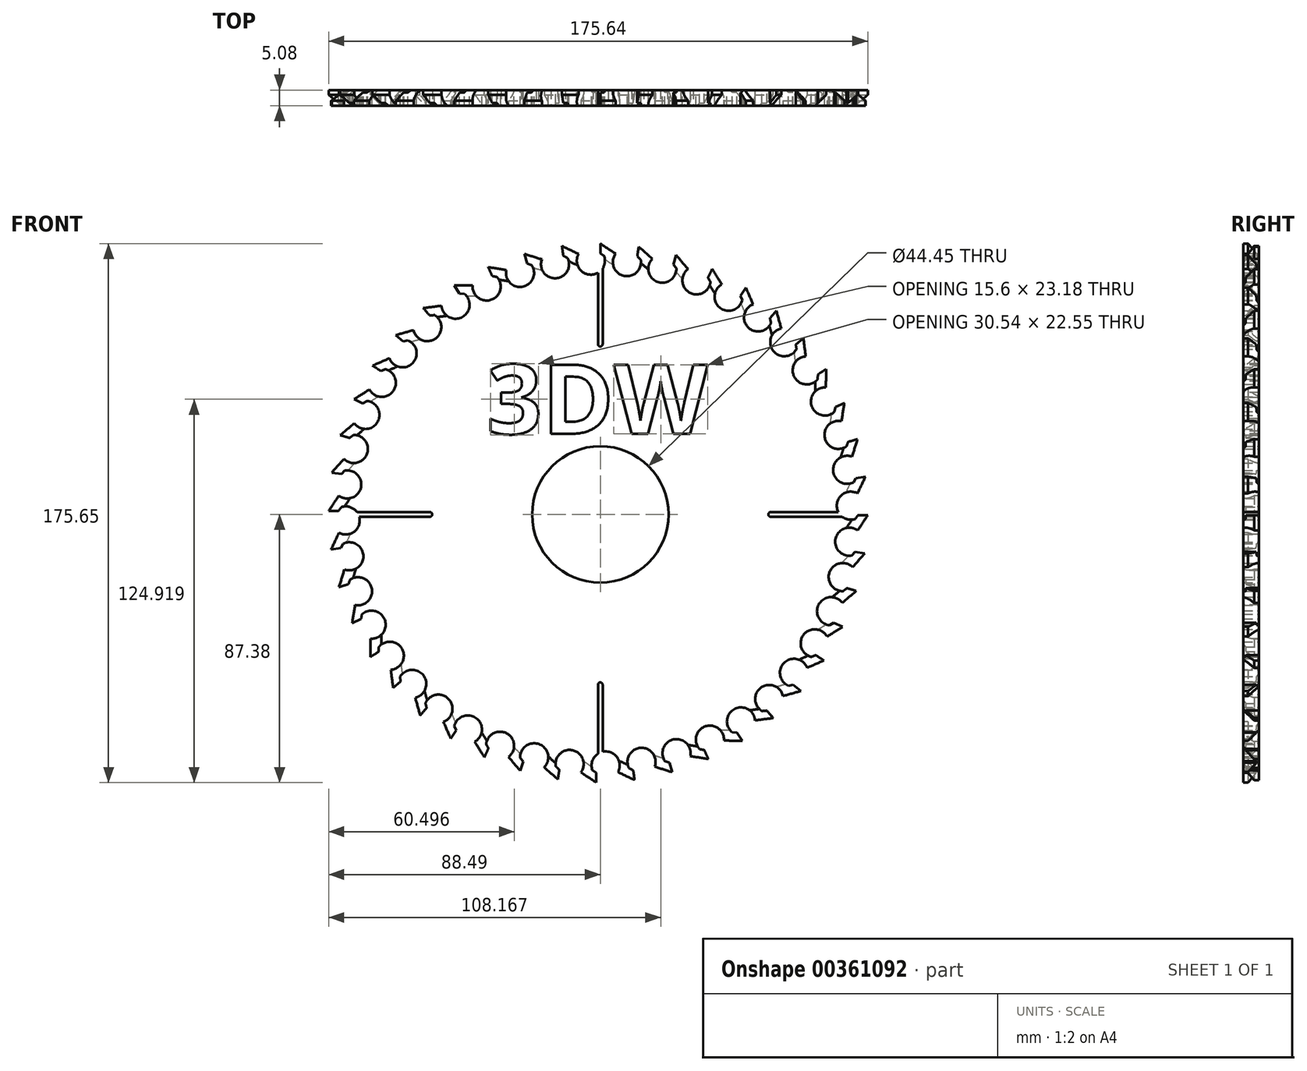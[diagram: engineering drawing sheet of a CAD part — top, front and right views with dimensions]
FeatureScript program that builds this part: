
annotation { "Feature Type Name" : "Feature", "Feature Type Description" : "" }
export const myFeature = defineFeature(function(context is Context, id is Id, definition is map)
    precondition{}
    {
        {
            var Q0;
            Q0=qCreatedBy(makeId("Front.planeOp"),FACE);
            var sketch = newSketch(context, id + "F0", { "sketchPlane" : qUnion([Q0])});
            skCircle(sketch, "E0", {"center": v(0, 0) * mm, "radius": 22.23 * mm});
            skLineSegment(sketch, "E1", {"start": v(0, 88.27) * mm, "end": v(0, 85.07) * mm});
            skLineSegment(sketch, "E2", {"start": v(0, 85.07) * mm, "end": v(1.27, 84.16) * mm});
            skLineSegment(sketch, "E3", {"start": v(1.27, 84.16) * mm, "end": v(1.27, 87.63) * mm});
            skLineSegment(sketch, "E4", {"start": v(1.27, 87.63) * mm, "end": v(0, 88.27) * mm});
            skLineSegment(sketch, "E5", {"start": v(1.27, 87.63) * mm, "end": v(5.07, 85.07) * mm});
            skLineSegment(sketch, "E6.1.0", {"start": v(-10.66, 83.58) * mm, "end": v(-11.15, 87.02) * mm});
            skLineSegment(sketch, "E6.1.1", {"start": v(-11.15, 87.02) * mm, "end": v(-7.03, 85.02) * mm});
            skLineSegment(sketch, "E6.1.2", {"start": v(-12.5, 87.47) * mm, "end": v(-12.05, 84.3) * mm});
            skLineSegment(sketch, "E6.1.3", {"start": v(-11.15, 87.02) * mm, "end": v(-12.5, 87.47) * mm});
            skLineSegment(sketch, "E6.1.4", {"start": v(-12.05, 84.3) * mm, "end": v(-10.66, 83.58) * mm});
            skLineSegment(sketch, "E6.2.0", {"start": v(-22.39, 81.31) * mm, "end": v(-23.37, 84.64) * mm});
            skLineSegment(sketch, "E6.2.1", {"start": v(-23.37, 84.64) * mm, "end": v(-19, 83.25) * mm});
            skLineSegment(sketch, "E6.2.2", {"start": v(-24.77, 84.9) * mm, "end": v(-23.87, 81.83) * mm});
            skLineSegment(sketch, "E6.2.3", {"start": v(-23.37, 84.64) * mm, "end": v(-24.77, 84.9) * mm});
            skLineSegment(sketch, "E6.2.4", {"start": v(-23.87, 81.83) * mm, "end": v(-22.39, 81.31) * mm});
            skLineSegment(sketch, "E6.3.0", {"start": v(-33.68, 77.4) * mm, "end": v(-35.12, 80.56) * mm});
            skLineSegment(sketch, "E6.3.1", {"start": v(-35.12, 80.56) * mm, "end": v(-30.6, 79.8) * mm});
            skLineSegment(sketch, "E6.3.2", {"start": v(-36.54, 80.6) * mm, "end": v(-35.21, 77.7) * mm});
            skLineSegment(sketch, "E6.3.3", {"start": v(-35.12, 80.56) * mm, "end": v(-36.54, 80.6) * mm});
            skLineSegment(sketch, "E6.3.4", {"start": v(-35.21, 77.7) * mm, "end": v(-33.68, 77.4) * mm});
            skLineSegment(sketch, "E6.4.0", {"start": v(-44.3, 71.92) * mm, "end": v(-46.17, 74.84) * mm});
            skLineSegment(sketch, "E6.4.1", {"start": v(-46.17, 74.84) * mm, "end": v(-41.6, 74.73) * mm});
            skLineSegment(sketch, "E6.4.2", {"start": v(-47.59, 74.69) * mm, "end": v(-45.86, 72) * mm});
            skLineSegment(sketch, "E6.4.3", {"start": v(-46.17, 74.84) * mm, "end": v(-47.59, 74.69) * mm});
            skLineSegment(sketch, "E6.4.4", {"start": v(-45.86, 72) * mm, "end": v(-44.3, 71.92) * mm});
            skLineSegment(sketch, "E6.5.0", {"start": v(-54.02, 64.98) * mm, "end": v(-56.3, 67.6) * mm});
            skLineSegment(sketch, "E6.5.1", {"start": v(-56.3, 67.6) * mm, "end": v(-51.75, 68.15) * mm});
            skLineSegment(sketch, "E6.5.2", {"start": v(-57.67, 67.25) * mm, "end": v(-55.58, 64.84) * mm});
            skLineSegment(sketch, "E6.5.3", {"start": v(-56.3, 67.6) * mm, "end": v(-57.67, 67.25) * mm});
            skLineSegment(sketch, "E6.5.4", {"start": v(-55.58, 64.84) * mm, "end": v(-54.02, 64.98) * mm});
            skLineSegment(sketch, "E6.6.0", {"start": v(-62.66, 56.73) * mm, "end": v(-65.29, 59) * mm});
            skLineSegment(sketch, "E6.6.1", {"start": v(-65.29, 59) * mm, "end": v(-60.87, 60.2) * mm});
            skLineSegment(sketch, "E6.6.2", {"start": v(-66.6, 58.46) * mm, "end": v(-64.18, 56.37) * mm});
            skLineSegment(sketch, "E6.6.3", {"start": v(-65.29, 59) * mm, "end": v(-66.6, 58.46) * mm});
            skLineSegment(sketch, "E6.6.4", {"start": v(-64.18, 56.37) * mm, "end": v(-62.66, 56.73) * mm});
            skLineSegment(sketch, "E6.7.0", {"start": v(-70.04, 47.34) * mm, "end": v(-72.96, 49.21) * mm});
            skLineSegment(sketch, "E6.7.1", {"start": v(-72.96, 49.21) * mm, "end": v(-68.76, 51.02) * mm});
            skLineSegment(sketch, "E6.7.2", {"start": v(-74.19, 48.49) * mm, "end": v(-71.5, 46.76) * mm});
            skLineSegment(sketch, "E6.7.3", {"start": v(-72.96, 49.21) * mm, "end": v(-74.19, 48.49) * mm});
            skLineSegment(sketch, "E6.7.4", {"start": v(-71.5, 46.76) * mm, "end": v(-70.04, 47.34) * mm});
            skLineSegment(sketch, "E6.8.0", {"start": v(-76.01, 36.99) * mm, "end": v(-79.17, 38.43) * mm});
            skLineSegment(sketch, "E6.8.1", {"start": v(-79.17, 38.43) * mm, "end": v(-75.26, 40.82) * mm});
            skLineSegment(sketch, "E6.8.2", {"start": v(-80.28, 37.54) * mm, "end": v(-77.37, 36.2) * mm});
            skLineSegment(sketch, "E6.8.3", {"start": v(-79.17, 38.43) * mm, "end": v(-80.28, 37.54) * mm});
            skLineSegment(sketch, "E6.8.4", {"start": v(-77.37, 36.2) * mm, "end": v(-76.01, 36.99) * mm});
            skLineSegment(sketch, "E6.9.0", {"start": v(-80.45, 25.9) * mm, "end": v(-83.77, 26.87) * mm});
            skLineSegment(sketch, "E6.9.1", {"start": v(-83.77, 26.87) * mm, "end": v(-80.25, 29.79) * mm});
            skLineSegment(sketch, "E6.9.2", {"start": v(-84.75, 25.83) * mm, "end": v(-81.68, 24.93) * mm});
            skLineSegment(sketch, "E6.9.3", {"start": v(-83.77, 26.87) * mm, "end": v(-84.75, 25.83) * mm});
            skLineSegment(sketch, "E6.9.4", {"start": v(-81.68, 24.93) * mm, "end": v(-80.45, 25.9) * mm});
            skLineSegment(sketch, "E6.10.0", {"start": v(-83.26, 14.28) * mm, "end": v(-86.69, 14.77) * mm});
            skLineSegment(sketch, "E6.10.1", {"start": v(-86.69, 14.77) * mm, "end": v(-83.61, 18.17) * mm});
            skLineSegment(sketch, "E6.10.2", {"start": v(-87.5, 13.6) * mm, "end": v(-84.34, 13.15) * mm});
            skLineSegment(sketch, "E6.10.3", {"start": v(-86.69, 14.77) * mm, "end": v(-87.5, 13.6) * mm});
            skLineSegment(sketch, "E6.10.4", {"start": v(-84.34, 13.15) * mm, "end": v(-83.26, 14.28) * mm});
            skLineSegment(sketch, "E6.11.0", {"start": v(-84.38, 2.39) * mm, "end": v(-87.85, 2.39) * mm});
            skLineSegment(sketch, "E6.11.1", {"start": v(-87.85, 2.39) * mm, "end": v(-85.3, 6.18) * mm});
            skLineSegment(sketch, "E6.11.2", {"start": v(-88.5, 1.11) * mm, "end": v(-85.3, 1.11) * mm});
            skLineSegment(sketch, "E6.11.3", {"start": v(-87.85, 2.39) * mm, "end": v(-88.5, 1.11) * mm});
            skLineSegment(sketch, "E6.11.4", {"start": v(-85.3, 1.11) * mm, "end": v(-84.38, 2.39) * mm});
            skLineSegment(sketch, "E6.12.0", {"start": v(-83.8, -9.55) * mm, "end": v(-87.24, -10.04) * mm});
            skLineSegment(sketch, "E6.12.1", {"start": v(-87.24, -10.04) * mm, "end": v(-85.25, -5.92) * mm});
            skLineSegment(sketch, "E6.12.2", {"start": v(-87.7, -11.4) * mm, "end": v(-84.53, -10.94) * mm});
            skLineSegment(sketch, "E6.12.3", {"start": v(-87.24, -10.04) * mm, "end": v(-87.7, -11.4) * mm});
            skLineSegment(sketch, "E6.12.4", {"start": v(-84.53, -10.94) * mm, "end": v(-83.8, -9.55) * mm});
            skLineSegment(sketch, "E6.13.0", {"start": v(-81.54, -21.28) * mm, "end": v(-84.87, -22.25) * mm});
            skLineSegment(sketch, "E6.13.1", {"start": v(-84.87, -22.25) * mm, "end": v(-83.48, -17.9) * mm});
            skLineSegment(sketch, "E6.13.2", {"start": v(-85.12, -23.66) * mm, "end": v(-82.05, -22.75) * mm});
            skLineSegment(sketch, "E6.13.3", {"start": v(-84.87, -22.25) * mm, "end": v(-85.12, -23.66) * mm});
            skLineSegment(sketch, "E6.13.4", {"start": v(-82.05, -22.75) * mm, "end": v(-81.54, -21.28) * mm});
            skLineSegment(sketch, "E6.14.0", {"start": v(-77.63, -32.56) * mm, "end": v(-80.78, -34) * mm});
            skLineSegment(sketch, "E6.14.1", {"start": v(-80.78, -34) * mm, "end": v(-80.03, -29.5) * mm});
            skLineSegment(sketch, "E6.14.2", {"start": v(-80.83, -35.43) * mm, "end": v(-77.92, -34.1) * mm});
            skLineSegment(sketch, "E6.14.3", {"start": v(-80.78, -34) * mm, "end": v(-80.83, -35.43) * mm});
            skLineSegment(sketch, "E6.14.4", {"start": v(-77.92, -34.1) * mm, "end": v(-77.63, -32.56) * mm});
            skLineSegment(sketch, "E6.15.0", {"start": v(-72.15, -43.18) * mm, "end": v(-75.06, -45.06) * mm});
            skLineSegment(sketch, "E6.15.1", {"start": v(-75.06, -45.06) * mm, "end": v(-74.96, -40.48) * mm});
            skLineSegment(sketch, "E6.15.2", {"start": v(-74.91, -46.47) * mm, "end": v(-72.22, -44.74) * mm});
            skLineSegment(sketch, "E6.15.3", {"start": v(-75.06, -45.06) * mm, "end": v(-74.91, -46.47) * mm});
            skLineSegment(sketch, "E6.15.4", {"start": v(-72.22, -44.74) * mm, "end": v(-72.15, -43.18) * mm});
            skLineSegment(sketch, "E6.16.0", {"start": v(-65.21, -52.9) * mm, "end": v(-67.83, -55.18) * mm});
            skLineSegment(sketch, "E6.16.1", {"start": v(-67.83, -55.18) * mm, "end": v(-68.38, -50.64) * mm});
            skLineSegment(sketch, "E6.16.2", {"start": v(-67.48, -56.56) * mm, "end": v(-65.06, -54.47) * mm});
            skLineSegment(sketch, "E6.16.3", {"start": v(-67.83, -55.18) * mm, "end": v(-67.48, -56.56) * mm});
            skLineSegment(sketch, "E6.16.4", {"start": v(-65.06, -54.47) * mm, "end": v(-65.21, -52.9) * mm});
            skLineSegment(sketch, "E6.17.0", {"start": v(-56.96, -61.55) * mm, "end": v(-59.23, -64.17) * mm});
            skLineSegment(sketch, "E6.17.1", {"start": v(-59.23, -64.17) * mm, "end": v(-60.42, -59.75) * mm});
            skLineSegment(sketch, "E6.17.2", {"start": v(-58.69, -65.49) * mm, "end": v(-56.6, -63.07) * mm});
            skLineSegment(sketch, "E6.17.3", {"start": v(-59.23, -64.17) * mm, "end": v(-58.69, -65.49) * mm});
            skLineSegment(sketch, "E6.17.4", {"start": v(-56.6, -63.07) * mm, "end": v(-56.96, -61.55) * mm});
            skLineSegment(sketch, "E6.18.0", {"start": v(-47.56, -68.93) * mm, "end": v(-49.44, -71.85) * mm});
            skLineSegment(sketch, "E6.18.1", {"start": v(-49.44, -71.85) * mm, "end": v(-51.25, -67.64) * mm});
            skLineSegment(sketch, "E6.18.2", {"start": v(-48.71, -73.07) * mm, "end": v(-46.98, -70.38) * mm});
            skLineSegment(sketch, "E6.18.3", {"start": v(-49.44, -71.85) * mm, "end": v(-48.71, -73.07) * mm});
            skLineSegment(sketch, "E6.18.4", {"start": v(-46.98, -70.38) * mm, "end": v(-47.56, -68.93) * mm});
            skLineSegment(sketch, "E6.19.0", {"start": v(-37.21, -74.9) * mm, "end": v(-38.66, -78.05) * mm});
            skLineSegment(sketch, "E6.19.1", {"start": v(-38.66, -78.05) * mm, "end": v(-41.04, -74.15) * mm});
            skLineSegment(sketch, "E6.19.2", {"start": v(-37.76, -79.16) * mm, "end": v(-36.43, -76.25) * mm});
            skLineSegment(sketch, "E6.19.3", {"start": v(-38.66, -78.05) * mm, "end": v(-37.76, -79.16) * mm});
            skLineSegment(sketch, "E6.19.4", {"start": v(-36.43, -76.25) * mm, "end": v(-37.21, -74.9) * mm});
            skLineSegment(sketch, "E6.20.0", {"start": v(-26.12, -79.33) * mm, "end": v(-27.1, -82.66) * mm});
            skLineSegment(sketch, "E6.20.1", {"start": v(-27.1, -82.66) * mm, "end": v(-30.02, -79.14) * mm});
            skLineSegment(sketch, "E6.20.2", {"start": v(-26.05, -83.63) * mm, "end": v(-25.15, -80.56) * mm});
            skLineSegment(sketch, "E6.20.3", {"start": v(-27.1, -82.66) * mm, "end": v(-26.05, -83.63) * mm});
            skLineSegment(sketch, "E6.20.4", {"start": v(-25.15, -80.56) * mm, "end": v(-26.12, -79.33) * mm});
            skLineSegment(sketch, "E6.21.0", {"start": v(-14.5, -82.14) * mm, "end": v(-15, -85.58) * mm});
            skLineSegment(sketch, "E6.21.1", {"start": v(-15, -85.58) * mm, "end": v(-18.4, -82.5) * mm});
            skLineSegment(sketch, "E6.21.2", {"start": v(-13.83, -86.39) * mm, "end": v(-13.38, -83.22) * mm});
            skLineSegment(sketch, "E6.21.3", {"start": v(-15, -85.58) * mm, "end": v(-13.83, -86.39) * mm});
            skLineSegment(sketch, "E6.21.4", {"start": v(-13.38, -83.22) * mm, "end": v(-14.5, -82.14) * mm});
            skLineSegment(sketch, "E6.22.0", {"start": v(-2.61, -83.27) * mm, "end": v(-2.61, -86.74) * mm});
            skLineSegment(sketch, "E6.22.1", {"start": v(-2.61, -86.74) * mm, "end": v(-6.4, -84.18) * mm});
            skLineSegment(sketch, "E6.22.2", {"start": v(-1.34, -87.38) * mm, "end": v(-1.34, -84.18) * mm});
            skLineSegment(sketch, "E6.22.3", {"start": v(-2.61, -86.74) * mm, "end": v(-1.34, -87.38) * mm});
            skLineSegment(sketch, "E6.22.4", {"start": v(-1.34, -84.18) * mm, "end": v(-2.61, -83.27) * mm});
            skLineSegment(sketch, "E6.23.0", {"start": v(9.32, -82.7) * mm, "end": v(9.81, -86.13) * mm});
            skLineSegment(sketch, "E6.23.1", {"start": v(9.81, -86.13) * mm, "end": v(5.7, -84.13) * mm});
            skLineSegment(sketch, "E6.23.2", {"start": v(11.17, -86.58) * mm, "end": v(10.71, -83.41) * mm});
            skLineSegment(sketch, "E6.23.3", {"start": v(9.81, -86.13) * mm, "end": v(11.17, -86.58) * mm});
            skLineSegment(sketch, "E6.23.4", {"start": v(10.71, -83.41) * mm, "end": v(9.32, -82.7) * mm});
            skLineSegment(sketch, "E6.24.0", {"start": v(21.05, -80.43) * mm, "end": v(22.03, -83.76) * mm});
            skLineSegment(sketch, "E6.24.1", {"start": v(22.03, -83.76) * mm, "end": v(17.67, -82.37) * mm});
            skLineSegment(sketch, "E6.24.2", {"start": v(23.43, -84) * mm, "end": v(22.53, -80.94) * mm});
            skLineSegment(sketch, "E6.24.3", {"start": v(22.03, -83.76) * mm, "end": v(23.43, -84) * mm});
            skLineSegment(sketch, "E6.24.4", {"start": v(22.53, -80.94) * mm, "end": v(21.05, -80.43) * mm});
            skLineSegment(sketch, "E6.25.0", {"start": v(32.34, -76.51) * mm, "end": v(33.78, -79.67) * mm});
            skLineSegment(sketch, "E6.25.1", {"start": v(33.78, -79.67) * mm, "end": v(29.26, -78.92) * mm});
            skLineSegment(sketch, "E6.25.2", {"start": v(35.2, -79.72) * mm, "end": v(33.87, -76.81) * mm});
            skLineSegment(sketch, "E6.25.3", {"start": v(33.78, -79.67) * mm, "end": v(35.2, -79.72) * mm});
            skLineSegment(sketch, "E6.25.4", {"start": v(33.87, -76.81) * mm, "end": v(32.34, -76.51) * mm});
            skLineSegment(sketch, "E6.26.0", {"start": v(42.95, -71.03) * mm, "end": v(44.83, -73.95) * mm});
            skLineSegment(sketch, "E6.26.1", {"start": v(44.83, -73.95) * mm, "end": v(40.25, -73.85) * mm});
            skLineSegment(sketch, "E6.26.2", {"start": v(46.25, -73.8) * mm, "end": v(44.52, -71.1) * mm});
            skLineSegment(sketch, "E6.26.3", {"start": v(44.83, -73.95) * mm, "end": v(46.25, -73.8) * mm});
            skLineSegment(sketch, "E6.26.4", {"start": v(44.52, -71.1) * mm, "end": v(42.95, -71.03) * mm});
            skLineSegment(sketch, "E6.27.0", {"start": v(52.68, -64.1) * mm, "end": v(54.95, -66.72) * mm});
            skLineSegment(sketch, "E6.27.1", {"start": v(54.95, -66.72) * mm, "end": v(50.41, -67.27) * mm});
            skLineSegment(sketch, "E6.27.2", {"start": v(56.33, -66.37) * mm, "end": v(54.24, -63.95) * mm});
            skLineSegment(sketch, "E6.27.3", {"start": v(54.95, -66.72) * mm, "end": v(56.33, -66.37) * mm});
            skLineSegment(sketch, "E6.27.4", {"start": v(54.24, -63.95) * mm, "end": v(52.68, -64.1) * mm});
            skLineSegment(sketch, "E6.28.0", {"start": v(61.32, -55.85) * mm, "end": v(63.95, -58.12) * mm});
            skLineSegment(sketch, "E6.28.1", {"start": v(63.95, -58.12) * mm, "end": v(59.53, -59.3) * mm});
            skLineSegment(sketch, "E6.28.2", {"start": v(65.26, -57.57) * mm, "end": v(62.85, -55.48) * mm});
            skLineSegment(sketch, "E6.28.3", {"start": v(63.95, -58.12) * mm, "end": v(65.26, -57.57) * mm});
            skLineSegment(sketch, "E6.28.4", {"start": v(62.85, -55.48) * mm, "end": v(61.32, -55.85) * mm});
            skLineSegment(sketch, "E6.29.0", {"start": v(68.7, -46.45) * mm, "end": v(71.62, -48.33) * mm});
            skLineSegment(sketch, "E6.29.1", {"start": v(71.62, -48.33) * mm, "end": v(67.42, -50.13) * mm});
            skLineSegment(sketch, "E6.29.2", {"start": v(72.85, -47.6) * mm, "end": v(70.16, -45.87) * mm});
            skLineSegment(sketch, "E6.29.3", {"start": v(71.62, -48.33) * mm, "end": v(72.85, -47.6) * mm});
            skLineSegment(sketch, "E6.29.4", {"start": v(70.16, -45.87) * mm, "end": v(68.7, -46.45) * mm});
            skLineSegment(sketch, "E6.30.0", {"start": v(74.67, -36.1) * mm, "end": v(77.83, -37.54) * mm});
            skLineSegment(sketch, "E6.30.1", {"start": v(77.83, -37.54) * mm, "end": v(73.92, -39.93) * mm});
            skLineSegment(sketch, "E6.30.2", {"start": v(78.94, -36.65) * mm, "end": v(76.03, -35.32) * mm});
            skLineSegment(sketch, "E6.30.3", {"start": v(77.83, -37.54) * mm, "end": v(78.94, -36.65) * mm});
            skLineSegment(sketch, "E6.30.4", {"start": v(76.03, -35.32) * mm, "end": v(74.67, -36.1) * mm});
            skLineSegment(sketch, "E6.31.0", {"start": v(79.1, -25) * mm, "end": v(82.43, -25.98) * mm});
            skLineSegment(sketch, "E6.31.1", {"start": v(82.43, -25.98) * mm, "end": v(78.9, -28.9) * mm});
            skLineSegment(sketch, "E6.31.2", {"start": v(83.4, -24.94) * mm, "end": v(80.34, -24.04) * mm});
            skLineSegment(sketch, "E6.31.3", {"start": v(82.43, -25.98) * mm, "end": v(83.4, -24.94) * mm});
            skLineSegment(sketch, "E6.31.4", {"start": v(80.34, -24.04) * mm, "end": v(79.1, -25) * mm});
            skLineSegment(sketch, "E6.32.0", {"start": v(81.92, -13.4) * mm, "end": v(85.35, -13.89) * mm});
            skLineSegment(sketch, "E6.32.1", {"start": v(85.35, -13.89) * mm, "end": v(82.28, -17.28) * mm});
            skLineSegment(sketch, "E6.32.2", {"start": v(86.16, -12.72) * mm, "end": v(83, -12.26) * mm});
            skLineSegment(sketch, "E6.32.3", {"start": v(85.35, -13.89) * mm, "end": v(86.16, -12.72) * mm});
            skLineSegment(sketch, "E6.32.4", {"start": v(83, -12.26) * mm, "end": v(81.92, -13.4) * mm});
            skLineSegment(sketch, "E6.33.0", {"start": v(83.04, -1.5) * mm, "end": v(86.51, -1.5) * mm});
            skLineSegment(sketch, "E6.33.1", {"start": v(86.51, -1.5) * mm, "end": v(83.95, -5.3) * mm});
            skLineSegment(sketch, "E6.33.2", {"start": v(87.15, -0.23) * mm, "end": v(83.95, -0.23) * mm});
            skLineSegment(sketch, "E6.33.3", {"start": v(86.51, -1.5) * mm, "end": v(87.15, -0.23) * mm});
            skLineSegment(sketch, "E6.33.4", {"start": v(83.95, -0.23) * mm, "end": v(83.04, -1.5) * mm});
            skLineSegment(sketch, "E6.34.0", {"start": v(82.47, 10.43) * mm, "end": v(85.9, 10.93) * mm});
            skLineSegment(sketch, "E6.34.1", {"start": v(85.9, 10.93) * mm, "end": v(83.9, 6.8) * mm});
            skLineSegment(sketch, "E6.34.2", {"start": v(86.35, 12.28) * mm, "end": v(83.19, 11.82) * mm});
            skLineSegment(sketch, "E6.34.3", {"start": v(85.9, 10.93) * mm, "end": v(86.35, 12.28) * mm});
            skLineSegment(sketch, "E6.34.4", {"start": v(83.19, 11.82) * mm, "end": v(82.47, 10.43) * mm});
            skLineSegment(sketch, "E6.35.0", {"start": v(80.2, 22.16) * mm, "end": v(83.53, 23.14) * mm});
            skLineSegment(sketch, "E6.35.1", {"start": v(83.53, 23.14) * mm, "end": v(82.14, 18.78) * mm});
            skLineSegment(sketch, "E6.35.2", {"start": v(83.78, 24.54) * mm, "end": v(80.71, 23.64) * mm});
            skLineSegment(sketch, "E6.35.3", {"start": v(83.53, 23.14) * mm, "end": v(83.78, 24.54) * mm});
            skLineSegment(sketch, "E6.35.4", {"start": v(80.71, 23.64) * mm, "end": v(80.2, 22.16) * mm});
            skLineSegment(sketch, "E6.36.0", {"start": v(76.29, 33.45) * mm, "end": v(79.44, 34.9) * mm});
            skLineSegment(sketch, "E6.36.1", {"start": v(79.44, 34.9) * mm, "end": v(78.69, 30.38) * mm});
            skLineSegment(sketch, "E6.36.2", {"start": v(79.5, 36.32) * mm, "end": v(76.58, 34.99) * mm});
            skLineSegment(sketch, "E6.36.3", {"start": v(79.44, 34.9) * mm, "end": v(79.5, 36.32) * mm});
            skLineSegment(sketch, "E6.36.4", {"start": v(76.58, 34.99) * mm, "end": v(76.29, 33.45) * mm});
            skLineSegment(sketch, "E6.37.0", {"start": v(70.8, 44.07) * mm, "end": v(73.72, 45.94) * mm});
            skLineSegment(sketch, "E6.37.1", {"start": v(73.72, 45.94) * mm, "end": v(73.62, 41.37) * mm});
            skLineSegment(sketch, "E6.37.2", {"start": v(73.57, 47.36) * mm, "end": v(70.88, 45.63) * mm});
            skLineSegment(sketch, "E6.37.3", {"start": v(73.72, 45.94) * mm, "end": v(73.57, 47.36) * mm});
            skLineSegment(sketch, "E6.37.4", {"start": v(70.88, 45.63) * mm, "end": v(70.8, 44.07) * mm});
            skLineSegment(sketch, "E6.38.0", {"start": v(63.87, 53.8) * mm, "end": v(66.5, 56.07) * mm});
            skLineSegment(sketch, "E6.38.1", {"start": v(66.5, 56.07) * mm, "end": v(67.04, 51.52) * mm});
            skLineSegment(sketch, "E6.38.2", {"start": v(66.14, 57.45) * mm, "end": v(63.72, 55.35) * mm});
            skLineSegment(sketch, "E6.38.3", {"start": v(66.5, 56.07) * mm, "end": v(66.14, 57.45) * mm});
            skLineSegment(sketch, "E6.38.4", {"start": v(63.72, 55.35) * mm, "end": v(63.87, 53.8) * mm});
            skLineSegment(sketch, "E6.39.0", {"start": v(55.62, 62.44) * mm, "end": v(57.9, 65.06) * mm});
            skLineSegment(sketch, "E6.39.1", {"start": v(57.9, 65.06) * mm, "end": v(59.08, 60.64) * mm});
            skLineSegment(sketch, "E6.39.2", {"start": v(57.35, 66.38) * mm, "end": v(55.25, 63.96) * mm});
            skLineSegment(sketch, "E6.39.3", {"start": v(57.9, 65.06) * mm, "end": v(57.35, 66.38) * mm});
            skLineSegment(sketch, "E6.39.4", {"start": v(55.25, 63.96) * mm, "end": v(55.62, 62.44) * mm});
            skLineSegment(sketch, "E6.40.0", {"start": v(46.22, 69.82) * mm, "end": v(48.1, 72.74) * mm});
            skLineSegment(sketch, "E6.40.1", {"start": v(48.1, 72.74) * mm, "end": v(49.9, 68.53) * mm});
            skLineSegment(sketch, "E6.40.2", {"start": v(47.37, 73.96) * mm, "end": v(45.64, 71.27) * mm});
            skLineSegment(sketch, "E6.40.3", {"start": v(48.1, 72.74) * mm, "end": v(47.37, 73.96) * mm});
            skLineSegment(sketch, "E6.40.4", {"start": v(45.64, 71.27) * mm, "end": v(46.22, 69.82) * mm});
            skLineSegment(sketch, "E6.41.0", {"start": v(35.87, 75.79) * mm, "end": v(37.32, 78.94) * mm});
            skLineSegment(sketch, "E6.41.1", {"start": v(37.32, 78.94) * mm, "end": v(39.7, 75.04) * mm});
            skLineSegment(sketch, "E6.41.2", {"start": v(36.42, 80.05) * mm, "end": v(35.1, 77.14) * mm});
            skLineSegment(sketch, "E6.41.3", {"start": v(37.32, 78.94) * mm, "end": v(36.42, 80.05) * mm});
            skLineSegment(sketch, "E6.41.4", {"start": v(35.1, 77.14) * mm, "end": v(35.87, 75.79) * mm});
            skLineSegment(sketch, "E6.42.0", {"start": v(24.78, 80.22) * mm, "end": v(25.76, 83.55) * mm});
            skLineSegment(sketch, "E6.42.1", {"start": v(25.76, 83.55) * mm, "end": v(28.68, 80.02) * mm});
            skLineSegment(sketch, "E6.42.2", {"start": v(24.72, 84.52) * mm, "end": v(23.81, 81.45) * mm});
            skLineSegment(sketch, "E6.42.3", {"start": v(25.76, 83.55) * mm, "end": v(24.72, 84.52) * mm});
            skLineSegment(sketch, "E6.42.4", {"start": v(23.81, 81.45) * mm, "end": v(24.78, 80.22) * mm});
            skLineSegment(sketch, "E6.43.0", {"start": v(13.17, 83.03) * mm, "end": v(13.66, 86.46) * mm});
            skLineSegment(sketch, "E6.43.1", {"start": v(13.66, 86.46) * mm, "end": v(17.05, 83.39) * mm});
            skLineSegment(sketch, "E6.43.2", {"start": v(12.5, 87.28) * mm, "end": v(12.04, 84.1) * mm});
            skLineSegment(sketch, "E6.43.3", {"start": v(13.66, 86.46) * mm, "end": v(12.5, 87.28) * mm});
            skLineSegment(sketch, "E6.43.4", {"start": v(12.04, 84.1) * mm, "end": v(13.17, 83.03) * mm});
            skPoint(sketch, "E6.center", {"position": v(-0.67, 0.44) * mm});
            skArc(sketch, "E7", {"start": v(5.07, 85.07) * mm, "mid": v(7.54, 77.79) * mm, "end": v(13.17, 83.03) * mm});
            skArc(sketch, "E8.1.0", {"start": v(-7.03, 85.02) * mm, "mid": v(-3.55, 78.17) * mm, "end": v(1.27, 84.16) * mm});
            skArc(sketch, "E8.2.0", {"start": v(-19, 83.25) * mm, "mid": v(-14.58, 76.97) * mm, "end": v(-10.66, 83.58) * mm});
            skArc(sketch, "E8.3.0", {"start": v(-30.6, 79.8) * mm, "mid": v(-25.33, 74.21) * mm, "end": v(-22.39, 81.31) * mm});
            skArc(sketch, "E8.4.0", {"start": v(-41.6, 74.73) * mm, "mid": v(-35.58, 69.95) * mm, "end": v(-33.68, 77.4) * mm});
            skArc(sketch, "E8.5.0", {"start": v(-51.75, 68.15) * mm, "mid": v(-45.11, 64.28) * mm, "end": v(-44.3, 71.92) * mm});
            skArc(sketch, "E8.6.0", {"start": v(-60.87, 60.2) * mm, "mid": v(-53.74, 57.3) * mm, "end": v(-54.02, 64.98) * mm});
            skArc(sketch, "E8.7.0", {"start": v(-68.76, 51.02) * mm, "mid": v(-61.3, 49.17) * mm, "end": v(-62.66, 56.73) * mm});
            skArc(sketch, "E8.8.0", {"start": v(-75.26, 40.82) * mm, "mid": v(-67.61, 40.04) * mm, "end": v(-70.04, 47.34) * mm});
            skArc(sketch, "E8.9.0", {"start": v(-80.25, 29.79) * mm, "mid": v(-72.57, 30.11) * mm, "end": v(-76.01, 36.99) * mm});
            skArc(sketch, "E8.10.0", {"start": v(-83.61, 18.17) * mm, "mid": v(-76.06, 19.58) * mm, "end": v(-80.45, 25.9) * mm});
            skArc(sketch, "E8.11.0", {"start": v(-85.3, 6.18) * mm, "mid": v(-78.02, 8.66) * mm, "end": v(-83.26, 14.28) * mm});
            skArc(sketch, "E8.12.0", {"start": v(-85.25, -5.92) * mm, "mid": v(-78.4, -2.43) * mm, "end": v(-84.38, 2.39) * mm});
            skArc(sketch, "E8.13.0", {"start": v(-83.48, -17.9) * mm, "mid": v(-77.2, -13.47) * mm, "end": v(-83.8, -9.55) * mm});
            skArc(sketch, "E8.14.0", {"start": v(-80.03, -29.5) * mm, "mid": v(-74.44, -24.22) * mm, "end": v(-81.54, -21.28) * mm});
            skArc(sketch, "E8.15.0", {"start": v(-74.96, -40.48) * mm, "mid": v(-70.18, -34.46) * mm, "end": v(-77.63, -32.56) * mm});
            skArc(sketch, "E8.16.0", {"start": v(-68.38, -50.64) * mm, "mid": v(-64.5, -44) * mm, "end": v(-72.15, -43.18) * mm});
            skArc(sketch, "E8.17.0", {"start": v(-60.42, -59.75) * mm, "mid": v(-57.53, -52.63) * mm, "end": v(-65.21, -52.9) * mm});
            skArc(sketch, "E8.18.0", {"start": v(-51.25, -67.64) * mm, "mid": v(-49.4, -60.18) * mm, "end": v(-56.96, -61.55) * mm});
            skArc(sketch, "E8.19.0", {"start": v(-41.04, -74.15) * mm, "mid": v(-40.27, -66.5) * mm, "end": v(-47.56, -68.93) * mm});
            skArc(sketch, "E8.20.0", {"start": v(-30.02, -79.14) * mm, "mid": v(-30.34, -71.45) * mm, "end": v(-37.21, -74.9) * mm});
            skArc(sketch, "E8.21.0", {"start": v(-18.4, -82.5) * mm, "mid": v(-19.8, -74.95) * mm, "end": v(-26.12, -79.33) * mm});
            skArc(sketch, "E8.22.0", {"start": v(-6.4, -84.18) * mm, "mid": v(-8.88, -76.9) * mm, "end": v(-14.5, -82.14) * mm});
            skArc(sketch, "E8.23.0", {"start": v(5.7, -84.13) * mm, "mid": v(2.2, -77.28) * mm, "end": v(-2.61, -83.27) * mm});
            skArc(sketch, "E8.24.0", {"start": v(17.67, -82.37) * mm, "mid": v(13.24, -76.08) * mm, "end": v(9.32, -82.7) * mm});
            skArc(sketch, "E8.25.0", {"start": v(29.26, -78.92) * mm, "mid": v(23.99, -73.32) * mm, "end": v(21.05, -80.43) * mm});
            skArc(sketch, "E8.26.0", {"start": v(40.25, -73.85) * mm, "mid": v(34.24, -69.06) * mm, "end": v(32.34, -76.51) * mm});
            skArc(sketch, "E8.27.0", {"start": v(50.41, -67.27) * mm, "mid": v(43.77, -63.39) * mm, "end": v(42.95, -71.03) * mm});
            skArc(sketch, "E8.28.0", {"start": v(59.53, -59.3) * mm, "mid": v(52.4, -56.41) * mm, "end": v(52.68, -64.1) * mm});
            skArc(sketch, "E8.29.0", {"start": v(67.42, -50.13) * mm, "mid": v(59.96, -48.28) * mm, "end": v(61.32, -55.85) * mm});
            skArc(sketch, "E8.30.0", {"start": v(73.92, -39.93) * mm, "mid": v(66.27, -39.16) * mm, "end": v(68.7, -46.45) * mm});
            skArc(sketch, "E8.31.0", {"start": v(78.9, -28.9) * mm, "mid": v(71.23, -29.23) * mm, "end": v(74.67, -36.1) * mm});
            skArc(sketch, "E8.32.0", {"start": v(82.28, -17.28) * mm, "mid": v(74.72, -18.7) * mm, "end": v(79.1, -25) * mm});
            skArc(sketch, "E8.33.0", {"start": v(83.95, -5.3) * mm, "mid": v(76.68, -7.77) * mm, "end": v(81.92, -13.4) * mm});
            skArc(sketch, "E8.34.0", {"start": v(83.9, 6.8) * mm, "mid": v(77.06, 3.32) * mm, "end": v(83.04, -1.5) * mm});
            skArc(sketch, "E8.35.0", {"start": v(82.14, 18.78) * mm, "mid": v(75.86, 14.35) * mm, "end": v(82.47, 10.43) * mm});
            skArc(sketch, "E8.36.0", {"start": v(78.69, 30.38) * mm, "mid": v(73.1, 25.1) * mm, "end": v(80.2, 22.16) * mm});
            skArc(sketch, "E8.37.0", {"start": v(73.62, 41.37) * mm, "mid": v(68.84, 35.35) * mm, "end": v(76.29, 33.45) * mm});
            skArc(sketch, "E8.38.0", {"start": v(67.04, 51.52) * mm, "mid": v(63.16, 44.89) * mm, "end": v(70.8, 44.07) * mm});
            skArc(sketch, "E8.39.0", {"start": v(59.08, 60.64) * mm, "mid": v(56.19, 53.52) * mm, "end": v(63.87, 53.8) * mm});
            skArc(sketch, "E8.40.0", {"start": v(49.9, 68.53) * mm, "mid": v(48.06, 61.07) * mm, "end": v(55.62, 62.44) * mm});
            skArc(sketch, "E8.41.0", {"start": v(39.7, 75.04) * mm, "mid": v(38.93, 67.39) * mm, "end": v(46.22, 69.82) * mm});
            skArc(sketch, "E8.42.0", {"start": v(28.68, 80.02) * mm, "mid": v(29, 72.34) * mm, "end": v(35.87, 75.79) * mm});
            skArc(sketch, "E8.43.0", {"start": v(17.05, 83.39) * mm, "mid": v(18.47, 75.83) * mm, "end": v(24.78, 80.22) * mm});
            skSolve(sketch);
        }
        {
            var Q0;
            Q0 = qSketchRegion(id + "F0", true);
            extrude(context, id + "F1", {"entities" : qUnion([Q0]), "depth" : 5.08 * mm});
        }
        {
            var Q0;
            Q0=makeQuery(id+"F1.opExtrude","SWEPT_EDGE",EDGE,{"disambiguationData":[OSD([sQuery(id+"F0.wireOp",EDGE,"E6.1.0"),sQuery(id+"F0.wireOp",EDGE,"E6.1.1"),sQuery(id+"F0.wireOp",EDGE,"E6.1.3")])]});
            var Q1;
            Q1=makeQuery(id+"F1.opExtrude","SWEPT_EDGE",EDGE,{"disambiguationData":[OSD([sQuery(id+"F0.wireOp",EDGE,"E3"),sQuery(id+"F0.wireOp",EDGE,"E4"),sQuery(id+"F0.wireOp",EDGE,"E5")])]});
            var Q2;
            Q2=makeQuery(id+"F1.opExtrude","SWEPT_EDGE",EDGE,{"disambiguationData":[OSD([sQuery(id+"F0.wireOp",EDGE,"E6.43.0"),sQuery(id+"F0.wireOp",EDGE,"E6.43.1"),sQuery(id+"F0.wireOp",EDGE,"E6.43.3")])]});
            var Q3;
            Q3=makeQuery(id+"F1.opExtrude","SWEPT_EDGE",EDGE,{"disambiguationData":[OSD([sQuery(id+"F0.wireOp",EDGE,"E6.42.0"),sQuery(id+"F0.wireOp",EDGE,"E6.42.1"),sQuery(id+"F0.wireOp",EDGE,"E6.42.3")])]});
            var Q4;
            Q4=makeQuery(id+"F1.opExtrude","SWEPT_EDGE",EDGE,{"disambiguationData":[OSD([sQuery(id+"F0.wireOp",EDGE,"E6.41.0"),sQuery(id+"F0.wireOp",EDGE,"E6.41.1"),sQuery(id+"F0.wireOp",EDGE,"E6.41.3")])]});
            var Q5;
            Q5=makeQuery(id+"F1.opExtrude","SWEPT_EDGE",EDGE,{"disambiguationData":[OSD([sQuery(id+"F0.wireOp",EDGE,"E6.40.0"),sQuery(id+"F0.wireOp",EDGE,"E6.40.1"),sQuery(id+"F0.wireOp",EDGE,"E6.40.3")])]});
            var Q6;
            Q6=makeQuery(id+"F1.opExtrude","SWEPT_EDGE",EDGE,{"disambiguationData":[OSD([sQuery(id+"F0.wireOp",EDGE,"E6.39.0"),sQuery(id+"F0.wireOp",EDGE,"E6.39.1"),sQuery(id+"F0.wireOp",EDGE,"E6.39.3")])]});
            var Q7;
            Q7=makeQuery(id+"F1.opExtrude","SWEPT_EDGE",EDGE,{"disambiguationData":[OSD([sQuery(id+"F0.wireOp",EDGE,"E6.38.0"),sQuery(id+"F0.wireOp",EDGE,"E6.38.1"),sQuery(id+"F0.wireOp",EDGE,"E6.38.3")])]});
            var Q8;
            Q8=makeQuery(id+"F1.opExtrude","SWEPT_EDGE",EDGE,{"disambiguationData":[OSD([sQuery(id+"F0.wireOp",EDGE,"E6.37.0"),sQuery(id+"F0.wireOp",EDGE,"E6.37.1"),sQuery(id+"F0.wireOp",EDGE,"E6.37.3")])]});
            var Q9;
            Q9=makeQuery(id+"F1.opExtrude","SWEPT_EDGE",EDGE,{"disambiguationData":[OSD([sQuery(id+"F0.wireOp",EDGE,"E6.36.0"),sQuery(id+"F0.wireOp",EDGE,"E6.36.1"),sQuery(id+"F0.wireOp",EDGE,"E6.36.3")])]});
            var Q10;
            Q10=makeQuery(id+"F1.opExtrude","SWEPT_EDGE",EDGE,{"disambiguationData":[OSD([sQuery(id+"F0.wireOp",EDGE,"E6.35.0"),sQuery(id+"F0.wireOp",EDGE,"E6.35.1"),sQuery(id+"F0.wireOp",EDGE,"E6.35.3")])]});
            var Q11;
            Q11=makeQuery(id+"F1.opExtrude","SWEPT_EDGE",EDGE,{"disambiguationData":[OSD([sQuery(id+"F0.wireOp",EDGE,"E6.34.0"),sQuery(id+"F0.wireOp",EDGE,"E6.34.1"),sQuery(id+"F0.wireOp",EDGE,"E6.34.3")])]});
            var Q12;
            Q12=makeQuery(id+"F1.opExtrude","SWEPT_EDGE",EDGE,{"disambiguationData":[OSD([sQuery(id+"F0.wireOp",EDGE,"E6.33.0"),sQuery(id+"F0.wireOp",EDGE,"E6.33.1"),sQuery(id+"F0.wireOp",EDGE,"E6.33.3")])]});
            var Q13;
            Q13=makeQuery(id+"F1.opExtrude","SWEPT_EDGE",EDGE,{"disambiguationData":[OSD([sQuery(id+"F0.wireOp",EDGE,"E6.32.0"),sQuery(id+"F0.wireOp",EDGE,"E6.32.1"),sQuery(id+"F0.wireOp",EDGE,"E6.32.3")])]});
            var Q14;
            Q14=makeQuery(id+"F1.opExtrude","SWEPT_EDGE",EDGE,{"disambiguationData":[OSD([sQuery(id+"F0.wireOp",EDGE,"E6.31.0"),sQuery(id+"F0.wireOp",EDGE,"E6.31.1"),sQuery(id+"F0.wireOp",EDGE,"E6.31.3")])]});
            var Q15;
            Q15=makeQuery(id+"F1.opExtrude","SWEPT_EDGE",EDGE,{"disambiguationData":[OSD([sQuery(id+"F0.wireOp",EDGE,"E6.30.0"),sQuery(id+"F0.wireOp",EDGE,"E6.30.1"),sQuery(id+"F0.wireOp",EDGE,"E6.30.3")])]});
            var Q16;
            Q16=makeQuery(id+"F1.opExtrude","SWEPT_EDGE",EDGE,{"disambiguationData":[OSD([sQuery(id+"F0.wireOp",EDGE,"E6.29.0"),sQuery(id+"F0.wireOp",EDGE,"E6.29.1"),sQuery(id+"F0.wireOp",EDGE,"E6.29.3")])]});
            var Q17;
            Q17=makeQuery(id+"F1.opExtrude","SWEPT_EDGE",EDGE,{"disambiguationData":[OSD([sQuery(id+"F0.wireOp",EDGE,"E6.28.0"),sQuery(id+"F0.wireOp",EDGE,"E6.28.1"),sQuery(id+"F0.wireOp",EDGE,"E6.28.3")])]});
            var Q18;
            Q18=makeQuery(id+"F1.opExtrude","SWEPT_EDGE",EDGE,{"disambiguationData":[OSD([sQuery(id+"F0.wireOp",EDGE,"E6.27.0"),sQuery(id+"F0.wireOp",EDGE,"E6.27.1"),sQuery(id+"F0.wireOp",EDGE,"E6.27.3")])]});
            var Q19;
            Q19=makeQuery(id+"F1.opExtrude","SWEPT_EDGE",EDGE,{"disambiguationData":[OSD([sQuery(id+"F0.wireOp",EDGE,"E6.26.0"),sQuery(id+"F0.wireOp",EDGE,"E6.26.1"),sQuery(id+"F0.wireOp",EDGE,"E6.26.3")])]});
            var Q20;
            Q20=makeQuery(id+"F1.opExtrude","SWEPT_EDGE",EDGE,{"disambiguationData":[OSD([sQuery(id+"F0.wireOp",EDGE,"E6.25.0"),sQuery(id+"F0.wireOp",EDGE,"E6.25.1"),sQuery(id+"F0.wireOp",EDGE,"E6.25.3")])]});
            var Q21;
            Q21=makeQuery(id+"F1.opExtrude","SWEPT_EDGE",EDGE,{"disambiguationData":[OSD([sQuery(id+"F0.wireOp",EDGE,"E6.24.0"),sQuery(id+"F0.wireOp",EDGE,"E6.24.1"),sQuery(id+"F0.wireOp",EDGE,"E6.24.3")])]});
            var Q22;
            Q22=makeQuery(id+"F1.opExtrude","SWEPT_EDGE",EDGE,{"disambiguationData":[OSD([sQuery(id+"F0.wireOp",EDGE,"E6.23.0"),sQuery(id+"F0.wireOp",EDGE,"E6.23.1"),sQuery(id+"F0.wireOp",EDGE,"E6.23.3")])]});
            var Q23;
            Q23=makeQuery(id+"F1.opExtrude","SWEPT_EDGE",EDGE,{"disambiguationData":[OSD([sQuery(id+"F0.wireOp",EDGE,"E6.22.0"),sQuery(id+"F0.wireOp",EDGE,"E6.22.1"),sQuery(id+"F0.wireOp",EDGE,"E6.22.3")])]});
            var Q24;
            Q24=makeQuery(id+"F1.opExtrude","SWEPT_EDGE",EDGE,{"disambiguationData":[OSD([sQuery(id+"F0.wireOp",EDGE,"E6.21.0"),sQuery(id+"F0.wireOp",EDGE,"E6.21.1"),sQuery(id+"F0.wireOp",EDGE,"E6.21.3")])]});
            var Q25;
            Q25=makeQuery(id+"F1.opExtrude","SWEPT_EDGE",EDGE,{"disambiguationData":[OSD([sQuery(id+"F0.wireOp",EDGE,"E6.20.0"),sQuery(id+"F0.wireOp",EDGE,"E6.20.1"),sQuery(id+"F0.wireOp",EDGE,"E6.20.3")])]});
            var Q26;
            Q26=makeQuery(id+"F1.opExtrude","SWEPT_EDGE",EDGE,{"disambiguationData":[OSD([sQuery(id+"F0.wireOp",EDGE,"E6.19.0"),sQuery(id+"F0.wireOp",EDGE,"E6.19.1"),sQuery(id+"F0.wireOp",EDGE,"E6.19.3")])]});
            var Q27;
            Q27=makeQuery(id+"F1.opExtrude","SWEPT_EDGE",EDGE,{"disambiguationData":[OSD([sQuery(id+"F0.wireOp",EDGE,"E6.18.0"),sQuery(id+"F0.wireOp",EDGE,"E6.18.1"),sQuery(id+"F0.wireOp",EDGE,"E6.18.3")])]});
            var Q28;
            Q28=makeQuery(id+"F1.opExtrude","SWEPT_EDGE",EDGE,{"disambiguationData":[OSD([sQuery(id+"F0.wireOp",EDGE,"E6.17.0"),sQuery(id+"F0.wireOp",EDGE,"E6.17.1"),sQuery(id+"F0.wireOp",EDGE,"E6.17.3")])]});
            var Q29;
            Q29=makeQuery(id+"F1.opExtrude","SWEPT_EDGE",EDGE,{"disambiguationData":[OSD([sQuery(id+"F0.wireOp",EDGE,"E6.16.0"),sQuery(id+"F0.wireOp",EDGE,"E6.16.1"),sQuery(id+"F0.wireOp",EDGE,"E6.16.3")])]});
            var Q30;
            Q30=makeQuery(id+"F1.opExtrude","SWEPT_EDGE",EDGE,{"disambiguationData":[OSD([sQuery(id+"F0.wireOp",EDGE,"E6.15.0"),sQuery(id+"F0.wireOp",EDGE,"E6.15.1"),sQuery(id+"F0.wireOp",EDGE,"E6.15.3")])]});
            var Q31;
            Q31=makeQuery(id+"F1.opExtrude","SWEPT_EDGE",EDGE,{"disambiguationData":[OSD([sQuery(id+"F0.wireOp",EDGE,"E6.14.0"),sQuery(id+"F0.wireOp",EDGE,"E6.14.1"),sQuery(id+"F0.wireOp",EDGE,"E6.14.3")])]});
            var Q32;
            Q32=makeQuery(id+"F1.opExtrude","SWEPT_EDGE",EDGE,{"disambiguationData":[OSD([sQuery(id+"F0.wireOp",EDGE,"E6.13.0"),sQuery(id+"F0.wireOp",EDGE,"E6.13.1"),sQuery(id+"F0.wireOp",EDGE,"E6.13.3")])]});
            var Q33;
            Q33=makeQuery(id+"F1.opExtrude","SWEPT_EDGE",EDGE,{"disambiguationData":[OSD([sQuery(id+"F0.wireOp",EDGE,"E6.12.0"),sQuery(id+"F0.wireOp",EDGE,"E6.12.1"),sQuery(id+"F0.wireOp",EDGE,"E6.12.3")])]});
            var Q34;
            Q34=makeQuery(id+"F1.opExtrude","SWEPT_EDGE",EDGE,{"disambiguationData":[OSD([sQuery(id+"F0.wireOp",EDGE,"E6.11.0"),sQuery(id+"F0.wireOp",EDGE,"E6.11.1"),sQuery(id+"F0.wireOp",EDGE,"E6.11.3")])]});
            var Q35;
            Q35=makeQuery(id+"F1.opExtrude","SWEPT_EDGE",EDGE,{"disambiguationData":[OSD([sQuery(id+"F0.wireOp",EDGE,"E6.10.0"),sQuery(id+"F0.wireOp",EDGE,"E6.10.1"),sQuery(id+"F0.wireOp",EDGE,"E6.10.3")])]});
            var Q36;
            Q36=makeQuery(id+"F1.opExtrude","SWEPT_EDGE",EDGE,{"disambiguationData":[OSD([sQuery(id+"F0.wireOp",EDGE,"E6.9.0"),sQuery(id+"F0.wireOp",EDGE,"E6.9.1"),sQuery(id+"F0.wireOp",EDGE,"E6.9.3")])]});
            var Q37;
            Q37=makeQuery(id+"F1.opExtrude","SWEPT_EDGE",EDGE,{"disambiguationData":[OSD([sQuery(id+"F0.wireOp",EDGE,"E6.8.0"),sQuery(id+"F0.wireOp",EDGE,"E6.8.1"),sQuery(id+"F0.wireOp",EDGE,"E6.8.3")])]});
            var Q38;
            Q38=makeQuery(id+"F1.opExtrude","SWEPT_EDGE",EDGE,{"disambiguationData":[OSD([sQuery(id+"F0.wireOp",EDGE,"E6.7.0"),sQuery(id+"F0.wireOp",EDGE,"E6.7.1"),sQuery(id+"F0.wireOp",EDGE,"E6.7.3")])]});
            var Q39;
            Q39=makeQuery(id+"F1.opExtrude","SWEPT_EDGE",EDGE,{"disambiguationData":[OSD([sQuery(id+"F0.wireOp",EDGE,"E6.6.0"),sQuery(id+"F0.wireOp",EDGE,"E6.6.1"),sQuery(id+"F0.wireOp",EDGE,"E6.6.3")])]});
            var Q40;
            Q40=makeQuery(id+"F1.opExtrude","SWEPT_EDGE",EDGE,{"disambiguationData":[OSD([sQuery(id+"F0.wireOp",EDGE,"E6.5.0"),sQuery(id+"F0.wireOp",EDGE,"E6.5.1"),sQuery(id+"F0.wireOp",EDGE,"E6.5.3")])]});
            var Q41;
            Q41=makeQuery(id+"F1.opExtrude","SWEPT_EDGE",EDGE,{"disambiguationData":[OSD([sQuery(id+"F0.wireOp",EDGE,"E6.4.0"),sQuery(id+"F0.wireOp",EDGE,"E6.4.1"),sQuery(id+"F0.wireOp",EDGE,"E6.4.3")])]});
            var Q42;
            Q42=makeQuery(id+"F1.opExtrude","SWEPT_EDGE",EDGE,{"disambiguationData":[OSD([sQuery(id+"F0.wireOp",EDGE,"E6.3.0"),sQuery(id+"F0.wireOp",EDGE,"E6.3.1"),sQuery(id+"F0.wireOp",EDGE,"E6.3.3")])]});
            var Q43;
            Q43=makeQuery(id+"F1.opExtrude","SWEPT_EDGE",EDGE,{"disambiguationData":[OSD([sQuery(id+"F0.wireOp",EDGE,"E6.2.0"),sQuery(id+"F0.wireOp",EDGE,"E6.2.1"),sQuery(id+"F0.wireOp",EDGE,"E6.2.3")])]});
            fillet(context, id + "F2", {"entities" : qUnion([Q0, Q1, Q2, Q3, Q4, Q5, Q6, Q7, Q8, Q9, Q10, Q11, Q12, Q13, Q14, Q15, Q16, Q17, Q18, Q19, Q20, Q21, Q22, Q23, Q24, Q25, Q26, Q27, Q28, Q29, Q30, Q31, Q32, Q33, Q34, Q35, Q36, Q37, Q38, Q39, Q40, Q41, Q42, Q43]), "radius" : 4067.85 * mm, "tangentPropagation" : true, "allowEdgeOverflow" : false});
        }
        {
            var Q0;
            {var subQ0=sQuery(id+"F0.wireOp",EDGE,"E6.23.3");var subQ1=sQuery(id+"F0.wireOp",EDGE,"E6.23.1");Q0=makeQuery(id+"F2.opFillet","BLEND_EDGE",EDGE,{"blendedFrom":[makeQuery(id+"F1.opExtrude","SWEPT_EDGE",EDGE,{"disambiguationData":[OSD([sQuery(id+"F0.wireOp",EDGE,"E6.23.0"),subQ1,subQ0])]}),makeQuery(id+"F1.opExtrude","CAP_FACE",FACE,{"disambiguationData":[OSD([sQuery(id+"F0.wireOp",EDGE,"E0"),sQuery(id+"F0.wireOp",EDGE,"E1"),sQuery(id+"F0.wireOp",EDGE,"E2"),sQuery(id+"F0.wireOp",EDGE,"E4"),sQuery(id+"F0.wireOp",EDGE,"E5"),sQuery(id+"F0.wireOp",EDGE,"E6.1.1"),sQuery(id+"F0.wireOp",EDGE,"E6.1.2"),sQuery(id+"F0.wireOp",EDGE,"E6.1.3"),sQuery(id+"F0.wireOp",EDGE,"E6.1.4"),sQuery(id+"F0.wireOp",EDGE,"E6.2.1"),sQuery(id+"F0.wireOp",EDGE,"E6.2.2"),sQuery(id+"F0.wireOp",EDGE,"E6.2.3"),sQuery(id+"F0.wireOp",EDGE,"E6.2.4"),sQuery(id+"F0.wireOp",EDGE,"E6.3.1"),sQuery(id+"F0.wireOp",EDGE,"E6.3.2"),sQuery(id+"F0.wireOp",EDGE,"E6.3.3"),sQuery(id+"F0.wireOp",EDGE,"E6.3.4"),sQuery(id+"F0.wireOp",EDGE,"E6.4.1"),sQuery(id+"F0.wireOp",EDGE,"E6.4.2"),sQuery(id+"F0.wireOp",EDGE,"E6.4.3"),sQuery(id+"F0.wireOp",EDGE,"E6.4.4"),sQuery(id+"F0.wireOp",EDGE,"E6.5.1"),sQuery(id+"F0.wireOp",EDGE,"E6.5.2"),sQuery(id+"F0.wireOp",EDGE,"E6.5.3"),sQuery(id+"F0.wireOp",EDGE,"E6.5.4"),sQuery(id+"F0.wireOp",EDGE,"E6.6.1"),sQuery(id+"F0.wireOp",EDGE,"E6.6.2"),sQuery(id+"F0.wireOp",EDGE,"E6.6.3"),sQuery(id+"F0.wireOp",EDGE,"E6.6.4"),sQuery(id+"F0.wireOp",EDGE,"E6.7.1"),sQuery(id+"F0.wireOp",EDGE,"E6.7.2"),sQuery(id+"F0.wireOp",EDGE,"E6.7.3"),sQuery(id+"F0.wireOp",EDGE,"E6.7.4"),sQuery(id+"F0.wireOp",EDGE,"E6.8.1"),sQuery(id+"F0.wireOp",EDGE,"E6.8.2"),sQuery(id+"F0.wireOp",EDGE,"E6.8.3"),sQuery(id+"F0.wireOp",EDGE,"E6.8.4"),sQuery(id+"F0.wireOp",EDGE,"E6.9.1"),sQuery(id+"F0.wireOp",EDGE,"E6.9.2"),sQuery(id+"F0.wireOp",EDGE,"E6.9.3"),sQuery(id+"F0.wireOp",EDGE,"E6.9.4"),sQuery(id+"F0.wireOp",EDGE,"E6.10.1"),sQuery(id+"F0.wireOp",EDGE,"E6.10.2"),sQuery(id+"F0.wireOp",EDGE,"E6.10.3"),sQuery(id+"F0.wireOp",EDGE,"E6.10.4"),sQuery(id+"F0.wireOp",EDGE,"E6.11.1"),sQuery(id+"F0.wireOp",EDGE,"E6.11.2"),sQuery(id+"F0.wireOp",EDGE,"E6.11.3"),sQuery(id+"F0.wireOp",EDGE,"E6.11.4"),sQuery(id+"F0.wireOp",EDGE,"E6.12.1"),sQuery(id+"F0.wireOp",EDGE,"E6.12.2"),sQuery(id+"F0.wireOp",EDGE,"E6.12.3"),sQuery(id+"F0.wireOp",EDGE,"E6.12.4"),sQuery(id+"F0.wireOp",EDGE,"E6.13.1"),sQuery(id+"F0.wireOp",EDGE,"E6.13.2"),sQuery(id+"F0.wireOp",EDGE,"E6.13.3"),sQuery(id+"F0.wireOp",EDGE,"E6.13.4"),sQuery(id+"F0.wireOp",EDGE,"E6.14.1"),sQuery(id+"F0.wireOp",EDGE,"E6.14.2"),sQuery(id+"F0.wireOp",EDGE,"E6.14.3"),sQuery(id+"F0.wireOp",EDGE,"E6.14.4"),sQuery(id+"F0.wireOp",EDGE,"E6.15.1"),sQuery(id+"F0.wireOp",EDGE,"E6.15.2"),sQuery(id+"F0.wireOp",EDGE,"E6.15.3"),sQuery(id+"F0.wireOp",EDGE,"E6.15.4"),sQuery(id+"F0.wireOp",EDGE,"E6.16.1"),sQuery(id+"F0.wireOp",EDGE,"E6.16.2"),sQuery(id+"F0.wireOp",EDGE,"E6.16.3"),sQuery(id+"F0.wireOp",EDGE,"E6.16.4"),sQuery(id+"F0.wireOp",EDGE,"E6.17.1"),sQuery(id+"F0.wireOp",EDGE,"E6.17.2"),sQuery(id+"F0.wireOp",EDGE,"E6.17.3"),sQuery(id+"F0.wireOp",EDGE,"E6.17.4"),sQuery(id+"F0.wireOp",EDGE,"E6.18.1"),sQuery(id+"F0.wireOp",EDGE,"E6.18.2"),sQuery(id+"F0.wireOp",EDGE,"E6.18.3"),sQuery(id+"F0.wireOp",EDGE,"E6.18.4"),sQuery(id+"F0.wireOp",EDGE,"E6.19.1"),sQuery(id+"F0.wireOp",EDGE,"E6.19.2"),sQuery(id+"F0.wireOp",EDGE,"E6.19.3"),sQuery(id+"F0.wireOp",EDGE,"E6.19.4"),sQuery(id+"F0.wireOp",EDGE,"E6.20.1"),sQuery(id+"F0.wireOp",EDGE,"E6.20.2"),sQuery(id+"F0.wireOp",EDGE,"E6.20.3"),sQuery(id+"F0.wireOp",EDGE,"E6.20.4"),sQuery(id+"F0.wireOp",EDGE,"E6.21.1"),sQuery(id+"F0.wireOp",EDGE,"E6.21.2"),sQuery(id+"F0.wireOp",EDGE,"E6.21.3"),sQuery(id+"F0.wireOp",EDGE,"E6.21.4"),sQuery(id+"F0.wireOp",EDGE,"E6.22.1"),sQuery(id+"F0.wireOp",EDGE,"E6.22.2"),sQuery(id+"F0.wireOp",EDGE,"E6.22.3"),sQuery(id+"F0.wireOp",EDGE,"E6.22.4"),subQ1,sQuery(id+"F0.wireOp",EDGE,"E6.23.2"),subQ0,sQuery(id+"F0.wireOp",EDGE,"E6.23.4"),sQuery(id+"F0.wireOp",EDGE,"E6.24.1"),sQuery(id+"F0.wireOp",EDGE,"E6.24.2"),sQuery(id+"F0.wireOp",EDGE,"E6.24.3"),sQuery(id+"F0.wireOp",EDGE,"E6.24.4"),sQuery(id+"F0.wireOp",EDGE,"E6.25.1"),sQuery(id+"F0.wireOp",EDGE,"E6.25.2"),sQuery(id+"F0.wireOp",EDGE,"E6.25.3"),sQuery(id+"F0.wireOp",EDGE,"E6.25.4"),sQuery(id+"F0.wireOp",EDGE,"E6.26.1"),sQuery(id+"F0.wireOp",EDGE,"E6.26.2"),sQuery(id+"F0.wireOp",EDGE,"E6.26.3"),sQuery(id+"F0.wireOp",EDGE,"E6.26.4"),sQuery(id+"F0.wireOp",EDGE,"E6.27.1"),sQuery(id+"F0.wireOp",EDGE,"E6.27.2"),sQuery(id+"F0.wireOp",EDGE,"E6.27.3"),sQuery(id+"F0.wireOp",EDGE,"E6.27.4"),sQuery(id+"F0.wireOp",EDGE,"E6.28.1"),sQuery(id+"F0.wireOp",EDGE,"E6.28.2"),sQuery(id+"F0.wireOp",EDGE,"E6.28.3"),sQuery(id+"F0.wireOp",EDGE,"E6.28.4"),sQuery(id+"F0.wireOp",EDGE,"E6.29.1"),sQuery(id+"F0.wireOp",EDGE,"E6.29.2"),sQuery(id+"F0.wireOp",EDGE,"E6.29.3"),sQuery(id+"F0.wireOp",EDGE,"E6.29.4"),sQuery(id+"F0.wireOp",EDGE,"E6.30.1"),sQuery(id+"F0.wireOp",EDGE,"E6.30.2"),sQuery(id+"F0.wireOp",EDGE,"E6.30.3"),sQuery(id+"F0.wireOp",EDGE,"E6.30.4"),sQuery(id+"F0.wireOp",EDGE,"E6.31.1"),sQuery(id+"F0.wireOp",EDGE,"E6.31.2"),sQuery(id+"F0.wireOp",EDGE,"E6.31.3"),sQuery(id+"F0.wireOp",EDGE,"E6.31.4"),sQuery(id+"F0.wireOp",EDGE,"E6.32.1"),sQuery(id+"F0.wireOp",EDGE,"E6.32.2"),sQuery(id+"F0.wireOp",EDGE,"E6.32.3"),sQuery(id+"F0.wireOp",EDGE,"E6.32.4"),sQuery(id+"F0.wireOp",EDGE,"E6.33.1"),sQuery(id+"F0.wireOp",EDGE,"E6.33.2"),sQuery(id+"F0.wireOp",EDGE,"E6.33.3"),sQuery(id+"F0.wireOp",EDGE,"E6.33.4"),sQuery(id+"F0.wireOp",EDGE,"E6.34.1"),sQuery(id+"F0.wireOp",EDGE,"E6.34.2"),sQuery(id+"F0.wireOp",EDGE,"E6.34.3"),sQuery(id+"F0.wireOp",EDGE,"E6.34.4"),sQuery(id+"F0.wireOp",EDGE,"E6.35.1"),sQuery(id+"F0.wireOp",EDGE,"E6.35.2"),sQuery(id+"F0.wireOp",EDGE,"E6.35.3"),sQuery(id+"F0.wireOp",EDGE,"E6.35.4"),sQuery(id+"F0.wireOp",EDGE,"E6.36.1"),sQuery(id+"F0.wireOp",EDGE,"E6.36.2"),sQuery(id+"F0.wireOp",EDGE,"E6.36.3"),sQuery(id+"F0.wireOp",EDGE,"E6.36.4"),sQuery(id+"F0.wireOp",EDGE,"E6.37.1"),sQuery(id+"F0.wireOp",EDGE,"E6.37.2"),sQuery(id+"F0.wireOp",EDGE,"E6.37.3"),sQuery(id+"F0.wireOp",EDGE,"E6.37.4"),sQuery(id+"F0.wireOp",EDGE,"E6.38.1"),sQuery(id+"F0.wireOp",EDGE,"E6.38.2"),sQuery(id+"F0.wireOp",EDGE,"E6.38.3"),sQuery(id+"F0.wireOp",EDGE,"E6.38.4"),sQuery(id+"F0.wireOp",EDGE,"E6.39.1"),sQuery(id+"F0.wireOp",EDGE,"E6.39.2"),sQuery(id+"F0.wireOp",EDGE,"E6.39.3"),sQuery(id+"F0.wireOp",EDGE,"E6.39.4"),sQuery(id+"F0.wireOp",EDGE,"E6.40.1"),sQuery(id+"F0.wireOp",EDGE,"E6.40.2"),sQuery(id+"F0.wireOp",EDGE,"E6.40.3"),sQuery(id+"F0.wireOp",EDGE,"E6.40.4"),sQuery(id+"F0.wireOp",EDGE,"E6.41.1"),sQuery(id+"F0.wireOp",EDGE,"E6.41.2"),sQuery(id+"F0.wireOp",EDGE,"E6.41.3"),sQuery(id+"F0.wireOp",EDGE,"E6.41.4"),sQuery(id+"F0.wireOp",EDGE,"E6.42.1"),sQuery(id+"F0.wireOp",EDGE,"E6.42.2"),sQuery(id+"F0.wireOp",EDGE,"E6.42.3"),sQuery(id+"F0.wireOp",EDGE,"E6.42.4"),sQuery(id+"F0.wireOp",EDGE,"E6.43.1"),sQuery(id+"F0.wireOp",EDGE,"E6.43.2"),sQuery(id+"F0.wireOp",EDGE,"E6.43.3"),sQuery(id+"F0.wireOp",EDGE,"E6.43.4"),sQuery(id+"F0.wireOp",EDGE,"E7"),sQuery(id+"F0.wireOp",EDGE,"E8.1.0"),sQuery(id+"F0.wireOp",EDGE,"E8.2.0"),sQuery(id+"F0.wireOp",EDGE,"E8.3.0"),sQuery(id+"F0.wireOp",EDGE,"E8.4.0"),sQuery(id+"F0.wireOp",EDGE,"E8.5.0"),sQuery(id+"F0.wireOp",EDGE,"E8.6.0"),sQuery(id+"F0.wireOp",EDGE,"E8.7.0"),sQuery(id+"F0.wireOp",EDGE,"E8.8.0"),sQuery(id+"F0.wireOp",EDGE,"E8.9.0"),sQuery(id+"F0.wireOp",EDGE,"E8.10.0"),sQuery(id+"F0.wireOp",EDGE,"E8.11.0"),sQuery(id+"F0.wireOp",EDGE,"E8.12.0"),sQuery(id+"F0.wireOp",EDGE,"E8.13.0"),sQuery(id+"F0.wireOp",EDGE,"E8.14.0"),sQuery(id+"F0.wireOp",EDGE,"E8.15.0"),sQuery(id+"F0.wireOp",EDGE,"E8.16.0"),sQuery(id+"F0.wireOp",EDGE,"E8.17.0"),sQuery(id+"F0.wireOp",EDGE,"E8.18.0"),sQuery(id+"F0.wireOp",EDGE,"E8.19.0"),sQuery(id+"F0.wireOp",EDGE,"E8.20.0"),sQuery(id+"F0.wireOp",EDGE,"E8.21.0"),sQuery(id+"F0.wireOp",EDGE,"E8.22.0"),sQuery(id+"F0.wireOp",EDGE,"E8.23.0"),sQuery(id+"F0.wireOp",EDGE,"E8.24.0"),sQuery(id+"F0.wireOp",EDGE,"E8.25.0"),sQuery(id+"F0.wireOp",EDGE,"E8.26.0"),sQuery(id+"F0.wireOp",EDGE,"E8.27.0"),sQuery(id+"F0.wireOp",EDGE,"E8.28.0"),sQuery(id+"F0.wireOp",EDGE,"E8.29.0"),sQuery(id+"F0.wireOp",EDGE,"E8.30.0"),sQuery(id+"F0.wireOp",EDGE,"E8.31.0"),sQuery(id+"F0.wireOp",EDGE,"E8.32.0"),sQuery(id+"F0.wireOp",EDGE,"E8.33.0"),sQuery(id+"F0.wireOp",EDGE,"E8.34.0"),sQuery(id+"F0.wireOp",EDGE,"E8.35.0"),sQuery(id+"F0.wireOp",EDGE,"E8.36.0"),sQuery(id+"F0.wireOp",EDGE,"E8.37.0"),sQuery(id+"F0.wireOp",EDGE,"E8.38.0"),sQuery(id+"F0.wireOp",EDGE,"E8.39.0"),sQuery(id+"F0.wireOp",EDGE,"E8.40.0"),sQuery(id+"F0.wireOp",EDGE,"E8.41.0"),sQuery(id+"F0.wireOp",EDGE,"E8.42.0"),sQuery(id+"F0.wireOp",EDGE,"E8.43.0")])],"isStart":false})],"blendedInto":[makeQuery(id+"F1.opExtrude","CAP_FACE",FACE,{"disambiguationData":[OSD([sQuery(id+"F0.wireOp",EDGE,"E0"),sQuery(id+"F0.wireOp",EDGE,"E1"),sQuery(id+"F0.wireOp",EDGE,"E2"),sQuery(id+"F0.wireOp",EDGE,"E4"),sQuery(id+"F0.wireOp",EDGE,"E5"),sQuery(id+"F0.wireOp",EDGE,"E6.1.1"),sQuery(id+"F0.wireOp",EDGE,"E6.1.2"),sQuery(id+"F0.wireOp",EDGE,"E6.1.3"),sQuery(id+"F0.wireOp",EDGE,"E6.1.4"),sQuery(id+"F0.wireOp",EDGE,"E6.2.1"),sQuery(id+"F0.wireOp",EDGE,"E6.2.2"),sQuery(id+"F0.wireOp",EDGE,"E6.2.3"),sQuery(id+"F0.wireOp",EDGE,"E6.2.4"),sQuery(id+"F0.wireOp",EDGE,"E6.3.1"),sQuery(id+"F0.wireOp",EDGE,"E6.3.2"),sQuery(id+"F0.wireOp",EDGE,"E6.3.3"),sQuery(id+"F0.wireOp",EDGE,"E6.3.4"),sQuery(id+"F0.wireOp",EDGE,"E6.4.1"),sQuery(id+"F0.wireOp",EDGE,"E6.4.2"),sQuery(id+"F0.wireOp",EDGE,"E6.4.3"),sQuery(id+"F0.wireOp",EDGE,"E6.4.4"),sQuery(id+"F0.wireOp",EDGE,"E6.5.1"),sQuery(id+"F0.wireOp",EDGE,"E6.5.2"),sQuery(id+"F0.wireOp",EDGE,"E6.5.3"),sQuery(id+"F0.wireOp",EDGE,"E6.5.4"),sQuery(id+"F0.wireOp",EDGE,"E6.6.1"),sQuery(id+"F0.wireOp",EDGE,"E6.6.2"),sQuery(id+"F0.wireOp",EDGE,"E6.6.3"),sQuery(id+"F0.wireOp",EDGE,"E6.6.4"),sQuery(id+"F0.wireOp",EDGE,"E6.7.1"),sQuery(id+"F0.wireOp",EDGE,"E6.7.2"),sQuery(id+"F0.wireOp",EDGE,"E6.7.3"),sQuery(id+"F0.wireOp",EDGE,"E6.7.4"),sQuery(id+"F0.wireOp",EDGE,"E6.8.1"),sQuery(id+"F0.wireOp",EDGE,"E6.8.2"),sQuery(id+"F0.wireOp",EDGE,"E6.8.3"),sQuery(id+"F0.wireOp",EDGE,"E6.8.4"),sQuery(id+"F0.wireOp",EDGE,"E6.9.1"),sQuery(id+"F0.wireOp",EDGE,"E6.9.2"),sQuery(id+"F0.wireOp",EDGE,"E6.9.3"),sQuery(id+"F0.wireOp",EDGE,"E6.9.4"),sQuery(id+"F0.wireOp",EDGE,"E6.10.1"),sQuery(id+"F0.wireOp",EDGE,"E6.10.2"),sQuery(id+"F0.wireOp",EDGE,"E6.10.3"),sQuery(id+"F0.wireOp",EDGE,"E6.10.4"),sQuery(id+"F0.wireOp",EDGE,"E6.11.1"),sQuery(id+"F0.wireOp",EDGE,"E6.11.2"),sQuery(id+"F0.wireOp",EDGE,"E6.11.3"),sQuery(id+"F0.wireOp",EDGE,"E6.11.4"),sQuery(id+"F0.wireOp",EDGE,"E6.12.1"),sQuery(id+"F0.wireOp",EDGE,"E6.12.2"),sQuery(id+"F0.wireOp",EDGE,"E6.12.3"),sQuery(id+"F0.wireOp",EDGE,"E6.12.4"),sQuery(id+"F0.wireOp",EDGE,"E6.13.1"),sQuery(id+"F0.wireOp",EDGE,"E6.13.2"),sQuery(id+"F0.wireOp",EDGE,"E6.13.3"),sQuery(id+"F0.wireOp",EDGE,"E6.13.4"),sQuery(id+"F0.wireOp",EDGE,"E6.14.1"),sQuery(id+"F0.wireOp",EDGE,"E6.14.2"),sQuery(id+"F0.wireOp",EDGE,"E6.14.3"),sQuery(id+"F0.wireOp",EDGE,"E6.14.4"),sQuery(id+"F0.wireOp",EDGE,"E6.15.1"),sQuery(id+"F0.wireOp",EDGE,"E6.15.2"),sQuery(id+"F0.wireOp",EDGE,"E6.15.3"),sQuery(id+"F0.wireOp",EDGE,"E6.15.4"),sQuery(id+"F0.wireOp",EDGE,"E6.16.1"),sQuery(id+"F0.wireOp",EDGE,"E6.16.2"),sQuery(id+"F0.wireOp",EDGE,"E6.16.3"),sQuery(id+"F0.wireOp",EDGE,"E6.16.4"),sQuery(id+"F0.wireOp",EDGE,"E6.17.1"),sQuery(id+"F0.wireOp",EDGE,"E6.17.2"),sQuery(id+"F0.wireOp",EDGE,"E6.17.3"),sQuery(id+"F0.wireOp",EDGE,"E6.17.4"),sQuery(id+"F0.wireOp",EDGE,"E6.18.1"),sQuery(id+"F0.wireOp",EDGE,"E6.18.2"),sQuery(id+"F0.wireOp",EDGE,"E6.18.3"),sQuery(id+"F0.wireOp",EDGE,"E6.18.4"),sQuery(id+"F0.wireOp",EDGE,"E6.19.1"),sQuery(id+"F0.wireOp",EDGE,"E6.19.2"),sQuery(id+"F0.wireOp",EDGE,"E6.19.3"),sQuery(id+"F0.wireOp",EDGE,"E6.19.4"),sQuery(id+"F0.wireOp",EDGE,"E6.20.1"),sQuery(id+"F0.wireOp",EDGE,"E6.20.2"),sQuery(id+"F0.wireOp",EDGE,"E6.20.3"),sQuery(id+"F0.wireOp",EDGE,"E6.20.4"),sQuery(id+"F0.wireOp",EDGE,"E6.21.1"),sQuery(id+"F0.wireOp",EDGE,"E6.21.2"),sQuery(id+"F0.wireOp",EDGE,"E6.21.3"),sQuery(id+"F0.wireOp",EDGE,"E6.21.4"),sQuery(id+"F0.wireOp",EDGE,"E6.22.1"),sQuery(id+"F0.wireOp",EDGE,"E6.22.2"),sQuery(id+"F0.wireOp",EDGE,"E6.22.3"),sQuery(id+"F0.wireOp",EDGE,"E6.22.4"),subQ1,sQuery(id+"F0.wireOp",EDGE,"E6.23.2"),subQ0,sQuery(id+"F0.wireOp",EDGE,"E6.23.4"),sQuery(id+"F0.wireOp",EDGE,"E6.24.1"),sQuery(id+"F0.wireOp",EDGE,"E6.24.2"),sQuery(id+"F0.wireOp",EDGE,"E6.24.3"),sQuery(id+"F0.wireOp",EDGE,"E6.24.4"),sQuery(id+"F0.wireOp",EDGE,"E6.25.1"),sQuery(id+"F0.wireOp",EDGE,"E6.25.2"),sQuery(id+"F0.wireOp",EDGE,"E6.25.3"),sQuery(id+"F0.wireOp",EDGE,"E6.25.4"),sQuery(id+"F0.wireOp",EDGE,"E6.26.1"),sQuery(id+"F0.wireOp",EDGE,"E6.26.2"),sQuery(id+"F0.wireOp",EDGE,"E6.26.3"),sQuery(id+"F0.wireOp",EDGE,"E6.26.4"),sQuery(id+"F0.wireOp",EDGE,"E6.27.1"),sQuery(id+"F0.wireOp",EDGE,"E6.27.2"),sQuery(id+"F0.wireOp",EDGE,"E6.27.3"),sQuery(id+"F0.wireOp",EDGE,"E6.27.4"),sQuery(id+"F0.wireOp",EDGE,"E6.28.1"),sQuery(id+"F0.wireOp",EDGE,"E6.28.2"),sQuery(id+"F0.wireOp",EDGE,"E6.28.3"),sQuery(id+"F0.wireOp",EDGE,"E6.28.4"),sQuery(id+"F0.wireOp",EDGE,"E6.29.1"),sQuery(id+"F0.wireOp",EDGE,"E6.29.2"),sQuery(id+"F0.wireOp",EDGE,"E6.29.3"),sQuery(id+"F0.wireOp",EDGE,"E6.29.4"),sQuery(id+"F0.wireOp",EDGE,"E6.30.1"),sQuery(id+"F0.wireOp",EDGE,"E6.30.2"),sQuery(id+"F0.wireOp",EDGE,"E6.30.3"),sQuery(id+"F0.wireOp",EDGE,"E6.30.4"),sQuery(id+"F0.wireOp",EDGE,"E6.31.1"),sQuery(id+"F0.wireOp",EDGE,"E6.31.2"),sQuery(id+"F0.wireOp",EDGE,"E6.31.3"),sQuery(id+"F0.wireOp",EDGE,"E6.31.4"),sQuery(id+"F0.wireOp",EDGE,"E6.32.1"),sQuery(id+"F0.wireOp",EDGE,"E6.32.2"),sQuery(id+"F0.wireOp",EDGE,"E6.32.3"),sQuery(id+"F0.wireOp",EDGE,"E6.32.4"),sQuery(id+"F0.wireOp",EDGE,"E6.33.1"),sQuery(id+"F0.wireOp",EDGE,"E6.33.2"),sQuery(id+"F0.wireOp",EDGE,"E6.33.3"),sQuery(id+"F0.wireOp",EDGE,"E6.33.4"),sQuery(id+"F0.wireOp",EDGE,"E6.34.1"),sQuery(id+"F0.wireOp",EDGE,"E6.34.2"),sQuery(id+"F0.wireOp",EDGE,"E6.34.3"),sQuery(id+"F0.wireOp",EDGE,"E6.34.4"),sQuery(id+"F0.wireOp",EDGE,"E6.35.1"),sQuery(id+"F0.wireOp",EDGE,"E6.35.2"),sQuery(id+"F0.wireOp",EDGE,"E6.35.3"),sQuery(id+"F0.wireOp",EDGE,"E6.35.4"),sQuery(id+"F0.wireOp",EDGE,"E6.36.1"),sQuery(id+"F0.wireOp",EDGE,"E6.36.2"),sQuery(id+"F0.wireOp",EDGE,"E6.36.3"),sQuery(id+"F0.wireOp",EDGE,"E6.36.4"),sQuery(id+"F0.wireOp",EDGE,"E6.37.1"),sQuery(id+"F0.wireOp",EDGE,"E6.37.2"),sQuery(id+"F0.wireOp",EDGE,"E6.37.3"),sQuery(id+"F0.wireOp",EDGE,"E6.37.4"),sQuery(id+"F0.wireOp",EDGE,"E6.38.1"),sQuery(id+"F0.wireOp",EDGE,"E6.38.2"),sQuery(id+"F0.wireOp",EDGE,"E6.38.3"),sQuery(id+"F0.wireOp",EDGE,"E6.38.4"),sQuery(id+"F0.wireOp",EDGE,"E6.39.1"),sQuery(id+"F0.wireOp",EDGE,"E6.39.2"),sQuery(id+"F0.wireOp",EDGE,"E6.39.3"),sQuery(id+"F0.wireOp",EDGE,"E6.39.4"),sQuery(id+"F0.wireOp",EDGE,"E6.40.1"),sQuery(id+"F0.wireOp",EDGE,"E6.40.2"),sQuery(id+"F0.wireOp",EDGE,"E6.40.3"),sQuery(id+"F0.wireOp",EDGE,"E6.40.4"),sQuery(id+"F0.wireOp",EDGE,"E6.41.1"),sQuery(id+"F0.wireOp",EDGE,"E6.41.2"),sQuery(id+"F0.wireOp",EDGE,"E6.41.3"),sQuery(id+"F0.wireOp",EDGE,"E6.41.4"),sQuery(id+"F0.wireOp",EDGE,"E6.42.1"),sQuery(id+"F0.wireOp",EDGE,"E6.42.2"),sQuery(id+"F0.wireOp",EDGE,"E6.42.3"),sQuery(id+"F0.wireOp",EDGE,"E6.42.4"),sQuery(id+"F0.wireOp",EDGE,"E6.43.1"),sQuery(id+"F0.wireOp",EDGE,"E6.43.2"),sQuery(id+"F0.wireOp",EDGE,"E6.43.3"),sQuery(id+"F0.wireOp",EDGE,"E6.43.4"),sQuery(id+"F0.wireOp",EDGE,"E7"),sQuery(id+"F0.wireOp",EDGE,"E8.1.0"),sQuery(id+"F0.wireOp",EDGE,"E8.2.0"),sQuery(id+"F0.wireOp",EDGE,"E8.3.0"),sQuery(id+"F0.wireOp",EDGE,"E8.4.0"),sQuery(id+"F0.wireOp",EDGE,"E8.5.0"),sQuery(id+"F0.wireOp",EDGE,"E8.6.0"),sQuery(id+"F0.wireOp",EDGE,"E8.7.0"),sQuery(id+"F0.wireOp",EDGE,"E8.8.0"),sQuery(id+"F0.wireOp",EDGE,"E8.9.0"),sQuery(id+"F0.wireOp",EDGE,"E8.10.0"),sQuery(id+"F0.wireOp",EDGE,"E8.11.0"),sQuery(id+"F0.wireOp",EDGE,"E8.12.0"),sQuery(id+"F0.wireOp",EDGE,"E8.13.0"),sQuery(id+"F0.wireOp",EDGE,"E8.14.0"),sQuery(id+"F0.wireOp",EDGE,"E8.15.0"),sQuery(id+"F0.wireOp",EDGE,"E8.16.0"),sQuery(id+"F0.wireOp",EDGE,"E8.17.0"),sQuery(id+"F0.wireOp",EDGE,"E8.18.0"),sQuery(id+"F0.wireOp",EDGE,"E8.19.0"),sQuery(id+"F0.wireOp",EDGE,"E8.20.0"),sQuery(id+"F0.wireOp",EDGE,"E8.21.0"),sQuery(id+"F0.wireOp",EDGE,"E8.22.0"),sQuery(id+"F0.wireOp",EDGE,"E8.23.0"),sQuery(id+"F0.wireOp",EDGE,"E8.24.0"),sQuery(id+"F0.wireOp",EDGE,"E8.25.0"),sQuery(id+"F0.wireOp",EDGE,"E8.26.0"),sQuery(id+"F0.wireOp",EDGE,"E8.27.0"),sQuery(id+"F0.wireOp",EDGE,"E8.28.0"),sQuery(id+"F0.wireOp",EDGE,"E8.29.0"),sQuery(id+"F0.wireOp",EDGE,"E8.30.0"),sQuery(id+"F0.wireOp",EDGE,"E8.31.0"),sQuery(id+"F0.wireOp",EDGE,"E8.32.0"),sQuery(id+"F0.wireOp",EDGE,"E8.33.0"),sQuery(id+"F0.wireOp",EDGE,"E8.34.0"),sQuery(id+"F0.wireOp",EDGE,"E8.35.0"),sQuery(id+"F0.wireOp",EDGE,"E8.36.0"),sQuery(id+"F0.wireOp",EDGE,"E8.37.0"),sQuery(id+"F0.wireOp",EDGE,"E8.38.0"),sQuery(id+"F0.wireOp",EDGE,"E8.39.0"),sQuery(id+"F0.wireOp",EDGE,"E8.40.0"),sQuery(id+"F0.wireOp",EDGE,"E8.41.0"),sQuery(id+"F0.wireOp",EDGE,"E8.42.0"),sQuery(id+"F0.wireOp",EDGE,"E8.43.0")])],"isStart":false})]});}
            var Q1;
            {var subQ0=sQuery(id+"F0.wireOp",EDGE,"E6.25.3");var subQ1=sQuery(id+"F0.wireOp",EDGE,"E6.25.1");Q1=makeQuery(id+"F2.opFillet","BLEND_EDGE",EDGE,{"blendedFrom":[makeQuery(id+"F1.opExtrude","SWEPT_EDGE",EDGE,{"disambiguationData":[OSD([sQuery(id+"F0.wireOp",EDGE,"E6.25.0"),subQ1,subQ0])]}),makeQuery(id+"F1.opExtrude","CAP_FACE",FACE,{"disambiguationData":[OSD([sQuery(id+"F0.wireOp",EDGE,"E0"),sQuery(id+"F0.wireOp",EDGE,"E1"),sQuery(id+"F0.wireOp",EDGE,"E2"),sQuery(id+"F0.wireOp",EDGE,"E4"),sQuery(id+"F0.wireOp",EDGE,"E5"),sQuery(id+"F0.wireOp",EDGE,"E6.1.1"),sQuery(id+"F0.wireOp",EDGE,"E6.1.2"),sQuery(id+"F0.wireOp",EDGE,"E6.1.3"),sQuery(id+"F0.wireOp",EDGE,"E6.1.4"),sQuery(id+"F0.wireOp",EDGE,"E6.2.1"),sQuery(id+"F0.wireOp",EDGE,"E6.2.2"),sQuery(id+"F0.wireOp",EDGE,"E6.2.3"),sQuery(id+"F0.wireOp",EDGE,"E6.2.4"),sQuery(id+"F0.wireOp",EDGE,"E6.3.1"),sQuery(id+"F0.wireOp",EDGE,"E6.3.2"),sQuery(id+"F0.wireOp",EDGE,"E6.3.3"),sQuery(id+"F0.wireOp",EDGE,"E6.3.4"),sQuery(id+"F0.wireOp",EDGE,"E6.4.1"),sQuery(id+"F0.wireOp",EDGE,"E6.4.2"),sQuery(id+"F0.wireOp",EDGE,"E6.4.3"),sQuery(id+"F0.wireOp",EDGE,"E6.4.4"),sQuery(id+"F0.wireOp",EDGE,"E6.5.1"),sQuery(id+"F0.wireOp",EDGE,"E6.5.2"),sQuery(id+"F0.wireOp",EDGE,"E6.5.3"),sQuery(id+"F0.wireOp",EDGE,"E6.5.4"),sQuery(id+"F0.wireOp",EDGE,"E6.6.1"),sQuery(id+"F0.wireOp",EDGE,"E6.6.2"),sQuery(id+"F0.wireOp",EDGE,"E6.6.3"),sQuery(id+"F0.wireOp",EDGE,"E6.6.4"),sQuery(id+"F0.wireOp",EDGE,"E6.7.1"),sQuery(id+"F0.wireOp",EDGE,"E6.7.2"),sQuery(id+"F0.wireOp",EDGE,"E6.7.3"),sQuery(id+"F0.wireOp",EDGE,"E6.7.4"),sQuery(id+"F0.wireOp",EDGE,"E6.8.1"),sQuery(id+"F0.wireOp",EDGE,"E6.8.2"),sQuery(id+"F0.wireOp",EDGE,"E6.8.3"),sQuery(id+"F0.wireOp",EDGE,"E6.8.4"),sQuery(id+"F0.wireOp",EDGE,"E6.9.1"),sQuery(id+"F0.wireOp",EDGE,"E6.9.2"),sQuery(id+"F0.wireOp",EDGE,"E6.9.3"),sQuery(id+"F0.wireOp",EDGE,"E6.9.4"),sQuery(id+"F0.wireOp",EDGE,"E6.10.1"),sQuery(id+"F0.wireOp",EDGE,"E6.10.2"),sQuery(id+"F0.wireOp",EDGE,"E6.10.3"),sQuery(id+"F0.wireOp",EDGE,"E6.10.4"),sQuery(id+"F0.wireOp",EDGE,"E6.11.1"),sQuery(id+"F0.wireOp",EDGE,"E6.11.2"),sQuery(id+"F0.wireOp",EDGE,"E6.11.3"),sQuery(id+"F0.wireOp",EDGE,"E6.11.4"),sQuery(id+"F0.wireOp",EDGE,"E6.12.1"),sQuery(id+"F0.wireOp",EDGE,"E6.12.2"),sQuery(id+"F0.wireOp",EDGE,"E6.12.3"),sQuery(id+"F0.wireOp",EDGE,"E6.12.4"),sQuery(id+"F0.wireOp",EDGE,"E6.13.1"),sQuery(id+"F0.wireOp",EDGE,"E6.13.2"),sQuery(id+"F0.wireOp",EDGE,"E6.13.3"),sQuery(id+"F0.wireOp",EDGE,"E6.13.4"),sQuery(id+"F0.wireOp",EDGE,"E6.14.1"),sQuery(id+"F0.wireOp",EDGE,"E6.14.2"),sQuery(id+"F0.wireOp",EDGE,"E6.14.3"),sQuery(id+"F0.wireOp",EDGE,"E6.14.4"),sQuery(id+"F0.wireOp",EDGE,"E6.15.1"),sQuery(id+"F0.wireOp",EDGE,"E6.15.2"),sQuery(id+"F0.wireOp",EDGE,"E6.15.3"),sQuery(id+"F0.wireOp",EDGE,"E6.15.4"),sQuery(id+"F0.wireOp",EDGE,"E6.16.1"),sQuery(id+"F0.wireOp",EDGE,"E6.16.2"),sQuery(id+"F0.wireOp",EDGE,"E6.16.3"),sQuery(id+"F0.wireOp",EDGE,"E6.16.4"),sQuery(id+"F0.wireOp",EDGE,"E6.17.1"),sQuery(id+"F0.wireOp",EDGE,"E6.17.2"),sQuery(id+"F0.wireOp",EDGE,"E6.17.3"),sQuery(id+"F0.wireOp",EDGE,"E6.17.4"),sQuery(id+"F0.wireOp",EDGE,"E6.18.1"),sQuery(id+"F0.wireOp",EDGE,"E6.18.2"),sQuery(id+"F0.wireOp",EDGE,"E6.18.3"),sQuery(id+"F0.wireOp",EDGE,"E6.18.4"),sQuery(id+"F0.wireOp",EDGE,"E6.19.1"),sQuery(id+"F0.wireOp",EDGE,"E6.19.2"),sQuery(id+"F0.wireOp",EDGE,"E6.19.3"),sQuery(id+"F0.wireOp",EDGE,"E6.19.4"),sQuery(id+"F0.wireOp",EDGE,"E6.20.1"),sQuery(id+"F0.wireOp",EDGE,"E6.20.2"),sQuery(id+"F0.wireOp",EDGE,"E6.20.3"),sQuery(id+"F0.wireOp",EDGE,"E6.20.4"),sQuery(id+"F0.wireOp",EDGE,"E6.21.1"),sQuery(id+"F0.wireOp",EDGE,"E6.21.2"),sQuery(id+"F0.wireOp",EDGE,"E6.21.3"),sQuery(id+"F0.wireOp",EDGE,"E6.21.4"),sQuery(id+"F0.wireOp",EDGE,"E6.22.1"),sQuery(id+"F0.wireOp",EDGE,"E6.22.2"),sQuery(id+"F0.wireOp",EDGE,"E6.22.3"),sQuery(id+"F0.wireOp",EDGE,"E6.22.4"),sQuery(id+"F0.wireOp",EDGE,"E6.23.1"),sQuery(id+"F0.wireOp",EDGE,"E6.23.2"),sQuery(id+"F0.wireOp",EDGE,"E6.23.3"),sQuery(id+"F0.wireOp",EDGE,"E6.23.4"),sQuery(id+"F0.wireOp",EDGE,"E6.24.1"),sQuery(id+"F0.wireOp",EDGE,"E6.24.2"),sQuery(id+"F0.wireOp",EDGE,"E6.24.3"),sQuery(id+"F0.wireOp",EDGE,"E6.24.4"),subQ1,sQuery(id+"F0.wireOp",EDGE,"E6.25.2"),subQ0,sQuery(id+"F0.wireOp",EDGE,"E6.25.4"),sQuery(id+"F0.wireOp",EDGE,"E6.26.1"),sQuery(id+"F0.wireOp",EDGE,"E6.26.2"),sQuery(id+"F0.wireOp",EDGE,"E6.26.3"),sQuery(id+"F0.wireOp",EDGE,"E6.26.4"),sQuery(id+"F0.wireOp",EDGE,"E6.27.1"),sQuery(id+"F0.wireOp",EDGE,"E6.27.2"),sQuery(id+"F0.wireOp",EDGE,"E6.27.3"),sQuery(id+"F0.wireOp",EDGE,"E6.27.4"),sQuery(id+"F0.wireOp",EDGE,"E6.28.1"),sQuery(id+"F0.wireOp",EDGE,"E6.28.2"),sQuery(id+"F0.wireOp",EDGE,"E6.28.3"),sQuery(id+"F0.wireOp",EDGE,"E6.28.4"),sQuery(id+"F0.wireOp",EDGE,"E6.29.1"),sQuery(id+"F0.wireOp",EDGE,"E6.29.2"),sQuery(id+"F0.wireOp",EDGE,"E6.29.3"),sQuery(id+"F0.wireOp",EDGE,"E6.29.4"),sQuery(id+"F0.wireOp",EDGE,"E6.30.1"),sQuery(id+"F0.wireOp",EDGE,"E6.30.2"),sQuery(id+"F0.wireOp",EDGE,"E6.30.3"),sQuery(id+"F0.wireOp",EDGE,"E6.30.4"),sQuery(id+"F0.wireOp",EDGE,"E6.31.1"),sQuery(id+"F0.wireOp",EDGE,"E6.31.2"),sQuery(id+"F0.wireOp",EDGE,"E6.31.3"),sQuery(id+"F0.wireOp",EDGE,"E6.31.4"),sQuery(id+"F0.wireOp",EDGE,"E6.32.1"),sQuery(id+"F0.wireOp",EDGE,"E6.32.2"),sQuery(id+"F0.wireOp",EDGE,"E6.32.3"),sQuery(id+"F0.wireOp",EDGE,"E6.32.4"),sQuery(id+"F0.wireOp",EDGE,"E6.33.1"),sQuery(id+"F0.wireOp",EDGE,"E6.33.2"),sQuery(id+"F0.wireOp",EDGE,"E6.33.3"),sQuery(id+"F0.wireOp",EDGE,"E6.33.4"),sQuery(id+"F0.wireOp",EDGE,"E6.34.1"),sQuery(id+"F0.wireOp",EDGE,"E6.34.2"),sQuery(id+"F0.wireOp",EDGE,"E6.34.3"),sQuery(id+"F0.wireOp",EDGE,"E6.34.4"),sQuery(id+"F0.wireOp",EDGE,"E6.35.1"),sQuery(id+"F0.wireOp",EDGE,"E6.35.2"),sQuery(id+"F0.wireOp",EDGE,"E6.35.3"),sQuery(id+"F0.wireOp",EDGE,"E6.35.4"),sQuery(id+"F0.wireOp",EDGE,"E6.36.1"),sQuery(id+"F0.wireOp",EDGE,"E6.36.2"),sQuery(id+"F0.wireOp",EDGE,"E6.36.3"),sQuery(id+"F0.wireOp",EDGE,"E6.36.4"),sQuery(id+"F0.wireOp",EDGE,"E6.37.1"),sQuery(id+"F0.wireOp",EDGE,"E6.37.2"),sQuery(id+"F0.wireOp",EDGE,"E6.37.3"),sQuery(id+"F0.wireOp",EDGE,"E6.37.4"),sQuery(id+"F0.wireOp",EDGE,"E6.38.1"),sQuery(id+"F0.wireOp",EDGE,"E6.38.2"),sQuery(id+"F0.wireOp",EDGE,"E6.38.3"),sQuery(id+"F0.wireOp",EDGE,"E6.38.4"),sQuery(id+"F0.wireOp",EDGE,"E6.39.1"),sQuery(id+"F0.wireOp",EDGE,"E6.39.2"),sQuery(id+"F0.wireOp",EDGE,"E6.39.3"),sQuery(id+"F0.wireOp",EDGE,"E6.39.4"),sQuery(id+"F0.wireOp",EDGE,"E6.40.1"),sQuery(id+"F0.wireOp",EDGE,"E6.40.2"),sQuery(id+"F0.wireOp",EDGE,"E6.40.3"),sQuery(id+"F0.wireOp",EDGE,"E6.40.4"),sQuery(id+"F0.wireOp",EDGE,"E6.41.1"),sQuery(id+"F0.wireOp",EDGE,"E6.41.2"),sQuery(id+"F0.wireOp",EDGE,"E6.41.3"),sQuery(id+"F0.wireOp",EDGE,"E6.41.4"),sQuery(id+"F0.wireOp",EDGE,"E6.42.1"),sQuery(id+"F0.wireOp",EDGE,"E6.42.2"),sQuery(id+"F0.wireOp",EDGE,"E6.42.3"),sQuery(id+"F0.wireOp",EDGE,"E6.42.4"),sQuery(id+"F0.wireOp",EDGE,"E6.43.1"),sQuery(id+"F0.wireOp",EDGE,"E6.43.2"),sQuery(id+"F0.wireOp",EDGE,"E6.43.3"),sQuery(id+"F0.wireOp",EDGE,"E6.43.4"),sQuery(id+"F0.wireOp",EDGE,"E7"),sQuery(id+"F0.wireOp",EDGE,"E8.1.0"),sQuery(id+"F0.wireOp",EDGE,"E8.2.0"),sQuery(id+"F0.wireOp",EDGE,"E8.3.0"),sQuery(id+"F0.wireOp",EDGE,"E8.4.0"),sQuery(id+"F0.wireOp",EDGE,"E8.5.0"),sQuery(id+"F0.wireOp",EDGE,"E8.6.0"),sQuery(id+"F0.wireOp",EDGE,"E8.7.0"),sQuery(id+"F0.wireOp",EDGE,"E8.8.0"),sQuery(id+"F0.wireOp",EDGE,"E8.9.0"),sQuery(id+"F0.wireOp",EDGE,"E8.10.0"),sQuery(id+"F0.wireOp",EDGE,"E8.11.0"),sQuery(id+"F0.wireOp",EDGE,"E8.12.0"),sQuery(id+"F0.wireOp",EDGE,"E8.13.0"),sQuery(id+"F0.wireOp",EDGE,"E8.14.0"),sQuery(id+"F0.wireOp",EDGE,"E8.15.0"),sQuery(id+"F0.wireOp",EDGE,"E8.16.0"),sQuery(id+"F0.wireOp",EDGE,"E8.17.0"),sQuery(id+"F0.wireOp",EDGE,"E8.18.0"),sQuery(id+"F0.wireOp",EDGE,"E8.19.0"),sQuery(id+"F0.wireOp",EDGE,"E8.20.0"),sQuery(id+"F0.wireOp",EDGE,"E8.21.0"),sQuery(id+"F0.wireOp",EDGE,"E8.22.0"),sQuery(id+"F0.wireOp",EDGE,"E8.23.0"),sQuery(id+"F0.wireOp",EDGE,"E8.24.0"),sQuery(id+"F0.wireOp",EDGE,"E8.25.0"),sQuery(id+"F0.wireOp",EDGE,"E8.26.0"),sQuery(id+"F0.wireOp",EDGE,"E8.27.0"),sQuery(id+"F0.wireOp",EDGE,"E8.28.0"),sQuery(id+"F0.wireOp",EDGE,"E8.29.0"),sQuery(id+"F0.wireOp",EDGE,"E8.30.0"),sQuery(id+"F0.wireOp",EDGE,"E8.31.0"),sQuery(id+"F0.wireOp",EDGE,"E8.32.0"),sQuery(id+"F0.wireOp",EDGE,"E8.33.0"),sQuery(id+"F0.wireOp",EDGE,"E8.34.0"),sQuery(id+"F0.wireOp",EDGE,"E8.35.0"),sQuery(id+"F0.wireOp",EDGE,"E8.36.0"),sQuery(id+"F0.wireOp",EDGE,"E8.37.0"),sQuery(id+"F0.wireOp",EDGE,"E8.38.0"),sQuery(id+"F0.wireOp",EDGE,"E8.39.0"),sQuery(id+"F0.wireOp",EDGE,"E8.40.0"),sQuery(id+"F0.wireOp",EDGE,"E8.41.0"),sQuery(id+"F0.wireOp",EDGE,"E8.42.0"),sQuery(id+"F0.wireOp",EDGE,"E8.43.0")])],"isStart":false})],"blendedInto":[makeQuery(id+"F1.opExtrude","CAP_FACE",FACE,{"disambiguationData":[OSD([sQuery(id+"F0.wireOp",EDGE,"E0"),sQuery(id+"F0.wireOp",EDGE,"E1"),sQuery(id+"F0.wireOp",EDGE,"E2"),sQuery(id+"F0.wireOp",EDGE,"E4"),sQuery(id+"F0.wireOp",EDGE,"E5"),sQuery(id+"F0.wireOp",EDGE,"E6.1.1"),sQuery(id+"F0.wireOp",EDGE,"E6.1.2"),sQuery(id+"F0.wireOp",EDGE,"E6.1.3"),sQuery(id+"F0.wireOp",EDGE,"E6.1.4"),sQuery(id+"F0.wireOp",EDGE,"E6.2.1"),sQuery(id+"F0.wireOp",EDGE,"E6.2.2"),sQuery(id+"F0.wireOp",EDGE,"E6.2.3"),sQuery(id+"F0.wireOp",EDGE,"E6.2.4"),sQuery(id+"F0.wireOp",EDGE,"E6.3.1"),sQuery(id+"F0.wireOp",EDGE,"E6.3.2"),sQuery(id+"F0.wireOp",EDGE,"E6.3.3"),sQuery(id+"F0.wireOp",EDGE,"E6.3.4"),sQuery(id+"F0.wireOp",EDGE,"E6.4.1"),sQuery(id+"F0.wireOp",EDGE,"E6.4.2"),sQuery(id+"F0.wireOp",EDGE,"E6.4.3"),sQuery(id+"F0.wireOp",EDGE,"E6.4.4"),sQuery(id+"F0.wireOp",EDGE,"E6.5.1"),sQuery(id+"F0.wireOp",EDGE,"E6.5.2"),sQuery(id+"F0.wireOp",EDGE,"E6.5.3"),sQuery(id+"F0.wireOp",EDGE,"E6.5.4"),sQuery(id+"F0.wireOp",EDGE,"E6.6.1"),sQuery(id+"F0.wireOp",EDGE,"E6.6.2"),sQuery(id+"F0.wireOp",EDGE,"E6.6.3"),sQuery(id+"F0.wireOp",EDGE,"E6.6.4"),sQuery(id+"F0.wireOp",EDGE,"E6.7.1"),sQuery(id+"F0.wireOp",EDGE,"E6.7.2"),sQuery(id+"F0.wireOp",EDGE,"E6.7.3"),sQuery(id+"F0.wireOp",EDGE,"E6.7.4"),sQuery(id+"F0.wireOp",EDGE,"E6.8.1"),sQuery(id+"F0.wireOp",EDGE,"E6.8.2"),sQuery(id+"F0.wireOp",EDGE,"E6.8.3"),sQuery(id+"F0.wireOp",EDGE,"E6.8.4"),sQuery(id+"F0.wireOp",EDGE,"E6.9.1"),sQuery(id+"F0.wireOp",EDGE,"E6.9.2"),sQuery(id+"F0.wireOp",EDGE,"E6.9.3"),sQuery(id+"F0.wireOp",EDGE,"E6.9.4"),sQuery(id+"F0.wireOp",EDGE,"E6.10.1"),sQuery(id+"F0.wireOp",EDGE,"E6.10.2"),sQuery(id+"F0.wireOp",EDGE,"E6.10.3"),sQuery(id+"F0.wireOp",EDGE,"E6.10.4"),sQuery(id+"F0.wireOp",EDGE,"E6.11.1"),sQuery(id+"F0.wireOp",EDGE,"E6.11.2"),sQuery(id+"F0.wireOp",EDGE,"E6.11.3"),sQuery(id+"F0.wireOp",EDGE,"E6.11.4"),sQuery(id+"F0.wireOp",EDGE,"E6.12.1"),sQuery(id+"F0.wireOp",EDGE,"E6.12.2"),sQuery(id+"F0.wireOp",EDGE,"E6.12.3"),sQuery(id+"F0.wireOp",EDGE,"E6.12.4"),sQuery(id+"F0.wireOp",EDGE,"E6.13.1"),sQuery(id+"F0.wireOp",EDGE,"E6.13.2"),sQuery(id+"F0.wireOp",EDGE,"E6.13.3"),sQuery(id+"F0.wireOp",EDGE,"E6.13.4"),sQuery(id+"F0.wireOp",EDGE,"E6.14.1"),sQuery(id+"F0.wireOp",EDGE,"E6.14.2"),sQuery(id+"F0.wireOp",EDGE,"E6.14.3"),sQuery(id+"F0.wireOp",EDGE,"E6.14.4"),sQuery(id+"F0.wireOp",EDGE,"E6.15.1"),sQuery(id+"F0.wireOp",EDGE,"E6.15.2"),sQuery(id+"F0.wireOp",EDGE,"E6.15.3"),sQuery(id+"F0.wireOp",EDGE,"E6.15.4"),sQuery(id+"F0.wireOp",EDGE,"E6.16.1"),sQuery(id+"F0.wireOp",EDGE,"E6.16.2"),sQuery(id+"F0.wireOp",EDGE,"E6.16.3"),sQuery(id+"F0.wireOp",EDGE,"E6.16.4"),sQuery(id+"F0.wireOp",EDGE,"E6.17.1"),sQuery(id+"F0.wireOp",EDGE,"E6.17.2"),sQuery(id+"F0.wireOp",EDGE,"E6.17.3"),sQuery(id+"F0.wireOp",EDGE,"E6.17.4"),sQuery(id+"F0.wireOp",EDGE,"E6.18.1"),sQuery(id+"F0.wireOp",EDGE,"E6.18.2"),sQuery(id+"F0.wireOp",EDGE,"E6.18.3"),sQuery(id+"F0.wireOp",EDGE,"E6.18.4"),sQuery(id+"F0.wireOp",EDGE,"E6.19.1"),sQuery(id+"F0.wireOp",EDGE,"E6.19.2"),sQuery(id+"F0.wireOp",EDGE,"E6.19.3"),sQuery(id+"F0.wireOp",EDGE,"E6.19.4"),sQuery(id+"F0.wireOp",EDGE,"E6.20.1"),sQuery(id+"F0.wireOp",EDGE,"E6.20.2"),sQuery(id+"F0.wireOp",EDGE,"E6.20.3"),sQuery(id+"F0.wireOp",EDGE,"E6.20.4"),sQuery(id+"F0.wireOp",EDGE,"E6.21.1"),sQuery(id+"F0.wireOp",EDGE,"E6.21.2"),sQuery(id+"F0.wireOp",EDGE,"E6.21.3"),sQuery(id+"F0.wireOp",EDGE,"E6.21.4"),sQuery(id+"F0.wireOp",EDGE,"E6.22.1"),sQuery(id+"F0.wireOp",EDGE,"E6.22.2"),sQuery(id+"F0.wireOp",EDGE,"E6.22.3"),sQuery(id+"F0.wireOp",EDGE,"E6.22.4"),sQuery(id+"F0.wireOp",EDGE,"E6.23.1"),sQuery(id+"F0.wireOp",EDGE,"E6.23.2"),sQuery(id+"F0.wireOp",EDGE,"E6.23.3"),sQuery(id+"F0.wireOp",EDGE,"E6.23.4"),sQuery(id+"F0.wireOp",EDGE,"E6.24.1"),sQuery(id+"F0.wireOp",EDGE,"E6.24.2"),sQuery(id+"F0.wireOp",EDGE,"E6.24.3"),sQuery(id+"F0.wireOp",EDGE,"E6.24.4"),subQ1,sQuery(id+"F0.wireOp",EDGE,"E6.25.2"),subQ0,sQuery(id+"F0.wireOp",EDGE,"E6.25.4"),sQuery(id+"F0.wireOp",EDGE,"E6.26.1"),sQuery(id+"F0.wireOp",EDGE,"E6.26.2"),sQuery(id+"F0.wireOp",EDGE,"E6.26.3"),sQuery(id+"F0.wireOp",EDGE,"E6.26.4"),sQuery(id+"F0.wireOp",EDGE,"E6.27.1"),sQuery(id+"F0.wireOp",EDGE,"E6.27.2"),sQuery(id+"F0.wireOp",EDGE,"E6.27.3"),sQuery(id+"F0.wireOp",EDGE,"E6.27.4"),sQuery(id+"F0.wireOp",EDGE,"E6.28.1"),sQuery(id+"F0.wireOp",EDGE,"E6.28.2"),sQuery(id+"F0.wireOp",EDGE,"E6.28.3"),sQuery(id+"F0.wireOp",EDGE,"E6.28.4"),sQuery(id+"F0.wireOp",EDGE,"E6.29.1"),sQuery(id+"F0.wireOp",EDGE,"E6.29.2"),sQuery(id+"F0.wireOp",EDGE,"E6.29.3"),sQuery(id+"F0.wireOp",EDGE,"E6.29.4"),sQuery(id+"F0.wireOp",EDGE,"E6.30.1"),sQuery(id+"F0.wireOp",EDGE,"E6.30.2"),sQuery(id+"F0.wireOp",EDGE,"E6.30.3"),sQuery(id+"F0.wireOp",EDGE,"E6.30.4"),sQuery(id+"F0.wireOp",EDGE,"E6.31.1"),sQuery(id+"F0.wireOp",EDGE,"E6.31.2"),sQuery(id+"F0.wireOp",EDGE,"E6.31.3"),sQuery(id+"F0.wireOp",EDGE,"E6.31.4"),sQuery(id+"F0.wireOp",EDGE,"E6.32.1"),sQuery(id+"F0.wireOp",EDGE,"E6.32.2"),sQuery(id+"F0.wireOp",EDGE,"E6.32.3"),sQuery(id+"F0.wireOp",EDGE,"E6.32.4"),sQuery(id+"F0.wireOp",EDGE,"E6.33.1"),sQuery(id+"F0.wireOp",EDGE,"E6.33.2"),sQuery(id+"F0.wireOp",EDGE,"E6.33.3"),sQuery(id+"F0.wireOp",EDGE,"E6.33.4"),sQuery(id+"F0.wireOp",EDGE,"E6.34.1"),sQuery(id+"F0.wireOp",EDGE,"E6.34.2"),sQuery(id+"F0.wireOp",EDGE,"E6.34.3"),sQuery(id+"F0.wireOp",EDGE,"E6.34.4"),sQuery(id+"F0.wireOp",EDGE,"E6.35.1"),sQuery(id+"F0.wireOp",EDGE,"E6.35.2"),sQuery(id+"F0.wireOp",EDGE,"E6.35.3"),sQuery(id+"F0.wireOp",EDGE,"E6.35.4"),sQuery(id+"F0.wireOp",EDGE,"E6.36.1"),sQuery(id+"F0.wireOp",EDGE,"E6.36.2"),sQuery(id+"F0.wireOp",EDGE,"E6.36.3"),sQuery(id+"F0.wireOp",EDGE,"E6.36.4"),sQuery(id+"F0.wireOp",EDGE,"E6.37.1"),sQuery(id+"F0.wireOp",EDGE,"E6.37.2"),sQuery(id+"F0.wireOp",EDGE,"E6.37.3"),sQuery(id+"F0.wireOp",EDGE,"E6.37.4"),sQuery(id+"F0.wireOp",EDGE,"E6.38.1"),sQuery(id+"F0.wireOp",EDGE,"E6.38.2"),sQuery(id+"F0.wireOp",EDGE,"E6.38.3"),sQuery(id+"F0.wireOp",EDGE,"E6.38.4"),sQuery(id+"F0.wireOp",EDGE,"E6.39.1"),sQuery(id+"F0.wireOp",EDGE,"E6.39.2"),sQuery(id+"F0.wireOp",EDGE,"E6.39.3"),sQuery(id+"F0.wireOp",EDGE,"E6.39.4"),sQuery(id+"F0.wireOp",EDGE,"E6.40.1"),sQuery(id+"F0.wireOp",EDGE,"E6.40.2"),sQuery(id+"F0.wireOp",EDGE,"E6.40.3"),sQuery(id+"F0.wireOp",EDGE,"E6.40.4"),sQuery(id+"F0.wireOp",EDGE,"E6.41.1"),sQuery(id+"F0.wireOp",EDGE,"E6.41.2"),sQuery(id+"F0.wireOp",EDGE,"E6.41.3"),sQuery(id+"F0.wireOp",EDGE,"E6.41.4"),sQuery(id+"F0.wireOp",EDGE,"E6.42.1"),sQuery(id+"F0.wireOp",EDGE,"E6.42.2"),sQuery(id+"F0.wireOp",EDGE,"E6.42.3"),sQuery(id+"F0.wireOp",EDGE,"E6.42.4"),sQuery(id+"F0.wireOp",EDGE,"E6.43.1"),sQuery(id+"F0.wireOp",EDGE,"E6.43.2"),sQuery(id+"F0.wireOp",EDGE,"E6.43.3"),sQuery(id+"F0.wireOp",EDGE,"E6.43.4"),sQuery(id+"F0.wireOp",EDGE,"E7"),sQuery(id+"F0.wireOp",EDGE,"E8.1.0"),sQuery(id+"F0.wireOp",EDGE,"E8.2.0"),sQuery(id+"F0.wireOp",EDGE,"E8.3.0"),sQuery(id+"F0.wireOp",EDGE,"E8.4.0"),sQuery(id+"F0.wireOp",EDGE,"E8.5.0"),sQuery(id+"F0.wireOp",EDGE,"E8.6.0"),sQuery(id+"F0.wireOp",EDGE,"E8.7.0"),sQuery(id+"F0.wireOp",EDGE,"E8.8.0"),sQuery(id+"F0.wireOp",EDGE,"E8.9.0"),sQuery(id+"F0.wireOp",EDGE,"E8.10.0"),sQuery(id+"F0.wireOp",EDGE,"E8.11.0"),sQuery(id+"F0.wireOp",EDGE,"E8.12.0"),sQuery(id+"F0.wireOp",EDGE,"E8.13.0"),sQuery(id+"F0.wireOp",EDGE,"E8.14.0"),sQuery(id+"F0.wireOp",EDGE,"E8.15.0"),sQuery(id+"F0.wireOp",EDGE,"E8.16.0"),sQuery(id+"F0.wireOp",EDGE,"E8.17.0"),sQuery(id+"F0.wireOp",EDGE,"E8.18.0"),sQuery(id+"F0.wireOp",EDGE,"E8.19.0"),sQuery(id+"F0.wireOp",EDGE,"E8.20.0"),sQuery(id+"F0.wireOp",EDGE,"E8.21.0"),sQuery(id+"F0.wireOp",EDGE,"E8.22.0"),sQuery(id+"F0.wireOp",EDGE,"E8.23.0"),sQuery(id+"F0.wireOp",EDGE,"E8.24.0"),sQuery(id+"F0.wireOp",EDGE,"E8.25.0"),sQuery(id+"F0.wireOp",EDGE,"E8.26.0"),sQuery(id+"F0.wireOp",EDGE,"E8.27.0"),sQuery(id+"F0.wireOp",EDGE,"E8.28.0"),sQuery(id+"F0.wireOp",EDGE,"E8.29.0"),sQuery(id+"F0.wireOp",EDGE,"E8.30.0"),sQuery(id+"F0.wireOp",EDGE,"E8.31.0"),sQuery(id+"F0.wireOp",EDGE,"E8.32.0"),sQuery(id+"F0.wireOp",EDGE,"E8.33.0"),sQuery(id+"F0.wireOp",EDGE,"E8.34.0"),sQuery(id+"F0.wireOp",EDGE,"E8.35.0"),sQuery(id+"F0.wireOp",EDGE,"E8.36.0"),sQuery(id+"F0.wireOp",EDGE,"E8.37.0"),sQuery(id+"F0.wireOp",EDGE,"E8.38.0"),sQuery(id+"F0.wireOp",EDGE,"E8.39.0"),sQuery(id+"F0.wireOp",EDGE,"E8.40.0"),sQuery(id+"F0.wireOp",EDGE,"E8.41.0"),sQuery(id+"F0.wireOp",EDGE,"E8.42.0"),sQuery(id+"F0.wireOp",EDGE,"E8.43.0")])],"isStart":false})]});}
            var Q2;
            {var subQ0=sQuery(id+"F0.wireOp",EDGE,"E6.27.3");var subQ1=sQuery(id+"F0.wireOp",EDGE,"E6.27.1");Q2=makeQuery(id+"F2.opFillet","BLEND_EDGE",EDGE,{"blendedFrom":[makeQuery(id+"F1.opExtrude","SWEPT_EDGE",EDGE,{"disambiguationData":[OSD([sQuery(id+"F0.wireOp",EDGE,"E6.27.0"),subQ1,subQ0])]}),makeQuery(id+"F1.opExtrude","CAP_FACE",FACE,{"disambiguationData":[OSD([sQuery(id+"F0.wireOp",EDGE,"E0"),sQuery(id+"F0.wireOp",EDGE,"E1"),sQuery(id+"F0.wireOp",EDGE,"E2"),sQuery(id+"F0.wireOp",EDGE,"E4"),sQuery(id+"F0.wireOp",EDGE,"E5"),sQuery(id+"F0.wireOp",EDGE,"E6.1.1"),sQuery(id+"F0.wireOp",EDGE,"E6.1.2"),sQuery(id+"F0.wireOp",EDGE,"E6.1.3"),sQuery(id+"F0.wireOp",EDGE,"E6.1.4"),sQuery(id+"F0.wireOp",EDGE,"E6.2.1"),sQuery(id+"F0.wireOp",EDGE,"E6.2.2"),sQuery(id+"F0.wireOp",EDGE,"E6.2.3"),sQuery(id+"F0.wireOp",EDGE,"E6.2.4"),sQuery(id+"F0.wireOp",EDGE,"E6.3.1"),sQuery(id+"F0.wireOp",EDGE,"E6.3.2"),sQuery(id+"F0.wireOp",EDGE,"E6.3.3"),sQuery(id+"F0.wireOp",EDGE,"E6.3.4"),sQuery(id+"F0.wireOp",EDGE,"E6.4.1"),sQuery(id+"F0.wireOp",EDGE,"E6.4.2"),sQuery(id+"F0.wireOp",EDGE,"E6.4.3"),sQuery(id+"F0.wireOp",EDGE,"E6.4.4"),sQuery(id+"F0.wireOp",EDGE,"E6.5.1"),sQuery(id+"F0.wireOp",EDGE,"E6.5.2"),sQuery(id+"F0.wireOp",EDGE,"E6.5.3"),sQuery(id+"F0.wireOp",EDGE,"E6.5.4"),sQuery(id+"F0.wireOp",EDGE,"E6.6.1"),sQuery(id+"F0.wireOp",EDGE,"E6.6.2"),sQuery(id+"F0.wireOp",EDGE,"E6.6.3"),sQuery(id+"F0.wireOp",EDGE,"E6.6.4"),sQuery(id+"F0.wireOp",EDGE,"E6.7.1"),sQuery(id+"F0.wireOp",EDGE,"E6.7.2"),sQuery(id+"F0.wireOp",EDGE,"E6.7.3"),sQuery(id+"F0.wireOp",EDGE,"E6.7.4"),sQuery(id+"F0.wireOp",EDGE,"E6.8.1"),sQuery(id+"F0.wireOp",EDGE,"E6.8.2"),sQuery(id+"F0.wireOp",EDGE,"E6.8.3"),sQuery(id+"F0.wireOp",EDGE,"E6.8.4"),sQuery(id+"F0.wireOp",EDGE,"E6.9.1"),sQuery(id+"F0.wireOp",EDGE,"E6.9.2"),sQuery(id+"F0.wireOp",EDGE,"E6.9.3"),sQuery(id+"F0.wireOp",EDGE,"E6.9.4"),sQuery(id+"F0.wireOp",EDGE,"E6.10.1"),sQuery(id+"F0.wireOp",EDGE,"E6.10.2"),sQuery(id+"F0.wireOp",EDGE,"E6.10.3"),sQuery(id+"F0.wireOp",EDGE,"E6.10.4"),sQuery(id+"F0.wireOp",EDGE,"E6.11.1"),sQuery(id+"F0.wireOp",EDGE,"E6.11.2"),sQuery(id+"F0.wireOp",EDGE,"E6.11.3"),sQuery(id+"F0.wireOp",EDGE,"E6.11.4"),sQuery(id+"F0.wireOp",EDGE,"E6.12.1"),sQuery(id+"F0.wireOp",EDGE,"E6.12.2"),sQuery(id+"F0.wireOp",EDGE,"E6.12.3"),sQuery(id+"F0.wireOp",EDGE,"E6.12.4"),sQuery(id+"F0.wireOp",EDGE,"E6.13.1"),sQuery(id+"F0.wireOp",EDGE,"E6.13.2"),sQuery(id+"F0.wireOp",EDGE,"E6.13.3"),sQuery(id+"F0.wireOp",EDGE,"E6.13.4"),sQuery(id+"F0.wireOp",EDGE,"E6.14.1"),sQuery(id+"F0.wireOp",EDGE,"E6.14.2"),sQuery(id+"F0.wireOp",EDGE,"E6.14.3"),sQuery(id+"F0.wireOp",EDGE,"E6.14.4"),sQuery(id+"F0.wireOp",EDGE,"E6.15.1"),sQuery(id+"F0.wireOp",EDGE,"E6.15.2"),sQuery(id+"F0.wireOp",EDGE,"E6.15.3"),sQuery(id+"F0.wireOp",EDGE,"E6.15.4"),sQuery(id+"F0.wireOp",EDGE,"E6.16.1"),sQuery(id+"F0.wireOp",EDGE,"E6.16.2"),sQuery(id+"F0.wireOp",EDGE,"E6.16.3"),sQuery(id+"F0.wireOp",EDGE,"E6.16.4"),sQuery(id+"F0.wireOp",EDGE,"E6.17.1"),sQuery(id+"F0.wireOp",EDGE,"E6.17.2"),sQuery(id+"F0.wireOp",EDGE,"E6.17.3"),sQuery(id+"F0.wireOp",EDGE,"E6.17.4"),sQuery(id+"F0.wireOp",EDGE,"E6.18.1"),sQuery(id+"F0.wireOp",EDGE,"E6.18.2"),sQuery(id+"F0.wireOp",EDGE,"E6.18.3"),sQuery(id+"F0.wireOp",EDGE,"E6.18.4"),sQuery(id+"F0.wireOp",EDGE,"E6.19.1"),sQuery(id+"F0.wireOp",EDGE,"E6.19.2"),sQuery(id+"F0.wireOp",EDGE,"E6.19.3"),sQuery(id+"F0.wireOp",EDGE,"E6.19.4"),sQuery(id+"F0.wireOp",EDGE,"E6.20.1"),sQuery(id+"F0.wireOp",EDGE,"E6.20.2"),sQuery(id+"F0.wireOp",EDGE,"E6.20.3"),sQuery(id+"F0.wireOp",EDGE,"E6.20.4"),sQuery(id+"F0.wireOp",EDGE,"E6.21.1"),sQuery(id+"F0.wireOp",EDGE,"E6.21.2"),sQuery(id+"F0.wireOp",EDGE,"E6.21.3"),sQuery(id+"F0.wireOp",EDGE,"E6.21.4"),sQuery(id+"F0.wireOp",EDGE,"E6.22.1"),sQuery(id+"F0.wireOp",EDGE,"E6.22.2"),sQuery(id+"F0.wireOp",EDGE,"E6.22.3"),sQuery(id+"F0.wireOp",EDGE,"E6.22.4"),sQuery(id+"F0.wireOp",EDGE,"E6.23.1"),sQuery(id+"F0.wireOp",EDGE,"E6.23.2"),sQuery(id+"F0.wireOp",EDGE,"E6.23.3"),sQuery(id+"F0.wireOp",EDGE,"E6.23.4"),sQuery(id+"F0.wireOp",EDGE,"E6.24.1"),sQuery(id+"F0.wireOp",EDGE,"E6.24.2"),sQuery(id+"F0.wireOp",EDGE,"E6.24.3"),sQuery(id+"F0.wireOp",EDGE,"E6.24.4"),sQuery(id+"F0.wireOp",EDGE,"E6.25.1"),sQuery(id+"F0.wireOp",EDGE,"E6.25.2"),sQuery(id+"F0.wireOp",EDGE,"E6.25.3"),sQuery(id+"F0.wireOp",EDGE,"E6.25.4"),sQuery(id+"F0.wireOp",EDGE,"E6.26.1"),sQuery(id+"F0.wireOp",EDGE,"E6.26.2"),sQuery(id+"F0.wireOp",EDGE,"E6.26.3"),sQuery(id+"F0.wireOp",EDGE,"E6.26.4"),subQ1,sQuery(id+"F0.wireOp",EDGE,"E6.27.2"),subQ0,sQuery(id+"F0.wireOp",EDGE,"E6.27.4"),sQuery(id+"F0.wireOp",EDGE,"E6.28.1"),sQuery(id+"F0.wireOp",EDGE,"E6.28.2"),sQuery(id+"F0.wireOp",EDGE,"E6.28.3"),sQuery(id+"F0.wireOp",EDGE,"E6.28.4"),sQuery(id+"F0.wireOp",EDGE,"E6.29.1"),sQuery(id+"F0.wireOp",EDGE,"E6.29.2"),sQuery(id+"F0.wireOp",EDGE,"E6.29.3"),sQuery(id+"F0.wireOp",EDGE,"E6.29.4"),sQuery(id+"F0.wireOp",EDGE,"E6.30.1"),sQuery(id+"F0.wireOp",EDGE,"E6.30.2"),sQuery(id+"F0.wireOp",EDGE,"E6.30.3"),sQuery(id+"F0.wireOp",EDGE,"E6.30.4"),sQuery(id+"F0.wireOp",EDGE,"E6.31.1"),sQuery(id+"F0.wireOp",EDGE,"E6.31.2"),sQuery(id+"F0.wireOp",EDGE,"E6.31.3"),sQuery(id+"F0.wireOp",EDGE,"E6.31.4"),sQuery(id+"F0.wireOp",EDGE,"E6.32.1"),sQuery(id+"F0.wireOp",EDGE,"E6.32.2"),sQuery(id+"F0.wireOp",EDGE,"E6.32.3"),sQuery(id+"F0.wireOp",EDGE,"E6.32.4"),sQuery(id+"F0.wireOp",EDGE,"E6.33.1"),sQuery(id+"F0.wireOp",EDGE,"E6.33.2"),sQuery(id+"F0.wireOp",EDGE,"E6.33.3"),sQuery(id+"F0.wireOp",EDGE,"E6.33.4"),sQuery(id+"F0.wireOp",EDGE,"E6.34.1"),sQuery(id+"F0.wireOp",EDGE,"E6.34.2"),sQuery(id+"F0.wireOp",EDGE,"E6.34.3"),sQuery(id+"F0.wireOp",EDGE,"E6.34.4"),sQuery(id+"F0.wireOp",EDGE,"E6.35.1"),sQuery(id+"F0.wireOp",EDGE,"E6.35.2"),sQuery(id+"F0.wireOp",EDGE,"E6.35.3"),sQuery(id+"F0.wireOp",EDGE,"E6.35.4"),sQuery(id+"F0.wireOp",EDGE,"E6.36.1"),sQuery(id+"F0.wireOp",EDGE,"E6.36.2"),sQuery(id+"F0.wireOp",EDGE,"E6.36.3"),sQuery(id+"F0.wireOp",EDGE,"E6.36.4"),sQuery(id+"F0.wireOp",EDGE,"E6.37.1"),sQuery(id+"F0.wireOp",EDGE,"E6.37.2"),sQuery(id+"F0.wireOp",EDGE,"E6.37.3"),sQuery(id+"F0.wireOp",EDGE,"E6.37.4"),sQuery(id+"F0.wireOp",EDGE,"E6.38.1"),sQuery(id+"F0.wireOp",EDGE,"E6.38.2"),sQuery(id+"F0.wireOp",EDGE,"E6.38.3"),sQuery(id+"F0.wireOp",EDGE,"E6.38.4"),sQuery(id+"F0.wireOp",EDGE,"E6.39.1"),sQuery(id+"F0.wireOp",EDGE,"E6.39.2"),sQuery(id+"F0.wireOp",EDGE,"E6.39.3"),sQuery(id+"F0.wireOp",EDGE,"E6.39.4"),sQuery(id+"F0.wireOp",EDGE,"E6.40.1"),sQuery(id+"F0.wireOp",EDGE,"E6.40.2"),sQuery(id+"F0.wireOp",EDGE,"E6.40.3"),sQuery(id+"F0.wireOp",EDGE,"E6.40.4"),sQuery(id+"F0.wireOp",EDGE,"E6.41.1"),sQuery(id+"F0.wireOp",EDGE,"E6.41.2"),sQuery(id+"F0.wireOp",EDGE,"E6.41.3"),sQuery(id+"F0.wireOp",EDGE,"E6.41.4"),sQuery(id+"F0.wireOp",EDGE,"E6.42.1"),sQuery(id+"F0.wireOp",EDGE,"E6.42.2"),sQuery(id+"F0.wireOp",EDGE,"E6.42.3"),sQuery(id+"F0.wireOp",EDGE,"E6.42.4"),sQuery(id+"F0.wireOp",EDGE,"E6.43.1"),sQuery(id+"F0.wireOp",EDGE,"E6.43.2"),sQuery(id+"F0.wireOp",EDGE,"E6.43.3"),sQuery(id+"F0.wireOp",EDGE,"E6.43.4"),sQuery(id+"F0.wireOp",EDGE,"E7"),sQuery(id+"F0.wireOp",EDGE,"E8.1.0"),sQuery(id+"F0.wireOp",EDGE,"E8.2.0"),sQuery(id+"F0.wireOp",EDGE,"E8.3.0"),sQuery(id+"F0.wireOp",EDGE,"E8.4.0"),sQuery(id+"F0.wireOp",EDGE,"E8.5.0"),sQuery(id+"F0.wireOp",EDGE,"E8.6.0"),sQuery(id+"F0.wireOp",EDGE,"E8.7.0"),sQuery(id+"F0.wireOp",EDGE,"E8.8.0"),sQuery(id+"F0.wireOp",EDGE,"E8.9.0"),sQuery(id+"F0.wireOp",EDGE,"E8.10.0"),sQuery(id+"F0.wireOp",EDGE,"E8.11.0"),sQuery(id+"F0.wireOp",EDGE,"E8.12.0"),sQuery(id+"F0.wireOp",EDGE,"E8.13.0"),sQuery(id+"F0.wireOp",EDGE,"E8.14.0"),sQuery(id+"F0.wireOp",EDGE,"E8.15.0"),sQuery(id+"F0.wireOp",EDGE,"E8.16.0"),sQuery(id+"F0.wireOp",EDGE,"E8.17.0"),sQuery(id+"F0.wireOp",EDGE,"E8.18.0"),sQuery(id+"F0.wireOp",EDGE,"E8.19.0"),sQuery(id+"F0.wireOp",EDGE,"E8.20.0"),sQuery(id+"F0.wireOp",EDGE,"E8.21.0"),sQuery(id+"F0.wireOp",EDGE,"E8.22.0"),sQuery(id+"F0.wireOp",EDGE,"E8.23.0"),sQuery(id+"F0.wireOp",EDGE,"E8.24.0"),sQuery(id+"F0.wireOp",EDGE,"E8.25.0"),sQuery(id+"F0.wireOp",EDGE,"E8.26.0"),sQuery(id+"F0.wireOp",EDGE,"E8.27.0"),sQuery(id+"F0.wireOp",EDGE,"E8.28.0"),sQuery(id+"F0.wireOp",EDGE,"E8.29.0"),sQuery(id+"F0.wireOp",EDGE,"E8.30.0"),sQuery(id+"F0.wireOp",EDGE,"E8.31.0"),sQuery(id+"F0.wireOp",EDGE,"E8.32.0"),sQuery(id+"F0.wireOp",EDGE,"E8.33.0"),sQuery(id+"F0.wireOp",EDGE,"E8.34.0"),sQuery(id+"F0.wireOp",EDGE,"E8.35.0"),sQuery(id+"F0.wireOp",EDGE,"E8.36.0"),sQuery(id+"F0.wireOp",EDGE,"E8.37.0"),sQuery(id+"F0.wireOp",EDGE,"E8.38.0"),sQuery(id+"F0.wireOp",EDGE,"E8.39.0"),sQuery(id+"F0.wireOp",EDGE,"E8.40.0"),sQuery(id+"F0.wireOp",EDGE,"E8.41.0"),sQuery(id+"F0.wireOp",EDGE,"E8.42.0"),sQuery(id+"F0.wireOp",EDGE,"E8.43.0")])],"isStart":false})],"blendedInto":[makeQuery(id+"F1.opExtrude","CAP_FACE",FACE,{"disambiguationData":[OSD([sQuery(id+"F0.wireOp",EDGE,"E0"),sQuery(id+"F0.wireOp",EDGE,"E1"),sQuery(id+"F0.wireOp",EDGE,"E2"),sQuery(id+"F0.wireOp",EDGE,"E4"),sQuery(id+"F0.wireOp",EDGE,"E5"),sQuery(id+"F0.wireOp",EDGE,"E6.1.1"),sQuery(id+"F0.wireOp",EDGE,"E6.1.2"),sQuery(id+"F0.wireOp",EDGE,"E6.1.3"),sQuery(id+"F0.wireOp",EDGE,"E6.1.4"),sQuery(id+"F0.wireOp",EDGE,"E6.2.1"),sQuery(id+"F0.wireOp",EDGE,"E6.2.2"),sQuery(id+"F0.wireOp",EDGE,"E6.2.3"),sQuery(id+"F0.wireOp",EDGE,"E6.2.4"),sQuery(id+"F0.wireOp",EDGE,"E6.3.1"),sQuery(id+"F0.wireOp",EDGE,"E6.3.2"),sQuery(id+"F0.wireOp",EDGE,"E6.3.3"),sQuery(id+"F0.wireOp",EDGE,"E6.3.4"),sQuery(id+"F0.wireOp",EDGE,"E6.4.1"),sQuery(id+"F0.wireOp",EDGE,"E6.4.2"),sQuery(id+"F0.wireOp",EDGE,"E6.4.3"),sQuery(id+"F0.wireOp",EDGE,"E6.4.4"),sQuery(id+"F0.wireOp",EDGE,"E6.5.1"),sQuery(id+"F0.wireOp",EDGE,"E6.5.2"),sQuery(id+"F0.wireOp",EDGE,"E6.5.3"),sQuery(id+"F0.wireOp",EDGE,"E6.5.4"),sQuery(id+"F0.wireOp",EDGE,"E6.6.1"),sQuery(id+"F0.wireOp",EDGE,"E6.6.2"),sQuery(id+"F0.wireOp",EDGE,"E6.6.3"),sQuery(id+"F0.wireOp",EDGE,"E6.6.4"),sQuery(id+"F0.wireOp",EDGE,"E6.7.1"),sQuery(id+"F0.wireOp",EDGE,"E6.7.2"),sQuery(id+"F0.wireOp",EDGE,"E6.7.3"),sQuery(id+"F0.wireOp",EDGE,"E6.7.4"),sQuery(id+"F0.wireOp",EDGE,"E6.8.1"),sQuery(id+"F0.wireOp",EDGE,"E6.8.2"),sQuery(id+"F0.wireOp",EDGE,"E6.8.3"),sQuery(id+"F0.wireOp",EDGE,"E6.8.4"),sQuery(id+"F0.wireOp",EDGE,"E6.9.1"),sQuery(id+"F0.wireOp",EDGE,"E6.9.2"),sQuery(id+"F0.wireOp",EDGE,"E6.9.3"),sQuery(id+"F0.wireOp",EDGE,"E6.9.4"),sQuery(id+"F0.wireOp",EDGE,"E6.10.1"),sQuery(id+"F0.wireOp",EDGE,"E6.10.2"),sQuery(id+"F0.wireOp",EDGE,"E6.10.3"),sQuery(id+"F0.wireOp",EDGE,"E6.10.4"),sQuery(id+"F0.wireOp",EDGE,"E6.11.1"),sQuery(id+"F0.wireOp",EDGE,"E6.11.2"),sQuery(id+"F0.wireOp",EDGE,"E6.11.3"),sQuery(id+"F0.wireOp",EDGE,"E6.11.4"),sQuery(id+"F0.wireOp",EDGE,"E6.12.1"),sQuery(id+"F0.wireOp",EDGE,"E6.12.2"),sQuery(id+"F0.wireOp",EDGE,"E6.12.3"),sQuery(id+"F0.wireOp",EDGE,"E6.12.4"),sQuery(id+"F0.wireOp",EDGE,"E6.13.1"),sQuery(id+"F0.wireOp",EDGE,"E6.13.2"),sQuery(id+"F0.wireOp",EDGE,"E6.13.3"),sQuery(id+"F0.wireOp",EDGE,"E6.13.4"),sQuery(id+"F0.wireOp",EDGE,"E6.14.1"),sQuery(id+"F0.wireOp",EDGE,"E6.14.2"),sQuery(id+"F0.wireOp",EDGE,"E6.14.3"),sQuery(id+"F0.wireOp",EDGE,"E6.14.4"),sQuery(id+"F0.wireOp",EDGE,"E6.15.1"),sQuery(id+"F0.wireOp",EDGE,"E6.15.2"),sQuery(id+"F0.wireOp",EDGE,"E6.15.3"),sQuery(id+"F0.wireOp",EDGE,"E6.15.4"),sQuery(id+"F0.wireOp",EDGE,"E6.16.1"),sQuery(id+"F0.wireOp",EDGE,"E6.16.2"),sQuery(id+"F0.wireOp",EDGE,"E6.16.3"),sQuery(id+"F0.wireOp",EDGE,"E6.16.4"),sQuery(id+"F0.wireOp",EDGE,"E6.17.1"),sQuery(id+"F0.wireOp",EDGE,"E6.17.2"),sQuery(id+"F0.wireOp",EDGE,"E6.17.3"),sQuery(id+"F0.wireOp",EDGE,"E6.17.4"),sQuery(id+"F0.wireOp",EDGE,"E6.18.1"),sQuery(id+"F0.wireOp",EDGE,"E6.18.2"),sQuery(id+"F0.wireOp",EDGE,"E6.18.3"),sQuery(id+"F0.wireOp",EDGE,"E6.18.4"),sQuery(id+"F0.wireOp",EDGE,"E6.19.1"),sQuery(id+"F0.wireOp",EDGE,"E6.19.2"),sQuery(id+"F0.wireOp",EDGE,"E6.19.3"),sQuery(id+"F0.wireOp",EDGE,"E6.19.4"),sQuery(id+"F0.wireOp",EDGE,"E6.20.1"),sQuery(id+"F0.wireOp",EDGE,"E6.20.2"),sQuery(id+"F0.wireOp",EDGE,"E6.20.3"),sQuery(id+"F0.wireOp",EDGE,"E6.20.4"),sQuery(id+"F0.wireOp",EDGE,"E6.21.1"),sQuery(id+"F0.wireOp",EDGE,"E6.21.2"),sQuery(id+"F0.wireOp",EDGE,"E6.21.3"),sQuery(id+"F0.wireOp",EDGE,"E6.21.4"),sQuery(id+"F0.wireOp",EDGE,"E6.22.1"),sQuery(id+"F0.wireOp",EDGE,"E6.22.2"),sQuery(id+"F0.wireOp",EDGE,"E6.22.3"),sQuery(id+"F0.wireOp",EDGE,"E6.22.4"),sQuery(id+"F0.wireOp",EDGE,"E6.23.1"),sQuery(id+"F0.wireOp",EDGE,"E6.23.2"),sQuery(id+"F0.wireOp",EDGE,"E6.23.3"),sQuery(id+"F0.wireOp",EDGE,"E6.23.4"),sQuery(id+"F0.wireOp",EDGE,"E6.24.1"),sQuery(id+"F0.wireOp",EDGE,"E6.24.2"),sQuery(id+"F0.wireOp",EDGE,"E6.24.3"),sQuery(id+"F0.wireOp",EDGE,"E6.24.4"),sQuery(id+"F0.wireOp",EDGE,"E6.25.1"),sQuery(id+"F0.wireOp",EDGE,"E6.25.2"),sQuery(id+"F0.wireOp",EDGE,"E6.25.3"),sQuery(id+"F0.wireOp",EDGE,"E6.25.4"),sQuery(id+"F0.wireOp",EDGE,"E6.26.1"),sQuery(id+"F0.wireOp",EDGE,"E6.26.2"),sQuery(id+"F0.wireOp",EDGE,"E6.26.3"),sQuery(id+"F0.wireOp",EDGE,"E6.26.4"),subQ1,sQuery(id+"F0.wireOp",EDGE,"E6.27.2"),subQ0,sQuery(id+"F0.wireOp",EDGE,"E6.27.4"),sQuery(id+"F0.wireOp",EDGE,"E6.28.1"),sQuery(id+"F0.wireOp",EDGE,"E6.28.2"),sQuery(id+"F0.wireOp",EDGE,"E6.28.3"),sQuery(id+"F0.wireOp",EDGE,"E6.28.4"),sQuery(id+"F0.wireOp",EDGE,"E6.29.1"),sQuery(id+"F0.wireOp",EDGE,"E6.29.2"),sQuery(id+"F0.wireOp",EDGE,"E6.29.3"),sQuery(id+"F0.wireOp",EDGE,"E6.29.4"),sQuery(id+"F0.wireOp",EDGE,"E6.30.1"),sQuery(id+"F0.wireOp",EDGE,"E6.30.2"),sQuery(id+"F0.wireOp",EDGE,"E6.30.3"),sQuery(id+"F0.wireOp",EDGE,"E6.30.4"),sQuery(id+"F0.wireOp",EDGE,"E6.31.1"),sQuery(id+"F0.wireOp",EDGE,"E6.31.2"),sQuery(id+"F0.wireOp",EDGE,"E6.31.3"),sQuery(id+"F0.wireOp",EDGE,"E6.31.4"),sQuery(id+"F0.wireOp",EDGE,"E6.32.1"),sQuery(id+"F0.wireOp",EDGE,"E6.32.2"),sQuery(id+"F0.wireOp",EDGE,"E6.32.3"),sQuery(id+"F0.wireOp",EDGE,"E6.32.4"),sQuery(id+"F0.wireOp",EDGE,"E6.33.1"),sQuery(id+"F0.wireOp",EDGE,"E6.33.2"),sQuery(id+"F0.wireOp",EDGE,"E6.33.3"),sQuery(id+"F0.wireOp",EDGE,"E6.33.4"),sQuery(id+"F0.wireOp",EDGE,"E6.34.1"),sQuery(id+"F0.wireOp",EDGE,"E6.34.2"),sQuery(id+"F0.wireOp",EDGE,"E6.34.3"),sQuery(id+"F0.wireOp",EDGE,"E6.34.4"),sQuery(id+"F0.wireOp",EDGE,"E6.35.1"),sQuery(id+"F0.wireOp",EDGE,"E6.35.2"),sQuery(id+"F0.wireOp",EDGE,"E6.35.3"),sQuery(id+"F0.wireOp",EDGE,"E6.35.4"),sQuery(id+"F0.wireOp",EDGE,"E6.36.1"),sQuery(id+"F0.wireOp",EDGE,"E6.36.2"),sQuery(id+"F0.wireOp",EDGE,"E6.36.3"),sQuery(id+"F0.wireOp",EDGE,"E6.36.4"),sQuery(id+"F0.wireOp",EDGE,"E6.37.1"),sQuery(id+"F0.wireOp",EDGE,"E6.37.2"),sQuery(id+"F0.wireOp",EDGE,"E6.37.3"),sQuery(id+"F0.wireOp",EDGE,"E6.37.4"),sQuery(id+"F0.wireOp",EDGE,"E6.38.1"),sQuery(id+"F0.wireOp",EDGE,"E6.38.2"),sQuery(id+"F0.wireOp",EDGE,"E6.38.3"),sQuery(id+"F0.wireOp",EDGE,"E6.38.4"),sQuery(id+"F0.wireOp",EDGE,"E6.39.1"),sQuery(id+"F0.wireOp",EDGE,"E6.39.2"),sQuery(id+"F0.wireOp",EDGE,"E6.39.3"),sQuery(id+"F0.wireOp",EDGE,"E6.39.4"),sQuery(id+"F0.wireOp",EDGE,"E6.40.1"),sQuery(id+"F0.wireOp",EDGE,"E6.40.2"),sQuery(id+"F0.wireOp",EDGE,"E6.40.3"),sQuery(id+"F0.wireOp",EDGE,"E6.40.4"),sQuery(id+"F0.wireOp",EDGE,"E6.41.1"),sQuery(id+"F0.wireOp",EDGE,"E6.41.2"),sQuery(id+"F0.wireOp",EDGE,"E6.41.3"),sQuery(id+"F0.wireOp",EDGE,"E6.41.4"),sQuery(id+"F0.wireOp",EDGE,"E6.42.1"),sQuery(id+"F0.wireOp",EDGE,"E6.42.2"),sQuery(id+"F0.wireOp",EDGE,"E6.42.3"),sQuery(id+"F0.wireOp",EDGE,"E6.42.4"),sQuery(id+"F0.wireOp",EDGE,"E6.43.1"),sQuery(id+"F0.wireOp",EDGE,"E6.43.2"),sQuery(id+"F0.wireOp",EDGE,"E6.43.3"),sQuery(id+"F0.wireOp",EDGE,"E6.43.4"),sQuery(id+"F0.wireOp",EDGE,"E7"),sQuery(id+"F0.wireOp",EDGE,"E8.1.0"),sQuery(id+"F0.wireOp",EDGE,"E8.2.0"),sQuery(id+"F0.wireOp",EDGE,"E8.3.0"),sQuery(id+"F0.wireOp",EDGE,"E8.4.0"),sQuery(id+"F0.wireOp",EDGE,"E8.5.0"),sQuery(id+"F0.wireOp",EDGE,"E8.6.0"),sQuery(id+"F0.wireOp",EDGE,"E8.7.0"),sQuery(id+"F0.wireOp",EDGE,"E8.8.0"),sQuery(id+"F0.wireOp",EDGE,"E8.9.0"),sQuery(id+"F0.wireOp",EDGE,"E8.10.0"),sQuery(id+"F0.wireOp",EDGE,"E8.11.0"),sQuery(id+"F0.wireOp",EDGE,"E8.12.0"),sQuery(id+"F0.wireOp",EDGE,"E8.13.0"),sQuery(id+"F0.wireOp",EDGE,"E8.14.0"),sQuery(id+"F0.wireOp",EDGE,"E8.15.0"),sQuery(id+"F0.wireOp",EDGE,"E8.16.0"),sQuery(id+"F0.wireOp",EDGE,"E8.17.0"),sQuery(id+"F0.wireOp",EDGE,"E8.18.0"),sQuery(id+"F0.wireOp",EDGE,"E8.19.0"),sQuery(id+"F0.wireOp",EDGE,"E8.20.0"),sQuery(id+"F0.wireOp",EDGE,"E8.21.0"),sQuery(id+"F0.wireOp",EDGE,"E8.22.0"),sQuery(id+"F0.wireOp",EDGE,"E8.23.0"),sQuery(id+"F0.wireOp",EDGE,"E8.24.0"),sQuery(id+"F0.wireOp",EDGE,"E8.25.0"),sQuery(id+"F0.wireOp",EDGE,"E8.26.0"),sQuery(id+"F0.wireOp",EDGE,"E8.27.0"),sQuery(id+"F0.wireOp",EDGE,"E8.28.0"),sQuery(id+"F0.wireOp",EDGE,"E8.29.0"),sQuery(id+"F0.wireOp",EDGE,"E8.30.0"),sQuery(id+"F0.wireOp",EDGE,"E8.31.0"),sQuery(id+"F0.wireOp",EDGE,"E8.32.0"),sQuery(id+"F0.wireOp",EDGE,"E8.33.0"),sQuery(id+"F0.wireOp",EDGE,"E8.34.0"),sQuery(id+"F0.wireOp",EDGE,"E8.35.0"),sQuery(id+"F0.wireOp",EDGE,"E8.36.0"),sQuery(id+"F0.wireOp",EDGE,"E8.37.0"),sQuery(id+"F0.wireOp",EDGE,"E8.38.0"),sQuery(id+"F0.wireOp",EDGE,"E8.39.0"),sQuery(id+"F0.wireOp",EDGE,"E8.40.0"),sQuery(id+"F0.wireOp",EDGE,"E8.41.0"),sQuery(id+"F0.wireOp",EDGE,"E8.42.0"),sQuery(id+"F0.wireOp",EDGE,"E8.43.0")])],"isStart":false})]});}
            var Q3;
            {var subQ0=sQuery(id+"F0.wireOp",EDGE,"E6.29.3");var subQ1=sQuery(id+"F0.wireOp",EDGE,"E6.29.1");Q3=makeQuery(id+"F2.opFillet","BLEND_EDGE",EDGE,{"blendedFrom":[makeQuery(id+"F1.opExtrude","SWEPT_EDGE",EDGE,{"disambiguationData":[OSD([sQuery(id+"F0.wireOp",EDGE,"E6.29.0"),subQ1,subQ0])]}),makeQuery(id+"F1.opExtrude","CAP_FACE",FACE,{"disambiguationData":[OSD([sQuery(id+"F0.wireOp",EDGE,"E0"),sQuery(id+"F0.wireOp",EDGE,"E1"),sQuery(id+"F0.wireOp",EDGE,"E2"),sQuery(id+"F0.wireOp",EDGE,"E4"),sQuery(id+"F0.wireOp",EDGE,"E5"),sQuery(id+"F0.wireOp",EDGE,"E6.1.1"),sQuery(id+"F0.wireOp",EDGE,"E6.1.2"),sQuery(id+"F0.wireOp",EDGE,"E6.1.3"),sQuery(id+"F0.wireOp",EDGE,"E6.1.4"),sQuery(id+"F0.wireOp",EDGE,"E6.2.1"),sQuery(id+"F0.wireOp",EDGE,"E6.2.2"),sQuery(id+"F0.wireOp",EDGE,"E6.2.3"),sQuery(id+"F0.wireOp",EDGE,"E6.2.4"),sQuery(id+"F0.wireOp",EDGE,"E6.3.1"),sQuery(id+"F0.wireOp",EDGE,"E6.3.2"),sQuery(id+"F0.wireOp",EDGE,"E6.3.3"),sQuery(id+"F0.wireOp",EDGE,"E6.3.4"),sQuery(id+"F0.wireOp",EDGE,"E6.4.1"),sQuery(id+"F0.wireOp",EDGE,"E6.4.2"),sQuery(id+"F0.wireOp",EDGE,"E6.4.3"),sQuery(id+"F0.wireOp",EDGE,"E6.4.4"),sQuery(id+"F0.wireOp",EDGE,"E6.5.1"),sQuery(id+"F0.wireOp",EDGE,"E6.5.2"),sQuery(id+"F0.wireOp",EDGE,"E6.5.3"),sQuery(id+"F0.wireOp",EDGE,"E6.5.4"),sQuery(id+"F0.wireOp",EDGE,"E6.6.1"),sQuery(id+"F0.wireOp",EDGE,"E6.6.2"),sQuery(id+"F0.wireOp",EDGE,"E6.6.3"),sQuery(id+"F0.wireOp",EDGE,"E6.6.4"),sQuery(id+"F0.wireOp",EDGE,"E6.7.1"),sQuery(id+"F0.wireOp",EDGE,"E6.7.2"),sQuery(id+"F0.wireOp",EDGE,"E6.7.3"),sQuery(id+"F0.wireOp",EDGE,"E6.7.4"),sQuery(id+"F0.wireOp",EDGE,"E6.8.1"),sQuery(id+"F0.wireOp",EDGE,"E6.8.2"),sQuery(id+"F0.wireOp",EDGE,"E6.8.3"),sQuery(id+"F0.wireOp",EDGE,"E6.8.4"),sQuery(id+"F0.wireOp",EDGE,"E6.9.1"),sQuery(id+"F0.wireOp",EDGE,"E6.9.2"),sQuery(id+"F0.wireOp",EDGE,"E6.9.3"),sQuery(id+"F0.wireOp",EDGE,"E6.9.4"),sQuery(id+"F0.wireOp",EDGE,"E6.10.1"),sQuery(id+"F0.wireOp",EDGE,"E6.10.2"),sQuery(id+"F0.wireOp",EDGE,"E6.10.3"),sQuery(id+"F0.wireOp",EDGE,"E6.10.4"),sQuery(id+"F0.wireOp",EDGE,"E6.11.1"),sQuery(id+"F0.wireOp",EDGE,"E6.11.2"),sQuery(id+"F0.wireOp",EDGE,"E6.11.3"),sQuery(id+"F0.wireOp",EDGE,"E6.11.4"),sQuery(id+"F0.wireOp",EDGE,"E6.12.1"),sQuery(id+"F0.wireOp",EDGE,"E6.12.2"),sQuery(id+"F0.wireOp",EDGE,"E6.12.3"),sQuery(id+"F0.wireOp",EDGE,"E6.12.4"),sQuery(id+"F0.wireOp",EDGE,"E6.13.1"),sQuery(id+"F0.wireOp",EDGE,"E6.13.2"),sQuery(id+"F0.wireOp",EDGE,"E6.13.3"),sQuery(id+"F0.wireOp",EDGE,"E6.13.4"),sQuery(id+"F0.wireOp",EDGE,"E6.14.1"),sQuery(id+"F0.wireOp",EDGE,"E6.14.2"),sQuery(id+"F0.wireOp",EDGE,"E6.14.3"),sQuery(id+"F0.wireOp",EDGE,"E6.14.4"),sQuery(id+"F0.wireOp",EDGE,"E6.15.1"),sQuery(id+"F0.wireOp",EDGE,"E6.15.2"),sQuery(id+"F0.wireOp",EDGE,"E6.15.3"),sQuery(id+"F0.wireOp",EDGE,"E6.15.4"),sQuery(id+"F0.wireOp",EDGE,"E6.16.1"),sQuery(id+"F0.wireOp",EDGE,"E6.16.2"),sQuery(id+"F0.wireOp",EDGE,"E6.16.3"),sQuery(id+"F0.wireOp",EDGE,"E6.16.4"),sQuery(id+"F0.wireOp",EDGE,"E6.17.1"),sQuery(id+"F0.wireOp",EDGE,"E6.17.2"),sQuery(id+"F0.wireOp",EDGE,"E6.17.3"),sQuery(id+"F0.wireOp",EDGE,"E6.17.4"),sQuery(id+"F0.wireOp",EDGE,"E6.18.1"),sQuery(id+"F0.wireOp",EDGE,"E6.18.2"),sQuery(id+"F0.wireOp",EDGE,"E6.18.3"),sQuery(id+"F0.wireOp",EDGE,"E6.18.4"),sQuery(id+"F0.wireOp",EDGE,"E6.19.1"),sQuery(id+"F0.wireOp",EDGE,"E6.19.2"),sQuery(id+"F0.wireOp",EDGE,"E6.19.3"),sQuery(id+"F0.wireOp",EDGE,"E6.19.4"),sQuery(id+"F0.wireOp",EDGE,"E6.20.1"),sQuery(id+"F0.wireOp",EDGE,"E6.20.2"),sQuery(id+"F0.wireOp",EDGE,"E6.20.3"),sQuery(id+"F0.wireOp",EDGE,"E6.20.4"),sQuery(id+"F0.wireOp",EDGE,"E6.21.1"),sQuery(id+"F0.wireOp",EDGE,"E6.21.2"),sQuery(id+"F0.wireOp",EDGE,"E6.21.3"),sQuery(id+"F0.wireOp",EDGE,"E6.21.4"),sQuery(id+"F0.wireOp",EDGE,"E6.22.1"),sQuery(id+"F0.wireOp",EDGE,"E6.22.2"),sQuery(id+"F0.wireOp",EDGE,"E6.22.3"),sQuery(id+"F0.wireOp",EDGE,"E6.22.4"),sQuery(id+"F0.wireOp",EDGE,"E6.23.1"),sQuery(id+"F0.wireOp",EDGE,"E6.23.2"),sQuery(id+"F0.wireOp",EDGE,"E6.23.3"),sQuery(id+"F0.wireOp",EDGE,"E6.23.4"),sQuery(id+"F0.wireOp",EDGE,"E6.24.1"),sQuery(id+"F0.wireOp",EDGE,"E6.24.2"),sQuery(id+"F0.wireOp",EDGE,"E6.24.3"),sQuery(id+"F0.wireOp",EDGE,"E6.24.4"),sQuery(id+"F0.wireOp",EDGE,"E6.25.1"),sQuery(id+"F0.wireOp",EDGE,"E6.25.2"),sQuery(id+"F0.wireOp",EDGE,"E6.25.3"),sQuery(id+"F0.wireOp",EDGE,"E6.25.4"),sQuery(id+"F0.wireOp",EDGE,"E6.26.1"),sQuery(id+"F0.wireOp",EDGE,"E6.26.2"),sQuery(id+"F0.wireOp",EDGE,"E6.26.3"),sQuery(id+"F0.wireOp",EDGE,"E6.26.4"),sQuery(id+"F0.wireOp",EDGE,"E6.27.1"),sQuery(id+"F0.wireOp",EDGE,"E6.27.2"),sQuery(id+"F0.wireOp",EDGE,"E6.27.3"),sQuery(id+"F0.wireOp",EDGE,"E6.27.4"),sQuery(id+"F0.wireOp",EDGE,"E6.28.1"),sQuery(id+"F0.wireOp",EDGE,"E6.28.2"),sQuery(id+"F0.wireOp",EDGE,"E6.28.3"),sQuery(id+"F0.wireOp",EDGE,"E6.28.4"),subQ1,sQuery(id+"F0.wireOp",EDGE,"E6.29.2"),subQ0,sQuery(id+"F0.wireOp",EDGE,"E6.29.4"),sQuery(id+"F0.wireOp",EDGE,"E6.30.1"),sQuery(id+"F0.wireOp",EDGE,"E6.30.2"),sQuery(id+"F0.wireOp",EDGE,"E6.30.3"),sQuery(id+"F0.wireOp",EDGE,"E6.30.4"),sQuery(id+"F0.wireOp",EDGE,"E6.31.1"),sQuery(id+"F0.wireOp",EDGE,"E6.31.2"),sQuery(id+"F0.wireOp",EDGE,"E6.31.3"),sQuery(id+"F0.wireOp",EDGE,"E6.31.4"),sQuery(id+"F0.wireOp",EDGE,"E6.32.1"),sQuery(id+"F0.wireOp",EDGE,"E6.32.2"),sQuery(id+"F0.wireOp",EDGE,"E6.32.3"),sQuery(id+"F0.wireOp",EDGE,"E6.32.4"),sQuery(id+"F0.wireOp",EDGE,"E6.33.1"),sQuery(id+"F0.wireOp",EDGE,"E6.33.2"),sQuery(id+"F0.wireOp",EDGE,"E6.33.3"),sQuery(id+"F0.wireOp",EDGE,"E6.33.4"),sQuery(id+"F0.wireOp",EDGE,"E6.34.1"),sQuery(id+"F0.wireOp",EDGE,"E6.34.2"),sQuery(id+"F0.wireOp",EDGE,"E6.34.3"),sQuery(id+"F0.wireOp",EDGE,"E6.34.4"),sQuery(id+"F0.wireOp",EDGE,"E6.35.1"),sQuery(id+"F0.wireOp",EDGE,"E6.35.2"),sQuery(id+"F0.wireOp",EDGE,"E6.35.3"),sQuery(id+"F0.wireOp",EDGE,"E6.35.4"),sQuery(id+"F0.wireOp",EDGE,"E6.36.1"),sQuery(id+"F0.wireOp",EDGE,"E6.36.2"),sQuery(id+"F0.wireOp",EDGE,"E6.36.3"),sQuery(id+"F0.wireOp",EDGE,"E6.36.4"),sQuery(id+"F0.wireOp",EDGE,"E6.37.1"),sQuery(id+"F0.wireOp",EDGE,"E6.37.2"),sQuery(id+"F0.wireOp",EDGE,"E6.37.3"),sQuery(id+"F0.wireOp",EDGE,"E6.37.4"),sQuery(id+"F0.wireOp",EDGE,"E6.38.1"),sQuery(id+"F0.wireOp",EDGE,"E6.38.2"),sQuery(id+"F0.wireOp",EDGE,"E6.38.3"),sQuery(id+"F0.wireOp",EDGE,"E6.38.4"),sQuery(id+"F0.wireOp",EDGE,"E6.39.1"),sQuery(id+"F0.wireOp",EDGE,"E6.39.2"),sQuery(id+"F0.wireOp",EDGE,"E6.39.3"),sQuery(id+"F0.wireOp",EDGE,"E6.39.4"),sQuery(id+"F0.wireOp",EDGE,"E6.40.1"),sQuery(id+"F0.wireOp",EDGE,"E6.40.2"),sQuery(id+"F0.wireOp",EDGE,"E6.40.3"),sQuery(id+"F0.wireOp",EDGE,"E6.40.4"),sQuery(id+"F0.wireOp",EDGE,"E6.41.1"),sQuery(id+"F0.wireOp",EDGE,"E6.41.2"),sQuery(id+"F0.wireOp",EDGE,"E6.41.3"),sQuery(id+"F0.wireOp",EDGE,"E6.41.4"),sQuery(id+"F0.wireOp",EDGE,"E6.42.1"),sQuery(id+"F0.wireOp",EDGE,"E6.42.2"),sQuery(id+"F0.wireOp",EDGE,"E6.42.3"),sQuery(id+"F0.wireOp",EDGE,"E6.42.4"),sQuery(id+"F0.wireOp",EDGE,"E6.43.1"),sQuery(id+"F0.wireOp",EDGE,"E6.43.2"),sQuery(id+"F0.wireOp",EDGE,"E6.43.3"),sQuery(id+"F0.wireOp",EDGE,"E6.43.4"),sQuery(id+"F0.wireOp",EDGE,"E7"),sQuery(id+"F0.wireOp",EDGE,"E8.1.0"),sQuery(id+"F0.wireOp",EDGE,"E8.2.0"),sQuery(id+"F0.wireOp",EDGE,"E8.3.0"),sQuery(id+"F0.wireOp",EDGE,"E8.4.0"),sQuery(id+"F0.wireOp",EDGE,"E8.5.0"),sQuery(id+"F0.wireOp",EDGE,"E8.6.0"),sQuery(id+"F0.wireOp",EDGE,"E8.7.0"),sQuery(id+"F0.wireOp",EDGE,"E8.8.0"),sQuery(id+"F0.wireOp",EDGE,"E8.9.0"),sQuery(id+"F0.wireOp",EDGE,"E8.10.0"),sQuery(id+"F0.wireOp",EDGE,"E8.11.0"),sQuery(id+"F0.wireOp",EDGE,"E8.12.0"),sQuery(id+"F0.wireOp",EDGE,"E8.13.0"),sQuery(id+"F0.wireOp",EDGE,"E8.14.0"),sQuery(id+"F0.wireOp",EDGE,"E8.15.0"),sQuery(id+"F0.wireOp",EDGE,"E8.16.0"),sQuery(id+"F0.wireOp",EDGE,"E8.17.0"),sQuery(id+"F0.wireOp",EDGE,"E8.18.0"),sQuery(id+"F0.wireOp",EDGE,"E8.19.0"),sQuery(id+"F0.wireOp",EDGE,"E8.20.0"),sQuery(id+"F0.wireOp",EDGE,"E8.21.0"),sQuery(id+"F0.wireOp",EDGE,"E8.22.0"),sQuery(id+"F0.wireOp",EDGE,"E8.23.0"),sQuery(id+"F0.wireOp",EDGE,"E8.24.0"),sQuery(id+"F0.wireOp",EDGE,"E8.25.0"),sQuery(id+"F0.wireOp",EDGE,"E8.26.0"),sQuery(id+"F0.wireOp",EDGE,"E8.27.0"),sQuery(id+"F0.wireOp",EDGE,"E8.28.0"),sQuery(id+"F0.wireOp",EDGE,"E8.29.0"),sQuery(id+"F0.wireOp",EDGE,"E8.30.0"),sQuery(id+"F0.wireOp",EDGE,"E8.31.0"),sQuery(id+"F0.wireOp",EDGE,"E8.32.0"),sQuery(id+"F0.wireOp",EDGE,"E8.33.0"),sQuery(id+"F0.wireOp",EDGE,"E8.34.0"),sQuery(id+"F0.wireOp",EDGE,"E8.35.0"),sQuery(id+"F0.wireOp",EDGE,"E8.36.0"),sQuery(id+"F0.wireOp",EDGE,"E8.37.0"),sQuery(id+"F0.wireOp",EDGE,"E8.38.0"),sQuery(id+"F0.wireOp",EDGE,"E8.39.0"),sQuery(id+"F0.wireOp",EDGE,"E8.40.0"),sQuery(id+"F0.wireOp",EDGE,"E8.41.0"),sQuery(id+"F0.wireOp",EDGE,"E8.42.0"),sQuery(id+"F0.wireOp",EDGE,"E8.43.0")])],"isStart":false})],"blendedInto":[makeQuery(id+"F1.opExtrude","CAP_FACE",FACE,{"disambiguationData":[OSD([sQuery(id+"F0.wireOp",EDGE,"E0"),sQuery(id+"F0.wireOp",EDGE,"E1"),sQuery(id+"F0.wireOp",EDGE,"E2"),sQuery(id+"F0.wireOp",EDGE,"E4"),sQuery(id+"F0.wireOp",EDGE,"E5"),sQuery(id+"F0.wireOp",EDGE,"E6.1.1"),sQuery(id+"F0.wireOp",EDGE,"E6.1.2"),sQuery(id+"F0.wireOp",EDGE,"E6.1.3"),sQuery(id+"F0.wireOp",EDGE,"E6.1.4"),sQuery(id+"F0.wireOp",EDGE,"E6.2.1"),sQuery(id+"F0.wireOp",EDGE,"E6.2.2"),sQuery(id+"F0.wireOp",EDGE,"E6.2.3"),sQuery(id+"F0.wireOp",EDGE,"E6.2.4"),sQuery(id+"F0.wireOp",EDGE,"E6.3.1"),sQuery(id+"F0.wireOp",EDGE,"E6.3.2"),sQuery(id+"F0.wireOp",EDGE,"E6.3.3"),sQuery(id+"F0.wireOp",EDGE,"E6.3.4"),sQuery(id+"F0.wireOp",EDGE,"E6.4.1"),sQuery(id+"F0.wireOp",EDGE,"E6.4.2"),sQuery(id+"F0.wireOp",EDGE,"E6.4.3"),sQuery(id+"F0.wireOp",EDGE,"E6.4.4"),sQuery(id+"F0.wireOp",EDGE,"E6.5.1"),sQuery(id+"F0.wireOp",EDGE,"E6.5.2"),sQuery(id+"F0.wireOp",EDGE,"E6.5.3"),sQuery(id+"F0.wireOp",EDGE,"E6.5.4"),sQuery(id+"F0.wireOp",EDGE,"E6.6.1"),sQuery(id+"F0.wireOp",EDGE,"E6.6.2"),sQuery(id+"F0.wireOp",EDGE,"E6.6.3"),sQuery(id+"F0.wireOp",EDGE,"E6.6.4"),sQuery(id+"F0.wireOp",EDGE,"E6.7.1"),sQuery(id+"F0.wireOp",EDGE,"E6.7.2"),sQuery(id+"F0.wireOp",EDGE,"E6.7.3"),sQuery(id+"F0.wireOp",EDGE,"E6.7.4"),sQuery(id+"F0.wireOp",EDGE,"E6.8.1"),sQuery(id+"F0.wireOp",EDGE,"E6.8.2"),sQuery(id+"F0.wireOp",EDGE,"E6.8.3"),sQuery(id+"F0.wireOp",EDGE,"E6.8.4"),sQuery(id+"F0.wireOp",EDGE,"E6.9.1"),sQuery(id+"F0.wireOp",EDGE,"E6.9.2"),sQuery(id+"F0.wireOp",EDGE,"E6.9.3"),sQuery(id+"F0.wireOp",EDGE,"E6.9.4"),sQuery(id+"F0.wireOp",EDGE,"E6.10.1"),sQuery(id+"F0.wireOp",EDGE,"E6.10.2"),sQuery(id+"F0.wireOp",EDGE,"E6.10.3"),sQuery(id+"F0.wireOp",EDGE,"E6.10.4"),sQuery(id+"F0.wireOp",EDGE,"E6.11.1"),sQuery(id+"F0.wireOp",EDGE,"E6.11.2"),sQuery(id+"F0.wireOp",EDGE,"E6.11.3"),sQuery(id+"F0.wireOp",EDGE,"E6.11.4"),sQuery(id+"F0.wireOp",EDGE,"E6.12.1"),sQuery(id+"F0.wireOp",EDGE,"E6.12.2"),sQuery(id+"F0.wireOp",EDGE,"E6.12.3"),sQuery(id+"F0.wireOp",EDGE,"E6.12.4"),sQuery(id+"F0.wireOp",EDGE,"E6.13.1"),sQuery(id+"F0.wireOp",EDGE,"E6.13.2"),sQuery(id+"F0.wireOp",EDGE,"E6.13.3"),sQuery(id+"F0.wireOp",EDGE,"E6.13.4"),sQuery(id+"F0.wireOp",EDGE,"E6.14.1"),sQuery(id+"F0.wireOp",EDGE,"E6.14.2"),sQuery(id+"F0.wireOp",EDGE,"E6.14.3"),sQuery(id+"F0.wireOp",EDGE,"E6.14.4"),sQuery(id+"F0.wireOp",EDGE,"E6.15.1"),sQuery(id+"F0.wireOp",EDGE,"E6.15.2"),sQuery(id+"F0.wireOp",EDGE,"E6.15.3"),sQuery(id+"F0.wireOp",EDGE,"E6.15.4"),sQuery(id+"F0.wireOp",EDGE,"E6.16.1"),sQuery(id+"F0.wireOp",EDGE,"E6.16.2"),sQuery(id+"F0.wireOp",EDGE,"E6.16.3"),sQuery(id+"F0.wireOp",EDGE,"E6.16.4"),sQuery(id+"F0.wireOp",EDGE,"E6.17.1"),sQuery(id+"F0.wireOp",EDGE,"E6.17.2"),sQuery(id+"F0.wireOp",EDGE,"E6.17.3"),sQuery(id+"F0.wireOp",EDGE,"E6.17.4"),sQuery(id+"F0.wireOp",EDGE,"E6.18.1"),sQuery(id+"F0.wireOp",EDGE,"E6.18.2"),sQuery(id+"F0.wireOp",EDGE,"E6.18.3"),sQuery(id+"F0.wireOp",EDGE,"E6.18.4"),sQuery(id+"F0.wireOp",EDGE,"E6.19.1"),sQuery(id+"F0.wireOp",EDGE,"E6.19.2"),sQuery(id+"F0.wireOp",EDGE,"E6.19.3"),sQuery(id+"F0.wireOp",EDGE,"E6.19.4"),sQuery(id+"F0.wireOp",EDGE,"E6.20.1"),sQuery(id+"F0.wireOp",EDGE,"E6.20.2"),sQuery(id+"F0.wireOp",EDGE,"E6.20.3"),sQuery(id+"F0.wireOp",EDGE,"E6.20.4"),sQuery(id+"F0.wireOp",EDGE,"E6.21.1"),sQuery(id+"F0.wireOp",EDGE,"E6.21.2"),sQuery(id+"F0.wireOp",EDGE,"E6.21.3"),sQuery(id+"F0.wireOp",EDGE,"E6.21.4"),sQuery(id+"F0.wireOp",EDGE,"E6.22.1"),sQuery(id+"F0.wireOp",EDGE,"E6.22.2"),sQuery(id+"F0.wireOp",EDGE,"E6.22.3"),sQuery(id+"F0.wireOp",EDGE,"E6.22.4"),sQuery(id+"F0.wireOp",EDGE,"E6.23.1"),sQuery(id+"F0.wireOp",EDGE,"E6.23.2"),sQuery(id+"F0.wireOp",EDGE,"E6.23.3"),sQuery(id+"F0.wireOp",EDGE,"E6.23.4"),sQuery(id+"F0.wireOp",EDGE,"E6.24.1"),sQuery(id+"F0.wireOp",EDGE,"E6.24.2"),sQuery(id+"F0.wireOp",EDGE,"E6.24.3"),sQuery(id+"F0.wireOp",EDGE,"E6.24.4"),sQuery(id+"F0.wireOp",EDGE,"E6.25.1"),sQuery(id+"F0.wireOp",EDGE,"E6.25.2"),sQuery(id+"F0.wireOp",EDGE,"E6.25.3"),sQuery(id+"F0.wireOp",EDGE,"E6.25.4"),sQuery(id+"F0.wireOp",EDGE,"E6.26.1"),sQuery(id+"F0.wireOp",EDGE,"E6.26.2"),sQuery(id+"F0.wireOp",EDGE,"E6.26.3"),sQuery(id+"F0.wireOp",EDGE,"E6.26.4"),sQuery(id+"F0.wireOp",EDGE,"E6.27.1"),sQuery(id+"F0.wireOp",EDGE,"E6.27.2"),sQuery(id+"F0.wireOp",EDGE,"E6.27.3"),sQuery(id+"F0.wireOp",EDGE,"E6.27.4"),sQuery(id+"F0.wireOp",EDGE,"E6.28.1"),sQuery(id+"F0.wireOp",EDGE,"E6.28.2"),sQuery(id+"F0.wireOp",EDGE,"E6.28.3"),sQuery(id+"F0.wireOp",EDGE,"E6.28.4"),subQ1,sQuery(id+"F0.wireOp",EDGE,"E6.29.2"),subQ0,sQuery(id+"F0.wireOp",EDGE,"E6.29.4"),sQuery(id+"F0.wireOp",EDGE,"E6.30.1"),sQuery(id+"F0.wireOp",EDGE,"E6.30.2"),sQuery(id+"F0.wireOp",EDGE,"E6.30.3"),sQuery(id+"F0.wireOp",EDGE,"E6.30.4"),sQuery(id+"F0.wireOp",EDGE,"E6.31.1"),sQuery(id+"F0.wireOp",EDGE,"E6.31.2"),sQuery(id+"F0.wireOp",EDGE,"E6.31.3"),sQuery(id+"F0.wireOp",EDGE,"E6.31.4"),sQuery(id+"F0.wireOp",EDGE,"E6.32.1"),sQuery(id+"F0.wireOp",EDGE,"E6.32.2"),sQuery(id+"F0.wireOp",EDGE,"E6.32.3"),sQuery(id+"F0.wireOp",EDGE,"E6.32.4"),sQuery(id+"F0.wireOp",EDGE,"E6.33.1"),sQuery(id+"F0.wireOp",EDGE,"E6.33.2"),sQuery(id+"F0.wireOp",EDGE,"E6.33.3"),sQuery(id+"F0.wireOp",EDGE,"E6.33.4"),sQuery(id+"F0.wireOp",EDGE,"E6.34.1"),sQuery(id+"F0.wireOp",EDGE,"E6.34.2"),sQuery(id+"F0.wireOp",EDGE,"E6.34.3"),sQuery(id+"F0.wireOp",EDGE,"E6.34.4"),sQuery(id+"F0.wireOp",EDGE,"E6.35.1"),sQuery(id+"F0.wireOp",EDGE,"E6.35.2"),sQuery(id+"F0.wireOp",EDGE,"E6.35.3"),sQuery(id+"F0.wireOp",EDGE,"E6.35.4"),sQuery(id+"F0.wireOp",EDGE,"E6.36.1"),sQuery(id+"F0.wireOp",EDGE,"E6.36.2"),sQuery(id+"F0.wireOp",EDGE,"E6.36.3"),sQuery(id+"F0.wireOp",EDGE,"E6.36.4"),sQuery(id+"F0.wireOp",EDGE,"E6.37.1"),sQuery(id+"F0.wireOp",EDGE,"E6.37.2"),sQuery(id+"F0.wireOp",EDGE,"E6.37.3"),sQuery(id+"F0.wireOp",EDGE,"E6.37.4"),sQuery(id+"F0.wireOp",EDGE,"E6.38.1"),sQuery(id+"F0.wireOp",EDGE,"E6.38.2"),sQuery(id+"F0.wireOp",EDGE,"E6.38.3"),sQuery(id+"F0.wireOp",EDGE,"E6.38.4"),sQuery(id+"F0.wireOp",EDGE,"E6.39.1"),sQuery(id+"F0.wireOp",EDGE,"E6.39.2"),sQuery(id+"F0.wireOp",EDGE,"E6.39.3"),sQuery(id+"F0.wireOp",EDGE,"E6.39.4"),sQuery(id+"F0.wireOp",EDGE,"E6.40.1"),sQuery(id+"F0.wireOp",EDGE,"E6.40.2"),sQuery(id+"F0.wireOp",EDGE,"E6.40.3"),sQuery(id+"F0.wireOp",EDGE,"E6.40.4"),sQuery(id+"F0.wireOp",EDGE,"E6.41.1"),sQuery(id+"F0.wireOp",EDGE,"E6.41.2"),sQuery(id+"F0.wireOp",EDGE,"E6.41.3"),sQuery(id+"F0.wireOp",EDGE,"E6.41.4"),sQuery(id+"F0.wireOp",EDGE,"E6.42.1"),sQuery(id+"F0.wireOp",EDGE,"E6.42.2"),sQuery(id+"F0.wireOp",EDGE,"E6.42.3"),sQuery(id+"F0.wireOp",EDGE,"E6.42.4"),sQuery(id+"F0.wireOp",EDGE,"E6.43.1"),sQuery(id+"F0.wireOp",EDGE,"E6.43.2"),sQuery(id+"F0.wireOp",EDGE,"E6.43.3"),sQuery(id+"F0.wireOp",EDGE,"E6.43.4"),sQuery(id+"F0.wireOp",EDGE,"E7"),sQuery(id+"F0.wireOp",EDGE,"E8.1.0"),sQuery(id+"F0.wireOp",EDGE,"E8.2.0"),sQuery(id+"F0.wireOp",EDGE,"E8.3.0"),sQuery(id+"F0.wireOp",EDGE,"E8.4.0"),sQuery(id+"F0.wireOp",EDGE,"E8.5.0"),sQuery(id+"F0.wireOp",EDGE,"E8.6.0"),sQuery(id+"F0.wireOp",EDGE,"E8.7.0"),sQuery(id+"F0.wireOp",EDGE,"E8.8.0"),sQuery(id+"F0.wireOp",EDGE,"E8.9.0"),sQuery(id+"F0.wireOp",EDGE,"E8.10.0"),sQuery(id+"F0.wireOp",EDGE,"E8.11.0"),sQuery(id+"F0.wireOp",EDGE,"E8.12.0"),sQuery(id+"F0.wireOp",EDGE,"E8.13.0"),sQuery(id+"F0.wireOp",EDGE,"E8.14.0"),sQuery(id+"F0.wireOp",EDGE,"E8.15.0"),sQuery(id+"F0.wireOp",EDGE,"E8.16.0"),sQuery(id+"F0.wireOp",EDGE,"E8.17.0"),sQuery(id+"F0.wireOp",EDGE,"E8.18.0"),sQuery(id+"F0.wireOp",EDGE,"E8.19.0"),sQuery(id+"F0.wireOp",EDGE,"E8.20.0"),sQuery(id+"F0.wireOp",EDGE,"E8.21.0"),sQuery(id+"F0.wireOp",EDGE,"E8.22.0"),sQuery(id+"F0.wireOp",EDGE,"E8.23.0"),sQuery(id+"F0.wireOp",EDGE,"E8.24.0"),sQuery(id+"F0.wireOp",EDGE,"E8.25.0"),sQuery(id+"F0.wireOp",EDGE,"E8.26.0"),sQuery(id+"F0.wireOp",EDGE,"E8.27.0"),sQuery(id+"F0.wireOp",EDGE,"E8.28.0"),sQuery(id+"F0.wireOp",EDGE,"E8.29.0"),sQuery(id+"F0.wireOp",EDGE,"E8.30.0"),sQuery(id+"F0.wireOp",EDGE,"E8.31.0"),sQuery(id+"F0.wireOp",EDGE,"E8.32.0"),sQuery(id+"F0.wireOp",EDGE,"E8.33.0"),sQuery(id+"F0.wireOp",EDGE,"E8.34.0"),sQuery(id+"F0.wireOp",EDGE,"E8.35.0"),sQuery(id+"F0.wireOp",EDGE,"E8.36.0"),sQuery(id+"F0.wireOp",EDGE,"E8.37.0"),sQuery(id+"F0.wireOp",EDGE,"E8.38.0"),sQuery(id+"F0.wireOp",EDGE,"E8.39.0"),sQuery(id+"F0.wireOp",EDGE,"E8.40.0"),sQuery(id+"F0.wireOp",EDGE,"E8.41.0"),sQuery(id+"F0.wireOp",EDGE,"E8.42.0"),sQuery(id+"F0.wireOp",EDGE,"E8.43.0")])],"isStart":false})]});}
            var Q4;
            {var subQ0=sQuery(id+"F0.wireOp",EDGE,"E6.31.3");var subQ1=sQuery(id+"F0.wireOp",EDGE,"E6.31.1");Q4=makeQuery(id+"F2.opFillet","BLEND_EDGE",EDGE,{"blendedFrom":[makeQuery(id+"F1.opExtrude","SWEPT_EDGE",EDGE,{"disambiguationData":[OSD([sQuery(id+"F0.wireOp",EDGE,"E6.31.0"),subQ1,subQ0])]}),makeQuery(id+"F1.opExtrude","CAP_FACE",FACE,{"disambiguationData":[OSD([sQuery(id+"F0.wireOp",EDGE,"E0"),sQuery(id+"F0.wireOp",EDGE,"E1"),sQuery(id+"F0.wireOp",EDGE,"E2"),sQuery(id+"F0.wireOp",EDGE,"E4"),sQuery(id+"F0.wireOp",EDGE,"E5"),sQuery(id+"F0.wireOp",EDGE,"E6.1.1"),sQuery(id+"F0.wireOp",EDGE,"E6.1.2"),sQuery(id+"F0.wireOp",EDGE,"E6.1.3"),sQuery(id+"F0.wireOp",EDGE,"E6.1.4"),sQuery(id+"F0.wireOp",EDGE,"E6.2.1"),sQuery(id+"F0.wireOp",EDGE,"E6.2.2"),sQuery(id+"F0.wireOp",EDGE,"E6.2.3"),sQuery(id+"F0.wireOp",EDGE,"E6.2.4"),sQuery(id+"F0.wireOp",EDGE,"E6.3.1"),sQuery(id+"F0.wireOp",EDGE,"E6.3.2"),sQuery(id+"F0.wireOp",EDGE,"E6.3.3"),sQuery(id+"F0.wireOp",EDGE,"E6.3.4"),sQuery(id+"F0.wireOp",EDGE,"E6.4.1"),sQuery(id+"F0.wireOp",EDGE,"E6.4.2"),sQuery(id+"F0.wireOp",EDGE,"E6.4.3"),sQuery(id+"F0.wireOp",EDGE,"E6.4.4"),sQuery(id+"F0.wireOp",EDGE,"E6.5.1"),sQuery(id+"F0.wireOp",EDGE,"E6.5.2"),sQuery(id+"F0.wireOp",EDGE,"E6.5.3"),sQuery(id+"F0.wireOp",EDGE,"E6.5.4"),sQuery(id+"F0.wireOp",EDGE,"E6.6.1"),sQuery(id+"F0.wireOp",EDGE,"E6.6.2"),sQuery(id+"F0.wireOp",EDGE,"E6.6.3"),sQuery(id+"F0.wireOp",EDGE,"E6.6.4"),sQuery(id+"F0.wireOp",EDGE,"E6.7.1"),sQuery(id+"F0.wireOp",EDGE,"E6.7.2"),sQuery(id+"F0.wireOp",EDGE,"E6.7.3"),sQuery(id+"F0.wireOp",EDGE,"E6.7.4"),sQuery(id+"F0.wireOp",EDGE,"E6.8.1"),sQuery(id+"F0.wireOp",EDGE,"E6.8.2"),sQuery(id+"F0.wireOp",EDGE,"E6.8.3"),sQuery(id+"F0.wireOp",EDGE,"E6.8.4"),sQuery(id+"F0.wireOp",EDGE,"E6.9.1"),sQuery(id+"F0.wireOp",EDGE,"E6.9.2"),sQuery(id+"F0.wireOp",EDGE,"E6.9.3"),sQuery(id+"F0.wireOp",EDGE,"E6.9.4"),sQuery(id+"F0.wireOp",EDGE,"E6.10.1"),sQuery(id+"F0.wireOp",EDGE,"E6.10.2"),sQuery(id+"F0.wireOp",EDGE,"E6.10.3"),sQuery(id+"F0.wireOp",EDGE,"E6.10.4"),sQuery(id+"F0.wireOp",EDGE,"E6.11.1"),sQuery(id+"F0.wireOp",EDGE,"E6.11.2"),sQuery(id+"F0.wireOp",EDGE,"E6.11.3"),sQuery(id+"F0.wireOp",EDGE,"E6.11.4"),sQuery(id+"F0.wireOp",EDGE,"E6.12.1"),sQuery(id+"F0.wireOp",EDGE,"E6.12.2"),sQuery(id+"F0.wireOp",EDGE,"E6.12.3"),sQuery(id+"F0.wireOp",EDGE,"E6.12.4"),sQuery(id+"F0.wireOp",EDGE,"E6.13.1"),sQuery(id+"F0.wireOp",EDGE,"E6.13.2"),sQuery(id+"F0.wireOp",EDGE,"E6.13.3"),sQuery(id+"F0.wireOp",EDGE,"E6.13.4"),sQuery(id+"F0.wireOp",EDGE,"E6.14.1"),sQuery(id+"F0.wireOp",EDGE,"E6.14.2"),sQuery(id+"F0.wireOp",EDGE,"E6.14.3"),sQuery(id+"F0.wireOp",EDGE,"E6.14.4"),sQuery(id+"F0.wireOp",EDGE,"E6.15.1"),sQuery(id+"F0.wireOp",EDGE,"E6.15.2"),sQuery(id+"F0.wireOp",EDGE,"E6.15.3"),sQuery(id+"F0.wireOp",EDGE,"E6.15.4"),sQuery(id+"F0.wireOp",EDGE,"E6.16.1"),sQuery(id+"F0.wireOp",EDGE,"E6.16.2"),sQuery(id+"F0.wireOp",EDGE,"E6.16.3"),sQuery(id+"F0.wireOp",EDGE,"E6.16.4"),sQuery(id+"F0.wireOp",EDGE,"E6.17.1"),sQuery(id+"F0.wireOp",EDGE,"E6.17.2"),sQuery(id+"F0.wireOp",EDGE,"E6.17.3"),sQuery(id+"F0.wireOp",EDGE,"E6.17.4"),sQuery(id+"F0.wireOp",EDGE,"E6.18.1"),sQuery(id+"F0.wireOp",EDGE,"E6.18.2"),sQuery(id+"F0.wireOp",EDGE,"E6.18.3"),sQuery(id+"F0.wireOp",EDGE,"E6.18.4"),sQuery(id+"F0.wireOp",EDGE,"E6.19.1"),sQuery(id+"F0.wireOp",EDGE,"E6.19.2"),sQuery(id+"F0.wireOp",EDGE,"E6.19.3"),sQuery(id+"F0.wireOp",EDGE,"E6.19.4"),sQuery(id+"F0.wireOp",EDGE,"E6.20.1"),sQuery(id+"F0.wireOp",EDGE,"E6.20.2"),sQuery(id+"F0.wireOp",EDGE,"E6.20.3"),sQuery(id+"F0.wireOp",EDGE,"E6.20.4"),sQuery(id+"F0.wireOp",EDGE,"E6.21.1"),sQuery(id+"F0.wireOp",EDGE,"E6.21.2"),sQuery(id+"F0.wireOp",EDGE,"E6.21.3"),sQuery(id+"F0.wireOp",EDGE,"E6.21.4"),sQuery(id+"F0.wireOp",EDGE,"E6.22.1"),sQuery(id+"F0.wireOp",EDGE,"E6.22.2"),sQuery(id+"F0.wireOp",EDGE,"E6.22.3"),sQuery(id+"F0.wireOp",EDGE,"E6.22.4"),sQuery(id+"F0.wireOp",EDGE,"E6.23.1"),sQuery(id+"F0.wireOp",EDGE,"E6.23.2"),sQuery(id+"F0.wireOp",EDGE,"E6.23.3"),sQuery(id+"F0.wireOp",EDGE,"E6.23.4"),sQuery(id+"F0.wireOp",EDGE,"E6.24.1"),sQuery(id+"F0.wireOp",EDGE,"E6.24.2"),sQuery(id+"F0.wireOp",EDGE,"E6.24.3"),sQuery(id+"F0.wireOp",EDGE,"E6.24.4"),sQuery(id+"F0.wireOp",EDGE,"E6.25.1"),sQuery(id+"F0.wireOp",EDGE,"E6.25.2"),sQuery(id+"F0.wireOp",EDGE,"E6.25.3"),sQuery(id+"F0.wireOp",EDGE,"E6.25.4"),sQuery(id+"F0.wireOp",EDGE,"E6.26.1"),sQuery(id+"F0.wireOp",EDGE,"E6.26.2"),sQuery(id+"F0.wireOp",EDGE,"E6.26.3"),sQuery(id+"F0.wireOp",EDGE,"E6.26.4"),sQuery(id+"F0.wireOp",EDGE,"E6.27.1"),sQuery(id+"F0.wireOp",EDGE,"E6.27.2"),sQuery(id+"F0.wireOp",EDGE,"E6.27.3"),sQuery(id+"F0.wireOp",EDGE,"E6.27.4"),sQuery(id+"F0.wireOp",EDGE,"E6.28.1"),sQuery(id+"F0.wireOp",EDGE,"E6.28.2"),sQuery(id+"F0.wireOp",EDGE,"E6.28.3"),sQuery(id+"F0.wireOp",EDGE,"E6.28.4"),sQuery(id+"F0.wireOp",EDGE,"E6.29.1"),sQuery(id+"F0.wireOp",EDGE,"E6.29.2"),sQuery(id+"F0.wireOp",EDGE,"E6.29.3"),sQuery(id+"F0.wireOp",EDGE,"E6.29.4"),sQuery(id+"F0.wireOp",EDGE,"E6.30.1"),sQuery(id+"F0.wireOp",EDGE,"E6.30.2"),sQuery(id+"F0.wireOp",EDGE,"E6.30.3"),sQuery(id+"F0.wireOp",EDGE,"E6.30.4"),subQ1,sQuery(id+"F0.wireOp",EDGE,"E6.31.2"),subQ0,sQuery(id+"F0.wireOp",EDGE,"E6.31.4"),sQuery(id+"F0.wireOp",EDGE,"E6.32.1"),sQuery(id+"F0.wireOp",EDGE,"E6.32.2"),sQuery(id+"F0.wireOp",EDGE,"E6.32.3"),sQuery(id+"F0.wireOp",EDGE,"E6.32.4"),sQuery(id+"F0.wireOp",EDGE,"E6.33.1"),sQuery(id+"F0.wireOp",EDGE,"E6.33.2"),sQuery(id+"F0.wireOp",EDGE,"E6.33.3"),sQuery(id+"F0.wireOp",EDGE,"E6.33.4"),sQuery(id+"F0.wireOp",EDGE,"E6.34.1"),sQuery(id+"F0.wireOp",EDGE,"E6.34.2"),sQuery(id+"F0.wireOp",EDGE,"E6.34.3"),sQuery(id+"F0.wireOp",EDGE,"E6.34.4"),sQuery(id+"F0.wireOp",EDGE,"E6.35.1"),sQuery(id+"F0.wireOp",EDGE,"E6.35.2"),sQuery(id+"F0.wireOp",EDGE,"E6.35.3"),sQuery(id+"F0.wireOp",EDGE,"E6.35.4"),sQuery(id+"F0.wireOp",EDGE,"E6.36.1"),sQuery(id+"F0.wireOp",EDGE,"E6.36.2"),sQuery(id+"F0.wireOp",EDGE,"E6.36.3"),sQuery(id+"F0.wireOp",EDGE,"E6.36.4"),sQuery(id+"F0.wireOp",EDGE,"E6.37.1"),sQuery(id+"F0.wireOp",EDGE,"E6.37.2"),sQuery(id+"F0.wireOp",EDGE,"E6.37.3"),sQuery(id+"F0.wireOp",EDGE,"E6.37.4"),sQuery(id+"F0.wireOp",EDGE,"E6.38.1"),sQuery(id+"F0.wireOp",EDGE,"E6.38.2"),sQuery(id+"F0.wireOp",EDGE,"E6.38.3"),sQuery(id+"F0.wireOp",EDGE,"E6.38.4"),sQuery(id+"F0.wireOp",EDGE,"E6.39.1"),sQuery(id+"F0.wireOp",EDGE,"E6.39.2"),sQuery(id+"F0.wireOp",EDGE,"E6.39.3"),sQuery(id+"F0.wireOp",EDGE,"E6.39.4"),sQuery(id+"F0.wireOp",EDGE,"E6.40.1"),sQuery(id+"F0.wireOp",EDGE,"E6.40.2"),sQuery(id+"F0.wireOp",EDGE,"E6.40.3"),sQuery(id+"F0.wireOp",EDGE,"E6.40.4"),sQuery(id+"F0.wireOp",EDGE,"E6.41.1"),sQuery(id+"F0.wireOp",EDGE,"E6.41.2"),sQuery(id+"F0.wireOp",EDGE,"E6.41.3"),sQuery(id+"F0.wireOp",EDGE,"E6.41.4"),sQuery(id+"F0.wireOp",EDGE,"E6.42.1"),sQuery(id+"F0.wireOp",EDGE,"E6.42.2"),sQuery(id+"F0.wireOp",EDGE,"E6.42.3"),sQuery(id+"F0.wireOp",EDGE,"E6.42.4"),sQuery(id+"F0.wireOp",EDGE,"E6.43.1"),sQuery(id+"F0.wireOp",EDGE,"E6.43.2"),sQuery(id+"F0.wireOp",EDGE,"E6.43.3"),sQuery(id+"F0.wireOp",EDGE,"E6.43.4"),sQuery(id+"F0.wireOp",EDGE,"E7"),sQuery(id+"F0.wireOp",EDGE,"E8.1.0"),sQuery(id+"F0.wireOp",EDGE,"E8.2.0"),sQuery(id+"F0.wireOp",EDGE,"E8.3.0"),sQuery(id+"F0.wireOp",EDGE,"E8.4.0"),sQuery(id+"F0.wireOp",EDGE,"E8.5.0"),sQuery(id+"F0.wireOp",EDGE,"E8.6.0"),sQuery(id+"F0.wireOp",EDGE,"E8.7.0"),sQuery(id+"F0.wireOp",EDGE,"E8.8.0"),sQuery(id+"F0.wireOp",EDGE,"E8.9.0"),sQuery(id+"F0.wireOp",EDGE,"E8.10.0"),sQuery(id+"F0.wireOp",EDGE,"E8.11.0"),sQuery(id+"F0.wireOp",EDGE,"E8.12.0"),sQuery(id+"F0.wireOp",EDGE,"E8.13.0"),sQuery(id+"F0.wireOp",EDGE,"E8.14.0"),sQuery(id+"F0.wireOp",EDGE,"E8.15.0"),sQuery(id+"F0.wireOp",EDGE,"E8.16.0"),sQuery(id+"F0.wireOp",EDGE,"E8.17.0"),sQuery(id+"F0.wireOp",EDGE,"E8.18.0"),sQuery(id+"F0.wireOp",EDGE,"E8.19.0"),sQuery(id+"F0.wireOp",EDGE,"E8.20.0"),sQuery(id+"F0.wireOp",EDGE,"E8.21.0"),sQuery(id+"F0.wireOp",EDGE,"E8.22.0"),sQuery(id+"F0.wireOp",EDGE,"E8.23.0"),sQuery(id+"F0.wireOp",EDGE,"E8.24.0"),sQuery(id+"F0.wireOp",EDGE,"E8.25.0"),sQuery(id+"F0.wireOp",EDGE,"E8.26.0"),sQuery(id+"F0.wireOp",EDGE,"E8.27.0"),sQuery(id+"F0.wireOp",EDGE,"E8.28.0"),sQuery(id+"F0.wireOp",EDGE,"E8.29.0"),sQuery(id+"F0.wireOp",EDGE,"E8.30.0"),sQuery(id+"F0.wireOp",EDGE,"E8.31.0"),sQuery(id+"F0.wireOp",EDGE,"E8.32.0"),sQuery(id+"F0.wireOp",EDGE,"E8.33.0"),sQuery(id+"F0.wireOp",EDGE,"E8.34.0"),sQuery(id+"F0.wireOp",EDGE,"E8.35.0"),sQuery(id+"F0.wireOp",EDGE,"E8.36.0"),sQuery(id+"F0.wireOp",EDGE,"E8.37.0"),sQuery(id+"F0.wireOp",EDGE,"E8.38.0"),sQuery(id+"F0.wireOp",EDGE,"E8.39.0"),sQuery(id+"F0.wireOp",EDGE,"E8.40.0"),sQuery(id+"F0.wireOp",EDGE,"E8.41.0"),sQuery(id+"F0.wireOp",EDGE,"E8.42.0"),sQuery(id+"F0.wireOp",EDGE,"E8.43.0")])],"isStart":false})],"blendedInto":[makeQuery(id+"F1.opExtrude","CAP_FACE",FACE,{"disambiguationData":[OSD([sQuery(id+"F0.wireOp",EDGE,"E0"),sQuery(id+"F0.wireOp",EDGE,"E1"),sQuery(id+"F0.wireOp",EDGE,"E2"),sQuery(id+"F0.wireOp",EDGE,"E4"),sQuery(id+"F0.wireOp",EDGE,"E5"),sQuery(id+"F0.wireOp",EDGE,"E6.1.1"),sQuery(id+"F0.wireOp",EDGE,"E6.1.2"),sQuery(id+"F0.wireOp",EDGE,"E6.1.3"),sQuery(id+"F0.wireOp",EDGE,"E6.1.4"),sQuery(id+"F0.wireOp",EDGE,"E6.2.1"),sQuery(id+"F0.wireOp",EDGE,"E6.2.2"),sQuery(id+"F0.wireOp",EDGE,"E6.2.3"),sQuery(id+"F0.wireOp",EDGE,"E6.2.4"),sQuery(id+"F0.wireOp",EDGE,"E6.3.1"),sQuery(id+"F0.wireOp",EDGE,"E6.3.2"),sQuery(id+"F0.wireOp",EDGE,"E6.3.3"),sQuery(id+"F0.wireOp",EDGE,"E6.3.4"),sQuery(id+"F0.wireOp",EDGE,"E6.4.1"),sQuery(id+"F0.wireOp",EDGE,"E6.4.2"),sQuery(id+"F0.wireOp",EDGE,"E6.4.3"),sQuery(id+"F0.wireOp",EDGE,"E6.4.4"),sQuery(id+"F0.wireOp",EDGE,"E6.5.1"),sQuery(id+"F0.wireOp",EDGE,"E6.5.2"),sQuery(id+"F0.wireOp",EDGE,"E6.5.3"),sQuery(id+"F0.wireOp",EDGE,"E6.5.4"),sQuery(id+"F0.wireOp",EDGE,"E6.6.1"),sQuery(id+"F0.wireOp",EDGE,"E6.6.2"),sQuery(id+"F0.wireOp",EDGE,"E6.6.3"),sQuery(id+"F0.wireOp",EDGE,"E6.6.4"),sQuery(id+"F0.wireOp",EDGE,"E6.7.1"),sQuery(id+"F0.wireOp",EDGE,"E6.7.2"),sQuery(id+"F0.wireOp",EDGE,"E6.7.3"),sQuery(id+"F0.wireOp",EDGE,"E6.7.4"),sQuery(id+"F0.wireOp",EDGE,"E6.8.1"),sQuery(id+"F0.wireOp",EDGE,"E6.8.2"),sQuery(id+"F0.wireOp",EDGE,"E6.8.3"),sQuery(id+"F0.wireOp",EDGE,"E6.8.4"),sQuery(id+"F0.wireOp",EDGE,"E6.9.1"),sQuery(id+"F0.wireOp",EDGE,"E6.9.2"),sQuery(id+"F0.wireOp",EDGE,"E6.9.3"),sQuery(id+"F0.wireOp",EDGE,"E6.9.4"),sQuery(id+"F0.wireOp",EDGE,"E6.10.1"),sQuery(id+"F0.wireOp",EDGE,"E6.10.2"),sQuery(id+"F0.wireOp",EDGE,"E6.10.3"),sQuery(id+"F0.wireOp",EDGE,"E6.10.4"),sQuery(id+"F0.wireOp",EDGE,"E6.11.1"),sQuery(id+"F0.wireOp",EDGE,"E6.11.2"),sQuery(id+"F0.wireOp",EDGE,"E6.11.3"),sQuery(id+"F0.wireOp",EDGE,"E6.11.4"),sQuery(id+"F0.wireOp",EDGE,"E6.12.1"),sQuery(id+"F0.wireOp",EDGE,"E6.12.2"),sQuery(id+"F0.wireOp",EDGE,"E6.12.3"),sQuery(id+"F0.wireOp",EDGE,"E6.12.4"),sQuery(id+"F0.wireOp",EDGE,"E6.13.1"),sQuery(id+"F0.wireOp",EDGE,"E6.13.2"),sQuery(id+"F0.wireOp",EDGE,"E6.13.3"),sQuery(id+"F0.wireOp",EDGE,"E6.13.4"),sQuery(id+"F0.wireOp",EDGE,"E6.14.1"),sQuery(id+"F0.wireOp",EDGE,"E6.14.2"),sQuery(id+"F0.wireOp",EDGE,"E6.14.3"),sQuery(id+"F0.wireOp",EDGE,"E6.14.4"),sQuery(id+"F0.wireOp",EDGE,"E6.15.1"),sQuery(id+"F0.wireOp",EDGE,"E6.15.2"),sQuery(id+"F0.wireOp",EDGE,"E6.15.3"),sQuery(id+"F0.wireOp",EDGE,"E6.15.4"),sQuery(id+"F0.wireOp",EDGE,"E6.16.1"),sQuery(id+"F0.wireOp",EDGE,"E6.16.2"),sQuery(id+"F0.wireOp",EDGE,"E6.16.3"),sQuery(id+"F0.wireOp",EDGE,"E6.16.4"),sQuery(id+"F0.wireOp",EDGE,"E6.17.1"),sQuery(id+"F0.wireOp",EDGE,"E6.17.2"),sQuery(id+"F0.wireOp",EDGE,"E6.17.3"),sQuery(id+"F0.wireOp",EDGE,"E6.17.4"),sQuery(id+"F0.wireOp",EDGE,"E6.18.1"),sQuery(id+"F0.wireOp",EDGE,"E6.18.2"),sQuery(id+"F0.wireOp",EDGE,"E6.18.3"),sQuery(id+"F0.wireOp",EDGE,"E6.18.4"),sQuery(id+"F0.wireOp",EDGE,"E6.19.1"),sQuery(id+"F0.wireOp",EDGE,"E6.19.2"),sQuery(id+"F0.wireOp",EDGE,"E6.19.3"),sQuery(id+"F0.wireOp",EDGE,"E6.19.4"),sQuery(id+"F0.wireOp",EDGE,"E6.20.1"),sQuery(id+"F0.wireOp",EDGE,"E6.20.2"),sQuery(id+"F0.wireOp",EDGE,"E6.20.3"),sQuery(id+"F0.wireOp",EDGE,"E6.20.4"),sQuery(id+"F0.wireOp",EDGE,"E6.21.1"),sQuery(id+"F0.wireOp",EDGE,"E6.21.2"),sQuery(id+"F0.wireOp",EDGE,"E6.21.3"),sQuery(id+"F0.wireOp",EDGE,"E6.21.4"),sQuery(id+"F0.wireOp",EDGE,"E6.22.1"),sQuery(id+"F0.wireOp",EDGE,"E6.22.2"),sQuery(id+"F0.wireOp",EDGE,"E6.22.3"),sQuery(id+"F0.wireOp",EDGE,"E6.22.4"),sQuery(id+"F0.wireOp",EDGE,"E6.23.1"),sQuery(id+"F0.wireOp",EDGE,"E6.23.2"),sQuery(id+"F0.wireOp",EDGE,"E6.23.3"),sQuery(id+"F0.wireOp",EDGE,"E6.23.4"),sQuery(id+"F0.wireOp",EDGE,"E6.24.1"),sQuery(id+"F0.wireOp",EDGE,"E6.24.2"),sQuery(id+"F0.wireOp",EDGE,"E6.24.3"),sQuery(id+"F0.wireOp",EDGE,"E6.24.4"),sQuery(id+"F0.wireOp",EDGE,"E6.25.1"),sQuery(id+"F0.wireOp",EDGE,"E6.25.2"),sQuery(id+"F0.wireOp",EDGE,"E6.25.3"),sQuery(id+"F0.wireOp",EDGE,"E6.25.4"),sQuery(id+"F0.wireOp",EDGE,"E6.26.1"),sQuery(id+"F0.wireOp",EDGE,"E6.26.2"),sQuery(id+"F0.wireOp",EDGE,"E6.26.3"),sQuery(id+"F0.wireOp",EDGE,"E6.26.4"),sQuery(id+"F0.wireOp",EDGE,"E6.27.1"),sQuery(id+"F0.wireOp",EDGE,"E6.27.2"),sQuery(id+"F0.wireOp",EDGE,"E6.27.3"),sQuery(id+"F0.wireOp",EDGE,"E6.27.4"),sQuery(id+"F0.wireOp",EDGE,"E6.28.1"),sQuery(id+"F0.wireOp",EDGE,"E6.28.2"),sQuery(id+"F0.wireOp",EDGE,"E6.28.3"),sQuery(id+"F0.wireOp",EDGE,"E6.28.4"),sQuery(id+"F0.wireOp",EDGE,"E6.29.1"),sQuery(id+"F0.wireOp",EDGE,"E6.29.2"),sQuery(id+"F0.wireOp",EDGE,"E6.29.3"),sQuery(id+"F0.wireOp",EDGE,"E6.29.4"),sQuery(id+"F0.wireOp",EDGE,"E6.30.1"),sQuery(id+"F0.wireOp",EDGE,"E6.30.2"),sQuery(id+"F0.wireOp",EDGE,"E6.30.3"),sQuery(id+"F0.wireOp",EDGE,"E6.30.4"),subQ1,sQuery(id+"F0.wireOp",EDGE,"E6.31.2"),subQ0,sQuery(id+"F0.wireOp",EDGE,"E6.31.4"),sQuery(id+"F0.wireOp",EDGE,"E6.32.1"),sQuery(id+"F0.wireOp",EDGE,"E6.32.2"),sQuery(id+"F0.wireOp",EDGE,"E6.32.3"),sQuery(id+"F0.wireOp",EDGE,"E6.32.4"),sQuery(id+"F0.wireOp",EDGE,"E6.33.1"),sQuery(id+"F0.wireOp",EDGE,"E6.33.2"),sQuery(id+"F0.wireOp",EDGE,"E6.33.3"),sQuery(id+"F0.wireOp",EDGE,"E6.33.4"),sQuery(id+"F0.wireOp",EDGE,"E6.34.1"),sQuery(id+"F0.wireOp",EDGE,"E6.34.2"),sQuery(id+"F0.wireOp",EDGE,"E6.34.3"),sQuery(id+"F0.wireOp",EDGE,"E6.34.4"),sQuery(id+"F0.wireOp",EDGE,"E6.35.1"),sQuery(id+"F0.wireOp",EDGE,"E6.35.2"),sQuery(id+"F0.wireOp",EDGE,"E6.35.3"),sQuery(id+"F0.wireOp",EDGE,"E6.35.4"),sQuery(id+"F0.wireOp",EDGE,"E6.36.1"),sQuery(id+"F0.wireOp",EDGE,"E6.36.2"),sQuery(id+"F0.wireOp",EDGE,"E6.36.3"),sQuery(id+"F0.wireOp",EDGE,"E6.36.4"),sQuery(id+"F0.wireOp",EDGE,"E6.37.1"),sQuery(id+"F0.wireOp",EDGE,"E6.37.2"),sQuery(id+"F0.wireOp",EDGE,"E6.37.3"),sQuery(id+"F0.wireOp",EDGE,"E6.37.4"),sQuery(id+"F0.wireOp",EDGE,"E6.38.1"),sQuery(id+"F0.wireOp",EDGE,"E6.38.2"),sQuery(id+"F0.wireOp",EDGE,"E6.38.3"),sQuery(id+"F0.wireOp",EDGE,"E6.38.4"),sQuery(id+"F0.wireOp",EDGE,"E6.39.1"),sQuery(id+"F0.wireOp",EDGE,"E6.39.2"),sQuery(id+"F0.wireOp",EDGE,"E6.39.3"),sQuery(id+"F0.wireOp",EDGE,"E6.39.4"),sQuery(id+"F0.wireOp",EDGE,"E6.40.1"),sQuery(id+"F0.wireOp",EDGE,"E6.40.2"),sQuery(id+"F0.wireOp",EDGE,"E6.40.3"),sQuery(id+"F0.wireOp",EDGE,"E6.40.4"),sQuery(id+"F0.wireOp",EDGE,"E6.41.1"),sQuery(id+"F0.wireOp",EDGE,"E6.41.2"),sQuery(id+"F0.wireOp",EDGE,"E6.41.3"),sQuery(id+"F0.wireOp",EDGE,"E6.41.4"),sQuery(id+"F0.wireOp",EDGE,"E6.42.1"),sQuery(id+"F0.wireOp",EDGE,"E6.42.2"),sQuery(id+"F0.wireOp",EDGE,"E6.42.3"),sQuery(id+"F0.wireOp",EDGE,"E6.42.4"),sQuery(id+"F0.wireOp",EDGE,"E6.43.1"),sQuery(id+"F0.wireOp",EDGE,"E6.43.2"),sQuery(id+"F0.wireOp",EDGE,"E6.43.3"),sQuery(id+"F0.wireOp",EDGE,"E6.43.4"),sQuery(id+"F0.wireOp",EDGE,"E7"),sQuery(id+"F0.wireOp",EDGE,"E8.1.0"),sQuery(id+"F0.wireOp",EDGE,"E8.2.0"),sQuery(id+"F0.wireOp",EDGE,"E8.3.0"),sQuery(id+"F0.wireOp",EDGE,"E8.4.0"),sQuery(id+"F0.wireOp",EDGE,"E8.5.0"),sQuery(id+"F0.wireOp",EDGE,"E8.6.0"),sQuery(id+"F0.wireOp",EDGE,"E8.7.0"),sQuery(id+"F0.wireOp",EDGE,"E8.8.0"),sQuery(id+"F0.wireOp",EDGE,"E8.9.0"),sQuery(id+"F0.wireOp",EDGE,"E8.10.0"),sQuery(id+"F0.wireOp",EDGE,"E8.11.0"),sQuery(id+"F0.wireOp",EDGE,"E8.12.0"),sQuery(id+"F0.wireOp",EDGE,"E8.13.0"),sQuery(id+"F0.wireOp",EDGE,"E8.14.0"),sQuery(id+"F0.wireOp",EDGE,"E8.15.0"),sQuery(id+"F0.wireOp",EDGE,"E8.16.0"),sQuery(id+"F0.wireOp",EDGE,"E8.17.0"),sQuery(id+"F0.wireOp",EDGE,"E8.18.0"),sQuery(id+"F0.wireOp",EDGE,"E8.19.0"),sQuery(id+"F0.wireOp",EDGE,"E8.20.0"),sQuery(id+"F0.wireOp",EDGE,"E8.21.0"),sQuery(id+"F0.wireOp",EDGE,"E8.22.0"),sQuery(id+"F0.wireOp",EDGE,"E8.23.0"),sQuery(id+"F0.wireOp",EDGE,"E8.24.0"),sQuery(id+"F0.wireOp",EDGE,"E8.25.0"),sQuery(id+"F0.wireOp",EDGE,"E8.26.0"),sQuery(id+"F0.wireOp",EDGE,"E8.27.0"),sQuery(id+"F0.wireOp",EDGE,"E8.28.0"),sQuery(id+"F0.wireOp",EDGE,"E8.29.0"),sQuery(id+"F0.wireOp",EDGE,"E8.30.0"),sQuery(id+"F0.wireOp",EDGE,"E8.31.0"),sQuery(id+"F0.wireOp",EDGE,"E8.32.0"),sQuery(id+"F0.wireOp",EDGE,"E8.33.0"),sQuery(id+"F0.wireOp",EDGE,"E8.34.0"),sQuery(id+"F0.wireOp",EDGE,"E8.35.0"),sQuery(id+"F0.wireOp",EDGE,"E8.36.0"),sQuery(id+"F0.wireOp",EDGE,"E8.37.0"),sQuery(id+"F0.wireOp",EDGE,"E8.38.0"),sQuery(id+"F0.wireOp",EDGE,"E8.39.0"),sQuery(id+"F0.wireOp",EDGE,"E8.40.0"),sQuery(id+"F0.wireOp",EDGE,"E8.41.0"),sQuery(id+"F0.wireOp",EDGE,"E8.42.0"),sQuery(id+"F0.wireOp",EDGE,"E8.43.0")])],"isStart":false})]});}
            var Q5;
            {var subQ0=sQuery(id+"F0.wireOp",EDGE,"E6.33.3");var subQ1=sQuery(id+"F0.wireOp",EDGE,"E6.33.1");Q5=makeQuery(id+"F2.opFillet","BLEND_EDGE",EDGE,{"blendedFrom":[makeQuery(id+"F1.opExtrude","SWEPT_EDGE",EDGE,{"disambiguationData":[OSD([sQuery(id+"F0.wireOp",EDGE,"E6.33.0"),subQ1,subQ0])]}),makeQuery(id+"F1.opExtrude","CAP_FACE",FACE,{"disambiguationData":[OSD([sQuery(id+"F0.wireOp",EDGE,"E0"),sQuery(id+"F0.wireOp",EDGE,"E1"),sQuery(id+"F0.wireOp",EDGE,"E2"),sQuery(id+"F0.wireOp",EDGE,"E4"),sQuery(id+"F0.wireOp",EDGE,"E5"),sQuery(id+"F0.wireOp",EDGE,"E6.1.1"),sQuery(id+"F0.wireOp",EDGE,"E6.1.2"),sQuery(id+"F0.wireOp",EDGE,"E6.1.3"),sQuery(id+"F0.wireOp",EDGE,"E6.1.4"),sQuery(id+"F0.wireOp",EDGE,"E6.2.1"),sQuery(id+"F0.wireOp",EDGE,"E6.2.2"),sQuery(id+"F0.wireOp",EDGE,"E6.2.3"),sQuery(id+"F0.wireOp",EDGE,"E6.2.4"),sQuery(id+"F0.wireOp",EDGE,"E6.3.1"),sQuery(id+"F0.wireOp",EDGE,"E6.3.2"),sQuery(id+"F0.wireOp",EDGE,"E6.3.3"),sQuery(id+"F0.wireOp",EDGE,"E6.3.4"),sQuery(id+"F0.wireOp",EDGE,"E6.4.1"),sQuery(id+"F0.wireOp",EDGE,"E6.4.2"),sQuery(id+"F0.wireOp",EDGE,"E6.4.3"),sQuery(id+"F0.wireOp",EDGE,"E6.4.4"),sQuery(id+"F0.wireOp",EDGE,"E6.5.1"),sQuery(id+"F0.wireOp",EDGE,"E6.5.2"),sQuery(id+"F0.wireOp",EDGE,"E6.5.3"),sQuery(id+"F0.wireOp",EDGE,"E6.5.4"),sQuery(id+"F0.wireOp",EDGE,"E6.6.1"),sQuery(id+"F0.wireOp",EDGE,"E6.6.2"),sQuery(id+"F0.wireOp",EDGE,"E6.6.3"),sQuery(id+"F0.wireOp",EDGE,"E6.6.4"),sQuery(id+"F0.wireOp",EDGE,"E6.7.1"),sQuery(id+"F0.wireOp",EDGE,"E6.7.2"),sQuery(id+"F0.wireOp",EDGE,"E6.7.3"),sQuery(id+"F0.wireOp",EDGE,"E6.7.4"),sQuery(id+"F0.wireOp",EDGE,"E6.8.1"),sQuery(id+"F0.wireOp",EDGE,"E6.8.2"),sQuery(id+"F0.wireOp",EDGE,"E6.8.3"),sQuery(id+"F0.wireOp",EDGE,"E6.8.4"),sQuery(id+"F0.wireOp",EDGE,"E6.9.1"),sQuery(id+"F0.wireOp",EDGE,"E6.9.2"),sQuery(id+"F0.wireOp",EDGE,"E6.9.3"),sQuery(id+"F0.wireOp",EDGE,"E6.9.4"),sQuery(id+"F0.wireOp",EDGE,"E6.10.1"),sQuery(id+"F0.wireOp",EDGE,"E6.10.2"),sQuery(id+"F0.wireOp",EDGE,"E6.10.3"),sQuery(id+"F0.wireOp",EDGE,"E6.10.4"),sQuery(id+"F0.wireOp",EDGE,"E6.11.1"),sQuery(id+"F0.wireOp",EDGE,"E6.11.2"),sQuery(id+"F0.wireOp",EDGE,"E6.11.3"),sQuery(id+"F0.wireOp",EDGE,"E6.11.4"),sQuery(id+"F0.wireOp",EDGE,"E6.12.1"),sQuery(id+"F0.wireOp",EDGE,"E6.12.2"),sQuery(id+"F0.wireOp",EDGE,"E6.12.3"),sQuery(id+"F0.wireOp",EDGE,"E6.12.4"),sQuery(id+"F0.wireOp",EDGE,"E6.13.1"),sQuery(id+"F0.wireOp",EDGE,"E6.13.2"),sQuery(id+"F0.wireOp",EDGE,"E6.13.3"),sQuery(id+"F0.wireOp",EDGE,"E6.13.4"),sQuery(id+"F0.wireOp",EDGE,"E6.14.1"),sQuery(id+"F0.wireOp",EDGE,"E6.14.2"),sQuery(id+"F0.wireOp",EDGE,"E6.14.3"),sQuery(id+"F0.wireOp",EDGE,"E6.14.4"),sQuery(id+"F0.wireOp",EDGE,"E6.15.1"),sQuery(id+"F0.wireOp",EDGE,"E6.15.2"),sQuery(id+"F0.wireOp",EDGE,"E6.15.3"),sQuery(id+"F0.wireOp",EDGE,"E6.15.4"),sQuery(id+"F0.wireOp",EDGE,"E6.16.1"),sQuery(id+"F0.wireOp",EDGE,"E6.16.2"),sQuery(id+"F0.wireOp",EDGE,"E6.16.3"),sQuery(id+"F0.wireOp",EDGE,"E6.16.4"),sQuery(id+"F0.wireOp",EDGE,"E6.17.1"),sQuery(id+"F0.wireOp",EDGE,"E6.17.2"),sQuery(id+"F0.wireOp",EDGE,"E6.17.3"),sQuery(id+"F0.wireOp",EDGE,"E6.17.4"),sQuery(id+"F0.wireOp",EDGE,"E6.18.1"),sQuery(id+"F0.wireOp",EDGE,"E6.18.2"),sQuery(id+"F0.wireOp",EDGE,"E6.18.3"),sQuery(id+"F0.wireOp",EDGE,"E6.18.4"),sQuery(id+"F0.wireOp",EDGE,"E6.19.1"),sQuery(id+"F0.wireOp",EDGE,"E6.19.2"),sQuery(id+"F0.wireOp",EDGE,"E6.19.3"),sQuery(id+"F0.wireOp",EDGE,"E6.19.4"),sQuery(id+"F0.wireOp",EDGE,"E6.20.1"),sQuery(id+"F0.wireOp",EDGE,"E6.20.2"),sQuery(id+"F0.wireOp",EDGE,"E6.20.3"),sQuery(id+"F0.wireOp",EDGE,"E6.20.4"),sQuery(id+"F0.wireOp",EDGE,"E6.21.1"),sQuery(id+"F0.wireOp",EDGE,"E6.21.2"),sQuery(id+"F0.wireOp",EDGE,"E6.21.3"),sQuery(id+"F0.wireOp",EDGE,"E6.21.4"),sQuery(id+"F0.wireOp",EDGE,"E6.22.1"),sQuery(id+"F0.wireOp",EDGE,"E6.22.2"),sQuery(id+"F0.wireOp",EDGE,"E6.22.3"),sQuery(id+"F0.wireOp",EDGE,"E6.22.4"),sQuery(id+"F0.wireOp",EDGE,"E6.23.1"),sQuery(id+"F0.wireOp",EDGE,"E6.23.2"),sQuery(id+"F0.wireOp",EDGE,"E6.23.3"),sQuery(id+"F0.wireOp",EDGE,"E6.23.4"),sQuery(id+"F0.wireOp",EDGE,"E6.24.1"),sQuery(id+"F0.wireOp",EDGE,"E6.24.2"),sQuery(id+"F0.wireOp",EDGE,"E6.24.3"),sQuery(id+"F0.wireOp",EDGE,"E6.24.4"),sQuery(id+"F0.wireOp",EDGE,"E6.25.1"),sQuery(id+"F0.wireOp",EDGE,"E6.25.2"),sQuery(id+"F0.wireOp",EDGE,"E6.25.3"),sQuery(id+"F0.wireOp",EDGE,"E6.25.4"),sQuery(id+"F0.wireOp",EDGE,"E6.26.1"),sQuery(id+"F0.wireOp",EDGE,"E6.26.2"),sQuery(id+"F0.wireOp",EDGE,"E6.26.3"),sQuery(id+"F0.wireOp",EDGE,"E6.26.4"),sQuery(id+"F0.wireOp",EDGE,"E6.27.1"),sQuery(id+"F0.wireOp",EDGE,"E6.27.2"),sQuery(id+"F0.wireOp",EDGE,"E6.27.3"),sQuery(id+"F0.wireOp",EDGE,"E6.27.4"),sQuery(id+"F0.wireOp",EDGE,"E6.28.1"),sQuery(id+"F0.wireOp",EDGE,"E6.28.2"),sQuery(id+"F0.wireOp",EDGE,"E6.28.3"),sQuery(id+"F0.wireOp",EDGE,"E6.28.4"),sQuery(id+"F0.wireOp",EDGE,"E6.29.1"),sQuery(id+"F0.wireOp",EDGE,"E6.29.2"),sQuery(id+"F0.wireOp",EDGE,"E6.29.3"),sQuery(id+"F0.wireOp",EDGE,"E6.29.4"),sQuery(id+"F0.wireOp",EDGE,"E6.30.1"),sQuery(id+"F0.wireOp",EDGE,"E6.30.2"),sQuery(id+"F0.wireOp",EDGE,"E6.30.3"),sQuery(id+"F0.wireOp",EDGE,"E6.30.4"),sQuery(id+"F0.wireOp",EDGE,"E6.31.1"),sQuery(id+"F0.wireOp",EDGE,"E6.31.2"),sQuery(id+"F0.wireOp",EDGE,"E6.31.3"),sQuery(id+"F0.wireOp",EDGE,"E6.31.4"),sQuery(id+"F0.wireOp",EDGE,"E6.32.1"),sQuery(id+"F0.wireOp",EDGE,"E6.32.2"),sQuery(id+"F0.wireOp",EDGE,"E6.32.3"),sQuery(id+"F0.wireOp",EDGE,"E6.32.4"),subQ1,sQuery(id+"F0.wireOp",EDGE,"E6.33.2"),subQ0,sQuery(id+"F0.wireOp",EDGE,"E6.33.4"),sQuery(id+"F0.wireOp",EDGE,"E6.34.1"),sQuery(id+"F0.wireOp",EDGE,"E6.34.2"),sQuery(id+"F0.wireOp",EDGE,"E6.34.3"),sQuery(id+"F0.wireOp",EDGE,"E6.34.4"),sQuery(id+"F0.wireOp",EDGE,"E6.35.1"),sQuery(id+"F0.wireOp",EDGE,"E6.35.2"),sQuery(id+"F0.wireOp",EDGE,"E6.35.3"),sQuery(id+"F0.wireOp",EDGE,"E6.35.4"),sQuery(id+"F0.wireOp",EDGE,"E6.36.1"),sQuery(id+"F0.wireOp",EDGE,"E6.36.2"),sQuery(id+"F0.wireOp",EDGE,"E6.36.3"),sQuery(id+"F0.wireOp",EDGE,"E6.36.4"),sQuery(id+"F0.wireOp",EDGE,"E6.37.1"),sQuery(id+"F0.wireOp",EDGE,"E6.37.2"),sQuery(id+"F0.wireOp",EDGE,"E6.37.3"),sQuery(id+"F0.wireOp",EDGE,"E6.37.4"),sQuery(id+"F0.wireOp",EDGE,"E6.38.1"),sQuery(id+"F0.wireOp",EDGE,"E6.38.2"),sQuery(id+"F0.wireOp",EDGE,"E6.38.3"),sQuery(id+"F0.wireOp",EDGE,"E6.38.4"),sQuery(id+"F0.wireOp",EDGE,"E6.39.1"),sQuery(id+"F0.wireOp",EDGE,"E6.39.2"),sQuery(id+"F0.wireOp",EDGE,"E6.39.3"),sQuery(id+"F0.wireOp",EDGE,"E6.39.4"),sQuery(id+"F0.wireOp",EDGE,"E6.40.1"),sQuery(id+"F0.wireOp",EDGE,"E6.40.2"),sQuery(id+"F0.wireOp",EDGE,"E6.40.3"),sQuery(id+"F0.wireOp",EDGE,"E6.40.4"),sQuery(id+"F0.wireOp",EDGE,"E6.41.1"),sQuery(id+"F0.wireOp",EDGE,"E6.41.2"),sQuery(id+"F0.wireOp",EDGE,"E6.41.3"),sQuery(id+"F0.wireOp",EDGE,"E6.41.4"),sQuery(id+"F0.wireOp",EDGE,"E6.42.1"),sQuery(id+"F0.wireOp",EDGE,"E6.42.2"),sQuery(id+"F0.wireOp",EDGE,"E6.42.3"),sQuery(id+"F0.wireOp",EDGE,"E6.42.4"),sQuery(id+"F0.wireOp",EDGE,"E6.43.1"),sQuery(id+"F0.wireOp",EDGE,"E6.43.2"),sQuery(id+"F0.wireOp",EDGE,"E6.43.3"),sQuery(id+"F0.wireOp",EDGE,"E6.43.4"),sQuery(id+"F0.wireOp",EDGE,"E7"),sQuery(id+"F0.wireOp",EDGE,"E8.1.0"),sQuery(id+"F0.wireOp",EDGE,"E8.2.0"),sQuery(id+"F0.wireOp",EDGE,"E8.3.0"),sQuery(id+"F0.wireOp",EDGE,"E8.4.0"),sQuery(id+"F0.wireOp",EDGE,"E8.5.0"),sQuery(id+"F0.wireOp",EDGE,"E8.6.0"),sQuery(id+"F0.wireOp",EDGE,"E8.7.0"),sQuery(id+"F0.wireOp",EDGE,"E8.8.0"),sQuery(id+"F0.wireOp",EDGE,"E8.9.0"),sQuery(id+"F0.wireOp",EDGE,"E8.10.0"),sQuery(id+"F0.wireOp",EDGE,"E8.11.0"),sQuery(id+"F0.wireOp",EDGE,"E8.12.0"),sQuery(id+"F0.wireOp",EDGE,"E8.13.0"),sQuery(id+"F0.wireOp",EDGE,"E8.14.0"),sQuery(id+"F0.wireOp",EDGE,"E8.15.0"),sQuery(id+"F0.wireOp",EDGE,"E8.16.0"),sQuery(id+"F0.wireOp",EDGE,"E8.17.0"),sQuery(id+"F0.wireOp",EDGE,"E8.18.0"),sQuery(id+"F0.wireOp",EDGE,"E8.19.0"),sQuery(id+"F0.wireOp",EDGE,"E8.20.0"),sQuery(id+"F0.wireOp",EDGE,"E8.21.0"),sQuery(id+"F0.wireOp",EDGE,"E8.22.0"),sQuery(id+"F0.wireOp",EDGE,"E8.23.0"),sQuery(id+"F0.wireOp",EDGE,"E8.24.0"),sQuery(id+"F0.wireOp",EDGE,"E8.25.0"),sQuery(id+"F0.wireOp",EDGE,"E8.26.0"),sQuery(id+"F0.wireOp",EDGE,"E8.27.0"),sQuery(id+"F0.wireOp",EDGE,"E8.28.0"),sQuery(id+"F0.wireOp",EDGE,"E8.29.0"),sQuery(id+"F0.wireOp",EDGE,"E8.30.0"),sQuery(id+"F0.wireOp",EDGE,"E8.31.0"),sQuery(id+"F0.wireOp",EDGE,"E8.32.0"),sQuery(id+"F0.wireOp",EDGE,"E8.33.0"),sQuery(id+"F0.wireOp",EDGE,"E8.34.0"),sQuery(id+"F0.wireOp",EDGE,"E8.35.0"),sQuery(id+"F0.wireOp",EDGE,"E8.36.0"),sQuery(id+"F0.wireOp",EDGE,"E8.37.0"),sQuery(id+"F0.wireOp",EDGE,"E8.38.0"),sQuery(id+"F0.wireOp",EDGE,"E8.39.0"),sQuery(id+"F0.wireOp",EDGE,"E8.40.0"),sQuery(id+"F0.wireOp",EDGE,"E8.41.0"),sQuery(id+"F0.wireOp",EDGE,"E8.42.0"),sQuery(id+"F0.wireOp",EDGE,"E8.43.0")])],"isStart":false})],"blendedInto":[makeQuery(id+"F1.opExtrude","CAP_FACE",FACE,{"disambiguationData":[OSD([sQuery(id+"F0.wireOp",EDGE,"E0"),sQuery(id+"F0.wireOp",EDGE,"E1"),sQuery(id+"F0.wireOp",EDGE,"E2"),sQuery(id+"F0.wireOp",EDGE,"E4"),sQuery(id+"F0.wireOp",EDGE,"E5"),sQuery(id+"F0.wireOp",EDGE,"E6.1.1"),sQuery(id+"F0.wireOp",EDGE,"E6.1.2"),sQuery(id+"F0.wireOp",EDGE,"E6.1.3"),sQuery(id+"F0.wireOp",EDGE,"E6.1.4"),sQuery(id+"F0.wireOp",EDGE,"E6.2.1"),sQuery(id+"F0.wireOp",EDGE,"E6.2.2"),sQuery(id+"F0.wireOp",EDGE,"E6.2.3"),sQuery(id+"F0.wireOp",EDGE,"E6.2.4"),sQuery(id+"F0.wireOp",EDGE,"E6.3.1"),sQuery(id+"F0.wireOp",EDGE,"E6.3.2"),sQuery(id+"F0.wireOp",EDGE,"E6.3.3"),sQuery(id+"F0.wireOp",EDGE,"E6.3.4"),sQuery(id+"F0.wireOp",EDGE,"E6.4.1"),sQuery(id+"F0.wireOp",EDGE,"E6.4.2"),sQuery(id+"F0.wireOp",EDGE,"E6.4.3"),sQuery(id+"F0.wireOp",EDGE,"E6.4.4"),sQuery(id+"F0.wireOp",EDGE,"E6.5.1"),sQuery(id+"F0.wireOp",EDGE,"E6.5.2"),sQuery(id+"F0.wireOp",EDGE,"E6.5.3"),sQuery(id+"F0.wireOp",EDGE,"E6.5.4"),sQuery(id+"F0.wireOp",EDGE,"E6.6.1"),sQuery(id+"F0.wireOp",EDGE,"E6.6.2"),sQuery(id+"F0.wireOp",EDGE,"E6.6.3"),sQuery(id+"F0.wireOp",EDGE,"E6.6.4"),sQuery(id+"F0.wireOp",EDGE,"E6.7.1"),sQuery(id+"F0.wireOp",EDGE,"E6.7.2"),sQuery(id+"F0.wireOp",EDGE,"E6.7.3"),sQuery(id+"F0.wireOp",EDGE,"E6.7.4"),sQuery(id+"F0.wireOp",EDGE,"E6.8.1"),sQuery(id+"F0.wireOp",EDGE,"E6.8.2"),sQuery(id+"F0.wireOp",EDGE,"E6.8.3"),sQuery(id+"F0.wireOp",EDGE,"E6.8.4"),sQuery(id+"F0.wireOp",EDGE,"E6.9.1"),sQuery(id+"F0.wireOp",EDGE,"E6.9.2"),sQuery(id+"F0.wireOp",EDGE,"E6.9.3"),sQuery(id+"F0.wireOp",EDGE,"E6.9.4"),sQuery(id+"F0.wireOp",EDGE,"E6.10.1"),sQuery(id+"F0.wireOp",EDGE,"E6.10.2"),sQuery(id+"F0.wireOp",EDGE,"E6.10.3"),sQuery(id+"F0.wireOp",EDGE,"E6.10.4"),sQuery(id+"F0.wireOp",EDGE,"E6.11.1"),sQuery(id+"F0.wireOp",EDGE,"E6.11.2"),sQuery(id+"F0.wireOp",EDGE,"E6.11.3"),sQuery(id+"F0.wireOp",EDGE,"E6.11.4"),sQuery(id+"F0.wireOp",EDGE,"E6.12.1"),sQuery(id+"F0.wireOp",EDGE,"E6.12.2"),sQuery(id+"F0.wireOp",EDGE,"E6.12.3"),sQuery(id+"F0.wireOp",EDGE,"E6.12.4"),sQuery(id+"F0.wireOp",EDGE,"E6.13.1"),sQuery(id+"F0.wireOp",EDGE,"E6.13.2"),sQuery(id+"F0.wireOp",EDGE,"E6.13.3"),sQuery(id+"F0.wireOp",EDGE,"E6.13.4"),sQuery(id+"F0.wireOp",EDGE,"E6.14.1"),sQuery(id+"F0.wireOp",EDGE,"E6.14.2"),sQuery(id+"F0.wireOp",EDGE,"E6.14.3"),sQuery(id+"F0.wireOp",EDGE,"E6.14.4"),sQuery(id+"F0.wireOp",EDGE,"E6.15.1"),sQuery(id+"F0.wireOp",EDGE,"E6.15.2"),sQuery(id+"F0.wireOp",EDGE,"E6.15.3"),sQuery(id+"F0.wireOp",EDGE,"E6.15.4"),sQuery(id+"F0.wireOp",EDGE,"E6.16.1"),sQuery(id+"F0.wireOp",EDGE,"E6.16.2"),sQuery(id+"F0.wireOp",EDGE,"E6.16.3"),sQuery(id+"F0.wireOp",EDGE,"E6.16.4"),sQuery(id+"F0.wireOp",EDGE,"E6.17.1"),sQuery(id+"F0.wireOp",EDGE,"E6.17.2"),sQuery(id+"F0.wireOp",EDGE,"E6.17.3"),sQuery(id+"F0.wireOp",EDGE,"E6.17.4"),sQuery(id+"F0.wireOp",EDGE,"E6.18.1"),sQuery(id+"F0.wireOp",EDGE,"E6.18.2"),sQuery(id+"F0.wireOp",EDGE,"E6.18.3"),sQuery(id+"F0.wireOp",EDGE,"E6.18.4"),sQuery(id+"F0.wireOp",EDGE,"E6.19.1"),sQuery(id+"F0.wireOp",EDGE,"E6.19.2"),sQuery(id+"F0.wireOp",EDGE,"E6.19.3"),sQuery(id+"F0.wireOp",EDGE,"E6.19.4"),sQuery(id+"F0.wireOp",EDGE,"E6.20.1"),sQuery(id+"F0.wireOp",EDGE,"E6.20.2"),sQuery(id+"F0.wireOp",EDGE,"E6.20.3"),sQuery(id+"F0.wireOp",EDGE,"E6.20.4"),sQuery(id+"F0.wireOp",EDGE,"E6.21.1"),sQuery(id+"F0.wireOp",EDGE,"E6.21.2"),sQuery(id+"F0.wireOp",EDGE,"E6.21.3"),sQuery(id+"F0.wireOp",EDGE,"E6.21.4"),sQuery(id+"F0.wireOp",EDGE,"E6.22.1"),sQuery(id+"F0.wireOp",EDGE,"E6.22.2"),sQuery(id+"F0.wireOp",EDGE,"E6.22.3"),sQuery(id+"F0.wireOp",EDGE,"E6.22.4"),sQuery(id+"F0.wireOp",EDGE,"E6.23.1"),sQuery(id+"F0.wireOp",EDGE,"E6.23.2"),sQuery(id+"F0.wireOp",EDGE,"E6.23.3"),sQuery(id+"F0.wireOp",EDGE,"E6.23.4"),sQuery(id+"F0.wireOp",EDGE,"E6.24.1"),sQuery(id+"F0.wireOp",EDGE,"E6.24.2"),sQuery(id+"F0.wireOp",EDGE,"E6.24.3"),sQuery(id+"F0.wireOp",EDGE,"E6.24.4"),sQuery(id+"F0.wireOp",EDGE,"E6.25.1"),sQuery(id+"F0.wireOp",EDGE,"E6.25.2"),sQuery(id+"F0.wireOp",EDGE,"E6.25.3"),sQuery(id+"F0.wireOp",EDGE,"E6.25.4"),sQuery(id+"F0.wireOp",EDGE,"E6.26.1"),sQuery(id+"F0.wireOp",EDGE,"E6.26.2"),sQuery(id+"F0.wireOp",EDGE,"E6.26.3"),sQuery(id+"F0.wireOp",EDGE,"E6.26.4"),sQuery(id+"F0.wireOp",EDGE,"E6.27.1"),sQuery(id+"F0.wireOp",EDGE,"E6.27.2"),sQuery(id+"F0.wireOp",EDGE,"E6.27.3"),sQuery(id+"F0.wireOp",EDGE,"E6.27.4"),sQuery(id+"F0.wireOp",EDGE,"E6.28.1"),sQuery(id+"F0.wireOp",EDGE,"E6.28.2"),sQuery(id+"F0.wireOp",EDGE,"E6.28.3"),sQuery(id+"F0.wireOp",EDGE,"E6.28.4"),sQuery(id+"F0.wireOp",EDGE,"E6.29.1"),sQuery(id+"F0.wireOp",EDGE,"E6.29.2"),sQuery(id+"F0.wireOp",EDGE,"E6.29.3"),sQuery(id+"F0.wireOp",EDGE,"E6.29.4"),sQuery(id+"F0.wireOp",EDGE,"E6.30.1"),sQuery(id+"F0.wireOp",EDGE,"E6.30.2"),sQuery(id+"F0.wireOp",EDGE,"E6.30.3"),sQuery(id+"F0.wireOp",EDGE,"E6.30.4"),sQuery(id+"F0.wireOp",EDGE,"E6.31.1"),sQuery(id+"F0.wireOp",EDGE,"E6.31.2"),sQuery(id+"F0.wireOp",EDGE,"E6.31.3"),sQuery(id+"F0.wireOp",EDGE,"E6.31.4"),sQuery(id+"F0.wireOp",EDGE,"E6.32.1"),sQuery(id+"F0.wireOp",EDGE,"E6.32.2"),sQuery(id+"F0.wireOp",EDGE,"E6.32.3"),sQuery(id+"F0.wireOp",EDGE,"E6.32.4"),subQ1,sQuery(id+"F0.wireOp",EDGE,"E6.33.2"),subQ0,sQuery(id+"F0.wireOp",EDGE,"E6.33.4"),sQuery(id+"F0.wireOp",EDGE,"E6.34.1"),sQuery(id+"F0.wireOp",EDGE,"E6.34.2"),sQuery(id+"F0.wireOp",EDGE,"E6.34.3"),sQuery(id+"F0.wireOp",EDGE,"E6.34.4"),sQuery(id+"F0.wireOp",EDGE,"E6.35.1"),sQuery(id+"F0.wireOp",EDGE,"E6.35.2"),sQuery(id+"F0.wireOp",EDGE,"E6.35.3"),sQuery(id+"F0.wireOp",EDGE,"E6.35.4"),sQuery(id+"F0.wireOp",EDGE,"E6.36.1"),sQuery(id+"F0.wireOp",EDGE,"E6.36.2"),sQuery(id+"F0.wireOp",EDGE,"E6.36.3"),sQuery(id+"F0.wireOp",EDGE,"E6.36.4"),sQuery(id+"F0.wireOp",EDGE,"E6.37.1"),sQuery(id+"F0.wireOp",EDGE,"E6.37.2"),sQuery(id+"F0.wireOp",EDGE,"E6.37.3"),sQuery(id+"F0.wireOp",EDGE,"E6.37.4"),sQuery(id+"F0.wireOp",EDGE,"E6.38.1"),sQuery(id+"F0.wireOp",EDGE,"E6.38.2"),sQuery(id+"F0.wireOp",EDGE,"E6.38.3"),sQuery(id+"F0.wireOp",EDGE,"E6.38.4"),sQuery(id+"F0.wireOp",EDGE,"E6.39.1"),sQuery(id+"F0.wireOp",EDGE,"E6.39.2"),sQuery(id+"F0.wireOp",EDGE,"E6.39.3"),sQuery(id+"F0.wireOp",EDGE,"E6.39.4"),sQuery(id+"F0.wireOp",EDGE,"E6.40.1"),sQuery(id+"F0.wireOp",EDGE,"E6.40.2"),sQuery(id+"F0.wireOp",EDGE,"E6.40.3"),sQuery(id+"F0.wireOp",EDGE,"E6.40.4"),sQuery(id+"F0.wireOp",EDGE,"E6.41.1"),sQuery(id+"F0.wireOp",EDGE,"E6.41.2"),sQuery(id+"F0.wireOp",EDGE,"E6.41.3"),sQuery(id+"F0.wireOp",EDGE,"E6.41.4"),sQuery(id+"F0.wireOp",EDGE,"E6.42.1"),sQuery(id+"F0.wireOp",EDGE,"E6.42.2"),sQuery(id+"F0.wireOp",EDGE,"E6.42.3"),sQuery(id+"F0.wireOp",EDGE,"E6.42.4"),sQuery(id+"F0.wireOp",EDGE,"E6.43.1"),sQuery(id+"F0.wireOp",EDGE,"E6.43.2"),sQuery(id+"F0.wireOp",EDGE,"E6.43.3"),sQuery(id+"F0.wireOp",EDGE,"E6.43.4"),sQuery(id+"F0.wireOp",EDGE,"E7"),sQuery(id+"F0.wireOp",EDGE,"E8.1.0"),sQuery(id+"F0.wireOp",EDGE,"E8.2.0"),sQuery(id+"F0.wireOp",EDGE,"E8.3.0"),sQuery(id+"F0.wireOp",EDGE,"E8.4.0"),sQuery(id+"F0.wireOp",EDGE,"E8.5.0"),sQuery(id+"F0.wireOp",EDGE,"E8.6.0"),sQuery(id+"F0.wireOp",EDGE,"E8.7.0"),sQuery(id+"F0.wireOp",EDGE,"E8.8.0"),sQuery(id+"F0.wireOp",EDGE,"E8.9.0"),sQuery(id+"F0.wireOp",EDGE,"E8.10.0"),sQuery(id+"F0.wireOp",EDGE,"E8.11.0"),sQuery(id+"F0.wireOp",EDGE,"E8.12.0"),sQuery(id+"F0.wireOp",EDGE,"E8.13.0"),sQuery(id+"F0.wireOp",EDGE,"E8.14.0"),sQuery(id+"F0.wireOp",EDGE,"E8.15.0"),sQuery(id+"F0.wireOp",EDGE,"E8.16.0"),sQuery(id+"F0.wireOp",EDGE,"E8.17.0"),sQuery(id+"F0.wireOp",EDGE,"E8.18.0"),sQuery(id+"F0.wireOp",EDGE,"E8.19.0"),sQuery(id+"F0.wireOp",EDGE,"E8.20.0"),sQuery(id+"F0.wireOp",EDGE,"E8.21.0"),sQuery(id+"F0.wireOp",EDGE,"E8.22.0"),sQuery(id+"F0.wireOp",EDGE,"E8.23.0"),sQuery(id+"F0.wireOp",EDGE,"E8.24.0"),sQuery(id+"F0.wireOp",EDGE,"E8.25.0"),sQuery(id+"F0.wireOp",EDGE,"E8.26.0"),sQuery(id+"F0.wireOp",EDGE,"E8.27.0"),sQuery(id+"F0.wireOp",EDGE,"E8.28.0"),sQuery(id+"F0.wireOp",EDGE,"E8.29.0"),sQuery(id+"F0.wireOp",EDGE,"E8.30.0"),sQuery(id+"F0.wireOp",EDGE,"E8.31.0"),sQuery(id+"F0.wireOp",EDGE,"E8.32.0"),sQuery(id+"F0.wireOp",EDGE,"E8.33.0"),sQuery(id+"F0.wireOp",EDGE,"E8.34.0"),sQuery(id+"F0.wireOp",EDGE,"E8.35.0"),sQuery(id+"F0.wireOp",EDGE,"E8.36.0"),sQuery(id+"F0.wireOp",EDGE,"E8.37.0"),sQuery(id+"F0.wireOp",EDGE,"E8.38.0"),sQuery(id+"F0.wireOp",EDGE,"E8.39.0"),sQuery(id+"F0.wireOp",EDGE,"E8.40.0"),sQuery(id+"F0.wireOp",EDGE,"E8.41.0"),sQuery(id+"F0.wireOp",EDGE,"E8.42.0"),sQuery(id+"F0.wireOp",EDGE,"E8.43.0")])],"isStart":false})]});}
            var Q6;
            {var subQ0=sQuery(id+"F0.wireOp",EDGE,"E6.35.3");var subQ1=sQuery(id+"F0.wireOp",EDGE,"E6.35.1");Q6=makeQuery(id+"F2.opFillet","BLEND_EDGE",EDGE,{"blendedFrom":[makeQuery(id+"F1.opExtrude","SWEPT_EDGE",EDGE,{"disambiguationData":[OSD([sQuery(id+"F0.wireOp",EDGE,"E6.35.0"),subQ1,subQ0])]}),makeQuery(id+"F1.opExtrude","CAP_FACE",FACE,{"disambiguationData":[OSD([sQuery(id+"F0.wireOp",EDGE,"E0"),sQuery(id+"F0.wireOp",EDGE,"E1"),sQuery(id+"F0.wireOp",EDGE,"E2"),sQuery(id+"F0.wireOp",EDGE,"E4"),sQuery(id+"F0.wireOp",EDGE,"E5"),sQuery(id+"F0.wireOp",EDGE,"E6.1.1"),sQuery(id+"F0.wireOp",EDGE,"E6.1.2"),sQuery(id+"F0.wireOp",EDGE,"E6.1.3"),sQuery(id+"F0.wireOp",EDGE,"E6.1.4"),sQuery(id+"F0.wireOp",EDGE,"E6.2.1"),sQuery(id+"F0.wireOp",EDGE,"E6.2.2"),sQuery(id+"F0.wireOp",EDGE,"E6.2.3"),sQuery(id+"F0.wireOp",EDGE,"E6.2.4"),sQuery(id+"F0.wireOp",EDGE,"E6.3.1"),sQuery(id+"F0.wireOp",EDGE,"E6.3.2"),sQuery(id+"F0.wireOp",EDGE,"E6.3.3"),sQuery(id+"F0.wireOp",EDGE,"E6.3.4"),sQuery(id+"F0.wireOp",EDGE,"E6.4.1"),sQuery(id+"F0.wireOp",EDGE,"E6.4.2"),sQuery(id+"F0.wireOp",EDGE,"E6.4.3"),sQuery(id+"F0.wireOp",EDGE,"E6.4.4"),sQuery(id+"F0.wireOp",EDGE,"E6.5.1"),sQuery(id+"F0.wireOp",EDGE,"E6.5.2"),sQuery(id+"F0.wireOp",EDGE,"E6.5.3"),sQuery(id+"F0.wireOp",EDGE,"E6.5.4"),sQuery(id+"F0.wireOp",EDGE,"E6.6.1"),sQuery(id+"F0.wireOp",EDGE,"E6.6.2"),sQuery(id+"F0.wireOp",EDGE,"E6.6.3"),sQuery(id+"F0.wireOp",EDGE,"E6.6.4"),sQuery(id+"F0.wireOp",EDGE,"E6.7.1"),sQuery(id+"F0.wireOp",EDGE,"E6.7.2"),sQuery(id+"F0.wireOp",EDGE,"E6.7.3"),sQuery(id+"F0.wireOp",EDGE,"E6.7.4"),sQuery(id+"F0.wireOp",EDGE,"E6.8.1"),sQuery(id+"F0.wireOp",EDGE,"E6.8.2"),sQuery(id+"F0.wireOp",EDGE,"E6.8.3"),sQuery(id+"F0.wireOp",EDGE,"E6.8.4"),sQuery(id+"F0.wireOp",EDGE,"E6.9.1"),sQuery(id+"F0.wireOp",EDGE,"E6.9.2"),sQuery(id+"F0.wireOp",EDGE,"E6.9.3"),sQuery(id+"F0.wireOp",EDGE,"E6.9.4"),sQuery(id+"F0.wireOp",EDGE,"E6.10.1"),sQuery(id+"F0.wireOp",EDGE,"E6.10.2"),sQuery(id+"F0.wireOp",EDGE,"E6.10.3"),sQuery(id+"F0.wireOp",EDGE,"E6.10.4"),sQuery(id+"F0.wireOp",EDGE,"E6.11.1"),sQuery(id+"F0.wireOp",EDGE,"E6.11.2"),sQuery(id+"F0.wireOp",EDGE,"E6.11.3"),sQuery(id+"F0.wireOp",EDGE,"E6.11.4"),sQuery(id+"F0.wireOp",EDGE,"E6.12.1"),sQuery(id+"F0.wireOp",EDGE,"E6.12.2"),sQuery(id+"F0.wireOp",EDGE,"E6.12.3"),sQuery(id+"F0.wireOp",EDGE,"E6.12.4"),sQuery(id+"F0.wireOp",EDGE,"E6.13.1"),sQuery(id+"F0.wireOp",EDGE,"E6.13.2"),sQuery(id+"F0.wireOp",EDGE,"E6.13.3"),sQuery(id+"F0.wireOp",EDGE,"E6.13.4"),sQuery(id+"F0.wireOp",EDGE,"E6.14.1"),sQuery(id+"F0.wireOp",EDGE,"E6.14.2"),sQuery(id+"F0.wireOp",EDGE,"E6.14.3"),sQuery(id+"F0.wireOp",EDGE,"E6.14.4"),sQuery(id+"F0.wireOp",EDGE,"E6.15.1"),sQuery(id+"F0.wireOp",EDGE,"E6.15.2"),sQuery(id+"F0.wireOp",EDGE,"E6.15.3"),sQuery(id+"F0.wireOp",EDGE,"E6.15.4"),sQuery(id+"F0.wireOp",EDGE,"E6.16.1"),sQuery(id+"F0.wireOp",EDGE,"E6.16.2"),sQuery(id+"F0.wireOp",EDGE,"E6.16.3"),sQuery(id+"F0.wireOp",EDGE,"E6.16.4"),sQuery(id+"F0.wireOp",EDGE,"E6.17.1"),sQuery(id+"F0.wireOp",EDGE,"E6.17.2"),sQuery(id+"F0.wireOp",EDGE,"E6.17.3"),sQuery(id+"F0.wireOp",EDGE,"E6.17.4"),sQuery(id+"F0.wireOp",EDGE,"E6.18.1"),sQuery(id+"F0.wireOp",EDGE,"E6.18.2"),sQuery(id+"F0.wireOp",EDGE,"E6.18.3"),sQuery(id+"F0.wireOp",EDGE,"E6.18.4"),sQuery(id+"F0.wireOp",EDGE,"E6.19.1"),sQuery(id+"F0.wireOp",EDGE,"E6.19.2"),sQuery(id+"F0.wireOp",EDGE,"E6.19.3"),sQuery(id+"F0.wireOp",EDGE,"E6.19.4"),sQuery(id+"F0.wireOp",EDGE,"E6.20.1"),sQuery(id+"F0.wireOp",EDGE,"E6.20.2"),sQuery(id+"F0.wireOp",EDGE,"E6.20.3"),sQuery(id+"F0.wireOp",EDGE,"E6.20.4"),sQuery(id+"F0.wireOp",EDGE,"E6.21.1"),sQuery(id+"F0.wireOp",EDGE,"E6.21.2"),sQuery(id+"F0.wireOp",EDGE,"E6.21.3"),sQuery(id+"F0.wireOp",EDGE,"E6.21.4"),sQuery(id+"F0.wireOp",EDGE,"E6.22.1"),sQuery(id+"F0.wireOp",EDGE,"E6.22.2"),sQuery(id+"F0.wireOp",EDGE,"E6.22.3"),sQuery(id+"F0.wireOp",EDGE,"E6.22.4"),sQuery(id+"F0.wireOp",EDGE,"E6.23.1"),sQuery(id+"F0.wireOp",EDGE,"E6.23.2"),sQuery(id+"F0.wireOp",EDGE,"E6.23.3"),sQuery(id+"F0.wireOp",EDGE,"E6.23.4"),sQuery(id+"F0.wireOp",EDGE,"E6.24.1"),sQuery(id+"F0.wireOp",EDGE,"E6.24.2"),sQuery(id+"F0.wireOp",EDGE,"E6.24.3"),sQuery(id+"F0.wireOp",EDGE,"E6.24.4"),sQuery(id+"F0.wireOp",EDGE,"E6.25.1"),sQuery(id+"F0.wireOp",EDGE,"E6.25.2"),sQuery(id+"F0.wireOp",EDGE,"E6.25.3"),sQuery(id+"F0.wireOp",EDGE,"E6.25.4"),sQuery(id+"F0.wireOp",EDGE,"E6.26.1"),sQuery(id+"F0.wireOp",EDGE,"E6.26.2"),sQuery(id+"F0.wireOp",EDGE,"E6.26.3"),sQuery(id+"F0.wireOp",EDGE,"E6.26.4"),sQuery(id+"F0.wireOp",EDGE,"E6.27.1"),sQuery(id+"F0.wireOp",EDGE,"E6.27.2"),sQuery(id+"F0.wireOp",EDGE,"E6.27.3"),sQuery(id+"F0.wireOp",EDGE,"E6.27.4"),sQuery(id+"F0.wireOp",EDGE,"E6.28.1"),sQuery(id+"F0.wireOp",EDGE,"E6.28.2"),sQuery(id+"F0.wireOp",EDGE,"E6.28.3"),sQuery(id+"F0.wireOp",EDGE,"E6.28.4"),sQuery(id+"F0.wireOp",EDGE,"E6.29.1"),sQuery(id+"F0.wireOp",EDGE,"E6.29.2"),sQuery(id+"F0.wireOp",EDGE,"E6.29.3"),sQuery(id+"F0.wireOp",EDGE,"E6.29.4"),sQuery(id+"F0.wireOp",EDGE,"E6.30.1"),sQuery(id+"F0.wireOp",EDGE,"E6.30.2"),sQuery(id+"F0.wireOp",EDGE,"E6.30.3"),sQuery(id+"F0.wireOp",EDGE,"E6.30.4"),sQuery(id+"F0.wireOp",EDGE,"E6.31.1"),sQuery(id+"F0.wireOp",EDGE,"E6.31.2"),sQuery(id+"F0.wireOp",EDGE,"E6.31.3"),sQuery(id+"F0.wireOp",EDGE,"E6.31.4"),sQuery(id+"F0.wireOp",EDGE,"E6.32.1"),sQuery(id+"F0.wireOp",EDGE,"E6.32.2"),sQuery(id+"F0.wireOp",EDGE,"E6.32.3"),sQuery(id+"F0.wireOp",EDGE,"E6.32.4"),sQuery(id+"F0.wireOp",EDGE,"E6.33.1"),sQuery(id+"F0.wireOp",EDGE,"E6.33.2"),sQuery(id+"F0.wireOp",EDGE,"E6.33.3"),sQuery(id+"F0.wireOp",EDGE,"E6.33.4"),sQuery(id+"F0.wireOp",EDGE,"E6.34.1"),sQuery(id+"F0.wireOp",EDGE,"E6.34.2"),sQuery(id+"F0.wireOp",EDGE,"E6.34.3"),sQuery(id+"F0.wireOp",EDGE,"E6.34.4"),subQ1,sQuery(id+"F0.wireOp",EDGE,"E6.35.2"),subQ0,sQuery(id+"F0.wireOp",EDGE,"E6.35.4"),sQuery(id+"F0.wireOp",EDGE,"E6.36.1"),sQuery(id+"F0.wireOp",EDGE,"E6.36.2"),sQuery(id+"F0.wireOp",EDGE,"E6.36.3"),sQuery(id+"F0.wireOp",EDGE,"E6.36.4"),sQuery(id+"F0.wireOp",EDGE,"E6.37.1"),sQuery(id+"F0.wireOp",EDGE,"E6.37.2"),sQuery(id+"F0.wireOp",EDGE,"E6.37.3"),sQuery(id+"F0.wireOp",EDGE,"E6.37.4"),sQuery(id+"F0.wireOp",EDGE,"E6.38.1"),sQuery(id+"F0.wireOp",EDGE,"E6.38.2"),sQuery(id+"F0.wireOp",EDGE,"E6.38.3"),sQuery(id+"F0.wireOp",EDGE,"E6.38.4"),sQuery(id+"F0.wireOp",EDGE,"E6.39.1"),sQuery(id+"F0.wireOp",EDGE,"E6.39.2"),sQuery(id+"F0.wireOp",EDGE,"E6.39.3"),sQuery(id+"F0.wireOp",EDGE,"E6.39.4"),sQuery(id+"F0.wireOp",EDGE,"E6.40.1"),sQuery(id+"F0.wireOp",EDGE,"E6.40.2"),sQuery(id+"F0.wireOp",EDGE,"E6.40.3"),sQuery(id+"F0.wireOp",EDGE,"E6.40.4"),sQuery(id+"F0.wireOp",EDGE,"E6.41.1"),sQuery(id+"F0.wireOp",EDGE,"E6.41.2"),sQuery(id+"F0.wireOp",EDGE,"E6.41.3"),sQuery(id+"F0.wireOp",EDGE,"E6.41.4"),sQuery(id+"F0.wireOp",EDGE,"E6.42.1"),sQuery(id+"F0.wireOp",EDGE,"E6.42.2"),sQuery(id+"F0.wireOp",EDGE,"E6.42.3"),sQuery(id+"F0.wireOp",EDGE,"E6.42.4"),sQuery(id+"F0.wireOp",EDGE,"E6.43.1"),sQuery(id+"F0.wireOp",EDGE,"E6.43.2"),sQuery(id+"F0.wireOp",EDGE,"E6.43.3"),sQuery(id+"F0.wireOp",EDGE,"E6.43.4"),sQuery(id+"F0.wireOp",EDGE,"E7"),sQuery(id+"F0.wireOp",EDGE,"E8.1.0"),sQuery(id+"F0.wireOp",EDGE,"E8.2.0"),sQuery(id+"F0.wireOp",EDGE,"E8.3.0"),sQuery(id+"F0.wireOp",EDGE,"E8.4.0"),sQuery(id+"F0.wireOp",EDGE,"E8.5.0"),sQuery(id+"F0.wireOp",EDGE,"E8.6.0"),sQuery(id+"F0.wireOp",EDGE,"E8.7.0"),sQuery(id+"F0.wireOp",EDGE,"E8.8.0"),sQuery(id+"F0.wireOp",EDGE,"E8.9.0"),sQuery(id+"F0.wireOp",EDGE,"E8.10.0"),sQuery(id+"F0.wireOp",EDGE,"E8.11.0"),sQuery(id+"F0.wireOp",EDGE,"E8.12.0"),sQuery(id+"F0.wireOp",EDGE,"E8.13.0"),sQuery(id+"F0.wireOp",EDGE,"E8.14.0"),sQuery(id+"F0.wireOp",EDGE,"E8.15.0"),sQuery(id+"F0.wireOp",EDGE,"E8.16.0"),sQuery(id+"F0.wireOp",EDGE,"E8.17.0"),sQuery(id+"F0.wireOp",EDGE,"E8.18.0"),sQuery(id+"F0.wireOp",EDGE,"E8.19.0"),sQuery(id+"F0.wireOp",EDGE,"E8.20.0"),sQuery(id+"F0.wireOp",EDGE,"E8.21.0"),sQuery(id+"F0.wireOp",EDGE,"E8.22.0"),sQuery(id+"F0.wireOp",EDGE,"E8.23.0"),sQuery(id+"F0.wireOp",EDGE,"E8.24.0"),sQuery(id+"F0.wireOp",EDGE,"E8.25.0"),sQuery(id+"F0.wireOp",EDGE,"E8.26.0"),sQuery(id+"F0.wireOp",EDGE,"E8.27.0"),sQuery(id+"F0.wireOp",EDGE,"E8.28.0"),sQuery(id+"F0.wireOp",EDGE,"E8.29.0"),sQuery(id+"F0.wireOp",EDGE,"E8.30.0"),sQuery(id+"F0.wireOp",EDGE,"E8.31.0"),sQuery(id+"F0.wireOp",EDGE,"E8.32.0"),sQuery(id+"F0.wireOp",EDGE,"E8.33.0"),sQuery(id+"F0.wireOp",EDGE,"E8.34.0"),sQuery(id+"F0.wireOp",EDGE,"E8.35.0"),sQuery(id+"F0.wireOp",EDGE,"E8.36.0"),sQuery(id+"F0.wireOp",EDGE,"E8.37.0"),sQuery(id+"F0.wireOp",EDGE,"E8.38.0"),sQuery(id+"F0.wireOp",EDGE,"E8.39.0"),sQuery(id+"F0.wireOp",EDGE,"E8.40.0"),sQuery(id+"F0.wireOp",EDGE,"E8.41.0"),sQuery(id+"F0.wireOp",EDGE,"E8.42.0"),sQuery(id+"F0.wireOp",EDGE,"E8.43.0")])],"isStart":false})],"blendedInto":[makeQuery(id+"F1.opExtrude","CAP_FACE",FACE,{"disambiguationData":[OSD([sQuery(id+"F0.wireOp",EDGE,"E0"),sQuery(id+"F0.wireOp",EDGE,"E1"),sQuery(id+"F0.wireOp",EDGE,"E2"),sQuery(id+"F0.wireOp",EDGE,"E4"),sQuery(id+"F0.wireOp",EDGE,"E5"),sQuery(id+"F0.wireOp",EDGE,"E6.1.1"),sQuery(id+"F0.wireOp",EDGE,"E6.1.2"),sQuery(id+"F0.wireOp",EDGE,"E6.1.3"),sQuery(id+"F0.wireOp",EDGE,"E6.1.4"),sQuery(id+"F0.wireOp",EDGE,"E6.2.1"),sQuery(id+"F0.wireOp",EDGE,"E6.2.2"),sQuery(id+"F0.wireOp",EDGE,"E6.2.3"),sQuery(id+"F0.wireOp",EDGE,"E6.2.4"),sQuery(id+"F0.wireOp",EDGE,"E6.3.1"),sQuery(id+"F0.wireOp",EDGE,"E6.3.2"),sQuery(id+"F0.wireOp",EDGE,"E6.3.3"),sQuery(id+"F0.wireOp",EDGE,"E6.3.4"),sQuery(id+"F0.wireOp",EDGE,"E6.4.1"),sQuery(id+"F0.wireOp",EDGE,"E6.4.2"),sQuery(id+"F0.wireOp",EDGE,"E6.4.3"),sQuery(id+"F0.wireOp",EDGE,"E6.4.4"),sQuery(id+"F0.wireOp",EDGE,"E6.5.1"),sQuery(id+"F0.wireOp",EDGE,"E6.5.2"),sQuery(id+"F0.wireOp",EDGE,"E6.5.3"),sQuery(id+"F0.wireOp",EDGE,"E6.5.4"),sQuery(id+"F0.wireOp",EDGE,"E6.6.1"),sQuery(id+"F0.wireOp",EDGE,"E6.6.2"),sQuery(id+"F0.wireOp",EDGE,"E6.6.3"),sQuery(id+"F0.wireOp",EDGE,"E6.6.4"),sQuery(id+"F0.wireOp",EDGE,"E6.7.1"),sQuery(id+"F0.wireOp",EDGE,"E6.7.2"),sQuery(id+"F0.wireOp",EDGE,"E6.7.3"),sQuery(id+"F0.wireOp",EDGE,"E6.7.4"),sQuery(id+"F0.wireOp",EDGE,"E6.8.1"),sQuery(id+"F0.wireOp",EDGE,"E6.8.2"),sQuery(id+"F0.wireOp",EDGE,"E6.8.3"),sQuery(id+"F0.wireOp",EDGE,"E6.8.4"),sQuery(id+"F0.wireOp",EDGE,"E6.9.1"),sQuery(id+"F0.wireOp",EDGE,"E6.9.2"),sQuery(id+"F0.wireOp",EDGE,"E6.9.3"),sQuery(id+"F0.wireOp",EDGE,"E6.9.4"),sQuery(id+"F0.wireOp",EDGE,"E6.10.1"),sQuery(id+"F0.wireOp",EDGE,"E6.10.2"),sQuery(id+"F0.wireOp",EDGE,"E6.10.3"),sQuery(id+"F0.wireOp",EDGE,"E6.10.4"),sQuery(id+"F0.wireOp",EDGE,"E6.11.1"),sQuery(id+"F0.wireOp",EDGE,"E6.11.2"),sQuery(id+"F0.wireOp",EDGE,"E6.11.3"),sQuery(id+"F0.wireOp",EDGE,"E6.11.4"),sQuery(id+"F0.wireOp",EDGE,"E6.12.1"),sQuery(id+"F0.wireOp",EDGE,"E6.12.2"),sQuery(id+"F0.wireOp",EDGE,"E6.12.3"),sQuery(id+"F0.wireOp",EDGE,"E6.12.4"),sQuery(id+"F0.wireOp",EDGE,"E6.13.1"),sQuery(id+"F0.wireOp",EDGE,"E6.13.2"),sQuery(id+"F0.wireOp",EDGE,"E6.13.3"),sQuery(id+"F0.wireOp",EDGE,"E6.13.4"),sQuery(id+"F0.wireOp",EDGE,"E6.14.1"),sQuery(id+"F0.wireOp",EDGE,"E6.14.2"),sQuery(id+"F0.wireOp",EDGE,"E6.14.3"),sQuery(id+"F0.wireOp",EDGE,"E6.14.4"),sQuery(id+"F0.wireOp",EDGE,"E6.15.1"),sQuery(id+"F0.wireOp",EDGE,"E6.15.2"),sQuery(id+"F0.wireOp",EDGE,"E6.15.3"),sQuery(id+"F0.wireOp",EDGE,"E6.15.4"),sQuery(id+"F0.wireOp",EDGE,"E6.16.1"),sQuery(id+"F0.wireOp",EDGE,"E6.16.2"),sQuery(id+"F0.wireOp",EDGE,"E6.16.3"),sQuery(id+"F0.wireOp",EDGE,"E6.16.4"),sQuery(id+"F0.wireOp",EDGE,"E6.17.1"),sQuery(id+"F0.wireOp",EDGE,"E6.17.2"),sQuery(id+"F0.wireOp",EDGE,"E6.17.3"),sQuery(id+"F0.wireOp",EDGE,"E6.17.4"),sQuery(id+"F0.wireOp",EDGE,"E6.18.1"),sQuery(id+"F0.wireOp",EDGE,"E6.18.2"),sQuery(id+"F0.wireOp",EDGE,"E6.18.3"),sQuery(id+"F0.wireOp",EDGE,"E6.18.4"),sQuery(id+"F0.wireOp",EDGE,"E6.19.1"),sQuery(id+"F0.wireOp",EDGE,"E6.19.2"),sQuery(id+"F0.wireOp",EDGE,"E6.19.3"),sQuery(id+"F0.wireOp",EDGE,"E6.19.4"),sQuery(id+"F0.wireOp",EDGE,"E6.20.1"),sQuery(id+"F0.wireOp",EDGE,"E6.20.2"),sQuery(id+"F0.wireOp",EDGE,"E6.20.3"),sQuery(id+"F0.wireOp",EDGE,"E6.20.4"),sQuery(id+"F0.wireOp",EDGE,"E6.21.1"),sQuery(id+"F0.wireOp",EDGE,"E6.21.2"),sQuery(id+"F0.wireOp",EDGE,"E6.21.3"),sQuery(id+"F0.wireOp",EDGE,"E6.21.4"),sQuery(id+"F0.wireOp",EDGE,"E6.22.1"),sQuery(id+"F0.wireOp",EDGE,"E6.22.2"),sQuery(id+"F0.wireOp",EDGE,"E6.22.3"),sQuery(id+"F0.wireOp",EDGE,"E6.22.4"),sQuery(id+"F0.wireOp",EDGE,"E6.23.1"),sQuery(id+"F0.wireOp",EDGE,"E6.23.2"),sQuery(id+"F0.wireOp",EDGE,"E6.23.3"),sQuery(id+"F0.wireOp",EDGE,"E6.23.4"),sQuery(id+"F0.wireOp",EDGE,"E6.24.1"),sQuery(id+"F0.wireOp",EDGE,"E6.24.2"),sQuery(id+"F0.wireOp",EDGE,"E6.24.3"),sQuery(id+"F0.wireOp",EDGE,"E6.24.4"),sQuery(id+"F0.wireOp",EDGE,"E6.25.1"),sQuery(id+"F0.wireOp",EDGE,"E6.25.2"),sQuery(id+"F0.wireOp",EDGE,"E6.25.3"),sQuery(id+"F0.wireOp",EDGE,"E6.25.4"),sQuery(id+"F0.wireOp",EDGE,"E6.26.1"),sQuery(id+"F0.wireOp",EDGE,"E6.26.2"),sQuery(id+"F0.wireOp",EDGE,"E6.26.3"),sQuery(id+"F0.wireOp",EDGE,"E6.26.4"),sQuery(id+"F0.wireOp",EDGE,"E6.27.1"),sQuery(id+"F0.wireOp",EDGE,"E6.27.2"),sQuery(id+"F0.wireOp",EDGE,"E6.27.3"),sQuery(id+"F0.wireOp",EDGE,"E6.27.4"),sQuery(id+"F0.wireOp",EDGE,"E6.28.1"),sQuery(id+"F0.wireOp",EDGE,"E6.28.2"),sQuery(id+"F0.wireOp",EDGE,"E6.28.3"),sQuery(id+"F0.wireOp",EDGE,"E6.28.4"),sQuery(id+"F0.wireOp",EDGE,"E6.29.1"),sQuery(id+"F0.wireOp",EDGE,"E6.29.2"),sQuery(id+"F0.wireOp",EDGE,"E6.29.3"),sQuery(id+"F0.wireOp",EDGE,"E6.29.4"),sQuery(id+"F0.wireOp",EDGE,"E6.30.1"),sQuery(id+"F0.wireOp",EDGE,"E6.30.2"),sQuery(id+"F0.wireOp",EDGE,"E6.30.3"),sQuery(id+"F0.wireOp",EDGE,"E6.30.4"),sQuery(id+"F0.wireOp",EDGE,"E6.31.1"),sQuery(id+"F0.wireOp",EDGE,"E6.31.2"),sQuery(id+"F0.wireOp",EDGE,"E6.31.3"),sQuery(id+"F0.wireOp",EDGE,"E6.31.4"),sQuery(id+"F0.wireOp",EDGE,"E6.32.1"),sQuery(id+"F0.wireOp",EDGE,"E6.32.2"),sQuery(id+"F0.wireOp",EDGE,"E6.32.3"),sQuery(id+"F0.wireOp",EDGE,"E6.32.4"),sQuery(id+"F0.wireOp",EDGE,"E6.33.1"),sQuery(id+"F0.wireOp",EDGE,"E6.33.2"),sQuery(id+"F0.wireOp",EDGE,"E6.33.3"),sQuery(id+"F0.wireOp",EDGE,"E6.33.4"),sQuery(id+"F0.wireOp",EDGE,"E6.34.1"),sQuery(id+"F0.wireOp",EDGE,"E6.34.2"),sQuery(id+"F0.wireOp",EDGE,"E6.34.3"),sQuery(id+"F0.wireOp",EDGE,"E6.34.4"),subQ1,sQuery(id+"F0.wireOp",EDGE,"E6.35.2"),subQ0,sQuery(id+"F0.wireOp",EDGE,"E6.35.4"),sQuery(id+"F0.wireOp",EDGE,"E6.36.1"),sQuery(id+"F0.wireOp",EDGE,"E6.36.2"),sQuery(id+"F0.wireOp",EDGE,"E6.36.3"),sQuery(id+"F0.wireOp",EDGE,"E6.36.4"),sQuery(id+"F0.wireOp",EDGE,"E6.37.1"),sQuery(id+"F0.wireOp",EDGE,"E6.37.2"),sQuery(id+"F0.wireOp",EDGE,"E6.37.3"),sQuery(id+"F0.wireOp",EDGE,"E6.37.4"),sQuery(id+"F0.wireOp",EDGE,"E6.38.1"),sQuery(id+"F0.wireOp",EDGE,"E6.38.2"),sQuery(id+"F0.wireOp",EDGE,"E6.38.3"),sQuery(id+"F0.wireOp",EDGE,"E6.38.4"),sQuery(id+"F0.wireOp",EDGE,"E6.39.1"),sQuery(id+"F0.wireOp",EDGE,"E6.39.2"),sQuery(id+"F0.wireOp",EDGE,"E6.39.3"),sQuery(id+"F0.wireOp",EDGE,"E6.39.4"),sQuery(id+"F0.wireOp",EDGE,"E6.40.1"),sQuery(id+"F0.wireOp",EDGE,"E6.40.2"),sQuery(id+"F0.wireOp",EDGE,"E6.40.3"),sQuery(id+"F0.wireOp",EDGE,"E6.40.4"),sQuery(id+"F0.wireOp",EDGE,"E6.41.1"),sQuery(id+"F0.wireOp",EDGE,"E6.41.2"),sQuery(id+"F0.wireOp",EDGE,"E6.41.3"),sQuery(id+"F0.wireOp",EDGE,"E6.41.4"),sQuery(id+"F0.wireOp",EDGE,"E6.42.1"),sQuery(id+"F0.wireOp",EDGE,"E6.42.2"),sQuery(id+"F0.wireOp",EDGE,"E6.42.3"),sQuery(id+"F0.wireOp",EDGE,"E6.42.4"),sQuery(id+"F0.wireOp",EDGE,"E6.43.1"),sQuery(id+"F0.wireOp",EDGE,"E6.43.2"),sQuery(id+"F0.wireOp",EDGE,"E6.43.3"),sQuery(id+"F0.wireOp",EDGE,"E6.43.4"),sQuery(id+"F0.wireOp",EDGE,"E7"),sQuery(id+"F0.wireOp",EDGE,"E8.1.0"),sQuery(id+"F0.wireOp",EDGE,"E8.2.0"),sQuery(id+"F0.wireOp",EDGE,"E8.3.0"),sQuery(id+"F0.wireOp",EDGE,"E8.4.0"),sQuery(id+"F0.wireOp",EDGE,"E8.5.0"),sQuery(id+"F0.wireOp",EDGE,"E8.6.0"),sQuery(id+"F0.wireOp",EDGE,"E8.7.0"),sQuery(id+"F0.wireOp",EDGE,"E8.8.0"),sQuery(id+"F0.wireOp",EDGE,"E8.9.0"),sQuery(id+"F0.wireOp",EDGE,"E8.10.0"),sQuery(id+"F0.wireOp",EDGE,"E8.11.0"),sQuery(id+"F0.wireOp",EDGE,"E8.12.0"),sQuery(id+"F0.wireOp",EDGE,"E8.13.0"),sQuery(id+"F0.wireOp",EDGE,"E8.14.0"),sQuery(id+"F0.wireOp",EDGE,"E8.15.0"),sQuery(id+"F0.wireOp",EDGE,"E8.16.0"),sQuery(id+"F0.wireOp",EDGE,"E8.17.0"),sQuery(id+"F0.wireOp",EDGE,"E8.18.0"),sQuery(id+"F0.wireOp",EDGE,"E8.19.0"),sQuery(id+"F0.wireOp",EDGE,"E8.20.0"),sQuery(id+"F0.wireOp",EDGE,"E8.21.0"),sQuery(id+"F0.wireOp",EDGE,"E8.22.0"),sQuery(id+"F0.wireOp",EDGE,"E8.23.0"),sQuery(id+"F0.wireOp",EDGE,"E8.24.0"),sQuery(id+"F0.wireOp",EDGE,"E8.25.0"),sQuery(id+"F0.wireOp",EDGE,"E8.26.0"),sQuery(id+"F0.wireOp",EDGE,"E8.27.0"),sQuery(id+"F0.wireOp",EDGE,"E8.28.0"),sQuery(id+"F0.wireOp",EDGE,"E8.29.0"),sQuery(id+"F0.wireOp",EDGE,"E8.30.0"),sQuery(id+"F0.wireOp",EDGE,"E8.31.0"),sQuery(id+"F0.wireOp",EDGE,"E8.32.0"),sQuery(id+"F0.wireOp",EDGE,"E8.33.0"),sQuery(id+"F0.wireOp",EDGE,"E8.34.0"),sQuery(id+"F0.wireOp",EDGE,"E8.35.0"),sQuery(id+"F0.wireOp",EDGE,"E8.36.0"),sQuery(id+"F0.wireOp",EDGE,"E8.37.0"),sQuery(id+"F0.wireOp",EDGE,"E8.38.0"),sQuery(id+"F0.wireOp",EDGE,"E8.39.0"),sQuery(id+"F0.wireOp",EDGE,"E8.40.0"),sQuery(id+"F0.wireOp",EDGE,"E8.41.0"),sQuery(id+"F0.wireOp",EDGE,"E8.42.0"),sQuery(id+"F0.wireOp",EDGE,"E8.43.0")])],"isStart":false})]});}
            var Q7;
            {var subQ0=sQuery(id+"F0.wireOp",EDGE,"E6.37.3");var subQ1=sQuery(id+"F0.wireOp",EDGE,"E6.37.1");Q7=makeQuery(id+"F2.opFillet","BLEND_EDGE",EDGE,{"blendedFrom":[makeQuery(id+"F1.opExtrude","SWEPT_EDGE",EDGE,{"disambiguationData":[OSD([sQuery(id+"F0.wireOp",EDGE,"E6.37.0"),subQ1,subQ0])]}),makeQuery(id+"F1.opExtrude","CAP_FACE",FACE,{"disambiguationData":[OSD([sQuery(id+"F0.wireOp",EDGE,"E0"),sQuery(id+"F0.wireOp",EDGE,"E1"),sQuery(id+"F0.wireOp",EDGE,"E2"),sQuery(id+"F0.wireOp",EDGE,"E4"),sQuery(id+"F0.wireOp",EDGE,"E5"),sQuery(id+"F0.wireOp",EDGE,"E6.1.1"),sQuery(id+"F0.wireOp",EDGE,"E6.1.2"),sQuery(id+"F0.wireOp",EDGE,"E6.1.3"),sQuery(id+"F0.wireOp",EDGE,"E6.1.4"),sQuery(id+"F0.wireOp",EDGE,"E6.2.1"),sQuery(id+"F0.wireOp",EDGE,"E6.2.2"),sQuery(id+"F0.wireOp",EDGE,"E6.2.3"),sQuery(id+"F0.wireOp",EDGE,"E6.2.4"),sQuery(id+"F0.wireOp",EDGE,"E6.3.1"),sQuery(id+"F0.wireOp",EDGE,"E6.3.2"),sQuery(id+"F0.wireOp",EDGE,"E6.3.3"),sQuery(id+"F0.wireOp",EDGE,"E6.3.4"),sQuery(id+"F0.wireOp",EDGE,"E6.4.1"),sQuery(id+"F0.wireOp",EDGE,"E6.4.2"),sQuery(id+"F0.wireOp",EDGE,"E6.4.3"),sQuery(id+"F0.wireOp",EDGE,"E6.4.4"),sQuery(id+"F0.wireOp",EDGE,"E6.5.1"),sQuery(id+"F0.wireOp",EDGE,"E6.5.2"),sQuery(id+"F0.wireOp",EDGE,"E6.5.3"),sQuery(id+"F0.wireOp",EDGE,"E6.5.4"),sQuery(id+"F0.wireOp",EDGE,"E6.6.1"),sQuery(id+"F0.wireOp",EDGE,"E6.6.2"),sQuery(id+"F0.wireOp",EDGE,"E6.6.3"),sQuery(id+"F0.wireOp",EDGE,"E6.6.4"),sQuery(id+"F0.wireOp",EDGE,"E6.7.1"),sQuery(id+"F0.wireOp",EDGE,"E6.7.2"),sQuery(id+"F0.wireOp",EDGE,"E6.7.3"),sQuery(id+"F0.wireOp",EDGE,"E6.7.4"),sQuery(id+"F0.wireOp",EDGE,"E6.8.1"),sQuery(id+"F0.wireOp",EDGE,"E6.8.2"),sQuery(id+"F0.wireOp",EDGE,"E6.8.3"),sQuery(id+"F0.wireOp",EDGE,"E6.8.4"),sQuery(id+"F0.wireOp",EDGE,"E6.9.1"),sQuery(id+"F0.wireOp",EDGE,"E6.9.2"),sQuery(id+"F0.wireOp",EDGE,"E6.9.3"),sQuery(id+"F0.wireOp",EDGE,"E6.9.4"),sQuery(id+"F0.wireOp",EDGE,"E6.10.1"),sQuery(id+"F0.wireOp",EDGE,"E6.10.2"),sQuery(id+"F0.wireOp",EDGE,"E6.10.3"),sQuery(id+"F0.wireOp",EDGE,"E6.10.4"),sQuery(id+"F0.wireOp",EDGE,"E6.11.1"),sQuery(id+"F0.wireOp",EDGE,"E6.11.2"),sQuery(id+"F0.wireOp",EDGE,"E6.11.3"),sQuery(id+"F0.wireOp",EDGE,"E6.11.4"),sQuery(id+"F0.wireOp",EDGE,"E6.12.1"),sQuery(id+"F0.wireOp",EDGE,"E6.12.2"),sQuery(id+"F0.wireOp",EDGE,"E6.12.3"),sQuery(id+"F0.wireOp",EDGE,"E6.12.4"),sQuery(id+"F0.wireOp",EDGE,"E6.13.1"),sQuery(id+"F0.wireOp",EDGE,"E6.13.2"),sQuery(id+"F0.wireOp",EDGE,"E6.13.3"),sQuery(id+"F0.wireOp",EDGE,"E6.13.4"),sQuery(id+"F0.wireOp",EDGE,"E6.14.1"),sQuery(id+"F0.wireOp",EDGE,"E6.14.2"),sQuery(id+"F0.wireOp",EDGE,"E6.14.3"),sQuery(id+"F0.wireOp",EDGE,"E6.14.4"),sQuery(id+"F0.wireOp",EDGE,"E6.15.1"),sQuery(id+"F0.wireOp",EDGE,"E6.15.2"),sQuery(id+"F0.wireOp",EDGE,"E6.15.3"),sQuery(id+"F0.wireOp",EDGE,"E6.15.4"),sQuery(id+"F0.wireOp",EDGE,"E6.16.1"),sQuery(id+"F0.wireOp",EDGE,"E6.16.2"),sQuery(id+"F0.wireOp",EDGE,"E6.16.3"),sQuery(id+"F0.wireOp",EDGE,"E6.16.4"),sQuery(id+"F0.wireOp",EDGE,"E6.17.1"),sQuery(id+"F0.wireOp",EDGE,"E6.17.2"),sQuery(id+"F0.wireOp",EDGE,"E6.17.3"),sQuery(id+"F0.wireOp",EDGE,"E6.17.4"),sQuery(id+"F0.wireOp",EDGE,"E6.18.1"),sQuery(id+"F0.wireOp",EDGE,"E6.18.2"),sQuery(id+"F0.wireOp",EDGE,"E6.18.3"),sQuery(id+"F0.wireOp",EDGE,"E6.18.4"),sQuery(id+"F0.wireOp",EDGE,"E6.19.1"),sQuery(id+"F0.wireOp",EDGE,"E6.19.2"),sQuery(id+"F0.wireOp",EDGE,"E6.19.3"),sQuery(id+"F0.wireOp",EDGE,"E6.19.4"),sQuery(id+"F0.wireOp",EDGE,"E6.20.1"),sQuery(id+"F0.wireOp",EDGE,"E6.20.2"),sQuery(id+"F0.wireOp",EDGE,"E6.20.3"),sQuery(id+"F0.wireOp",EDGE,"E6.20.4"),sQuery(id+"F0.wireOp",EDGE,"E6.21.1"),sQuery(id+"F0.wireOp",EDGE,"E6.21.2"),sQuery(id+"F0.wireOp",EDGE,"E6.21.3"),sQuery(id+"F0.wireOp",EDGE,"E6.21.4"),sQuery(id+"F0.wireOp",EDGE,"E6.22.1"),sQuery(id+"F0.wireOp",EDGE,"E6.22.2"),sQuery(id+"F0.wireOp",EDGE,"E6.22.3"),sQuery(id+"F0.wireOp",EDGE,"E6.22.4"),sQuery(id+"F0.wireOp",EDGE,"E6.23.1"),sQuery(id+"F0.wireOp",EDGE,"E6.23.2"),sQuery(id+"F0.wireOp",EDGE,"E6.23.3"),sQuery(id+"F0.wireOp",EDGE,"E6.23.4"),sQuery(id+"F0.wireOp",EDGE,"E6.24.1"),sQuery(id+"F0.wireOp",EDGE,"E6.24.2"),sQuery(id+"F0.wireOp",EDGE,"E6.24.3"),sQuery(id+"F0.wireOp",EDGE,"E6.24.4"),sQuery(id+"F0.wireOp",EDGE,"E6.25.1"),sQuery(id+"F0.wireOp",EDGE,"E6.25.2"),sQuery(id+"F0.wireOp",EDGE,"E6.25.3"),sQuery(id+"F0.wireOp",EDGE,"E6.25.4"),sQuery(id+"F0.wireOp",EDGE,"E6.26.1"),sQuery(id+"F0.wireOp",EDGE,"E6.26.2"),sQuery(id+"F0.wireOp",EDGE,"E6.26.3"),sQuery(id+"F0.wireOp",EDGE,"E6.26.4"),sQuery(id+"F0.wireOp",EDGE,"E6.27.1"),sQuery(id+"F0.wireOp",EDGE,"E6.27.2"),sQuery(id+"F0.wireOp",EDGE,"E6.27.3"),sQuery(id+"F0.wireOp",EDGE,"E6.27.4"),sQuery(id+"F0.wireOp",EDGE,"E6.28.1"),sQuery(id+"F0.wireOp",EDGE,"E6.28.2"),sQuery(id+"F0.wireOp",EDGE,"E6.28.3"),sQuery(id+"F0.wireOp",EDGE,"E6.28.4"),sQuery(id+"F0.wireOp",EDGE,"E6.29.1"),sQuery(id+"F0.wireOp",EDGE,"E6.29.2"),sQuery(id+"F0.wireOp",EDGE,"E6.29.3"),sQuery(id+"F0.wireOp",EDGE,"E6.29.4"),sQuery(id+"F0.wireOp",EDGE,"E6.30.1"),sQuery(id+"F0.wireOp",EDGE,"E6.30.2"),sQuery(id+"F0.wireOp",EDGE,"E6.30.3"),sQuery(id+"F0.wireOp",EDGE,"E6.30.4"),sQuery(id+"F0.wireOp",EDGE,"E6.31.1"),sQuery(id+"F0.wireOp",EDGE,"E6.31.2"),sQuery(id+"F0.wireOp",EDGE,"E6.31.3"),sQuery(id+"F0.wireOp",EDGE,"E6.31.4"),sQuery(id+"F0.wireOp",EDGE,"E6.32.1"),sQuery(id+"F0.wireOp",EDGE,"E6.32.2"),sQuery(id+"F0.wireOp",EDGE,"E6.32.3"),sQuery(id+"F0.wireOp",EDGE,"E6.32.4"),sQuery(id+"F0.wireOp",EDGE,"E6.33.1"),sQuery(id+"F0.wireOp",EDGE,"E6.33.2"),sQuery(id+"F0.wireOp",EDGE,"E6.33.3"),sQuery(id+"F0.wireOp",EDGE,"E6.33.4"),sQuery(id+"F0.wireOp",EDGE,"E6.34.1"),sQuery(id+"F0.wireOp",EDGE,"E6.34.2"),sQuery(id+"F0.wireOp",EDGE,"E6.34.3"),sQuery(id+"F0.wireOp",EDGE,"E6.34.4"),sQuery(id+"F0.wireOp",EDGE,"E6.35.1"),sQuery(id+"F0.wireOp",EDGE,"E6.35.2"),sQuery(id+"F0.wireOp",EDGE,"E6.35.3"),sQuery(id+"F0.wireOp",EDGE,"E6.35.4"),sQuery(id+"F0.wireOp",EDGE,"E6.36.1"),sQuery(id+"F0.wireOp",EDGE,"E6.36.2"),sQuery(id+"F0.wireOp",EDGE,"E6.36.3"),sQuery(id+"F0.wireOp",EDGE,"E6.36.4"),subQ1,sQuery(id+"F0.wireOp",EDGE,"E6.37.2"),subQ0,sQuery(id+"F0.wireOp",EDGE,"E6.37.4"),sQuery(id+"F0.wireOp",EDGE,"E6.38.1"),sQuery(id+"F0.wireOp",EDGE,"E6.38.2"),sQuery(id+"F0.wireOp",EDGE,"E6.38.3"),sQuery(id+"F0.wireOp",EDGE,"E6.38.4"),sQuery(id+"F0.wireOp",EDGE,"E6.39.1"),sQuery(id+"F0.wireOp",EDGE,"E6.39.2"),sQuery(id+"F0.wireOp",EDGE,"E6.39.3"),sQuery(id+"F0.wireOp",EDGE,"E6.39.4"),sQuery(id+"F0.wireOp",EDGE,"E6.40.1"),sQuery(id+"F0.wireOp",EDGE,"E6.40.2"),sQuery(id+"F0.wireOp",EDGE,"E6.40.3"),sQuery(id+"F0.wireOp",EDGE,"E6.40.4"),sQuery(id+"F0.wireOp",EDGE,"E6.41.1"),sQuery(id+"F0.wireOp",EDGE,"E6.41.2"),sQuery(id+"F0.wireOp",EDGE,"E6.41.3"),sQuery(id+"F0.wireOp",EDGE,"E6.41.4"),sQuery(id+"F0.wireOp",EDGE,"E6.42.1"),sQuery(id+"F0.wireOp",EDGE,"E6.42.2"),sQuery(id+"F0.wireOp",EDGE,"E6.42.3"),sQuery(id+"F0.wireOp",EDGE,"E6.42.4"),sQuery(id+"F0.wireOp",EDGE,"E6.43.1"),sQuery(id+"F0.wireOp",EDGE,"E6.43.2"),sQuery(id+"F0.wireOp",EDGE,"E6.43.3"),sQuery(id+"F0.wireOp",EDGE,"E6.43.4"),sQuery(id+"F0.wireOp",EDGE,"E7"),sQuery(id+"F0.wireOp",EDGE,"E8.1.0"),sQuery(id+"F0.wireOp",EDGE,"E8.2.0"),sQuery(id+"F0.wireOp",EDGE,"E8.3.0"),sQuery(id+"F0.wireOp",EDGE,"E8.4.0"),sQuery(id+"F0.wireOp",EDGE,"E8.5.0"),sQuery(id+"F0.wireOp",EDGE,"E8.6.0"),sQuery(id+"F0.wireOp",EDGE,"E8.7.0"),sQuery(id+"F0.wireOp",EDGE,"E8.8.0"),sQuery(id+"F0.wireOp",EDGE,"E8.9.0"),sQuery(id+"F0.wireOp",EDGE,"E8.10.0"),sQuery(id+"F0.wireOp",EDGE,"E8.11.0"),sQuery(id+"F0.wireOp",EDGE,"E8.12.0"),sQuery(id+"F0.wireOp",EDGE,"E8.13.0"),sQuery(id+"F0.wireOp",EDGE,"E8.14.0"),sQuery(id+"F0.wireOp",EDGE,"E8.15.0"),sQuery(id+"F0.wireOp",EDGE,"E8.16.0"),sQuery(id+"F0.wireOp",EDGE,"E8.17.0"),sQuery(id+"F0.wireOp",EDGE,"E8.18.0"),sQuery(id+"F0.wireOp",EDGE,"E8.19.0"),sQuery(id+"F0.wireOp",EDGE,"E8.20.0"),sQuery(id+"F0.wireOp",EDGE,"E8.21.0"),sQuery(id+"F0.wireOp",EDGE,"E8.22.0"),sQuery(id+"F0.wireOp",EDGE,"E8.23.0"),sQuery(id+"F0.wireOp",EDGE,"E8.24.0"),sQuery(id+"F0.wireOp",EDGE,"E8.25.0"),sQuery(id+"F0.wireOp",EDGE,"E8.26.0"),sQuery(id+"F0.wireOp",EDGE,"E8.27.0"),sQuery(id+"F0.wireOp",EDGE,"E8.28.0"),sQuery(id+"F0.wireOp",EDGE,"E8.29.0"),sQuery(id+"F0.wireOp",EDGE,"E8.30.0"),sQuery(id+"F0.wireOp",EDGE,"E8.31.0"),sQuery(id+"F0.wireOp",EDGE,"E8.32.0"),sQuery(id+"F0.wireOp",EDGE,"E8.33.0"),sQuery(id+"F0.wireOp",EDGE,"E8.34.0"),sQuery(id+"F0.wireOp",EDGE,"E8.35.0"),sQuery(id+"F0.wireOp",EDGE,"E8.36.0"),sQuery(id+"F0.wireOp",EDGE,"E8.37.0"),sQuery(id+"F0.wireOp",EDGE,"E8.38.0"),sQuery(id+"F0.wireOp",EDGE,"E8.39.0"),sQuery(id+"F0.wireOp",EDGE,"E8.40.0"),sQuery(id+"F0.wireOp",EDGE,"E8.41.0"),sQuery(id+"F0.wireOp",EDGE,"E8.42.0"),sQuery(id+"F0.wireOp",EDGE,"E8.43.0")])],"isStart":false})],"blendedInto":[makeQuery(id+"F1.opExtrude","CAP_FACE",FACE,{"disambiguationData":[OSD([sQuery(id+"F0.wireOp",EDGE,"E0"),sQuery(id+"F0.wireOp",EDGE,"E1"),sQuery(id+"F0.wireOp",EDGE,"E2"),sQuery(id+"F0.wireOp",EDGE,"E4"),sQuery(id+"F0.wireOp",EDGE,"E5"),sQuery(id+"F0.wireOp",EDGE,"E6.1.1"),sQuery(id+"F0.wireOp",EDGE,"E6.1.2"),sQuery(id+"F0.wireOp",EDGE,"E6.1.3"),sQuery(id+"F0.wireOp",EDGE,"E6.1.4"),sQuery(id+"F0.wireOp",EDGE,"E6.2.1"),sQuery(id+"F0.wireOp",EDGE,"E6.2.2"),sQuery(id+"F0.wireOp",EDGE,"E6.2.3"),sQuery(id+"F0.wireOp",EDGE,"E6.2.4"),sQuery(id+"F0.wireOp",EDGE,"E6.3.1"),sQuery(id+"F0.wireOp",EDGE,"E6.3.2"),sQuery(id+"F0.wireOp",EDGE,"E6.3.3"),sQuery(id+"F0.wireOp",EDGE,"E6.3.4"),sQuery(id+"F0.wireOp",EDGE,"E6.4.1"),sQuery(id+"F0.wireOp",EDGE,"E6.4.2"),sQuery(id+"F0.wireOp",EDGE,"E6.4.3"),sQuery(id+"F0.wireOp",EDGE,"E6.4.4"),sQuery(id+"F0.wireOp",EDGE,"E6.5.1"),sQuery(id+"F0.wireOp",EDGE,"E6.5.2"),sQuery(id+"F0.wireOp",EDGE,"E6.5.3"),sQuery(id+"F0.wireOp",EDGE,"E6.5.4"),sQuery(id+"F0.wireOp",EDGE,"E6.6.1"),sQuery(id+"F0.wireOp",EDGE,"E6.6.2"),sQuery(id+"F0.wireOp",EDGE,"E6.6.3"),sQuery(id+"F0.wireOp",EDGE,"E6.6.4"),sQuery(id+"F0.wireOp",EDGE,"E6.7.1"),sQuery(id+"F0.wireOp",EDGE,"E6.7.2"),sQuery(id+"F0.wireOp",EDGE,"E6.7.3"),sQuery(id+"F0.wireOp",EDGE,"E6.7.4"),sQuery(id+"F0.wireOp",EDGE,"E6.8.1"),sQuery(id+"F0.wireOp",EDGE,"E6.8.2"),sQuery(id+"F0.wireOp",EDGE,"E6.8.3"),sQuery(id+"F0.wireOp",EDGE,"E6.8.4"),sQuery(id+"F0.wireOp",EDGE,"E6.9.1"),sQuery(id+"F0.wireOp",EDGE,"E6.9.2"),sQuery(id+"F0.wireOp",EDGE,"E6.9.3"),sQuery(id+"F0.wireOp",EDGE,"E6.9.4"),sQuery(id+"F0.wireOp",EDGE,"E6.10.1"),sQuery(id+"F0.wireOp",EDGE,"E6.10.2"),sQuery(id+"F0.wireOp",EDGE,"E6.10.3"),sQuery(id+"F0.wireOp",EDGE,"E6.10.4"),sQuery(id+"F0.wireOp",EDGE,"E6.11.1"),sQuery(id+"F0.wireOp",EDGE,"E6.11.2"),sQuery(id+"F0.wireOp",EDGE,"E6.11.3"),sQuery(id+"F0.wireOp",EDGE,"E6.11.4"),sQuery(id+"F0.wireOp",EDGE,"E6.12.1"),sQuery(id+"F0.wireOp",EDGE,"E6.12.2"),sQuery(id+"F0.wireOp",EDGE,"E6.12.3"),sQuery(id+"F0.wireOp",EDGE,"E6.12.4"),sQuery(id+"F0.wireOp",EDGE,"E6.13.1"),sQuery(id+"F0.wireOp",EDGE,"E6.13.2"),sQuery(id+"F0.wireOp",EDGE,"E6.13.3"),sQuery(id+"F0.wireOp",EDGE,"E6.13.4"),sQuery(id+"F0.wireOp",EDGE,"E6.14.1"),sQuery(id+"F0.wireOp",EDGE,"E6.14.2"),sQuery(id+"F0.wireOp",EDGE,"E6.14.3"),sQuery(id+"F0.wireOp",EDGE,"E6.14.4"),sQuery(id+"F0.wireOp",EDGE,"E6.15.1"),sQuery(id+"F0.wireOp",EDGE,"E6.15.2"),sQuery(id+"F0.wireOp",EDGE,"E6.15.3"),sQuery(id+"F0.wireOp",EDGE,"E6.15.4"),sQuery(id+"F0.wireOp",EDGE,"E6.16.1"),sQuery(id+"F0.wireOp",EDGE,"E6.16.2"),sQuery(id+"F0.wireOp",EDGE,"E6.16.3"),sQuery(id+"F0.wireOp",EDGE,"E6.16.4"),sQuery(id+"F0.wireOp",EDGE,"E6.17.1"),sQuery(id+"F0.wireOp",EDGE,"E6.17.2"),sQuery(id+"F0.wireOp",EDGE,"E6.17.3"),sQuery(id+"F0.wireOp",EDGE,"E6.17.4"),sQuery(id+"F0.wireOp",EDGE,"E6.18.1"),sQuery(id+"F0.wireOp",EDGE,"E6.18.2"),sQuery(id+"F0.wireOp",EDGE,"E6.18.3"),sQuery(id+"F0.wireOp",EDGE,"E6.18.4"),sQuery(id+"F0.wireOp",EDGE,"E6.19.1"),sQuery(id+"F0.wireOp",EDGE,"E6.19.2"),sQuery(id+"F0.wireOp",EDGE,"E6.19.3"),sQuery(id+"F0.wireOp",EDGE,"E6.19.4"),sQuery(id+"F0.wireOp",EDGE,"E6.20.1"),sQuery(id+"F0.wireOp",EDGE,"E6.20.2"),sQuery(id+"F0.wireOp",EDGE,"E6.20.3"),sQuery(id+"F0.wireOp",EDGE,"E6.20.4"),sQuery(id+"F0.wireOp",EDGE,"E6.21.1"),sQuery(id+"F0.wireOp",EDGE,"E6.21.2"),sQuery(id+"F0.wireOp",EDGE,"E6.21.3"),sQuery(id+"F0.wireOp",EDGE,"E6.21.4"),sQuery(id+"F0.wireOp",EDGE,"E6.22.1"),sQuery(id+"F0.wireOp",EDGE,"E6.22.2"),sQuery(id+"F0.wireOp",EDGE,"E6.22.3"),sQuery(id+"F0.wireOp",EDGE,"E6.22.4"),sQuery(id+"F0.wireOp",EDGE,"E6.23.1"),sQuery(id+"F0.wireOp",EDGE,"E6.23.2"),sQuery(id+"F0.wireOp",EDGE,"E6.23.3"),sQuery(id+"F0.wireOp",EDGE,"E6.23.4"),sQuery(id+"F0.wireOp",EDGE,"E6.24.1"),sQuery(id+"F0.wireOp",EDGE,"E6.24.2"),sQuery(id+"F0.wireOp",EDGE,"E6.24.3"),sQuery(id+"F0.wireOp",EDGE,"E6.24.4"),sQuery(id+"F0.wireOp",EDGE,"E6.25.1"),sQuery(id+"F0.wireOp",EDGE,"E6.25.2"),sQuery(id+"F0.wireOp",EDGE,"E6.25.3"),sQuery(id+"F0.wireOp",EDGE,"E6.25.4"),sQuery(id+"F0.wireOp",EDGE,"E6.26.1"),sQuery(id+"F0.wireOp",EDGE,"E6.26.2"),sQuery(id+"F0.wireOp",EDGE,"E6.26.3"),sQuery(id+"F0.wireOp",EDGE,"E6.26.4"),sQuery(id+"F0.wireOp",EDGE,"E6.27.1"),sQuery(id+"F0.wireOp",EDGE,"E6.27.2"),sQuery(id+"F0.wireOp",EDGE,"E6.27.3"),sQuery(id+"F0.wireOp",EDGE,"E6.27.4"),sQuery(id+"F0.wireOp",EDGE,"E6.28.1"),sQuery(id+"F0.wireOp",EDGE,"E6.28.2"),sQuery(id+"F0.wireOp",EDGE,"E6.28.3"),sQuery(id+"F0.wireOp",EDGE,"E6.28.4"),sQuery(id+"F0.wireOp",EDGE,"E6.29.1"),sQuery(id+"F0.wireOp",EDGE,"E6.29.2"),sQuery(id+"F0.wireOp",EDGE,"E6.29.3"),sQuery(id+"F0.wireOp",EDGE,"E6.29.4"),sQuery(id+"F0.wireOp",EDGE,"E6.30.1"),sQuery(id+"F0.wireOp",EDGE,"E6.30.2"),sQuery(id+"F0.wireOp",EDGE,"E6.30.3"),sQuery(id+"F0.wireOp",EDGE,"E6.30.4"),sQuery(id+"F0.wireOp",EDGE,"E6.31.1"),sQuery(id+"F0.wireOp",EDGE,"E6.31.2"),sQuery(id+"F0.wireOp",EDGE,"E6.31.3"),sQuery(id+"F0.wireOp",EDGE,"E6.31.4"),sQuery(id+"F0.wireOp",EDGE,"E6.32.1"),sQuery(id+"F0.wireOp",EDGE,"E6.32.2"),sQuery(id+"F0.wireOp",EDGE,"E6.32.3"),sQuery(id+"F0.wireOp",EDGE,"E6.32.4"),sQuery(id+"F0.wireOp",EDGE,"E6.33.1"),sQuery(id+"F0.wireOp",EDGE,"E6.33.2"),sQuery(id+"F0.wireOp",EDGE,"E6.33.3"),sQuery(id+"F0.wireOp",EDGE,"E6.33.4"),sQuery(id+"F0.wireOp",EDGE,"E6.34.1"),sQuery(id+"F0.wireOp",EDGE,"E6.34.2"),sQuery(id+"F0.wireOp",EDGE,"E6.34.3"),sQuery(id+"F0.wireOp",EDGE,"E6.34.4"),sQuery(id+"F0.wireOp",EDGE,"E6.35.1"),sQuery(id+"F0.wireOp",EDGE,"E6.35.2"),sQuery(id+"F0.wireOp",EDGE,"E6.35.3"),sQuery(id+"F0.wireOp",EDGE,"E6.35.4"),sQuery(id+"F0.wireOp",EDGE,"E6.36.1"),sQuery(id+"F0.wireOp",EDGE,"E6.36.2"),sQuery(id+"F0.wireOp",EDGE,"E6.36.3"),sQuery(id+"F0.wireOp",EDGE,"E6.36.4"),subQ1,sQuery(id+"F0.wireOp",EDGE,"E6.37.2"),subQ0,sQuery(id+"F0.wireOp",EDGE,"E6.37.4"),sQuery(id+"F0.wireOp",EDGE,"E6.38.1"),sQuery(id+"F0.wireOp",EDGE,"E6.38.2"),sQuery(id+"F0.wireOp",EDGE,"E6.38.3"),sQuery(id+"F0.wireOp",EDGE,"E6.38.4"),sQuery(id+"F0.wireOp",EDGE,"E6.39.1"),sQuery(id+"F0.wireOp",EDGE,"E6.39.2"),sQuery(id+"F0.wireOp",EDGE,"E6.39.3"),sQuery(id+"F0.wireOp",EDGE,"E6.39.4"),sQuery(id+"F0.wireOp",EDGE,"E6.40.1"),sQuery(id+"F0.wireOp",EDGE,"E6.40.2"),sQuery(id+"F0.wireOp",EDGE,"E6.40.3"),sQuery(id+"F0.wireOp",EDGE,"E6.40.4"),sQuery(id+"F0.wireOp",EDGE,"E6.41.1"),sQuery(id+"F0.wireOp",EDGE,"E6.41.2"),sQuery(id+"F0.wireOp",EDGE,"E6.41.3"),sQuery(id+"F0.wireOp",EDGE,"E6.41.4"),sQuery(id+"F0.wireOp",EDGE,"E6.42.1"),sQuery(id+"F0.wireOp",EDGE,"E6.42.2"),sQuery(id+"F0.wireOp",EDGE,"E6.42.3"),sQuery(id+"F0.wireOp",EDGE,"E6.42.4"),sQuery(id+"F0.wireOp",EDGE,"E6.43.1"),sQuery(id+"F0.wireOp",EDGE,"E6.43.2"),sQuery(id+"F0.wireOp",EDGE,"E6.43.3"),sQuery(id+"F0.wireOp",EDGE,"E6.43.4"),sQuery(id+"F0.wireOp",EDGE,"E7"),sQuery(id+"F0.wireOp",EDGE,"E8.1.0"),sQuery(id+"F0.wireOp",EDGE,"E8.2.0"),sQuery(id+"F0.wireOp",EDGE,"E8.3.0"),sQuery(id+"F0.wireOp",EDGE,"E8.4.0"),sQuery(id+"F0.wireOp",EDGE,"E8.5.0"),sQuery(id+"F0.wireOp",EDGE,"E8.6.0"),sQuery(id+"F0.wireOp",EDGE,"E8.7.0"),sQuery(id+"F0.wireOp",EDGE,"E8.8.0"),sQuery(id+"F0.wireOp",EDGE,"E8.9.0"),sQuery(id+"F0.wireOp",EDGE,"E8.10.0"),sQuery(id+"F0.wireOp",EDGE,"E8.11.0"),sQuery(id+"F0.wireOp",EDGE,"E8.12.0"),sQuery(id+"F0.wireOp",EDGE,"E8.13.0"),sQuery(id+"F0.wireOp",EDGE,"E8.14.0"),sQuery(id+"F0.wireOp",EDGE,"E8.15.0"),sQuery(id+"F0.wireOp",EDGE,"E8.16.0"),sQuery(id+"F0.wireOp",EDGE,"E8.17.0"),sQuery(id+"F0.wireOp",EDGE,"E8.18.0"),sQuery(id+"F0.wireOp",EDGE,"E8.19.0"),sQuery(id+"F0.wireOp",EDGE,"E8.20.0"),sQuery(id+"F0.wireOp",EDGE,"E8.21.0"),sQuery(id+"F0.wireOp",EDGE,"E8.22.0"),sQuery(id+"F0.wireOp",EDGE,"E8.23.0"),sQuery(id+"F0.wireOp",EDGE,"E8.24.0"),sQuery(id+"F0.wireOp",EDGE,"E8.25.0"),sQuery(id+"F0.wireOp",EDGE,"E8.26.0"),sQuery(id+"F0.wireOp",EDGE,"E8.27.0"),sQuery(id+"F0.wireOp",EDGE,"E8.28.0"),sQuery(id+"F0.wireOp",EDGE,"E8.29.0"),sQuery(id+"F0.wireOp",EDGE,"E8.30.0"),sQuery(id+"F0.wireOp",EDGE,"E8.31.0"),sQuery(id+"F0.wireOp",EDGE,"E8.32.0"),sQuery(id+"F0.wireOp",EDGE,"E8.33.0"),sQuery(id+"F0.wireOp",EDGE,"E8.34.0"),sQuery(id+"F0.wireOp",EDGE,"E8.35.0"),sQuery(id+"F0.wireOp",EDGE,"E8.36.0"),sQuery(id+"F0.wireOp",EDGE,"E8.37.0"),sQuery(id+"F0.wireOp",EDGE,"E8.38.0"),sQuery(id+"F0.wireOp",EDGE,"E8.39.0"),sQuery(id+"F0.wireOp",EDGE,"E8.40.0"),sQuery(id+"F0.wireOp",EDGE,"E8.41.0"),sQuery(id+"F0.wireOp",EDGE,"E8.42.0"),sQuery(id+"F0.wireOp",EDGE,"E8.43.0")])],"isStart":false})]});}
            var Q8;
            {var subQ0=sQuery(id+"F0.wireOp",EDGE,"E6.39.3");var subQ1=sQuery(id+"F0.wireOp",EDGE,"E6.39.1");Q8=makeQuery(id+"F2.opFillet","BLEND_EDGE",EDGE,{"blendedFrom":[makeQuery(id+"F1.opExtrude","SWEPT_EDGE",EDGE,{"disambiguationData":[OSD([sQuery(id+"F0.wireOp",EDGE,"E6.39.0"),subQ1,subQ0])]}),makeQuery(id+"F1.opExtrude","CAP_FACE",FACE,{"disambiguationData":[OSD([sQuery(id+"F0.wireOp",EDGE,"E0"),sQuery(id+"F0.wireOp",EDGE,"E1"),sQuery(id+"F0.wireOp",EDGE,"E2"),sQuery(id+"F0.wireOp",EDGE,"E4"),sQuery(id+"F0.wireOp",EDGE,"E5"),sQuery(id+"F0.wireOp",EDGE,"E6.1.1"),sQuery(id+"F0.wireOp",EDGE,"E6.1.2"),sQuery(id+"F0.wireOp",EDGE,"E6.1.3"),sQuery(id+"F0.wireOp",EDGE,"E6.1.4"),sQuery(id+"F0.wireOp",EDGE,"E6.2.1"),sQuery(id+"F0.wireOp",EDGE,"E6.2.2"),sQuery(id+"F0.wireOp",EDGE,"E6.2.3"),sQuery(id+"F0.wireOp",EDGE,"E6.2.4"),sQuery(id+"F0.wireOp",EDGE,"E6.3.1"),sQuery(id+"F0.wireOp",EDGE,"E6.3.2"),sQuery(id+"F0.wireOp",EDGE,"E6.3.3"),sQuery(id+"F0.wireOp",EDGE,"E6.3.4"),sQuery(id+"F0.wireOp",EDGE,"E6.4.1"),sQuery(id+"F0.wireOp",EDGE,"E6.4.2"),sQuery(id+"F0.wireOp",EDGE,"E6.4.3"),sQuery(id+"F0.wireOp",EDGE,"E6.4.4"),sQuery(id+"F0.wireOp",EDGE,"E6.5.1"),sQuery(id+"F0.wireOp",EDGE,"E6.5.2"),sQuery(id+"F0.wireOp",EDGE,"E6.5.3"),sQuery(id+"F0.wireOp",EDGE,"E6.5.4"),sQuery(id+"F0.wireOp",EDGE,"E6.6.1"),sQuery(id+"F0.wireOp",EDGE,"E6.6.2"),sQuery(id+"F0.wireOp",EDGE,"E6.6.3"),sQuery(id+"F0.wireOp",EDGE,"E6.6.4"),sQuery(id+"F0.wireOp",EDGE,"E6.7.1"),sQuery(id+"F0.wireOp",EDGE,"E6.7.2"),sQuery(id+"F0.wireOp",EDGE,"E6.7.3"),sQuery(id+"F0.wireOp",EDGE,"E6.7.4"),sQuery(id+"F0.wireOp",EDGE,"E6.8.1"),sQuery(id+"F0.wireOp",EDGE,"E6.8.2"),sQuery(id+"F0.wireOp",EDGE,"E6.8.3"),sQuery(id+"F0.wireOp",EDGE,"E6.8.4"),sQuery(id+"F0.wireOp",EDGE,"E6.9.1"),sQuery(id+"F0.wireOp",EDGE,"E6.9.2"),sQuery(id+"F0.wireOp",EDGE,"E6.9.3"),sQuery(id+"F0.wireOp",EDGE,"E6.9.4"),sQuery(id+"F0.wireOp",EDGE,"E6.10.1"),sQuery(id+"F0.wireOp",EDGE,"E6.10.2"),sQuery(id+"F0.wireOp",EDGE,"E6.10.3"),sQuery(id+"F0.wireOp",EDGE,"E6.10.4"),sQuery(id+"F0.wireOp",EDGE,"E6.11.1"),sQuery(id+"F0.wireOp",EDGE,"E6.11.2"),sQuery(id+"F0.wireOp",EDGE,"E6.11.3"),sQuery(id+"F0.wireOp",EDGE,"E6.11.4"),sQuery(id+"F0.wireOp",EDGE,"E6.12.1"),sQuery(id+"F0.wireOp",EDGE,"E6.12.2"),sQuery(id+"F0.wireOp",EDGE,"E6.12.3"),sQuery(id+"F0.wireOp",EDGE,"E6.12.4"),sQuery(id+"F0.wireOp",EDGE,"E6.13.1"),sQuery(id+"F0.wireOp",EDGE,"E6.13.2"),sQuery(id+"F0.wireOp",EDGE,"E6.13.3"),sQuery(id+"F0.wireOp",EDGE,"E6.13.4"),sQuery(id+"F0.wireOp",EDGE,"E6.14.1"),sQuery(id+"F0.wireOp",EDGE,"E6.14.2"),sQuery(id+"F0.wireOp",EDGE,"E6.14.3"),sQuery(id+"F0.wireOp",EDGE,"E6.14.4"),sQuery(id+"F0.wireOp",EDGE,"E6.15.1"),sQuery(id+"F0.wireOp",EDGE,"E6.15.2"),sQuery(id+"F0.wireOp",EDGE,"E6.15.3"),sQuery(id+"F0.wireOp",EDGE,"E6.15.4"),sQuery(id+"F0.wireOp",EDGE,"E6.16.1"),sQuery(id+"F0.wireOp",EDGE,"E6.16.2"),sQuery(id+"F0.wireOp",EDGE,"E6.16.3"),sQuery(id+"F0.wireOp",EDGE,"E6.16.4"),sQuery(id+"F0.wireOp",EDGE,"E6.17.1"),sQuery(id+"F0.wireOp",EDGE,"E6.17.2"),sQuery(id+"F0.wireOp",EDGE,"E6.17.3"),sQuery(id+"F0.wireOp",EDGE,"E6.17.4"),sQuery(id+"F0.wireOp",EDGE,"E6.18.1"),sQuery(id+"F0.wireOp",EDGE,"E6.18.2"),sQuery(id+"F0.wireOp",EDGE,"E6.18.3"),sQuery(id+"F0.wireOp",EDGE,"E6.18.4"),sQuery(id+"F0.wireOp",EDGE,"E6.19.1"),sQuery(id+"F0.wireOp",EDGE,"E6.19.2"),sQuery(id+"F0.wireOp",EDGE,"E6.19.3"),sQuery(id+"F0.wireOp",EDGE,"E6.19.4"),sQuery(id+"F0.wireOp",EDGE,"E6.20.1"),sQuery(id+"F0.wireOp",EDGE,"E6.20.2"),sQuery(id+"F0.wireOp",EDGE,"E6.20.3"),sQuery(id+"F0.wireOp",EDGE,"E6.20.4"),sQuery(id+"F0.wireOp",EDGE,"E6.21.1"),sQuery(id+"F0.wireOp",EDGE,"E6.21.2"),sQuery(id+"F0.wireOp",EDGE,"E6.21.3"),sQuery(id+"F0.wireOp",EDGE,"E6.21.4"),sQuery(id+"F0.wireOp",EDGE,"E6.22.1"),sQuery(id+"F0.wireOp",EDGE,"E6.22.2"),sQuery(id+"F0.wireOp",EDGE,"E6.22.3"),sQuery(id+"F0.wireOp",EDGE,"E6.22.4"),sQuery(id+"F0.wireOp",EDGE,"E6.23.1"),sQuery(id+"F0.wireOp",EDGE,"E6.23.2"),sQuery(id+"F0.wireOp",EDGE,"E6.23.3"),sQuery(id+"F0.wireOp",EDGE,"E6.23.4"),sQuery(id+"F0.wireOp",EDGE,"E6.24.1"),sQuery(id+"F0.wireOp",EDGE,"E6.24.2"),sQuery(id+"F0.wireOp",EDGE,"E6.24.3"),sQuery(id+"F0.wireOp",EDGE,"E6.24.4"),sQuery(id+"F0.wireOp",EDGE,"E6.25.1"),sQuery(id+"F0.wireOp",EDGE,"E6.25.2"),sQuery(id+"F0.wireOp",EDGE,"E6.25.3"),sQuery(id+"F0.wireOp",EDGE,"E6.25.4"),sQuery(id+"F0.wireOp",EDGE,"E6.26.1"),sQuery(id+"F0.wireOp",EDGE,"E6.26.2"),sQuery(id+"F0.wireOp",EDGE,"E6.26.3"),sQuery(id+"F0.wireOp",EDGE,"E6.26.4"),sQuery(id+"F0.wireOp",EDGE,"E6.27.1"),sQuery(id+"F0.wireOp",EDGE,"E6.27.2"),sQuery(id+"F0.wireOp",EDGE,"E6.27.3"),sQuery(id+"F0.wireOp",EDGE,"E6.27.4"),sQuery(id+"F0.wireOp",EDGE,"E6.28.1"),sQuery(id+"F0.wireOp",EDGE,"E6.28.2"),sQuery(id+"F0.wireOp",EDGE,"E6.28.3"),sQuery(id+"F0.wireOp",EDGE,"E6.28.4"),sQuery(id+"F0.wireOp",EDGE,"E6.29.1"),sQuery(id+"F0.wireOp",EDGE,"E6.29.2"),sQuery(id+"F0.wireOp",EDGE,"E6.29.3"),sQuery(id+"F0.wireOp",EDGE,"E6.29.4"),sQuery(id+"F0.wireOp",EDGE,"E6.30.1"),sQuery(id+"F0.wireOp",EDGE,"E6.30.2"),sQuery(id+"F0.wireOp",EDGE,"E6.30.3"),sQuery(id+"F0.wireOp",EDGE,"E6.30.4"),sQuery(id+"F0.wireOp",EDGE,"E6.31.1"),sQuery(id+"F0.wireOp",EDGE,"E6.31.2"),sQuery(id+"F0.wireOp",EDGE,"E6.31.3"),sQuery(id+"F0.wireOp",EDGE,"E6.31.4"),sQuery(id+"F0.wireOp",EDGE,"E6.32.1"),sQuery(id+"F0.wireOp",EDGE,"E6.32.2"),sQuery(id+"F0.wireOp",EDGE,"E6.32.3"),sQuery(id+"F0.wireOp",EDGE,"E6.32.4"),sQuery(id+"F0.wireOp",EDGE,"E6.33.1"),sQuery(id+"F0.wireOp",EDGE,"E6.33.2"),sQuery(id+"F0.wireOp",EDGE,"E6.33.3"),sQuery(id+"F0.wireOp",EDGE,"E6.33.4"),sQuery(id+"F0.wireOp",EDGE,"E6.34.1"),sQuery(id+"F0.wireOp",EDGE,"E6.34.2"),sQuery(id+"F0.wireOp",EDGE,"E6.34.3"),sQuery(id+"F0.wireOp",EDGE,"E6.34.4"),sQuery(id+"F0.wireOp",EDGE,"E6.35.1"),sQuery(id+"F0.wireOp",EDGE,"E6.35.2"),sQuery(id+"F0.wireOp",EDGE,"E6.35.3"),sQuery(id+"F0.wireOp",EDGE,"E6.35.4"),sQuery(id+"F0.wireOp",EDGE,"E6.36.1"),sQuery(id+"F0.wireOp",EDGE,"E6.36.2"),sQuery(id+"F0.wireOp",EDGE,"E6.36.3"),sQuery(id+"F0.wireOp",EDGE,"E6.36.4"),sQuery(id+"F0.wireOp",EDGE,"E6.37.1"),sQuery(id+"F0.wireOp",EDGE,"E6.37.2"),sQuery(id+"F0.wireOp",EDGE,"E6.37.3"),sQuery(id+"F0.wireOp",EDGE,"E6.37.4"),sQuery(id+"F0.wireOp",EDGE,"E6.38.1"),sQuery(id+"F0.wireOp",EDGE,"E6.38.2"),sQuery(id+"F0.wireOp",EDGE,"E6.38.3"),sQuery(id+"F0.wireOp",EDGE,"E6.38.4"),subQ1,sQuery(id+"F0.wireOp",EDGE,"E6.39.2"),subQ0,sQuery(id+"F0.wireOp",EDGE,"E6.39.4"),sQuery(id+"F0.wireOp",EDGE,"E6.40.1"),sQuery(id+"F0.wireOp",EDGE,"E6.40.2"),sQuery(id+"F0.wireOp",EDGE,"E6.40.3"),sQuery(id+"F0.wireOp",EDGE,"E6.40.4"),sQuery(id+"F0.wireOp",EDGE,"E6.41.1"),sQuery(id+"F0.wireOp",EDGE,"E6.41.2"),sQuery(id+"F0.wireOp",EDGE,"E6.41.3"),sQuery(id+"F0.wireOp",EDGE,"E6.41.4"),sQuery(id+"F0.wireOp",EDGE,"E6.42.1"),sQuery(id+"F0.wireOp",EDGE,"E6.42.2"),sQuery(id+"F0.wireOp",EDGE,"E6.42.3"),sQuery(id+"F0.wireOp",EDGE,"E6.42.4"),sQuery(id+"F0.wireOp",EDGE,"E6.43.1"),sQuery(id+"F0.wireOp",EDGE,"E6.43.2"),sQuery(id+"F0.wireOp",EDGE,"E6.43.3"),sQuery(id+"F0.wireOp",EDGE,"E6.43.4"),sQuery(id+"F0.wireOp",EDGE,"E7"),sQuery(id+"F0.wireOp",EDGE,"E8.1.0"),sQuery(id+"F0.wireOp",EDGE,"E8.2.0"),sQuery(id+"F0.wireOp",EDGE,"E8.3.0"),sQuery(id+"F0.wireOp",EDGE,"E8.4.0"),sQuery(id+"F0.wireOp",EDGE,"E8.5.0"),sQuery(id+"F0.wireOp",EDGE,"E8.6.0"),sQuery(id+"F0.wireOp",EDGE,"E8.7.0"),sQuery(id+"F0.wireOp",EDGE,"E8.8.0"),sQuery(id+"F0.wireOp",EDGE,"E8.9.0"),sQuery(id+"F0.wireOp",EDGE,"E8.10.0"),sQuery(id+"F0.wireOp",EDGE,"E8.11.0"),sQuery(id+"F0.wireOp",EDGE,"E8.12.0"),sQuery(id+"F0.wireOp",EDGE,"E8.13.0"),sQuery(id+"F0.wireOp",EDGE,"E8.14.0"),sQuery(id+"F0.wireOp",EDGE,"E8.15.0"),sQuery(id+"F0.wireOp",EDGE,"E8.16.0"),sQuery(id+"F0.wireOp",EDGE,"E8.17.0"),sQuery(id+"F0.wireOp",EDGE,"E8.18.0"),sQuery(id+"F0.wireOp",EDGE,"E8.19.0"),sQuery(id+"F0.wireOp",EDGE,"E8.20.0"),sQuery(id+"F0.wireOp",EDGE,"E8.21.0"),sQuery(id+"F0.wireOp",EDGE,"E8.22.0"),sQuery(id+"F0.wireOp",EDGE,"E8.23.0"),sQuery(id+"F0.wireOp",EDGE,"E8.24.0"),sQuery(id+"F0.wireOp",EDGE,"E8.25.0"),sQuery(id+"F0.wireOp",EDGE,"E8.26.0"),sQuery(id+"F0.wireOp",EDGE,"E8.27.0"),sQuery(id+"F0.wireOp",EDGE,"E8.28.0"),sQuery(id+"F0.wireOp",EDGE,"E8.29.0"),sQuery(id+"F0.wireOp",EDGE,"E8.30.0"),sQuery(id+"F0.wireOp",EDGE,"E8.31.0"),sQuery(id+"F0.wireOp",EDGE,"E8.32.0"),sQuery(id+"F0.wireOp",EDGE,"E8.33.0"),sQuery(id+"F0.wireOp",EDGE,"E8.34.0"),sQuery(id+"F0.wireOp",EDGE,"E8.35.0"),sQuery(id+"F0.wireOp",EDGE,"E8.36.0"),sQuery(id+"F0.wireOp",EDGE,"E8.37.0"),sQuery(id+"F0.wireOp",EDGE,"E8.38.0"),sQuery(id+"F0.wireOp",EDGE,"E8.39.0"),sQuery(id+"F0.wireOp",EDGE,"E8.40.0"),sQuery(id+"F0.wireOp",EDGE,"E8.41.0"),sQuery(id+"F0.wireOp",EDGE,"E8.42.0"),sQuery(id+"F0.wireOp",EDGE,"E8.43.0")])],"isStart":false})],"blendedInto":[makeQuery(id+"F1.opExtrude","CAP_FACE",FACE,{"disambiguationData":[OSD([sQuery(id+"F0.wireOp",EDGE,"E0"),sQuery(id+"F0.wireOp",EDGE,"E1"),sQuery(id+"F0.wireOp",EDGE,"E2"),sQuery(id+"F0.wireOp",EDGE,"E4"),sQuery(id+"F0.wireOp",EDGE,"E5"),sQuery(id+"F0.wireOp",EDGE,"E6.1.1"),sQuery(id+"F0.wireOp",EDGE,"E6.1.2"),sQuery(id+"F0.wireOp",EDGE,"E6.1.3"),sQuery(id+"F0.wireOp",EDGE,"E6.1.4"),sQuery(id+"F0.wireOp",EDGE,"E6.2.1"),sQuery(id+"F0.wireOp",EDGE,"E6.2.2"),sQuery(id+"F0.wireOp",EDGE,"E6.2.3"),sQuery(id+"F0.wireOp",EDGE,"E6.2.4"),sQuery(id+"F0.wireOp",EDGE,"E6.3.1"),sQuery(id+"F0.wireOp",EDGE,"E6.3.2"),sQuery(id+"F0.wireOp",EDGE,"E6.3.3"),sQuery(id+"F0.wireOp",EDGE,"E6.3.4"),sQuery(id+"F0.wireOp",EDGE,"E6.4.1"),sQuery(id+"F0.wireOp",EDGE,"E6.4.2"),sQuery(id+"F0.wireOp",EDGE,"E6.4.3"),sQuery(id+"F0.wireOp",EDGE,"E6.4.4"),sQuery(id+"F0.wireOp",EDGE,"E6.5.1"),sQuery(id+"F0.wireOp",EDGE,"E6.5.2"),sQuery(id+"F0.wireOp",EDGE,"E6.5.3"),sQuery(id+"F0.wireOp",EDGE,"E6.5.4"),sQuery(id+"F0.wireOp",EDGE,"E6.6.1"),sQuery(id+"F0.wireOp",EDGE,"E6.6.2"),sQuery(id+"F0.wireOp",EDGE,"E6.6.3"),sQuery(id+"F0.wireOp",EDGE,"E6.6.4"),sQuery(id+"F0.wireOp",EDGE,"E6.7.1"),sQuery(id+"F0.wireOp",EDGE,"E6.7.2"),sQuery(id+"F0.wireOp",EDGE,"E6.7.3"),sQuery(id+"F0.wireOp",EDGE,"E6.7.4"),sQuery(id+"F0.wireOp",EDGE,"E6.8.1"),sQuery(id+"F0.wireOp",EDGE,"E6.8.2"),sQuery(id+"F0.wireOp",EDGE,"E6.8.3"),sQuery(id+"F0.wireOp",EDGE,"E6.8.4"),sQuery(id+"F0.wireOp",EDGE,"E6.9.1"),sQuery(id+"F0.wireOp",EDGE,"E6.9.2"),sQuery(id+"F0.wireOp",EDGE,"E6.9.3"),sQuery(id+"F0.wireOp",EDGE,"E6.9.4"),sQuery(id+"F0.wireOp",EDGE,"E6.10.1"),sQuery(id+"F0.wireOp",EDGE,"E6.10.2"),sQuery(id+"F0.wireOp",EDGE,"E6.10.3"),sQuery(id+"F0.wireOp",EDGE,"E6.10.4"),sQuery(id+"F0.wireOp",EDGE,"E6.11.1"),sQuery(id+"F0.wireOp",EDGE,"E6.11.2"),sQuery(id+"F0.wireOp",EDGE,"E6.11.3"),sQuery(id+"F0.wireOp",EDGE,"E6.11.4"),sQuery(id+"F0.wireOp",EDGE,"E6.12.1"),sQuery(id+"F0.wireOp",EDGE,"E6.12.2"),sQuery(id+"F0.wireOp",EDGE,"E6.12.3"),sQuery(id+"F0.wireOp",EDGE,"E6.12.4"),sQuery(id+"F0.wireOp",EDGE,"E6.13.1"),sQuery(id+"F0.wireOp",EDGE,"E6.13.2"),sQuery(id+"F0.wireOp",EDGE,"E6.13.3"),sQuery(id+"F0.wireOp",EDGE,"E6.13.4"),sQuery(id+"F0.wireOp",EDGE,"E6.14.1"),sQuery(id+"F0.wireOp",EDGE,"E6.14.2"),sQuery(id+"F0.wireOp",EDGE,"E6.14.3"),sQuery(id+"F0.wireOp",EDGE,"E6.14.4"),sQuery(id+"F0.wireOp",EDGE,"E6.15.1"),sQuery(id+"F0.wireOp",EDGE,"E6.15.2"),sQuery(id+"F0.wireOp",EDGE,"E6.15.3"),sQuery(id+"F0.wireOp",EDGE,"E6.15.4"),sQuery(id+"F0.wireOp",EDGE,"E6.16.1"),sQuery(id+"F0.wireOp",EDGE,"E6.16.2"),sQuery(id+"F0.wireOp",EDGE,"E6.16.3"),sQuery(id+"F0.wireOp",EDGE,"E6.16.4"),sQuery(id+"F0.wireOp",EDGE,"E6.17.1"),sQuery(id+"F0.wireOp",EDGE,"E6.17.2"),sQuery(id+"F0.wireOp",EDGE,"E6.17.3"),sQuery(id+"F0.wireOp",EDGE,"E6.17.4"),sQuery(id+"F0.wireOp",EDGE,"E6.18.1"),sQuery(id+"F0.wireOp",EDGE,"E6.18.2"),sQuery(id+"F0.wireOp",EDGE,"E6.18.3"),sQuery(id+"F0.wireOp",EDGE,"E6.18.4"),sQuery(id+"F0.wireOp",EDGE,"E6.19.1"),sQuery(id+"F0.wireOp",EDGE,"E6.19.2"),sQuery(id+"F0.wireOp",EDGE,"E6.19.3"),sQuery(id+"F0.wireOp",EDGE,"E6.19.4"),sQuery(id+"F0.wireOp",EDGE,"E6.20.1"),sQuery(id+"F0.wireOp",EDGE,"E6.20.2"),sQuery(id+"F0.wireOp",EDGE,"E6.20.3"),sQuery(id+"F0.wireOp",EDGE,"E6.20.4"),sQuery(id+"F0.wireOp",EDGE,"E6.21.1"),sQuery(id+"F0.wireOp",EDGE,"E6.21.2"),sQuery(id+"F0.wireOp",EDGE,"E6.21.3"),sQuery(id+"F0.wireOp",EDGE,"E6.21.4"),sQuery(id+"F0.wireOp",EDGE,"E6.22.1"),sQuery(id+"F0.wireOp",EDGE,"E6.22.2"),sQuery(id+"F0.wireOp",EDGE,"E6.22.3"),sQuery(id+"F0.wireOp",EDGE,"E6.22.4"),sQuery(id+"F0.wireOp",EDGE,"E6.23.1"),sQuery(id+"F0.wireOp",EDGE,"E6.23.2"),sQuery(id+"F0.wireOp",EDGE,"E6.23.3"),sQuery(id+"F0.wireOp",EDGE,"E6.23.4"),sQuery(id+"F0.wireOp",EDGE,"E6.24.1"),sQuery(id+"F0.wireOp",EDGE,"E6.24.2"),sQuery(id+"F0.wireOp",EDGE,"E6.24.3"),sQuery(id+"F0.wireOp",EDGE,"E6.24.4"),sQuery(id+"F0.wireOp",EDGE,"E6.25.1"),sQuery(id+"F0.wireOp",EDGE,"E6.25.2"),sQuery(id+"F0.wireOp",EDGE,"E6.25.3"),sQuery(id+"F0.wireOp",EDGE,"E6.25.4"),sQuery(id+"F0.wireOp",EDGE,"E6.26.1"),sQuery(id+"F0.wireOp",EDGE,"E6.26.2"),sQuery(id+"F0.wireOp",EDGE,"E6.26.3"),sQuery(id+"F0.wireOp",EDGE,"E6.26.4"),sQuery(id+"F0.wireOp",EDGE,"E6.27.1"),sQuery(id+"F0.wireOp",EDGE,"E6.27.2"),sQuery(id+"F0.wireOp",EDGE,"E6.27.3"),sQuery(id+"F0.wireOp",EDGE,"E6.27.4"),sQuery(id+"F0.wireOp",EDGE,"E6.28.1"),sQuery(id+"F0.wireOp",EDGE,"E6.28.2"),sQuery(id+"F0.wireOp",EDGE,"E6.28.3"),sQuery(id+"F0.wireOp",EDGE,"E6.28.4"),sQuery(id+"F0.wireOp",EDGE,"E6.29.1"),sQuery(id+"F0.wireOp",EDGE,"E6.29.2"),sQuery(id+"F0.wireOp",EDGE,"E6.29.3"),sQuery(id+"F0.wireOp",EDGE,"E6.29.4"),sQuery(id+"F0.wireOp",EDGE,"E6.30.1"),sQuery(id+"F0.wireOp",EDGE,"E6.30.2"),sQuery(id+"F0.wireOp",EDGE,"E6.30.3"),sQuery(id+"F0.wireOp",EDGE,"E6.30.4"),sQuery(id+"F0.wireOp",EDGE,"E6.31.1"),sQuery(id+"F0.wireOp",EDGE,"E6.31.2"),sQuery(id+"F0.wireOp",EDGE,"E6.31.3"),sQuery(id+"F0.wireOp",EDGE,"E6.31.4"),sQuery(id+"F0.wireOp",EDGE,"E6.32.1"),sQuery(id+"F0.wireOp",EDGE,"E6.32.2"),sQuery(id+"F0.wireOp",EDGE,"E6.32.3"),sQuery(id+"F0.wireOp",EDGE,"E6.32.4"),sQuery(id+"F0.wireOp",EDGE,"E6.33.1"),sQuery(id+"F0.wireOp",EDGE,"E6.33.2"),sQuery(id+"F0.wireOp",EDGE,"E6.33.3"),sQuery(id+"F0.wireOp",EDGE,"E6.33.4"),sQuery(id+"F0.wireOp",EDGE,"E6.34.1"),sQuery(id+"F0.wireOp",EDGE,"E6.34.2"),sQuery(id+"F0.wireOp",EDGE,"E6.34.3"),sQuery(id+"F0.wireOp",EDGE,"E6.34.4"),sQuery(id+"F0.wireOp",EDGE,"E6.35.1"),sQuery(id+"F0.wireOp",EDGE,"E6.35.2"),sQuery(id+"F0.wireOp",EDGE,"E6.35.3"),sQuery(id+"F0.wireOp",EDGE,"E6.35.4"),sQuery(id+"F0.wireOp",EDGE,"E6.36.1"),sQuery(id+"F0.wireOp",EDGE,"E6.36.2"),sQuery(id+"F0.wireOp",EDGE,"E6.36.3"),sQuery(id+"F0.wireOp",EDGE,"E6.36.4"),sQuery(id+"F0.wireOp",EDGE,"E6.37.1"),sQuery(id+"F0.wireOp",EDGE,"E6.37.2"),sQuery(id+"F0.wireOp",EDGE,"E6.37.3"),sQuery(id+"F0.wireOp",EDGE,"E6.37.4"),sQuery(id+"F0.wireOp",EDGE,"E6.38.1"),sQuery(id+"F0.wireOp",EDGE,"E6.38.2"),sQuery(id+"F0.wireOp",EDGE,"E6.38.3"),sQuery(id+"F0.wireOp",EDGE,"E6.38.4"),subQ1,sQuery(id+"F0.wireOp",EDGE,"E6.39.2"),subQ0,sQuery(id+"F0.wireOp",EDGE,"E6.39.4"),sQuery(id+"F0.wireOp",EDGE,"E6.40.1"),sQuery(id+"F0.wireOp",EDGE,"E6.40.2"),sQuery(id+"F0.wireOp",EDGE,"E6.40.3"),sQuery(id+"F0.wireOp",EDGE,"E6.40.4"),sQuery(id+"F0.wireOp",EDGE,"E6.41.1"),sQuery(id+"F0.wireOp",EDGE,"E6.41.2"),sQuery(id+"F0.wireOp",EDGE,"E6.41.3"),sQuery(id+"F0.wireOp",EDGE,"E6.41.4"),sQuery(id+"F0.wireOp",EDGE,"E6.42.1"),sQuery(id+"F0.wireOp",EDGE,"E6.42.2"),sQuery(id+"F0.wireOp",EDGE,"E6.42.3"),sQuery(id+"F0.wireOp",EDGE,"E6.42.4"),sQuery(id+"F0.wireOp",EDGE,"E6.43.1"),sQuery(id+"F0.wireOp",EDGE,"E6.43.2"),sQuery(id+"F0.wireOp",EDGE,"E6.43.3"),sQuery(id+"F0.wireOp",EDGE,"E6.43.4"),sQuery(id+"F0.wireOp",EDGE,"E7"),sQuery(id+"F0.wireOp",EDGE,"E8.1.0"),sQuery(id+"F0.wireOp",EDGE,"E8.2.0"),sQuery(id+"F0.wireOp",EDGE,"E8.3.0"),sQuery(id+"F0.wireOp",EDGE,"E8.4.0"),sQuery(id+"F0.wireOp",EDGE,"E8.5.0"),sQuery(id+"F0.wireOp",EDGE,"E8.6.0"),sQuery(id+"F0.wireOp",EDGE,"E8.7.0"),sQuery(id+"F0.wireOp",EDGE,"E8.8.0"),sQuery(id+"F0.wireOp",EDGE,"E8.9.0"),sQuery(id+"F0.wireOp",EDGE,"E8.10.0"),sQuery(id+"F0.wireOp",EDGE,"E8.11.0"),sQuery(id+"F0.wireOp",EDGE,"E8.12.0"),sQuery(id+"F0.wireOp",EDGE,"E8.13.0"),sQuery(id+"F0.wireOp",EDGE,"E8.14.0"),sQuery(id+"F0.wireOp",EDGE,"E8.15.0"),sQuery(id+"F0.wireOp",EDGE,"E8.16.0"),sQuery(id+"F0.wireOp",EDGE,"E8.17.0"),sQuery(id+"F0.wireOp",EDGE,"E8.18.0"),sQuery(id+"F0.wireOp",EDGE,"E8.19.0"),sQuery(id+"F0.wireOp",EDGE,"E8.20.0"),sQuery(id+"F0.wireOp",EDGE,"E8.21.0"),sQuery(id+"F0.wireOp",EDGE,"E8.22.0"),sQuery(id+"F0.wireOp",EDGE,"E8.23.0"),sQuery(id+"F0.wireOp",EDGE,"E8.24.0"),sQuery(id+"F0.wireOp",EDGE,"E8.25.0"),sQuery(id+"F0.wireOp",EDGE,"E8.26.0"),sQuery(id+"F0.wireOp",EDGE,"E8.27.0"),sQuery(id+"F0.wireOp",EDGE,"E8.28.0"),sQuery(id+"F0.wireOp",EDGE,"E8.29.0"),sQuery(id+"F0.wireOp",EDGE,"E8.30.0"),sQuery(id+"F0.wireOp",EDGE,"E8.31.0"),sQuery(id+"F0.wireOp",EDGE,"E8.32.0"),sQuery(id+"F0.wireOp",EDGE,"E8.33.0"),sQuery(id+"F0.wireOp",EDGE,"E8.34.0"),sQuery(id+"F0.wireOp",EDGE,"E8.35.0"),sQuery(id+"F0.wireOp",EDGE,"E8.36.0"),sQuery(id+"F0.wireOp",EDGE,"E8.37.0"),sQuery(id+"F0.wireOp",EDGE,"E8.38.0"),sQuery(id+"F0.wireOp",EDGE,"E8.39.0"),sQuery(id+"F0.wireOp",EDGE,"E8.40.0"),sQuery(id+"F0.wireOp",EDGE,"E8.41.0"),sQuery(id+"F0.wireOp",EDGE,"E8.42.0"),sQuery(id+"F0.wireOp",EDGE,"E8.43.0")])],"isStart":false})]});}
            var Q9;
            {var subQ0=sQuery(id+"F0.wireOp",EDGE,"E6.41.3");var subQ1=sQuery(id+"F0.wireOp",EDGE,"E6.41.1");Q9=makeQuery(id+"F2.opFillet","BLEND_EDGE",EDGE,{"blendedFrom":[makeQuery(id+"F1.opExtrude","SWEPT_EDGE",EDGE,{"disambiguationData":[OSD([sQuery(id+"F0.wireOp",EDGE,"E6.41.0"),subQ1,subQ0])]}),makeQuery(id+"F1.opExtrude","CAP_FACE",FACE,{"disambiguationData":[OSD([sQuery(id+"F0.wireOp",EDGE,"E0"),sQuery(id+"F0.wireOp",EDGE,"E1"),sQuery(id+"F0.wireOp",EDGE,"E2"),sQuery(id+"F0.wireOp",EDGE,"E4"),sQuery(id+"F0.wireOp",EDGE,"E5"),sQuery(id+"F0.wireOp",EDGE,"E6.1.1"),sQuery(id+"F0.wireOp",EDGE,"E6.1.2"),sQuery(id+"F0.wireOp",EDGE,"E6.1.3"),sQuery(id+"F0.wireOp",EDGE,"E6.1.4"),sQuery(id+"F0.wireOp",EDGE,"E6.2.1"),sQuery(id+"F0.wireOp",EDGE,"E6.2.2"),sQuery(id+"F0.wireOp",EDGE,"E6.2.3"),sQuery(id+"F0.wireOp",EDGE,"E6.2.4"),sQuery(id+"F0.wireOp",EDGE,"E6.3.1"),sQuery(id+"F0.wireOp",EDGE,"E6.3.2"),sQuery(id+"F0.wireOp",EDGE,"E6.3.3"),sQuery(id+"F0.wireOp",EDGE,"E6.3.4"),sQuery(id+"F0.wireOp",EDGE,"E6.4.1"),sQuery(id+"F0.wireOp",EDGE,"E6.4.2"),sQuery(id+"F0.wireOp",EDGE,"E6.4.3"),sQuery(id+"F0.wireOp",EDGE,"E6.4.4"),sQuery(id+"F0.wireOp",EDGE,"E6.5.1"),sQuery(id+"F0.wireOp",EDGE,"E6.5.2"),sQuery(id+"F0.wireOp",EDGE,"E6.5.3"),sQuery(id+"F0.wireOp",EDGE,"E6.5.4"),sQuery(id+"F0.wireOp",EDGE,"E6.6.1"),sQuery(id+"F0.wireOp",EDGE,"E6.6.2"),sQuery(id+"F0.wireOp",EDGE,"E6.6.3"),sQuery(id+"F0.wireOp",EDGE,"E6.6.4"),sQuery(id+"F0.wireOp",EDGE,"E6.7.1"),sQuery(id+"F0.wireOp",EDGE,"E6.7.2"),sQuery(id+"F0.wireOp",EDGE,"E6.7.3"),sQuery(id+"F0.wireOp",EDGE,"E6.7.4"),sQuery(id+"F0.wireOp",EDGE,"E6.8.1"),sQuery(id+"F0.wireOp",EDGE,"E6.8.2"),sQuery(id+"F0.wireOp",EDGE,"E6.8.3"),sQuery(id+"F0.wireOp",EDGE,"E6.8.4"),sQuery(id+"F0.wireOp",EDGE,"E6.9.1"),sQuery(id+"F0.wireOp",EDGE,"E6.9.2"),sQuery(id+"F0.wireOp",EDGE,"E6.9.3"),sQuery(id+"F0.wireOp",EDGE,"E6.9.4"),sQuery(id+"F0.wireOp",EDGE,"E6.10.1"),sQuery(id+"F0.wireOp",EDGE,"E6.10.2"),sQuery(id+"F0.wireOp",EDGE,"E6.10.3"),sQuery(id+"F0.wireOp",EDGE,"E6.10.4"),sQuery(id+"F0.wireOp",EDGE,"E6.11.1"),sQuery(id+"F0.wireOp",EDGE,"E6.11.2"),sQuery(id+"F0.wireOp",EDGE,"E6.11.3"),sQuery(id+"F0.wireOp",EDGE,"E6.11.4"),sQuery(id+"F0.wireOp",EDGE,"E6.12.1"),sQuery(id+"F0.wireOp",EDGE,"E6.12.2"),sQuery(id+"F0.wireOp",EDGE,"E6.12.3"),sQuery(id+"F0.wireOp",EDGE,"E6.12.4"),sQuery(id+"F0.wireOp",EDGE,"E6.13.1"),sQuery(id+"F0.wireOp",EDGE,"E6.13.2"),sQuery(id+"F0.wireOp",EDGE,"E6.13.3"),sQuery(id+"F0.wireOp",EDGE,"E6.13.4"),sQuery(id+"F0.wireOp",EDGE,"E6.14.1"),sQuery(id+"F0.wireOp",EDGE,"E6.14.2"),sQuery(id+"F0.wireOp",EDGE,"E6.14.3"),sQuery(id+"F0.wireOp",EDGE,"E6.14.4"),sQuery(id+"F0.wireOp",EDGE,"E6.15.1"),sQuery(id+"F0.wireOp",EDGE,"E6.15.2"),sQuery(id+"F0.wireOp",EDGE,"E6.15.3"),sQuery(id+"F0.wireOp",EDGE,"E6.15.4"),sQuery(id+"F0.wireOp",EDGE,"E6.16.1"),sQuery(id+"F0.wireOp",EDGE,"E6.16.2"),sQuery(id+"F0.wireOp",EDGE,"E6.16.3"),sQuery(id+"F0.wireOp",EDGE,"E6.16.4"),sQuery(id+"F0.wireOp",EDGE,"E6.17.1"),sQuery(id+"F0.wireOp",EDGE,"E6.17.2"),sQuery(id+"F0.wireOp",EDGE,"E6.17.3"),sQuery(id+"F0.wireOp",EDGE,"E6.17.4"),sQuery(id+"F0.wireOp",EDGE,"E6.18.1"),sQuery(id+"F0.wireOp",EDGE,"E6.18.2"),sQuery(id+"F0.wireOp",EDGE,"E6.18.3"),sQuery(id+"F0.wireOp",EDGE,"E6.18.4"),sQuery(id+"F0.wireOp",EDGE,"E6.19.1"),sQuery(id+"F0.wireOp",EDGE,"E6.19.2"),sQuery(id+"F0.wireOp",EDGE,"E6.19.3"),sQuery(id+"F0.wireOp",EDGE,"E6.19.4"),sQuery(id+"F0.wireOp",EDGE,"E6.20.1"),sQuery(id+"F0.wireOp",EDGE,"E6.20.2"),sQuery(id+"F0.wireOp",EDGE,"E6.20.3"),sQuery(id+"F0.wireOp",EDGE,"E6.20.4"),sQuery(id+"F0.wireOp",EDGE,"E6.21.1"),sQuery(id+"F0.wireOp",EDGE,"E6.21.2"),sQuery(id+"F0.wireOp",EDGE,"E6.21.3"),sQuery(id+"F0.wireOp",EDGE,"E6.21.4"),sQuery(id+"F0.wireOp",EDGE,"E6.22.1"),sQuery(id+"F0.wireOp",EDGE,"E6.22.2"),sQuery(id+"F0.wireOp",EDGE,"E6.22.3"),sQuery(id+"F0.wireOp",EDGE,"E6.22.4"),sQuery(id+"F0.wireOp",EDGE,"E6.23.1"),sQuery(id+"F0.wireOp",EDGE,"E6.23.2"),sQuery(id+"F0.wireOp",EDGE,"E6.23.3"),sQuery(id+"F0.wireOp",EDGE,"E6.23.4"),sQuery(id+"F0.wireOp",EDGE,"E6.24.1"),sQuery(id+"F0.wireOp",EDGE,"E6.24.2"),sQuery(id+"F0.wireOp",EDGE,"E6.24.3"),sQuery(id+"F0.wireOp",EDGE,"E6.24.4"),sQuery(id+"F0.wireOp",EDGE,"E6.25.1"),sQuery(id+"F0.wireOp",EDGE,"E6.25.2"),sQuery(id+"F0.wireOp",EDGE,"E6.25.3"),sQuery(id+"F0.wireOp",EDGE,"E6.25.4"),sQuery(id+"F0.wireOp",EDGE,"E6.26.1"),sQuery(id+"F0.wireOp",EDGE,"E6.26.2"),sQuery(id+"F0.wireOp",EDGE,"E6.26.3"),sQuery(id+"F0.wireOp",EDGE,"E6.26.4"),sQuery(id+"F0.wireOp",EDGE,"E6.27.1"),sQuery(id+"F0.wireOp",EDGE,"E6.27.2"),sQuery(id+"F0.wireOp",EDGE,"E6.27.3"),sQuery(id+"F0.wireOp",EDGE,"E6.27.4"),sQuery(id+"F0.wireOp",EDGE,"E6.28.1"),sQuery(id+"F0.wireOp",EDGE,"E6.28.2"),sQuery(id+"F0.wireOp",EDGE,"E6.28.3"),sQuery(id+"F0.wireOp",EDGE,"E6.28.4"),sQuery(id+"F0.wireOp",EDGE,"E6.29.1"),sQuery(id+"F0.wireOp",EDGE,"E6.29.2"),sQuery(id+"F0.wireOp",EDGE,"E6.29.3"),sQuery(id+"F0.wireOp",EDGE,"E6.29.4"),sQuery(id+"F0.wireOp",EDGE,"E6.30.1"),sQuery(id+"F0.wireOp",EDGE,"E6.30.2"),sQuery(id+"F0.wireOp",EDGE,"E6.30.3"),sQuery(id+"F0.wireOp",EDGE,"E6.30.4"),sQuery(id+"F0.wireOp",EDGE,"E6.31.1"),sQuery(id+"F0.wireOp",EDGE,"E6.31.2"),sQuery(id+"F0.wireOp",EDGE,"E6.31.3"),sQuery(id+"F0.wireOp",EDGE,"E6.31.4"),sQuery(id+"F0.wireOp",EDGE,"E6.32.1"),sQuery(id+"F0.wireOp",EDGE,"E6.32.2"),sQuery(id+"F0.wireOp",EDGE,"E6.32.3"),sQuery(id+"F0.wireOp",EDGE,"E6.32.4"),sQuery(id+"F0.wireOp",EDGE,"E6.33.1"),sQuery(id+"F0.wireOp",EDGE,"E6.33.2"),sQuery(id+"F0.wireOp",EDGE,"E6.33.3"),sQuery(id+"F0.wireOp",EDGE,"E6.33.4"),sQuery(id+"F0.wireOp",EDGE,"E6.34.1"),sQuery(id+"F0.wireOp",EDGE,"E6.34.2"),sQuery(id+"F0.wireOp",EDGE,"E6.34.3"),sQuery(id+"F0.wireOp",EDGE,"E6.34.4"),sQuery(id+"F0.wireOp",EDGE,"E6.35.1"),sQuery(id+"F0.wireOp",EDGE,"E6.35.2"),sQuery(id+"F0.wireOp",EDGE,"E6.35.3"),sQuery(id+"F0.wireOp",EDGE,"E6.35.4"),sQuery(id+"F0.wireOp",EDGE,"E6.36.1"),sQuery(id+"F0.wireOp",EDGE,"E6.36.2"),sQuery(id+"F0.wireOp",EDGE,"E6.36.3"),sQuery(id+"F0.wireOp",EDGE,"E6.36.4"),sQuery(id+"F0.wireOp",EDGE,"E6.37.1"),sQuery(id+"F0.wireOp",EDGE,"E6.37.2"),sQuery(id+"F0.wireOp",EDGE,"E6.37.3"),sQuery(id+"F0.wireOp",EDGE,"E6.37.4"),sQuery(id+"F0.wireOp",EDGE,"E6.38.1"),sQuery(id+"F0.wireOp",EDGE,"E6.38.2"),sQuery(id+"F0.wireOp",EDGE,"E6.38.3"),sQuery(id+"F0.wireOp",EDGE,"E6.38.4"),sQuery(id+"F0.wireOp",EDGE,"E6.39.1"),sQuery(id+"F0.wireOp",EDGE,"E6.39.2"),sQuery(id+"F0.wireOp",EDGE,"E6.39.3"),sQuery(id+"F0.wireOp",EDGE,"E6.39.4"),sQuery(id+"F0.wireOp",EDGE,"E6.40.1"),sQuery(id+"F0.wireOp",EDGE,"E6.40.2"),sQuery(id+"F0.wireOp",EDGE,"E6.40.3"),sQuery(id+"F0.wireOp",EDGE,"E6.40.4"),subQ1,sQuery(id+"F0.wireOp",EDGE,"E6.41.2"),subQ0,sQuery(id+"F0.wireOp",EDGE,"E6.41.4"),sQuery(id+"F0.wireOp",EDGE,"E6.42.1"),sQuery(id+"F0.wireOp",EDGE,"E6.42.2"),sQuery(id+"F0.wireOp",EDGE,"E6.42.3"),sQuery(id+"F0.wireOp",EDGE,"E6.42.4"),sQuery(id+"F0.wireOp",EDGE,"E6.43.1"),sQuery(id+"F0.wireOp",EDGE,"E6.43.2"),sQuery(id+"F0.wireOp",EDGE,"E6.43.3"),sQuery(id+"F0.wireOp",EDGE,"E6.43.4"),sQuery(id+"F0.wireOp",EDGE,"E7"),sQuery(id+"F0.wireOp",EDGE,"E8.1.0"),sQuery(id+"F0.wireOp",EDGE,"E8.2.0"),sQuery(id+"F0.wireOp",EDGE,"E8.3.0"),sQuery(id+"F0.wireOp",EDGE,"E8.4.0"),sQuery(id+"F0.wireOp",EDGE,"E8.5.0"),sQuery(id+"F0.wireOp",EDGE,"E8.6.0"),sQuery(id+"F0.wireOp",EDGE,"E8.7.0"),sQuery(id+"F0.wireOp",EDGE,"E8.8.0"),sQuery(id+"F0.wireOp",EDGE,"E8.9.0"),sQuery(id+"F0.wireOp",EDGE,"E8.10.0"),sQuery(id+"F0.wireOp",EDGE,"E8.11.0"),sQuery(id+"F0.wireOp",EDGE,"E8.12.0"),sQuery(id+"F0.wireOp",EDGE,"E8.13.0"),sQuery(id+"F0.wireOp",EDGE,"E8.14.0"),sQuery(id+"F0.wireOp",EDGE,"E8.15.0"),sQuery(id+"F0.wireOp",EDGE,"E8.16.0"),sQuery(id+"F0.wireOp",EDGE,"E8.17.0"),sQuery(id+"F0.wireOp",EDGE,"E8.18.0"),sQuery(id+"F0.wireOp",EDGE,"E8.19.0"),sQuery(id+"F0.wireOp",EDGE,"E8.20.0"),sQuery(id+"F0.wireOp",EDGE,"E8.21.0"),sQuery(id+"F0.wireOp",EDGE,"E8.22.0"),sQuery(id+"F0.wireOp",EDGE,"E8.23.0"),sQuery(id+"F0.wireOp",EDGE,"E8.24.0"),sQuery(id+"F0.wireOp",EDGE,"E8.25.0"),sQuery(id+"F0.wireOp",EDGE,"E8.26.0"),sQuery(id+"F0.wireOp",EDGE,"E8.27.0"),sQuery(id+"F0.wireOp",EDGE,"E8.28.0"),sQuery(id+"F0.wireOp",EDGE,"E8.29.0"),sQuery(id+"F0.wireOp",EDGE,"E8.30.0"),sQuery(id+"F0.wireOp",EDGE,"E8.31.0"),sQuery(id+"F0.wireOp",EDGE,"E8.32.0"),sQuery(id+"F0.wireOp",EDGE,"E8.33.0"),sQuery(id+"F0.wireOp",EDGE,"E8.34.0"),sQuery(id+"F0.wireOp",EDGE,"E8.35.0"),sQuery(id+"F0.wireOp",EDGE,"E8.36.0"),sQuery(id+"F0.wireOp",EDGE,"E8.37.0"),sQuery(id+"F0.wireOp",EDGE,"E8.38.0"),sQuery(id+"F0.wireOp",EDGE,"E8.39.0"),sQuery(id+"F0.wireOp",EDGE,"E8.40.0"),sQuery(id+"F0.wireOp",EDGE,"E8.41.0"),sQuery(id+"F0.wireOp",EDGE,"E8.42.0"),sQuery(id+"F0.wireOp",EDGE,"E8.43.0")])],"isStart":false})],"blendedInto":[makeQuery(id+"F1.opExtrude","CAP_FACE",FACE,{"disambiguationData":[OSD([sQuery(id+"F0.wireOp",EDGE,"E0"),sQuery(id+"F0.wireOp",EDGE,"E1"),sQuery(id+"F0.wireOp",EDGE,"E2"),sQuery(id+"F0.wireOp",EDGE,"E4"),sQuery(id+"F0.wireOp",EDGE,"E5"),sQuery(id+"F0.wireOp",EDGE,"E6.1.1"),sQuery(id+"F0.wireOp",EDGE,"E6.1.2"),sQuery(id+"F0.wireOp",EDGE,"E6.1.3"),sQuery(id+"F0.wireOp",EDGE,"E6.1.4"),sQuery(id+"F0.wireOp",EDGE,"E6.2.1"),sQuery(id+"F0.wireOp",EDGE,"E6.2.2"),sQuery(id+"F0.wireOp",EDGE,"E6.2.3"),sQuery(id+"F0.wireOp",EDGE,"E6.2.4"),sQuery(id+"F0.wireOp",EDGE,"E6.3.1"),sQuery(id+"F0.wireOp",EDGE,"E6.3.2"),sQuery(id+"F0.wireOp",EDGE,"E6.3.3"),sQuery(id+"F0.wireOp",EDGE,"E6.3.4"),sQuery(id+"F0.wireOp",EDGE,"E6.4.1"),sQuery(id+"F0.wireOp",EDGE,"E6.4.2"),sQuery(id+"F0.wireOp",EDGE,"E6.4.3"),sQuery(id+"F0.wireOp",EDGE,"E6.4.4"),sQuery(id+"F0.wireOp",EDGE,"E6.5.1"),sQuery(id+"F0.wireOp",EDGE,"E6.5.2"),sQuery(id+"F0.wireOp",EDGE,"E6.5.3"),sQuery(id+"F0.wireOp",EDGE,"E6.5.4"),sQuery(id+"F0.wireOp",EDGE,"E6.6.1"),sQuery(id+"F0.wireOp",EDGE,"E6.6.2"),sQuery(id+"F0.wireOp",EDGE,"E6.6.3"),sQuery(id+"F0.wireOp",EDGE,"E6.6.4"),sQuery(id+"F0.wireOp",EDGE,"E6.7.1"),sQuery(id+"F0.wireOp",EDGE,"E6.7.2"),sQuery(id+"F0.wireOp",EDGE,"E6.7.3"),sQuery(id+"F0.wireOp",EDGE,"E6.7.4"),sQuery(id+"F0.wireOp",EDGE,"E6.8.1"),sQuery(id+"F0.wireOp",EDGE,"E6.8.2"),sQuery(id+"F0.wireOp",EDGE,"E6.8.3"),sQuery(id+"F0.wireOp",EDGE,"E6.8.4"),sQuery(id+"F0.wireOp",EDGE,"E6.9.1"),sQuery(id+"F0.wireOp",EDGE,"E6.9.2"),sQuery(id+"F0.wireOp",EDGE,"E6.9.3"),sQuery(id+"F0.wireOp",EDGE,"E6.9.4"),sQuery(id+"F0.wireOp",EDGE,"E6.10.1"),sQuery(id+"F0.wireOp",EDGE,"E6.10.2"),sQuery(id+"F0.wireOp",EDGE,"E6.10.3"),sQuery(id+"F0.wireOp",EDGE,"E6.10.4"),sQuery(id+"F0.wireOp",EDGE,"E6.11.1"),sQuery(id+"F0.wireOp",EDGE,"E6.11.2"),sQuery(id+"F0.wireOp",EDGE,"E6.11.3"),sQuery(id+"F0.wireOp",EDGE,"E6.11.4"),sQuery(id+"F0.wireOp",EDGE,"E6.12.1"),sQuery(id+"F0.wireOp",EDGE,"E6.12.2"),sQuery(id+"F0.wireOp",EDGE,"E6.12.3"),sQuery(id+"F0.wireOp",EDGE,"E6.12.4"),sQuery(id+"F0.wireOp",EDGE,"E6.13.1"),sQuery(id+"F0.wireOp",EDGE,"E6.13.2"),sQuery(id+"F0.wireOp",EDGE,"E6.13.3"),sQuery(id+"F0.wireOp",EDGE,"E6.13.4"),sQuery(id+"F0.wireOp",EDGE,"E6.14.1"),sQuery(id+"F0.wireOp",EDGE,"E6.14.2"),sQuery(id+"F0.wireOp",EDGE,"E6.14.3"),sQuery(id+"F0.wireOp",EDGE,"E6.14.4"),sQuery(id+"F0.wireOp",EDGE,"E6.15.1"),sQuery(id+"F0.wireOp",EDGE,"E6.15.2"),sQuery(id+"F0.wireOp",EDGE,"E6.15.3"),sQuery(id+"F0.wireOp",EDGE,"E6.15.4"),sQuery(id+"F0.wireOp",EDGE,"E6.16.1"),sQuery(id+"F0.wireOp",EDGE,"E6.16.2"),sQuery(id+"F0.wireOp",EDGE,"E6.16.3"),sQuery(id+"F0.wireOp",EDGE,"E6.16.4"),sQuery(id+"F0.wireOp",EDGE,"E6.17.1"),sQuery(id+"F0.wireOp",EDGE,"E6.17.2"),sQuery(id+"F0.wireOp",EDGE,"E6.17.3"),sQuery(id+"F0.wireOp",EDGE,"E6.17.4"),sQuery(id+"F0.wireOp",EDGE,"E6.18.1"),sQuery(id+"F0.wireOp",EDGE,"E6.18.2"),sQuery(id+"F0.wireOp",EDGE,"E6.18.3"),sQuery(id+"F0.wireOp",EDGE,"E6.18.4"),sQuery(id+"F0.wireOp",EDGE,"E6.19.1"),sQuery(id+"F0.wireOp",EDGE,"E6.19.2"),sQuery(id+"F0.wireOp",EDGE,"E6.19.3"),sQuery(id+"F0.wireOp",EDGE,"E6.19.4"),sQuery(id+"F0.wireOp",EDGE,"E6.20.1"),sQuery(id+"F0.wireOp",EDGE,"E6.20.2"),sQuery(id+"F0.wireOp",EDGE,"E6.20.3"),sQuery(id+"F0.wireOp",EDGE,"E6.20.4"),sQuery(id+"F0.wireOp",EDGE,"E6.21.1"),sQuery(id+"F0.wireOp",EDGE,"E6.21.2"),sQuery(id+"F0.wireOp",EDGE,"E6.21.3"),sQuery(id+"F0.wireOp",EDGE,"E6.21.4"),sQuery(id+"F0.wireOp",EDGE,"E6.22.1"),sQuery(id+"F0.wireOp",EDGE,"E6.22.2"),sQuery(id+"F0.wireOp",EDGE,"E6.22.3"),sQuery(id+"F0.wireOp",EDGE,"E6.22.4"),sQuery(id+"F0.wireOp",EDGE,"E6.23.1"),sQuery(id+"F0.wireOp",EDGE,"E6.23.2"),sQuery(id+"F0.wireOp",EDGE,"E6.23.3"),sQuery(id+"F0.wireOp",EDGE,"E6.23.4"),sQuery(id+"F0.wireOp",EDGE,"E6.24.1"),sQuery(id+"F0.wireOp",EDGE,"E6.24.2"),sQuery(id+"F0.wireOp",EDGE,"E6.24.3"),sQuery(id+"F0.wireOp",EDGE,"E6.24.4"),sQuery(id+"F0.wireOp",EDGE,"E6.25.1"),sQuery(id+"F0.wireOp",EDGE,"E6.25.2"),sQuery(id+"F0.wireOp",EDGE,"E6.25.3"),sQuery(id+"F0.wireOp",EDGE,"E6.25.4"),sQuery(id+"F0.wireOp",EDGE,"E6.26.1"),sQuery(id+"F0.wireOp",EDGE,"E6.26.2"),sQuery(id+"F0.wireOp",EDGE,"E6.26.3"),sQuery(id+"F0.wireOp",EDGE,"E6.26.4"),sQuery(id+"F0.wireOp",EDGE,"E6.27.1"),sQuery(id+"F0.wireOp",EDGE,"E6.27.2"),sQuery(id+"F0.wireOp",EDGE,"E6.27.3"),sQuery(id+"F0.wireOp",EDGE,"E6.27.4"),sQuery(id+"F0.wireOp",EDGE,"E6.28.1"),sQuery(id+"F0.wireOp",EDGE,"E6.28.2"),sQuery(id+"F0.wireOp",EDGE,"E6.28.3"),sQuery(id+"F0.wireOp",EDGE,"E6.28.4"),sQuery(id+"F0.wireOp",EDGE,"E6.29.1"),sQuery(id+"F0.wireOp",EDGE,"E6.29.2"),sQuery(id+"F0.wireOp",EDGE,"E6.29.3"),sQuery(id+"F0.wireOp",EDGE,"E6.29.4"),sQuery(id+"F0.wireOp",EDGE,"E6.30.1"),sQuery(id+"F0.wireOp",EDGE,"E6.30.2"),sQuery(id+"F0.wireOp",EDGE,"E6.30.3"),sQuery(id+"F0.wireOp",EDGE,"E6.30.4"),sQuery(id+"F0.wireOp",EDGE,"E6.31.1"),sQuery(id+"F0.wireOp",EDGE,"E6.31.2"),sQuery(id+"F0.wireOp",EDGE,"E6.31.3"),sQuery(id+"F0.wireOp",EDGE,"E6.31.4"),sQuery(id+"F0.wireOp",EDGE,"E6.32.1"),sQuery(id+"F0.wireOp",EDGE,"E6.32.2"),sQuery(id+"F0.wireOp",EDGE,"E6.32.3"),sQuery(id+"F0.wireOp",EDGE,"E6.32.4"),sQuery(id+"F0.wireOp",EDGE,"E6.33.1"),sQuery(id+"F0.wireOp",EDGE,"E6.33.2"),sQuery(id+"F0.wireOp",EDGE,"E6.33.3"),sQuery(id+"F0.wireOp",EDGE,"E6.33.4"),sQuery(id+"F0.wireOp",EDGE,"E6.34.1"),sQuery(id+"F0.wireOp",EDGE,"E6.34.2"),sQuery(id+"F0.wireOp",EDGE,"E6.34.3"),sQuery(id+"F0.wireOp",EDGE,"E6.34.4"),sQuery(id+"F0.wireOp",EDGE,"E6.35.1"),sQuery(id+"F0.wireOp",EDGE,"E6.35.2"),sQuery(id+"F0.wireOp",EDGE,"E6.35.3"),sQuery(id+"F0.wireOp",EDGE,"E6.35.4"),sQuery(id+"F0.wireOp",EDGE,"E6.36.1"),sQuery(id+"F0.wireOp",EDGE,"E6.36.2"),sQuery(id+"F0.wireOp",EDGE,"E6.36.3"),sQuery(id+"F0.wireOp",EDGE,"E6.36.4"),sQuery(id+"F0.wireOp",EDGE,"E6.37.1"),sQuery(id+"F0.wireOp",EDGE,"E6.37.2"),sQuery(id+"F0.wireOp",EDGE,"E6.37.3"),sQuery(id+"F0.wireOp",EDGE,"E6.37.4"),sQuery(id+"F0.wireOp",EDGE,"E6.38.1"),sQuery(id+"F0.wireOp",EDGE,"E6.38.2"),sQuery(id+"F0.wireOp",EDGE,"E6.38.3"),sQuery(id+"F0.wireOp",EDGE,"E6.38.4"),sQuery(id+"F0.wireOp",EDGE,"E6.39.1"),sQuery(id+"F0.wireOp",EDGE,"E6.39.2"),sQuery(id+"F0.wireOp",EDGE,"E6.39.3"),sQuery(id+"F0.wireOp",EDGE,"E6.39.4"),sQuery(id+"F0.wireOp",EDGE,"E6.40.1"),sQuery(id+"F0.wireOp",EDGE,"E6.40.2"),sQuery(id+"F0.wireOp",EDGE,"E6.40.3"),sQuery(id+"F0.wireOp",EDGE,"E6.40.4"),subQ1,sQuery(id+"F0.wireOp",EDGE,"E6.41.2"),subQ0,sQuery(id+"F0.wireOp",EDGE,"E6.41.4"),sQuery(id+"F0.wireOp",EDGE,"E6.42.1"),sQuery(id+"F0.wireOp",EDGE,"E6.42.2"),sQuery(id+"F0.wireOp",EDGE,"E6.42.3"),sQuery(id+"F0.wireOp",EDGE,"E6.42.4"),sQuery(id+"F0.wireOp",EDGE,"E6.43.1"),sQuery(id+"F0.wireOp",EDGE,"E6.43.2"),sQuery(id+"F0.wireOp",EDGE,"E6.43.3"),sQuery(id+"F0.wireOp",EDGE,"E6.43.4"),sQuery(id+"F0.wireOp",EDGE,"E7"),sQuery(id+"F0.wireOp",EDGE,"E8.1.0"),sQuery(id+"F0.wireOp",EDGE,"E8.2.0"),sQuery(id+"F0.wireOp",EDGE,"E8.3.0"),sQuery(id+"F0.wireOp",EDGE,"E8.4.0"),sQuery(id+"F0.wireOp",EDGE,"E8.5.0"),sQuery(id+"F0.wireOp",EDGE,"E8.6.0"),sQuery(id+"F0.wireOp",EDGE,"E8.7.0"),sQuery(id+"F0.wireOp",EDGE,"E8.8.0"),sQuery(id+"F0.wireOp",EDGE,"E8.9.0"),sQuery(id+"F0.wireOp",EDGE,"E8.10.0"),sQuery(id+"F0.wireOp",EDGE,"E8.11.0"),sQuery(id+"F0.wireOp",EDGE,"E8.12.0"),sQuery(id+"F0.wireOp",EDGE,"E8.13.0"),sQuery(id+"F0.wireOp",EDGE,"E8.14.0"),sQuery(id+"F0.wireOp",EDGE,"E8.15.0"),sQuery(id+"F0.wireOp",EDGE,"E8.16.0"),sQuery(id+"F0.wireOp",EDGE,"E8.17.0"),sQuery(id+"F0.wireOp",EDGE,"E8.18.0"),sQuery(id+"F0.wireOp",EDGE,"E8.19.0"),sQuery(id+"F0.wireOp",EDGE,"E8.20.0"),sQuery(id+"F0.wireOp",EDGE,"E8.21.0"),sQuery(id+"F0.wireOp",EDGE,"E8.22.0"),sQuery(id+"F0.wireOp",EDGE,"E8.23.0"),sQuery(id+"F0.wireOp",EDGE,"E8.24.0"),sQuery(id+"F0.wireOp",EDGE,"E8.25.0"),sQuery(id+"F0.wireOp",EDGE,"E8.26.0"),sQuery(id+"F0.wireOp",EDGE,"E8.27.0"),sQuery(id+"F0.wireOp",EDGE,"E8.28.0"),sQuery(id+"F0.wireOp",EDGE,"E8.29.0"),sQuery(id+"F0.wireOp",EDGE,"E8.30.0"),sQuery(id+"F0.wireOp",EDGE,"E8.31.0"),sQuery(id+"F0.wireOp",EDGE,"E8.32.0"),sQuery(id+"F0.wireOp",EDGE,"E8.33.0"),sQuery(id+"F0.wireOp",EDGE,"E8.34.0"),sQuery(id+"F0.wireOp",EDGE,"E8.35.0"),sQuery(id+"F0.wireOp",EDGE,"E8.36.0"),sQuery(id+"F0.wireOp",EDGE,"E8.37.0"),sQuery(id+"F0.wireOp",EDGE,"E8.38.0"),sQuery(id+"F0.wireOp",EDGE,"E8.39.0"),sQuery(id+"F0.wireOp",EDGE,"E8.40.0"),sQuery(id+"F0.wireOp",EDGE,"E8.41.0"),sQuery(id+"F0.wireOp",EDGE,"E8.42.0"),sQuery(id+"F0.wireOp",EDGE,"E8.43.0")])],"isStart":false})]});}
            var Q10;
            {var subQ0=sQuery(id+"F0.wireOp",EDGE,"E6.43.3");var subQ1=sQuery(id+"F0.wireOp",EDGE,"E6.43.1");Q10=makeQuery(id+"F2.opFillet","BLEND_EDGE",EDGE,{"blendedFrom":[makeQuery(id+"F1.opExtrude","SWEPT_EDGE",EDGE,{"disambiguationData":[OSD([sQuery(id+"F0.wireOp",EDGE,"E6.43.0"),subQ1,subQ0])]}),makeQuery(id+"F1.opExtrude","CAP_FACE",FACE,{"disambiguationData":[OSD([sQuery(id+"F0.wireOp",EDGE,"E0"),sQuery(id+"F0.wireOp",EDGE,"E1"),sQuery(id+"F0.wireOp",EDGE,"E2"),sQuery(id+"F0.wireOp",EDGE,"E4"),sQuery(id+"F0.wireOp",EDGE,"E5"),sQuery(id+"F0.wireOp",EDGE,"E6.1.1"),sQuery(id+"F0.wireOp",EDGE,"E6.1.2"),sQuery(id+"F0.wireOp",EDGE,"E6.1.3"),sQuery(id+"F0.wireOp",EDGE,"E6.1.4"),sQuery(id+"F0.wireOp",EDGE,"E6.2.1"),sQuery(id+"F0.wireOp",EDGE,"E6.2.2"),sQuery(id+"F0.wireOp",EDGE,"E6.2.3"),sQuery(id+"F0.wireOp",EDGE,"E6.2.4"),sQuery(id+"F0.wireOp",EDGE,"E6.3.1"),sQuery(id+"F0.wireOp",EDGE,"E6.3.2"),sQuery(id+"F0.wireOp",EDGE,"E6.3.3"),sQuery(id+"F0.wireOp",EDGE,"E6.3.4"),sQuery(id+"F0.wireOp",EDGE,"E6.4.1"),sQuery(id+"F0.wireOp",EDGE,"E6.4.2"),sQuery(id+"F0.wireOp",EDGE,"E6.4.3"),sQuery(id+"F0.wireOp",EDGE,"E6.4.4"),sQuery(id+"F0.wireOp",EDGE,"E6.5.1"),sQuery(id+"F0.wireOp",EDGE,"E6.5.2"),sQuery(id+"F0.wireOp",EDGE,"E6.5.3"),sQuery(id+"F0.wireOp",EDGE,"E6.5.4"),sQuery(id+"F0.wireOp",EDGE,"E6.6.1"),sQuery(id+"F0.wireOp",EDGE,"E6.6.2"),sQuery(id+"F0.wireOp",EDGE,"E6.6.3"),sQuery(id+"F0.wireOp",EDGE,"E6.6.4"),sQuery(id+"F0.wireOp",EDGE,"E6.7.1"),sQuery(id+"F0.wireOp",EDGE,"E6.7.2"),sQuery(id+"F0.wireOp",EDGE,"E6.7.3"),sQuery(id+"F0.wireOp",EDGE,"E6.7.4"),sQuery(id+"F0.wireOp",EDGE,"E6.8.1"),sQuery(id+"F0.wireOp",EDGE,"E6.8.2"),sQuery(id+"F0.wireOp",EDGE,"E6.8.3"),sQuery(id+"F0.wireOp",EDGE,"E6.8.4"),sQuery(id+"F0.wireOp",EDGE,"E6.9.1"),sQuery(id+"F0.wireOp",EDGE,"E6.9.2"),sQuery(id+"F0.wireOp",EDGE,"E6.9.3"),sQuery(id+"F0.wireOp",EDGE,"E6.9.4"),sQuery(id+"F0.wireOp",EDGE,"E6.10.1"),sQuery(id+"F0.wireOp",EDGE,"E6.10.2"),sQuery(id+"F0.wireOp",EDGE,"E6.10.3"),sQuery(id+"F0.wireOp",EDGE,"E6.10.4"),sQuery(id+"F0.wireOp",EDGE,"E6.11.1"),sQuery(id+"F0.wireOp",EDGE,"E6.11.2"),sQuery(id+"F0.wireOp",EDGE,"E6.11.3"),sQuery(id+"F0.wireOp",EDGE,"E6.11.4"),sQuery(id+"F0.wireOp",EDGE,"E6.12.1"),sQuery(id+"F0.wireOp",EDGE,"E6.12.2"),sQuery(id+"F0.wireOp",EDGE,"E6.12.3"),sQuery(id+"F0.wireOp",EDGE,"E6.12.4"),sQuery(id+"F0.wireOp",EDGE,"E6.13.1"),sQuery(id+"F0.wireOp",EDGE,"E6.13.2"),sQuery(id+"F0.wireOp",EDGE,"E6.13.3"),sQuery(id+"F0.wireOp",EDGE,"E6.13.4"),sQuery(id+"F0.wireOp",EDGE,"E6.14.1"),sQuery(id+"F0.wireOp",EDGE,"E6.14.2"),sQuery(id+"F0.wireOp",EDGE,"E6.14.3"),sQuery(id+"F0.wireOp",EDGE,"E6.14.4"),sQuery(id+"F0.wireOp",EDGE,"E6.15.1"),sQuery(id+"F0.wireOp",EDGE,"E6.15.2"),sQuery(id+"F0.wireOp",EDGE,"E6.15.3"),sQuery(id+"F0.wireOp",EDGE,"E6.15.4"),sQuery(id+"F0.wireOp",EDGE,"E6.16.1"),sQuery(id+"F0.wireOp",EDGE,"E6.16.2"),sQuery(id+"F0.wireOp",EDGE,"E6.16.3"),sQuery(id+"F0.wireOp",EDGE,"E6.16.4"),sQuery(id+"F0.wireOp",EDGE,"E6.17.1"),sQuery(id+"F0.wireOp",EDGE,"E6.17.2"),sQuery(id+"F0.wireOp",EDGE,"E6.17.3"),sQuery(id+"F0.wireOp",EDGE,"E6.17.4"),sQuery(id+"F0.wireOp",EDGE,"E6.18.1"),sQuery(id+"F0.wireOp",EDGE,"E6.18.2"),sQuery(id+"F0.wireOp",EDGE,"E6.18.3"),sQuery(id+"F0.wireOp",EDGE,"E6.18.4"),sQuery(id+"F0.wireOp",EDGE,"E6.19.1"),sQuery(id+"F0.wireOp",EDGE,"E6.19.2"),sQuery(id+"F0.wireOp",EDGE,"E6.19.3"),sQuery(id+"F0.wireOp",EDGE,"E6.19.4"),sQuery(id+"F0.wireOp",EDGE,"E6.20.1"),sQuery(id+"F0.wireOp",EDGE,"E6.20.2"),sQuery(id+"F0.wireOp",EDGE,"E6.20.3"),sQuery(id+"F0.wireOp",EDGE,"E6.20.4"),sQuery(id+"F0.wireOp",EDGE,"E6.21.1"),sQuery(id+"F0.wireOp",EDGE,"E6.21.2"),sQuery(id+"F0.wireOp",EDGE,"E6.21.3"),sQuery(id+"F0.wireOp",EDGE,"E6.21.4"),sQuery(id+"F0.wireOp",EDGE,"E6.22.1"),sQuery(id+"F0.wireOp",EDGE,"E6.22.2"),sQuery(id+"F0.wireOp",EDGE,"E6.22.3"),sQuery(id+"F0.wireOp",EDGE,"E6.22.4"),sQuery(id+"F0.wireOp",EDGE,"E6.23.1"),sQuery(id+"F0.wireOp",EDGE,"E6.23.2"),sQuery(id+"F0.wireOp",EDGE,"E6.23.3"),sQuery(id+"F0.wireOp",EDGE,"E6.23.4"),sQuery(id+"F0.wireOp",EDGE,"E6.24.1"),sQuery(id+"F0.wireOp",EDGE,"E6.24.2"),sQuery(id+"F0.wireOp",EDGE,"E6.24.3"),sQuery(id+"F0.wireOp",EDGE,"E6.24.4"),sQuery(id+"F0.wireOp",EDGE,"E6.25.1"),sQuery(id+"F0.wireOp",EDGE,"E6.25.2"),sQuery(id+"F0.wireOp",EDGE,"E6.25.3"),sQuery(id+"F0.wireOp",EDGE,"E6.25.4"),sQuery(id+"F0.wireOp",EDGE,"E6.26.1"),sQuery(id+"F0.wireOp",EDGE,"E6.26.2"),sQuery(id+"F0.wireOp",EDGE,"E6.26.3"),sQuery(id+"F0.wireOp",EDGE,"E6.26.4"),sQuery(id+"F0.wireOp",EDGE,"E6.27.1"),sQuery(id+"F0.wireOp",EDGE,"E6.27.2"),sQuery(id+"F0.wireOp",EDGE,"E6.27.3"),sQuery(id+"F0.wireOp",EDGE,"E6.27.4"),sQuery(id+"F0.wireOp",EDGE,"E6.28.1"),sQuery(id+"F0.wireOp",EDGE,"E6.28.2"),sQuery(id+"F0.wireOp",EDGE,"E6.28.3"),sQuery(id+"F0.wireOp",EDGE,"E6.28.4"),sQuery(id+"F0.wireOp",EDGE,"E6.29.1"),sQuery(id+"F0.wireOp",EDGE,"E6.29.2"),sQuery(id+"F0.wireOp",EDGE,"E6.29.3"),sQuery(id+"F0.wireOp",EDGE,"E6.29.4"),sQuery(id+"F0.wireOp",EDGE,"E6.30.1"),sQuery(id+"F0.wireOp",EDGE,"E6.30.2"),sQuery(id+"F0.wireOp",EDGE,"E6.30.3"),sQuery(id+"F0.wireOp",EDGE,"E6.30.4"),sQuery(id+"F0.wireOp",EDGE,"E6.31.1"),sQuery(id+"F0.wireOp",EDGE,"E6.31.2"),sQuery(id+"F0.wireOp",EDGE,"E6.31.3"),sQuery(id+"F0.wireOp",EDGE,"E6.31.4"),sQuery(id+"F0.wireOp",EDGE,"E6.32.1"),sQuery(id+"F0.wireOp",EDGE,"E6.32.2"),sQuery(id+"F0.wireOp",EDGE,"E6.32.3"),sQuery(id+"F0.wireOp",EDGE,"E6.32.4"),sQuery(id+"F0.wireOp",EDGE,"E6.33.1"),sQuery(id+"F0.wireOp",EDGE,"E6.33.2"),sQuery(id+"F0.wireOp",EDGE,"E6.33.3"),sQuery(id+"F0.wireOp",EDGE,"E6.33.4"),sQuery(id+"F0.wireOp",EDGE,"E6.34.1"),sQuery(id+"F0.wireOp",EDGE,"E6.34.2"),sQuery(id+"F0.wireOp",EDGE,"E6.34.3"),sQuery(id+"F0.wireOp",EDGE,"E6.34.4"),sQuery(id+"F0.wireOp",EDGE,"E6.35.1"),sQuery(id+"F0.wireOp",EDGE,"E6.35.2"),sQuery(id+"F0.wireOp",EDGE,"E6.35.3"),sQuery(id+"F0.wireOp",EDGE,"E6.35.4"),sQuery(id+"F0.wireOp",EDGE,"E6.36.1"),sQuery(id+"F0.wireOp",EDGE,"E6.36.2"),sQuery(id+"F0.wireOp",EDGE,"E6.36.3"),sQuery(id+"F0.wireOp",EDGE,"E6.36.4"),sQuery(id+"F0.wireOp",EDGE,"E6.37.1"),sQuery(id+"F0.wireOp",EDGE,"E6.37.2"),sQuery(id+"F0.wireOp",EDGE,"E6.37.3"),sQuery(id+"F0.wireOp",EDGE,"E6.37.4"),sQuery(id+"F0.wireOp",EDGE,"E6.38.1"),sQuery(id+"F0.wireOp",EDGE,"E6.38.2"),sQuery(id+"F0.wireOp",EDGE,"E6.38.3"),sQuery(id+"F0.wireOp",EDGE,"E6.38.4"),sQuery(id+"F0.wireOp",EDGE,"E6.39.1"),sQuery(id+"F0.wireOp",EDGE,"E6.39.2"),sQuery(id+"F0.wireOp",EDGE,"E6.39.3"),sQuery(id+"F0.wireOp",EDGE,"E6.39.4"),sQuery(id+"F0.wireOp",EDGE,"E6.40.1"),sQuery(id+"F0.wireOp",EDGE,"E6.40.2"),sQuery(id+"F0.wireOp",EDGE,"E6.40.3"),sQuery(id+"F0.wireOp",EDGE,"E6.40.4"),sQuery(id+"F0.wireOp",EDGE,"E6.41.1"),sQuery(id+"F0.wireOp",EDGE,"E6.41.2"),sQuery(id+"F0.wireOp",EDGE,"E6.41.3"),sQuery(id+"F0.wireOp",EDGE,"E6.41.4"),sQuery(id+"F0.wireOp",EDGE,"E6.42.1"),sQuery(id+"F0.wireOp",EDGE,"E6.42.2"),sQuery(id+"F0.wireOp",EDGE,"E6.42.3"),sQuery(id+"F0.wireOp",EDGE,"E6.42.4"),subQ1,sQuery(id+"F0.wireOp",EDGE,"E6.43.2"),subQ0,sQuery(id+"F0.wireOp",EDGE,"E6.43.4"),sQuery(id+"F0.wireOp",EDGE,"E7"),sQuery(id+"F0.wireOp",EDGE,"E8.1.0"),sQuery(id+"F0.wireOp",EDGE,"E8.2.0"),sQuery(id+"F0.wireOp",EDGE,"E8.3.0"),sQuery(id+"F0.wireOp",EDGE,"E8.4.0"),sQuery(id+"F0.wireOp",EDGE,"E8.5.0"),sQuery(id+"F0.wireOp",EDGE,"E8.6.0"),sQuery(id+"F0.wireOp",EDGE,"E8.7.0"),sQuery(id+"F0.wireOp",EDGE,"E8.8.0"),sQuery(id+"F0.wireOp",EDGE,"E8.9.0"),sQuery(id+"F0.wireOp",EDGE,"E8.10.0"),sQuery(id+"F0.wireOp",EDGE,"E8.11.0"),sQuery(id+"F0.wireOp",EDGE,"E8.12.0"),sQuery(id+"F0.wireOp",EDGE,"E8.13.0"),sQuery(id+"F0.wireOp",EDGE,"E8.14.0"),sQuery(id+"F0.wireOp",EDGE,"E8.15.0"),sQuery(id+"F0.wireOp",EDGE,"E8.16.0"),sQuery(id+"F0.wireOp",EDGE,"E8.17.0"),sQuery(id+"F0.wireOp",EDGE,"E8.18.0"),sQuery(id+"F0.wireOp",EDGE,"E8.19.0"),sQuery(id+"F0.wireOp",EDGE,"E8.20.0"),sQuery(id+"F0.wireOp",EDGE,"E8.21.0"),sQuery(id+"F0.wireOp",EDGE,"E8.22.0"),sQuery(id+"F0.wireOp",EDGE,"E8.23.0"),sQuery(id+"F0.wireOp",EDGE,"E8.24.0"),sQuery(id+"F0.wireOp",EDGE,"E8.25.0"),sQuery(id+"F0.wireOp",EDGE,"E8.26.0"),sQuery(id+"F0.wireOp",EDGE,"E8.27.0"),sQuery(id+"F0.wireOp",EDGE,"E8.28.0"),sQuery(id+"F0.wireOp",EDGE,"E8.29.0"),sQuery(id+"F0.wireOp",EDGE,"E8.30.0"),sQuery(id+"F0.wireOp",EDGE,"E8.31.0"),sQuery(id+"F0.wireOp",EDGE,"E8.32.0"),sQuery(id+"F0.wireOp",EDGE,"E8.33.0"),sQuery(id+"F0.wireOp",EDGE,"E8.34.0"),sQuery(id+"F0.wireOp",EDGE,"E8.35.0"),sQuery(id+"F0.wireOp",EDGE,"E8.36.0"),sQuery(id+"F0.wireOp",EDGE,"E8.37.0"),sQuery(id+"F0.wireOp",EDGE,"E8.38.0"),sQuery(id+"F0.wireOp",EDGE,"E8.39.0"),sQuery(id+"F0.wireOp",EDGE,"E8.40.0"),sQuery(id+"F0.wireOp",EDGE,"E8.41.0"),sQuery(id+"F0.wireOp",EDGE,"E8.42.0"),sQuery(id+"F0.wireOp",EDGE,"E8.43.0")])],"isStart":false})],"blendedInto":[makeQuery(id+"F1.opExtrude","CAP_FACE",FACE,{"disambiguationData":[OSD([sQuery(id+"F0.wireOp",EDGE,"E0"),sQuery(id+"F0.wireOp",EDGE,"E1"),sQuery(id+"F0.wireOp",EDGE,"E2"),sQuery(id+"F0.wireOp",EDGE,"E4"),sQuery(id+"F0.wireOp",EDGE,"E5"),sQuery(id+"F0.wireOp",EDGE,"E6.1.1"),sQuery(id+"F0.wireOp",EDGE,"E6.1.2"),sQuery(id+"F0.wireOp",EDGE,"E6.1.3"),sQuery(id+"F0.wireOp",EDGE,"E6.1.4"),sQuery(id+"F0.wireOp",EDGE,"E6.2.1"),sQuery(id+"F0.wireOp",EDGE,"E6.2.2"),sQuery(id+"F0.wireOp",EDGE,"E6.2.3"),sQuery(id+"F0.wireOp",EDGE,"E6.2.4"),sQuery(id+"F0.wireOp",EDGE,"E6.3.1"),sQuery(id+"F0.wireOp",EDGE,"E6.3.2"),sQuery(id+"F0.wireOp",EDGE,"E6.3.3"),sQuery(id+"F0.wireOp",EDGE,"E6.3.4"),sQuery(id+"F0.wireOp",EDGE,"E6.4.1"),sQuery(id+"F0.wireOp",EDGE,"E6.4.2"),sQuery(id+"F0.wireOp",EDGE,"E6.4.3"),sQuery(id+"F0.wireOp",EDGE,"E6.4.4"),sQuery(id+"F0.wireOp",EDGE,"E6.5.1"),sQuery(id+"F0.wireOp",EDGE,"E6.5.2"),sQuery(id+"F0.wireOp",EDGE,"E6.5.3"),sQuery(id+"F0.wireOp",EDGE,"E6.5.4"),sQuery(id+"F0.wireOp",EDGE,"E6.6.1"),sQuery(id+"F0.wireOp",EDGE,"E6.6.2"),sQuery(id+"F0.wireOp",EDGE,"E6.6.3"),sQuery(id+"F0.wireOp",EDGE,"E6.6.4"),sQuery(id+"F0.wireOp",EDGE,"E6.7.1"),sQuery(id+"F0.wireOp",EDGE,"E6.7.2"),sQuery(id+"F0.wireOp",EDGE,"E6.7.3"),sQuery(id+"F0.wireOp",EDGE,"E6.7.4"),sQuery(id+"F0.wireOp",EDGE,"E6.8.1"),sQuery(id+"F0.wireOp",EDGE,"E6.8.2"),sQuery(id+"F0.wireOp",EDGE,"E6.8.3"),sQuery(id+"F0.wireOp",EDGE,"E6.8.4"),sQuery(id+"F0.wireOp",EDGE,"E6.9.1"),sQuery(id+"F0.wireOp",EDGE,"E6.9.2"),sQuery(id+"F0.wireOp",EDGE,"E6.9.3"),sQuery(id+"F0.wireOp",EDGE,"E6.9.4"),sQuery(id+"F0.wireOp",EDGE,"E6.10.1"),sQuery(id+"F0.wireOp",EDGE,"E6.10.2"),sQuery(id+"F0.wireOp",EDGE,"E6.10.3"),sQuery(id+"F0.wireOp",EDGE,"E6.10.4"),sQuery(id+"F0.wireOp",EDGE,"E6.11.1"),sQuery(id+"F0.wireOp",EDGE,"E6.11.2"),sQuery(id+"F0.wireOp",EDGE,"E6.11.3"),sQuery(id+"F0.wireOp",EDGE,"E6.11.4"),sQuery(id+"F0.wireOp",EDGE,"E6.12.1"),sQuery(id+"F0.wireOp",EDGE,"E6.12.2"),sQuery(id+"F0.wireOp",EDGE,"E6.12.3"),sQuery(id+"F0.wireOp",EDGE,"E6.12.4"),sQuery(id+"F0.wireOp",EDGE,"E6.13.1"),sQuery(id+"F0.wireOp",EDGE,"E6.13.2"),sQuery(id+"F0.wireOp",EDGE,"E6.13.3"),sQuery(id+"F0.wireOp",EDGE,"E6.13.4"),sQuery(id+"F0.wireOp",EDGE,"E6.14.1"),sQuery(id+"F0.wireOp",EDGE,"E6.14.2"),sQuery(id+"F0.wireOp",EDGE,"E6.14.3"),sQuery(id+"F0.wireOp",EDGE,"E6.14.4"),sQuery(id+"F0.wireOp",EDGE,"E6.15.1"),sQuery(id+"F0.wireOp",EDGE,"E6.15.2"),sQuery(id+"F0.wireOp",EDGE,"E6.15.3"),sQuery(id+"F0.wireOp",EDGE,"E6.15.4"),sQuery(id+"F0.wireOp",EDGE,"E6.16.1"),sQuery(id+"F0.wireOp",EDGE,"E6.16.2"),sQuery(id+"F0.wireOp",EDGE,"E6.16.3"),sQuery(id+"F0.wireOp",EDGE,"E6.16.4"),sQuery(id+"F0.wireOp",EDGE,"E6.17.1"),sQuery(id+"F0.wireOp",EDGE,"E6.17.2"),sQuery(id+"F0.wireOp",EDGE,"E6.17.3"),sQuery(id+"F0.wireOp",EDGE,"E6.17.4"),sQuery(id+"F0.wireOp",EDGE,"E6.18.1"),sQuery(id+"F0.wireOp",EDGE,"E6.18.2"),sQuery(id+"F0.wireOp",EDGE,"E6.18.3"),sQuery(id+"F0.wireOp",EDGE,"E6.18.4"),sQuery(id+"F0.wireOp",EDGE,"E6.19.1"),sQuery(id+"F0.wireOp",EDGE,"E6.19.2"),sQuery(id+"F0.wireOp",EDGE,"E6.19.3"),sQuery(id+"F0.wireOp",EDGE,"E6.19.4"),sQuery(id+"F0.wireOp",EDGE,"E6.20.1"),sQuery(id+"F0.wireOp",EDGE,"E6.20.2"),sQuery(id+"F0.wireOp",EDGE,"E6.20.3"),sQuery(id+"F0.wireOp",EDGE,"E6.20.4"),sQuery(id+"F0.wireOp",EDGE,"E6.21.1"),sQuery(id+"F0.wireOp",EDGE,"E6.21.2"),sQuery(id+"F0.wireOp",EDGE,"E6.21.3"),sQuery(id+"F0.wireOp",EDGE,"E6.21.4"),sQuery(id+"F0.wireOp",EDGE,"E6.22.1"),sQuery(id+"F0.wireOp",EDGE,"E6.22.2"),sQuery(id+"F0.wireOp",EDGE,"E6.22.3"),sQuery(id+"F0.wireOp",EDGE,"E6.22.4"),sQuery(id+"F0.wireOp",EDGE,"E6.23.1"),sQuery(id+"F0.wireOp",EDGE,"E6.23.2"),sQuery(id+"F0.wireOp",EDGE,"E6.23.3"),sQuery(id+"F0.wireOp",EDGE,"E6.23.4"),sQuery(id+"F0.wireOp",EDGE,"E6.24.1"),sQuery(id+"F0.wireOp",EDGE,"E6.24.2"),sQuery(id+"F0.wireOp",EDGE,"E6.24.3"),sQuery(id+"F0.wireOp",EDGE,"E6.24.4"),sQuery(id+"F0.wireOp",EDGE,"E6.25.1"),sQuery(id+"F0.wireOp",EDGE,"E6.25.2"),sQuery(id+"F0.wireOp",EDGE,"E6.25.3"),sQuery(id+"F0.wireOp",EDGE,"E6.25.4"),sQuery(id+"F0.wireOp",EDGE,"E6.26.1"),sQuery(id+"F0.wireOp",EDGE,"E6.26.2"),sQuery(id+"F0.wireOp",EDGE,"E6.26.3"),sQuery(id+"F0.wireOp",EDGE,"E6.26.4"),sQuery(id+"F0.wireOp",EDGE,"E6.27.1"),sQuery(id+"F0.wireOp",EDGE,"E6.27.2"),sQuery(id+"F0.wireOp",EDGE,"E6.27.3"),sQuery(id+"F0.wireOp",EDGE,"E6.27.4"),sQuery(id+"F0.wireOp",EDGE,"E6.28.1"),sQuery(id+"F0.wireOp",EDGE,"E6.28.2"),sQuery(id+"F0.wireOp",EDGE,"E6.28.3"),sQuery(id+"F0.wireOp",EDGE,"E6.28.4"),sQuery(id+"F0.wireOp",EDGE,"E6.29.1"),sQuery(id+"F0.wireOp",EDGE,"E6.29.2"),sQuery(id+"F0.wireOp",EDGE,"E6.29.3"),sQuery(id+"F0.wireOp",EDGE,"E6.29.4"),sQuery(id+"F0.wireOp",EDGE,"E6.30.1"),sQuery(id+"F0.wireOp",EDGE,"E6.30.2"),sQuery(id+"F0.wireOp",EDGE,"E6.30.3"),sQuery(id+"F0.wireOp",EDGE,"E6.30.4"),sQuery(id+"F0.wireOp",EDGE,"E6.31.1"),sQuery(id+"F0.wireOp",EDGE,"E6.31.2"),sQuery(id+"F0.wireOp",EDGE,"E6.31.3"),sQuery(id+"F0.wireOp",EDGE,"E6.31.4"),sQuery(id+"F0.wireOp",EDGE,"E6.32.1"),sQuery(id+"F0.wireOp",EDGE,"E6.32.2"),sQuery(id+"F0.wireOp",EDGE,"E6.32.3"),sQuery(id+"F0.wireOp",EDGE,"E6.32.4"),sQuery(id+"F0.wireOp",EDGE,"E6.33.1"),sQuery(id+"F0.wireOp",EDGE,"E6.33.2"),sQuery(id+"F0.wireOp",EDGE,"E6.33.3"),sQuery(id+"F0.wireOp",EDGE,"E6.33.4"),sQuery(id+"F0.wireOp",EDGE,"E6.34.1"),sQuery(id+"F0.wireOp",EDGE,"E6.34.2"),sQuery(id+"F0.wireOp",EDGE,"E6.34.3"),sQuery(id+"F0.wireOp",EDGE,"E6.34.4"),sQuery(id+"F0.wireOp",EDGE,"E6.35.1"),sQuery(id+"F0.wireOp",EDGE,"E6.35.2"),sQuery(id+"F0.wireOp",EDGE,"E6.35.3"),sQuery(id+"F0.wireOp",EDGE,"E6.35.4"),sQuery(id+"F0.wireOp",EDGE,"E6.36.1"),sQuery(id+"F0.wireOp",EDGE,"E6.36.2"),sQuery(id+"F0.wireOp",EDGE,"E6.36.3"),sQuery(id+"F0.wireOp",EDGE,"E6.36.4"),sQuery(id+"F0.wireOp",EDGE,"E6.37.1"),sQuery(id+"F0.wireOp",EDGE,"E6.37.2"),sQuery(id+"F0.wireOp",EDGE,"E6.37.3"),sQuery(id+"F0.wireOp",EDGE,"E6.37.4"),sQuery(id+"F0.wireOp",EDGE,"E6.38.1"),sQuery(id+"F0.wireOp",EDGE,"E6.38.2"),sQuery(id+"F0.wireOp",EDGE,"E6.38.3"),sQuery(id+"F0.wireOp",EDGE,"E6.38.4"),sQuery(id+"F0.wireOp",EDGE,"E6.39.1"),sQuery(id+"F0.wireOp",EDGE,"E6.39.2"),sQuery(id+"F0.wireOp",EDGE,"E6.39.3"),sQuery(id+"F0.wireOp",EDGE,"E6.39.4"),sQuery(id+"F0.wireOp",EDGE,"E6.40.1"),sQuery(id+"F0.wireOp",EDGE,"E6.40.2"),sQuery(id+"F0.wireOp",EDGE,"E6.40.3"),sQuery(id+"F0.wireOp",EDGE,"E6.40.4"),sQuery(id+"F0.wireOp",EDGE,"E6.41.1"),sQuery(id+"F0.wireOp",EDGE,"E6.41.2"),sQuery(id+"F0.wireOp",EDGE,"E6.41.3"),sQuery(id+"F0.wireOp",EDGE,"E6.41.4"),sQuery(id+"F0.wireOp",EDGE,"E6.42.1"),sQuery(id+"F0.wireOp",EDGE,"E6.42.2"),sQuery(id+"F0.wireOp",EDGE,"E6.42.3"),sQuery(id+"F0.wireOp",EDGE,"E6.42.4"),subQ1,sQuery(id+"F0.wireOp",EDGE,"E6.43.2"),subQ0,sQuery(id+"F0.wireOp",EDGE,"E6.43.4"),sQuery(id+"F0.wireOp",EDGE,"E7"),sQuery(id+"F0.wireOp",EDGE,"E8.1.0"),sQuery(id+"F0.wireOp",EDGE,"E8.2.0"),sQuery(id+"F0.wireOp",EDGE,"E8.3.0"),sQuery(id+"F0.wireOp",EDGE,"E8.4.0"),sQuery(id+"F0.wireOp",EDGE,"E8.5.0"),sQuery(id+"F0.wireOp",EDGE,"E8.6.0"),sQuery(id+"F0.wireOp",EDGE,"E8.7.0"),sQuery(id+"F0.wireOp",EDGE,"E8.8.0"),sQuery(id+"F0.wireOp",EDGE,"E8.9.0"),sQuery(id+"F0.wireOp",EDGE,"E8.10.0"),sQuery(id+"F0.wireOp",EDGE,"E8.11.0"),sQuery(id+"F0.wireOp",EDGE,"E8.12.0"),sQuery(id+"F0.wireOp",EDGE,"E8.13.0"),sQuery(id+"F0.wireOp",EDGE,"E8.14.0"),sQuery(id+"F0.wireOp",EDGE,"E8.15.0"),sQuery(id+"F0.wireOp",EDGE,"E8.16.0"),sQuery(id+"F0.wireOp",EDGE,"E8.17.0"),sQuery(id+"F0.wireOp",EDGE,"E8.18.0"),sQuery(id+"F0.wireOp",EDGE,"E8.19.0"),sQuery(id+"F0.wireOp",EDGE,"E8.20.0"),sQuery(id+"F0.wireOp",EDGE,"E8.21.0"),sQuery(id+"F0.wireOp",EDGE,"E8.22.0"),sQuery(id+"F0.wireOp",EDGE,"E8.23.0"),sQuery(id+"F0.wireOp",EDGE,"E8.24.0"),sQuery(id+"F0.wireOp",EDGE,"E8.25.0"),sQuery(id+"F0.wireOp",EDGE,"E8.26.0"),sQuery(id+"F0.wireOp",EDGE,"E8.27.0"),sQuery(id+"F0.wireOp",EDGE,"E8.28.0"),sQuery(id+"F0.wireOp",EDGE,"E8.29.0"),sQuery(id+"F0.wireOp",EDGE,"E8.30.0"),sQuery(id+"F0.wireOp",EDGE,"E8.31.0"),sQuery(id+"F0.wireOp",EDGE,"E8.32.0"),sQuery(id+"F0.wireOp",EDGE,"E8.33.0"),sQuery(id+"F0.wireOp",EDGE,"E8.34.0"),sQuery(id+"F0.wireOp",EDGE,"E8.35.0"),sQuery(id+"F0.wireOp",EDGE,"E8.36.0"),sQuery(id+"F0.wireOp",EDGE,"E8.37.0"),sQuery(id+"F0.wireOp",EDGE,"E8.38.0"),sQuery(id+"F0.wireOp",EDGE,"E8.39.0"),sQuery(id+"F0.wireOp",EDGE,"E8.40.0"),sQuery(id+"F0.wireOp",EDGE,"E8.41.0"),sQuery(id+"F0.wireOp",EDGE,"E8.42.0"),sQuery(id+"F0.wireOp",EDGE,"E8.43.0")])],"isStart":false})]});}
            var Q11;
            {var subQ0=sQuery(id+"F0.wireOp",EDGE,"E6.1.3");var subQ1=sQuery(id+"F0.wireOp",EDGE,"E6.1.1");Q11=makeQuery(id+"F2.opFillet","BLEND_EDGE",EDGE,{"blendedFrom":[makeQuery(id+"F1.opExtrude","SWEPT_EDGE",EDGE,{"disambiguationData":[OSD([sQuery(id+"F0.wireOp",EDGE,"E6.1.0"),subQ1,subQ0])]}),makeQuery(id+"F1.opExtrude","CAP_FACE",FACE,{"disambiguationData":[OSD([sQuery(id+"F0.wireOp",EDGE,"E0"),sQuery(id+"F0.wireOp",EDGE,"E1"),sQuery(id+"F0.wireOp",EDGE,"E2"),sQuery(id+"F0.wireOp",EDGE,"E4"),sQuery(id+"F0.wireOp",EDGE,"E5"),subQ1,sQuery(id+"F0.wireOp",EDGE,"E6.1.2"),subQ0,sQuery(id+"F0.wireOp",EDGE,"E6.1.4"),sQuery(id+"F0.wireOp",EDGE,"E6.2.1"),sQuery(id+"F0.wireOp",EDGE,"E6.2.2"),sQuery(id+"F0.wireOp",EDGE,"E6.2.3"),sQuery(id+"F0.wireOp",EDGE,"E6.2.4"),sQuery(id+"F0.wireOp",EDGE,"E6.3.1"),sQuery(id+"F0.wireOp",EDGE,"E6.3.2"),sQuery(id+"F0.wireOp",EDGE,"E6.3.3"),sQuery(id+"F0.wireOp",EDGE,"E6.3.4"),sQuery(id+"F0.wireOp",EDGE,"E6.4.1"),sQuery(id+"F0.wireOp",EDGE,"E6.4.2"),sQuery(id+"F0.wireOp",EDGE,"E6.4.3"),sQuery(id+"F0.wireOp",EDGE,"E6.4.4"),sQuery(id+"F0.wireOp",EDGE,"E6.5.1"),sQuery(id+"F0.wireOp",EDGE,"E6.5.2"),sQuery(id+"F0.wireOp",EDGE,"E6.5.3"),sQuery(id+"F0.wireOp",EDGE,"E6.5.4"),sQuery(id+"F0.wireOp",EDGE,"E6.6.1"),sQuery(id+"F0.wireOp",EDGE,"E6.6.2"),sQuery(id+"F0.wireOp",EDGE,"E6.6.3"),sQuery(id+"F0.wireOp",EDGE,"E6.6.4"),sQuery(id+"F0.wireOp",EDGE,"E6.7.1"),sQuery(id+"F0.wireOp",EDGE,"E6.7.2"),sQuery(id+"F0.wireOp",EDGE,"E6.7.3"),sQuery(id+"F0.wireOp",EDGE,"E6.7.4"),sQuery(id+"F0.wireOp",EDGE,"E6.8.1"),sQuery(id+"F0.wireOp",EDGE,"E6.8.2"),sQuery(id+"F0.wireOp",EDGE,"E6.8.3"),sQuery(id+"F0.wireOp",EDGE,"E6.8.4"),sQuery(id+"F0.wireOp",EDGE,"E6.9.1"),sQuery(id+"F0.wireOp",EDGE,"E6.9.2"),sQuery(id+"F0.wireOp",EDGE,"E6.9.3"),sQuery(id+"F0.wireOp",EDGE,"E6.9.4"),sQuery(id+"F0.wireOp",EDGE,"E6.10.1"),sQuery(id+"F0.wireOp",EDGE,"E6.10.2"),sQuery(id+"F0.wireOp",EDGE,"E6.10.3"),sQuery(id+"F0.wireOp",EDGE,"E6.10.4"),sQuery(id+"F0.wireOp",EDGE,"E6.11.1"),sQuery(id+"F0.wireOp",EDGE,"E6.11.2"),sQuery(id+"F0.wireOp",EDGE,"E6.11.3"),sQuery(id+"F0.wireOp",EDGE,"E6.11.4"),sQuery(id+"F0.wireOp",EDGE,"E6.12.1"),sQuery(id+"F0.wireOp",EDGE,"E6.12.2"),sQuery(id+"F0.wireOp",EDGE,"E6.12.3"),sQuery(id+"F0.wireOp",EDGE,"E6.12.4"),sQuery(id+"F0.wireOp",EDGE,"E6.13.1"),sQuery(id+"F0.wireOp",EDGE,"E6.13.2"),sQuery(id+"F0.wireOp",EDGE,"E6.13.3"),sQuery(id+"F0.wireOp",EDGE,"E6.13.4"),sQuery(id+"F0.wireOp",EDGE,"E6.14.1"),sQuery(id+"F0.wireOp",EDGE,"E6.14.2"),sQuery(id+"F0.wireOp",EDGE,"E6.14.3"),sQuery(id+"F0.wireOp",EDGE,"E6.14.4"),sQuery(id+"F0.wireOp",EDGE,"E6.15.1"),sQuery(id+"F0.wireOp",EDGE,"E6.15.2"),sQuery(id+"F0.wireOp",EDGE,"E6.15.3"),sQuery(id+"F0.wireOp",EDGE,"E6.15.4"),sQuery(id+"F0.wireOp",EDGE,"E6.16.1"),sQuery(id+"F0.wireOp",EDGE,"E6.16.2"),sQuery(id+"F0.wireOp",EDGE,"E6.16.3"),sQuery(id+"F0.wireOp",EDGE,"E6.16.4"),sQuery(id+"F0.wireOp",EDGE,"E6.17.1"),sQuery(id+"F0.wireOp",EDGE,"E6.17.2"),sQuery(id+"F0.wireOp",EDGE,"E6.17.3"),sQuery(id+"F0.wireOp",EDGE,"E6.17.4"),sQuery(id+"F0.wireOp",EDGE,"E6.18.1"),sQuery(id+"F0.wireOp",EDGE,"E6.18.2"),sQuery(id+"F0.wireOp",EDGE,"E6.18.3"),sQuery(id+"F0.wireOp",EDGE,"E6.18.4"),sQuery(id+"F0.wireOp",EDGE,"E6.19.1"),sQuery(id+"F0.wireOp",EDGE,"E6.19.2"),sQuery(id+"F0.wireOp",EDGE,"E6.19.3"),sQuery(id+"F0.wireOp",EDGE,"E6.19.4"),sQuery(id+"F0.wireOp",EDGE,"E6.20.1"),sQuery(id+"F0.wireOp",EDGE,"E6.20.2"),sQuery(id+"F0.wireOp",EDGE,"E6.20.3"),sQuery(id+"F0.wireOp",EDGE,"E6.20.4"),sQuery(id+"F0.wireOp",EDGE,"E6.21.1"),sQuery(id+"F0.wireOp",EDGE,"E6.21.2"),sQuery(id+"F0.wireOp",EDGE,"E6.21.3"),sQuery(id+"F0.wireOp",EDGE,"E6.21.4"),sQuery(id+"F0.wireOp",EDGE,"E6.22.1"),sQuery(id+"F0.wireOp",EDGE,"E6.22.2"),sQuery(id+"F0.wireOp",EDGE,"E6.22.3"),sQuery(id+"F0.wireOp",EDGE,"E6.22.4"),sQuery(id+"F0.wireOp",EDGE,"E6.23.1"),sQuery(id+"F0.wireOp",EDGE,"E6.23.2"),sQuery(id+"F0.wireOp",EDGE,"E6.23.3"),sQuery(id+"F0.wireOp",EDGE,"E6.23.4"),sQuery(id+"F0.wireOp",EDGE,"E6.24.1"),sQuery(id+"F0.wireOp",EDGE,"E6.24.2"),sQuery(id+"F0.wireOp",EDGE,"E6.24.3"),sQuery(id+"F0.wireOp",EDGE,"E6.24.4"),sQuery(id+"F0.wireOp",EDGE,"E6.25.1"),sQuery(id+"F0.wireOp",EDGE,"E6.25.2"),sQuery(id+"F0.wireOp",EDGE,"E6.25.3"),sQuery(id+"F0.wireOp",EDGE,"E6.25.4"),sQuery(id+"F0.wireOp",EDGE,"E6.26.1"),sQuery(id+"F0.wireOp",EDGE,"E6.26.2"),sQuery(id+"F0.wireOp",EDGE,"E6.26.3"),sQuery(id+"F0.wireOp",EDGE,"E6.26.4"),sQuery(id+"F0.wireOp",EDGE,"E6.27.1"),sQuery(id+"F0.wireOp",EDGE,"E6.27.2"),sQuery(id+"F0.wireOp",EDGE,"E6.27.3"),sQuery(id+"F0.wireOp",EDGE,"E6.27.4"),sQuery(id+"F0.wireOp",EDGE,"E6.28.1"),sQuery(id+"F0.wireOp",EDGE,"E6.28.2"),sQuery(id+"F0.wireOp",EDGE,"E6.28.3"),sQuery(id+"F0.wireOp",EDGE,"E6.28.4"),sQuery(id+"F0.wireOp",EDGE,"E6.29.1"),sQuery(id+"F0.wireOp",EDGE,"E6.29.2"),sQuery(id+"F0.wireOp",EDGE,"E6.29.3"),sQuery(id+"F0.wireOp",EDGE,"E6.29.4"),sQuery(id+"F0.wireOp",EDGE,"E6.30.1"),sQuery(id+"F0.wireOp",EDGE,"E6.30.2"),sQuery(id+"F0.wireOp",EDGE,"E6.30.3"),sQuery(id+"F0.wireOp",EDGE,"E6.30.4"),sQuery(id+"F0.wireOp",EDGE,"E6.31.1"),sQuery(id+"F0.wireOp",EDGE,"E6.31.2"),sQuery(id+"F0.wireOp",EDGE,"E6.31.3"),sQuery(id+"F0.wireOp",EDGE,"E6.31.4"),sQuery(id+"F0.wireOp",EDGE,"E6.32.1"),sQuery(id+"F0.wireOp",EDGE,"E6.32.2"),sQuery(id+"F0.wireOp",EDGE,"E6.32.3"),sQuery(id+"F0.wireOp",EDGE,"E6.32.4"),sQuery(id+"F0.wireOp",EDGE,"E6.33.1"),sQuery(id+"F0.wireOp",EDGE,"E6.33.2"),sQuery(id+"F0.wireOp",EDGE,"E6.33.3"),sQuery(id+"F0.wireOp",EDGE,"E6.33.4"),sQuery(id+"F0.wireOp",EDGE,"E6.34.1"),sQuery(id+"F0.wireOp",EDGE,"E6.34.2"),sQuery(id+"F0.wireOp",EDGE,"E6.34.3"),sQuery(id+"F0.wireOp",EDGE,"E6.34.4"),sQuery(id+"F0.wireOp",EDGE,"E6.35.1"),sQuery(id+"F0.wireOp",EDGE,"E6.35.2"),sQuery(id+"F0.wireOp",EDGE,"E6.35.3"),sQuery(id+"F0.wireOp",EDGE,"E6.35.4"),sQuery(id+"F0.wireOp",EDGE,"E6.36.1"),sQuery(id+"F0.wireOp",EDGE,"E6.36.2"),sQuery(id+"F0.wireOp",EDGE,"E6.36.3"),sQuery(id+"F0.wireOp",EDGE,"E6.36.4"),sQuery(id+"F0.wireOp",EDGE,"E6.37.1"),sQuery(id+"F0.wireOp",EDGE,"E6.37.2"),sQuery(id+"F0.wireOp",EDGE,"E6.37.3"),sQuery(id+"F0.wireOp",EDGE,"E6.37.4"),sQuery(id+"F0.wireOp",EDGE,"E6.38.1"),sQuery(id+"F0.wireOp",EDGE,"E6.38.2"),sQuery(id+"F0.wireOp",EDGE,"E6.38.3"),sQuery(id+"F0.wireOp",EDGE,"E6.38.4"),sQuery(id+"F0.wireOp",EDGE,"E6.39.1"),sQuery(id+"F0.wireOp",EDGE,"E6.39.2"),sQuery(id+"F0.wireOp",EDGE,"E6.39.3"),sQuery(id+"F0.wireOp",EDGE,"E6.39.4"),sQuery(id+"F0.wireOp",EDGE,"E6.40.1"),sQuery(id+"F0.wireOp",EDGE,"E6.40.2"),sQuery(id+"F0.wireOp",EDGE,"E6.40.3"),sQuery(id+"F0.wireOp",EDGE,"E6.40.4"),sQuery(id+"F0.wireOp",EDGE,"E6.41.1"),sQuery(id+"F0.wireOp",EDGE,"E6.41.2"),sQuery(id+"F0.wireOp",EDGE,"E6.41.3"),sQuery(id+"F0.wireOp",EDGE,"E6.41.4"),sQuery(id+"F0.wireOp",EDGE,"E6.42.1"),sQuery(id+"F0.wireOp",EDGE,"E6.42.2"),sQuery(id+"F0.wireOp",EDGE,"E6.42.3"),sQuery(id+"F0.wireOp",EDGE,"E6.42.4"),sQuery(id+"F0.wireOp",EDGE,"E6.43.1"),sQuery(id+"F0.wireOp",EDGE,"E6.43.2"),sQuery(id+"F0.wireOp",EDGE,"E6.43.3"),sQuery(id+"F0.wireOp",EDGE,"E6.43.4"),sQuery(id+"F0.wireOp",EDGE,"E7"),sQuery(id+"F0.wireOp",EDGE,"E8.1.0"),sQuery(id+"F0.wireOp",EDGE,"E8.2.0"),sQuery(id+"F0.wireOp",EDGE,"E8.3.0"),sQuery(id+"F0.wireOp",EDGE,"E8.4.0"),sQuery(id+"F0.wireOp",EDGE,"E8.5.0"),sQuery(id+"F0.wireOp",EDGE,"E8.6.0"),sQuery(id+"F0.wireOp",EDGE,"E8.7.0"),sQuery(id+"F0.wireOp",EDGE,"E8.8.0"),sQuery(id+"F0.wireOp",EDGE,"E8.9.0"),sQuery(id+"F0.wireOp",EDGE,"E8.10.0"),sQuery(id+"F0.wireOp",EDGE,"E8.11.0"),sQuery(id+"F0.wireOp",EDGE,"E8.12.0"),sQuery(id+"F0.wireOp",EDGE,"E8.13.0"),sQuery(id+"F0.wireOp",EDGE,"E8.14.0"),sQuery(id+"F0.wireOp",EDGE,"E8.15.0"),sQuery(id+"F0.wireOp",EDGE,"E8.16.0"),sQuery(id+"F0.wireOp",EDGE,"E8.17.0"),sQuery(id+"F0.wireOp",EDGE,"E8.18.0"),sQuery(id+"F0.wireOp",EDGE,"E8.19.0"),sQuery(id+"F0.wireOp",EDGE,"E8.20.0"),sQuery(id+"F0.wireOp",EDGE,"E8.21.0"),sQuery(id+"F0.wireOp",EDGE,"E8.22.0"),sQuery(id+"F0.wireOp",EDGE,"E8.23.0"),sQuery(id+"F0.wireOp",EDGE,"E8.24.0"),sQuery(id+"F0.wireOp",EDGE,"E8.25.0"),sQuery(id+"F0.wireOp",EDGE,"E8.26.0"),sQuery(id+"F0.wireOp",EDGE,"E8.27.0"),sQuery(id+"F0.wireOp",EDGE,"E8.28.0"),sQuery(id+"F0.wireOp",EDGE,"E8.29.0"),sQuery(id+"F0.wireOp",EDGE,"E8.30.0"),sQuery(id+"F0.wireOp",EDGE,"E8.31.0"),sQuery(id+"F0.wireOp",EDGE,"E8.32.0"),sQuery(id+"F0.wireOp",EDGE,"E8.33.0"),sQuery(id+"F0.wireOp",EDGE,"E8.34.0"),sQuery(id+"F0.wireOp",EDGE,"E8.35.0"),sQuery(id+"F0.wireOp",EDGE,"E8.36.0"),sQuery(id+"F0.wireOp",EDGE,"E8.37.0"),sQuery(id+"F0.wireOp",EDGE,"E8.38.0"),sQuery(id+"F0.wireOp",EDGE,"E8.39.0"),sQuery(id+"F0.wireOp",EDGE,"E8.40.0"),sQuery(id+"F0.wireOp",EDGE,"E8.41.0"),sQuery(id+"F0.wireOp",EDGE,"E8.42.0"),sQuery(id+"F0.wireOp",EDGE,"E8.43.0")])],"isStart":false})],"blendedInto":[makeQuery(id+"F1.opExtrude","CAP_FACE",FACE,{"disambiguationData":[OSD([sQuery(id+"F0.wireOp",EDGE,"E0"),sQuery(id+"F0.wireOp",EDGE,"E1"),sQuery(id+"F0.wireOp",EDGE,"E2"),sQuery(id+"F0.wireOp",EDGE,"E4"),sQuery(id+"F0.wireOp",EDGE,"E5"),subQ1,sQuery(id+"F0.wireOp",EDGE,"E6.1.2"),subQ0,sQuery(id+"F0.wireOp",EDGE,"E6.1.4"),sQuery(id+"F0.wireOp",EDGE,"E6.2.1"),sQuery(id+"F0.wireOp",EDGE,"E6.2.2"),sQuery(id+"F0.wireOp",EDGE,"E6.2.3"),sQuery(id+"F0.wireOp",EDGE,"E6.2.4"),sQuery(id+"F0.wireOp",EDGE,"E6.3.1"),sQuery(id+"F0.wireOp",EDGE,"E6.3.2"),sQuery(id+"F0.wireOp",EDGE,"E6.3.3"),sQuery(id+"F0.wireOp",EDGE,"E6.3.4"),sQuery(id+"F0.wireOp",EDGE,"E6.4.1"),sQuery(id+"F0.wireOp",EDGE,"E6.4.2"),sQuery(id+"F0.wireOp",EDGE,"E6.4.3"),sQuery(id+"F0.wireOp",EDGE,"E6.4.4"),sQuery(id+"F0.wireOp",EDGE,"E6.5.1"),sQuery(id+"F0.wireOp",EDGE,"E6.5.2"),sQuery(id+"F0.wireOp",EDGE,"E6.5.3"),sQuery(id+"F0.wireOp",EDGE,"E6.5.4"),sQuery(id+"F0.wireOp",EDGE,"E6.6.1"),sQuery(id+"F0.wireOp",EDGE,"E6.6.2"),sQuery(id+"F0.wireOp",EDGE,"E6.6.3"),sQuery(id+"F0.wireOp",EDGE,"E6.6.4"),sQuery(id+"F0.wireOp",EDGE,"E6.7.1"),sQuery(id+"F0.wireOp",EDGE,"E6.7.2"),sQuery(id+"F0.wireOp",EDGE,"E6.7.3"),sQuery(id+"F0.wireOp",EDGE,"E6.7.4"),sQuery(id+"F0.wireOp",EDGE,"E6.8.1"),sQuery(id+"F0.wireOp",EDGE,"E6.8.2"),sQuery(id+"F0.wireOp",EDGE,"E6.8.3"),sQuery(id+"F0.wireOp",EDGE,"E6.8.4"),sQuery(id+"F0.wireOp",EDGE,"E6.9.1"),sQuery(id+"F0.wireOp",EDGE,"E6.9.2"),sQuery(id+"F0.wireOp",EDGE,"E6.9.3"),sQuery(id+"F0.wireOp",EDGE,"E6.9.4"),sQuery(id+"F0.wireOp",EDGE,"E6.10.1"),sQuery(id+"F0.wireOp",EDGE,"E6.10.2"),sQuery(id+"F0.wireOp",EDGE,"E6.10.3"),sQuery(id+"F0.wireOp",EDGE,"E6.10.4"),sQuery(id+"F0.wireOp",EDGE,"E6.11.1"),sQuery(id+"F0.wireOp",EDGE,"E6.11.2"),sQuery(id+"F0.wireOp",EDGE,"E6.11.3"),sQuery(id+"F0.wireOp",EDGE,"E6.11.4"),sQuery(id+"F0.wireOp",EDGE,"E6.12.1"),sQuery(id+"F0.wireOp",EDGE,"E6.12.2"),sQuery(id+"F0.wireOp",EDGE,"E6.12.3"),sQuery(id+"F0.wireOp",EDGE,"E6.12.4"),sQuery(id+"F0.wireOp",EDGE,"E6.13.1"),sQuery(id+"F0.wireOp",EDGE,"E6.13.2"),sQuery(id+"F0.wireOp",EDGE,"E6.13.3"),sQuery(id+"F0.wireOp",EDGE,"E6.13.4"),sQuery(id+"F0.wireOp",EDGE,"E6.14.1"),sQuery(id+"F0.wireOp",EDGE,"E6.14.2"),sQuery(id+"F0.wireOp",EDGE,"E6.14.3"),sQuery(id+"F0.wireOp",EDGE,"E6.14.4"),sQuery(id+"F0.wireOp",EDGE,"E6.15.1"),sQuery(id+"F0.wireOp",EDGE,"E6.15.2"),sQuery(id+"F0.wireOp",EDGE,"E6.15.3"),sQuery(id+"F0.wireOp",EDGE,"E6.15.4"),sQuery(id+"F0.wireOp",EDGE,"E6.16.1"),sQuery(id+"F0.wireOp",EDGE,"E6.16.2"),sQuery(id+"F0.wireOp",EDGE,"E6.16.3"),sQuery(id+"F0.wireOp",EDGE,"E6.16.4"),sQuery(id+"F0.wireOp",EDGE,"E6.17.1"),sQuery(id+"F0.wireOp",EDGE,"E6.17.2"),sQuery(id+"F0.wireOp",EDGE,"E6.17.3"),sQuery(id+"F0.wireOp",EDGE,"E6.17.4"),sQuery(id+"F0.wireOp",EDGE,"E6.18.1"),sQuery(id+"F0.wireOp",EDGE,"E6.18.2"),sQuery(id+"F0.wireOp",EDGE,"E6.18.3"),sQuery(id+"F0.wireOp",EDGE,"E6.18.4"),sQuery(id+"F0.wireOp",EDGE,"E6.19.1"),sQuery(id+"F0.wireOp",EDGE,"E6.19.2"),sQuery(id+"F0.wireOp",EDGE,"E6.19.3"),sQuery(id+"F0.wireOp",EDGE,"E6.19.4"),sQuery(id+"F0.wireOp",EDGE,"E6.20.1"),sQuery(id+"F0.wireOp",EDGE,"E6.20.2"),sQuery(id+"F0.wireOp",EDGE,"E6.20.3"),sQuery(id+"F0.wireOp",EDGE,"E6.20.4"),sQuery(id+"F0.wireOp",EDGE,"E6.21.1"),sQuery(id+"F0.wireOp",EDGE,"E6.21.2"),sQuery(id+"F0.wireOp",EDGE,"E6.21.3"),sQuery(id+"F0.wireOp",EDGE,"E6.21.4"),sQuery(id+"F0.wireOp",EDGE,"E6.22.1"),sQuery(id+"F0.wireOp",EDGE,"E6.22.2"),sQuery(id+"F0.wireOp",EDGE,"E6.22.3"),sQuery(id+"F0.wireOp",EDGE,"E6.22.4"),sQuery(id+"F0.wireOp",EDGE,"E6.23.1"),sQuery(id+"F0.wireOp",EDGE,"E6.23.2"),sQuery(id+"F0.wireOp",EDGE,"E6.23.3"),sQuery(id+"F0.wireOp",EDGE,"E6.23.4"),sQuery(id+"F0.wireOp",EDGE,"E6.24.1"),sQuery(id+"F0.wireOp",EDGE,"E6.24.2"),sQuery(id+"F0.wireOp",EDGE,"E6.24.3"),sQuery(id+"F0.wireOp",EDGE,"E6.24.4"),sQuery(id+"F0.wireOp",EDGE,"E6.25.1"),sQuery(id+"F0.wireOp",EDGE,"E6.25.2"),sQuery(id+"F0.wireOp",EDGE,"E6.25.3"),sQuery(id+"F0.wireOp",EDGE,"E6.25.4"),sQuery(id+"F0.wireOp",EDGE,"E6.26.1"),sQuery(id+"F0.wireOp",EDGE,"E6.26.2"),sQuery(id+"F0.wireOp",EDGE,"E6.26.3"),sQuery(id+"F0.wireOp",EDGE,"E6.26.4"),sQuery(id+"F0.wireOp",EDGE,"E6.27.1"),sQuery(id+"F0.wireOp",EDGE,"E6.27.2"),sQuery(id+"F0.wireOp",EDGE,"E6.27.3"),sQuery(id+"F0.wireOp",EDGE,"E6.27.4"),sQuery(id+"F0.wireOp",EDGE,"E6.28.1"),sQuery(id+"F0.wireOp",EDGE,"E6.28.2"),sQuery(id+"F0.wireOp",EDGE,"E6.28.3"),sQuery(id+"F0.wireOp",EDGE,"E6.28.4"),sQuery(id+"F0.wireOp",EDGE,"E6.29.1"),sQuery(id+"F0.wireOp",EDGE,"E6.29.2"),sQuery(id+"F0.wireOp",EDGE,"E6.29.3"),sQuery(id+"F0.wireOp",EDGE,"E6.29.4"),sQuery(id+"F0.wireOp",EDGE,"E6.30.1"),sQuery(id+"F0.wireOp",EDGE,"E6.30.2"),sQuery(id+"F0.wireOp",EDGE,"E6.30.3"),sQuery(id+"F0.wireOp",EDGE,"E6.30.4"),sQuery(id+"F0.wireOp",EDGE,"E6.31.1"),sQuery(id+"F0.wireOp",EDGE,"E6.31.2"),sQuery(id+"F0.wireOp",EDGE,"E6.31.3"),sQuery(id+"F0.wireOp",EDGE,"E6.31.4"),sQuery(id+"F0.wireOp",EDGE,"E6.32.1"),sQuery(id+"F0.wireOp",EDGE,"E6.32.2"),sQuery(id+"F0.wireOp",EDGE,"E6.32.3"),sQuery(id+"F0.wireOp",EDGE,"E6.32.4"),sQuery(id+"F0.wireOp",EDGE,"E6.33.1"),sQuery(id+"F0.wireOp",EDGE,"E6.33.2"),sQuery(id+"F0.wireOp",EDGE,"E6.33.3"),sQuery(id+"F0.wireOp",EDGE,"E6.33.4"),sQuery(id+"F0.wireOp",EDGE,"E6.34.1"),sQuery(id+"F0.wireOp",EDGE,"E6.34.2"),sQuery(id+"F0.wireOp",EDGE,"E6.34.3"),sQuery(id+"F0.wireOp",EDGE,"E6.34.4"),sQuery(id+"F0.wireOp",EDGE,"E6.35.1"),sQuery(id+"F0.wireOp",EDGE,"E6.35.2"),sQuery(id+"F0.wireOp",EDGE,"E6.35.3"),sQuery(id+"F0.wireOp",EDGE,"E6.35.4"),sQuery(id+"F0.wireOp",EDGE,"E6.36.1"),sQuery(id+"F0.wireOp",EDGE,"E6.36.2"),sQuery(id+"F0.wireOp",EDGE,"E6.36.3"),sQuery(id+"F0.wireOp",EDGE,"E6.36.4"),sQuery(id+"F0.wireOp",EDGE,"E6.37.1"),sQuery(id+"F0.wireOp",EDGE,"E6.37.2"),sQuery(id+"F0.wireOp",EDGE,"E6.37.3"),sQuery(id+"F0.wireOp",EDGE,"E6.37.4"),sQuery(id+"F0.wireOp",EDGE,"E6.38.1"),sQuery(id+"F0.wireOp",EDGE,"E6.38.2"),sQuery(id+"F0.wireOp",EDGE,"E6.38.3"),sQuery(id+"F0.wireOp",EDGE,"E6.38.4"),sQuery(id+"F0.wireOp",EDGE,"E6.39.1"),sQuery(id+"F0.wireOp",EDGE,"E6.39.2"),sQuery(id+"F0.wireOp",EDGE,"E6.39.3"),sQuery(id+"F0.wireOp",EDGE,"E6.39.4"),sQuery(id+"F0.wireOp",EDGE,"E6.40.1"),sQuery(id+"F0.wireOp",EDGE,"E6.40.2"),sQuery(id+"F0.wireOp",EDGE,"E6.40.3"),sQuery(id+"F0.wireOp",EDGE,"E6.40.4"),sQuery(id+"F0.wireOp",EDGE,"E6.41.1"),sQuery(id+"F0.wireOp",EDGE,"E6.41.2"),sQuery(id+"F0.wireOp",EDGE,"E6.41.3"),sQuery(id+"F0.wireOp",EDGE,"E6.41.4"),sQuery(id+"F0.wireOp",EDGE,"E6.42.1"),sQuery(id+"F0.wireOp",EDGE,"E6.42.2"),sQuery(id+"F0.wireOp",EDGE,"E6.42.3"),sQuery(id+"F0.wireOp",EDGE,"E6.42.4"),sQuery(id+"F0.wireOp",EDGE,"E6.43.1"),sQuery(id+"F0.wireOp",EDGE,"E6.43.2"),sQuery(id+"F0.wireOp",EDGE,"E6.43.3"),sQuery(id+"F0.wireOp",EDGE,"E6.43.4"),sQuery(id+"F0.wireOp",EDGE,"E7"),sQuery(id+"F0.wireOp",EDGE,"E8.1.0"),sQuery(id+"F0.wireOp",EDGE,"E8.2.0"),sQuery(id+"F0.wireOp",EDGE,"E8.3.0"),sQuery(id+"F0.wireOp",EDGE,"E8.4.0"),sQuery(id+"F0.wireOp",EDGE,"E8.5.0"),sQuery(id+"F0.wireOp",EDGE,"E8.6.0"),sQuery(id+"F0.wireOp",EDGE,"E8.7.0"),sQuery(id+"F0.wireOp",EDGE,"E8.8.0"),sQuery(id+"F0.wireOp",EDGE,"E8.9.0"),sQuery(id+"F0.wireOp",EDGE,"E8.10.0"),sQuery(id+"F0.wireOp",EDGE,"E8.11.0"),sQuery(id+"F0.wireOp",EDGE,"E8.12.0"),sQuery(id+"F0.wireOp",EDGE,"E8.13.0"),sQuery(id+"F0.wireOp",EDGE,"E8.14.0"),sQuery(id+"F0.wireOp",EDGE,"E8.15.0"),sQuery(id+"F0.wireOp",EDGE,"E8.16.0"),sQuery(id+"F0.wireOp",EDGE,"E8.17.0"),sQuery(id+"F0.wireOp",EDGE,"E8.18.0"),sQuery(id+"F0.wireOp",EDGE,"E8.19.0"),sQuery(id+"F0.wireOp",EDGE,"E8.20.0"),sQuery(id+"F0.wireOp",EDGE,"E8.21.0"),sQuery(id+"F0.wireOp",EDGE,"E8.22.0"),sQuery(id+"F0.wireOp",EDGE,"E8.23.0"),sQuery(id+"F0.wireOp",EDGE,"E8.24.0"),sQuery(id+"F0.wireOp",EDGE,"E8.25.0"),sQuery(id+"F0.wireOp",EDGE,"E8.26.0"),sQuery(id+"F0.wireOp",EDGE,"E8.27.0"),sQuery(id+"F0.wireOp",EDGE,"E8.28.0"),sQuery(id+"F0.wireOp",EDGE,"E8.29.0"),sQuery(id+"F0.wireOp",EDGE,"E8.30.0"),sQuery(id+"F0.wireOp",EDGE,"E8.31.0"),sQuery(id+"F0.wireOp",EDGE,"E8.32.0"),sQuery(id+"F0.wireOp",EDGE,"E8.33.0"),sQuery(id+"F0.wireOp",EDGE,"E8.34.0"),sQuery(id+"F0.wireOp",EDGE,"E8.35.0"),sQuery(id+"F0.wireOp",EDGE,"E8.36.0"),sQuery(id+"F0.wireOp",EDGE,"E8.37.0"),sQuery(id+"F0.wireOp",EDGE,"E8.38.0"),sQuery(id+"F0.wireOp",EDGE,"E8.39.0"),sQuery(id+"F0.wireOp",EDGE,"E8.40.0"),sQuery(id+"F0.wireOp",EDGE,"E8.41.0"),sQuery(id+"F0.wireOp",EDGE,"E8.42.0"),sQuery(id+"F0.wireOp",EDGE,"E8.43.0")])],"isStart":false})]});}
            var Q12;
            {var subQ0=sQuery(id+"F0.wireOp",EDGE,"E6.3.3");var subQ1=sQuery(id+"F0.wireOp",EDGE,"E6.3.1");Q12=makeQuery(id+"F2.opFillet","BLEND_EDGE",EDGE,{"blendedFrom":[makeQuery(id+"F1.opExtrude","SWEPT_EDGE",EDGE,{"disambiguationData":[OSD([sQuery(id+"F0.wireOp",EDGE,"E6.3.0"),subQ1,subQ0])]}),makeQuery(id+"F1.opExtrude","CAP_FACE",FACE,{"disambiguationData":[OSD([sQuery(id+"F0.wireOp",EDGE,"E0"),sQuery(id+"F0.wireOp",EDGE,"E1"),sQuery(id+"F0.wireOp",EDGE,"E2"),sQuery(id+"F0.wireOp",EDGE,"E4"),sQuery(id+"F0.wireOp",EDGE,"E5"),sQuery(id+"F0.wireOp",EDGE,"E6.1.1"),sQuery(id+"F0.wireOp",EDGE,"E6.1.2"),sQuery(id+"F0.wireOp",EDGE,"E6.1.3"),sQuery(id+"F0.wireOp",EDGE,"E6.1.4"),sQuery(id+"F0.wireOp",EDGE,"E6.2.1"),sQuery(id+"F0.wireOp",EDGE,"E6.2.2"),sQuery(id+"F0.wireOp",EDGE,"E6.2.3"),sQuery(id+"F0.wireOp",EDGE,"E6.2.4"),subQ1,sQuery(id+"F0.wireOp",EDGE,"E6.3.2"),subQ0,sQuery(id+"F0.wireOp",EDGE,"E6.3.4"),sQuery(id+"F0.wireOp",EDGE,"E6.4.1"),sQuery(id+"F0.wireOp",EDGE,"E6.4.2"),sQuery(id+"F0.wireOp",EDGE,"E6.4.3"),sQuery(id+"F0.wireOp",EDGE,"E6.4.4"),sQuery(id+"F0.wireOp",EDGE,"E6.5.1"),sQuery(id+"F0.wireOp",EDGE,"E6.5.2"),sQuery(id+"F0.wireOp",EDGE,"E6.5.3"),sQuery(id+"F0.wireOp",EDGE,"E6.5.4"),sQuery(id+"F0.wireOp",EDGE,"E6.6.1"),sQuery(id+"F0.wireOp",EDGE,"E6.6.2"),sQuery(id+"F0.wireOp",EDGE,"E6.6.3"),sQuery(id+"F0.wireOp",EDGE,"E6.6.4"),sQuery(id+"F0.wireOp",EDGE,"E6.7.1"),sQuery(id+"F0.wireOp",EDGE,"E6.7.2"),sQuery(id+"F0.wireOp",EDGE,"E6.7.3"),sQuery(id+"F0.wireOp",EDGE,"E6.7.4"),sQuery(id+"F0.wireOp",EDGE,"E6.8.1"),sQuery(id+"F0.wireOp",EDGE,"E6.8.2"),sQuery(id+"F0.wireOp",EDGE,"E6.8.3"),sQuery(id+"F0.wireOp",EDGE,"E6.8.4"),sQuery(id+"F0.wireOp",EDGE,"E6.9.1"),sQuery(id+"F0.wireOp",EDGE,"E6.9.2"),sQuery(id+"F0.wireOp",EDGE,"E6.9.3"),sQuery(id+"F0.wireOp",EDGE,"E6.9.4"),sQuery(id+"F0.wireOp",EDGE,"E6.10.1"),sQuery(id+"F0.wireOp",EDGE,"E6.10.2"),sQuery(id+"F0.wireOp",EDGE,"E6.10.3"),sQuery(id+"F0.wireOp",EDGE,"E6.10.4"),sQuery(id+"F0.wireOp",EDGE,"E6.11.1"),sQuery(id+"F0.wireOp",EDGE,"E6.11.2"),sQuery(id+"F0.wireOp",EDGE,"E6.11.3"),sQuery(id+"F0.wireOp",EDGE,"E6.11.4"),sQuery(id+"F0.wireOp",EDGE,"E6.12.1"),sQuery(id+"F0.wireOp",EDGE,"E6.12.2"),sQuery(id+"F0.wireOp",EDGE,"E6.12.3"),sQuery(id+"F0.wireOp",EDGE,"E6.12.4"),sQuery(id+"F0.wireOp",EDGE,"E6.13.1"),sQuery(id+"F0.wireOp",EDGE,"E6.13.2"),sQuery(id+"F0.wireOp",EDGE,"E6.13.3"),sQuery(id+"F0.wireOp",EDGE,"E6.13.4"),sQuery(id+"F0.wireOp",EDGE,"E6.14.1"),sQuery(id+"F0.wireOp",EDGE,"E6.14.2"),sQuery(id+"F0.wireOp",EDGE,"E6.14.3"),sQuery(id+"F0.wireOp",EDGE,"E6.14.4"),sQuery(id+"F0.wireOp",EDGE,"E6.15.1"),sQuery(id+"F0.wireOp",EDGE,"E6.15.2"),sQuery(id+"F0.wireOp",EDGE,"E6.15.3"),sQuery(id+"F0.wireOp",EDGE,"E6.15.4"),sQuery(id+"F0.wireOp",EDGE,"E6.16.1"),sQuery(id+"F0.wireOp",EDGE,"E6.16.2"),sQuery(id+"F0.wireOp",EDGE,"E6.16.3"),sQuery(id+"F0.wireOp",EDGE,"E6.16.4"),sQuery(id+"F0.wireOp",EDGE,"E6.17.1"),sQuery(id+"F0.wireOp",EDGE,"E6.17.2"),sQuery(id+"F0.wireOp",EDGE,"E6.17.3"),sQuery(id+"F0.wireOp",EDGE,"E6.17.4"),sQuery(id+"F0.wireOp",EDGE,"E6.18.1"),sQuery(id+"F0.wireOp",EDGE,"E6.18.2"),sQuery(id+"F0.wireOp",EDGE,"E6.18.3"),sQuery(id+"F0.wireOp",EDGE,"E6.18.4"),sQuery(id+"F0.wireOp",EDGE,"E6.19.1"),sQuery(id+"F0.wireOp",EDGE,"E6.19.2"),sQuery(id+"F0.wireOp",EDGE,"E6.19.3"),sQuery(id+"F0.wireOp",EDGE,"E6.19.4"),sQuery(id+"F0.wireOp",EDGE,"E6.20.1"),sQuery(id+"F0.wireOp",EDGE,"E6.20.2"),sQuery(id+"F0.wireOp",EDGE,"E6.20.3"),sQuery(id+"F0.wireOp",EDGE,"E6.20.4"),sQuery(id+"F0.wireOp",EDGE,"E6.21.1"),sQuery(id+"F0.wireOp",EDGE,"E6.21.2"),sQuery(id+"F0.wireOp",EDGE,"E6.21.3"),sQuery(id+"F0.wireOp",EDGE,"E6.21.4"),sQuery(id+"F0.wireOp",EDGE,"E6.22.1"),sQuery(id+"F0.wireOp",EDGE,"E6.22.2"),sQuery(id+"F0.wireOp",EDGE,"E6.22.3"),sQuery(id+"F0.wireOp",EDGE,"E6.22.4"),sQuery(id+"F0.wireOp",EDGE,"E6.23.1"),sQuery(id+"F0.wireOp",EDGE,"E6.23.2"),sQuery(id+"F0.wireOp",EDGE,"E6.23.3"),sQuery(id+"F0.wireOp",EDGE,"E6.23.4"),sQuery(id+"F0.wireOp",EDGE,"E6.24.1"),sQuery(id+"F0.wireOp",EDGE,"E6.24.2"),sQuery(id+"F0.wireOp",EDGE,"E6.24.3"),sQuery(id+"F0.wireOp",EDGE,"E6.24.4"),sQuery(id+"F0.wireOp",EDGE,"E6.25.1"),sQuery(id+"F0.wireOp",EDGE,"E6.25.2"),sQuery(id+"F0.wireOp",EDGE,"E6.25.3"),sQuery(id+"F0.wireOp",EDGE,"E6.25.4"),sQuery(id+"F0.wireOp",EDGE,"E6.26.1"),sQuery(id+"F0.wireOp",EDGE,"E6.26.2"),sQuery(id+"F0.wireOp",EDGE,"E6.26.3"),sQuery(id+"F0.wireOp",EDGE,"E6.26.4"),sQuery(id+"F0.wireOp",EDGE,"E6.27.1"),sQuery(id+"F0.wireOp",EDGE,"E6.27.2"),sQuery(id+"F0.wireOp",EDGE,"E6.27.3"),sQuery(id+"F0.wireOp",EDGE,"E6.27.4"),sQuery(id+"F0.wireOp",EDGE,"E6.28.1"),sQuery(id+"F0.wireOp",EDGE,"E6.28.2"),sQuery(id+"F0.wireOp",EDGE,"E6.28.3"),sQuery(id+"F0.wireOp",EDGE,"E6.28.4"),sQuery(id+"F0.wireOp",EDGE,"E6.29.1"),sQuery(id+"F0.wireOp",EDGE,"E6.29.2"),sQuery(id+"F0.wireOp",EDGE,"E6.29.3"),sQuery(id+"F0.wireOp",EDGE,"E6.29.4"),sQuery(id+"F0.wireOp",EDGE,"E6.30.1"),sQuery(id+"F0.wireOp",EDGE,"E6.30.2"),sQuery(id+"F0.wireOp",EDGE,"E6.30.3"),sQuery(id+"F0.wireOp",EDGE,"E6.30.4"),sQuery(id+"F0.wireOp",EDGE,"E6.31.1"),sQuery(id+"F0.wireOp",EDGE,"E6.31.2"),sQuery(id+"F0.wireOp",EDGE,"E6.31.3"),sQuery(id+"F0.wireOp",EDGE,"E6.31.4"),sQuery(id+"F0.wireOp",EDGE,"E6.32.1"),sQuery(id+"F0.wireOp",EDGE,"E6.32.2"),sQuery(id+"F0.wireOp",EDGE,"E6.32.3"),sQuery(id+"F0.wireOp",EDGE,"E6.32.4"),sQuery(id+"F0.wireOp",EDGE,"E6.33.1"),sQuery(id+"F0.wireOp",EDGE,"E6.33.2"),sQuery(id+"F0.wireOp",EDGE,"E6.33.3"),sQuery(id+"F0.wireOp",EDGE,"E6.33.4"),sQuery(id+"F0.wireOp",EDGE,"E6.34.1"),sQuery(id+"F0.wireOp",EDGE,"E6.34.2"),sQuery(id+"F0.wireOp",EDGE,"E6.34.3"),sQuery(id+"F0.wireOp",EDGE,"E6.34.4"),sQuery(id+"F0.wireOp",EDGE,"E6.35.1"),sQuery(id+"F0.wireOp",EDGE,"E6.35.2"),sQuery(id+"F0.wireOp",EDGE,"E6.35.3"),sQuery(id+"F0.wireOp",EDGE,"E6.35.4"),sQuery(id+"F0.wireOp",EDGE,"E6.36.1"),sQuery(id+"F0.wireOp",EDGE,"E6.36.2"),sQuery(id+"F0.wireOp",EDGE,"E6.36.3"),sQuery(id+"F0.wireOp",EDGE,"E6.36.4"),sQuery(id+"F0.wireOp",EDGE,"E6.37.1"),sQuery(id+"F0.wireOp",EDGE,"E6.37.2"),sQuery(id+"F0.wireOp",EDGE,"E6.37.3"),sQuery(id+"F0.wireOp",EDGE,"E6.37.4"),sQuery(id+"F0.wireOp",EDGE,"E6.38.1"),sQuery(id+"F0.wireOp",EDGE,"E6.38.2"),sQuery(id+"F0.wireOp",EDGE,"E6.38.3"),sQuery(id+"F0.wireOp",EDGE,"E6.38.4"),sQuery(id+"F0.wireOp",EDGE,"E6.39.1"),sQuery(id+"F0.wireOp",EDGE,"E6.39.2"),sQuery(id+"F0.wireOp",EDGE,"E6.39.3"),sQuery(id+"F0.wireOp",EDGE,"E6.39.4"),sQuery(id+"F0.wireOp",EDGE,"E6.40.1"),sQuery(id+"F0.wireOp",EDGE,"E6.40.2"),sQuery(id+"F0.wireOp",EDGE,"E6.40.3"),sQuery(id+"F0.wireOp",EDGE,"E6.40.4"),sQuery(id+"F0.wireOp",EDGE,"E6.41.1"),sQuery(id+"F0.wireOp",EDGE,"E6.41.2"),sQuery(id+"F0.wireOp",EDGE,"E6.41.3"),sQuery(id+"F0.wireOp",EDGE,"E6.41.4"),sQuery(id+"F0.wireOp",EDGE,"E6.42.1"),sQuery(id+"F0.wireOp",EDGE,"E6.42.2"),sQuery(id+"F0.wireOp",EDGE,"E6.42.3"),sQuery(id+"F0.wireOp",EDGE,"E6.42.4"),sQuery(id+"F0.wireOp",EDGE,"E6.43.1"),sQuery(id+"F0.wireOp",EDGE,"E6.43.2"),sQuery(id+"F0.wireOp",EDGE,"E6.43.3"),sQuery(id+"F0.wireOp",EDGE,"E6.43.4"),sQuery(id+"F0.wireOp",EDGE,"E7"),sQuery(id+"F0.wireOp",EDGE,"E8.1.0"),sQuery(id+"F0.wireOp",EDGE,"E8.2.0"),sQuery(id+"F0.wireOp",EDGE,"E8.3.0"),sQuery(id+"F0.wireOp",EDGE,"E8.4.0"),sQuery(id+"F0.wireOp",EDGE,"E8.5.0"),sQuery(id+"F0.wireOp",EDGE,"E8.6.0"),sQuery(id+"F0.wireOp",EDGE,"E8.7.0"),sQuery(id+"F0.wireOp",EDGE,"E8.8.0"),sQuery(id+"F0.wireOp",EDGE,"E8.9.0"),sQuery(id+"F0.wireOp",EDGE,"E8.10.0"),sQuery(id+"F0.wireOp",EDGE,"E8.11.0"),sQuery(id+"F0.wireOp",EDGE,"E8.12.0"),sQuery(id+"F0.wireOp",EDGE,"E8.13.0"),sQuery(id+"F0.wireOp",EDGE,"E8.14.0"),sQuery(id+"F0.wireOp",EDGE,"E8.15.0"),sQuery(id+"F0.wireOp",EDGE,"E8.16.0"),sQuery(id+"F0.wireOp",EDGE,"E8.17.0"),sQuery(id+"F0.wireOp",EDGE,"E8.18.0"),sQuery(id+"F0.wireOp",EDGE,"E8.19.0"),sQuery(id+"F0.wireOp",EDGE,"E8.20.0"),sQuery(id+"F0.wireOp",EDGE,"E8.21.0"),sQuery(id+"F0.wireOp",EDGE,"E8.22.0"),sQuery(id+"F0.wireOp",EDGE,"E8.23.0"),sQuery(id+"F0.wireOp",EDGE,"E8.24.0"),sQuery(id+"F0.wireOp",EDGE,"E8.25.0"),sQuery(id+"F0.wireOp",EDGE,"E8.26.0"),sQuery(id+"F0.wireOp",EDGE,"E8.27.0"),sQuery(id+"F0.wireOp",EDGE,"E8.28.0"),sQuery(id+"F0.wireOp",EDGE,"E8.29.0"),sQuery(id+"F0.wireOp",EDGE,"E8.30.0"),sQuery(id+"F0.wireOp",EDGE,"E8.31.0"),sQuery(id+"F0.wireOp",EDGE,"E8.32.0"),sQuery(id+"F0.wireOp",EDGE,"E8.33.0"),sQuery(id+"F0.wireOp",EDGE,"E8.34.0"),sQuery(id+"F0.wireOp",EDGE,"E8.35.0"),sQuery(id+"F0.wireOp",EDGE,"E8.36.0"),sQuery(id+"F0.wireOp",EDGE,"E8.37.0"),sQuery(id+"F0.wireOp",EDGE,"E8.38.0"),sQuery(id+"F0.wireOp",EDGE,"E8.39.0"),sQuery(id+"F0.wireOp",EDGE,"E8.40.0"),sQuery(id+"F0.wireOp",EDGE,"E8.41.0"),sQuery(id+"F0.wireOp",EDGE,"E8.42.0"),sQuery(id+"F0.wireOp",EDGE,"E8.43.0")])],"isStart":false})],"blendedInto":[makeQuery(id+"F1.opExtrude","CAP_FACE",FACE,{"disambiguationData":[OSD([sQuery(id+"F0.wireOp",EDGE,"E0"),sQuery(id+"F0.wireOp",EDGE,"E1"),sQuery(id+"F0.wireOp",EDGE,"E2"),sQuery(id+"F0.wireOp",EDGE,"E4"),sQuery(id+"F0.wireOp",EDGE,"E5"),sQuery(id+"F0.wireOp",EDGE,"E6.1.1"),sQuery(id+"F0.wireOp",EDGE,"E6.1.2"),sQuery(id+"F0.wireOp",EDGE,"E6.1.3"),sQuery(id+"F0.wireOp",EDGE,"E6.1.4"),sQuery(id+"F0.wireOp",EDGE,"E6.2.1"),sQuery(id+"F0.wireOp",EDGE,"E6.2.2"),sQuery(id+"F0.wireOp",EDGE,"E6.2.3"),sQuery(id+"F0.wireOp",EDGE,"E6.2.4"),subQ1,sQuery(id+"F0.wireOp",EDGE,"E6.3.2"),subQ0,sQuery(id+"F0.wireOp",EDGE,"E6.3.4"),sQuery(id+"F0.wireOp",EDGE,"E6.4.1"),sQuery(id+"F0.wireOp",EDGE,"E6.4.2"),sQuery(id+"F0.wireOp",EDGE,"E6.4.3"),sQuery(id+"F0.wireOp",EDGE,"E6.4.4"),sQuery(id+"F0.wireOp",EDGE,"E6.5.1"),sQuery(id+"F0.wireOp",EDGE,"E6.5.2"),sQuery(id+"F0.wireOp",EDGE,"E6.5.3"),sQuery(id+"F0.wireOp",EDGE,"E6.5.4"),sQuery(id+"F0.wireOp",EDGE,"E6.6.1"),sQuery(id+"F0.wireOp",EDGE,"E6.6.2"),sQuery(id+"F0.wireOp",EDGE,"E6.6.3"),sQuery(id+"F0.wireOp",EDGE,"E6.6.4"),sQuery(id+"F0.wireOp",EDGE,"E6.7.1"),sQuery(id+"F0.wireOp",EDGE,"E6.7.2"),sQuery(id+"F0.wireOp",EDGE,"E6.7.3"),sQuery(id+"F0.wireOp",EDGE,"E6.7.4"),sQuery(id+"F0.wireOp",EDGE,"E6.8.1"),sQuery(id+"F0.wireOp",EDGE,"E6.8.2"),sQuery(id+"F0.wireOp",EDGE,"E6.8.3"),sQuery(id+"F0.wireOp",EDGE,"E6.8.4"),sQuery(id+"F0.wireOp",EDGE,"E6.9.1"),sQuery(id+"F0.wireOp",EDGE,"E6.9.2"),sQuery(id+"F0.wireOp",EDGE,"E6.9.3"),sQuery(id+"F0.wireOp",EDGE,"E6.9.4"),sQuery(id+"F0.wireOp",EDGE,"E6.10.1"),sQuery(id+"F0.wireOp",EDGE,"E6.10.2"),sQuery(id+"F0.wireOp",EDGE,"E6.10.3"),sQuery(id+"F0.wireOp",EDGE,"E6.10.4"),sQuery(id+"F0.wireOp",EDGE,"E6.11.1"),sQuery(id+"F0.wireOp",EDGE,"E6.11.2"),sQuery(id+"F0.wireOp",EDGE,"E6.11.3"),sQuery(id+"F0.wireOp",EDGE,"E6.11.4"),sQuery(id+"F0.wireOp",EDGE,"E6.12.1"),sQuery(id+"F0.wireOp",EDGE,"E6.12.2"),sQuery(id+"F0.wireOp",EDGE,"E6.12.3"),sQuery(id+"F0.wireOp",EDGE,"E6.12.4"),sQuery(id+"F0.wireOp",EDGE,"E6.13.1"),sQuery(id+"F0.wireOp",EDGE,"E6.13.2"),sQuery(id+"F0.wireOp",EDGE,"E6.13.3"),sQuery(id+"F0.wireOp",EDGE,"E6.13.4"),sQuery(id+"F0.wireOp",EDGE,"E6.14.1"),sQuery(id+"F0.wireOp",EDGE,"E6.14.2"),sQuery(id+"F0.wireOp",EDGE,"E6.14.3"),sQuery(id+"F0.wireOp",EDGE,"E6.14.4"),sQuery(id+"F0.wireOp",EDGE,"E6.15.1"),sQuery(id+"F0.wireOp",EDGE,"E6.15.2"),sQuery(id+"F0.wireOp",EDGE,"E6.15.3"),sQuery(id+"F0.wireOp",EDGE,"E6.15.4"),sQuery(id+"F0.wireOp",EDGE,"E6.16.1"),sQuery(id+"F0.wireOp",EDGE,"E6.16.2"),sQuery(id+"F0.wireOp",EDGE,"E6.16.3"),sQuery(id+"F0.wireOp",EDGE,"E6.16.4"),sQuery(id+"F0.wireOp",EDGE,"E6.17.1"),sQuery(id+"F0.wireOp",EDGE,"E6.17.2"),sQuery(id+"F0.wireOp",EDGE,"E6.17.3"),sQuery(id+"F0.wireOp",EDGE,"E6.17.4"),sQuery(id+"F0.wireOp",EDGE,"E6.18.1"),sQuery(id+"F0.wireOp",EDGE,"E6.18.2"),sQuery(id+"F0.wireOp",EDGE,"E6.18.3"),sQuery(id+"F0.wireOp",EDGE,"E6.18.4"),sQuery(id+"F0.wireOp",EDGE,"E6.19.1"),sQuery(id+"F0.wireOp",EDGE,"E6.19.2"),sQuery(id+"F0.wireOp",EDGE,"E6.19.3"),sQuery(id+"F0.wireOp",EDGE,"E6.19.4"),sQuery(id+"F0.wireOp",EDGE,"E6.20.1"),sQuery(id+"F0.wireOp",EDGE,"E6.20.2"),sQuery(id+"F0.wireOp",EDGE,"E6.20.3"),sQuery(id+"F0.wireOp",EDGE,"E6.20.4"),sQuery(id+"F0.wireOp",EDGE,"E6.21.1"),sQuery(id+"F0.wireOp",EDGE,"E6.21.2"),sQuery(id+"F0.wireOp",EDGE,"E6.21.3"),sQuery(id+"F0.wireOp",EDGE,"E6.21.4"),sQuery(id+"F0.wireOp",EDGE,"E6.22.1"),sQuery(id+"F0.wireOp",EDGE,"E6.22.2"),sQuery(id+"F0.wireOp",EDGE,"E6.22.3"),sQuery(id+"F0.wireOp",EDGE,"E6.22.4"),sQuery(id+"F0.wireOp",EDGE,"E6.23.1"),sQuery(id+"F0.wireOp",EDGE,"E6.23.2"),sQuery(id+"F0.wireOp",EDGE,"E6.23.3"),sQuery(id+"F0.wireOp",EDGE,"E6.23.4"),sQuery(id+"F0.wireOp",EDGE,"E6.24.1"),sQuery(id+"F0.wireOp",EDGE,"E6.24.2"),sQuery(id+"F0.wireOp",EDGE,"E6.24.3"),sQuery(id+"F0.wireOp",EDGE,"E6.24.4"),sQuery(id+"F0.wireOp",EDGE,"E6.25.1"),sQuery(id+"F0.wireOp",EDGE,"E6.25.2"),sQuery(id+"F0.wireOp",EDGE,"E6.25.3"),sQuery(id+"F0.wireOp",EDGE,"E6.25.4"),sQuery(id+"F0.wireOp",EDGE,"E6.26.1"),sQuery(id+"F0.wireOp",EDGE,"E6.26.2"),sQuery(id+"F0.wireOp",EDGE,"E6.26.3"),sQuery(id+"F0.wireOp",EDGE,"E6.26.4"),sQuery(id+"F0.wireOp",EDGE,"E6.27.1"),sQuery(id+"F0.wireOp",EDGE,"E6.27.2"),sQuery(id+"F0.wireOp",EDGE,"E6.27.3"),sQuery(id+"F0.wireOp",EDGE,"E6.27.4"),sQuery(id+"F0.wireOp",EDGE,"E6.28.1"),sQuery(id+"F0.wireOp",EDGE,"E6.28.2"),sQuery(id+"F0.wireOp",EDGE,"E6.28.3"),sQuery(id+"F0.wireOp",EDGE,"E6.28.4"),sQuery(id+"F0.wireOp",EDGE,"E6.29.1"),sQuery(id+"F0.wireOp",EDGE,"E6.29.2"),sQuery(id+"F0.wireOp",EDGE,"E6.29.3"),sQuery(id+"F0.wireOp",EDGE,"E6.29.4"),sQuery(id+"F0.wireOp",EDGE,"E6.30.1"),sQuery(id+"F0.wireOp",EDGE,"E6.30.2"),sQuery(id+"F0.wireOp",EDGE,"E6.30.3"),sQuery(id+"F0.wireOp",EDGE,"E6.30.4"),sQuery(id+"F0.wireOp",EDGE,"E6.31.1"),sQuery(id+"F0.wireOp",EDGE,"E6.31.2"),sQuery(id+"F0.wireOp",EDGE,"E6.31.3"),sQuery(id+"F0.wireOp",EDGE,"E6.31.4"),sQuery(id+"F0.wireOp",EDGE,"E6.32.1"),sQuery(id+"F0.wireOp",EDGE,"E6.32.2"),sQuery(id+"F0.wireOp",EDGE,"E6.32.3"),sQuery(id+"F0.wireOp",EDGE,"E6.32.4"),sQuery(id+"F0.wireOp",EDGE,"E6.33.1"),sQuery(id+"F0.wireOp",EDGE,"E6.33.2"),sQuery(id+"F0.wireOp",EDGE,"E6.33.3"),sQuery(id+"F0.wireOp",EDGE,"E6.33.4"),sQuery(id+"F0.wireOp",EDGE,"E6.34.1"),sQuery(id+"F0.wireOp",EDGE,"E6.34.2"),sQuery(id+"F0.wireOp",EDGE,"E6.34.3"),sQuery(id+"F0.wireOp",EDGE,"E6.34.4"),sQuery(id+"F0.wireOp",EDGE,"E6.35.1"),sQuery(id+"F0.wireOp",EDGE,"E6.35.2"),sQuery(id+"F0.wireOp",EDGE,"E6.35.3"),sQuery(id+"F0.wireOp",EDGE,"E6.35.4"),sQuery(id+"F0.wireOp",EDGE,"E6.36.1"),sQuery(id+"F0.wireOp",EDGE,"E6.36.2"),sQuery(id+"F0.wireOp",EDGE,"E6.36.3"),sQuery(id+"F0.wireOp",EDGE,"E6.36.4"),sQuery(id+"F0.wireOp",EDGE,"E6.37.1"),sQuery(id+"F0.wireOp",EDGE,"E6.37.2"),sQuery(id+"F0.wireOp",EDGE,"E6.37.3"),sQuery(id+"F0.wireOp",EDGE,"E6.37.4"),sQuery(id+"F0.wireOp",EDGE,"E6.38.1"),sQuery(id+"F0.wireOp",EDGE,"E6.38.2"),sQuery(id+"F0.wireOp",EDGE,"E6.38.3"),sQuery(id+"F0.wireOp",EDGE,"E6.38.4"),sQuery(id+"F0.wireOp",EDGE,"E6.39.1"),sQuery(id+"F0.wireOp",EDGE,"E6.39.2"),sQuery(id+"F0.wireOp",EDGE,"E6.39.3"),sQuery(id+"F0.wireOp",EDGE,"E6.39.4"),sQuery(id+"F0.wireOp",EDGE,"E6.40.1"),sQuery(id+"F0.wireOp",EDGE,"E6.40.2"),sQuery(id+"F0.wireOp",EDGE,"E6.40.3"),sQuery(id+"F0.wireOp",EDGE,"E6.40.4"),sQuery(id+"F0.wireOp",EDGE,"E6.41.1"),sQuery(id+"F0.wireOp",EDGE,"E6.41.2"),sQuery(id+"F0.wireOp",EDGE,"E6.41.3"),sQuery(id+"F0.wireOp",EDGE,"E6.41.4"),sQuery(id+"F0.wireOp",EDGE,"E6.42.1"),sQuery(id+"F0.wireOp",EDGE,"E6.42.2"),sQuery(id+"F0.wireOp",EDGE,"E6.42.3"),sQuery(id+"F0.wireOp",EDGE,"E6.42.4"),sQuery(id+"F0.wireOp",EDGE,"E6.43.1"),sQuery(id+"F0.wireOp",EDGE,"E6.43.2"),sQuery(id+"F0.wireOp",EDGE,"E6.43.3"),sQuery(id+"F0.wireOp",EDGE,"E6.43.4"),sQuery(id+"F0.wireOp",EDGE,"E7"),sQuery(id+"F0.wireOp",EDGE,"E8.1.0"),sQuery(id+"F0.wireOp",EDGE,"E8.2.0"),sQuery(id+"F0.wireOp",EDGE,"E8.3.0"),sQuery(id+"F0.wireOp",EDGE,"E8.4.0"),sQuery(id+"F0.wireOp",EDGE,"E8.5.0"),sQuery(id+"F0.wireOp",EDGE,"E8.6.0"),sQuery(id+"F0.wireOp",EDGE,"E8.7.0"),sQuery(id+"F0.wireOp",EDGE,"E8.8.0"),sQuery(id+"F0.wireOp",EDGE,"E8.9.0"),sQuery(id+"F0.wireOp",EDGE,"E8.10.0"),sQuery(id+"F0.wireOp",EDGE,"E8.11.0"),sQuery(id+"F0.wireOp",EDGE,"E8.12.0"),sQuery(id+"F0.wireOp",EDGE,"E8.13.0"),sQuery(id+"F0.wireOp",EDGE,"E8.14.0"),sQuery(id+"F0.wireOp",EDGE,"E8.15.0"),sQuery(id+"F0.wireOp",EDGE,"E8.16.0"),sQuery(id+"F0.wireOp",EDGE,"E8.17.0"),sQuery(id+"F0.wireOp",EDGE,"E8.18.0"),sQuery(id+"F0.wireOp",EDGE,"E8.19.0"),sQuery(id+"F0.wireOp",EDGE,"E8.20.0"),sQuery(id+"F0.wireOp",EDGE,"E8.21.0"),sQuery(id+"F0.wireOp",EDGE,"E8.22.0"),sQuery(id+"F0.wireOp",EDGE,"E8.23.0"),sQuery(id+"F0.wireOp",EDGE,"E8.24.0"),sQuery(id+"F0.wireOp",EDGE,"E8.25.0"),sQuery(id+"F0.wireOp",EDGE,"E8.26.0"),sQuery(id+"F0.wireOp",EDGE,"E8.27.0"),sQuery(id+"F0.wireOp",EDGE,"E8.28.0"),sQuery(id+"F0.wireOp",EDGE,"E8.29.0"),sQuery(id+"F0.wireOp",EDGE,"E8.30.0"),sQuery(id+"F0.wireOp",EDGE,"E8.31.0"),sQuery(id+"F0.wireOp",EDGE,"E8.32.0"),sQuery(id+"F0.wireOp",EDGE,"E8.33.0"),sQuery(id+"F0.wireOp",EDGE,"E8.34.0"),sQuery(id+"F0.wireOp",EDGE,"E8.35.0"),sQuery(id+"F0.wireOp",EDGE,"E8.36.0"),sQuery(id+"F0.wireOp",EDGE,"E8.37.0"),sQuery(id+"F0.wireOp",EDGE,"E8.38.0"),sQuery(id+"F0.wireOp",EDGE,"E8.39.0"),sQuery(id+"F0.wireOp",EDGE,"E8.40.0"),sQuery(id+"F0.wireOp",EDGE,"E8.41.0"),sQuery(id+"F0.wireOp",EDGE,"E8.42.0"),sQuery(id+"F0.wireOp",EDGE,"E8.43.0")])],"isStart":false})]});}
            var Q13;
            {var subQ0=sQuery(id+"F0.wireOp",EDGE,"E6.5.3");var subQ1=sQuery(id+"F0.wireOp",EDGE,"E6.5.1");Q13=makeQuery(id+"F2.opFillet","BLEND_EDGE",EDGE,{"blendedFrom":[makeQuery(id+"F1.opExtrude","SWEPT_EDGE",EDGE,{"disambiguationData":[OSD([sQuery(id+"F0.wireOp",EDGE,"E6.5.0"),subQ1,subQ0])]}),makeQuery(id+"F1.opExtrude","CAP_FACE",FACE,{"disambiguationData":[OSD([sQuery(id+"F0.wireOp",EDGE,"E0"),sQuery(id+"F0.wireOp",EDGE,"E1"),sQuery(id+"F0.wireOp",EDGE,"E2"),sQuery(id+"F0.wireOp",EDGE,"E4"),sQuery(id+"F0.wireOp",EDGE,"E5"),sQuery(id+"F0.wireOp",EDGE,"E6.1.1"),sQuery(id+"F0.wireOp",EDGE,"E6.1.2"),sQuery(id+"F0.wireOp",EDGE,"E6.1.3"),sQuery(id+"F0.wireOp",EDGE,"E6.1.4"),sQuery(id+"F0.wireOp",EDGE,"E6.2.1"),sQuery(id+"F0.wireOp",EDGE,"E6.2.2"),sQuery(id+"F0.wireOp",EDGE,"E6.2.3"),sQuery(id+"F0.wireOp",EDGE,"E6.2.4"),sQuery(id+"F0.wireOp",EDGE,"E6.3.1"),sQuery(id+"F0.wireOp",EDGE,"E6.3.2"),sQuery(id+"F0.wireOp",EDGE,"E6.3.3"),sQuery(id+"F0.wireOp",EDGE,"E6.3.4"),sQuery(id+"F0.wireOp",EDGE,"E6.4.1"),sQuery(id+"F0.wireOp",EDGE,"E6.4.2"),sQuery(id+"F0.wireOp",EDGE,"E6.4.3"),sQuery(id+"F0.wireOp",EDGE,"E6.4.4"),subQ1,sQuery(id+"F0.wireOp",EDGE,"E6.5.2"),subQ0,sQuery(id+"F0.wireOp",EDGE,"E6.5.4"),sQuery(id+"F0.wireOp",EDGE,"E6.6.1"),sQuery(id+"F0.wireOp",EDGE,"E6.6.2"),sQuery(id+"F0.wireOp",EDGE,"E6.6.3"),sQuery(id+"F0.wireOp",EDGE,"E6.6.4"),sQuery(id+"F0.wireOp",EDGE,"E6.7.1"),sQuery(id+"F0.wireOp",EDGE,"E6.7.2"),sQuery(id+"F0.wireOp",EDGE,"E6.7.3"),sQuery(id+"F0.wireOp",EDGE,"E6.7.4"),sQuery(id+"F0.wireOp",EDGE,"E6.8.1"),sQuery(id+"F0.wireOp",EDGE,"E6.8.2"),sQuery(id+"F0.wireOp",EDGE,"E6.8.3"),sQuery(id+"F0.wireOp",EDGE,"E6.8.4"),sQuery(id+"F0.wireOp",EDGE,"E6.9.1"),sQuery(id+"F0.wireOp",EDGE,"E6.9.2"),sQuery(id+"F0.wireOp",EDGE,"E6.9.3"),sQuery(id+"F0.wireOp",EDGE,"E6.9.4"),sQuery(id+"F0.wireOp",EDGE,"E6.10.1"),sQuery(id+"F0.wireOp",EDGE,"E6.10.2"),sQuery(id+"F0.wireOp",EDGE,"E6.10.3"),sQuery(id+"F0.wireOp",EDGE,"E6.10.4"),sQuery(id+"F0.wireOp",EDGE,"E6.11.1"),sQuery(id+"F0.wireOp",EDGE,"E6.11.2"),sQuery(id+"F0.wireOp",EDGE,"E6.11.3"),sQuery(id+"F0.wireOp",EDGE,"E6.11.4"),sQuery(id+"F0.wireOp",EDGE,"E6.12.1"),sQuery(id+"F0.wireOp",EDGE,"E6.12.2"),sQuery(id+"F0.wireOp",EDGE,"E6.12.3"),sQuery(id+"F0.wireOp",EDGE,"E6.12.4"),sQuery(id+"F0.wireOp",EDGE,"E6.13.1"),sQuery(id+"F0.wireOp",EDGE,"E6.13.2"),sQuery(id+"F0.wireOp",EDGE,"E6.13.3"),sQuery(id+"F0.wireOp",EDGE,"E6.13.4"),sQuery(id+"F0.wireOp",EDGE,"E6.14.1"),sQuery(id+"F0.wireOp",EDGE,"E6.14.2"),sQuery(id+"F0.wireOp",EDGE,"E6.14.3"),sQuery(id+"F0.wireOp",EDGE,"E6.14.4"),sQuery(id+"F0.wireOp",EDGE,"E6.15.1"),sQuery(id+"F0.wireOp",EDGE,"E6.15.2"),sQuery(id+"F0.wireOp",EDGE,"E6.15.3"),sQuery(id+"F0.wireOp",EDGE,"E6.15.4"),sQuery(id+"F0.wireOp",EDGE,"E6.16.1"),sQuery(id+"F0.wireOp",EDGE,"E6.16.2"),sQuery(id+"F0.wireOp",EDGE,"E6.16.3"),sQuery(id+"F0.wireOp",EDGE,"E6.16.4"),sQuery(id+"F0.wireOp",EDGE,"E6.17.1"),sQuery(id+"F0.wireOp",EDGE,"E6.17.2"),sQuery(id+"F0.wireOp",EDGE,"E6.17.3"),sQuery(id+"F0.wireOp",EDGE,"E6.17.4"),sQuery(id+"F0.wireOp",EDGE,"E6.18.1"),sQuery(id+"F0.wireOp",EDGE,"E6.18.2"),sQuery(id+"F0.wireOp",EDGE,"E6.18.3"),sQuery(id+"F0.wireOp",EDGE,"E6.18.4"),sQuery(id+"F0.wireOp",EDGE,"E6.19.1"),sQuery(id+"F0.wireOp",EDGE,"E6.19.2"),sQuery(id+"F0.wireOp",EDGE,"E6.19.3"),sQuery(id+"F0.wireOp",EDGE,"E6.19.4"),sQuery(id+"F0.wireOp",EDGE,"E6.20.1"),sQuery(id+"F0.wireOp",EDGE,"E6.20.2"),sQuery(id+"F0.wireOp",EDGE,"E6.20.3"),sQuery(id+"F0.wireOp",EDGE,"E6.20.4"),sQuery(id+"F0.wireOp",EDGE,"E6.21.1"),sQuery(id+"F0.wireOp",EDGE,"E6.21.2"),sQuery(id+"F0.wireOp",EDGE,"E6.21.3"),sQuery(id+"F0.wireOp",EDGE,"E6.21.4"),sQuery(id+"F0.wireOp",EDGE,"E6.22.1"),sQuery(id+"F0.wireOp",EDGE,"E6.22.2"),sQuery(id+"F0.wireOp",EDGE,"E6.22.3"),sQuery(id+"F0.wireOp",EDGE,"E6.22.4"),sQuery(id+"F0.wireOp",EDGE,"E6.23.1"),sQuery(id+"F0.wireOp",EDGE,"E6.23.2"),sQuery(id+"F0.wireOp",EDGE,"E6.23.3"),sQuery(id+"F0.wireOp",EDGE,"E6.23.4"),sQuery(id+"F0.wireOp",EDGE,"E6.24.1"),sQuery(id+"F0.wireOp",EDGE,"E6.24.2"),sQuery(id+"F0.wireOp",EDGE,"E6.24.3"),sQuery(id+"F0.wireOp",EDGE,"E6.24.4"),sQuery(id+"F0.wireOp",EDGE,"E6.25.1"),sQuery(id+"F0.wireOp",EDGE,"E6.25.2"),sQuery(id+"F0.wireOp",EDGE,"E6.25.3"),sQuery(id+"F0.wireOp",EDGE,"E6.25.4"),sQuery(id+"F0.wireOp",EDGE,"E6.26.1"),sQuery(id+"F0.wireOp",EDGE,"E6.26.2"),sQuery(id+"F0.wireOp",EDGE,"E6.26.3"),sQuery(id+"F0.wireOp",EDGE,"E6.26.4"),sQuery(id+"F0.wireOp",EDGE,"E6.27.1"),sQuery(id+"F0.wireOp",EDGE,"E6.27.2"),sQuery(id+"F0.wireOp",EDGE,"E6.27.3"),sQuery(id+"F0.wireOp",EDGE,"E6.27.4"),sQuery(id+"F0.wireOp",EDGE,"E6.28.1"),sQuery(id+"F0.wireOp",EDGE,"E6.28.2"),sQuery(id+"F0.wireOp",EDGE,"E6.28.3"),sQuery(id+"F0.wireOp",EDGE,"E6.28.4"),sQuery(id+"F0.wireOp",EDGE,"E6.29.1"),sQuery(id+"F0.wireOp",EDGE,"E6.29.2"),sQuery(id+"F0.wireOp",EDGE,"E6.29.3"),sQuery(id+"F0.wireOp",EDGE,"E6.29.4"),sQuery(id+"F0.wireOp",EDGE,"E6.30.1"),sQuery(id+"F0.wireOp",EDGE,"E6.30.2"),sQuery(id+"F0.wireOp",EDGE,"E6.30.3"),sQuery(id+"F0.wireOp",EDGE,"E6.30.4"),sQuery(id+"F0.wireOp",EDGE,"E6.31.1"),sQuery(id+"F0.wireOp",EDGE,"E6.31.2"),sQuery(id+"F0.wireOp",EDGE,"E6.31.3"),sQuery(id+"F0.wireOp",EDGE,"E6.31.4"),sQuery(id+"F0.wireOp",EDGE,"E6.32.1"),sQuery(id+"F0.wireOp",EDGE,"E6.32.2"),sQuery(id+"F0.wireOp",EDGE,"E6.32.3"),sQuery(id+"F0.wireOp",EDGE,"E6.32.4"),sQuery(id+"F0.wireOp",EDGE,"E6.33.1"),sQuery(id+"F0.wireOp",EDGE,"E6.33.2"),sQuery(id+"F0.wireOp",EDGE,"E6.33.3"),sQuery(id+"F0.wireOp",EDGE,"E6.33.4"),sQuery(id+"F0.wireOp",EDGE,"E6.34.1"),sQuery(id+"F0.wireOp",EDGE,"E6.34.2"),sQuery(id+"F0.wireOp",EDGE,"E6.34.3"),sQuery(id+"F0.wireOp",EDGE,"E6.34.4"),sQuery(id+"F0.wireOp",EDGE,"E6.35.1"),sQuery(id+"F0.wireOp",EDGE,"E6.35.2"),sQuery(id+"F0.wireOp",EDGE,"E6.35.3"),sQuery(id+"F0.wireOp",EDGE,"E6.35.4"),sQuery(id+"F0.wireOp",EDGE,"E6.36.1"),sQuery(id+"F0.wireOp",EDGE,"E6.36.2"),sQuery(id+"F0.wireOp",EDGE,"E6.36.3"),sQuery(id+"F0.wireOp",EDGE,"E6.36.4"),sQuery(id+"F0.wireOp",EDGE,"E6.37.1"),sQuery(id+"F0.wireOp",EDGE,"E6.37.2"),sQuery(id+"F0.wireOp",EDGE,"E6.37.3"),sQuery(id+"F0.wireOp",EDGE,"E6.37.4"),sQuery(id+"F0.wireOp",EDGE,"E6.38.1"),sQuery(id+"F0.wireOp",EDGE,"E6.38.2"),sQuery(id+"F0.wireOp",EDGE,"E6.38.3"),sQuery(id+"F0.wireOp",EDGE,"E6.38.4"),sQuery(id+"F0.wireOp",EDGE,"E6.39.1"),sQuery(id+"F0.wireOp",EDGE,"E6.39.2"),sQuery(id+"F0.wireOp",EDGE,"E6.39.3"),sQuery(id+"F0.wireOp",EDGE,"E6.39.4"),sQuery(id+"F0.wireOp",EDGE,"E6.40.1"),sQuery(id+"F0.wireOp",EDGE,"E6.40.2"),sQuery(id+"F0.wireOp",EDGE,"E6.40.3"),sQuery(id+"F0.wireOp",EDGE,"E6.40.4"),sQuery(id+"F0.wireOp",EDGE,"E6.41.1"),sQuery(id+"F0.wireOp",EDGE,"E6.41.2"),sQuery(id+"F0.wireOp",EDGE,"E6.41.3"),sQuery(id+"F0.wireOp",EDGE,"E6.41.4"),sQuery(id+"F0.wireOp",EDGE,"E6.42.1"),sQuery(id+"F0.wireOp",EDGE,"E6.42.2"),sQuery(id+"F0.wireOp",EDGE,"E6.42.3"),sQuery(id+"F0.wireOp",EDGE,"E6.42.4"),sQuery(id+"F0.wireOp",EDGE,"E6.43.1"),sQuery(id+"F0.wireOp",EDGE,"E6.43.2"),sQuery(id+"F0.wireOp",EDGE,"E6.43.3"),sQuery(id+"F0.wireOp",EDGE,"E6.43.4"),sQuery(id+"F0.wireOp",EDGE,"E7"),sQuery(id+"F0.wireOp",EDGE,"E8.1.0"),sQuery(id+"F0.wireOp",EDGE,"E8.2.0"),sQuery(id+"F0.wireOp",EDGE,"E8.3.0"),sQuery(id+"F0.wireOp",EDGE,"E8.4.0"),sQuery(id+"F0.wireOp",EDGE,"E8.5.0"),sQuery(id+"F0.wireOp",EDGE,"E8.6.0"),sQuery(id+"F0.wireOp",EDGE,"E8.7.0"),sQuery(id+"F0.wireOp",EDGE,"E8.8.0"),sQuery(id+"F0.wireOp",EDGE,"E8.9.0"),sQuery(id+"F0.wireOp",EDGE,"E8.10.0"),sQuery(id+"F0.wireOp",EDGE,"E8.11.0"),sQuery(id+"F0.wireOp",EDGE,"E8.12.0"),sQuery(id+"F0.wireOp",EDGE,"E8.13.0"),sQuery(id+"F0.wireOp",EDGE,"E8.14.0"),sQuery(id+"F0.wireOp",EDGE,"E8.15.0"),sQuery(id+"F0.wireOp",EDGE,"E8.16.0"),sQuery(id+"F0.wireOp",EDGE,"E8.17.0"),sQuery(id+"F0.wireOp",EDGE,"E8.18.0"),sQuery(id+"F0.wireOp",EDGE,"E8.19.0"),sQuery(id+"F0.wireOp",EDGE,"E8.20.0"),sQuery(id+"F0.wireOp",EDGE,"E8.21.0"),sQuery(id+"F0.wireOp",EDGE,"E8.22.0"),sQuery(id+"F0.wireOp",EDGE,"E8.23.0"),sQuery(id+"F0.wireOp",EDGE,"E8.24.0"),sQuery(id+"F0.wireOp",EDGE,"E8.25.0"),sQuery(id+"F0.wireOp",EDGE,"E8.26.0"),sQuery(id+"F0.wireOp",EDGE,"E8.27.0"),sQuery(id+"F0.wireOp",EDGE,"E8.28.0"),sQuery(id+"F0.wireOp",EDGE,"E8.29.0"),sQuery(id+"F0.wireOp",EDGE,"E8.30.0"),sQuery(id+"F0.wireOp",EDGE,"E8.31.0"),sQuery(id+"F0.wireOp",EDGE,"E8.32.0"),sQuery(id+"F0.wireOp",EDGE,"E8.33.0"),sQuery(id+"F0.wireOp",EDGE,"E8.34.0"),sQuery(id+"F0.wireOp",EDGE,"E8.35.0"),sQuery(id+"F0.wireOp",EDGE,"E8.36.0"),sQuery(id+"F0.wireOp",EDGE,"E8.37.0"),sQuery(id+"F0.wireOp",EDGE,"E8.38.0"),sQuery(id+"F0.wireOp",EDGE,"E8.39.0"),sQuery(id+"F0.wireOp",EDGE,"E8.40.0"),sQuery(id+"F0.wireOp",EDGE,"E8.41.0"),sQuery(id+"F0.wireOp",EDGE,"E8.42.0"),sQuery(id+"F0.wireOp",EDGE,"E8.43.0")])],"isStart":false})],"blendedInto":[makeQuery(id+"F1.opExtrude","CAP_FACE",FACE,{"disambiguationData":[OSD([sQuery(id+"F0.wireOp",EDGE,"E0"),sQuery(id+"F0.wireOp",EDGE,"E1"),sQuery(id+"F0.wireOp",EDGE,"E2"),sQuery(id+"F0.wireOp",EDGE,"E4"),sQuery(id+"F0.wireOp",EDGE,"E5"),sQuery(id+"F0.wireOp",EDGE,"E6.1.1"),sQuery(id+"F0.wireOp",EDGE,"E6.1.2"),sQuery(id+"F0.wireOp",EDGE,"E6.1.3"),sQuery(id+"F0.wireOp",EDGE,"E6.1.4"),sQuery(id+"F0.wireOp",EDGE,"E6.2.1"),sQuery(id+"F0.wireOp",EDGE,"E6.2.2"),sQuery(id+"F0.wireOp",EDGE,"E6.2.3"),sQuery(id+"F0.wireOp",EDGE,"E6.2.4"),sQuery(id+"F0.wireOp",EDGE,"E6.3.1"),sQuery(id+"F0.wireOp",EDGE,"E6.3.2"),sQuery(id+"F0.wireOp",EDGE,"E6.3.3"),sQuery(id+"F0.wireOp",EDGE,"E6.3.4"),sQuery(id+"F0.wireOp",EDGE,"E6.4.1"),sQuery(id+"F0.wireOp",EDGE,"E6.4.2"),sQuery(id+"F0.wireOp",EDGE,"E6.4.3"),sQuery(id+"F0.wireOp",EDGE,"E6.4.4"),subQ1,sQuery(id+"F0.wireOp",EDGE,"E6.5.2"),subQ0,sQuery(id+"F0.wireOp",EDGE,"E6.5.4"),sQuery(id+"F0.wireOp",EDGE,"E6.6.1"),sQuery(id+"F0.wireOp",EDGE,"E6.6.2"),sQuery(id+"F0.wireOp",EDGE,"E6.6.3"),sQuery(id+"F0.wireOp",EDGE,"E6.6.4"),sQuery(id+"F0.wireOp",EDGE,"E6.7.1"),sQuery(id+"F0.wireOp",EDGE,"E6.7.2"),sQuery(id+"F0.wireOp",EDGE,"E6.7.3"),sQuery(id+"F0.wireOp",EDGE,"E6.7.4"),sQuery(id+"F0.wireOp",EDGE,"E6.8.1"),sQuery(id+"F0.wireOp",EDGE,"E6.8.2"),sQuery(id+"F0.wireOp",EDGE,"E6.8.3"),sQuery(id+"F0.wireOp",EDGE,"E6.8.4"),sQuery(id+"F0.wireOp",EDGE,"E6.9.1"),sQuery(id+"F0.wireOp",EDGE,"E6.9.2"),sQuery(id+"F0.wireOp",EDGE,"E6.9.3"),sQuery(id+"F0.wireOp",EDGE,"E6.9.4"),sQuery(id+"F0.wireOp",EDGE,"E6.10.1"),sQuery(id+"F0.wireOp",EDGE,"E6.10.2"),sQuery(id+"F0.wireOp",EDGE,"E6.10.3"),sQuery(id+"F0.wireOp",EDGE,"E6.10.4"),sQuery(id+"F0.wireOp",EDGE,"E6.11.1"),sQuery(id+"F0.wireOp",EDGE,"E6.11.2"),sQuery(id+"F0.wireOp",EDGE,"E6.11.3"),sQuery(id+"F0.wireOp",EDGE,"E6.11.4"),sQuery(id+"F0.wireOp",EDGE,"E6.12.1"),sQuery(id+"F0.wireOp",EDGE,"E6.12.2"),sQuery(id+"F0.wireOp",EDGE,"E6.12.3"),sQuery(id+"F0.wireOp",EDGE,"E6.12.4"),sQuery(id+"F0.wireOp",EDGE,"E6.13.1"),sQuery(id+"F0.wireOp",EDGE,"E6.13.2"),sQuery(id+"F0.wireOp",EDGE,"E6.13.3"),sQuery(id+"F0.wireOp",EDGE,"E6.13.4"),sQuery(id+"F0.wireOp",EDGE,"E6.14.1"),sQuery(id+"F0.wireOp",EDGE,"E6.14.2"),sQuery(id+"F0.wireOp",EDGE,"E6.14.3"),sQuery(id+"F0.wireOp",EDGE,"E6.14.4"),sQuery(id+"F0.wireOp",EDGE,"E6.15.1"),sQuery(id+"F0.wireOp",EDGE,"E6.15.2"),sQuery(id+"F0.wireOp",EDGE,"E6.15.3"),sQuery(id+"F0.wireOp",EDGE,"E6.15.4"),sQuery(id+"F0.wireOp",EDGE,"E6.16.1"),sQuery(id+"F0.wireOp",EDGE,"E6.16.2"),sQuery(id+"F0.wireOp",EDGE,"E6.16.3"),sQuery(id+"F0.wireOp",EDGE,"E6.16.4"),sQuery(id+"F0.wireOp",EDGE,"E6.17.1"),sQuery(id+"F0.wireOp",EDGE,"E6.17.2"),sQuery(id+"F0.wireOp",EDGE,"E6.17.3"),sQuery(id+"F0.wireOp",EDGE,"E6.17.4"),sQuery(id+"F0.wireOp",EDGE,"E6.18.1"),sQuery(id+"F0.wireOp",EDGE,"E6.18.2"),sQuery(id+"F0.wireOp",EDGE,"E6.18.3"),sQuery(id+"F0.wireOp",EDGE,"E6.18.4"),sQuery(id+"F0.wireOp",EDGE,"E6.19.1"),sQuery(id+"F0.wireOp",EDGE,"E6.19.2"),sQuery(id+"F0.wireOp",EDGE,"E6.19.3"),sQuery(id+"F0.wireOp",EDGE,"E6.19.4"),sQuery(id+"F0.wireOp",EDGE,"E6.20.1"),sQuery(id+"F0.wireOp",EDGE,"E6.20.2"),sQuery(id+"F0.wireOp",EDGE,"E6.20.3"),sQuery(id+"F0.wireOp",EDGE,"E6.20.4"),sQuery(id+"F0.wireOp",EDGE,"E6.21.1"),sQuery(id+"F0.wireOp",EDGE,"E6.21.2"),sQuery(id+"F0.wireOp",EDGE,"E6.21.3"),sQuery(id+"F0.wireOp",EDGE,"E6.21.4"),sQuery(id+"F0.wireOp",EDGE,"E6.22.1"),sQuery(id+"F0.wireOp",EDGE,"E6.22.2"),sQuery(id+"F0.wireOp",EDGE,"E6.22.3"),sQuery(id+"F0.wireOp",EDGE,"E6.22.4"),sQuery(id+"F0.wireOp",EDGE,"E6.23.1"),sQuery(id+"F0.wireOp",EDGE,"E6.23.2"),sQuery(id+"F0.wireOp",EDGE,"E6.23.3"),sQuery(id+"F0.wireOp",EDGE,"E6.23.4"),sQuery(id+"F0.wireOp",EDGE,"E6.24.1"),sQuery(id+"F0.wireOp",EDGE,"E6.24.2"),sQuery(id+"F0.wireOp",EDGE,"E6.24.3"),sQuery(id+"F0.wireOp",EDGE,"E6.24.4"),sQuery(id+"F0.wireOp",EDGE,"E6.25.1"),sQuery(id+"F0.wireOp",EDGE,"E6.25.2"),sQuery(id+"F0.wireOp",EDGE,"E6.25.3"),sQuery(id+"F0.wireOp",EDGE,"E6.25.4"),sQuery(id+"F0.wireOp",EDGE,"E6.26.1"),sQuery(id+"F0.wireOp",EDGE,"E6.26.2"),sQuery(id+"F0.wireOp",EDGE,"E6.26.3"),sQuery(id+"F0.wireOp",EDGE,"E6.26.4"),sQuery(id+"F0.wireOp",EDGE,"E6.27.1"),sQuery(id+"F0.wireOp",EDGE,"E6.27.2"),sQuery(id+"F0.wireOp",EDGE,"E6.27.3"),sQuery(id+"F0.wireOp",EDGE,"E6.27.4"),sQuery(id+"F0.wireOp",EDGE,"E6.28.1"),sQuery(id+"F0.wireOp",EDGE,"E6.28.2"),sQuery(id+"F0.wireOp",EDGE,"E6.28.3"),sQuery(id+"F0.wireOp",EDGE,"E6.28.4"),sQuery(id+"F0.wireOp",EDGE,"E6.29.1"),sQuery(id+"F0.wireOp",EDGE,"E6.29.2"),sQuery(id+"F0.wireOp",EDGE,"E6.29.3"),sQuery(id+"F0.wireOp",EDGE,"E6.29.4"),sQuery(id+"F0.wireOp",EDGE,"E6.30.1"),sQuery(id+"F0.wireOp",EDGE,"E6.30.2"),sQuery(id+"F0.wireOp",EDGE,"E6.30.3"),sQuery(id+"F0.wireOp",EDGE,"E6.30.4"),sQuery(id+"F0.wireOp",EDGE,"E6.31.1"),sQuery(id+"F0.wireOp",EDGE,"E6.31.2"),sQuery(id+"F0.wireOp",EDGE,"E6.31.3"),sQuery(id+"F0.wireOp",EDGE,"E6.31.4"),sQuery(id+"F0.wireOp",EDGE,"E6.32.1"),sQuery(id+"F0.wireOp",EDGE,"E6.32.2"),sQuery(id+"F0.wireOp",EDGE,"E6.32.3"),sQuery(id+"F0.wireOp",EDGE,"E6.32.4"),sQuery(id+"F0.wireOp",EDGE,"E6.33.1"),sQuery(id+"F0.wireOp",EDGE,"E6.33.2"),sQuery(id+"F0.wireOp",EDGE,"E6.33.3"),sQuery(id+"F0.wireOp",EDGE,"E6.33.4"),sQuery(id+"F0.wireOp",EDGE,"E6.34.1"),sQuery(id+"F0.wireOp",EDGE,"E6.34.2"),sQuery(id+"F0.wireOp",EDGE,"E6.34.3"),sQuery(id+"F0.wireOp",EDGE,"E6.34.4"),sQuery(id+"F0.wireOp",EDGE,"E6.35.1"),sQuery(id+"F0.wireOp",EDGE,"E6.35.2"),sQuery(id+"F0.wireOp",EDGE,"E6.35.3"),sQuery(id+"F0.wireOp",EDGE,"E6.35.4"),sQuery(id+"F0.wireOp",EDGE,"E6.36.1"),sQuery(id+"F0.wireOp",EDGE,"E6.36.2"),sQuery(id+"F0.wireOp",EDGE,"E6.36.3"),sQuery(id+"F0.wireOp",EDGE,"E6.36.4"),sQuery(id+"F0.wireOp",EDGE,"E6.37.1"),sQuery(id+"F0.wireOp",EDGE,"E6.37.2"),sQuery(id+"F0.wireOp",EDGE,"E6.37.3"),sQuery(id+"F0.wireOp",EDGE,"E6.37.4"),sQuery(id+"F0.wireOp",EDGE,"E6.38.1"),sQuery(id+"F0.wireOp",EDGE,"E6.38.2"),sQuery(id+"F0.wireOp",EDGE,"E6.38.3"),sQuery(id+"F0.wireOp",EDGE,"E6.38.4"),sQuery(id+"F0.wireOp",EDGE,"E6.39.1"),sQuery(id+"F0.wireOp",EDGE,"E6.39.2"),sQuery(id+"F0.wireOp",EDGE,"E6.39.3"),sQuery(id+"F0.wireOp",EDGE,"E6.39.4"),sQuery(id+"F0.wireOp",EDGE,"E6.40.1"),sQuery(id+"F0.wireOp",EDGE,"E6.40.2"),sQuery(id+"F0.wireOp",EDGE,"E6.40.3"),sQuery(id+"F0.wireOp",EDGE,"E6.40.4"),sQuery(id+"F0.wireOp",EDGE,"E6.41.1"),sQuery(id+"F0.wireOp",EDGE,"E6.41.2"),sQuery(id+"F0.wireOp",EDGE,"E6.41.3"),sQuery(id+"F0.wireOp",EDGE,"E6.41.4"),sQuery(id+"F0.wireOp",EDGE,"E6.42.1"),sQuery(id+"F0.wireOp",EDGE,"E6.42.2"),sQuery(id+"F0.wireOp",EDGE,"E6.42.3"),sQuery(id+"F0.wireOp",EDGE,"E6.42.4"),sQuery(id+"F0.wireOp",EDGE,"E6.43.1"),sQuery(id+"F0.wireOp",EDGE,"E6.43.2"),sQuery(id+"F0.wireOp",EDGE,"E6.43.3"),sQuery(id+"F0.wireOp",EDGE,"E6.43.4"),sQuery(id+"F0.wireOp",EDGE,"E7"),sQuery(id+"F0.wireOp",EDGE,"E8.1.0"),sQuery(id+"F0.wireOp",EDGE,"E8.2.0"),sQuery(id+"F0.wireOp",EDGE,"E8.3.0"),sQuery(id+"F0.wireOp",EDGE,"E8.4.0"),sQuery(id+"F0.wireOp",EDGE,"E8.5.0"),sQuery(id+"F0.wireOp",EDGE,"E8.6.0"),sQuery(id+"F0.wireOp",EDGE,"E8.7.0"),sQuery(id+"F0.wireOp",EDGE,"E8.8.0"),sQuery(id+"F0.wireOp",EDGE,"E8.9.0"),sQuery(id+"F0.wireOp",EDGE,"E8.10.0"),sQuery(id+"F0.wireOp",EDGE,"E8.11.0"),sQuery(id+"F0.wireOp",EDGE,"E8.12.0"),sQuery(id+"F0.wireOp",EDGE,"E8.13.0"),sQuery(id+"F0.wireOp",EDGE,"E8.14.0"),sQuery(id+"F0.wireOp",EDGE,"E8.15.0"),sQuery(id+"F0.wireOp",EDGE,"E8.16.0"),sQuery(id+"F0.wireOp",EDGE,"E8.17.0"),sQuery(id+"F0.wireOp",EDGE,"E8.18.0"),sQuery(id+"F0.wireOp",EDGE,"E8.19.0"),sQuery(id+"F0.wireOp",EDGE,"E8.20.0"),sQuery(id+"F0.wireOp",EDGE,"E8.21.0"),sQuery(id+"F0.wireOp",EDGE,"E8.22.0"),sQuery(id+"F0.wireOp",EDGE,"E8.23.0"),sQuery(id+"F0.wireOp",EDGE,"E8.24.0"),sQuery(id+"F0.wireOp",EDGE,"E8.25.0"),sQuery(id+"F0.wireOp",EDGE,"E8.26.0"),sQuery(id+"F0.wireOp",EDGE,"E8.27.0"),sQuery(id+"F0.wireOp",EDGE,"E8.28.0"),sQuery(id+"F0.wireOp",EDGE,"E8.29.0"),sQuery(id+"F0.wireOp",EDGE,"E8.30.0"),sQuery(id+"F0.wireOp",EDGE,"E8.31.0"),sQuery(id+"F0.wireOp",EDGE,"E8.32.0"),sQuery(id+"F0.wireOp",EDGE,"E8.33.0"),sQuery(id+"F0.wireOp",EDGE,"E8.34.0"),sQuery(id+"F0.wireOp",EDGE,"E8.35.0"),sQuery(id+"F0.wireOp",EDGE,"E8.36.0"),sQuery(id+"F0.wireOp",EDGE,"E8.37.0"),sQuery(id+"F0.wireOp",EDGE,"E8.38.0"),sQuery(id+"F0.wireOp",EDGE,"E8.39.0"),sQuery(id+"F0.wireOp",EDGE,"E8.40.0"),sQuery(id+"F0.wireOp",EDGE,"E8.41.0"),sQuery(id+"F0.wireOp",EDGE,"E8.42.0"),sQuery(id+"F0.wireOp",EDGE,"E8.43.0")])],"isStart":false})]});}
            var Q14;
            {var subQ0=sQuery(id+"F0.wireOp",EDGE,"E6.7.3");var subQ1=sQuery(id+"F0.wireOp",EDGE,"E6.7.1");Q14=makeQuery(id+"F2.opFillet","BLEND_EDGE",EDGE,{"blendedFrom":[makeQuery(id+"F1.opExtrude","SWEPT_EDGE",EDGE,{"disambiguationData":[OSD([sQuery(id+"F0.wireOp",EDGE,"E6.7.0"),subQ1,subQ0])]}),makeQuery(id+"F1.opExtrude","CAP_FACE",FACE,{"disambiguationData":[OSD([sQuery(id+"F0.wireOp",EDGE,"E0"),sQuery(id+"F0.wireOp",EDGE,"E1"),sQuery(id+"F0.wireOp",EDGE,"E2"),sQuery(id+"F0.wireOp",EDGE,"E4"),sQuery(id+"F0.wireOp",EDGE,"E5"),sQuery(id+"F0.wireOp",EDGE,"E6.1.1"),sQuery(id+"F0.wireOp",EDGE,"E6.1.2"),sQuery(id+"F0.wireOp",EDGE,"E6.1.3"),sQuery(id+"F0.wireOp",EDGE,"E6.1.4"),sQuery(id+"F0.wireOp",EDGE,"E6.2.1"),sQuery(id+"F0.wireOp",EDGE,"E6.2.2"),sQuery(id+"F0.wireOp",EDGE,"E6.2.3"),sQuery(id+"F0.wireOp",EDGE,"E6.2.4"),sQuery(id+"F0.wireOp",EDGE,"E6.3.1"),sQuery(id+"F0.wireOp",EDGE,"E6.3.2"),sQuery(id+"F0.wireOp",EDGE,"E6.3.3"),sQuery(id+"F0.wireOp",EDGE,"E6.3.4"),sQuery(id+"F0.wireOp",EDGE,"E6.4.1"),sQuery(id+"F0.wireOp",EDGE,"E6.4.2"),sQuery(id+"F0.wireOp",EDGE,"E6.4.3"),sQuery(id+"F0.wireOp",EDGE,"E6.4.4"),sQuery(id+"F0.wireOp",EDGE,"E6.5.1"),sQuery(id+"F0.wireOp",EDGE,"E6.5.2"),sQuery(id+"F0.wireOp",EDGE,"E6.5.3"),sQuery(id+"F0.wireOp",EDGE,"E6.5.4"),sQuery(id+"F0.wireOp",EDGE,"E6.6.1"),sQuery(id+"F0.wireOp",EDGE,"E6.6.2"),sQuery(id+"F0.wireOp",EDGE,"E6.6.3"),sQuery(id+"F0.wireOp",EDGE,"E6.6.4"),subQ1,sQuery(id+"F0.wireOp",EDGE,"E6.7.2"),subQ0,sQuery(id+"F0.wireOp",EDGE,"E6.7.4"),sQuery(id+"F0.wireOp",EDGE,"E6.8.1"),sQuery(id+"F0.wireOp",EDGE,"E6.8.2"),sQuery(id+"F0.wireOp",EDGE,"E6.8.3"),sQuery(id+"F0.wireOp",EDGE,"E6.8.4"),sQuery(id+"F0.wireOp",EDGE,"E6.9.1"),sQuery(id+"F0.wireOp",EDGE,"E6.9.2"),sQuery(id+"F0.wireOp",EDGE,"E6.9.3"),sQuery(id+"F0.wireOp",EDGE,"E6.9.4"),sQuery(id+"F0.wireOp",EDGE,"E6.10.1"),sQuery(id+"F0.wireOp",EDGE,"E6.10.2"),sQuery(id+"F0.wireOp",EDGE,"E6.10.3"),sQuery(id+"F0.wireOp",EDGE,"E6.10.4"),sQuery(id+"F0.wireOp",EDGE,"E6.11.1"),sQuery(id+"F0.wireOp",EDGE,"E6.11.2"),sQuery(id+"F0.wireOp",EDGE,"E6.11.3"),sQuery(id+"F0.wireOp",EDGE,"E6.11.4"),sQuery(id+"F0.wireOp",EDGE,"E6.12.1"),sQuery(id+"F0.wireOp",EDGE,"E6.12.2"),sQuery(id+"F0.wireOp",EDGE,"E6.12.3"),sQuery(id+"F0.wireOp",EDGE,"E6.12.4"),sQuery(id+"F0.wireOp",EDGE,"E6.13.1"),sQuery(id+"F0.wireOp",EDGE,"E6.13.2"),sQuery(id+"F0.wireOp",EDGE,"E6.13.3"),sQuery(id+"F0.wireOp",EDGE,"E6.13.4"),sQuery(id+"F0.wireOp",EDGE,"E6.14.1"),sQuery(id+"F0.wireOp",EDGE,"E6.14.2"),sQuery(id+"F0.wireOp",EDGE,"E6.14.3"),sQuery(id+"F0.wireOp",EDGE,"E6.14.4"),sQuery(id+"F0.wireOp",EDGE,"E6.15.1"),sQuery(id+"F0.wireOp",EDGE,"E6.15.2"),sQuery(id+"F0.wireOp",EDGE,"E6.15.3"),sQuery(id+"F0.wireOp",EDGE,"E6.15.4"),sQuery(id+"F0.wireOp",EDGE,"E6.16.1"),sQuery(id+"F0.wireOp",EDGE,"E6.16.2"),sQuery(id+"F0.wireOp",EDGE,"E6.16.3"),sQuery(id+"F0.wireOp",EDGE,"E6.16.4"),sQuery(id+"F0.wireOp",EDGE,"E6.17.1"),sQuery(id+"F0.wireOp",EDGE,"E6.17.2"),sQuery(id+"F0.wireOp",EDGE,"E6.17.3"),sQuery(id+"F0.wireOp",EDGE,"E6.17.4"),sQuery(id+"F0.wireOp",EDGE,"E6.18.1"),sQuery(id+"F0.wireOp",EDGE,"E6.18.2"),sQuery(id+"F0.wireOp",EDGE,"E6.18.3"),sQuery(id+"F0.wireOp",EDGE,"E6.18.4"),sQuery(id+"F0.wireOp",EDGE,"E6.19.1"),sQuery(id+"F0.wireOp",EDGE,"E6.19.2"),sQuery(id+"F0.wireOp",EDGE,"E6.19.3"),sQuery(id+"F0.wireOp",EDGE,"E6.19.4"),sQuery(id+"F0.wireOp",EDGE,"E6.20.1"),sQuery(id+"F0.wireOp",EDGE,"E6.20.2"),sQuery(id+"F0.wireOp",EDGE,"E6.20.3"),sQuery(id+"F0.wireOp",EDGE,"E6.20.4"),sQuery(id+"F0.wireOp",EDGE,"E6.21.1"),sQuery(id+"F0.wireOp",EDGE,"E6.21.2"),sQuery(id+"F0.wireOp",EDGE,"E6.21.3"),sQuery(id+"F0.wireOp",EDGE,"E6.21.4"),sQuery(id+"F0.wireOp",EDGE,"E6.22.1"),sQuery(id+"F0.wireOp",EDGE,"E6.22.2"),sQuery(id+"F0.wireOp",EDGE,"E6.22.3"),sQuery(id+"F0.wireOp",EDGE,"E6.22.4"),sQuery(id+"F0.wireOp",EDGE,"E6.23.1"),sQuery(id+"F0.wireOp",EDGE,"E6.23.2"),sQuery(id+"F0.wireOp",EDGE,"E6.23.3"),sQuery(id+"F0.wireOp",EDGE,"E6.23.4"),sQuery(id+"F0.wireOp",EDGE,"E6.24.1"),sQuery(id+"F0.wireOp",EDGE,"E6.24.2"),sQuery(id+"F0.wireOp",EDGE,"E6.24.3"),sQuery(id+"F0.wireOp",EDGE,"E6.24.4"),sQuery(id+"F0.wireOp",EDGE,"E6.25.1"),sQuery(id+"F0.wireOp",EDGE,"E6.25.2"),sQuery(id+"F0.wireOp",EDGE,"E6.25.3"),sQuery(id+"F0.wireOp",EDGE,"E6.25.4"),sQuery(id+"F0.wireOp",EDGE,"E6.26.1"),sQuery(id+"F0.wireOp",EDGE,"E6.26.2"),sQuery(id+"F0.wireOp",EDGE,"E6.26.3"),sQuery(id+"F0.wireOp",EDGE,"E6.26.4"),sQuery(id+"F0.wireOp",EDGE,"E6.27.1"),sQuery(id+"F0.wireOp",EDGE,"E6.27.2"),sQuery(id+"F0.wireOp",EDGE,"E6.27.3"),sQuery(id+"F0.wireOp",EDGE,"E6.27.4"),sQuery(id+"F0.wireOp",EDGE,"E6.28.1"),sQuery(id+"F0.wireOp",EDGE,"E6.28.2"),sQuery(id+"F0.wireOp",EDGE,"E6.28.3"),sQuery(id+"F0.wireOp",EDGE,"E6.28.4"),sQuery(id+"F0.wireOp",EDGE,"E6.29.1"),sQuery(id+"F0.wireOp",EDGE,"E6.29.2"),sQuery(id+"F0.wireOp",EDGE,"E6.29.3"),sQuery(id+"F0.wireOp",EDGE,"E6.29.4"),sQuery(id+"F0.wireOp",EDGE,"E6.30.1"),sQuery(id+"F0.wireOp",EDGE,"E6.30.2"),sQuery(id+"F0.wireOp",EDGE,"E6.30.3"),sQuery(id+"F0.wireOp",EDGE,"E6.30.4"),sQuery(id+"F0.wireOp",EDGE,"E6.31.1"),sQuery(id+"F0.wireOp",EDGE,"E6.31.2"),sQuery(id+"F0.wireOp",EDGE,"E6.31.3"),sQuery(id+"F0.wireOp",EDGE,"E6.31.4"),sQuery(id+"F0.wireOp",EDGE,"E6.32.1"),sQuery(id+"F0.wireOp",EDGE,"E6.32.2"),sQuery(id+"F0.wireOp",EDGE,"E6.32.3"),sQuery(id+"F0.wireOp",EDGE,"E6.32.4"),sQuery(id+"F0.wireOp",EDGE,"E6.33.1"),sQuery(id+"F0.wireOp",EDGE,"E6.33.2"),sQuery(id+"F0.wireOp",EDGE,"E6.33.3"),sQuery(id+"F0.wireOp",EDGE,"E6.33.4"),sQuery(id+"F0.wireOp",EDGE,"E6.34.1"),sQuery(id+"F0.wireOp",EDGE,"E6.34.2"),sQuery(id+"F0.wireOp",EDGE,"E6.34.3"),sQuery(id+"F0.wireOp",EDGE,"E6.34.4"),sQuery(id+"F0.wireOp",EDGE,"E6.35.1"),sQuery(id+"F0.wireOp",EDGE,"E6.35.2"),sQuery(id+"F0.wireOp",EDGE,"E6.35.3"),sQuery(id+"F0.wireOp",EDGE,"E6.35.4"),sQuery(id+"F0.wireOp",EDGE,"E6.36.1"),sQuery(id+"F0.wireOp",EDGE,"E6.36.2"),sQuery(id+"F0.wireOp",EDGE,"E6.36.3"),sQuery(id+"F0.wireOp",EDGE,"E6.36.4"),sQuery(id+"F0.wireOp",EDGE,"E6.37.1"),sQuery(id+"F0.wireOp",EDGE,"E6.37.2"),sQuery(id+"F0.wireOp",EDGE,"E6.37.3"),sQuery(id+"F0.wireOp",EDGE,"E6.37.4"),sQuery(id+"F0.wireOp",EDGE,"E6.38.1"),sQuery(id+"F0.wireOp",EDGE,"E6.38.2"),sQuery(id+"F0.wireOp",EDGE,"E6.38.3"),sQuery(id+"F0.wireOp",EDGE,"E6.38.4"),sQuery(id+"F0.wireOp",EDGE,"E6.39.1"),sQuery(id+"F0.wireOp",EDGE,"E6.39.2"),sQuery(id+"F0.wireOp",EDGE,"E6.39.3"),sQuery(id+"F0.wireOp",EDGE,"E6.39.4"),sQuery(id+"F0.wireOp",EDGE,"E6.40.1"),sQuery(id+"F0.wireOp",EDGE,"E6.40.2"),sQuery(id+"F0.wireOp",EDGE,"E6.40.3"),sQuery(id+"F0.wireOp",EDGE,"E6.40.4"),sQuery(id+"F0.wireOp",EDGE,"E6.41.1"),sQuery(id+"F0.wireOp",EDGE,"E6.41.2"),sQuery(id+"F0.wireOp",EDGE,"E6.41.3"),sQuery(id+"F0.wireOp",EDGE,"E6.41.4"),sQuery(id+"F0.wireOp",EDGE,"E6.42.1"),sQuery(id+"F0.wireOp",EDGE,"E6.42.2"),sQuery(id+"F0.wireOp",EDGE,"E6.42.3"),sQuery(id+"F0.wireOp",EDGE,"E6.42.4"),sQuery(id+"F0.wireOp",EDGE,"E6.43.1"),sQuery(id+"F0.wireOp",EDGE,"E6.43.2"),sQuery(id+"F0.wireOp",EDGE,"E6.43.3"),sQuery(id+"F0.wireOp",EDGE,"E6.43.4"),sQuery(id+"F0.wireOp",EDGE,"E7"),sQuery(id+"F0.wireOp",EDGE,"E8.1.0"),sQuery(id+"F0.wireOp",EDGE,"E8.2.0"),sQuery(id+"F0.wireOp",EDGE,"E8.3.0"),sQuery(id+"F0.wireOp",EDGE,"E8.4.0"),sQuery(id+"F0.wireOp",EDGE,"E8.5.0"),sQuery(id+"F0.wireOp",EDGE,"E8.6.0"),sQuery(id+"F0.wireOp",EDGE,"E8.7.0"),sQuery(id+"F0.wireOp",EDGE,"E8.8.0"),sQuery(id+"F0.wireOp",EDGE,"E8.9.0"),sQuery(id+"F0.wireOp",EDGE,"E8.10.0"),sQuery(id+"F0.wireOp",EDGE,"E8.11.0"),sQuery(id+"F0.wireOp",EDGE,"E8.12.0"),sQuery(id+"F0.wireOp",EDGE,"E8.13.0"),sQuery(id+"F0.wireOp",EDGE,"E8.14.0"),sQuery(id+"F0.wireOp",EDGE,"E8.15.0"),sQuery(id+"F0.wireOp",EDGE,"E8.16.0"),sQuery(id+"F0.wireOp",EDGE,"E8.17.0"),sQuery(id+"F0.wireOp",EDGE,"E8.18.0"),sQuery(id+"F0.wireOp",EDGE,"E8.19.0"),sQuery(id+"F0.wireOp",EDGE,"E8.20.0"),sQuery(id+"F0.wireOp",EDGE,"E8.21.0"),sQuery(id+"F0.wireOp",EDGE,"E8.22.0"),sQuery(id+"F0.wireOp",EDGE,"E8.23.0"),sQuery(id+"F0.wireOp",EDGE,"E8.24.0"),sQuery(id+"F0.wireOp",EDGE,"E8.25.0"),sQuery(id+"F0.wireOp",EDGE,"E8.26.0"),sQuery(id+"F0.wireOp",EDGE,"E8.27.0"),sQuery(id+"F0.wireOp",EDGE,"E8.28.0"),sQuery(id+"F0.wireOp",EDGE,"E8.29.0"),sQuery(id+"F0.wireOp",EDGE,"E8.30.0"),sQuery(id+"F0.wireOp",EDGE,"E8.31.0"),sQuery(id+"F0.wireOp",EDGE,"E8.32.0"),sQuery(id+"F0.wireOp",EDGE,"E8.33.0"),sQuery(id+"F0.wireOp",EDGE,"E8.34.0"),sQuery(id+"F0.wireOp",EDGE,"E8.35.0"),sQuery(id+"F0.wireOp",EDGE,"E8.36.0"),sQuery(id+"F0.wireOp",EDGE,"E8.37.0"),sQuery(id+"F0.wireOp",EDGE,"E8.38.0"),sQuery(id+"F0.wireOp",EDGE,"E8.39.0"),sQuery(id+"F0.wireOp",EDGE,"E8.40.0"),sQuery(id+"F0.wireOp",EDGE,"E8.41.0"),sQuery(id+"F0.wireOp",EDGE,"E8.42.0"),sQuery(id+"F0.wireOp",EDGE,"E8.43.0")])],"isStart":false})],"blendedInto":[makeQuery(id+"F1.opExtrude","CAP_FACE",FACE,{"disambiguationData":[OSD([sQuery(id+"F0.wireOp",EDGE,"E0"),sQuery(id+"F0.wireOp",EDGE,"E1"),sQuery(id+"F0.wireOp",EDGE,"E2"),sQuery(id+"F0.wireOp",EDGE,"E4"),sQuery(id+"F0.wireOp",EDGE,"E5"),sQuery(id+"F0.wireOp",EDGE,"E6.1.1"),sQuery(id+"F0.wireOp",EDGE,"E6.1.2"),sQuery(id+"F0.wireOp",EDGE,"E6.1.3"),sQuery(id+"F0.wireOp",EDGE,"E6.1.4"),sQuery(id+"F0.wireOp",EDGE,"E6.2.1"),sQuery(id+"F0.wireOp",EDGE,"E6.2.2"),sQuery(id+"F0.wireOp",EDGE,"E6.2.3"),sQuery(id+"F0.wireOp",EDGE,"E6.2.4"),sQuery(id+"F0.wireOp",EDGE,"E6.3.1"),sQuery(id+"F0.wireOp",EDGE,"E6.3.2"),sQuery(id+"F0.wireOp",EDGE,"E6.3.3"),sQuery(id+"F0.wireOp",EDGE,"E6.3.4"),sQuery(id+"F0.wireOp",EDGE,"E6.4.1"),sQuery(id+"F0.wireOp",EDGE,"E6.4.2"),sQuery(id+"F0.wireOp",EDGE,"E6.4.3"),sQuery(id+"F0.wireOp",EDGE,"E6.4.4"),sQuery(id+"F0.wireOp",EDGE,"E6.5.1"),sQuery(id+"F0.wireOp",EDGE,"E6.5.2"),sQuery(id+"F0.wireOp",EDGE,"E6.5.3"),sQuery(id+"F0.wireOp",EDGE,"E6.5.4"),sQuery(id+"F0.wireOp",EDGE,"E6.6.1"),sQuery(id+"F0.wireOp",EDGE,"E6.6.2"),sQuery(id+"F0.wireOp",EDGE,"E6.6.3"),sQuery(id+"F0.wireOp",EDGE,"E6.6.4"),subQ1,sQuery(id+"F0.wireOp",EDGE,"E6.7.2"),subQ0,sQuery(id+"F0.wireOp",EDGE,"E6.7.4"),sQuery(id+"F0.wireOp",EDGE,"E6.8.1"),sQuery(id+"F0.wireOp",EDGE,"E6.8.2"),sQuery(id+"F0.wireOp",EDGE,"E6.8.3"),sQuery(id+"F0.wireOp",EDGE,"E6.8.4"),sQuery(id+"F0.wireOp",EDGE,"E6.9.1"),sQuery(id+"F0.wireOp",EDGE,"E6.9.2"),sQuery(id+"F0.wireOp",EDGE,"E6.9.3"),sQuery(id+"F0.wireOp",EDGE,"E6.9.4"),sQuery(id+"F0.wireOp",EDGE,"E6.10.1"),sQuery(id+"F0.wireOp",EDGE,"E6.10.2"),sQuery(id+"F0.wireOp",EDGE,"E6.10.3"),sQuery(id+"F0.wireOp",EDGE,"E6.10.4"),sQuery(id+"F0.wireOp",EDGE,"E6.11.1"),sQuery(id+"F0.wireOp",EDGE,"E6.11.2"),sQuery(id+"F0.wireOp",EDGE,"E6.11.3"),sQuery(id+"F0.wireOp",EDGE,"E6.11.4"),sQuery(id+"F0.wireOp",EDGE,"E6.12.1"),sQuery(id+"F0.wireOp",EDGE,"E6.12.2"),sQuery(id+"F0.wireOp",EDGE,"E6.12.3"),sQuery(id+"F0.wireOp",EDGE,"E6.12.4"),sQuery(id+"F0.wireOp",EDGE,"E6.13.1"),sQuery(id+"F0.wireOp",EDGE,"E6.13.2"),sQuery(id+"F0.wireOp",EDGE,"E6.13.3"),sQuery(id+"F0.wireOp",EDGE,"E6.13.4"),sQuery(id+"F0.wireOp",EDGE,"E6.14.1"),sQuery(id+"F0.wireOp",EDGE,"E6.14.2"),sQuery(id+"F0.wireOp",EDGE,"E6.14.3"),sQuery(id+"F0.wireOp",EDGE,"E6.14.4"),sQuery(id+"F0.wireOp",EDGE,"E6.15.1"),sQuery(id+"F0.wireOp",EDGE,"E6.15.2"),sQuery(id+"F0.wireOp",EDGE,"E6.15.3"),sQuery(id+"F0.wireOp",EDGE,"E6.15.4"),sQuery(id+"F0.wireOp",EDGE,"E6.16.1"),sQuery(id+"F0.wireOp",EDGE,"E6.16.2"),sQuery(id+"F0.wireOp",EDGE,"E6.16.3"),sQuery(id+"F0.wireOp",EDGE,"E6.16.4"),sQuery(id+"F0.wireOp",EDGE,"E6.17.1"),sQuery(id+"F0.wireOp",EDGE,"E6.17.2"),sQuery(id+"F0.wireOp",EDGE,"E6.17.3"),sQuery(id+"F0.wireOp",EDGE,"E6.17.4"),sQuery(id+"F0.wireOp",EDGE,"E6.18.1"),sQuery(id+"F0.wireOp",EDGE,"E6.18.2"),sQuery(id+"F0.wireOp",EDGE,"E6.18.3"),sQuery(id+"F0.wireOp",EDGE,"E6.18.4"),sQuery(id+"F0.wireOp",EDGE,"E6.19.1"),sQuery(id+"F0.wireOp",EDGE,"E6.19.2"),sQuery(id+"F0.wireOp",EDGE,"E6.19.3"),sQuery(id+"F0.wireOp",EDGE,"E6.19.4"),sQuery(id+"F0.wireOp",EDGE,"E6.20.1"),sQuery(id+"F0.wireOp",EDGE,"E6.20.2"),sQuery(id+"F0.wireOp",EDGE,"E6.20.3"),sQuery(id+"F0.wireOp",EDGE,"E6.20.4"),sQuery(id+"F0.wireOp",EDGE,"E6.21.1"),sQuery(id+"F0.wireOp",EDGE,"E6.21.2"),sQuery(id+"F0.wireOp",EDGE,"E6.21.3"),sQuery(id+"F0.wireOp",EDGE,"E6.21.4"),sQuery(id+"F0.wireOp",EDGE,"E6.22.1"),sQuery(id+"F0.wireOp",EDGE,"E6.22.2"),sQuery(id+"F0.wireOp",EDGE,"E6.22.3"),sQuery(id+"F0.wireOp",EDGE,"E6.22.4"),sQuery(id+"F0.wireOp",EDGE,"E6.23.1"),sQuery(id+"F0.wireOp",EDGE,"E6.23.2"),sQuery(id+"F0.wireOp",EDGE,"E6.23.3"),sQuery(id+"F0.wireOp",EDGE,"E6.23.4"),sQuery(id+"F0.wireOp",EDGE,"E6.24.1"),sQuery(id+"F0.wireOp",EDGE,"E6.24.2"),sQuery(id+"F0.wireOp",EDGE,"E6.24.3"),sQuery(id+"F0.wireOp",EDGE,"E6.24.4"),sQuery(id+"F0.wireOp",EDGE,"E6.25.1"),sQuery(id+"F0.wireOp",EDGE,"E6.25.2"),sQuery(id+"F0.wireOp",EDGE,"E6.25.3"),sQuery(id+"F0.wireOp",EDGE,"E6.25.4"),sQuery(id+"F0.wireOp",EDGE,"E6.26.1"),sQuery(id+"F0.wireOp",EDGE,"E6.26.2"),sQuery(id+"F0.wireOp",EDGE,"E6.26.3"),sQuery(id+"F0.wireOp",EDGE,"E6.26.4"),sQuery(id+"F0.wireOp",EDGE,"E6.27.1"),sQuery(id+"F0.wireOp",EDGE,"E6.27.2"),sQuery(id+"F0.wireOp",EDGE,"E6.27.3"),sQuery(id+"F0.wireOp",EDGE,"E6.27.4"),sQuery(id+"F0.wireOp",EDGE,"E6.28.1"),sQuery(id+"F0.wireOp",EDGE,"E6.28.2"),sQuery(id+"F0.wireOp",EDGE,"E6.28.3"),sQuery(id+"F0.wireOp",EDGE,"E6.28.4"),sQuery(id+"F0.wireOp",EDGE,"E6.29.1"),sQuery(id+"F0.wireOp",EDGE,"E6.29.2"),sQuery(id+"F0.wireOp",EDGE,"E6.29.3"),sQuery(id+"F0.wireOp",EDGE,"E6.29.4"),sQuery(id+"F0.wireOp",EDGE,"E6.30.1"),sQuery(id+"F0.wireOp",EDGE,"E6.30.2"),sQuery(id+"F0.wireOp",EDGE,"E6.30.3"),sQuery(id+"F0.wireOp",EDGE,"E6.30.4"),sQuery(id+"F0.wireOp",EDGE,"E6.31.1"),sQuery(id+"F0.wireOp",EDGE,"E6.31.2"),sQuery(id+"F0.wireOp",EDGE,"E6.31.3"),sQuery(id+"F0.wireOp",EDGE,"E6.31.4"),sQuery(id+"F0.wireOp",EDGE,"E6.32.1"),sQuery(id+"F0.wireOp",EDGE,"E6.32.2"),sQuery(id+"F0.wireOp",EDGE,"E6.32.3"),sQuery(id+"F0.wireOp",EDGE,"E6.32.4"),sQuery(id+"F0.wireOp",EDGE,"E6.33.1"),sQuery(id+"F0.wireOp",EDGE,"E6.33.2"),sQuery(id+"F0.wireOp",EDGE,"E6.33.3"),sQuery(id+"F0.wireOp",EDGE,"E6.33.4"),sQuery(id+"F0.wireOp",EDGE,"E6.34.1"),sQuery(id+"F0.wireOp",EDGE,"E6.34.2"),sQuery(id+"F0.wireOp",EDGE,"E6.34.3"),sQuery(id+"F0.wireOp",EDGE,"E6.34.4"),sQuery(id+"F0.wireOp",EDGE,"E6.35.1"),sQuery(id+"F0.wireOp",EDGE,"E6.35.2"),sQuery(id+"F0.wireOp",EDGE,"E6.35.3"),sQuery(id+"F0.wireOp",EDGE,"E6.35.4"),sQuery(id+"F0.wireOp",EDGE,"E6.36.1"),sQuery(id+"F0.wireOp",EDGE,"E6.36.2"),sQuery(id+"F0.wireOp",EDGE,"E6.36.3"),sQuery(id+"F0.wireOp",EDGE,"E6.36.4"),sQuery(id+"F0.wireOp",EDGE,"E6.37.1"),sQuery(id+"F0.wireOp",EDGE,"E6.37.2"),sQuery(id+"F0.wireOp",EDGE,"E6.37.3"),sQuery(id+"F0.wireOp",EDGE,"E6.37.4"),sQuery(id+"F0.wireOp",EDGE,"E6.38.1"),sQuery(id+"F0.wireOp",EDGE,"E6.38.2"),sQuery(id+"F0.wireOp",EDGE,"E6.38.3"),sQuery(id+"F0.wireOp",EDGE,"E6.38.4"),sQuery(id+"F0.wireOp",EDGE,"E6.39.1"),sQuery(id+"F0.wireOp",EDGE,"E6.39.2"),sQuery(id+"F0.wireOp",EDGE,"E6.39.3"),sQuery(id+"F0.wireOp",EDGE,"E6.39.4"),sQuery(id+"F0.wireOp",EDGE,"E6.40.1"),sQuery(id+"F0.wireOp",EDGE,"E6.40.2"),sQuery(id+"F0.wireOp",EDGE,"E6.40.3"),sQuery(id+"F0.wireOp",EDGE,"E6.40.4"),sQuery(id+"F0.wireOp",EDGE,"E6.41.1"),sQuery(id+"F0.wireOp",EDGE,"E6.41.2"),sQuery(id+"F0.wireOp",EDGE,"E6.41.3"),sQuery(id+"F0.wireOp",EDGE,"E6.41.4"),sQuery(id+"F0.wireOp",EDGE,"E6.42.1"),sQuery(id+"F0.wireOp",EDGE,"E6.42.2"),sQuery(id+"F0.wireOp",EDGE,"E6.42.3"),sQuery(id+"F0.wireOp",EDGE,"E6.42.4"),sQuery(id+"F0.wireOp",EDGE,"E6.43.1"),sQuery(id+"F0.wireOp",EDGE,"E6.43.2"),sQuery(id+"F0.wireOp",EDGE,"E6.43.3"),sQuery(id+"F0.wireOp",EDGE,"E6.43.4"),sQuery(id+"F0.wireOp",EDGE,"E7"),sQuery(id+"F0.wireOp",EDGE,"E8.1.0"),sQuery(id+"F0.wireOp",EDGE,"E8.2.0"),sQuery(id+"F0.wireOp",EDGE,"E8.3.0"),sQuery(id+"F0.wireOp",EDGE,"E8.4.0"),sQuery(id+"F0.wireOp",EDGE,"E8.5.0"),sQuery(id+"F0.wireOp",EDGE,"E8.6.0"),sQuery(id+"F0.wireOp",EDGE,"E8.7.0"),sQuery(id+"F0.wireOp",EDGE,"E8.8.0"),sQuery(id+"F0.wireOp",EDGE,"E8.9.0"),sQuery(id+"F0.wireOp",EDGE,"E8.10.0"),sQuery(id+"F0.wireOp",EDGE,"E8.11.0"),sQuery(id+"F0.wireOp",EDGE,"E8.12.0"),sQuery(id+"F0.wireOp",EDGE,"E8.13.0"),sQuery(id+"F0.wireOp",EDGE,"E8.14.0"),sQuery(id+"F0.wireOp",EDGE,"E8.15.0"),sQuery(id+"F0.wireOp",EDGE,"E8.16.0"),sQuery(id+"F0.wireOp",EDGE,"E8.17.0"),sQuery(id+"F0.wireOp",EDGE,"E8.18.0"),sQuery(id+"F0.wireOp",EDGE,"E8.19.0"),sQuery(id+"F0.wireOp",EDGE,"E8.20.0"),sQuery(id+"F0.wireOp",EDGE,"E8.21.0"),sQuery(id+"F0.wireOp",EDGE,"E8.22.0"),sQuery(id+"F0.wireOp",EDGE,"E8.23.0"),sQuery(id+"F0.wireOp",EDGE,"E8.24.0"),sQuery(id+"F0.wireOp",EDGE,"E8.25.0"),sQuery(id+"F0.wireOp",EDGE,"E8.26.0"),sQuery(id+"F0.wireOp",EDGE,"E8.27.0"),sQuery(id+"F0.wireOp",EDGE,"E8.28.0"),sQuery(id+"F0.wireOp",EDGE,"E8.29.0"),sQuery(id+"F0.wireOp",EDGE,"E8.30.0"),sQuery(id+"F0.wireOp",EDGE,"E8.31.0"),sQuery(id+"F0.wireOp",EDGE,"E8.32.0"),sQuery(id+"F0.wireOp",EDGE,"E8.33.0"),sQuery(id+"F0.wireOp",EDGE,"E8.34.0"),sQuery(id+"F0.wireOp",EDGE,"E8.35.0"),sQuery(id+"F0.wireOp",EDGE,"E8.36.0"),sQuery(id+"F0.wireOp",EDGE,"E8.37.0"),sQuery(id+"F0.wireOp",EDGE,"E8.38.0"),sQuery(id+"F0.wireOp",EDGE,"E8.39.0"),sQuery(id+"F0.wireOp",EDGE,"E8.40.0"),sQuery(id+"F0.wireOp",EDGE,"E8.41.0"),sQuery(id+"F0.wireOp",EDGE,"E8.42.0"),sQuery(id+"F0.wireOp",EDGE,"E8.43.0")])],"isStart":false})]});}
            var Q15;
            {var subQ0=sQuery(id+"F0.wireOp",EDGE,"E6.9.3");var subQ1=sQuery(id+"F0.wireOp",EDGE,"E6.9.1");Q15=makeQuery(id+"F2.opFillet","BLEND_EDGE",EDGE,{"blendedFrom":[makeQuery(id+"F1.opExtrude","SWEPT_EDGE",EDGE,{"disambiguationData":[OSD([sQuery(id+"F0.wireOp",EDGE,"E6.9.0"),subQ1,subQ0])]}),makeQuery(id+"F1.opExtrude","CAP_FACE",FACE,{"disambiguationData":[OSD([sQuery(id+"F0.wireOp",EDGE,"E0"),sQuery(id+"F0.wireOp",EDGE,"E1"),sQuery(id+"F0.wireOp",EDGE,"E2"),sQuery(id+"F0.wireOp",EDGE,"E4"),sQuery(id+"F0.wireOp",EDGE,"E5"),sQuery(id+"F0.wireOp",EDGE,"E6.1.1"),sQuery(id+"F0.wireOp",EDGE,"E6.1.2"),sQuery(id+"F0.wireOp",EDGE,"E6.1.3"),sQuery(id+"F0.wireOp",EDGE,"E6.1.4"),sQuery(id+"F0.wireOp",EDGE,"E6.2.1"),sQuery(id+"F0.wireOp",EDGE,"E6.2.2"),sQuery(id+"F0.wireOp",EDGE,"E6.2.3"),sQuery(id+"F0.wireOp",EDGE,"E6.2.4"),sQuery(id+"F0.wireOp",EDGE,"E6.3.1"),sQuery(id+"F0.wireOp",EDGE,"E6.3.2"),sQuery(id+"F0.wireOp",EDGE,"E6.3.3"),sQuery(id+"F0.wireOp",EDGE,"E6.3.4"),sQuery(id+"F0.wireOp",EDGE,"E6.4.1"),sQuery(id+"F0.wireOp",EDGE,"E6.4.2"),sQuery(id+"F0.wireOp",EDGE,"E6.4.3"),sQuery(id+"F0.wireOp",EDGE,"E6.4.4"),sQuery(id+"F0.wireOp",EDGE,"E6.5.1"),sQuery(id+"F0.wireOp",EDGE,"E6.5.2"),sQuery(id+"F0.wireOp",EDGE,"E6.5.3"),sQuery(id+"F0.wireOp",EDGE,"E6.5.4"),sQuery(id+"F0.wireOp",EDGE,"E6.6.1"),sQuery(id+"F0.wireOp",EDGE,"E6.6.2"),sQuery(id+"F0.wireOp",EDGE,"E6.6.3"),sQuery(id+"F0.wireOp",EDGE,"E6.6.4"),sQuery(id+"F0.wireOp",EDGE,"E6.7.1"),sQuery(id+"F0.wireOp",EDGE,"E6.7.2"),sQuery(id+"F0.wireOp",EDGE,"E6.7.3"),sQuery(id+"F0.wireOp",EDGE,"E6.7.4"),sQuery(id+"F0.wireOp",EDGE,"E6.8.1"),sQuery(id+"F0.wireOp",EDGE,"E6.8.2"),sQuery(id+"F0.wireOp",EDGE,"E6.8.3"),sQuery(id+"F0.wireOp",EDGE,"E6.8.4"),subQ1,sQuery(id+"F0.wireOp",EDGE,"E6.9.2"),subQ0,sQuery(id+"F0.wireOp",EDGE,"E6.9.4"),sQuery(id+"F0.wireOp",EDGE,"E6.10.1"),sQuery(id+"F0.wireOp",EDGE,"E6.10.2"),sQuery(id+"F0.wireOp",EDGE,"E6.10.3"),sQuery(id+"F0.wireOp",EDGE,"E6.10.4"),sQuery(id+"F0.wireOp",EDGE,"E6.11.1"),sQuery(id+"F0.wireOp",EDGE,"E6.11.2"),sQuery(id+"F0.wireOp",EDGE,"E6.11.3"),sQuery(id+"F0.wireOp",EDGE,"E6.11.4"),sQuery(id+"F0.wireOp",EDGE,"E6.12.1"),sQuery(id+"F0.wireOp",EDGE,"E6.12.2"),sQuery(id+"F0.wireOp",EDGE,"E6.12.3"),sQuery(id+"F0.wireOp",EDGE,"E6.12.4"),sQuery(id+"F0.wireOp",EDGE,"E6.13.1"),sQuery(id+"F0.wireOp",EDGE,"E6.13.2"),sQuery(id+"F0.wireOp",EDGE,"E6.13.3"),sQuery(id+"F0.wireOp",EDGE,"E6.13.4"),sQuery(id+"F0.wireOp",EDGE,"E6.14.1"),sQuery(id+"F0.wireOp",EDGE,"E6.14.2"),sQuery(id+"F0.wireOp",EDGE,"E6.14.3"),sQuery(id+"F0.wireOp",EDGE,"E6.14.4"),sQuery(id+"F0.wireOp",EDGE,"E6.15.1"),sQuery(id+"F0.wireOp",EDGE,"E6.15.2"),sQuery(id+"F0.wireOp",EDGE,"E6.15.3"),sQuery(id+"F0.wireOp",EDGE,"E6.15.4"),sQuery(id+"F0.wireOp",EDGE,"E6.16.1"),sQuery(id+"F0.wireOp",EDGE,"E6.16.2"),sQuery(id+"F0.wireOp",EDGE,"E6.16.3"),sQuery(id+"F0.wireOp",EDGE,"E6.16.4"),sQuery(id+"F0.wireOp",EDGE,"E6.17.1"),sQuery(id+"F0.wireOp",EDGE,"E6.17.2"),sQuery(id+"F0.wireOp",EDGE,"E6.17.3"),sQuery(id+"F0.wireOp",EDGE,"E6.17.4"),sQuery(id+"F0.wireOp",EDGE,"E6.18.1"),sQuery(id+"F0.wireOp",EDGE,"E6.18.2"),sQuery(id+"F0.wireOp",EDGE,"E6.18.3"),sQuery(id+"F0.wireOp",EDGE,"E6.18.4"),sQuery(id+"F0.wireOp",EDGE,"E6.19.1"),sQuery(id+"F0.wireOp",EDGE,"E6.19.2"),sQuery(id+"F0.wireOp",EDGE,"E6.19.3"),sQuery(id+"F0.wireOp",EDGE,"E6.19.4"),sQuery(id+"F0.wireOp",EDGE,"E6.20.1"),sQuery(id+"F0.wireOp",EDGE,"E6.20.2"),sQuery(id+"F0.wireOp",EDGE,"E6.20.3"),sQuery(id+"F0.wireOp",EDGE,"E6.20.4"),sQuery(id+"F0.wireOp",EDGE,"E6.21.1"),sQuery(id+"F0.wireOp",EDGE,"E6.21.2"),sQuery(id+"F0.wireOp",EDGE,"E6.21.3"),sQuery(id+"F0.wireOp",EDGE,"E6.21.4"),sQuery(id+"F0.wireOp",EDGE,"E6.22.1"),sQuery(id+"F0.wireOp",EDGE,"E6.22.2"),sQuery(id+"F0.wireOp",EDGE,"E6.22.3"),sQuery(id+"F0.wireOp",EDGE,"E6.22.4"),sQuery(id+"F0.wireOp",EDGE,"E6.23.1"),sQuery(id+"F0.wireOp",EDGE,"E6.23.2"),sQuery(id+"F0.wireOp",EDGE,"E6.23.3"),sQuery(id+"F0.wireOp",EDGE,"E6.23.4"),sQuery(id+"F0.wireOp",EDGE,"E6.24.1"),sQuery(id+"F0.wireOp",EDGE,"E6.24.2"),sQuery(id+"F0.wireOp",EDGE,"E6.24.3"),sQuery(id+"F0.wireOp",EDGE,"E6.24.4"),sQuery(id+"F0.wireOp",EDGE,"E6.25.1"),sQuery(id+"F0.wireOp",EDGE,"E6.25.2"),sQuery(id+"F0.wireOp",EDGE,"E6.25.3"),sQuery(id+"F0.wireOp",EDGE,"E6.25.4"),sQuery(id+"F0.wireOp",EDGE,"E6.26.1"),sQuery(id+"F0.wireOp",EDGE,"E6.26.2"),sQuery(id+"F0.wireOp",EDGE,"E6.26.3"),sQuery(id+"F0.wireOp",EDGE,"E6.26.4"),sQuery(id+"F0.wireOp",EDGE,"E6.27.1"),sQuery(id+"F0.wireOp",EDGE,"E6.27.2"),sQuery(id+"F0.wireOp",EDGE,"E6.27.3"),sQuery(id+"F0.wireOp",EDGE,"E6.27.4"),sQuery(id+"F0.wireOp",EDGE,"E6.28.1"),sQuery(id+"F0.wireOp",EDGE,"E6.28.2"),sQuery(id+"F0.wireOp",EDGE,"E6.28.3"),sQuery(id+"F0.wireOp",EDGE,"E6.28.4"),sQuery(id+"F0.wireOp",EDGE,"E6.29.1"),sQuery(id+"F0.wireOp",EDGE,"E6.29.2"),sQuery(id+"F0.wireOp",EDGE,"E6.29.3"),sQuery(id+"F0.wireOp",EDGE,"E6.29.4"),sQuery(id+"F0.wireOp",EDGE,"E6.30.1"),sQuery(id+"F0.wireOp",EDGE,"E6.30.2"),sQuery(id+"F0.wireOp",EDGE,"E6.30.3"),sQuery(id+"F0.wireOp",EDGE,"E6.30.4"),sQuery(id+"F0.wireOp",EDGE,"E6.31.1"),sQuery(id+"F0.wireOp",EDGE,"E6.31.2"),sQuery(id+"F0.wireOp",EDGE,"E6.31.3"),sQuery(id+"F0.wireOp",EDGE,"E6.31.4"),sQuery(id+"F0.wireOp",EDGE,"E6.32.1"),sQuery(id+"F0.wireOp",EDGE,"E6.32.2"),sQuery(id+"F0.wireOp",EDGE,"E6.32.3"),sQuery(id+"F0.wireOp",EDGE,"E6.32.4"),sQuery(id+"F0.wireOp",EDGE,"E6.33.1"),sQuery(id+"F0.wireOp",EDGE,"E6.33.2"),sQuery(id+"F0.wireOp",EDGE,"E6.33.3"),sQuery(id+"F0.wireOp",EDGE,"E6.33.4"),sQuery(id+"F0.wireOp",EDGE,"E6.34.1"),sQuery(id+"F0.wireOp",EDGE,"E6.34.2"),sQuery(id+"F0.wireOp",EDGE,"E6.34.3"),sQuery(id+"F0.wireOp",EDGE,"E6.34.4"),sQuery(id+"F0.wireOp",EDGE,"E6.35.1"),sQuery(id+"F0.wireOp",EDGE,"E6.35.2"),sQuery(id+"F0.wireOp",EDGE,"E6.35.3"),sQuery(id+"F0.wireOp",EDGE,"E6.35.4"),sQuery(id+"F0.wireOp",EDGE,"E6.36.1"),sQuery(id+"F0.wireOp",EDGE,"E6.36.2"),sQuery(id+"F0.wireOp",EDGE,"E6.36.3"),sQuery(id+"F0.wireOp",EDGE,"E6.36.4"),sQuery(id+"F0.wireOp",EDGE,"E6.37.1"),sQuery(id+"F0.wireOp",EDGE,"E6.37.2"),sQuery(id+"F0.wireOp",EDGE,"E6.37.3"),sQuery(id+"F0.wireOp",EDGE,"E6.37.4"),sQuery(id+"F0.wireOp",EDGE,"E6.38.1"),sQuery(id+"F0.wireOp",EDGE,"E6.38.2"),sQuery(id+"F0.wireOp",EDGE,"E6.38.3"),sQuery(id+"F0.wireOp",EDGE,"E6.38.4"),sQuery(id+"F0.wireOp",EDGE,"E6.39.1"),sQuery(id+"F0.wireOp",EDGE,"E6.39.2"),sQuery(id+"F0.wireOp",EDGE,"E6.39.3"),sQuery(id+"F0.wireOp",EDGE,"E6.39.4"),sQuery(id+"F0.wireOp",EDGE,"E6.40.1"),sQuery(id+"F0.wireOp",EDGE,"E6.40.2"),sQuery(id+"F0.wireOp",EDGE,"E6.40.3"),sQuery(id+"F0.wireOp",EDGE,"E6.40.4"),sQuery(id+"F0.wireOp",EDGE,"E6.41.1"),sQuery(id+"F0.wireOp",EDGE,"E6.41.2"),sQuery(id+"F0.wireOp",EDGE,"E6.41.3"),sQuery(id+"F0.wireOp",EDGE,"E6.41.4"),sQuery(id+"F0.wireOp",EDGE,"E6.42.1"),sQuery(id+"F0.wireOp",EDGE,"E6.42.2"),sQuery(id+"F0.wireOp",EDGE,"E6.42.3"),sQuery(id+"F0.wireOp",EDGE,"E6.42.4"),sQuery(id+"F0.wireOp",EDGE,"E6.43.1"),sQuery(id+"F0.wireOp",EDGE,"E6.43.2"),sQuery(id+"F0.wireOp",EDGE,"E6.43.3"),sQuery(id+"F0.wireOp",EDGE,"E6.43.4"),sQuery(id+"F0.wireOp",EDGE,"E7"),sQuery(id+"F0.wireOp",EDGE,"E8.1.0"),sQuery(id+"F0.wireOp",EDGE,"E8.2.0"),sQuery(id+"F0.wireOp",EDGE,"E8.3.0"),sQuery(id+"F0.wireOp",EDGE,"E8.4.0"),sQuery(id+"F0.wireOp",EDGE,"E8.5.0"),sQuery(id+"F0.wireOp",EDGE,"E8.6.0"),sQuery(id+"F0.wireOp",EDGE,"E8.7.0"),sQuery(id+"F0.wireOp",EDGE,"E8.8.0"),sQuery(id+"F0.wireOp",EDGE,"E8.9.0"),sQuery(id+"F0.wireOp",EDGE,"E8.10.0"),sQuery(id+"F0.wireOp",EDGE,"E8.11.0"),sQuery(id+"F0.wireOp",EDGE,"E8.12.0"),sQuery(id+"F0.wireOp",EDGE,"E8.13.0"),sQuery(id+"F0.wireOp",EDGE,"E8.14.0"),sQuery(id+"F0.wireOp",EDGE,"E8.15.0"),sQuery(id+"F0.wireOp",EDGE,"E8.16.0"),sQuery(id+"F0.wireOp",EDGE,"E8.17.0"),sQuery(id+"F0.wireOp",EDGE,"E8.18.0"),sQuery(id+"F0.wireOp",EDGE,"E8.19.0"),sQuery(id+"F0.wireOp",EDGE,"E8.20.0"),sQuery(id+"F0.wireOp",EDGE,"E8.21.0"),sQuery(id+"F0.wireOp",EDGE,"E8.22.0"),sQuery(id+"F0.wireOp",EDGE,"E8.23.0"),sQuery(id+"F0.wireOp",EDGE,"E8.24.0"),sQuery(id+"F0.wireOp",EDGE,"E8.25.0"),sQuery(id+"F0.wireOp",EDGE,"E8.26.0"),sQuery(id+"F0.wireOp",EDGE,"E8.27.0"),sQuery(id+"F0.wireOp",EDGE,"E8.28.0"),sQuery(id+"F0.wireOp",EDGE,"E8.29.0"),sQuery(id+"F0.wireOp",EDGE,"E8.30.0"),sQuery(id+"F0.wireOp",EDGE,"E8.31.0"),sQuery(id+"F0.wireOp",EDGE,"E8.32.0"),sQuery(id+"F0.wireOp",EDGE,"E8.33.0"),sQuery(id+"F0.wireOp",EDGE,"E8.34.0"),sQuery(id+"F0.wireOp",EDGE,"E8.35.0"),sQuery(id+"F0.wireOp",EDGE,"E8.36.0"),sQuery(id+"F0.wireOp",EDGE,"E8.37.0"),sQuery(id+"F0.wireOp",EDGE,"E8.38.0"),sQuery(id+"F0.wireOp",EDGE,"E8.39.0"),sQuery(id+"F0.wireOp",EDGE,"E8.40.0"),sQuery(id+"F0.wireOp",EDGE,"E8.41.0"),sQuery(id+"F0.wireOp",EDGE,"E8.42.0"),sQuery(id+"F0.wireOp",EDGE,"E8.43.0")])],"isStart":false})],"blendedInto":[makeQuery(id+"F1.opExtrude","CAP_FACE",FACE,{"disambiguationData":[OSD([sQuery(id+"F0.wireOp",EDGE,"E0"),sQuery(id+"F0.wireOp",EDGE,"E1"),sQuery(id+"F0.wireOp",EDGE,"E2"),sQuery(id+"F0.wireOp",EDGE,"E4"),sQuery(id+"F0.wireOp",EDGE,"E5"),sQuery(id+"F0.wireOp",EDGE,"E6.1.1"),sQuery(id+"F0.wireOp",EDGE,"E6.1.2"),sQuery(id+"F0.wireOp",EDGE,"E6.1.3"),sQuery(id+"F0.wireOp",EDGE,"E6.1.4"),sQuery(id+"F0.wireOp",EDGE,"E6.2.1"),sQuery(id+"F0.wireOp",EDGE,"E6.2.2"),sQuery(id+"F0.wireOp",EDGE,"E6.2.3"),sQuery(id+"F0.wireOp",EDGE,"E6.2.4"),sQuery(id+"F0.wireOp",EDGE,"E6.3.1"),sQuery(id+"F0.wireOp",EDGE,"E6.3.2"),sQuery(id+"F0.wireOp",EDGE,"E6.3.3"),sQuery(id+"F0.wireOp",EDGE,"E6.3.4"),sQuery(id+"F0.wireOp",EDGE,"E6.4.1"),sQuery(id+"F0.wireOp",EDGE,"E6.4.2"),sQuery(id+"F0.wireOp",EDGE,"E6.4.3"),sQuery(id+"F0.wireOp",EDGE,"E6.4.4"),sQuery(id+"F0.wireOp",EDGE,"E6.5.1"),sQuery(id+"F0.wireOp",EDGE,"E6.5.2"),sQuery(id+"F0.wireOp",EDGE,"E6.5.3"),sQuery(id+"F0.wireOp",EDGE,"E6.5.4"),sQuery(id+"F0.wireOp",EDGE,"E6.6.1"),sQuery(id+"F0.wireOp",EDGE,"E6.6.2"),sQuery(id+"F0.wireOp",EDGE,"E6.6.3"),sQuery(id+"F0.wireOp",EDGE,"E6.6.4"),sQuery(id+"F0.wireOp",EDGE,"E6.7.1"),sQuery(id+"F0.wireOp",EDGE,"E6.7.2"),sQuery(id+"F0.wireOp",EDGE,"E6.7.3"),sQuery(id+"F0.wireOp",EDGE,"E6.7.4"),sQuery(id+"F0.wireOp",EDGE,"E6.8.1"),sQuery(id+"F0.wireOp",EDGE,"E6.8.2"),sQuery(id+"F0.wireOp",EDGE,"E6.8.3"),sQuery(id+"F0.wireOp",EDGE,"E6.8.4"),subQ1,sQuery(id+"F0.wireOp",EDGE,"E6.9.2"),subQ0,sQuery(id+"F0.wireOp",EDGE,"E6.9.4"),sQuery(id+"F0.wireOp",EDGE,"E6.10.1"),sQuery(id+"F0.wireOp",EDGE,"E6.10.2"),sQuery(id+"F0.wireOp",EDGE,"E6.10.3"),sQuery(id+"F0.wireOp",EDGE,"E6.10.4"),sQuery(id+"F0.wireOp",EDGE,"E6.11.1"),sQuery(id+"F0.wireOp",EDGE,"E6.11.2"),sQuery(id+"F0.wireOp",EDGE,"E6.11.3"),sQuery(id+"F0.wireOp",EDGE,"E6.11.4"),sQuery(id+"F0.wireOp",EDGE,"E6.12.1"),sQuery(id+"F0.wireOp",EDGE,"E6.12.2"),sQuery(id+"F0.wireOp",EDGE,"E6.12.3"),sQuery(id+"F0.wireOp",EDGE,"E6.12.4"),sQuery(id+"F0.wireOp",EDGE,"E6.13.1"),sQuery(id+"F0.wireOp",EDGE,"E6.13.2"),sQuery(id+"F0.wireOp",EDGE,"E6.13.3"),sQuery(id+"F0.wireOp",EDGE,"E6.13.4"),sQuery(id+"F0.wireOp",EDGE,"E6.14.1"),sQuery(id+"F0.wireOp",EDGE,"E6.14.2"),sQuery(id+"F0.wireOp",EDGE,"E6.14.3"),sQuery(id+"F0.wireOp",EDGE,"E6.14.4"),sQuery(id+"F0.wireOp",EDGE,"E6.15.1"),sQuery(id+"F0.wireOp",EDGE,"E6.15.2"),sQuery(id+"F0.wireOp",EDGE,"E6.15.3"),sQuery(id+"F0.wireOp",EDGE,"E6.15.4"),sQuery(id+"F0.wireOp",EDGE,"E6.16.1"),sQuery(id+"F0.wireOp",EDGE,"E6.16.2"),sQuery(id+"F0.wireOp",EDGE,"E6.16.3"),sQuery(id+"F0.wireOp",EDGE,"E6.16.4"),sQuery(id+"F0.wireOp",EDGE,"E6.17.1"),sQuery(id+"F0.wireOp",EDGE,"E6.17.2"),sQuery(id+"F0.wireOp",EDGE,"E6.17.3"),sQuery(id+"F0.wireOp",EDGE,"E6.17.4"),sQuery(id+"F0.wireOp",EDGE,"E6.18.1"),sQuery(id+"F0.wireOp",EDGE,"E6.18.2"),sQuery(id+"F0.wireOp",EDGE,"E6.18.3"),sQuery(id+"F0.wireOp",EDGE,"E6.18.4"),sQuery(id+"F0.wireOp",EDGE,"E6.19.1"),sQuery(id+"F0.wireOp",EDGE,"E6.19.2"),sQuery(id+"F0.wireOp",EDGE,"E6.19.3"),sQuery(id+"F0.wireOp",EDGE,"E6.19.4"),sQuery(id+"F0.wireOp",EDGE,"E6.20.1"),sQuery(id+"F0.wireOp",EDGE,"E6.20.2"),sQuery(id+"F0.wireOp",EDGE,"E6.20.3"),sQuery(id+"F0.wireOp",EDGE,"E6.20.4"),sQuery(id+"F0.wireOp",EDGE,"E6.21.1"),sQuery(id+"F0.wireOp",EDGE,"E6.21.2"),sQuery(id+"F0.wireOp",EDGE,"E6.21.3"),sQuery(id+"F0.wireOp",EDGE,"E6.21.4"),sQuery(id+"F0.wireOp",EDGE,"E6.22.1"),sQuery(id+"F0.wireOp",EDGE,"E6.22.2"),sQuery(id+"F0.wireOp",EDGE,"E6.22.3"),sQuery(id+"F0.wireOp",EDGE,"E6.22.4"),sQuery(id+"F0.wireOp",EDGE,"E6.23.1"),sQuery(id+"F0.wireOp",EDGE,"E6.23.2"),sQuery(id+"F0.wireOp",EDGE,"E6.23.3"),sQuery(id+"F0.wireOp",EDGE,"E6.23.4"),sQuery(id+"F0.wireOp",EDGE,"E6.24.1"),sQuery(id+"F0.wireOp",EDGE,"E6.24.2"),sQuery(id+"F0.wireOp",EDGE,"E6.24.3"),sQuery(id+"F0.wireOp",EDGE,"E6.24.4"),sQuery(id+"F0.wireOp",EDGE,"E6.25.1"),sQuery(id+"F0.wireOp",EDGE,"E6.25.2"),sQuery(id+"F0.wireOp",EDGE,"E6.25.3"),sQuery(id+"F0.wireOp",EDGE,"E6.25.4"),sQuery(id+"F0.wireOp",EDGE,"E6.26.1"),sQuery(id+"F0.wireOp",EDGE,"E6.26.2"),sQuery(id+"F0.wireOp",EDGE,"E6.26.3"),sQuery(id+"F0.wireOp",EDGE,"E6.26.4"),sQuery(id+"F0.wireOp",EDGE,"E6.27.1"),sQuery(id+"F0.wireOp",EDGE,"E6.27.2"),sQuery(id+"F0.wireOp",EDGE,"E6.27.3"),sQuery(id+"F0.wireOp",EDGE,"E6.27.4"),sQuery(id+"F0.wireOp",EDGE,"E6.28.1"),sQuery(id+"F0.wireOp",EDGE,"E6.28.2"),sQuery(id+"F0.wireOp",EDGE,"E6.28.3"),sQuery(id+"F0.wireOp",EDGE,"E6.28.4"),sQuery(id+"F0.wireOp",EDGE,"E6.29.1"),sQuery(id+"F0.wireOp",EDGE,"E6.29.2"),sQuery(id+"F0.wireOp",EDGE,"E6.29.3"),sQuery(id+"F0.wireOp",EDGE,"E6.29.4"),sQuery(id+"F0.wireOp",EDGE,"E6.30.1"),sQuery(id+"F0.wireOp",EDGE,"E6.30.2"),sQuery(id+"F0.wireOp",EDGE,"E6.30.3"),sQuery(id+"F0.wireOp",EDGE,"E6.30.4"),sQuery(id+"F0.wireOp",EDGE,"E6.31.1"),sQuery(id+"F0.wireOp",EDGE,"E6.31.2"),sQuery(id+"F0.wireOp",EDGE,"E6.31.3"),sQuery(id+"F0.wireOp",EDGE,"E6.31.4"),sQuery(id+"F0.wireOp",EDGE,"E6.32.1"),sQuery(id+"F0.wireOp",EDGE,"E6.32.2"),sQuery(id+"F0.wireOp",EDGE,"E6.32.3"),sQuery(id+"F0.wireOp",EDGE,"E6.32.4"),sQuery(id+"F0.wireOp",EDGE,"E6.33.1"),sQuery(id+"F0.wireOp",EDGE,"E6.33.2"),sQuery(id+"F0.wireOp",EDGE,"E6.33.3"),sQuery(id+"F0.wireOp",EDGE,"E6.33.4"),sQuery(id+"F0.wireOp",EDGE,"E6.34.1"),sQuery(id+"F0.wireOp",EDGE,"E6.34.2"),sQuery(id+"F0.wireOp",EDGE,"E6.34.3"),sQuery(id+"F0.wireOp",EDGE,"E6.34.4"),sQuery(id+"F0.wireOp",EDGE,"E6.35.1"),sQuery(id+"F0.wireOp",EDGE,"E6.35.2"),sQuery(id+"F0.wireOp",EDGE,"E6.35.3"),sQuery(id+"F0.wireOp",EDGE,"E6.35.4"),sQuery(id+"F0.wireOp",EDGE,"E6.36.1"),sQuery(id+"F0.wireOp",EDGE,"E6.36.2"),sQuery(id+"F0.wireOp",EDGE,"E6.36.3"),sQuery(id+"F0.wireOp",EDGE,"E6.36.4"),sQuery(id+"F0.wireOp",EDGE,"E6.37.1"),sQuery(id+"F0.wireOp",EDGE,"E6.37.2"),sQuery(id+"F0.wireOp",EDGE,"E6.37.3"),sQuery(id+"F0.wireOp",EDGE,"E6.37.4"),sQuery(id+"F0.wireOp",EDGE,"E6.38.1"),sQuery(id+"F0.wireOp",EDGE,"E6.38.2"),sQuery(id+"F0.wireOp",EDGE,"E6.38.3"),sQuery(id+"F0.wireOp",EDGE,"E6.38.4"),sQuery(id+"F0.wireOp",EDGE,"E6.39.1"),sQuery(id+"F0.wireOp",EDGE,"E6.39.2"),sQuery(id+"F0.wireOp",EDGE,"E6.39.3"),sQuery(id+"F0.wireOp",EDGE,"E6.39.4"),sQuery(id+"F0.wireOp",EDGE,"E6.40.1"),sQuery(id+"F0.wireOp",EDGE,"E6.40.2"),sQuery(id+"F0.wireOp",EDGE,"E6.40.3"),sQuery(id+"F0.wireOp",EDGE,"E6.40.4"),sQuery(id+"F0.wireOp",EDGE,"E6.41.1"),sQuery(id+"F0.wireOp",EDGE,"E6.41.2"),sQuery(id+"F0.wireOp",EDGE,"E6.41.3"),sQuery(id+"F0.wireOp",EDGE,"E6.41.4"),sQuery(id+"F0.wireOp",EDGE,"E6.42.1"),sQuery(id+"F0.wireOp",EDGE,"E6.42.2"),sQuery(id+"F0.wireOp",EDGE,"E6.42.3"),sQuery(id+"F0.wireOp",EDGE,"E6.42.4"),sQuery(id+"F0.wireOp",EDGE,"E6.43.1"),sQuery(id+"F0.wireOp",EDGE,"E6.43.2"),sQuery(id+"F0.wireOp",EDGE,"E6.43.3"),sQuery(id+"F0.wireOp",EDGE,"E6.43.4"),sQuery(id+"F0.wireOp",EDGE,"E7"),sQuery(id+"F0.wireOp",EDGE,"E8.1.0"),sQuery(id+"F0.wireOp",EDGE,"E8.2.0"),sQuery(id+"F0.wireOp",EDGE,"E8.3.0"),sQuery(id+"F0.wireOp",EDGE,"E8.4.0"),sQuery(id+"F0.wireOp",EDGE,"E8.5.0"),sQuery(id+"F0.wireOp",EDGE,"E8.6.0"),sQuery(id+"F0.wireOp",EDGE,"E8.7.0"),sQuery(id+"F0.wireOp",EDGE,"E8.8.0"),sQuery(id+"F0.wireOp",EDGE,"E8.9.0"),sQuery(id+"F0.wireOp",EDGE,"E8.10.0"),sQuery(id+"F0.wireOp",EDGE,"E8.11.0"),sQuery(id+"F0.wireOp",EDGE,"E8.12.0"),sQuery(id+"F0.wireOp",EDGE,"E8.13.0"),sQuery(id+"F0.wireOp",EDGE,"E8.14.0"),sQuery(id+"F0.wireOp",EDGE,"E8.15.0"),sQuery(id+"F0.wireOp",EDGE,"E8.16.0"),sQuery(id+"F0.wireOp",EDGE,"E8.17.0"),sQuery(id+"F0.wireOp",EDGE,"E8.18.0"),sQuery(id+"F0.wireOp",EDGE,"E8.19.0"),sQuery(id+"F0.wireOp",EDGE,"E8.20.0"),sQuery(id+"F0.wireOp",EDGE,"E8.21.0"),sQuery(id+"F0.wireOp",EDGE,"E8.22.0"),sQuery(id+"F0.wireOp",EDGE,"E8.23.0"),sQuery(id+"F0.wireOp",EDGE,"E8.24.0"),sQuery(id+"F0.wireOp",EDGE,"E8.25.0"),sQuery(id+"F0.wireOp",EDGE,"E8.26.0"),sQuery(id+"F0.wireOp",EDGE,"E8.27.0"),sQuery(id+"F0.wireOp",EDGE,"E8.28.0"),sQuery(id+"F0.wireOp",EDGE,"E8.29.0"),sQuery(id+"F0.wireOp",EDGE,"E8.30.0"),sQuery(id+"F0.wireOp",EDGE,"E8.31.0"),sQuery(id+"F0.wireOp",EDGE,"E8.32.0"),sQuery(id+"F0.wireOp",EDGE,"E8.33.0"),sQuery(id+"F0.wireOp",EDGE,"E8.34.0"),sQuery(id+"F0.wireOp",EDGE,"E8.35.0"),sQuery(id+"F0.wireOp",EDGE,"E8.36.0"),sQuery(id+"F0.wireOp",EDGE,"E8.37.0"),sQuery(id+"F0.wireOp",EDGE,"E8.38.0"),sQuery(id+"F0.wireOp",EDGE,"E8.39.0"),sQuery(id+"F0.wireOp",EDGE,"E8.40.0"),sQuery(id+"F0.wireOp",EDGE,"E8.41.0"),sQuery(id+"F0.wireOp",EDGE,"E8.42.0"),sQuery(id+"F0.wireOp",EDGE,"E8.43.0")])],"isStart":false})]});}
            var Q16;
            {var subQ0=sQuery(id+"F0.wireOp",EDGE,"E6.11.3");var subQ1=sQuery(id+"F0.wireOp",EDGE,"E6.11.1");Q16=makeQuery(id+"F2.opFillet","BLEND_EDGE",EDGE,{"blendedFrom":[makeQuery(id+"F1.opExtrude","SWEPT_EDGE",EDGE,{"disambiguationData":[OSD([sQuery(id+"F0.wireOp",EDGE,"E6.11.0"),subQ1,subQ0])]}),makeQuery(id+"F1.opExtrude","CAP_FACE",FACE,{"disambiguationData":[OSD([sQuery(id+"F0.wireOp",EDGE,"E0"),sQuery(id+"F0.wireOp",EDGE,"E1"),sQuery(id+"F0.wireOp",EDGE,"E2"),sQuery(id+"F0.wireOp",EDGE,"E4"),sQuery(id+"F0.wireOp",EDGE,"E5"),sQuery(id+"F0.wireOp",EDGE,"E6.1.1"),sQuery(id+"F0.wireOp",EDGE,"E6.1.2"),sQuery(id+"F0.wireOp",EDGE,"E6.1.3"),sQuery(id+"F0.wireOp",EDGE,"E6.1.4"),sQuery(id+"F0.wireOp",EDGE,"E6.2.1"),sQuery(id+"F0.wireOp",EDGE,"E6.2.2"),sQuery(id+"F0.wireOp",EDGE,"E6.2.3"),sQuery(id+"F0.wireOp",EDGE,"E6.2.4"),sQuery(id+"F0.wireOp",EDGE,"E6.3.1"),sQuery(id+"F0.wireOp",EDGE,"E6.3.2"),sQuery(id+"F0.wireOp",EDGE,"E6.3.3"),sQuery(id+"F0.wireOp",EDGE,"E6.3.4"),sQuery(id+"F0.wireOp",EDGE,"E6.4.1"),sQuery(id+"F0.wireOp",EDGE,"E6.4.2"),sQuery(id+"F0.wireOp",EDGE,"E6.4.3"),sQuery(id+"F0.wireOp",EDGE,"E6.4.4"),sQuery(id+"F0.wireOp",EDGE,"E6.5.1"),sQuery(id+"F0.wireOp",EDGE,"E6.5.2"),sQuery(id+"F0.wireOp",EDGE,"E6.5.3"),sQuery(id+"F0.wireOp",EDGE,"E6.5.4"),sQuery(id+"F0.wireOp",EDGE,"E6.6.1"),sQuery(id+"F0.wireOp",EDGE,"E6.6.2"),sQuery(id+"F0.wireOp",EDGE,"E6.6.3"),sQuery(id+"F0.wireOp",EDGE,"E6.6.4"),sQuery(id+"F0.wireOp",EDGE,"E6.7.1"),sQuery(id+"F0.wireOp",EDGE,"E6.7.2"),sQuery(id+"F0.wireOp",EDGE,"E6.7.3"),sQuery(id+"F0.wireOp",EDGE,"E6.7.4"),sQuery(id+"F0.wireOp",EDGE,"E6.8.1"),sQuery(id+"F0.wireOp",EDGE,"E6.8.2"),sQuery(id+"F0.wireOp",EDGE,"E6.8.3"),sQuery(id+"F0.wireOp",EDGE,"E6.8.4"),sQuery(id+"F0.wireOp",EDGE,"E6.9.1"),sQuery(id+"F0.wireOp",EDGE,"E6.9.2"),sQuery(id+"F0.wireOp",EDGE,"E6.9.3"),sQuery(id+"F0.wireOp",EDGE,"E6.9.4"),sQuery(id+"F0.wireOp",EDGE,"E6.10.1"),sQuery(id+"F0.wireOp",EDGE,"E6.10.2"),sQuery(id+"F0.wireOp",EDGE,"E6.10.3"),sQuery(id+"F0.wireOp",EDGE,"E6.10.4"),subQ1,sQuery(id+"F0.wireOp",EDGE,"E6.11.2"),subQ0,sQuery(id+"F0.wireOp",EDGE,"E6.11.4"),sQuery(id+"F0.wireOp",EDGE,"E6.12.1"),sQuery(id+"F0.wireOp",EDGE,"E6.12.2"),sQuery(id+"F0.wireOp",EDGE,"E6.12.3"),sQuery(id+"F0.wireOp",EDGE,"E6.12.4"),sQuery(id+"F0.wireOp",EDGE,"E6.13.1"),sQuery(id+"F0.wireOp",EDGE,"E6.13.2"),sQuery(id+"F0.wireOp",EDGE,"E6.13.3"),sQuery(id+"F0.wireOp",EDGE,"E6.13.4"),sQuery(id+"F0.wireOp",EDGE,"E6.14.1"),sQuery(id+"F0.wireOp",EDGE,"E6.14.2"),sQuery(id+"F0.wireOp",EDGE,"E6.14.3"),sQuery(id+"F0.wireOp",EDGE,"E6.14.4"),sQuery(id+"F0.wireOp",EDGE,"E6.15.1"),sQuery(id+"F0.wireOp",EDGE,"E6.15.2"),sQuery(id+"F0.wireOp",EDGE,"E6.15.3"),sQuery(id+"F0.wireOp",EDGE,"E6.15.4"),sQuery(id+"F0.wireOp",EDGE,"E6.16.1"),sQuery(id+"F0.wireOp",EDGE,"E6.16.2"),sQuery(id+"F0.wireOp",EDGE,"E6.16.3"),sQuery(id+"F0.wireOp",EDGE,"E6.16.4"),sQuery(id+"F0.wireOp",EDGE,"E6.17.1"),sQuery(id+"F0.wireOp",EDGE,"E6.17.2"),sQuery(id+"F0.wireOp",EDGE,"E6.17.3"),sQuery(id+"F0.wireOp",EDGE,"E6.17.4"),sQuery(id+"F0.wireOp",EDGE,"E6.18.1"),sQuery(id+"F0.wireOp",EDGE,"E6.18.2"),sQuery(id+"F0.wireOp",EDGE,"E6.18.3"),sQuery(id+"F0.wireOp",EDGE,"E6.18.4"),sQuery(id+"F0.wireOp",EDGE,"E6.19.1"),sQuery(id+"F0.wireOp",EDGE,"E6.19.2"),sQuery(id+"F0.wireOp",EDGE,"E6.19.3"),sQuery(id+"F0.wireOp",EDGE,"E6.19.4"),sQuery(id+"F0.wireOp",EDGE,"E6.20.1"),sQuery(id+"F0.wireOp",EDGE,"E6.20.2"),sQuery(id+"F0.wireOp",EDGE,"E6.20.3"),sQuery(id+"F0.wireOp",EDGE,"E6.20.4"),sQuery(id+"F0.wireOp",EDGE,"E6.21.1"),sQuery(id+"F0.wireOp",EDGE,"E6.21.2"),sQuery(id+"F0.wireOp",EDGE,"E6.21.3"),sQuery(id+"F0.wireOp",EDGE,"E6.21.4"),sQuery(id+"F0.wireOp",EDGE,"E6.22.1"),sQuery(id+"F0.wireOp",EDGE,"E6.22.2"),sQuery(id+"F0.wireOp",EDGE,"E6.22.3"),sQuery(id+"F0.wireOp",EDGE,"E6.22.4"),sQuery(id+"F0.wireOp",EDGE,"E6.23.1"),sQuery(id+"F0.wireOp",EDGE,"E6.23.2"),sQuery(id+"F0.wireOp",EDGE,"E6.23.3"),sQuery(id+"F0.wireOp",EDGE,"E6.23.4"),sQuery(id+"F0.wireOp",EDGE,"E6.24.1"),sQuery(id+"F0.wireOp",EDGE,"E6.24.2"),sQuery(id+"F0.wireOp",EDGE,"E6.24.3"),sQuery(id+"F0.wireOp",EDGE,"E6.24.4"),sQuery(id+"F0.wireOp",EDGE,"E6.25.1"),sQuery(id+"F0.wireOp",EDGE,"E6.25.2"),sQuery(id+"F0.wireOp",EDGE,"E6.25.3"),sQuery(id+"F0.wireOp",EDGE,"E6.25.4"),sQuery(id+"F0.wireOp",EDGE,"E6.26.1"),sQuery(id+"F0.wireOp",EDGE,"E6.26.2"),sQuery(id+"F0.wireOp",EDGE,"E6.26.3"),sQuery(id+"F0.wireOp",EDGE,"E6.26.4"),sQuery(id+"F0.wireOp",EDGE,"E6.27.1"),sQuery(id+"F0.wireOp",EDGE,"E6.27.2"),sQuery(id+"F0.wireOp",EDGE,"E6.27.3"),sQuery(id+"F0.wireOp",EDGE,"E6.27.4"),sQuery(id+"F0.wireOp",EDGE,"E6.28.1"),sQuery(id+"F0.wireOp",EDGE,"E6.28.2"),sQuery(id+"F0.wireOp",EDGE,"E6.28.3"),sQuery(id+"F0.wireOp",EDGE,"E6.28.4"),sQuery(id+"F0.wireOp",EDGE,"E6.29.1"),sQuery(id+"F0.wireOp",EDGE,"E6.29.2"),sQuery(id+"F0.wireOp",EDGE,"E6.29.3"),sQuery(id+"F0.wireOp",EDGE,"E6.29.4"),sQuery(id+"F0.wireOp",EDGE,"E6.30.1"),sQuery(id+"F0.wireOp",EDGE,"E6.30.2"),sQuery(id+"F0.wireOp",EDGE,"E6.30.3"),sQuery(id+"F0.wireOp",EDGE,"E6.30.4"),sQuery(id+"F0.wireOp",EDGE,"E6.31.1"),sQuery(id+"F0.wireOp",EDGE,"E6.31.2"),sQuery(id+"F0.wireOp",EDGE,"E6.31.3"),sQuery(id+"F0.wireOp",EDGE,"E6.31.4"),sQuery(id+"F0.wireOp",EDGE,"E6.32.1"),sQuery(id+"F0.wireOp",EDGE,"E6.32.2"),sQuery(id+"F0.wireOp",EDGE,"E6.32.3"),sQuery(id+"F0.wireOp",EDGE,"E6.32.4"),sQuery(id+"F0.wireOp",EDGE,"E6.33.1"),sQuery(id+"F0.wireOp",EDGE,"E6.33.2"),sQuery(id+"F0.wireOp",EDGE,"E6.33.3"),sQuery(id+"F0.wireOp",EDGE,"E6.33.4"),sQuery(id+"F0.wireOp",EDGE,"E6.34.1"),sQuery(id+"F0.wireOp",EDGE,"E6.34.2"),sQuery(id+"F0.wireOp",EDGE,"E6.34.3"),sQuery(id+"F0.wireOp",EDGE,"E6.34.4"),sQuery(id+"F0.wireOp",EDGE,"E6.35.1"),sQuery(id+"F0.wireOp",EDGE,"E6.35.2"),sQuery(id+"F0.wireOp",EDGE,"E6.35.3"),sQuery(id+"F0.wireOp",EDGE,"E6.35.4"),sQuery(id+"F0.wireOp",EDGE,"E6.36.1"),sQuery(id+"F0.wireOp",EDGE,"E6.36.2"),sQuery(id+"F0.wireOp",EDGE,"E6.36.3"),sQuery(id+"F0.wireOp",EDGE,"E6.36.4"),sQuery(id+"F0.wireOp",EDGE,"E6.37.1"),sQuery(id+"F0.wireOp",EDGE,"E6.37.2"),sQuery(id+"F0.wireOp",EDGE,"E6.37.3"),sQuery(id+"F0.wireOp",EDGE,"E6.37.4"),sQuery(id+"F0.wireOp",EDGE,"E6.38.1"),sQuery(id+"F0.wireOp",EDGE,"E6.38.2"),sQuery(id+"F0.wireOp",EDGE,"E6.38.3"),sQuery(id+"F0.wireOp",EDGE,"E6.38.4"),sQuery(id+"F0.wireOp",EDGE,"E6.39.1"),sQuery(id+"F0.wireOp",EDGE,"E6.39.2"),sQuery(id+"F0.wireOp",EDGE,"E6.39.3"),sQuery(id+"F0.wireOp",EDGE,"E6.39.4"),sQuery(id+"F0.wireOp",EDGE,"E6.40.1"),sQuery(id+"F0.wireOp",EDGE,"E6.40.2"),sQuery(id+"F0.wireOp",EDGE,"E6.40.3"),sQuery(id+"F0.wireOp",EDGE,"E6.40.4"),sQuery(id+"F0.wireOp",EDGE,"E6.41.1"),sQuery(id+"F0.wireOp",EDGE,"E6.41.2"),sQuery(id+"F0.wireOp",EDGE,"E6.41.3"),sQuery(id+"F0.wireOp",EDGE,"E6.41.4"),sQuery(id+"F0.wireOp",EDGE,"E6.42.1"),sQuery(id+"F0.wireOp",EDGE,"E6.42.2"),sQuery(id+"F0.wireOp",EDGE,"E6.42.3"),sQuery(id+"F0.wireOp",EDGE,"E6.42.4"),sQuery(id+"F0.wireOp",EDGE,"E6.43.1"),sQuery(id+"F0.wireOp",EDGE,"E6.43.2"),sQuery(id+"F0.wireOp",EDGE,"E6.43.3"),sQuery(id+"F0.wireOp",EDGE,"E6.43.4"),sQuery(id+"F0.wireOp",EDGE,"E7"),sQuery(id+"F0.wireOp",EDGE,"E8.1.0"),sQuery(id+"F0.wireOp",EDGE,"E8.2.0"),sQuery(id+"F0.wireOp",EDGE,"E8.3.0"),sQuery(id+"F0.wireOp",EDGE,"E8.4.0"),sQuery(id+"F0.wireOp",EDGE,"E8.5.0"),sQuery(id+"F0.wireOp",EDGE,"E8.6.0"),sQuery(id+"F0.wireOp",EDGE,"E8.7.0"),sQuery(id+"F0.wireOp",EDGE,"E8.8.0"),sQuery(id+"F0.wireOp",EDGE,"E8.9.0"),sQuery(id+"F0.wireOp",EDGE,"E8.10.0"),sQuery(id+"F0.wireOp",EDGE,"E8.11.0"),sQuery(id+"F0.wireOp",EDGE,"E8.12.0"),sQuery(id+"F0.wireOp",EDGE,"E8.13.0"),sQuery(id+"F0.wireOp",EDGE,"E8.14.0"),sQuery(id+"F0.wireOp",EDGE,"E8.15.0"),sQuery(id+"F0.wireOp",EDGE,"E8.16.0"),sQuery(id+"F0.wireOp",EDGE,"E8.17.0"),sQuery(id+"F0.wireOp",EDGE,"E8.18.0"),sQuery(id+"F0.wireOp",EDGE,"E8.19.0"),sQuery(id+"F0.wireOp",EDGE,"E8.20.0"),sQuery(id+"F0.wireOp",EDGE,"E8.21.0"),sQuery(id+"F0.wireOp",EDGE,"E8.22.0"),sQuery(id+"F0.wireOp",EDGE,"E8.23.0"),sQuery(id+"F0.wireOp",EDGE,"E8.24.0"),sQuery(id+"F0.wireOp",EDGE,"E8.25.0"),sQuery(id+"F0.wireOp",EDGE,"E8.26.0"),sQuery(id+"F0.wireOp",EDGE,"E8.27.0"),sQuery(id+"F0.wireOp",EDGE,"E8.28.0"),sQuery(id+"F0.wireOp",EDGE,"E8.29.0"),sQuery(id+"F0.wireOp",EDGE,"E8.30.0"),sQuery(id+"F0.wireOp",EDGE,"E8.31.0"),sQuery(id+"F0.wireOp",EDGE,"E8.32.0"),sQuery(id+"F0.wireOp",EDGE,"E8.33.0"),sQuery(id+"F0.wireOp",EDGE,"E8.34.0"),sQuery(id+"F0.wireOp",EDGE,"E8.35.0"),sQuery(id+"F0.wireOp",EDGE,"E8.36.0"),sQuery(id+"F0.wireOp",EDGE,"E8.37.0"),sQuery(id+"F0.wireOp",EDGE,"E8.38.0"),sQuery(id+"F0.wireOp",EDGE,"E8.39.0"),sQuery(id+"F0.wireOp",EDGE,"E8.40.0"),sQuery(id+"F0.wireOp",EDGE,"E8.41.0"),sQuery(id+"F0.wireOp",EDGE,"E8.42.0"),sQuery(id+"F0.wireOp",EDGE,"E8.43.0")])],"isStart":false})],"blendedInto":[makeQuery(id+"F1.opExtrude","CAP_FACE",FACE,{"disambiguationData":[OSD([sQuery(id+"F0.wireOp",EDGE,"E0"),sQuery(id+"F0.wireOp",EDGE,"E1"),sQuery(id+"F0.wireOp",EDGE,"E2"),sQuery(id+"F0.wireOp",EDGE,"E4"),sQuery(id+"F0.wireOp",EDGE,"E5"),sQuery(id+"F0.wireOp",EDGE,"E6.1.1"),sQuery(id+"F0.wireOp",EDGE,"E6.1.2"),sQuery(id+"F0.wireOp",EDGE,"E6.1.3"),sQuery(id+"F0.wireOp",EDGE,"E6.1.4"),sQuery(id+"F0.wireOp",EDGE,"E6.2.1"),sQuery(id+"F0.wireOp",EDGE,"E6.2.2"),sQuery(id+"F0.wireOp",EDGE,"E6.2.3"),sQuery(id+"F0.wireOp",EDGE,"E6.2.4"),sQuery(id+"F0.wireOp",EDGE,"E6.3.1"),sQuery(id+"F0.wireOp",EDGE,"E6.3.2"),sQuery(id+"F0.wireOp",EDGE,"E6.3.3"),sQuery(id+"F0.wireOp",EDGE,"E6.3.4"),sQuery(id+"F0.wireOp",EDGE,"E6.4.1"),sQuery(id+"F0.wireOp",EDGE,"E6.4.2"),sQuery(id+"F0.wireOp",EDGE,"E6.4.3"),sQuery(id+"F0.wireOp",EDGE,"E6.4.4"),sQuery(id+"F0.wireOp",EDGE,"E6.5.1"),sQuery(id+"F0.wireOp",EDGE,"E6.5.2"),sQuery(id+"F0.wireOp",EDGE,"E6.5.3"),sQuery(id+"F0.wireOp",EDGE,"E6.5.4"),sQuery(id+"F0.wireOp",EDGE,"E6.6.1"),sQuery(id+"F0.wireOp",EDGE,"E6.6.2"),sQuery(id+"F0.wireOp",EDGE,"E6.6.3"),sQuery(id+"F0.wireOp",EDGE,"E6.6.4"),sQuery(id+"F0.wireOp",EDGE,"E6.7.1"),sQuery(id+"F0.wireOp",EDGE,"E6.7.2"),sQuery(id+"F0.wireOp",EDGE,"E6.7.3"),sQuery(id+"F0.wireOp",EDGE,"E6.7.4"),sQuery(id+"F0.wireOp",EDGE,"E6.8.1"),sQuery(id+"F0.wireOp",EDGE,"E6.8.2"),sQuery(id+"F0.wireOp",EDGE,"E6.8.3"),sQuery(id+"F0.wireOp",EDGE,"E6.8.4"),sQuery(id+"F0.wireOp",EDGE,"E6.9.1"),sQuery(id+"F0.wireOp",EDGE,"E6.9.2"),sQuery(id+"F0.wireOp",EDGE,"E6.9.3"),sQuery(id+"F0.wireOp",EDGE,"E6.9.4"),sQuery(id+"F0.wireOp",EDGE,"E6.10.1"),sQuery(id+"F0.wireOp",EDGE,"E6.10.2"),sQuery(id+"F0.wireOp",EDGE,"E6.10.3"),sQuery(id+"F0.wireOp",EDGE,"E6.10.4"),subQ1,sQuery(id+"F0.wireOp",EDGE,"E6.11.2"),subQ0,sQuery(id+"F0.wireOp",EDGE,"E6.11.4"),sQuery(id+"F0.wireOp",EDGE,"E6.12.1"),sQuery(id+"F0.wireOp",EDGE,"E6.12.2"),sQuery(id+"F0.wireOp",EDGE,"E6.12.3"),sQuery(id+"F0.wireOp",EDGE,"E6.12.4"),sQuery(id+"F0.wireOp",EDGE,"E6.13.1"),sQuery(id+"F0.wireOp",EDGE,"E6.13.2"),sQuery(id+"F0.wireOp",EDGE,"E6.13.3"),sQuery(id+"F0.wireOp",EDGE,"E6.13.4"),sQuery(id+"F0.wireOp",EDGE,"E6.14.1"),sQuery(id+"F0.wireOp",EDGE,"E6.14.2"),sQuery(id+"F0.wireOp",EDGE,"E6.14.3"),sQuery(id+"F0.wireOp",EDGE,"E6.14.4"),sQuery(id+"F0.wireOp",EDGE,"E6.15.1"),sQuery(id+"F0.wireOp",EDGE,"E6.15.2"),sQuery(id+"F0.wireOp",EDGE,"E6.15.3"),sQuery(id+"F0.wireOp",EDGE,"E6.15.4"),sQuery(id+"F0.wireOp",EDGE,"E6.16.1"),sQuery(id+"F0.wireOp",EDGE,"E6.16.2"),sQuery(id+"F0.wireOp",EDGE,"E6.16.3"),sQuery(id+"F0.wireOp",EDGE,"E6.16.4"),sQuery(id+"F0.wireOp",EDGE,"E6.17.1"),sQuery(id+"F0.wireOp",EDGE,"E6.17.2"),sQuery(id+"F0.wireOp",EDGE,"E6.17.3"),sQuery(id+"F0.wireOp",EDGE,"E6.17.4"),sQuery(id+"F0.wireOp",EDGE,"E6.18.1"),sQuery(id+"F0.wireOp",EDGE,"E6.18.2"),sQuery(id+"F0.wireOp",EDGE,"E6.18.3"),sQuery(id+"F0.wireOp",EDGE,"E6.18.4"),sQuery(id+"F0.wireOp",EDGE,"E6.19.1"),sQuery(id+"F0.wireOp",EDGE,"E6.19.2"),sQuery(id+"F0.wireOp",EDGE,"E6.19.3"),sQuery(id+"F0.wireOp",EDGE,"E6.19.4"),sQuery(id+"F0.wireOp",EDGE,"E6.20.1"),sQuery(id+"F0.wireOp",EDGE,"E6.20.2"),sQuery(id+"F0.wireOp",EDGE,"E6.20.3"),sQuery(id+"F0.wireOp",EDGE,"E6.20.4"),sQuery(id+"F0.wireOp",EDGE,"E6.21.1"),sQuery(id+"F0.wireOp",EDGE,"E6.21.2"),sQuery(id+"F0.wireOp",EDGE,"E6.21.3"),sQuery(id+"F0.wireOp",EDGE,"E6.21.4"),sQuery(id+"F0.wireOp",EDGE,"E6.22.1"),sQuery(id+"F0.wireOp",EDGE,"E6.22.2"),sQuery(id+"F0.wireOp",EDGE,"E6.22.3"),sQuery(id+"F0.wireOp",EDGE,"E6.22.4"),sQuery(id+"F0.wireOp",EDGE,"E6.23.1"),sQuery(id+"F0.wireOp",EDGE,"E6.23.2"),sQuery(id+"F0.wireOp",EDGE,"E6.23.3"),sQuery(id+"F0.wireOp",EDGE,"E6.23.4"),sQuery(id+"F0.wireOp",EDGE,"E6.24.1"),sQuery(id+"F0.wireOp",EDGE,"E6.24.2"),sQuery(id+"F0.wireOp",EDGE,"E6.24.3"),sQuery(id+"F0.wireOp",EDGE,"E6.24.4"),sQuery(id+"F0.wireOp",EDGE,"E6.25.1"),sQuery(id+"F0.wireOp",EDGE,"E6.25.2"),sQuery(id+"F0.wireOp",EDGE,"E6.25.3"),sQuery(id+"F0.wireOp",EDGE,"E6.25.4"),sQuery(id+"F0.wireOp",EDGE,"E6.26.1"),sQuery(id+"F0.wireOp",EDGE,"E6.26.2"),sQuery(id+"F0.wireOp",EDGE,"E6.26.3"),sQuery(id+"F0.wireOp",EDGE,"E6.26.4"),sQuery(id+"F0.wireOp",EDGE,"E6.27.1"),sQuery(id+"F0.wireOp",EDGE,"E6.27.2"),sQuery(id+"F0.wireOp",EDGE,"E6.27.3"),sQuery(id+"F0.wireOp",EDGE,"E6.27.4"),sQuery(id+"F0.wireOp",EDGE,"E6.28.1"),sQuery(id+"F0.wireOp",EDGE,"E6.28.2"),sQuery(id+"F0.wireOp",EDGE,"E6.28.3"),sQuery(id+"F0.wireOp",EDGE,"E6.28.4"),sQuery(id+"F0.wireOp",EDGE,"E6.29.1"),sQuery(id+"F0.wireOp",EDGE,"E6.29.2"),sQuery(id+"F0.wireOp",EDGE,"E6.29.3"),sQuery(id+"F0.wireOp",EDGE,"E6.29.4"),sQuery(id+"F0.wireOp",EDGE,"E6.30.1"),sQuery(id+"F0.wireOp",EDGE,"E6.30.2"),sQuery(id+"F0.wireOp",EDGE,"E6.30.3"),sQuery(id+"F0.wireOp",EDGE,"E6.30.4"),sQuery(id+"F0.wireOp",EDGE,"E6.31.1"),sQuery(id+"F0.wireOp",EDGE,"E6.31.2"),sQuery(id+"F0.wireOp",EDGE,"E6.31.3"),sQuery(id+"F0.wireOp",EDGE,"E6.31.4"),sQuery(id+"F0.wireOp",EDGE,"E6.32.1"),sQuery(id+"F0.wireOp",EDGE,"E6.32.2"),sQuery(id+"F0.wireOp",EDGE,"E6.32.3"),sQuery(id+"F0.wireOp",EDGE,"E6.32.4"),sQuery(id+"F0.wireOp",EDGE,"E6.33.1"),sQuery(id+"F0.wireOp",EDGE,"E6.33.2"),sQuery(id+"F0.wireOp",EDGE,"E6.33.3"),sQuery(id+"F0.wireOp",EDGE,"E6.33.4"),sQuery(id+"F0.wireOp",EDGE,"E6.34.1"),sQuery(id+"F0.wireOp",EDGE,"E6.34.2"),sQuery(id+"F0.wireOp",EDGE,"E6.34.3"),sQuery(id+"F0.wireOp",EDGE,"E6.34.4"),sQuery(id+"F0.wireOp",EDGE,"E6.35.1"),sQuery(id+"F0.wireOp",EDGE,"E6.35.2"),sQuery(id+"F0.wireOp",EDGE,"E6.35.3"),sQuery(id+"F0.wireOp",EDGE,"E6.35.4"),sQuery(id+"F0.wireOp",EDGE,"E6.36.1"),sQuery(id+"F0.wireOp",EDGE,"E6.36.2"),sQuery(id+"F0.wireOp",EDGE,"E6.36.3"),sQuery(id+"F0.wireOp",EDGE,"E6.36.4"),sQuery(id+"F0.wireOp",EDGE,"E6.37.1"),sQuery(id+"F0.wireOp",EDGE,"E6.37.2"),sQuery(id+"F0.wireOp",EDGE,"E6.37.3"),sQuery(id+"F0.wireOp",EDGE,"E6.37.4"),sQuery(id+"F0.wireOp",EDGE,"E6.38.1"),sQuery(id+"F0.wireOp",EDGE,"E6.38.2"),sQuery(id+"F0.wireOp",EDGE,"E6.38.3"),sQuery(id+"F0.wireOp",EDGE,"E6.38.4"),sQuery(id+"F0.wireOp",EDGE,"E6.39.1"),sQuery(id+"F0.wireOp",EDGE,"E6.39.2"),sQuery(id+"F0.wireOp",EDGE,"E6.39.3"),sQuery(id+"F0.wireOp",EDGE,"E6.39.4"),sQuery(id+"F0.wireOp",EDGE,"E6.40.1"),sQuery(id+"F0.wireOp",EDGE,"E6.40.2"),sQuery(id+"F0.wireOp",EDGE,"E6.40.3"),sQuery(id+"F0.wireOp",EDGE,"E6.40.4"),sQuery(id+"F0.wireOp",EDGE,"E6.41.1"),sQuery(id+"F0.wireOp",EDGE,"E6.41.2"),sQuery(id+"F0.wireOp",EDGE,"E6.41.3"),sQuery(id+"F0.wireOp",EDGE,"E6.41.4"),sQuery(id+"F0.wireOp",EDGE,"E6.42.1"),sQuery(id+"F0.wireOp",EDGE,"E6.42.2"),sQuery(id+"F0.wireOp",EDGE,"E6.42.3"),sQuery(id+"F0.wireOp",EDGE,"E6.42.4"),sQuery(id+"F0.wireOp",EDGE,"E6.43.1"),sQuery(id+"F0.wireOp",EDGE,"E6.43.2"),sQuery(id+"F0.wireOp",EDGE,"E6.43.3"),sQuery(id+"F0.wireOp",EDGE,"E6.43.4"),sQuery(id+"F0.wireOp",EDGE,"E7"),sQuery(id+"F0.wireOp",EDGE,"E8.1.0"),sQuery(id+"F0.wireOp",EDGE,"E8.2.0"),sQuery(id+"F0.wireOp",EDGE,"E8.3.0"),sQuery(id+"F0.wireOp",EDGE,"E8.4.0"),sQuery(id+"F0.wireOp",EDGE,"E8.5.0"),sQuery(id+"F0.wireOp",EDGE,"E8.6.0"),sQuery(id+"F0.wireOp",EDGE,"E8.7.0"),sQuery(id+"F0.wireOp",EDGE,"E8.8.0"),sQuery(id+"F0.wireOp",EDGE,"E8.9.0"),sQuery(id+"F0.wireOp",EDGE,"E8.10.0"),sQuery(id+"F0.wireOp",EDGE,"E8.11.0"),sQuery(id+"F0.wireOp",EDGE,"E8.12.0"),sQuery(id+"F0.wireOp",EDGE,"E8.13.0"),sQuery(id+"F0.wireOp",EDGE,"E8.14.0"),sQuery(id+"F0.wireOp",EDGE,"E8.15.0"),sQuery(id+"F0.wireOp",EDGE,"E8.16.0"),sQuery(id+"F0.wireOp",EDGE,"E8.17.0"),sQuery(id+"F0.wireOp",EDGE,"E8.18.0"),sQuery(id+"F0.wireOp",EDGE,"E8.19.0"),sQuery(id+"F0.wireOp",EDGE,"E8.20.0"),sQuery(id+"F0.wireOp",EDGE,"E8.21.0"),sQuery(id+"F0.wireOp",EDGE,"E8.22.0"),sQuery(id+"F0.wireOp",EDGE,"E8.23.0"),sQuery(id+"F0.wireOp",EDGE,"E8.24.0"),sQuery(id+"F0.wireOp",EDGE,"E8.25.0"),sQuery(id+"F0.wireOp",EDGE,"E8.26.0"),sQuery(id+"F0.wireOp",EDGE,"E8.27.0"),sQuery(id+"F0.wireOp",EDGE,"E8.28.0"),sQuery(id+"F0.wireOp",EDGE,"E8.29.0"),sQuery(id+"F0.wireOp",EDGE,"E8.30.0"),sQuery(id+"F0.wireOp",EDGE,"E8.31.0"),sQuery(id+"F0.wireOp",EDGE,"E8.32.0"),sQuery(id+"F0.wireOp",EDGE,"E8.33.0"),sQuery(id+"F0.wireOp",EDGE,"E8.34.0"),sQuery(id+"F0.wireOp",EDGE,"E8.35.0"),sQuery(id+"F0.wireOp",EDGE,"E8.36.0"),sQuery(id+"F0.wireOp",EDGE,"E8.37.0"),sQuery(id+"F0.wireOp",EDGE,"E8.38.0"),sQuery(id+"F0.wireOp",EDGE,"E8.39.0"),sQuery(id+"F0.wireOp",EDGE,"E8.40.0"),sQuery(id+"F0.wireOp",EDGE,"E8.41.0"),sQuery(id+"F0.wireOp",EDGE,"E8.42.0"),sQuery(id+"F0.wireOp",EDGE,"E8.43.0")])],"isStart":false})]});}
            var Q17;
            {var subQ0=sQuery(id+"F0.wireOp",EDGE,"E6.13.3");var subQ1=sQuery(id+"F0.wireOp",EDGE,"E6.13.1");Q17=makeQuery(id+"F2.opFillet","BLEND_EDGE",EDGE,{"blendedFrom":[makeQuery(id+"F1.opExtrude","SWEPT_EDGE",EDGE,{"disambiguationData":[OSD([sQuery(id+"F0.wireOp",EDGE,"E6.13.0"),subQ1,subQ0])]}),makeQuery(id+"F1.opExtrude","CAP_FACE",FACE,{"disambiguationData":[OSD([sQuery(id+"F0.wireOp",EDGE,"E0"),sQuery(id+"F0.wireOp",EDGE,"E1"),sQuery(id+"F0.wireOp",EDGE,"E2"),sQuery(id+"F0.wireOp",EDGE,"E4"),sQuery(id+"F0.wireOp",EDGE,"E5"),sQuery(id+"F0.wireOp",EDGE,"E6.1.1"),sQuery(id+"F0.wireOp",EDGE,"E6.1.2"),sQuery(id+"F0.wireOp",EDGE,"E6.1.3"),sQuery(id+"F0.wireOp",EDGE,"E6.1.4"),sQuery(id+"F0.wireOp",EDGE,"E6.2.1"),sQuery(id+"F0.wireOp",EDGE,"E6.2.2"),sQuery(id+"F0.wireOp",EDGE,"E6.2.3"),sQuery(id+"F0.wireOp",EDGE,"E6.2.4"),sQuery(id+"F0.wireOp",EDGE,"E6.3.1"),sQuery(id+"F0.wireOp",EDGE,"E6.3.2"),sQuery(id+"F0.wireOp",EDGE,"E6.3.3"),sQuery(id+"F0.wireOp",EDGE,"E6.3.4"),sQuery(id+"F0.wireOp",EDGE,"E6.4.1"),sQuery(id+"F0.wireOp",EDGE,"E6.4.2"),sQuery(id+"F0.wireOp",EDGE,"E6.4.3"),sQuery(id+"F0.wireOp",EDGE,"E6.4.4"),sQuery(id+"F0.wireOp",EDGE,"E6.5.1"),sQuery(id+"F0.wireOp",EDGE,"E6.5.2"),sQuery(id+"F0.wireOp",EDGE,"E6.5.3"),sQuery(id+"F0.wireOp",EDGE,"E6.5.4"),sQuery(id+"F0.wireOp",EDGE,"E6.6.1"),sQuery(id+"F0.wireOp",EDGE,"E6.6.2"),sQuery(id+"F0.wireOp",EDGE,"E6.6.3"),sQuery(id+"F0.wireOp",EDGE,"E6.6.4"),sQuery(id+"F0.wireOp",EDGE,"E6.7.1"),sQuery(id+"F0.wireOp",EDGE,"E6.7.2"),sQuery(id+"F0.wireOp",EDGE,"E6.7.3"),sQuery(id+"F0.wireOp",EDGE,"E6.7.4"),sQuery(id+"F0.wireOp",EDGE,"E6.8.1"),sQuery(id+"F0.wireOp",EDGE,"E6.8.2"),sQuery(id+"F0.wireOp",EDGE,"E6.8.3"),sQuery(id+"F0.wireOp",EDGE,"E6.8.4"),sQuery(id+"F0.wireOp",EDGE,"E6.9.1"),sQuery(id+"F0.wireOp",EDGE,"E6.9.2"),sQuery(id+"F0.wireOp",EDGE,"E6.9.3"),sQuery(id+"F0.wireOp",EDGE,"E6.9.4"),sQuery(id+"F0.wireOp",EDGE,"E6.10.1"),sQuery(id+"F0.wireOp",EDGE,"E6.10.2"),sQuery(id+"F0.wireOp",EDGE,"E6.10.3"),sQuery(id+"F0.wireOp",EDGE,"E6.10.4"),sQuery(id+"F0.wireOp",EDGE,"E6.11.1"),sQuery(id+"F0.wireOp",EDGE,"E6.11.2"),sQuery(id+"F0.wireOp",EDGE,"E6.11.3"),sQuery(id+"F0.wireOp",EDGE,"E6.11.4"),sQuery(id+"F0.wireOp",EDGE,"E6.12.1"),sQuery(id+"F0.wireOp",EDGE,"E6.12.2"),sQuery(id+"F0.wireOp",EDGE,"E6.12.3"),sQuery(id+"F0.wireOp",EDGE,"E6.12.4"),subQ1,sQuery(id+"F0.wireOp",EDGE,"E6.13.2"),subQ0,sQuery(id+"F0.wireOp",EDGE,"E6.13.4"),sQuery(id+"F0.wireOp",EDGE,"E6.14.1"),sQuery(id+"F0.wireOp",EDGE,"E6.14.2"),sQuery(id+"F0.wireOp",EDGE,"E6.14.3"),sQuery(id+"F0.wireOp",EDGE,"E6.14.4"),sQuery(id+"F0.wireOp",EDGE,"E6.15.1"),sQuery(id+"F0.wireOp",EDGE,"E6.15.2"),sQuery(id+"F0.wireOp",EDGE,"E6.15.3"),sQuery(id+"F0.wireOp",EDGE,"E6.15.4"),sQuery(id+"F0.wireOp",EDGE,"E6.16.1"),sQuery(id+"F0.wireOp",EDGE,"E6.16.2"),sQuery(id+"F0.wireOp",EDGE,"E6.16.3"),sQuery(id+"F0.wireOp",EDGE,"E6.16.4"),sQuery(id+"F0.wireOp",EDGE,"E6.17.1"),sQuery(id+"F0.wireOp",EDGE,"E6.17.2"),sQuery(id+"F0.wireOp",EDGE,"E6.17.3"),sQuery(id+"F0.wireOp",EDGE,"E6.17.4"),sQuery(id+"F0.wireOp",EDGE,"E6.18.1"),sQuery(id+"F0.wireOp",EDGE,"E6.18.2"),sQuery(id+"F0.wireOp",EDGE,"E6.18.3"),sQuery(id+"F0.wireOp",EDGE,"E6.18.4"),sQuery(id+"F0.wireOp",EDGE,"E6.19.1"),sQuery(id+"F0.wireOp",EDGE,"E6.19.2"),sQuery(id+"F0.wireOp",EDGE,"E6.19.3"),sQuery(id+"F0.wireOp",EDGE,"E6.19.4"),sQuery(id+"F0.wireOp",EDGE,"E6.20.1"),sQuery(id+"F0.wireOp",EDGE,"E6.20.2"),sQuery(id+"F0.wireOp",EDGE,"E6.20.3"),sQuery(id+"F0.wireOp",EDGE,"E6.20.4"),sQuery(id+"F0.wireOp",EDGE,"E6.21.1"),sQuery(id+"F0.wireOp",EDGE,"E6.21.2"),sQuery(id+"F0.wireOp",EDGE,"E6.21.3"),sQuery(id+"F0.wireOp",EDGE,"E6.21.4"),sQuery(id+"F0.wireOp",EDGE,"E6.22.1"),sQuery(id+"F0.wireOp",EDGE,"E6.22.2"),sQuery(id+"F0.wireOp",EDGE,"E6.22.3"),sQuery(id+"F0.wireOp",EDGE,"E6.22.4"),sQuery(id+"F0.wireOp",EDGE,"E6.23.1"),sQuery(id+"F0.wireOp",EDGE,"E6.23.2"),sQuery(id+"F0.wireOp",EDGE,"E6.23.3"),sQuery(id+"F0.wireOp",EDGE,"E6.23.4"),sQuery(id+"F0.wireOp",EDGE,"E6.24.1"),sQuery(id+"F0.wireOp",EDGE,"E6.24.2"),sQuery(id+"F0.wireOp",EDGE,"E6.24.3"),sQuery(id+"F0.wireOp",EDGE,"E6.24.4"),sQuery(id+"F0.wireOp",EDGE,"E6.25.1"),sQuery(id+"F0.wireOp",EDGE,"E6.25.2"),sQuery(id+"F0.wireOp",EDGE,"E6.25.3"),sQuery(id+"F0.wireOp",EDGE,"E6.25.4"),sQuery(id+"F0.wireOp",EDGE,"E6.26.1"),sQuery(id+"F0.wireOp",EDGE,"E6.26.2"),sQuery(id+"F0.wireOp",EDGE,"E6.26.3"),sQuery(id+"F0.wireOp",EDGE,"E6.26.4"),sQuery(id+"F0.wireOp",EDGE,"E6.27.1"),sQuery(id+"F0.wireOp",EDGE,"E6.27.2"),sQuery(id+"F0.wireOp",EDGE,"E6.27.3"),sQuery(id+"F0.wireOp",EDGE,"E6.27.4"),sQuery(id+"F0.wireOp",EDGE,"E6.28.1"),sQuery(id+"F0.wireOp",EDGE,"E6.28.2"),sQuery(id+"F0.wireOp",EDGE,"E6.28.3"),sQuery(id+"F0.wireOp",EDGE,"E6.28.4"),sQuery(id+"F0.wireOp",EDGE,"E6.29.1"),sQuery(id+"F0.wireOp",EDGE,"E6.29.2"),sQuery(id+"F0.wireOp",EDGE,"E6.29.3"),sQuery(id+"F0.wireOp",EDGE,"E6.29.4"),sQuery(id+"F0.wireOp",EDGE,"E6.30.1"),sQuery(id+"F0.wireOp",EDGE,"E6.30.2"),sQuery(id+"F0.wireOp",EDGE,"E6.30.3"),sQuery(id+"F0.wireOp",EDGE,"E6.30.4"),sQuery(id+"F0.wireOp",EDGE,"E6.31.1"),sQuery(id+"F0.wireOp",EDGE,"E6.31.2"),sQuery(id+"F0.wireOp",EDGE,"E6.31.3"),sQuery(id+"F0.wireOp",EDGE,"E6.31.4"),sQuery(id+"F0.wireOp",EDGE,"E6.32.1"),sQuery(id+"F0.wireOp",EDGE,"E6.32.2"),sQuery(id+"F0.wireOp",EDGE,"E6.32.3"),sQuery(id+"F0.wireOp",EDGE,"E6.32.4"),sQuery(id+"F0.wireOp",EDGE,"E6.33.1"),sQuery(id+"F0.wireOp",EDGE,"E6.33.2"),sQuery(id+"F0.wireOp",EDGE,"E6.33.3"),sQuery(id+"F0.wireOp",EDGE,"E6.33.4"),sQuery(id+"F0.wireOp",EDGE,"E6.34.1"),sQuery(id+"F0.wireOp",EDGE,"E6.34.2"),sQuery(id+"F0.wireOp",EDGE,"E6.34.3"),sQuery(id+"F0.wireOp",EDGE,"E6.34.4"),sQuery(id+"F0.wireOp",EDGE,"E6.35.1"),sQuery(id+"F0.wireOp",EDGE,"E6.35.2"),sQuery(id+"F0.wireOp",EDGE,"E6.35.3"),sQuery(id+"F0.wireOp",EDGE,"E6.35.4"),sQuery(id+"F0.wireOp",EDGE,"E6.36.1"),sQuery(id+"F0.wireOp",EDGE,"E6.36.2"),sQuery(id+"F0.wireOp",EDGE,"E6.36.3"),sQuery(id+"F0.wireOp",EDGE,"E6.36.4"),sQuery(id+"F0.wireOp",EDGE,"E6.37.1"),sQuery(id+"F0.wireOp",EDGE,"E6.37.2"),sQuery(id+"F0.wireOp",EDGE,"E6.37.3"),sQuery(id+"F0.wireOp",EDGE,"E6.37.4"),sQuery(id+"F0.wireOp",EDGE,"E6.38.1"),sQuery(id+"F0.wireOp",EDGE,"E6.38.2"),sQuery(id+"F0.wireOp",EDGE,"E6.38.3"),sQuery(id+"F0.wireOp",EDGE,"E6.38.4"),sQuery(id+"F0.wireOp",EDGE,"E6.39.1"),sQuery(id+"F0.wireOp",EDGE,"E6.39.2"),sQuery(id+"F0.wireOp",EDGE,"E6.39.3"),sQuery(id+"F0.wireOp",EDGE,"E6.39.4"),sQuery(id+"F0.wireOp",EDGE,"E6.40.1"),sQuery(id+"F0.wireOp",EDGE,"E6.40.2"),sQuery(id+"F0.wireOp",EDGE,"E6.40.3"),sQuery(id+"F0.wireOp",EDGE,"E6.40.4"),sQuery(id+"F0.wireOp",EDGE,"E6.41.1"),sQuery(id+"F0.wireOp",EDGE,"E6.41.2"),sQuery(id+"F0.wireOp",EDGE,"E6.41.3"),sQuery(id+"F0.wireOp",EDGE,"E6.41.4"),sQuery(id+"F0.wireOp",EDGE,"E6.42.1"),sQuery(id+"F0.wireOp",EDGE,"E6.42.2"),sQuery(id+"F0.wireOp",EDGE,"E6.42.3"),sQuery(id+"F0.wireOp",EDGE,"E6.42.4"),sQuery(id+"F0.wireOp",EDGE,"E6.43.1"),sQuery(id+"F0.wireOp",EDGE,"E6.43.2"),sQuery(id+"F0.wireOp",EDGE,"E6.43.3"),sQuery(id+"F0.wireOp",EDGE,"E6.43.4"),sQuery(id+"F0.wireOp",EDGE,"E7"),sQuery(id+"F0.wireOp",EDGE,"E8.1.0"),sQuery(id+"F0.wireOp",EDGE,"E8.2.0"),sQuery(id+"F0.wireOp",EDGE,"E8.3.0"),sQuery(id+"F0.wireOp",EDGE,"E8.4.0"),sQuery(id+"F0.wireOp",EDGE,"E8.5.0"),sQuery(id+"F0.wireOp",EDGE,"E8.6.0"),sQuery(id+"F0.wireOp",EDGE,"E8.7.0"),sQuery(id+"F0.wireOp",EDGE,"E8.8.0"),sQuery(id+"F0.wireOp",EDGE,"E8.9.0"),sQuery(id+"F0.wireOp",EDGE,"E8.10.0"),sQuery(id+"F0.wireOp",EDGE,"E8.11.0"),sQuery(id+"F0.wireOp",EDGE,"E8.12.0"),sQuery(id+"F0.wireOp",EDGE,"E8.13.0"),sQuery(id+"F0.wireOp",EDGE,"E8.14.0"),sQuery(id+"F0.wireOp",EDGE,"E8.15.0"),sQuery(id+"F0.wireOp",EDGE,"E8.16.0"),sQuery(id+"F0.wireOp",EDGE,"E8.17.0"),sQuery(id+"F0.wireOp",EDGE,"E8.18.0"),sQuery(id+"F0.wireOp",EDGE,"E8.19.0"),sQuery(id+"F0.wireOp",EDGE,"E8.20.0"),sQuery(id+"F0.wireOp",EDGE,"E8.21.0"),sQuery(id+"F0.wireOp",EDGE,"E8.22.0"),sQuery(id+"F0.wireOp",EDGE,"E8.23.0"),sQuery(id+"F0.wireOp",EDGE,"E8.24.0"),sQuery(id+"F0.wireOp",EDGE,"E8.25.0"),sQuery(id+"F0.wireOp",EDGE,"E8.26.0"),sQuery(id+"F0.wireOp",EDGE,"E8.27.0"),sQuery(id+"F0.wireOp",EDGE,"E8.28.0"),sQuery(id+"F0.wireOp",EDGE,"E8.29.0"),sQuery(id+"F0.wireOp",EDGE,"E8.30.0"),sQuery(id+"F0.wireOp",EDGE,"E8.31.0"),sQuery(id+"F0.wireOp",EDGE,"E8.32.0"),sQuery(id+"F0.wireOp",EDGE,"E8.33.0"),sQuery(id+"F0.wireOp",EDGE,"E8.34.0"),sQuery(id+"F0.wireOp",EDGE,"E8.35.0"),sQuery(id+"F0.wireOp",EDGE,"E8.36.0"),sQuery(id+"F0.wireOp",EDGE,"E8.37.0"),sQuery(id+"F0.wireOp",EDGE,"E8.38.0"),sQuery(id+"F0.wireOp",EDGE,"E8.39.0"),sQuery(id+"F0.wireOp",EDGE,"E8.40.0"),sQuery(id+"F0.wireOp",EDGE,"E8.41.0"),sQuery(id+"F0.wireOp",EDGE,"E8.42.0"),sQuery(id+"F0.wireOp",EDGE,"E8.43.0")])],"isStart":false})],"blendedInto":[makeQuery(id+"F1.opExtrude","CAP_FACE",FACE,{"disambiguationData":[OSD([sQuery(id+"F0.wireOp",EDGE,"E0"),sQuery(id+"F0.wireOp",EDGE,"E1"),sQuery(id+"F0.wireOp",EDGE,"E2"),sQuery(id+"F0.wireOp",EDGE,"E4"),sQuery(id+"F0.wireOp",EDGE,"E5"),sQuery(id+"F0.wireOp",EDGE,"E6.1.1"),sQuery(id+"F0.wireOp",EDGE,"E6.1.2"),sQuery(id+"F0.wireOp",EDGE,"E6.1.3"),sQuery(id+"F0.wireOp",EDGE,"E6.1.4"),sQuery(id+"F0.wireOp",EDGE,"E6.2.1"),sQuery(id+"F0.wireOp",EDGE,"E6.2.2"),sQuery(id+"F0.wireOp",EDGE,"E6.2.3"),sQuery(id+"F0.wireOp",EDGE,"E6.2.4"),sQuery(id+"F0.wireOp",EDGE,"E6.3.1"),sQuery(id+"F0.wireOp",EDGE,"E6.3.2"),sQuery(id+"F0.wireOp",EDGE,"E6.3.3"),sQuery(id+"F0.wireOp",EDGE,"E6.3.4"),sQuery(id+"F0.wireOp",EDGE,"E6.4.1"),sQuery(id+"F0.wireOp",EDGE,"E6.4.2"),sQuery(id+"F0.wireOp",EDGE,"E6.4.3"),sQuery(id+"F0.wireOp",EDGE,"E6.4.4"),sQuery(id+"F0.wireOp",EDGE,"E6.5.1"),sQuery(id+"F0.wireOp",EDGE,"E6.5.2"),sQuery(id+"F0.wireOp",EDGE,"E6.5.3"),sQuery(id+"F0.wireOp",EDGE,"E6.5.4"),sQuery(id+"F0.wireOp",EDGE,"E6.6.1"),sQuery(id+"F0.wireOp",EDGE,"E6.6.2"),sQuery(id+"F0.wireOp",EDGE,"E6.6.3"),sQuery(id+"F0.wireOp",EDGE,"E6.6.4"),sQuery(id+"F0.wireOp",EDGE,"E6.7.1"),sQuery(id+"F0.wireOp",EDGE,"E6.7.2"),sQuery(id+"F0.wireOp",EDGE,"E6.7.3"),sQuery(id+"F0.wireOp",EDGE,"E6.7.4"),sQuery(id+"F0.wireOp",EDGE,"E6.8.1"),sQuery(id+"F0.wireOp",EDGE,"E6.8.2"),sQuery(id+"F0.wireOp",EDGE,"E6.8.3"),sQuery(id+"F0.wireOp",EDGE,"E6.8.4"),sQuery(id+"F0.wireOp",EDGE,"E6.9.1"),sQuery(id+"F0.wireOp",EDGE,"E6.9.2"),sQuery(id+"F0.wireOp",EDGE,"E6.9.3"),sQuery(id+"F0.wireOp",EDGE,"E6.9.4"),sQuery(id+"F0.wireOp",EDGE,"E6.10.1"),sQuery(id+"F0.wireOp",EDGE,"E6.10.2"),sQuery(id+"F0.wireOp",EDGE,"E6.10.3"),sQuery(id+"F0.wireOp",EDGE,"E6.10.4"),sQuery(id+"F0.wireOp",EDGE,"E6.11.1"),sQuery(id+"F0.wireOp",EDGE,"E6.11.2"),sQuery(id+"F0.wireOp",EDGE,"E6.11.3"),sQuery(id+"F0.wireOp",EDGE,"E6.11.4"),sQuery(id+"F0.wireOp",EDGE,"E6.12.1"),sQuery(id+"F0.wireOp",EDGE,"E6.12.2"),sQuery(id+"F0.wireOp",EDGE,"E6.12.3"),sQuery(id+"F0.wireOp",EDGE,"E6.12.4"),subQ1,sQuery(id+"F0.wireOp",EDGE,"E6.13.2"),subQ0,sQuery(id+"F0.wireOp",EDGE,"E6.13.4"),sQuery(id+"F0.wireOp",EDGE,"E6.14.1"),sQuery(id+"F0.wireOp",EDGE,"E6.14.2"),sQuery(id+"F0.wireOp",EDGE,"E6.14.3"),sQuery(id+"F0.wireOp",EDGE,"E6.14.4"),sQuery(id+"F0.wireOp",EDGE,"E6.15.1"),sQuery(id+"F0.wireOp",EDGE,"E6.15.2"),sQuery(id+"F0.wireOp",EDGE,"E6.15.3"),sQuery(id+"F0.wireOp",EDGE,"E6.15.4"),sQuery(id+"F0.wireOp",EDGE,"E6.16.1"),sQuery(id+"F0.wireOp",EDGE,"E6.16.2"),sQuery(id+"F0.wireOp",EDGE,"E6.16.3"),sQuery(id+"F0.wireOp",EDGE,"E6.16.4"),sQuery(id+"F0.wireOp",EDGE,"E6.17.1"),sQuery(id+"F0.wireOp",EDGE,"E6.17.2"),sQuery(id+"F0.wireOp",EDGE,"E6.17.3"),sQuery(id+"F0.wireOp",EDGE,"E6.17.4"),sQuery(id+"F0.wireOp",EDGE,"E6.18.1"),sQuery(id+"F0.wireOp",EDGE,"E6.18.2"),sQuery(id+"F0.wireOp",EDGE,"E6.18.3"),sQuery(id+"F0.wireOp",EDGE,"E6.18.4"),sQuery(id+"F0.wireOp",EDGE,"E6.19.1"),sQuery(id+"F0.wireOp",EDGE,"E6.19.2"),sQuery(id+"F0.wireOp",EDGE,"E6.19.3"),sQuery(id+"F0.wireOp",EDGE,"E6.19.4"),sQuery(id+"F0.wireOp",EDGE,"E6.20.1"),sQuery(id+"F0.wireOp",EDGE,"E6.20.2"),sQuery(id+"F0.wireOp",EDGE,"E6.20.3"),sQuery(id+"F0.wireOp",EDGE,"E6.20.4"),sQuery(id+"F0.wireOp",EDGE,"E6.21.1"),sQuery(id+"F0.wireOp",EDGE,"E6.21.2"),sQuery(id+"F0.wireOp",EDGE,"E6.21.3"),sQuery(id+"F0.wireOp",EDGE,"E6.21.4"),sQuery(id+"F0.wireOp",EDGE,"E6.22.1"),sQuery(id+"F0.wireOp",EDGE,"E6.22.2"),sQuery(id+"F0.wireOp",EDGE,"E6.22.3"),sQuery(id+"F0.wireOp",EDGE,"E6.22.4"),sQuery(id+"F0.wireOp",EDGE,"E6.23.1"),sQuery(id+"F0.wireOp",EDGE,"E6.23.2"),sQuery(id+"F0.wireOp",EDGE,"E6.23.3"),sQuery(id+"F0.wireOp",EDGE,"E6.23.4"),sQuery(id+"F0.wireOp",EDGE,"E6.24.1"),sQuery(id+"F0.wireOp",EDGE,"E6.24.2"),sQuery(id+"F0.wireOp",EDGE,"E6.24.3"),sQuery(id+"F0.wireOp",EDGE,"E6.24.4"),sQuery(id+"F0.wireOp",EDGE,"E6.25.1"),sQuery(id+"F0.wireOp",EDGE,"E6.25.2"),sQuery(id+"F0.wireOp",EDGE,"E6.25.3"),sQuery(id+"F0.wireOp",EDGE,"E6.25.4"),sQuery(id+"F0.wireOp",EDGE,"E6.26.1"),sQuery(id+"F0.wireOp",EDGE,"E6.26.2"),sQuery(id+"F0.wireOp",EDGE,"E6.26.3"),sQuery(id+"F0.wireOp",EDGE,"E6.26.4"),sQuery(id+"F0.wireOp",EDGE,"E6.27.1"),sQuery(id+"F0.wireOp",EDGE,"E6.27.2"),sQuery(id+"F0.wireOp",EDGE,"E6.27.3"),sQuery(id+"F0.wireOp",EDGE,"E6.27.4"),sQuery(id+"F0.wireOp",EDGE,"E6.28.1"),sQuery(id+"F0.wireOp",EDGE,"E6.28.2"),sQuery(id+"F0.wireOp",EDGE,"E6.28.3"),sQuery(id+"F0.wireOp",EDGE,"E6.28.4"),sQuery(id+"F0.wireOp",EDGE,"E6.29.1"),sQuery(id+"F0.wireOp",EDGE,"E6.29.2"),sQuery(id+"F0.wireOp",EDGE,"E6.29.3"),sQuery(id+"F0.wireOp",EDGE,"E6.29.4"),sQuery(id+"F0.wireOp",EDGE,"E6.30.1"),sQuery(id+"F0.wireOp",EDGE,"E6.30.2"),sQuery(id+"F0.wireOp",EDGE,"E6.30.3"),sQuery(id+"F0.wireOp",EDGE,"E6.30.4"),sQuery(id+"F0.wireOp",EDGE,"E6.31.1"),sQuery(id+"F0.wireOp",EDGE,"E6.31.2"),sQuery(id+"F0.wireOp",EDGE,"E6.31.3"),sQuery(id+"F0.wireOp",EDGE,"E6.31.4"),sQuery(id+"F0.wireOp",EDGE,"E6.32.1"),sQuery(id+"F0.wireOp",EDGE,"E6.32.2"),sQuery(id+"F0.wireOp",EDGE,"E6.32.3"),sQuery(id+"F0.wireOp",EDGE,"E6.32.4"),sQuery(id+"F0.wireOp",EDGE,"E6.33.1"),sQuery(id+"F0.wireOp",EDGE,"E6.33.2"),sQuery(id+"F0.wireOp",EDGE,"E6.33.3"),sQuery(id+"F0.wireOp",EDGE,"E6.33.4"),sQuery(id+"F0.wireOp",EDGE,"E6.34.1"),sQuery(id+"F0.wireOp",EDGE,"E6.34.2"),sQuery(id+"F0.wireOp",EDGE,"E6.34.3"),sQuery(id+"F0.wireOp",EDGE,"E6.34.4"),sQuery(id+"F0.wireOp",EDGE,"E6.35.1"),sQuery(id+"F0.wireOp",EDGE,"E6.35.2"),sQuery(id+"F0.wireOp",EDGE,"E6.35.3"),sQuery(id+"F0.wireOp",EDGE,"E6.35.4"),sQuery(id+"F0.wireOp",EDGE,"E6.36.1"),sQuery(id+"F0.wireOp",EDGE,"E6.36.2"),sQuery(id+"F0.wireOp",EDGE,"E6.36.3"),sQuery(id+"F0.wireOp",EDGE,"E6.36.4"),sQuery(id+"F0.wireOp",EDGE,"E6.37.1"),sQuery(id+"F0.wireOp",EDGE,"E6.37.2"),sQuery(id+"F0.wireOp",EDGE,"E6.37.3"),sQuery(id+"F0.wireOp",EDGE,"E6.37.4"),sQuery(id+"F0.wireOp",EDGE,"E6.38.1"),sQuery(id+"F0.wireOp",EDGE,"E6.38.2"),sQuery(id+"F0.wireOp",EDGE,"E6.38.3"),sQuery(id+"F0.wireOp",EDGE,"E6.38.4"),sQuery(id+"F0.wireOp",EDGE,"E6.39.1"),sQuery(id+"F0.wireOp",EDGE,"E6.39.2"),sQuery(id+"F0.wireOp",EDGE,"E6.39.3"),sQuery(id+"F0.wireOp",EDGE,"E6.39.4"),sQuery(id+"F0.wireOp",EDGE,"E6.40.1"),sQuery(id+"F0.wireOp",EDGE,"E6.40.2"),sQuery(id+"F0.wireOp",EDGE,"E6.40.3"),sQuery(id+"F0.wireOp",EDGE,"E6.40.4"),sQuery(id+"F0.wireOp",EDGE,"E6.41.1"),sQuery(id+"F0.wireOp",EDGE,"E6.41.2"),sQuery(id+"F0.wireOp",EDGE,"E6.41.3"),sQuery(id+"F0.wireOp",EDGE,"E6.41.4"),sQuery(id+"F0.wireOp",EDGE,"E6.42.1"),sQuery(id+"F0.wireOp",EDGE,"E6.42.2"),sQuery(id+"F0.wireOp",EDGE,"E6.42.3"),sQuery(id+"F0.wireOp",EDGE,"E6.42.4"),sQuery(id+"F0.wireOp",EDGE,"E6.43.1"),sQuery(id+"F0.wireOp",EDGE,"E6.43.2"),sQuery(id+"F0.wireOp",EDGE,"E6.43.3"),sQuery(id+"F0.wireOp",EDGE,"E6.43.4"),sQuery(id+"F0.wireOp",EDGE,"E7"),sQuery(id+"F0.wireOp",EDGE,"E8.1.0"),sQuery(id+"F0.wireOp",EDGE,"E8.2.0"),sQuery(id+"F0.wireOp",EDGE,"E8.3.0"),sQuery(id+"F0.wireOp",EDGE,"E8.4.0"),sQuery(id+"F0.wireOp",EDGE,"E8.5.0"),sQuery(id+"F0.wireOp",EDGE,"E8.6.0"),sQuery(id+"F0.wireOp",EDGE,"E8.7.0"),sQuery(id+"F0.wireOp",EDGE,"E8.8.0"),sQuery(id+"F0.wireOp",EDGE,"E8.9.0"),sQuery(id+"F0.wireOp",EDGE,"E8.10.0"),sQuery(id+"F0.wireOp",EDGE,"E8.11.0"),sQuery(id+"F0.wireOp",EDGE,"E8.12.0"),sQuery(id+"F0.wireOp",EDGE,"E8.13.0"),sQuery(id+"F0.wireOp",EDGE,"E8.14.0"),sQuery(id+"F0.wireOp",EDGE,"E8.15.0"),sQuery(id+"F0.wireOp",EDGE,"E8.16.0"),sQuery(id+"F0.wireOp",EDGE,"E8.17.0"),sQuery(id+"F0.wireOp",EDGE,"E8.18.0"),sQuery(id+"F0.wireOp",EDGE,"E8.19.0"),sQuery(id+"F0.wireOp",EDGE,"E8.20.0"),sQuery(id+"F0.wireOp",EDGE,"E8.21.0"),sQuery(id+"F0.wireOp",EDGE,"E8.22.0"),sQuery(id+"F0.wireOp",EDGE,"E8.23.0"),sQuery(id+"F0.wireOp",EDGE,"E8.24.0"),sQuery(id+"F0.wireOp",EDGE,"E8.25.0"),sQuery(id+"F0.wireOp",EDGE,"E8.26.0"),sQuery(id+"F0.wireOp",EDGE,"E8.27.0"),sQuery(id+"F0.wireOp",EDGE,"E8.28.0"),sQuery(id+"F0.wireOp",EDGE,"E8.29.0"),sQuery(id+"F0.wireOp",EDGE,"E8.30.0"),sQuery(id+"F0.wireOp",EDGE,"E8.31.0"),sQuery(id+"F0.wireOp",EDGE,"E8.32.0"),sQuery(id+"F0.wireOp",EDGE,"E8.33.0"),sQuery(id+"F0.wireOp",EDGE,"E8.34.0"),sQuery(id+"F0.wireOp",EDGE,"E8.35.0"),sQuery(id+"F0.wireOp",EDGE,"E8.36.0"),sQuery(id+"F0.wireOp",EDGE,"E8.37.0"),sQuery(id+"F0.wireOp",EDGE,"E8.38.0"),sQuery(id+"F0.wireOp",EDGE,"E8.39.0"),sQuery(id+"F0.wireOp",EDGE,"E8.40.0"),sQuery(id+"F0.wireOp",EDGE,"E8.41.0"),sQuery(id+"F0.wireOp",EDGE,"E8.42.0"),sQuery(id+"F0.wireOp",EDGE,"E8.43.0")])],"isStart":false})]});}
            var Q18;
            {var subQ0=sQuery(id+"F0.wireOp",EDGE,"E6.15.3");var subQ1=sQuery(id+"F0.wireOp",EDGE,"E6.15.1");Q18=makeQuery(id+"F2.opFillet","BLEND_EDGE",EDGE,{"blendedFrom":[makeQuery(id+"F1.opExtrude","SWEPT_EDGE",EDGE,{"disambiguationData":[OSD([sQuery(id+"F0.wireOp",EDGE,"E6.15.0"),subQ1,subQ0])]}),makeQuery(id+"F1.opExtrude","CAP_FACE",FACE,{"disambiguationData":[OSD([sQuery(id+"F0.wireOp",EDGE,"E0"),sQuery(id+"F0.wireOp",EDGE,"E1"),sQuery(id+"F0.wireOp",EDGE,"E2"),sQuery(id+"F0.wireOp",EDGE,"E4"),sQuery(id+"F0.wireOp",EDGE,"E5"),sQuery(id+"F0.wireOp",EDGE,"E6.1.1"),sQuery(id+"F0.wireOp",EDGE,"E6.1.2"),sQuery(id+"F0.wireOp",EDGE,"E6.1.3"),sQuery(id+"F0.wireOp",EDGE,"E6.1.4"),sQuery(id+"F0.wireOp",EDGE,"E6.2.1"),sQuery(id+"F0.wireOp",EDGE,"E6.2.2"),sQuery(id+"F0.wireOp",EDGE,"E6.2.3"),sQuery(id+"F0.wireOp",EDGE,"E6.2.4"),sQuery(id+"F0.wireOp",EDGE,"E6.3.1"),sQuery(id+"F0.wireOp",EDGE,"E6.3.2"),sQuery(id+"F0.wireOp",EDGE,"E6.3.3"),sQuery(id+"F0.wireOp",EDGE,"E6.3.4"),sQuery(id+"F0.wireOp",EDGE,"E6.4.1"),sQuery(id+"F0.wireOp",EDGE,"E6.4.2"),sQuery(id+"F0.wireOp",EDGE,"E6.4.3"),sQuery(id+"F0.wireOp",EDGE,"E6.4.4"),sQuery(id+"F0.wireOp",EDGE,"E6.5.1"),sQuery(id+"F0.wireOp",EDGE,"E6.5.2"),sQuery(id+"F0.wireOp",EDGE,"E6.5.3"),sQuery(id+"F0.wireOp",EDGE,"E6.5.4"),sQuery(id+"F0.wireOp",EDGE,"E6.6.1"),sQuery(id+"F0.wireOp",EDGE,"E6.6.2"),sQuery(id+"F0.wireOp",EDGE,"E6.6.3"),sQuery(id+"F0.wireOp",EDGE,"E6.6.4"),sQuery(id+"F0.wireOp",EDGE,"E6.7.1"),sQuery(id+"F0.wireOp",EDGE,"E6.7.2"),sQuery(id+"F0.wireOp",EDGE,"E6.7.3"),sQuery(id+"F0.wireOp",EDGE,"E6.7.4"),sQuery(id+"F0.wireOp",EDGE,"E6.8.1"),sQuery(id+"F0.wireOp",EDGE,"E6.8.2"),sQuery(id+"F0.wireOp",EDGE,"E6.8.3"),sQuery(id+"F0.wireOp",EDGE,"E6.8.4"),sQuery(id+"F0.wireOp",EDGE,"E6.9.1"),sQuery(id+"F0.wireOp",EDGE,"E6.9.2"),sQuery(id+"F0.wireOp",EDGE,"E6.9.3"),sQuery(id+"F0.wireOp",EDGE,"E6.9.4"),sQuery(id+"F0.wireOp",EDGE,"E6.10.1"),sQuery(id+"F0.wireOp",EDGE,"E6.10.2"),sQuery(id+"F0.wireOp",EDGE,"E6.10.3"),sQuery(id+"F0.wireOp",EDGE,"E6.10.4"),sQuery(id+"F0.wireOp",EDGE,"E6.11.1"),sQuery(id+"F0.wireOp",EDGE,"E6.11.2"),sQuery(id+"F0.wireOp",EDGE,"E6.11.3"),sQuery(id+"F0.wireOp",EDGE,"E6.11.4"),sQuery(id+"F0.wireOp",EDGE,"E6.12.1"),sQuery(id+"F0.wireOp",EDGE,"E6.12.2"),sQuery(id+"F0.wireOp",EDGE,"E6.12.3"),sQuery(id+"F0.wireOp",EDGE,"E6.12.4"),sQuery(id+"F0.wireOp",EDGE,"E6.13.1"),sQuery(id+"F0.wireOp",EDGE,"E6.13.2"),sQuery(id+"F0.wireOp",EDGE,"E6.13.3"),sQuery(id+"F0.wireOp",EDGE,"E6.13.4"),sQuery(id+"F0.wireOp",EDGE,"E6.14.1"),sQuery(id+"F0.wireOp",EDGE,"E6.14.2"),sQuery(id+"F0.wireOp",EDGE,"E6.14.3"),sQuery(id+"F0.wireOp",EDGE,"E6.14.4"),subQ1,sQuery(id+"F0.wireOp",EDGE,"E6.15.2"),subQ0,sQuery(id+"F0.wireOp",EDGE,"E6.15.4"),sQuery(id+"F0.wireOp",EDGE,"E6.16.1"),sQuery(id+"F0.wireOp",EDGE,"E6.16.2"),sQuery(id+"F0.wireOp",EDGE,"E6.16.3"),sQuery(id+"F0.wireOp",EDGE,"E6.16.4"),sQuery(id+"F0.wireOp",EDGE,"E6.17.1"),sQuery(id+"F0.wireOp",EDGE,"E6.17.2"),sQuery(id+"F0.wireOp",EDGE,"E6.17.3"),sQuery(id+"F0.wireOp",EDGE,"E6.17.4"),sQuery(id+"F0.wireOp",EDGE,"E6.18.1"),sQuery(id+"F0.wireOp",EDGE,"E6.18.2"),sQuery(id+"F0.wireOp",EDGE,"E6.18.3"),sQuery(id+"F0.wireOp",EDGE,"E6.18.4"),sQuery(id+"F0.wireOp",EDGE,"E6.19.1"),sQuery(id+"F0.wireOp",EDGE,"E6.19.2"),sQuery(id+"F0.wireOp",EDGE,"E6.19.3"),sQuery(id+"F0.wireOp",EDGE,"E6.19.4"),sQuery(id+"F0.wireOp",EDGE,"E6.20.1"),sQuery(id+"F0.wireOp",EDGE,"E6.20.2"),sQuery(id+"F0.wireOp",EDGE,"E6.20.3"),sQuery(id+"F0.wireOp",EDGE,"E6.20.4"),sQuery(id+"F0.wireOp",EDGE,"E6.21.1"),sQuery(id+"F0.wireOp",EDGE,"E6.21.2"),sQuery(id+"F0.wireOp",EDGE,"E6.21.3"),sQuery(id+"F0.wireOp",EDGE,"E6.21.4"),sQuery(id+"F0.wireOp",EDGE,"E6.22.1"),sQuery(id+"F0.wireOp",EDGE,"E6.22.2"),sQuery(id+"F0.wireOp",EDGE,"E6.22.3"),sQuery(id+"F0.wireOp",EDGE,"E6.22.4"),sQuery(id+"F0.wireOp",EDGE,"E6.23.1"),sQuery(id+"F0.wireOp",EDGE,"E6.23.2"),sQuery(id+"F0.wireOp",EDGE,"E6.23.3"),sQuery(id+"F0.wireOp",EDGE,"E6.23.4"),sQuery(id+"F0.wireOp",EDGE,"E6.24.1"),sQuery(id+"F0.wireOp",EDGE,"E6.24.2"),sQuery(id+"F0.wireOp",EDGE,"E6.24.3"),sQuery(id+"F0.wireOp",EDGE,"E6.24.4"),sQuery(id+"F0.wireOp",EDGE,"E6.25.1"),sQuery(id+"F0.wireOp",EDGE,"E6.25.2"),sQuery(id+"F0.wireOp",EDGE,"E6.25.3"),sQuery(id+"F0.wireOp",EDGE,"E6.25.4"),sQuery(id+"F0.wireOp",EDGE,"E6.26.1"),sQuery(id+"F0.wireOp",EDGE,"E6.26.2"),sQuery(id+"F0.wireOp",EDGE,"E6.26.3"),sQuery(id+"F0.wireOp",EDGE,"E6.26.4"),sQuery(id+"F0.wireOp",EDGE,"E6.27.1"),sQuery(id+"F0.wireOp",EDGE,"E6.27.2"),sQuery(id+"F0.wireOp",EDGE,"E6.27.3"),sQuery(id+"F0.wireOp",EDGE,"E6.27.4"),sQuery(id+"F0.wireOp",EDGE,"E6.28.1"),sQuery(id+"F0.wireOp",EDGE,"E6.28.2"),sQuery(id+"F0.wireOp",EDGE,"E6.28.3"),sQuery(id+"F0.wireOp",EDGE,"E6.28.4"),sQuery(id+"F0.wireOp",EDGE,"E6.29.1"),sQuery(id+"F0.wireOp",EDGE,"E6.29.2"),sQuery(id+"F0.wireOp",EDGE,"E6.29.3"),sQuery(id+"F0.wireOp",EDGE,"E6.29.4"),sQuery(id+"F0.wireOp",EDGE,"E6.30.1"),sQuery(id+"F0.wireOp",EDGE,"E6.30.2"),sQuery(id+"F0.wireOp",EDGE,"E6.30.3"),sQuery(id+"F0.wireOp",EDGE,"E6.30.4"),sQuery(id+"F0.wireOp",EDGE,"E6.31.1"),sQuery(id+"F0.wireOp",EDGE,"E6.31.2"),sQuery(id+"F0.wireOp",EDGE,"E6.31.3"),sQuery(id+"F0.wireOp",EDGE,"E6.31.4"),sQuery(id+"F0.wireOp",EDGE,"E6.32.1"),sQuery(id+"F0.wireOp",EDGE,"E6.32.2"),sQuery(id+"F0.wireOp",EDGE,"E6.32.3"),sQuery(id+"F0.wireOp",EDGE,"E6.32.4"),sQuery(id+"F0.wireOp",EDGE,"E6.33.1"),sQuery(id+"F0.wireOp",EDGE,"E6.33.2"),sQuery(id+"F0.wireOp",EDGE,"E6.33.3"),sQuery(id+"F0.wireOp",EDGE,"E6.33.4"),sQuery(id+"F0.wireOp",EDGE,"E6.34.1"),sQuery(id+"F0.wireOp",EDGE,"E6.34.2"),sQuery(id+"F0.wireOp",EDGE,"E6.34.3"),sQuery(id+"F0.wireOp",EDGE,"E6.34.4"),sQuery(id+"F0.wireOp",EDGE,"E6.35.1"),sQuery(id+"F0.wireOp",EDGE,"E6.35.2"),sQuery(id+"F0.wireOp",EDGE,"E6.35.3"),sQuery(id+"F0.wireOp",EDGE,"E6.35.4"),sQuery(id+"F0.wireOp",EDGE,"E6.36.1"),sQuery(id+"F0.wireOp",EDGE,"E6.36.2"),sQuery(id+"F0.wireOp",EDGE,"E6.36.3"),sQuery(id+"F0.wireOp",EDGE,"E6.36.4"),sQuery(id+"F0.wireOp",EDGE,"E6.37.1"),sQuery(id+"F0.wireOp",EDGE,"E6.37.2"),sQuery(id+"F0.wireOp",EDGE,"E6.37.3"),sQuery(id+"F0.wireOp",EDGE,"E6.37.4"),sQuery(id+"F0.wireOp",EDGE,"E6.38.1"),sQuery(id+"F0.wireOp",EDGE,"E6.38.2"),sQuery(id+"F0.wireOp",EDGE,"E6.38.3"),sQuery(id+"F0.wireOp",EDGE,"E6.38.4"),sQuery(id+"F0.wireOp",EDGE,"E6.39.1"),sQuery(id+"F0.wireOp",EDGE,"E6.39.2"),sQuery(id+"F0.wireOp",EDGE,"E6.39.3"),sQuery(id+"F0.wireOp",EDGE,"E6.39.4"),sQuery(id+"F0.wireOp",EDGE,"E6.40.1"),sQuery(id+"F0.wireOp",EDGE,"E6.40.2"),sQuery(id+"F0.wireOp",EDGE,"E6.40.3"),sQuery(id+"F0.wireOp",EDGE,"E6.40.4"),sQuery(id+"F0.wireOp",EDGE,"E6.41.1"),sQuery(id+"F0.wireOp",EDGE,"E6.41.2"),sQuery(id+"F0.wireOp",EDGE,"E6.41.3"),sQuery(id+"F0.wireOp",EDGE,"E6.41.4"),sQuery(id+"F0.wireOp",EDGE,"E6.42.1"),sQuery(id+"F0.wireOp",EDGE,"E6.42.2"),sQuery(id+"F0.wireOp",EDGE,"E6.42.3"),sQuery(id+"F0.wireOp",EDGE,"E6.42.4"),sQuery(id+"F0.wireOp",EDGE,"E6.43.1"),sQuery(id+"F0.wireOp",EDGE,"E6.43.2"),sQuery(id+"F0.wireOp",EDGE,"E6.43.3"),sQuery(id+"F0.wireOp",EDGE,"E6.43.4"),sQuery(id+"F0.wireOp",EDGE,"E7"),sQuery(id+"F0.wireOp",EDGE,"E8.1.0"),sQuery(id+"F0.wireOp",EDGE,"E8.2.0"),sQuery(id+"F0.wireOp",EDGE,"E8.3.0"),sQuery(id+"F0.wireOp",EDGE,"E8.4.0"),sQuery(id+"F0.wireOp",EDGE,"E8.5.0"),sQuery(id+"F0.wireOp",EDGE,"E8.6.0"),sQuery(id+"F0.wireOp",EDGE,"E8.7.0"),sQuery(id+"F0.wireOp",EDGE,"E8.8.0"),sQuery(id+"F0.wireOp",EDGE,"E8.9.0"),sQuery(id+"F0.wireOp",EDGE,"E8.10.0"),sQuery(id+"F0.wireOp",EDGE,"E8.11.0"),sQuery(id+"F0.wireOp",EDGE,"E8.12.0"),sQuery(id+"F0.wireOp",EDGE,"E8.13.0"),sQuery(id+"F0.wireOp",EDGE,"E8.14.0"),sQuery(id+"F0.wireOp",EDGE,"E8.15.0"),sQuery(id+"F0.wireOp",EDGE,"E8.16.0"),sQuery(id+"F0.wireOp",EDGE,"E8.17.0"),sQuery(id+"F0.wireOp",EDGE,"E8.18.0"),sQuery(id+"F0.wireOp",EDGE,"E8.19.0"),sQuery(id+"F0.wireOp",EDGE,"E8.20.0"),sQuery(id+"F0.wireOp",EDGE,"E8.21.0"),sQuery(id+"F0.wireOp",EDGE,"E8.22.0"),sQuery(id+"F0.wireOp",EDGE,"E8.23.0"),sQuery(id+"F0.wireOp",EDGE,"E8.24.0"),sQuery(id+"F0.wireOp",EDGE,"E8.25.0"),sQuery(id+"F0.wireOp",EDGE,"E8.26.0"),sQuery(id+"F0.wireOp",EDGE,"E8.27.0"),sQuery(id+"F0.wireOp",EDGE,"E8.28.0"),sQuery(id+"F0.wireOp",EDGE,"E8.29.0"),sQuery(id+"F0.wireOp",EDGE,"E8.30.0"),sQuery(id+"F0.wireOp",EDGE,"E8.31.0"),sQuery(id+"F0.wireOp",EDGE,"E8.32.0"),sQuery(id+"F0.wireOp",EDGE,"E8.33.0"),sQuery(id+"F0.wireOp",EDGE,"E8.34.0"),sQuery(id+"F0.wireOp",EDGE,"E8.35.0"),sQuery(id+"F0.wireOp",EDGE,"E8.36.0"),sQuery(id+"F0.wireOp",EDGE,"E8.37.0"),sQuery(id+"F0.wireOp",EDGE,"E8.38.0"),sQuery(id+"F0.wireOp",EDGE,"E8.39.0"),sQuery(id+"F0.wireOp",EDGE,"E8.40.0"),sQuery(id+"F0.wireOp",EDGE,"E8.41.0"),sQuery(id+"F0.wireOp",EDGE,"E8.42.0"),sQuery(id+"F0.wireOp",EDGE,"E8.43.0")])],"isStart":false})],"blendedInto":[makeQuery(id+"F1.opExtrude","CAP_FACE",FACE,{"disambiguationData":[OSD([sQuery(id+"F0.wireOp",EDGE,"E0"),sQuery(id+"F0.wireOp",EDGE,"E1"),sQuery(id+"F0.wireOp",EDGE,"E2"),sQuery(id+"F0.wireOp",EDGE,"E4"),sQuery(id+"F0.wireOp",EDGE,"E5"),sQuery(id+"F0.wireOp",EDGE,"E6.1.1"),sQuery(id+"F0.wireOp",EDGE,"E6.1.2"),sQuery(id+"F0.wireOp",EDGE,"E6.1.3"),sQuery(id+"F0.wireOp",EDGE,"E6.1.4"),sQuery(id+"F0.wireOp",EDGE,"E6.2.1"),sQuery(id+"F0.wireOp",EDGE,"E6.2.2"),sQuery(id+"F0.wireOp",EDGE,"E6.2.3"),sQuery(id+"F0.wireOp",EDGE,"E6.2.4"),sQuery(id+"F0.wireOp",EDGE,"E6.3.1"),sQuery(id+"F0.wireOp",EDGE,"E6.3.2"),sQuery(id+"F0.wireOp",EDGE,"E6.3.3"),sQuery(id+"F0.wireOp",EDGE,"E6.3.4"),sQuery(id+"F0.wireOp",EDGE,"E6.4.1"),sQuery(id+"F0.wireOp",EDGE,"E6.4.2"),sQuery(id+"F0.wireOp",EDGE,"E6.4.3"),sQuery(id+"F0.wireOp",EDGE,"E6.4.4"),sQuery(id+"F0.wireOp",EDGE,"E6.5.1"),sQuery(id+"F0.wireOp",EDGE,"E6.5.2"),sQuery(id+"F0.wireOp",EDGE,"E6.5.3"),sQuery(id+"F0.wireOp",EDGE,"E6.5.4"),sQuery(id+"F0.wireOp",EDGE,"E6.6.1"),sQuery(id+"F0.wireOp",EDGE,"E6.6.2"),sQuery(id+"F0.wireOp",EDGE,"E6.6.3"),sQuery(id+"F0.wireOp",EDGE,"E6.6.4"),sQuery(id+"F0.wireOp",EDGE,"E6.7.1"),sQuery(id+"F0.wireOp",EDGE,"E6.7.2"),sQuery(id+"F0.wireOp",EDGE,"E6.7.3"),sQuery(id+"F0.wireOp",EDGE,"E6.7.4"),sQuery(id+"F0.wireOp",EDGE,"E6.8.1"),sQuery(id+"F0.wireOp",EDGE,"E6.8.2"),sQuery(id+"F0.wireOp",EDGE,"E6.8.3"),sQuery(id+"F0.wireOp",EDGE,"E6.8.4"),sQuery(id+"F0.wireOp",EDGE,"E6.9.1"),sQuery(id+"F0.wireOp",EDGE,"E6.9.2"),sQuery(id+"F0.wireOp",EDGE,"E6.9.3"),sQuery(id+"F0.wireOp",EDGE,"E6.9.4"),sQuery(id+"F0.wireOp",EDGE,"E6.10.1"),sQuery(id+"F0.wireOp",EDGE,"E6.10.2"),sQuery(id+"F0.wireOp",EDGE,"E6.10.3"),sQuery(id+"F0.wireOp",EDGE,"E6.10.4"),sQuery(id+"F0.wireOp",EDGE,"E6.11.1"),sQuery(id+"F0.wireOp",EDGE,"E6.11.2"),sQuery(id+"F0.wireOp",EDGE,"E6.11.3"),sQuery(id+"F0.wireOp",EDGE,"E6.11.4"),sQuery(id+"F0.wireOp",EDGE,"E6.12.1"),sQuery(id+"F0.wireOp",EDGE,"E6.12.2"),sQuery(id+"F0.wireOp",EDGE,"E6.12.3"),sQuery(id+"F0.wireOp",EDGE,"E6.12.4"),sQuery(id+"F0.wireOp",EDGE,"E6.13.1"),sQuery(id+"F0.wireOp",EDGE,"E6.13.2"),sQuery(id+"F0.wireOp",EDGE,"E6.13.3"),sQuery(id+"F0.wireOp",EDGE,"E6.13.4"),sQuery(id+"F0.wireOp",EDGE,"E6.14.1"),sQuery(id+"F0.wireOp",EDGE,"E6.14.2"),sQuery(id+"F0.wireOp",EDGE,"E6.14.3"),sQuery(id+"F0.wireOp",EDGE,"E6.14.4"),subQ1,sQuery(id+"F0.wireOp",EDGE,"E6.15.2"),subQ0,sQuery(id+"F0.wireOp",EDGE,"E6.15.4"),sQuery(id+"F0.wireOp",EDGE,"E6.16.1"),sQuery(id+"F0.wireOp",EDGE,"E6.16.2"),sQuery(id+"F0.wireOp",EDGE,"E6.16.3"),sQuery(id+"F0.wireOp",EDGE,"E6.16.4"),sQuery(id+"F0.wireOp",EDGE,"E6.17.1"),sQuery(id+"F0.wireOp",EDGE,"E6.17.2"),sQuery(id+"F0.wireOp",EDGE,"E6.17.3"),sQuery(id+"F0.wireOp",EDGE,"E6.17.4"),sQuery(id+"F0.wireOp",EDGE,"E6.18.1"),sQuery(id+"F0.wireOp",EDGE,"E6.18.2"),sQuery(id+"F0.wireOp",EDGE,"E6.18.3"),sQuery(id+"F0.wireOp",EDGE,"E6.18.4"),sQuery(id+"F0.wireOp",EDGE,"E6.19.1"),sQuery(id+"F0.wireOp",EDGE,"E6.19.2"),sQuery(id+"F0.wireOp",EDGE,"E6.19.3"),sQuery(id+"F0.wireOp",EDGE,"E6.19.4"),sQuery(id+"F0.wireOp",EDGE,"E6.20.1"),sQuery(id+"F0.wireOp",EDGE,"E6.20.2"),sQuery(id+"F0.wireOp",EDGE,"E6.20.3"),sQuery(id+"F0.wireOp",EDGE,"E6.20.4"),sQuery(id+"F0.wireOp",EDGE,"E6.21.1"),sQuery(id+"F0.wireOp",EDGE,"E6.21.2"),sQuery(id+"F0.wireOp",EDGE,"E6.21.3"),sQuery(id+"F0.wireOp",EDGE,"E6.21.4"),sQuery(id+"F0.wireOp",EDGE,"E6.22.1"),sQuery(id+"F0.wireOp",EDGE,"E6.22.2"),sQuery(id+"F0.wireOp",EDGE,"E6.22.3"),sQuery(id+"F0.wireOp",EDGE,"E6.22.4"),sQuery(id+"F0.wireOp",EDGE,"E6.23.1"),sQuery(id+"F0.wireOp",EDGE,"E6.23.2"),sQuery(id+"F0.wireOp",EDGE,"E6.23.3"),sQuery(id+"F0.wireOp",EDGE,"E6.23.4"),sQuery(id+"F0.wireOp",EDGE,"E6.24.1"),sQuery(id+"F0.wireOp",EDGE,"E6.24.2"),sQuery(id+"F0.wireOp",EDGE,"E6.24.3"),sQuery(id+"F0.wireOp",EDGE,"E6.24.4"),sQuery(id+"F0.wireOp",EDGE,"E6.25.1"),sQuery(id+"F0.wireOp",EDGE,"E6.25.2"),sQuery(id+"F0.wireOp",EDGE,"E6.25.3"),sQuery(id+"F0.wireOp",EDGE,"E6.25.4"),sQuery(id+"F0.wireOp",EDGE,"E6.26.1"),sQuery(id+"F0.wireOp",EDGE,"E6.26.2"),sQuery(id+"F0.wireOp",EDGE,"E6.26.3"),sQuery(id+"F0.wireOp",EDGE,"E6.26.4"),sQuery(id+"F0.wireOp",EDGE,"E6.27.1"),sQuery(id+"F0.wireOp",EDGE,"E6.27.2"),sQuery(id+"F0.wireOp",EDGE,"E6.27.3"),sQuery(id+"F0.wireOp",EDGE,"E6.27.4"),sQuery(id+"F0.wireOp",EDGE,"E6.28.1"),sQuery(id+"F0.wireOp",EDGE,"E6.28.2"),sQuery(id+"F0.wireOp",EDGE,"E6.28.3"),sQuery(id+"F0.wireOp",EDGE,"E6.28.4"),sQuery(id+"F0.wireOp",EDGE,"E6.29.1"),sQuery(id+"F0.wireOp",EDGE,"E6.29.2"),sQuery(id+"F0.wireOp",EDGE,"E6.29.3"),sQuery(id+"F0.wireOp",EDGE,"E6.29.4"),sQuery(id+"F0.wireOp",EDGE,"E6.30.1"),sQuery(id+"F0.wireOp",EDGE,"E6.30.2"),sQuery(id+"F0.wireOp",EDGE,"E6.30.3"),sQuery(id+"F0.wireOp",EDGE,"E6.30.4"),sQuery(id+"F0.wireOp",EDGE,"E6.31.1"),sQuery(id+"F0.wireOp",EDGE,"E6.31.2"),sQuery(id+"F0.wireOp",EDGE,"E6.31.3"),sQuery(id+"F0.wireOp",EDGE,"E6.31.4"),sQuery(id+"F0.wireOp",EDGE,"E6.32.1"),sQuery(id+"F0.wireOp",EDGE,"E6.32.2"),sQuery(id+"F0.wireOp",EDGE,"E6.32.3"),sQuery(id+"F0.wireOp",EDGE,"E6.32.4"),sQuery(id+"F0.wireOp",EDGE,"E6.33.1"),sQuery(id+"F0.wireOp",EDGE,"E6.33.2"),sQuery(id+"F0.wireOp",EDGE,"E6.33.3"),sQuery(id+"F0.wireOp",EDGE,"E6.33.4"),sQuery(id+"F0.wireOp",EDGE,"E6.34.1"),sQuery(id+"F0.wireOp",EDGE,"E6.34.2"),sQuery(id+"F0.wireOp",EDGE,"E6.34.3"),sQuery(id+"F0.wireOp",EDGE,"E6.34.4"),sQuery(id+"F0.wireOp",EDGE,"E6.35.1"),sQuery(id+"F0.wireOp",EDGE,"E6.35.2"),sQuery(id+"F0.wireOp",EDGE,"E6.35.3"),sQuery(id+"F0.wireOp",EDGE,"E6.35.4"),sQuery(id+"F0.wireOp",EDGE,"E6.36.1"),sQuery(id+"F0.wireOp",EDGE,"E6.36.2"),sQuery(id+"F0.wireOp",EDGE,"E6.36.3"),sQuery(id+"F0.wireOp",EDGE,"E6.36.4"),sQuery(id+"F0.wireOp",EDGE,"E6.37.1"),sQuery(id+"F0.wireOp",EDGE,"E6.37.2"),sQuery(id+"F0.wireOp",EDGE,"E6.37.3"),sQuery(id+"F0.wireOp",EDGE,"E6.37.4"),sQuery(id+"F0.wireOp",EDGE,"E6.38.1"),sQuery(id+"F0.wireOp",EDGE,"E6.38.2"),sQuery(id+"F0.wireOp",EDGE,"E6.38.3"),sQuery(id+"F0.wireOp",EDGE,"E6.38.4"),sQuery(id+"F0.wireOp",EDGE,"E6.39.1"),sQuery(id+"F0.wireOp",EDGE,"E6.39.2"),sQuery(id+"F0.wireOp",EDGE,"E6.39.3"),sQuery(id+"F0.wireOp",EDGE,"E6.39.4"),sQuery(id+"F0.wireOp",EDGE,"E6.40.1"),sQuery(id+"F0.wireOp",EDGE,"E6.40.2"),sQuery(id+"F0.wireOp",EDGE,"E6.40.3"),sQuery(id+"F0.wireOp",EDGE,"E6.40.4"),sQuery(id+"F0.wireOp",EDGE,"E6.41.1"),sQuery(id+"F0.wireOp",EDGE,"E6.41.2"),sQuery(id+"F0.wireOp",EDGE,"E6.41.3"),sQuery(id+"F0.wireOp",EDGE,"E6.41.4"),sQuery(id+"F0.wireOp",EDGE,"E6.42.1"),sQuery(id+"F0.wireOp",EDGE,"E6.42.2"),sQuery(id+"F0.wireOp",EDGE,"E6.42.3"),sQuery(id+"F0.wireOp",EDGE,"E6.42.4"),sQuery(id+"F0.wireOp",EDGE,"E6.43.1"),sQuery(id+"F0.wireOp",EDGE,"E6.43.2"),sQuery(id+"F0.wireOp",EDGE,"E6.43.3"),sQuery(id+"F0.wireOp",EDGE,"E6.43.4"),sQuery(id+"F0.wireOp",EDGE,"E7"),sQuery(id+"F0.wireOp",EDGE,"E8.1.0"),sQuery(id+"F0.wireOp",EDGE,"E8.2.0"),sQuery(id+"F0.wireOp",EDGE,"E8.3.0"),sQuery(id+"F0.wireOp",EDGE,"E8.4.0"),sQuery(id+"F0.wireOp",EDGE,"E8.5.0"),sQuery(id+"F0.wireOp",EDGE,"E8.6.0"),sQuery(id+"F0.wireOp",EDGE,"E8.7.0"),sQuery(id+"F0.wireOp",EDGE,"E8.8.0"),sQuery(id+"F0.wireOp",EDGE,"E8.9.0"),sQuery(id+"F0.wireOp",EDGE,"E8.10.0"),sQuery(id+"F0.wireOp",EDGE,"E8.11.0"),sQuery(id+"F0.wireOp",EDGE,"E8.12.0"),sQuery(id+"F0.wireOp",EDGE,"E8.13.0"),sQuery(id+"F0.wireOp",EDGE,"E8.14.0"),sQuery(id+"F0.wireOp",EDGE,"E8.15.0"),sQuery(id+"F0.wireOp",EDGE,"E8.16.0"),sQuery(id+"F0.wireOp",EDGE,"E8.17.0"),sQuery(id+"F0.wireOp",EDGE,"E8.18.0"),sQuery(id+"F0.wireOp",EDGE,"E8.19.0"),sQuery(id+"F0.wireOp",EDGE,"E8.20.0"),sQuery(id+"F0.wireOp",EDGE,"E8.21.0"),sQuery(id+"F0.wireOp",EDGE,"E8.22.0"),sQuery(id+"F0.wireOp",EDGE,"E8.23.0"),sQuery(id+"F0.wireOp",EDGE,"E8.24.0"),sQuery(id+"F0.wireOp",EDGE,"E8.25.0"),sQuery(id+"F0.wireOp",EDGE,"E8.26.0"),sQuery(id+"F0.wireOp",EDGE,"E8.27.0"),sQuery(id+"F0.wireOp",EDGE,"E8.28.0"),sQuery(id+"F0.wireOp",EDGE,"E8.29.0"),sQuery(id+"F0.wireOp",EDGE,"E8.30.0"),sQuery(id+"F0.wireOp",EDGE,"E8.31.0"),sQuery(id+"F0.wireOp",EDGE,"E8.32.0"),sQuery(id+"F0.wireOp",EDGE,"E8.33.0"),sQuery(id+"F0.wireOp",EDGE,"E8.34.0"),sQuery(id+"F0.wireOp",EDGE,"E8.35.0"),sQuery(id+"F0.wireOp",EDGE,"E8.36.0"),sQuery(id+"F0.wireOp",EDGE,"E8.37.0"),sQuery(id+"F0.wireOp",EDGE,"E8.38.0"),sQuery(id+"F0.wireOp",EDGE,"E8.39.0"),sQuery(id+"F0.wireOp",EDGE,"E8.40.0"),sQuery(id+"F0.wireOp",EDGE,"E8.41.0"),sQuery(id+"F0.wireOp",EDGE,"E8.42.0"),sQuery(id+"F0.wireOp",EDGE,"E8.43.0")])],"isStart":false})]});}
            var Q19;
            {var subQ0=sQuery(id+"F0.wireOp",EDGE,"E6.17.3");var subQ1=sQuery(id+"F0.wireOp",EDGE,"E6.17.1");Q19=makeQuery(id+"F2.opFillet","BLEND_EDGE",EDGE,{"blendedFrom":[makeQuery(id+"F1.opExtrude","SWEPT_EDGE",EDGE,{"disambiguationData":[OSD([sQuery(id+"F0.wireOp",EDGE,"E6.17.0"),subQ1,subQ0])]}),makeQuery(id+"F1.opExtrude","CAP_FACE",FACE,{"disambiguationData":[OSD([sQuery(id+"F0.wireOp",EDGE,"E0"),sQuery(id+"F0.wireOp",EDGE,"E1"),sQuery(id+"F0.wireOp",EDGE,"E2"),sQuery(id+"F0.wireOp",EDGE,"E4"),sQuery(id+"F0.wireOp",EDGE,"E5"),sQuery(id+"F0.wireOp",EDGE,"E6.1.1"),sQuery(id+"F0.wireOp",EDGE,"E6.1.2"),sQuery(id+"F0.wireOp",EDGE,"E6.1.3"),sQuery(id+"F0.wireOp",EDGE,"E6.1.4"),sQuery(id+"F0.wireOp",EDGE,"E6.2.1"),sQuery(id+"F0.wireOp",EDGE,"E6.2.2"),sQuery(id+"F0.wireOp",EDGE,"E6.2.3"),sQuery(id+"F0.wireOp",EDGE,"E6.2.4"),sQuery(id+"F0.wireOp",EDGE,"E6.3.1"),sQuery(id+"F0.wireOp",EDGE,"E6.3.2"),sQuery(id+"F0.wireOp",EDGE,"E6.3.3"),sQuery(id+"F0.wireOp",EDGE,"E6.3.4"),sQuery(id+"F0.wireOp",EDGE,"E6.4.1"),sQuery(id+"F0.wireOp",EDGE,"E6.4.2"),sQuery(id+"F0.wireOp",EDGE,"E6.4.3"),sQuery(id+"F0.wireOp",EDGE,"E6.4.4"),sQuery(id+"F0.wireOp",EDGE,"E6.5.1"),sQuery(id+"F0.wireOp",EDGE,"E6.5.2"),sQuery(id+"F0.wireOp",EDGE,"E6.5.3"),sQuery(id+"F0.wireOp",EDGE,"E6.5.4"),sQuery(id+"F0.wireOp",EDGE,"E6.6.1"),sQuery(id+"F0.wireOp",EDGE,"E6.6.2"),sQuery(id+"F0.wireOp",EDGE,"E6.6.3"),sQuery(id+"F0.wireOp",EDGE,"E6.6.4"),sQuery(id+"F0.wireOp",EDGE,"E6.7.1"),sQuery(id+"F0.wireOp",EDGE,"E6.7.2"),sQuery(id+"F0.wireOp",EDGE,"E6.7.3"),sQuery(id+"F0.wireOp",EDGE,"E6.7.4"),sQuery(id+"F0.wireOp",EDGE,"E6.8.1"),sQuery(id+"F0.wireOp",EDGE,"E6.8.2"),sQuery(id+"F0.wireOp",EDGE,"E6.8.3"),sQuery(id+"F0.wireOp",EDGE,"E6.8.4"),sQuery(id+"F0.wireOp",EDGE,"E6.9.1"),sQuery(id+"F0.wireOp",EDGE,"E6.9.2"),sQuery(id+"F0.wireOp",EDGE,"E6.9.3"),sQuery(id+"F0.wireOp",EDGE,"E6.9.4"),sQuery(id+"F0.wireOp",EDGE,"E6.10.1"),sQuery(id+"F0.wireOp",EDGE,"E6.10.2"),sQuery(id+"F0.wireOp",EDGE,"E6.10.3"),sQuery(id+"F0.wireOp",EDGE,"E6.10.4"),sQuery(id+"F0.wireOp",EDGE,"E6.11.1"),sQuery(id+"F0.wireOp",EDGE,"E6.11.2"),sQuery(id+"F0.wireOp",EDGE,"E6.11.3"),sQuery(id+"F0.wireOp",EDGE,"E6.11.4"),sQuery(id+"F0.wireOp",EDGE,"E6.12.1"),sQuery(id+"F0.wireOp",EDGE,"E6.12.2"),sQuery(id+"F0.wireOp",EDGE,"E6.12.3"),sQuery(id+"F0.wireOp",EDGE,"E6.12.4"),sQuery(id+"F0.wireOp",EDGE,"E6.13.1"),sQuery(id+"F0.wireOp",EDGE,"E6.13.2"),sQuery(id+"F0.wireOp",EDGE,"E6.13.3"),sQuery(id+"F0.wireOp",EDGE,"E6.13.4"),sQuery(id+"F0.wireOp",EDGE,"E6.14.1"),sQuery(id+"F0.wireOp",EDGE,"E6.14.2"),sQuery(id+"F0.wireOp",EDGE,"E6.14.3"),sQuery(id+"F0.wireOp",EDGE,"E6.14.4"),sQuery(id+"F0.wireOp",EDGE,"E6.15.1"),sQuery(id+"F0.wireOp",EDGE,"E6.15.2"),sQuery(id+"F0.wireOp",EDGE,"E6.15.3"),sQuery(id+"F0.wireOp",EDGE,"E6.15.4"),sQuery(id+"F0.wireOp",EDGE,"E6.16.1"),sQuery(id+"F0.wireOp",EDGE,"E6.16.2"),sQuery(id+"F0.wireOp",EDGE,"E6.16.3"),sQuery(id+"F0.wireOp",EDGE,"E6.16.4"),subQ1,sQuery(id+"F0.wireOp",EDGE,"E6.17.2"),subQ0,sQuery(id+"F0.wireOp",EDGE,"E6.17.4"),sQuery(id+"F0.wireOp",EDGE,"E6.18.1"),sQuery(id+"F0.wireOp",EDGE,"E6.18.2"),sQuery(id+"F0.wireOp",EDGE,"E6.18.3"),sQuery(id+"F0.wireOp",EDGE,"E6.18.4"),sQuery(id+"F0.wireOp",EDGE,"E6.19.1"),sQuery(id+"F0.wireOp",EDGE,"E6.19.2"),sQuery(id+"F0.wireOp",EDGE,"E6.19.3"),sQuery(id+"F0.wireOp",EDGE,"E6.19.4"),sQuery(id+"F0.wireOp",EDGE,"E6.20.1"),sQuery(id+"F0.wireOp",EDGE,"E6.20.2"),sQuery(id+"F0.wireOp",EDGE,"E6.20.3"),sQuery(id+"F0.wireOp",EDGE,"E6.20.4"),sQuery(id+"F0.wireOp",EDGE,"E6.21.1"),sQuery(id+"F0.wireOp",EDGE,"E6.21.2"),sQuery(id+"F0.wireOp",EDGE,"E6.21.3"),sQuery(id+"F0.wireOp",EDGE,"E6.21.4"),sQuery(id+"F0.wireOp",EDGE,"E6.22.1"),sQuery(id+"F0.wireOp",EDGE,"E6.22.2"),sQuery(id+"F0.wireOp",EDGE,"E6.22.3"),sQuery(id+"F0.wireOp",EDGE,"E6.22.4"),sQuery(id+"F0.wireOp",EDGE,"E6.23.1"),sQuery(id+"F0.wireOp",EDGE,"E6.23.2"),sQuery(id+"F0.wireOp",EDGE,"E6.23.3"),sQuery(id+"F0.wireOp",EDGE,"E6.23.4"),sQuery(id+"F0.wireOp",EDGE,"E6.24.1"),sQuery(id+"F0.wireOp",EDGE,"E6.24.2"),sQuery(id+"F0.wireOp",EDGE,"E6.24.3"),sQuery(id+"F0.wireOp",EDGE,"E6.24.4"),sQuery(id+"F0.wireOp",EDGE,"E6.25.1"),sQuery(id+"F0.wireOp",EDGE,"E6.25.2"),sQuery(id+"F0.wireOp",EDGE,"E6.25.3"),sQuery(id+"F0.wireOp",EDGE,"E6.25.4"),sQuery(id+"F0.wireOp",EDGE,"E6.26.1"),sQuery(id+"F0.wireOp",EDGE,"E6.26.2"),sQuery(id+"F0.wireOp",EDGE,"E6.26.3"),sQuery(id+"F0.wireOp",EDGE,"E6.26.4"),sQuery(id+"F0.wireOp",EDGE,"E6.27.1"),sQuery(id+"F0.wireOp",EDGE,"E6.27.2"),sQuery(id+"F0.wireOp",EDGE,"E6.27.3"),sQuery(id+"F0.wireOp",EDGE,"E6.27.4"),sQuery(id+"F0.wireOp",EDGE,"E6.28.1"),sQuery(id+"F0.wireOp",EDGE,"E6.28.2"),sQuery(id+"F0.wireOp",EDGE,"E6.28.3"),sQuery(id+"F0.wireOp",EDGE,"E6.28.4"),sQuery(id+"F0.wireOp",EDGE,"E6.29.1"),sQuery(id+"F0.wireOp",EDGE,"E6.29.2"),sQuery(id+"F0.wireOp",EDGE,"E6.29.3"),sQuery(id+"F0.wireOp",EDGE,"E6.29.4"),sQuery(id+"F0.wireOp",EDGE,"E6.30.1"),sQuery(id+"F0.wireOp",EDGE,"E6.30.2"),sQuery(id+"F0.wireOp",EDGE,"E6.30.3"),sQuery(id+"F0.wireOp",EDGE,"E6.30.4"),sQuery(id+"F0.wireOp",EDGE,"E6.31.1"),sQuery(id+"F0.wireOp",EDGE,"E6.31.2"),sQuery(id+"F0.wireOp",EDGE,"E6.31.3"),sQuery(id+"F0.wireOp",EDGE,"E6.31.4"),sQuery(id+"F0.wireOp",EDGE,"E6.32.1"),sQuery(id+"F0.wireOp",EDGE,"E6.32.2"),sQuery(id+"F0.wireOp",EDGE,"E6.32.3"),sQuery(id+"F0.wireOp",EDGE,"E6.32.4"),sQuery(id+"F0.wireOp",EDGE,"E6.33.1"),sQuery(id+"F0.wireOp",EDGE,"E6.33.2"),sQuery(id+"F0.wireOp",EDGE,"E6.33.3"),sQuery(id+"F0.wireOp",EDGE,"E6.33.4"),sQuery(id+"F0.wireOp",EDGE,"E6.34.1"),sQuery(id+"F0.wireOp",EDGE,"E6.34.2"),sQuery(id+"F0.wireOp",EDGE,"E6.34.3"),sQuery(id+"F0.wireOp",EDGE,"E6.34.4"),sQuery(id+"F0.wireOp",EDGE,"E6.35.1"),sQuery(id+"F0.wireOp",EDGE,"E6.35.2"),sQuery(id+"F0.wireOp",EDGE,"E6.35.3"),sQuery(id+"F0.wireOp",EDGE,"E6.35.4"),sQuery(id+"F0.wireOp",EDGE,"E6.36.1"),sQuery(id+"F0.wireOp",EDGE,"E6.36.2"),sQuery(id+"F0.wireOp",EDGE,"E6.36.3"),sQuery(id+"F0.wireOp",EDGE,"E6.36.4"),sQuery(id+"F0.wireOp",EDGE,"E6.37.1"),sQuery(id+"F0.wireOp",EDGE,"E6.37.2"),sQuery(id+"F0.wireOp",EDGE,"E6.37.3"),sQuery(id+"F0.wireOp",EDGE,"E6.37.4"),sQuery(id+"F0.wireOp",EDGE,"E6.38.1"),sQuery(id+"F0.wireOp",EDGE,"E6.38.2"),sQuery(id+"F0.wireOp",EDGE,"E6.38.3"),sQuery(id+"F0.wireOp",EDGE,"E6.38.4"),sQuery(id+"F0.wireOp",EDGE,"E6.39.1"),sQuery(id+"F0.wireOp",EDGE,"E6.39.2"),sQuery(id+"F0.wireOp",EDGE,"E6.39.3"),sQuery(id+"F0.wireOp",EDGE,"E6.39.4"),sQuery(id+"F0.wireOp",EDGE,"E6.40.1"),sQuery(id+"F0.wireOp",EDGE,"E6.40.2"),sQuery(id+"F0.wireOp",EDGE,"E6.40.3"),sQuery(id+"F0.wireOp",EDGE,"E6.40.4"),sQuery(id+"F0.wireOp",EDGE,"E6.41.1"),sQuery(id+"F0.wireOp",EDGE,"E6.41.2"),sQuery(id+"F0.wireOp",EDGE,"E6.41.3"),sQuery(id+"F0.wireOp",EDGE,"E6.41.4"),sQuery(id+"F0.wireOp",EDGE,"E6.42.1"),sQuery(id+"F0.wireOp",EDGE,"E6.42.2"),sQuery(id+"F0.wireOp",EDGE,"E6.42.3"),sQuery(id+"F0.wireOp",EDGE,"E6.42.4"),sQuery(id+"F0.wireOp",EDGE,"E6.43.1"),sQuery(id+"F0.wireOp",EDGE,"E6.43.2"),sQuery(id+"F0.wireOp",EDGE,"E6.43.3"),sQuery(id+"F0.wireOp",EDGE,"E6.43.4"),sQuery(id+"F0.wireOp",EDGE,"E7"),sQuery(id+"F0.wireOp",EDGE,"E8.1.0"),sQuery(id+"F0.wireOp",EDGE,"E8.2.0"),sQuery(id+"F0.wireOp",EDGE,"E8.3.0"),sQuery(id+"F0.wireOp",EDGE,"E8.4.0"),sQuery(id+"F0.wireOp",EDGE,"E8.5.0"),sQuery(id+"F0.wireOp",EDGE,"E8.6.0"),sQuery(id+"F0.wireOp",EDGE,"E8.7.0"),sQuery(id+"F0.wireOp",EDGE,"E8.8.0"),sQuery(id+"F0.wireOp",EDGE,"E8.9.0"),sQuery(id+"F0.wireOp",EDGE,"E8.10.0"),sQuery(id+"F0.wireOp",EDGE,"E8.11.0"),sQuery(id+"F0.wireOp",EDGE,"E8.12.0"),sQuery(id+"F0.wireOp",EDGE,"E8.13.0"),sQuery(id+"F0.wireOp",EDGE,"E8.14.0"),sQuery(id+"F0.wireOp",EDGE,"E8.15.0"),sQuery(id+"F0.wireOp",EDGE,"E8.16.0"),sQuery(id+"F0.wireOp",EDGE,"E8.17.0"),sQuery(id+"F0.wireOp",EDGE,"E8.18.0"),sQuery(id+"F0.wireOp",EDGE,"E8.19.0"),sQuery(id+"F0.wireOp",EDGE,"E8.20.0"),sQuery(id+"F0.wireOp",EDGE,"E8.21.0"),sQuery(id+"F0.wireOp",EDGE,"E8.22.0"),sQuery(id+"F0.wireOp",EDGE,"E8.23.0"),sQuery(id+"F0.wireOp",EDGE,"E8.24.0"),sQuery(id+"F0.wireOp",EDGE,"E8.25.0"),sQuery(id+"F0.wireOp",EDGE,"E8.26.0"),sQuery(id+"F0.wireOp",EDGE,"E8.27.0"),sQuery(id+"F0.wireOp",EDGE,"E8.28.0"),sQuery(id+"F0.wireOp",EDGE,"E8.29.0"),sQuery(id+"F0.wireOp",EDGE,"E8.30.0"),sQuery(id+"F0.wireOp",EDGE,"E8.31.0"),sQuery(id+"F0.wireOp",EDGE,"E8.32.0"),sQuery(id+"F0.wireOp",EDGE,"E8.33.0"),sQuery(id+"F0.wireOp",EDGE,"E8.34.0"),sQuery(id+"F0.wireOp",EDGE,"E8.35.0"),sQuery(id+"F0.wireOp",EDGE,"E8.36.0"),sQuery(id+"F0.wireOp",EDGE,"E8.37.0"),sQuery(id+"F0.wireOp",EDGE,"E8.38.0"),sQuery(id+"F0.wireOp",EDGE,"E8.39.0"),sQuery(id+"F0.wireOp",EDGE,"E8.40.0"),sQuery(id+"F0.wireOp",EDGE,"E8.41.0"),sQuery(id+"F0.wireOp",EDGE,"E8.42.0"),sQuery(id+"F0.wireOp",EDGE,"E8.43.0")])],"isStart":false})],"blendedInto":[makeQuery(id+"F1.opExtrude","CAP_FACE",FACE,{"disambiguationData":[OSD([sQuery(id+"F0.wireOp",EDGE,"E0"),sQuery(id+"F0.wireOp",EDGE,"E1"),sQuery(id+"F0.wireOp",EDGE,"E2"),sQuery(id+"F0.wireOp",EDGE,"E4"),sQuery(id+"F0.wireOp",EDGE,"E5"),sQuery(id+"F0.wireOp",EDGE,"E6.1.1"),sQuery(id+"F0.wireOp",EDGE,"E6.1.2"),sQuery(id+"F0.wireOp",EDGE,"E6.1.3"),sQuery(id+"F0.wireOp",EDGE,"E6.1.4"),sQuery(id+"F0.wireOp",EDGE,"E6.2.1"),sQuery(id+"F0.wireOp",EDGE,"E6.2.2"),sQuery(id+"F0.wireOp",EDGE,"E6.2.3"),sQuery(id+"F0.wireOp",EDGE,"E6.2.4"),sQuery(id+"F0.wireOp",EDGE,"E6.3.1"),sQuery(id+"F0.wireOp",EDGE,"E6.3.2"),sQuery(id+"F0.wireOp",EDGE,"E6.3.3"),sQuery(id+"F0.wireOp",EDGE,"E6.3.4"),sQuery(id+"F0.wireOp",EDGE,"E6.4.1"),sQuery(id+"F0.wireOp",EDGE,"E6.4.2"),sQuery(id+"F0.wireOp",EDGE,"E6.4.3"),sQuery(id+"F0.wireOp",EDGE,"E6.4.4"),sQuery(id+"F0.wireOp",EDGE,"E6.5.1"),sQuery(id+"F0.wireOp",EDGE,"E6.5.2"),sQuery(id+"F0.wireOp",EDGE,"E6.5.3"),sQuery(id+"F0.wireOp",EDGE,"E6.5.4"),sQuery(id+"F0.wireOp",EDGE,"E6.6.1"),sQuery(id+"F0.wireOp",EDGE,"E6.6.2"),sQuery(id+"F0.wireOp",EDGE,"E6.6.3"),sQuery(id+"F0.wireOp",EDGE,"E6.6.4"),sQuery(id+"F0.wireOp",EDGE,"E6.7.1"),sQuery(id+"F0.wireOp",EDGE,"E6.7.2"),sQuery(id+"F0.wireOp",EDGE,"E6.7.3"),sQuery(id+"F0.wireOp",EDGE,"E6.7.4"),sQuery(id+"F0.wireOp",EDGE,"E6.8.1"),sQuery(id+"F0.wireOp",EDGE,"E6.8.2"),sQuery(id+"F0.wireOp",EDGE,"E6.8.3"),sQuery(id+"F0.wireOp",EDGE,"E6.8.4"),sQuery(id+"F0.wireOp",EDGE,"E6.9.1"),sQuery(id+"F0.wireOp",EDGE,"E6.9.2"),sQuery(id+"F0.wireOp",EDGE,"E6.9.3"),sQuery(id+"F0.wireOp",EDGE,"E6.9.4"),sQuery(id+"F0.wireOp",EDGE,"E6.10.1"),sQuery(id+"F0.wireOp",EDGE,"E6.10.2"),sQuery(id+"F0.wireOp",EDGE,"E6.10.3"),sQuery(id+"F0.wireOp",EDGE,"E6.10.4"),sQuery(id+"F0.wireOp",EDGE,"E6.11.1"),sQuery(id+"F0.wireOp",EDGE,"E6.11.2"),sQuery(id+"F0.wireOp",EDGE,"E6.11.3"),sQuery(id+"F0.wireOp",EDGE,"E6.11.4"),sQuery(id+"F0.wireOp",EDGE,"E6.12.1"),sQuery(id+"F0.wireOp",EDGE,"E6.12.2"),sQuery(id+"F0.wireOp",EDGE,"E6.12.3"),sQuery(id+"F0.wireOp",EDGE,"E6.12.4"),sQuery(id+"F0.wireOp",EDGE,"E6.13.1"),sQuery(id+"F0.wireOp",EDGE,"E6.13.2"),sQuery(id+"F0.wireOp",EDGE,"E6.13.3"),sQuery(id+"F0.wireOp",EDGE,"E6.13.4"),sQuery(id+"F0.wireOp",EDGE,"E6.14.1"),sQuery(id+"F0.wireOp",EDGE,"E6.14.2"),sQuery(id+"F0.wireOp",EDGE,"E6.14.3"),sQuery(id+"F0.wireOp",EDGE,"E6.14.4"),sQuery(id+"F0.wireOp",EDGE,"E6.15.1"),sQuery(id+"F0.wireOp",EDGE,"E6.15.2"),sQuery(id+"F0.wireOp",EDGE,"E6.15.3"),sQuery(id+"F0.wireOp",EDGE,"E6.15.4"),sQuery(id+"F0.wireOp",EDGE,"E6.16.1"),sQuery(id+"F0.wireOp",EDGE,"E6.16.2"),sQuery(id+"F0.wireOp",EDGE,"E6.16.3"),sQuery(id+"F0.wireOp",EDGE,"E6.16.4"),subQ1,sQuery(id+"F0.wireOp",EDGE,"E6.17.2"),subQ0,sQuery(id+"F0.wireOp",EDGE,"E6.17.4"),sQuery(id+"F0.wireOp",EDGE,"E6.18.1"),sQuery(id+"F0.wireOp",EDGE,"E6.18.2"),sQuery(id+"F0.wireOp",EDGE,"E6.18.3"),sQuery(id+"F0.wireOp",EDGE,"E6.18.4"),sQuery(id+"F0.wireOp",EDGE,"E6.19.1"),sQuery(id+"F0.wireOp",EDGE,"E6.19.2"),sQuery(id+"F0.wireOp",EDGE,"E6.19.3"),sQuery(id+"F0.wireOp",EDGE,"E6.19.4"),sQuery(id+"F0.wireOp",EDGE,"E6.20.1"),sQuery(id+"F0.wireOp",EDGE,"E6.20.2"),sQuery(id+"F0.wireOp",EDGE,"E6.20.3"),sQuery(id+"F0.wireOp",EDGE,"E6.20.4"),sQuery(id+"F0.wireOp",EDGE,"E6.21.1"),sQuery(id+"F0.wireOp",EDGE,"E6.21.2"),sQuery(id+"F0.wireOp",EDGE,"E6.21.3"),sQuery(id+"F0.wireOp",EDGE,"E6.21.4"),sQuery(id+"F0.wireOp",EDGE,"E6.22.1"),sQuery(id+"F0.wireOp",EDGE,"E6.22.2"),sQuery(id+"F0.wireOp",EDGE,"E6.22.3"),sQuery(id+"F0.wireOp",EDGE,"E6.22.4"),sQuery(id+"F0.wireOp",EDGE,"E6.23.1"),sQuery(id+"F0.wireOp",EDGE,"E6.23.2"),sQuery(id+"F0.wireOp",EDGE,"E6.23.3"),sQuery(id+"F0.wireOp",EDGE,"E6.23.4"),sQuery(id+"F0.wireOp",EDGE,"E6.24.1"),sQuery(id+"F0.wireOp",EDGE,"E6.24.2"),sQuery(id+"F0.wireOp",EDGE,"E6.24.3"),sQuery(id+"F0.wireOp",EDGE,"E6.24.4"),sQuery(id+"F0.wireOp",EDGE,"E6.25.1"),sQuery(id+"F0.wireOp",EDGE,"E6.25.2"),sQuery(id+"F0.wireOp",EDGE,"E6.25.3"),sQuery(id+"F0.wireOp",EDGE,"E6.25.4"),sQuery(id+"F0.wireOp",EDGE,"E6.26.1"),sQuery(id+"F0.wireOp",EDGE,"E6.26.2"),sQuery(id+"F0.wireOp",EDGE,"E6.26.3"),sQuery(id+"F0.wireOp",EDGE,"E6.26.4"),sQuery(id+"F0.wireOp",EDGE,"E6.27.1"),sQuery(id+"F0.wireOp",EDGE,"E6.27.2"),sQuery(id+"F0.wireOp",EDGE,"E6.27.3"),sQuery(id+"F0.wireOp",EDGE,"E6.27.4"),sQuery(id+"F0.wireOp",EDGE,"E6.28.1"),sQuery(id+"F0.wireOp",EDGE,"E6.28.2"),sQuery(id+"F0.wireOp",EDGE,"E6.28.3"),sQuery(id+"F0.wireOp",EDGE,"E6.28.4"),sQuery(id+"F0.wireOp",EDGE,"E6.29.1"),sQuery(id+"F0.wireOp",EDGE,"E6.29.2"),sQuery(id+"F0.wireOp",EDGE,"E6.29.3"),sQuery(id+"F0.wireOp",EDGE,"E6.29.4"),sQuery(id+"F0.wireOp",EDGE,"E6.30.1"),sQuery(id+"F0.wireOp",EDGE,"E6.30.2"),sQuery(id+"F0.wireOp",EDGE,"E6.30.3"),sQuery(id+"F0.wireOp",EDGE,"E6.30.4"),sQuery(id+"F0.wireOp",EDGE,"E6.31.1"),sQuery(id+"F0.wireOp",EDGE,"E6.31.2"),sQuery(id+"F0.wireOp",EDGE,"E6.31.3"),sQuery(id+"F0.wireOp",EDGE,"E6.31.4"),sQuery(id+"F0.wireOp",EDGE,"E6.32.1"),sQuery(id+"F0.wireOp",EDGE,"E6.32.2"),sQuery(id+"F0.wireOp",EDGE,"E6.32.3"),sQuery(id+"F0.wireOp",EDGE,"E6.32.4"),sQuery(id+"F0.wireOp",EDGE,"E6.33.1"),sQuery(id+"F0.wireOp",EDGE,"E6.33.2"),sQuery(id+"F0.wireOp",EDGE,"E6.33.3"),sQuery(id+"F0.wireOp",EDGE,"E6.33.4"),sQuery(id+"F0.wireOp",EDGE,"E6.34.1"),sQuery(id+"F0.wireOp",EDGE,"E6.34.2"),sQuery(id+"F0.wireOp",EDGE,"E6.34.3"),sQuery(id+"F0.wireOp",EDGE,"E6.34.4"),sQuery(id+"F0.wireOp",EDGE,"E6.35.1"),sQuery(id+"F0.wireOp",EDGE,"E6.35.2"),sQuery(id+"F0.wireOp",EDGE,"E6.35.3"),sQuery(id+"F0.wireOp",EDGE,"E6.35.4"),sQuery(id+"F0.wireOp",EDGE,"E6.36.1"),sQuery(id+"F0.wireOp",EDGE,"E6.36.2"),sQuery(id+"F0.wireOp",EDGE,"E6.36.3"),sQuery(id+"F0.wireOp",EDGE,"E6.36.4"),sQuery(id+"F0.wireOp",EDGE,"E6.37.1"),sQuery(id+"F0.wireOp",EDGE,"E6.37.2"),sQuery(id+"F0.wireOp",EDGE,"E6.37.3"),sQuery(id+"F0.wireOp",EDGE,"E6.37.4"),sQuery(id+"F0.wireOp",EDGE,"E6.38.1"),sQuery(id+"F0.wireOp",EDGE,"E6.38.2"),sQuery(id+"F0.wireOp",EDGE,"E6.38.3"),sQuery(id+"F0.wireOp",EDGE,"E6.38.4"),sQuery(id+"F0.wireOp",EDGE,"E6.39.1"),sQuery(id+"F0.wireOp",EDGE,"E6.39.2"),sQuery(id+"F0.wireOp",EDGE,"E6.39.3"),sQuery(id+"F0.wireOp",EDGE,"E6.39.4"),sQuery(id+"F0.wireOp",EDGE,"E6.40.1"),sQuery(id+"F0.wireOp",EDGE,"E6.40.2"),sQuery(id+"F0.wireOp",EDGE,"E6.40.3"),sQuery(id+"F0.wireOp",EDGE,"E6.40.4"),sQuery(id+"F0.wireOp",EDGE,"E6.41.1"),sQuery(id+"F0.wireOp",EDGE,"E6.41.2"),sQuery(id+"F0.wireOp",EDGE,"E6.41.3"),sQuery(id+"F0.wireOp",EDGE,"E6.41.4"),sQuery(id+"F0.wireOp",EDGE,"E6.42.1"),sQuery(id+"F0.wireOp",EDGE,"E6.42.2"),sQuery(id+"F0.wireOp",EDGE,"E6.42.3"),sQuery(id+"F0.wireOp",EDGE,"E6.42.4"),sQuery(id+"F0.wireOp",EDGE,"E6.43.1"),sQuery(id+"F0.wireOp",EDGE,"E6.43.2"),sQuery(id+"F0.wireOp",EDGE,"E6.43.3"),sQuery(id+"F0.wireOp",EDGE,"E6.43.4"),sQuery(id+"F0.wireOp",EDGE,"E7"),sQuery(id+"F0.wireOp",EDGE,"E8.1.0"),sQuery(id+"F0.wireOp",EDGE,"E8.2.0"),sQuery(id+"F0.wireOp",EDGE,"E8.3.0"),sQuery(id+"F0.wireOp",EDGE,"E8.4.0"),sQuery(id+"F0.wireOp",EDGE,"E8.5.0"),sQuery(id+"F0.wireOp",EDGE,"E8.6.0"),sQuery(id+"F0.wireOp",EDGE,"E8.7.0"),sQuery(id+"F0.wireOp",EDGE,"E8.8.0"),sQuery(id+"F0.wireOp",EDGE,"E8.9.0"),sQuery(id+"F0.wireOp",EDGE,"E8.10.0"),sQuery(id+"F0.wireOp",EDGE,"E8.11.0"),sQuery(id+"F0.wireOp",EDGE,"E8.12.0"),sQuery(id+"F0.wireOp",EDGE,"E8.13.0"),sQuery(id+"F0.wireOp",EDGE,"E8.14.0"),sQuery(id+"F0.wireOp",EDGE,"E8.15.0"),sQuery(id+"F0.wireOp",EDGE,"E8.16.0"),sQuery(id+"F0.wireOp",EDGE,"E8.17.0"),sQuery(id+"F0.wireOp",EDGE,"E8.18.0"),sQuery(id+"F0.wireOp",EDGE,"E8.19.0"),sQuery(id+"F0.wireOp",EDGE,"E8.20.0"),sQuery(id+"F0.wireOp",EDGE,"E8.21.0"),sQuery(id+"F0.wireOp",EDGE,"E8.22.0"),sQuery(id+"F0.wireOp",EDGE,"E8.23.0"),sQuery(id+"F0.wireOp",EDGE,"E8.24.0"),sQuery(id+"F0.wireOp",EDGE,"E8.25.0"),sQuery(id+"F0.wireOp",EDGE,"E8.26.0"),sQuery(id+"F0.wireOp",EDGE,"E8.27.0"),sQuery(id+"F0.wireOp",EDGE,"E8.28.0"),sQuery(id+"F0.wireOp",EDGE,"E8.29.0"),sQuery(id+"F0.wireOp",EDGE,"E8.30.0"),sQuery(id+"F0.wireOp",EDGE,"E8.31.0"),sQuery(id+"F0.wireOp",EDGE,"E8.32.0"),sQuery(id+"F0.wireOp",EDGE,"E8.33.0"),sQuery(id+"F0.wireOp",EDGE,"E8.34.0"),sQuery(id+"F0.wireOp",EDGE,"E8.35.0"),sQuery(id+"F0.wireOp",EDGE,"E8.36.0"),sQuery(id+"F0.wireOp",EDGE,"E8.37.0"),sQuery(id+"F0.wireOp",EDGE,"E8.38.0"),sQuery(id+"F0.wireOp",EDGE,"E8.39.0"),sQuery(id+"F0.wireOp",EDGE,"E8.40.0"),sQuery(id+"F0.wireOp",EDGE,"E8.41.0"),sQuery(id+"F0.wireOp",EDGE,"E8.42.0"),sQuery(id+"F0.wireOp",EDGE,"E8.43.0")])],"isStart":false})]});}
            var Q20;
            {var subQ0=sQuery(id+"F0.wireOp",EDGE,"E6.19.3");var subQ1=sQuery(id+"F0.wireOp",EDGE,"E6.19.1");Q20=makeQuery(id+"F2.opFillet","BLEND_EDGE",EDGE,{"blendedFrom":[makeQuery(id+"F1.opExtrude","SWEPT_EDGE",EDGE,{"disambiguationData":[OSD([sQuery(id+"F0.wireOp",EDGE,"E6.19.0"),subQ1,subQ0])]}),makeQuery(id+"F1.opExtrude","CAP_FACE",FACE,{"disambiguationData":[OSD([sQuery(id+"F0.wireOp",EDGE,"E0"),sQuery(id+"F0.wireOp",EDGE,"E1"),sQuery(id+"F0.wireOp",EDGE,"E2"),sQuery(id+"F0.wireOp",EDGE,"E4"),sQuery(id+"F0.wireOp",EDGE,"E5"),sQuery(id+"F0.wireOp",EDGE,"E6.1.1"),sQuery(id+"F0.wireOp",EDGE,"E6.1.2"),sQuery(id+"F0.wireOp",EDGE,"E6.1.3"),sQuery(id+"F0.wireOp",EDGE,"E6.1.4"),sQuery(id+"F0.wireOp",EDGE,"E6.2.1"),sQuery(id+"F0.wireOp",EDGE,"E6.2.2"),sQuery(id+"F0.wireOp",EDGE,"E6.2.3"),sQuery(id+"F0.wireOp",EDGE,"E6.2.4"),sQuery(id+"F0.wireOp",EDGE,"E6.3.1"),sQuery(id+"F0.wireOp",EDGE,"E6.3.2"),sQuery(id+"F0.wireOp",EDGE,"E6.3.3"),sQuery(id+"F0.wireOp",EDGE,"E6.3.4"),sQuery(id+"F0.wireOp",EDGE,"E6.4.1"),sQuery(id+"F0.wireOp",EDGE,"E6.4.2"),sQuery(id+"F0.wireOp",EDGE,"E6.4.3"),sQuery(id+"F0.wireOp",EDGE,"E6.4.4"),sQuery(id+"F0.wireOp",EDGE,"E6.5.1"),sQuery(id+"F0.wireOp",EDGE,"E6.5.2"),sQuery(id+"F0.wireOp",EDGE,"E6.5.3"),sQuery(id+"F0.wireOp",EDGE,"E6.5.4"),sQuery(id+"F0.wireOp",EDGE,"E6.6.1"),sQuery(id+"F0.wireOp",EDGE,"E6.6.2"),sQuery(id+"F0.wireOp",EDGE,"E6.6.3"),sQuery(id+"F0.wireOp",EDGE,"E6.6.4"),sQuery(id+"F0.wireOp",EDGE,"E6.7.1"),sQuery(id+"F0.wireOp",EDGE,"E6.7.2"),sQuery(id+"F0.wireOp",EDGE,"E6.7.3"),sQuery(id+"F0.wireOp",EDGE,"E6.7.4"),sQuery(id+"F0.wireOp",EDGE,"E6.8.1"),sQuery(id+"F0.wireOp",EDGE,"E6.8.2"),sQuery(id+"F0.wireOp",EDGE,"E6.8.3"),sQuery(id+"F0.wireOp",EDGE,"E6.8.4"),sQuery(id+"F0.wireOp",EDGE,"E6.9.1"),sQuery(id+"F0.wireOp",EDGE,"E6.9.2"),sQuery(id+"F0.wireOp",EDGE,"E6.9.3"),sQuery(id+"F0.wireOp",EDGE,"E6.9.4"),sQuery(id+"F0.wireOp",EDGE,"E6.10.1"),sQuery(id+"F0.wireOp",EDGE,"E6.10.2"),sQuery(id+"F0.wireOp",EDGE,"E6.10.3"),sQuery(id+"F0.wireOp",EDGE,"E6.10.4"),sQuery(id+"F0.wireOp",EDGE,"E6.11.1"),sQuery(id+"F0.wireOp",EDGE,"E6.11.2"),sQuery(id+"F0.wireOp",EDGE,"E6.11.3"),sQuery(id+"F0.wireOp",EDGE,"E6.11.4"),sQuery(id+"F0.wireOp",EDGE,"E6.12.1"),sQuery(id+"F0.wireOp",EDGE,"E6.12.2"),sQuery(id+"F0.wireOp",EDGE,"E6.12.3"),sQuery(id+"F0.wireOp",EDGE,"E6.12.4"),sQuery(id+"F0.wireOp",EDGE,"E6.13.1"),sQuery(id+"F0.wireOp",EDGE,"E6.13.2"),sQuery(id+"F0.wireOp",EDGE,"E6.13.3"),sQuery(id+"F0.wireOp",EDGE,"E6.13.4"),sQuery(id+"F0.wireOp",EDGE,"E6.14.1"),sQuery(id+"F0.wireOp",EDGE,"E6.14.2"),sQuery(id+"F0.wireOp",EDGE,"E6.14.3"),sQuery(id+"F0.wireOp",EDGE,"E6.14.4"),sQuery(id+"F0.wireOp",EDGE,"E6.15.1"),sQuery(id+"F0.wireOp",EDGE,"E6.15.2"),sQuery(id+"F0.wireOp",EDGE,"E6.15.3"),sQuery(id+"F0.wireOp",EDGE,"E6.15.4"),sQuery(id+"F0.wireOp",EDGE,"E6.16.1"),sQuery(id+"F0.wireOp",EDGE,"E6.16.2"),sQuery(id+"F0.wireOp",EDGE,"E6.16.3"),sQuery(id+"F0.wireOp",EDGE,"E6.16.4"),sQuery(id+"F0.wireOp",EDGE,"E6.17.1"),sQuery(id+"F0.wireOp",EDGE,"E6.17.2"),sQuery(id+"F0.wireOp",EDGE,"E6.17.3"),sQuery(id+"F0.wireOp",EDGE,"E6.17.4"),sQuery(id+"F0.wireOp",EDGE,"E6.18.1"),sQuery(id+"F0.wireOp",EDGE,"E6.18.2"),sQuery(id+"F0.wireOp",EDGE,"E6.18.3"),sQuery(id+"F0.wireOp",EDGE,"E6.18.4"),subQ1,sQuery(id+"F0.wireOp",EDGE,"E6.19.2"),subQ0,sQuery(id+"F0.wireOp",EDGE,"E6.19.4"),sQuery(id+"F0.wireOp",EDGE,"E6.20.1"),sQuery(id+"F0.wireOp",EDGE,"E6.20.2"),sQuery(id+"F0.wireOp",EDGE,"E6.20.3"),sQuery(id+"F0.wireOp",EDGE,"E6.20.4"),sQuery(id+"F0.wireOp",EDGE,"E6.21.1"),sQuery(id+"F0.wireOp",EDGE,"E6.21.2"),sQuery(id+"F0.wireOp",EDGE,"E6.21.3"),sQuery(id+"F0.wireOp",EDGE,"E6.21.4"),sQuery(id+"F0.wireOp",EDGE,"E6.22.1"),sQuery(id+"F0.wireOp",EDGE,"E6.22.2"),sQuery(id+"F0.wireOp",EDGE,"E6.22.3"),sQuery(id+"F0.wireOp",EDGE,"E6.22.4"),sQuery(id+"F0.wireOp",EDGE,"E6.23.1"),sQuery(id+"F0.wireOp",EDGE,"E6.23.2"),sQuery(id+"F0.wireOp",EDGE,"E6.23.3"),sQuery(id+"F0.wireOp",EDGE,"E6.23.4"),sQuery(id+"F0.wireOp",EDGE,"E6.24.1"),sQuery(id+"F0.wireOp",EDGE,"E6.24.2"),sQuery(id+"F0.wireOp",EDGE,"E6.24.3"),sQuery(id+"F0.wireOp",EDGE,"E6.24.4"),sQuery(id+"F0.wireOp",EDGE,"E6.25.1"),sQuery(id+"F0.wireOp",EDGE,"E6.25.2"),sQuery(id+"F0.wireOp",EDGE,"E6.25.3"),sQuery(id+"F0.wireOp",EDGE,"E6.25.4"),sQuery(id+"F0.wireOp",EDGE,"E6.26.1"),sQuery(id+"F0.wireOp",EDGE,"E6.26.2"),sQuery(id+"F0.wireOp",EDGE,"E6.26.3"),sQuery(id+"F0.wireOp",EDGE,"E6.26.4"),sQuery(id+"F0.wireOp",EDGE,"E6.27.1"),sQuery(id+"F0.wireOp",EDGE,"E6.27.2"),sQuery(id+"F0.wireOp",EDGE,"E6.27.3"),sQuery(id+"F0.wireOp",EDGE,"E6.27.4"),sQuery(id+"F0.wireOp",EDGE,"E6.28.1"),sQuery(id+"F0.wireOp",EDGE,"E6.28.2"),sQuery(id+"F0.wireOp",EDGE,"E6.28.3"),sQuery(id+"F0.wireOp",EDGE,"E6.28.4"),sQuery(id+"F0.wireOp",EDGE,"E6.29.1"),sQuery(id+"F0.wireOp",EDGE,"E6.29.2"),sQuery(id+"F0.wireOp",EDGE,"E6.29.3"),sQuery(id+"F0.wireOp",EDGE,"E6.29.4"),sQuery(id+"F0.wireOp",EDGE,"E6.30.1"),sQuery(id+"F0.wireOp",EDGE,"E6.30.2"),sQuery(id+"F0.wireOp",EDGE,"E6.30.3"),sQuery(id+"F0.wireOp",EDGE,"E6.30.4"),sQuery(id+"F0.wireOp",EDGE,"E6.31.1"),sQuery(id+"F0.wireOp",EDGE,"E6.31.2"),sQuery(id+"F0.wireOp",EDGE,"E6.31.3"),sQuery(id+"F0.wireOp",EDGE,"E6.31.4"),sQuery(id+"F0.wireOp",EDGE,"E6.32.1"),sQuery(id+"F0.wireOp",EDGE,"E6.32.2"),sQuery(id+"F0.wireOp",EDGE,"E6.32.3"),sQuery(id+"F0.wireOp",EDGE,"E6.32.4"),sQuery(id+"F0.wireOp",EDGE,"E6.33.1"),sQuery(id+"F0.wireOp",EDGE,"E6.33.2"),sQuery(id+"F0.wireOp",EDGE,"E6.33.3"),sQuery(id+"F0.wireOp",EDGE,"E6.33.4"),sQuery(id+"F0.wireOp",EDGE,"E6.34.1"),sQuery(id+"F0.wireOp",EDGE,"E6.34.2"),sQuery(id+"F0.wireOp",EDGE,"E6.34.3"),sQuery(id+"F0.wireOp",EDGE,"E6.34.4"),sQuery(id+"F0.wireOp",EDGE,"E6.35.1"),sQuery(id+"F0.wireOp",EDGE,"E6.35.2"),sQuery(id+"F0.wireOp",EDGE,"E6.35.3"),sQuery(id+"F0.wireOp",EDGE,"E6.35.4"),sQuery(id+"F0.wireOp",EDGE,"E6.36.1"),sQuery(id+"F0.wireOp",EDGE,"E6.36.2"),sQuery(id+"F0.wireOp",EDGE,"E6.36.3"),sQuery(id+"F0.wireOp",EDGE,"E6.36.4"),sQuery(id+"F0.wireOp",EDGE,"E6.37.1"),sQuery(id+"F0.wireOp",EDGE,"E6.37.2"),sQuery(id+"F0.wireOp",EDGE,"E6.37.3"),sQuery(id+"F0.wireOp",EDGE,"E6.37.4"),sQuery(id+"F0.wireOp",EDGE,"E6.38.1"),sQuery(id+"F0.wireOp",EDGE,"E6.38.2"),sQuery(id+"F0.wireOp",EDGE,"E6.38.3"),sQuery(id+"F0.wireOp",EDGE,"E6.38.4"),sQuery(id+"F0.wireOp",EDGE,"E6.39.1"),sQuery(id+"F0.wireOp",EDGE,"E6.39.2"),sQuery(id+"F0.wireOp",EDGE,"E6.39.3"),sQuery(id+"F0.wireOp",EDGE,"E6.39.4"),sQuery(id+"F0.wireOp",EDGE,"E6.40.1"),sQuery(id+"F0.wireOp",EDGE,"E6.40.2"),sQuery(id+"F0.wireOp",EDGE,"E6.40.3"),sQuery(id+"F0.wireOp",EDGE,"E6.40.4"),sQuery(id+"F0.wireOp",EDGE,"E6.41.1"),sQuery(id+"F0.wireOp",EDGE,"E6.41.2"),sQuery(id+"F0.wireOp",EDGE,"E6.41.3"),sQuery(id+"F0.wireOp",EDGE,"E6.41.4"),sQuery(id+"F0.wireOp",EDGE,"E6.42.1"),sQuery(id+"F0.wireOp",EDGE,"E6.42.2"),sQuery(id+"F0.wireOp",EDGE,"E6.42.3"),sQuery(id+"F0.wireOp",EDGE,"E6.42.4"),sQuery(id+"F0.wireOp",EDGE,"E6.43.1"),sQuery(id+"F0.wireOp",EDGE,"E6.43.2"),sQuery(id+"F0.wireOp",EDGE,"E6.43.3"),sQuery(id+"F0.wireOp",EDGE,"E6.43.4"),sQuery(id+"F0.wireOp",EDGE,"E7"),sQuery(id+"F0.wireOp",EDGE,"E8.1.0"),sQuery(id+"F0.wireOp",EDGE,"E8.2.0"),sQuery(id+"F0.wireOp",EDGE,"E8.3.0"),sQuery(id+"F0.wireOp",EDGE,"E8.4.0"),sQuery(id+"F0.wireOp",EDGE,"E8.5.0"),sQuery(id+"F0.wireOp",EDGE,"E8.6.0"),sQuery(id+"F0.wireOp",EDGE,"E8.7.0"),sQuery(id+"F0.wireOp",EDGE,"E8.8.0"),sQuery(id+"F0.wireOp",EDGE,"E8.9.0"),sQuery(id+"F0.wireOp",EDGE,"E8.10.0"),sQuery(id+"F0.wireOp",EDGE,"E8.11.0"),sQuery(id+"F0.wireOp",EDGE,"E8.12.0"),sQuery(id+"F0.wireOp",EDGE,"E8.13.0"),sQuery(id+"F0.wireOp",EDGE,"E8.14.0"),sQuery(id+"F0.wireOp",EDGE,"E8.15.0"),sQuery(id+"F0.wireOp",EDGE,"E8.16.0"),sQuery(id+"F0.wireOp",EDGE,"E8.17.0"),sQuery(id+"F0.wireOp",EDGE,"E8.18.0"),sQuery(id+"F0.wireOp",EDGE,"E8.19.0"),sQuery(id+"F0.wireOp",EDGE,"E8.20.0"),sQuery(id+"F0.wireOp",EDGE,"E8.21.0"),sQuery(id+"F0.wireOp",EDGE,"E8.22.0"),sQuery(id+"F0.wireOp",EDGE,"E8.23.0"),sQuery(id+"F0.wireOp",EDGE,"E8.24.0"),sQuery(id+"F0.wireOp",EDGE,"E8.25.0"),sQuery(id+"F0.wireOp",EDGE,"E8.26.0"),sQuery(id+"F0.wireOp",EDGE,"E8.27.0"),sQuery(id+"F0.wireOp",EDGE,"E8.28.0"),sQuery(id+"F0.wireOp",EDGE,"E8.29.0"),sQuery(id+"F0.wireOp",EDGE,"E8.30.0"),sQuery(id+"F0.wireOp",EDGE,"E8.31.0"),sQuery(id+"F0.wireOp",EDGE,"E8.32.0"),sQuery(id+"F0.wireOp",EDGE,"E8.33.0"),sQuery(id+"F0.wireOp",EDGE,"E8.34.0"),sQuery(id+"F0.wireOp",EDGE,"E8.35.0"),sQuery(id+"F0.wireOp",EDGE,"E8.36.0"),sQuery(id+"F0.wireOp",EDGE,"E8.37.0"),sQuery(id+"F0.wireOp",EDGE,"E8.38.0"),sQuery(id+"F0.wireOp",EDGE,"E8.39.0"),sQuery(id+"F0.wireOp",EDGE,"E8.40.0"),sQuery(id+"F0.wireOp",EDGE,"E8.41.0"),sQuery(id+"F0.wireOp",EDGE,"E8.42.0"),sQuery(id+"F0.wireOp",EDGE,"E8.43.0")])],"isStart":false})],"blendedInto":[makeQuery(id+"F1.opExtrude","CAP_FACE",FACE,{"disambiguationData":[OSD([sQuery(id+"F0.wireOp",EDGE,"E0"),sQuery(id+"F0.wireOp",EDGE,"E1"),sQuery(id+"F0.wireOp",EDGE,"E2"),sQuery(id+"F0.wireOp",EDGE,"E4"),sQuery(id+"F0.wireOp",EDGE,"E5"),sQuery(id+"F0.wireOp",EDGE,"E6.1.1"),sQuery(id+"F0.wireOp",EDGE,"E6.1.2"),sQuery(id+"F0.wireOp",EDGE,"E6.1.3"),sQuery(id+"F0.wireOp",EDGE,"E6.1.4"),sQuery(id+"F0.wireOp",EDGE,"E6.2.1"),sQuery(id+"F0.wireOp",EDGE,"E6.2.2"),sQuery(id+"F0.wireOp",EDGE,"E6.2.3"),sQuery(id+"F0.wireOp",EDGE,"E6.2.4"),sQuery(id+"F0.wireOp",EDGE,"E6.3.1"),sQuery(id+"F0.wireOp",EDGE,"E6.3.2"),sQuery(id+"F0.wireOp",EDGE,"E6.3.3"),sQuery(id+"F0.wireOp",EDGE,"E6.3.4"),sQuery(id+"F0.wireOp",EDGE,"E6.4.1"),sQuery(id+"F0.wireOp",EDGE,"E6.4.2"),sQuery(id+"F0.wireOp",EDGE,"E6.4.3"),sQuery(id+"F0.wireOp",EDGE,"E6.4.4"),sQuery(id+"F0.wireOp",EDGE,"E6.5.1"),sQuery(id+"F0.wireOp",EDGE,"E6.5.2"),sQuery(id+"F0.wireOp",EDGE,"E6.5.3"),sQuery(id+"F0.wireOp",EDGE,"E6.5.4"),sQuery(id+"F0.wireOp",EDGE,"E6.6.1"),sQuery(id+"F0.wireOp",EDGE,"E6.6.2"),sQuery(id+"F0.wireOp",EDGE,"E6.6.3"),sQuery(id+"F0.wireOp",EDGE,"E6.6.4"),sQuery(id+"F0.wireOp",EDGE,"E6.7.1"),sQuery(id+"F0.wireOp",EDGE,"E6.7.2"),sQuery(id+"F0.wireOp",EDGE,"E6.7.3"),sQuery(id+"F0.wireOp",EDGE,"E6.7.4"),sQuery(id+"F0.wireOp",EDGE,"E6.8.1"),sQuery(id+"F0.wireOp",EDGE,"E6.8.2"),sQuery(id+"F0.wireOp",EDGE,"E6.8.3"),sQuery(id+"F0.wireOp",EDGE,"E6.8.4"),sQuery(id+"F0.wireOp",EDGE,"E6.9.1"),sQuery(id+"F0.wireOp",EDGE,"E6.9.2"),sQuery(id+"F0.wireOp",EDGE,"E6.9.3"),sQuery(id+"F0.wireOp",EDGE,"E6.9.4"),sQuery(id+"F0.wireOp",EDGE,"E6.10.1"),sQuery(id+"F0.wireOp",EDGE,"E6.10.2"),sQuery(id+"F0.wireOp",EDGE,"E6.10.3"),sQuery(id+"F0.wireOp",EDGE,"E6.10.4"),sQuery(id+"F0.wireOp",EDGE,"E6.11.1"),sQuery(id+"F0.wireOp",EDGE,"E6.11.2"),sQuery(id+"F0.wireOp",EDGE,"E6.11.3"),sQuery(id+"F0.wireOp",EDGE,"E6.11.4"),sQuery(id+"F0.wireOp",EDGE,"E6.12.1"),sQuery(id+"F0.wireOp",EDGE,"E6.12.2"),sQuery(id+"F0.wireOp",EDGE,"E6.12.3"),sQuery(id+"F0.wireOp",EDGE,"E6.12.4"),sQuery(id+"F0.wireOp",EDGE,"E6.13.1"),sQuery(id+"F0.wireOp",EDGE,"E6.13.2"),sQuery(id+"F0.wireOp",EDGE,"E6.13.3"),sQuery(id+"F0.wireOp",EDGE,"E6.13.4"),sQuery(id+"F0.wireOp",EDGE,"E6.14.1"),sQuery(id+"F0.wireOp",EDGE,"E6.14.2"),sQuery(id+"F0.wireOp",EDGE,"E6.14.3"),sQuery(id+"F0.wireOp",EDGE,"E6.14.4"),sQuery(id+"F0.wireOp",EDGE,"E6.15.1"),sQuery(id+"F0.wireOp",EDGE,"E6.15.2"),sQuery(id+"F0.wireOp",EDGE,"E6.15.3"),sQuery(id+"F0.wireOp",EDGE,"E6.15.4"),sQuery(id+"F0.wireOp",EDGE,"E6.16.1"),sQuery(id+"F0.wireOp",EDGE,"E6.16.2"),sQuery(id+"F0.wireOp",EDGE,"E6.16.3"),sQuery(id+"F0.wireOp",EDGE,"E6.16.4"),sQuery(id+"F0.wireOp",EDGE,"E6.17.1"),sQuery(id+"F0.wireOp",EDGE,"E6.17.2"),sQuery(id+"F0.wireOp",EDGE,"E6.17.3"),sQuery(id+"F0.wireOp",EDGE,"E6.17.4"),sQuery(id+"F0.wireOp",EDGE,"E6.18.1"),sQuery(id+"F0.wireOp",EDGE,"E6.18.2"),sQuery(id+"F0.wireOp",EDGE,"E6.18.3"),sQuery(id+"F0.wireOp",EDGE,"E6.18.4"),subQ1,sQuery(id+"F0.wireOp",EDGE,"E6.19.2"),subQ0,sQuery(id+"F0.wireOp",EDGE,"E6.19.4"),sQuery(id+"F0.wireOp",EDGE,"E6.20.1"),sQuery(id+"F0.wireOp",EDGE,"E6.20.2"),sQuery(id+"F0.wireOp",EDGE,"E6.20.3"),sQuery(id+"F0.wireOp",EDGE,"E6.20.4"),sQuery(id+"F0.wireOp",EDGE,"E6.21.1"),sQuery(id+"F0.wireOp",EDGE,"E6.21.2"),sQuery(id+"F0.wireOp",EDGE,"E6.21.3"),sQuery(id+"F0.wireOp",EDGE,"E6.21.4"),sQuery(id+"F0.wireOp",EDGE,"E6.22.1"),sQuery(id+"F0.wireOp",EDGE,"E6.22.2"),sQuery(id+"F0.wireOp",EDGE,"E6.22.3"),sQuery(id+"F0.wireOp",EDGE,"E6.22.4"),sQuery(id+"F0.wireOp",EDGE,"E6.23.1"),sQuery(id+"F0.wireOp",EDGE,"E6.23.2"),sQuery(id+"F0.wireOp",EDGE,"E6.23.3"),sQuery(id+"F0.wireOp",EDGE,"E6.23.4"),sQuery(id+"F0.wireOp",EDGE,"E6.24.1"),sQuery(id+"F0.wireOp",EDGE,"E6.24.2"),sQuery(id+"F0.wireOp",EDGE,"E6.24.3"),sQuery(id+"F0.wireOp",EDGE,"E6.24.4"),sQuery(id+"F0.wireOp",EDGE,"E6.25.1"),sQuery(id+"F0.wireOp",EDGE,"E6.25.2"),sQuery(id+"F0.wireOp",EDGE,"E6.25.3"),sQuery(id+"F0.wireOp",EDGE,"E6.25.4"),sQuery(id+"F0.wireOp",EDGE,"E6.26.1"),sQuery(id+"F0.wireOp",EDGE,"E6.26.2"),sQuery(id+"F0.wireOp",EDGE,"E6.26.3"),sQuery(id+"F0.wireOp",EDGE,"E6.26.4"),sQuery(id+"F0.wireOp",EDGE,"E6.27.1"),sQuery(id+"F0.wireOp",EDGE,"E6.27.2"),sQuery(id+"F0.wireOp",EDGE,"E6.27.3"),sQuery(id+"F0.wireOp",EDGE,"E6.27.4"),sQuery(id+"F0.wireOp",EDGE,"E6.28.1"),sQuery(id+"F0.wireOp",EDGE,"E6.28.2"),sQuery(id+"F0.wireOp",EDGE,"E6.28.3"),sQuery(id+"F0.wireOp",EDGE,"E6.28.4"),sQuery(id+"F0.wireOp",EDGE,"E6.29.1"),sQuery(id+"F0.wireOp",EDGE,"E6.29.2"),sQuery(id+"F0.wireOp",EDGE,"E6.29.3"),sQuery(id+"F0.wireOp",EDGE,"E6.29.4"),sQuery(id+"F0.wireOp",EDGE,"E6.30.1"),sQuery(id+"F0.wireOp",EDGE,"E6.30.2"),sQuery(id+"F0.wireOp",EDGE,"E6.30.3"),sQuery(id+"F0.wireOp",EDGE,"E6.30.4"),sQuery(id+"F0.wireOp",EDGE,"E6.31.1"),sQuery(id+"F0.wireOp",EDGE,"E6.31.2"),sQuery(id+"F0.wireOp",EDGE,"E6.31.3"),sQuery(id+"F0.wireOp",EDGE,"E6.31.4"),sQuery(id+"F0.wireOp",EDGE,"E6.32.1"),sQuery(id+"F0.wireOp",EDGE,"E6.32.2"),sQuery(id+"F0.wireOp",EDGE,"E6.32.3"),sQuery(id+"F0.wireOp",EDGE,"E6.32.4"),sQuery(id+"F0.wireOp",EDGE,"E6.33.1"),sQuery(id+"F0.wireOp",EDGE,"E6.33.2"),sQuery(id+"F0.wireOp",EDGE,"E6.33.3"),sQuery(id+"F0.wireOp",EDGE,"E6.33.4"),sQuery(id+"F0.wireOp",EDGE,"E6.34.1"),sQuery(id+"F0.wireOp",EDGE,"E6.34.2"),sQuery(id+"F0.wireOp",EDGE,"E6.34.3"),sQuery(id+"F0.wireOp",EDGE,"E6.34.4"),sQuery(id+"F0.wireOp",EDGE,"E6.35.1"),sQuery(id+"F0.wireOp",EDGE,"E6.35.2"),sQuery(id+"F0.wireOp",EDGE,"E6.35.3"),sQuery(id+"F0.wireOp",EDGE,"E6.35.4"),sQuery(id+"F0.wireOp",EDGE,"E6.36.1"),sQuery(id+"F0.wireOp",EDGE,"E6.36.2"),sQuery(id+"F0.wireOp",EDGE,"E6.36.3"),sQuery(id+"F0.wireOp",EDGE,"E6.36.4"),sQuery(id+"F0.wireOp",EDGE,"E6.37.1"),sQuery(id+"F0.wireOp",EDGE,"E6.37.2"),sQuery(id+"F0.wireOp",EDGE,"E6.37.3"),sQuery(id+"F0.wireOp",EDGE,"E6.37.4"),sQuery(id+"F0.wireOp",EDGE,"E6.38.1"),sQuery(id+"F0.wireOp",EDGE,"E6.38.2"),sQuery(id+"F0.wireOp",EDGE,"E6.38.3"),sQuery(id+"F0.wireOp",EDGE,"E6.38.4"),sQuery(id+"F0.wireOp",EDGE,"E6.39.1"),sQuery(id+"F0.wireOp",EDGE,"E6.39.2"),sQuery(id+"F0.wireOp",EDGE,"E6.39.3"),sQuery(id+"F0.wireOp",EDGE,"E6.39.4"),sQuery(id+"F0.wireOp",EDGE,"E6.40.1"),sQuery(id+"F0.wireOp",EDGE,"E6.40.2"),sQuery(id+"F0.wireOp",EDGE,"E6.40.3"),sQuery(id+"F0.wireOp",EDGE,"E6.40.4"),sQuery(id+"F0.wireOp",EDGE,"E6.41.1"),sQuery(id+"F0.wireOp",EDGE,"E6.41.2"),sQuery(id+"F0.wireOp",EDGE,"E6.41.3"),sQuery(id+"F0.wireOp",EDGE,"E6.41.4"),sQuery(id+"F0.wireOp",EDGE,"E6.42.1"),sQuery(id+"F0.wireOp",EDGE,"E6.42.2"),sQuery(id+"F0.wireOp",EDGE,"E6.42.3"),sQuery(id+"F0.wireOp",EDGE,"E6.42.4"),sQuery(id+"F0.wireOp",EDGE,"E6.43.1"),sQuery(id+"F0.wireOp",EDGE,"E6.43.2"),sQuery(id+"F0.wireOp",EDGE,"E6.43.3"),sQuery(id+"F0.wireOp",EDGE,"E6.43.4"),sQuery(id+"F0.wireOp",EDGE,"E7"),sQuery(id+"F0.wireOp",EDGE,"E8.1.0"),sQuery(id+"F0.wireOp",EDGE,"E8.2.0"),sQuery(id+"F0.wireOp",EDGE,"E8.3.0"),sQuery(id+"F0.wireOp",EDGE,"E8.4.0"),sQuery(id+"F0.wireOp",EDGE,"E8.5.0"),sQuery(id+"F0.wireOp",EDGE,"E8.6.0"),sQuery(id+"F0.wireOp",EDGE,"E8.7.0"),sQuery(id+"F0.wireOp",EDGE,"E8.8.0"),sQuery(id+"F0.wireOp",EDGE,"E8.9.0"),sQuery(id+"F0.wireOp",EDGE,"E8.10.0"),sQuery(id+"F0.wireOp",EDGE,"E8.11.0"),sQuery(id+"F0.wireOp",EDGE,"E8.12.0"),sQuery(id+"F0.wireOp",EDGE,"E8.13.0"),sQuery(id+"F0.wireOp",EDGE,"E8.14.0"),sQuery(id+"F0.wireOp",EDGE,"E8.15.0"),sQuery(id+"F0.wireOp",EDGE,"E8.16.0"),sQuery(id+"F0.wireOp",EDGE,"E8.17.0"),sQuery(id+"F0.wireOp",EDGE,"E8.18.0"),sQuery(id+"F0.wireOp",EDGE,"E8.19.0"),sQuery(id+"F0.wireOp",EDGE,"E8.20.0"),sQuery(id+"F0.wireOp",EDGE,"E8.21.0"),sQuery(id+"F0.wireOp",EDGE,"E8.22.0"),sQuery(id+"F0.wireOp",EDGE,"E8.23.0"),sQuery(id+"F0.wireOp",EDGE,"E8.24.0"),sQuery(id+"F0.wireOp",EDGE,"E8.25.0"),sQuery(id+"F0.wireOp",EDGE,"E8.26.0"),sQuery(id+"F0.wireOp",EDGE,"E8.27.0"),sQuery(id+"F0.wireOp",EDGE,"E8.28.0"),sQuery(id+"F0.wireOp",EDGE,"E8.29.0"),sQuery(id+"F0.wireOp",EDGE,"E8.30.0"),sQuery(id+"F0.wireOp",EDGE,"E8.31.0"),sQuery(id+"F0.wireOp",EDGE,"E8.32.0"),sQuery(id+"F0.wireOp",EDGE,"E8.33.0"),sQuery(id+"F0.wireOp",EDGE,"E8.34.0"),sQuery(id+"F0.wireOp",EDGE,"E8.35.0"),sQuery(id+"F0.wireOp",EDGE,"E8.36.0"),sQuery(id+"F0.wireOp",EDGE,"E8.37.0"),sQuery(id+"F0.wireOp",EDGE,"E8.38.0"),sQuery(id+"F0.wireOp",EDGE,"E8.39.0"),sQuery(id+"F0.wireOp",EDGE,"E8.40.0"),sQuery(id+"F0.wireOp",EDGE,"E8.41.0"),sQuery(id+"F0.wireOp",EDGE,"E8.42.0"),sQuery(id+"F0.wireOp",EDGE,"E8.43.0")])],"isStart":false})]});}
            var Q21;
            {var subQ0=sQuery(id+"F0.wireOp",EDGE,"E6.21.3");var subQ1=sQuery(id+"F0.wireOp",EDGE,"E6.21.1");Q21=makeQuery(id+"F2.opFillet","BLEND_EDGE",EDGE,{"blendedFrom":[makeQuery(id+"F1.opExtrude","SWEPT_EDGE",EDGE,{"disambiguationData":[OSD([sQuery(id+"F0.wireOp",EDGE,"E6.21.0"),subQ1,subQ0])]}),makeQuery(id+"F1.opExtrude","CAP_FACE",FACE,{"disambiguationData":[OSD([sQuery(id+"F0.wireOp",EDGE,"E0"),sQuery(id+"F0.wireOp",EDGE,"E1"),sQuery(id+"F0.wireOp",EDGE,"E2"),sQuery(id+"F0.wireOp",EDGE,"E4"),sQuery(id+"F0.wireOp",EDGE,"E5"),sQuery(id+"F0.wireOp",EDGE,"E6.1.1"),sQuery(id+"F0.wireOp",EDGE,"E6.1.2"),sQuery(id+"F0.wireOp",EDGE,"E6.1.3"),sQuery(id+"F0.wireOp",EDGE,"E6.1.4"),sQuery(id+"F0.wireOp",EDGE,"E6.2.1"),sQuery(id+"F0.wireOp",EDGE,"E6.2.2"),sQuery(id+"F0.wireOp",EDGE,"E6.2.3"),sQuery(id+"F0.wireOp",EDGE,"E6.2.4"),sQuery(id+"F0.wireOp",EDGE,"E6.3.1"),sQuery(id+"F0.wireOp",EDGE,"E6.3.2"),sQuery(id+"F0.wireOp",EDGE,"E6.3.3"),sQuery(id+"F0.wireOp",EDGE,"E6.3.4"),sQuery(id+"F0.wireOp",EDGE,"E6.4.1"),sQuery(id+"F0.wireOp",EDGE,"E6.4.2"),sQuery(id+"F0.wireOp",EDGE,"E6.4.3"),sQuery(id+"F0.wireOp",EDGE,"E6.4.4"),sQuery(id+"F0.wireOp",EDGE,"E6.5.1"),sQuery(id+"F0.wireOp",EDGE,"E6.5.2"),sQuery(id+"F0.wireOp",EDGE,"E6.5.3"),sQuery(id+"F0.wireOp",EDGE,"E6.5.4"),sQuery(id+"F0.wireOp",EDGE,"E6.6.1"),sQuery(id+"F0.wireOp",EDGE,"E6.6.2"),sQuery(id+"F0.wireOp",EDGE,"E6.6.3"),sQuery(id+"F0.wireOp",EDGE,"E6.6.4"),sQuery(id+"F0.wireOp",EDGE,"E6.7.1"),sQuery(id+"F0.wireOp",EDGE,"E6.7.2"),sQuery(id+"F0.wireOp",EDGE,"E6.7.3"),sQuery(id+"F0.wireOp",EDGE,"E6.7.4"),sQuery(id+"F0.wireOp",EDGE,"E6.8.1"),sQuery(id+"F0.wireOp",EDGE,"E6.8.2"),sQuery(id+"F0.wireOp",EDGE,"E6.8.3"),sQuery(id+"F0.wireOp",EDGE,"E6.8.4"),sQuery(id+"F0.wireOp",EDGE,"E6.9.1"),sQuery(id+"F0.wireOp",EDGE,"E6.9.2"),sQuery(id+"F0.wireOp",EDGE,"E6.9.3"),sQuery(id+"F0.wireOp",EDGE,"E6.9.4"),sQuery(id+"F0.wireOp",EDGE,"E6.10.1"),sQuery(id+"F0.wireOp",EDGE,"E6.10.2"),sQuery(id+"F0.wireOp",EDGE,"E6.10.3"),sQuery(id+"F0.wireOp",EDGE,"E6.10.4"),sQuery(id+"F0.wireOp",EDGE,"E6.11.1"),sQuery(id+"F0.wireOp",EDGE,"E6.11.2"),sQuery(id+"F0.wireOp",EDGE,"E6.11.3"),sQuery(id+"F0.wireOp",EDGE,"E6.11.4"),sQuery(id+"F0.wireOp",EDGE,"E6.12.1"),sQuery(id+"F0.wireOp",EDGE,"E6.12.2"),sQuery(id+"F0.wireOp",EDGE,"E6.12.3"),sQuery(id+"F0.wireOp",EDGE,"E6.12.4"),sQuery(id+"F0.wireOp",EDGE,"E6.13.1"),sQuery(id+"F0.wireOp",EDGE,"E6.13.2"),sQuery(id+"F0.wireOp",EDGE,"E6.13.3"),sQuery(id+"F0.wireOp",EDGE,"E6.13.4"),sQuery(id+"F0.wireOp",EDGE,"E6.14.1"),sQuery(id+"F0.wireOp",EDGE,"E6.14.2"),sQuery(id+"F0.wireOp",EDGE,"E6.14.3"),sQuery(id+"F0.wireOp",EDGE,"E6.14.4"),sQuery(id+"F0.wireOp",EDGE,"E6.15.1"),sQuery(id+"F0.wireOp",EDGE,"E6.15.2"),sQuery(id+"F0.wireOp",EDGE,"E6.15.3"),sQuery(id+"F0.wireOp",EDGE,"E6.15.4"),sQuery(id+"F0.wireOp",EDGE,"E6.16.1"),sQuery(id+"F0.wireOp",EDGE,"E6.16.2"),sQuery(id+"F0.wireOp",EDGE,"E6.16.3"),sQuery(id+"F0.wireOp",EDGE,"E6.16.4"),sQuery(id+"F0.wireOp",EDGE,"E6.17.1"),sQuery(id+"F0.wireOp",EDGE,"E6.17.2"),sQuery(id+"F0.wireOp",EDGE,"E6.17.3"),sQuery(id+"F0.wireOp",EDGE,"E6.17.4"),sQuery(id+"F0.wireOp",EDGE,"E6.18.1"),sQuery(id+"F0.wireOp",EDGE,"E6.18.2"),sQuery(id+"F0.wireOp",EDGE,"E6.18.3"),sQuery(id+"F0.wireOp",EDGE,"E6.18.4"),sQuery(id+"F0.wireOp",EDGE,"E6.19.1"),sQuery(id+"F0.wireOp",EDGE,"E6.19.2"),sQuery(id+"F0.wireOp",EDGE,"E6.19.3"),sQuery(id+"F0.wireOp",EDGE,"E6.19.4"),sQuery(id+"F0.wireOp",EDGE,"E6.20.1"),sQuery(id+"F0.wireOp",EDGE,"E6.20.2"),sQuery(id+"F0.wireOp",EDGE,"E6.20.3"),sQuery(id+"F0.wireOp",EDGE,"E6.20.4"),subQ1,sQuery(id+"F0.wireOp",EDGE,"E6.21.2"),subQ0,sQuery(id+"F0.wireOp",EDGE,"E6.21.4"),sQuery(id+"F0.wireOp",EDGE,"E6.22.1"),sQuery(id+"F0.wireOp",EDGE,"E6.22.2"),sQuery(id+"F0.wireOp",EDGE,"E6.22.3"),sQuery(id+"F0.wireOp",EDGE,"E6.22.4"),sQuery(id+"F0.wireOp",EDGE,"E6.23.1"),sQuery(id+"F0.wireOp",EDGE,"E6.23.2"),sQuery(id+"F0.wireOp",EDGE,"E6.23.3"),sQuery(id+"F0.wireOp",EDGE,"E6.23.4"),sQuery(id+"F0.wireOp",EDGE,"E6.24.1"),sQuery(id+"F0.wireOp",EDGE,"E6.24.2"),sQuery(id+"F0.wireOp",EDGE,"E6.24.3"),sQuery(id+"F0.wireOp",EDGE,"E6.24.4"),sQuery(id+"F0.wireOp",EDGE,"E6.25.1"),sQuery(id+"F0.wireOp",EDGE,"E6.25.2"),sQuery(id+"F0.wireOp",EDGE,"E6.25.3"),sQuery(id+"F0.wireOp",EDGE,"E6.25.4"),sQuery(id+"F0.wireOp",EDGE,"E6.26.1"),sQuery(id+"F0.wireOp",EDGE,"E6.26.2"),sQuery(id+"F0.wireOp",EDGE,"E6.26.3"),sQuery(id+"F0.wireOp",EDGE,"E6.26.4"),sQuery(id+"F0.wireOp",EDGE,"E6.27.1"),sQuery(id+"F0.wireOp",EDGE,"E6.27.2"),sQuery(id+"F0.wireOp",EDGE,"E6.27.3"),sQuery(id+"F0.wireOp",EDGE,"E6.27.4"),sQuery(id+"F0.wireOp",EDGE,"E6.28.1"),sQuery(id+"F0.wireOp",EDGE,"E6.28.2"),sQuery(id+"F0.wireOp",EDGE,"E6.28.3"),sQuery(id+"F0.wireOp",EDGE,"E6.28.4"),sQuery(id+"F0.wireOp",EDGE,"E6.29.1"),sQuery(id+"F0.wireOp",EDGE,"E6.29.2"),sQuery(id+"F0.wireOp",EDGE,"E6.29.3"),sQuery(id+"F0.wireOp",EDGE,"E6.29.4"),sQuery(id+"F0.wireOp",EDGE,"E6.30.1"),sQuery(id+"F0.wireOp",EDGE,"E6.30.2"),sQuery(id+"F0.wireOp",EDGE,"E6.30.3"),sQuery(id+"F0.wireOp",EDGE,"E6.30.4"),sQuery(id+"F0.wireOp",EDGE,"E6.31.1"),sQuery(id+"F0.wireOp",EDGE,"E6.31.2"),sQuery(id+"F0.wireOp",EDGE,"E6.31.3"),sQuery(id+"F0.wireOp",EDGE,"E6.31.4"),sQuery(id+"F0.wireOp",EDGE,"E6.32.1"),sQuery(id+"F0.wireOp",EDGE,"E6.32.2"),sQuery(id+"F0.wireOp",EDGE,"E6.32.3"),sQuery(id+"F0.wireOp",EDGE,"E6.32.4"),sQuery(id+"F0.wireOp",EDGE,"E6.33.1"),sQuery(id+"F0.wireOp",EDGE,"E6.33.2"),sQuery(id+"F0.wireOp",EDGE,"E6.33.3"),sQuery(id+"F0.wireOp",EDGE,"E6.33.4"),sQuery(id+"F0.wireOp",EDGE,"E6.34.1"),sQuery(id+"F0.wireOp",EDGE,"E6.34.2"),sQuery(id+"F0.wireOp",EDGE,"E6.34.3"),sQuery(id+"F0.wireOp",EDGE,"E6.34.4"),sQuery(id+"F0.wireOp",EDGE,"E6.35.1"),sQuery(id+"F0.wireOp",EDGE,"E6.35.2"),sQuery(id+"F0.wireOp",EDGE,"E6.35.3"),sQuery(id+"F0.wireOp",EDGE,"E6.35.4"),sQuery(id+"F0.wireOp",EDGE,"E6.36.1"),sQuery(id+"F0.wireOp",EDGE,"E6.36.2"),sQuery(id+"F0.wireOp",EDGE,"E6.36.3"),sQuery(id+"F0.wireOp",EDGE,"E6.36.4"),sQuery(id+"F0.wireOp",EDGE,"E6.37.1"),sQuery(id+"F0.wireOp",EDGE,"E6.37.2"),sQuery(id+"F0.wireOp",EDGE,"E6.37.3"),sQuery(id+"F0.wireOp",EDGE,"E6.37.4"),sQuery(id+"F0.wireOp",EDGE,"E6.38.1"),sQuery(id+"F0.wireOp",EDGE,"E6.38.2"),sQuery(id+"F0.wireOp",EDGE,"E6.38.3"),sQuery(id+"F0.wireOp",EDGE,"E6.38.4"),sQuery(id+"F0.wireOp",EDGE,"E6.39.1"),sQuery(id+"F0.wireOp",EDGE,"E6.39.2"),sQuery(id+"F0.wireOp",EDGE,"E6.39.3"),sQuery(id+"F0.wireOp",EDGE,"E6.39.4"),sQuery(id+"F0.wireOp",EDGE,"E6.40.1"),sQuery(id+"F0.wireOp",EDGE,"E6.40.2"),sQuery(id+"F0.wireOp",EDGE,"E6.40.3"),sQuery(id+"F0.wireOp",EDGE,"E6.40.4"),sQuery(id+"F0.wireOp",EDGE,"E6.41.1"),sQuery(id+"F0.wireOp",EDGE,"E6.41.2"),sQuery(id+"F0.wireOp",EDGE,"E6.41.3"),sQuery(id+"F0.wireOp",EDGE,"E6.41.4"),sQuery(id+"F0.wireOp",EDGE,"E6.42.1"),sQuery(id+"F0.wireOp",EDGE,"E6.42.2"),sQuery(id+"F0.wireOp",EDGE,"E6.42.3"),sQuery(id+"F0.wireOp",EDGE,"E6.42.4"),sQuery(id+"F0.wireOp",EDGE,"E6.43.1"),sQuery(id+"F0.wireOp",EDGE,"E6.43.2"),sQuery(id+"F0.wireOp",EDGE,"E6.43.3"),sQuery(id+"F0.wireOp",EDGE,"E6.43.4"),sQuery(id+"F0.wireOp",EDGE,"E7"),sQuery(id+"F0.wireOp",EDGE,"E8.1.0"),sQuery(id+"F0.wireOp",EDGE,"E8.2.0"),sQuery(id+"F0.wireOp",EDGE,"E8.3.0"),sQuery(id+"F0.wireOp",EDGE,"E8.4.0"),sQuery(id+"F0.wireOp",EDGE,"E8.5.0"),sQuery(id+"F0.wireOp",EDGE,"E8.6.0"),sQuery(id+"F0.wireOp",EDGE,"E8.7.0"),sQuery(id+"F0.wireOp",EDGE,"E8.8.0"),sQuery(id+"F0.wireOp",EDGE,"E8.9.0"),sQuery(id+"F0.wireOp",EDGE,"E8.10.0"),sQuery(id+"F0.wireOp",EDGE,"E8.11.0"),sQuery(id+"F0.wireOp",EDGE,"E8.12.0"),sQuery(id+"F0.wireOp",EDGE,"E8.13.0"),sQuery(id+"F0.wireOp",EDGE,"E8.14.0"),sQuery(id+"F0.wireOp",EDGE,"E8.15.0"),sQuery(id+"F0.wireOp",EDGE,"E8.16.0"),sQuery(id+"F0.wireOp",EDGE,"E8.17.0"),sQuery(id+"F0.wireOp",EDGE,"E8.18.0"),sQuery(id+"F0.wireOp",EDGE,"E8.19.0"),sQuery(id+"F0.wireOp",EDGE,"E8.20.0"),sQuery(id+"F0.wireOp",EDGE,"E8.21.0"),sQuery(id+"F0.wireOp",EDGE,"E8.22.0"),sQuery(id+"F0.wireOp",EDGE,"E8.23.0"),sQuery(id+"F0.wireOp",EDGE,"E8.24.0"),sQuery(id+"F0.wireOp",EDGE,"E8.25.0"),sQuery(id+"F0.wireOp",EDGE,"E8.26.0"),sQuery(id+"F0.wireOp",EDGE,"E8.27.0"),sQuery(id+"F0.wireOp",EDGE,"E8.28.0"),sQuery(id+"F0.wireOp",EDGE,"E8.29.0"),sQuery(id+"F0.wireOp",EDGE,"E8.30.0"),sQuery(id+"F0.wireOp",EDGE,"E8.31.0"),sQuery(id+"F0.wireOp",EDGE,"E8.32.0"),sQuery(id+"F0.wireOp",EDGE,"E8.33.0"),sQuery(id+"F0.wireOp",EDGE,"E8.34.0"),sQuery(id+"F0.wireOp",EDGE,"E8.35.0"),sQuery(id+"F0.wireOp",EDGE,"E8.36.0"),sQuery(id+"F0.wireOp",EDGE,"E8.37.0"),sQuery(id+"F0.wireOp",EDGE,"E8.38.0"),sQuery(id+"F0.wireOp",EDGE,"E8.39.0"),sQuery(id+"F0.wireOp",EDGE,"E8.40.0"),sQuery(id+"F0.wireOp",EDGE,"E8.41.0"),sQuery(id+"F0.wireOp",EDGE,"E8.42.0"),sQuery(id+"F0.wireOp",EDGE,"E8.43.0")])],"isStart":false})],"blendedInto":[makeQuery(id+"F1.opExtrude","CAP_FACE",FACE,{"disambiguationData":[OSD([sQuery(id+"F0.wireOp",EDGE,"E0"),sQuery(id+"F0.wireOp",EDGE,"E1"),sQuery(id+"F0.wireOp",EDGE,"E2"),sQuery(id+"F0.wireOp",EDGE,"E4"),sQuery(id+"F0.wireOp",EDGE,"E5"),sQuery(id+"F0.wireOp",EDGE,"E6.1.1"),sQuery(id+"F0.wireOp",EDGE,"E6.1.2"),sQuery(id+"F0.wireOp",EDGE,"E6.1.3"),sQuery(id+"F0.wireOp",EDGE,"E6.1.4"),sQuery(id+"F0.wireOp",EDGE,"E6.2.1"),sQuery(id+"F0.wireOp",EDGE,"E6.2.2"),sQuery(id+"F0.wireOp",EDGE,"E6.2.3"),sQuery(id+"F0.wireOp",EDGE,"E6.2.4"),sQuery(id+"F0.wireOp",EDGE,"E6.3.1"),sQuery(id+"F0.wireOp",EDGE,"E6.3.2"),sQuery(id+"F0.wireOp",EDGE,"E6.3.3"),sQuery(id+"F0.wireOp",EDGE,"E6.3.4"),sQuery(id+"F0.wireOp",EDGE,"E6.4.1"),sQuery(id+"F0.wireOp",EDGE,"E6.4.2"),sQuery(id+"F0.wireOp",EDGE,"E6.4.3"),sQuery(id+"F0.wireOp",EDGE,"E6.4.4"),sQuery(id+"F0.wireOp",EDGE,"E6.5.1"),sQuery(id+"F0.wireOp",EDGE,"E6.5.2"),sQuery(id+"F0.wireOp",EDGE,"E6.5.3"),sQuery(id+"F0.wireOp",EDGE,"E6.5.4"),sQuery(id+"F0.wireOp",EDGE,"E6.6.1"),sQuery(id+"F0.wireOp",EDGE,"E6.6.2"),sQuery(id+"F0.wireOp",EDGE,"E6.6.3"),sQuery(id+"F0.wireOp",EDGE,"E6.6.4"),sQuery(id+"F0.wireOp",EDGE,"E6.7.1"),sQuery(id+"F0.wireOp",EDGE,"E6.7.2"),sQuery(id+"F0.wireOp",EDGE,"E6.7.3"),sQuery(id+"F0.wireOp",EDGE,"E6.7.4"),sQuery(id+"F0.wireOp",EDGE,"E6.8.1"),sQuery(id+"F0.wireOp",EDGE,"E6.8.2"),sQuery(id+"F0.wireOp",EDGE,"E6.8.3"),sQuery(id+"F0.wireOp",EDGE,"E6.8.4"),sQuery(id+"F0.wireOp",EDGE,"E6.9.1"),sQuery(id+"F0.wireOp",EDGE,"E6.9.2"),sQuery(id+"F0.wireOp",EDGE,"E6.9.3"),sQuery(id+"F0.wireOp",EDGE,"E6.9.4"),sQuery(id+"F0.wireOp",EDGE,"E6.10.1"),sQuery(id+"F0.wireOp",EDGE,"E6.10.2"),sQuery(id+"F0.wireOp",EDGE,"E6.10.3"),sQuery(id+"F0.wireOp",EDGE,"E6.10.4"),sQuery(id+"F0.wireOp",EDGE,"E6.11.1"),sQuery(id+"F0.wireOp",EDGE,"E6.11.2"),sQuery(id+"F0.wireOp",EDGE,"E6.11.3"),sQuery(id+"F0.wireOp",EDGE,"E6.11.4"),sQuery(id+"F0.wireOp",EDGE,"E6.12.1"),sQuery(id+"F0.wireOp",EDGE,"E6.12.2"),sQuery(id+"F0.wireOp",EDGE,"E6.12.3"),sQuery(id+"F0.wireOp",EDGE,"E6.12.4"),sQuery(id+"F0.wireOp",EDGE,"E6.13.1"),sQuery(id+"F0.wireOp",EDGE,"E6.13.2"),sQuery(id+"F0.wireOp",EDGE,"E6.13.3"),sQuery(id+"F0.wireOp",EDGE,"E6.13.4"),sQuery(id+"F0.wireOp",EDGE,"E6.14.1"),sQuery(id+"F0.wireOp",EDGE,"E6.14.2"),sQuery(id+"F0.wireOp",EDGE,"E6.14.3"),sQuery(id+"F0.wireOp",EDGE,"E6.14.4"),sQuery(id+"F0.wireOp",EDGE,"E6.15.1"),sQuery(id+"F0.wireOp",EDGE,"E6.15.2"),sQuery(id+"F0.wireOp",EDGE,"E6.15.3"),sQuery(id+"F0.wireOp",EDGE,"E6.15.4"),sQuery(id+"F0.wireOp",EDGE,"E6.16.1"),sQuery(id+"F0.wireOp",EDGE,"E6.16.2"),sQuery(id+"F0.wireOp",EDGE,"E6.16.3"),sQuery(id+"F0.wireOp",EDGE,"E6.16.4"),sQuery(id+"F0.wireOp",EDGE,"E6.17.1"),sQuery(id+"F0.wireOp",EDGE,"E6.17.2"),sQuery(id+"F0.wireOp",EDGE,"E6.17.3"),sQuery(id+"F0.wireOp",EDGE,"E6.17.4"),sQuery(id+"F0.wireOp",EDGE,"E6.18.1"),sQuery(id+"F0.wireOp",EDGE,"E6.18.2"),sQuery(id+"F0.wireOp",EDGE,"E6.18.3"),sQuery(id+"F0.wireOp",EDGE,"E6.18.4"),sQuery(id+"F0.wireOp",EDGE,"E6.19.1"),sQuery(id+"F0.wireOp",EDGE,"E6.19.2"),sQuery(id+"F0.wireOp",EDGE,"E6.19.3"),sQuery(id+"F0.wireOp",EDGE,"E6.19.4"),sQuery(id+"F0.wireOp",EDGE,"E6.20.1"),sQuery(id+"F0.wireOp",EDGE,"E6.20.2"),sQuery(id+"F0.wireOp",EDGE,"E6.20.3"),sQuery(id+"F0.wireOp",EDGE,"E6.20.4"),subQ1,sQuery(id+"F0.wireOp",EDGE,"E6.21.2"),subQ0,sQuery(id+"F0.wireOp",EDGE,"E6.21.4"),sQuery(id+"F0.wireOp",EDGE,"E6.22.1"),sQuery(id+"F0.wireOp",EDGE,"E6.22.2"),sQuery(id+"F0.wireOp",EDGE,"E6.22.3"),sQuery(id+"F0.wireOp",EDGE,"E6.22.4"),sQuery(id+"F0.wireOp",EDGE,"E6.23.1"),sQuery(id+"F0.wireOp",EDGE,"E6.23.2"),sQuery(id+"F0.wireOp",EDGE,"E6.23.3"),sQuery(id+"F0.wireOp",EDGE,"E6.23.4"),sQuery(id+"F0.wireOp",EDGE,"E6.24.1"),sQuery(id+"F0.wireOp",EDGE,"E6.24.2"),sQuery(id+"F0.wireOp",EDGE,"E6.24.3"),sQuery(id+"F0.wireOp",EDGE,"E6.24.4"),sQuery(id+"F0.wireOp",EDGE,"E6.25.1"),sQuery(id+"F0.wireOp",EDGE,"E6.25.2"),sQuery(id+"F0.wireOp",EDGE,"E6.25.3"),sQuery(id+"F0.wireOp",EDGE,"E6.25.4"),sQuery(id+"F0.wireOp",EDGE,"E6.26.1"),sQuery(id+"F0.wireOp",EDGE,"E6.26.2"),sQuery(id+"F0.wireOp",EDGE,"E6.26.3"),sQuery(id+"F0.wireOp",EDGE,"E6.26.4"),sQuery(id+"F0.wireOp",EDGE,"E6.27.1"),sQuery(id+"F0.wireOp",EDGE,"E6.27.2"),sQuery(id+"F0.wireOp",EDGE,"E6.27.3"),sQuery(id+"F0.wireOp",EDGE,"E6.27.4"),sQuery(id+"F0.wireOp",EDGE,"E6.28.1"),sQuery(id+"F0.wireOp",EDGE,"E6.28.2"),sQuery(id+"F0.wireOp",EDGE,"E6.28.3"),sQuery(id+"F0.wireOp",EDGE,"E6.28.4"),sQuery(id+"F0.wireOp",EDGE,"E6.29.1"),sQuery(id+"F0.wireOp",EDGE,"E6.29.2"),sQuery(id+"F0.wireOp",EDGE,"E6.29.3"),sQuery(id+"F0.wireOp",EDGE,"E6.29.4"),sQuery(id+"F0.wireOp",EDGE,"E6.30.1"),sQuery(id+"F0.wireOp",EDGE,"E6.30.2"),sQuery(id+"F0.wireOp",EDGE,"E6.30.3"),sQuery(id+"F0.wireOp",EDGE,"E6.30.4"),sQuery(id+"F0.wireOp",EDGE,"E6.31.1"),sQuery(id+"F0.wireOp",EDGE,"E6.31.2"),sQuery(id+"F0.wireOp",EDGE,"E6.31.3"),sQuery(id+"F0.wireOp",EDGE,"E6.31.4"),sQuery(id+"F0.wireOp",EDGE,"E6.32.1"),sQuery(id+"F0.wireOp",EDGE,"E6.32.2"),sQuery(id+"F0.wireOp",EDGE,"E6.32.3"),sQuery(id+"F0.wireOp",EDGE,"E6.32.4"),sQuery(id+"F0.wireOp",EDGE,"E6.33.1"),sQuery(id+"F0.wireOp",EDGE,"E6.33.2"),sQuery(id+"F0.wireOp",EDGE,"E6.33.3"),sQuery(id+"F0.wireOp",EDGE,"E6.33.4"),sQuery(id+"F0.wireOp",EDGE,"E6.34.1"),sQuery(id+"F0.wireOp",EDGE,"E6.34.2"),sQuery(id+"F0.wireOp",EDGE,"E6.34.3"),sQuery(id+"F0.wireOp",EDGE,"E6.34.4"),sQuery(id+"F0.wireOp",EDGE,"E6.35.1"),sQuery(id+"F0.wireOp",EDGE,"E6.35.2"),sQuery(id+"F0.wireOp",EDGE,"E6.35.3"),sQuery(id+"F0.wireOp",EDGE,"E6.35.4"),sQuery(id+"F0.wireOp",EDGE,"E6.36.1"),sQuery(id+"F0.wireOp",EDGE,"E6.36.2"),sQuery(id+"F0.wireOp",EDGE,"E6.36.3"),sQuery(id+"F0.wireOp",EDGE,"E6.36.4"),sQuery(id+"F0.wireOp",EDGE,"E6.37.1"),sQuery(id+"F0.wireOp",EDGE,"E6.37.2"),sQuery(id+"F0.wireOp",EDGE,"E6.37.3"),sQuery(id+"F0.wireOp",EDGE,"E6.37.4"),sQuery(id+"F0.wireOp",EDGE,"E6.38.1"),sQuery(id+"F0.wireOp",EDGE,"E6.38.2"),sQuery(id+"F0.wireOp",EDGE,"E6.38.3"),sQuery(id+"F0.wireOp",EDGE,"E6.38.4"),sQuery(id+"F0.wireOp",EDGE,"E6.39.1"),sQuery(id+"F0.wireOp",EDGE,"E6.39.2"),sQuery(id+"F0.wireOp",EDGE,"E6.39.3"),sQuery(id+"F0.wireOp",EDGE,"E6.39.4"),sQuery(id+"F0.wireOp",EDGE,"E6.40.1"),sQuery(id+"F0.wireOp",EDGE,"E6.40.2"),sQuery(id+"F0.wireOp",EDGE,"E6.40.3"),sQuery(id+"F0.wireOp",EDGE,"E6.40.4"),sQuery(id+"F0.wireOp",EDGE,"E6.41.1"),sQuery(id+"F0.wireOp",EDGE,"E6.41.2"),sQuery(id+"F0.wireOp",EDGE,"E6.41.3"),sQuery(id+"F0.wireOp",EDGE,"E6.41.4"),sQuery(id+"F0.wireOp",EDGE,"E6.42.1"),sQuery(id+"F0.wireOp",EDGE,"E6.42.2"),sQuery(id+"F0.wireOp",EDGE,"E6.42.3"),sQuery(id+"F0.wireOp",EDGE,"E6.42.4"),sQuery(id+"F0.wireOp",EDGE,"E6.43.1"),sQuery(id+"F0.wireOp",EDGE,"E6.43.2"),sQuery(id+"F0.wireOp",EDGE,"E6.43.3"),sQuery(id+"F0.wireOp",EDGE,"E6.43.4"),sQuery(id+"F0.wireOp",EDGE,"E7"),sQuery(id+"F0.wireOp",EDGE,"E8.1.0"),sQuery(id+"F0.wireOp",EDGE,"E8.2.0"),sQuery(id+"F0.wireOp",EDGE,"E8.3.0"),sQuery(id+"F0.wireOp",EDGE,"E8.4.0"),sQuery(id+"F0.wireOp",EDGE,"E8.5.0"),sQuery(id+"F0.wireOp",EDGE,"E8.6.0"),sQuery(id+"F0.wireOp",EDGE,"E8.7.0"),sQuery(id+"F0.wireOp",EDGE,"E8.8.0"),sQuery(id+"F0.wireOp",EDGE,"E8.9.0"),sQuery(id+"F0.wireOp",EDGE,"E8.10.0"),sQuery(id+"F0.wireOp",EDGE,"E8.11.0"),sQuery(id+"F0.wireOp",EDGE,"E8.12.0"),sQuery(id+"F0.wireOp",EDGE,"E8.13.0"),sQuery(id+"F0.wireOp",EDGE,"E8.14.0"),sQuery(id+"F0.wireOp",EDGE,"E8.15.0"),sQuery(id+"F0.wireOp",EDGE,"E8.16.0"),sQuery(id+"F0.wireOp",EDGE,"E8.17.0"),sQuery(id+"F0.wireOp",EDGE,"E8.18.0"),sQuery(id+"F0.wireOp",EDGE,"E8.19.0"),sQuery(id+"F0.wireOp",EDGE,"E8.20.0"),sQuery(id+"F0.wireOp",EDGE,"E8.21.0"),sQuery(id+"F0.wireOp",EDGE,"E8.22.0"),sQuery(id+"F0.wireOp",EDGE,"E8.23.0"),sQuery(id+"F0.wireOp",EDGE,"E8.24.0"),sQuery(id+"F0.wireOp",EDGE,"E8.25.0"),sQuery(id+"F0.wireOp",EDGE,"E8.26.0"),sQuery(id+"F0.wireOp",EDGE,"E8.27.0"),sQuery(id+"F0.wireOp",EDGE,"E8.28.0"),sQuery(id+"F0.wireOp",EDGE,"E8.29.0"),sQuery(id+"F0.wireOp",EDGE,"E8.30.0"),sQuery(id+"F0.wireOp",EDGE,"E8.31.0"),sQuery(id+"F0.wireOp",EDGE,"E8.32.0"),sQuery(id+"F0.wireOp",EDGE,"E8.33.0"),sQuery(id+"F0.wireOp",EDGE,"E8.34.0"),sQuery(id+"F0.wireOp",EDGE,"E8.35.0"),sQuery(id+"F0.wireOp",EDGE,"E8.36.0"),sQuery(id+"F0.wireOp",EDGE,"E8.37.0"),sQuery(id+"F0.wireOp",EDGE,"E8.38.0"),sQuery(id+"F0.wireOp",EDGE,"E8.39.0"),sQuery(id+"F0.wireOp",EDGE,"E8.40.0"),sQuery(id+"F0.wireOp",EDGE,"E8.41.0"),sQuery(id+"F0.wireOp",EDGE,"E8.42.0"),sQuery(id+"F0.wireOp",EDGE,"E8.43.0")])],"isStart":false})]});}
            var Q22;
            {var subQ0=sQuery(id+"F0.wireOp",EDGE,"E5");var subQ1=sQuery(id+"F0.wireOp",EDGE,"E4");Q22=makeQuery(id+"F2.opFillet","BLEND_EDGE",EDGE,{"blendedFrom":[makeQuery(id+"F1.opExtrude","SWEPT_EDGE",EDGE,{"disambiguationData":[OSD([sQuery(id+"F0.wireOp",EDGE,"E3"),subQ1,subQ0])]}),makeQuery(id+"F1.opExtrude","CAP_FACE",FACE,{"disambiguationData":[OSD([sQuery(id+"F0.wireOp",EDGE,"E0"),sQuery(id+"F0.wireOp",EDGE,"E1"),sQuery(id+"F0.wireOp",EDGE,"E2"),subQ1,subQ0,sQuery(id+"F0.wireOp",EDGE,"E6.1.1"),sQuery(id+"F0.wireOp",EDGE,"E6.1.2"),sQuery(id+"F0.wireOp",EDGE,"E6.1.3"),sQuery(id+"F0.wireOp",EDGE,"E6.1.4"),sQuery(id+"F0.wireOp",EDGE,"E6.2.1"),sQuery(id+"F0.wireOp",EDGE,"E6.2.2"),sQuery(id+"F0.wireOp",EDGE,"E6.2.3"),sQuery(id+"F0.wireOp",EDGE,"E6.2.4"),sQuery(id+"F0.wireOp",EDGE,"E6.3.1"),sQuery(id+"F0.wireOp",EDGE,"E6.3.2"),sQuery(id+"F0.wireOp",EDGE,"E6.3.3"),sQuery(id+"F0.wireOp",EDGE,"E6.3.4"),sQuery(id+"F0.wireOp",EDGE,"E6.4.1"),sQuery(id+"F0.wireOp",EDGE,"E6.4.2"),sQuery(id+"F0.wireOp",EDGE,"E6.4.3"),sQuery(id+"F0.wireOp",EDGE,"E6.4.4"),sQuery(id+"F0.wireOp",EDGE,"E6.5.1"),sQuery(id+"F0.wireOp",EDGE,"E6.5.2"),sQuery(id+"F0.wireOp",EDGE,"E6.5.3"),sQuery(id+"F0.wireOp",EDGE,"E6.5.4"),sQuery(id+"F0.wireOp",EDGE,"E6.6.1"),sQuery(id+"F0.wireOp",EDGE,"E6.6.2"),sQuery(id+"F0.wireOp",EDGE,"E6.6.3"),sQuery(id+"F0.wireOp",EDGE,"E6.6.4"),sQuery(id+"F0.wireOp",EDGE,"E6.7.1"),sQuery(id+"F0.wireOp",EDGE,"E6.7.2"),sQuery(id+"F0.wireOp",EDGE,"E6.7.3"),sQuery(id+"F0.wireOp",EDGE,"E6.7.4"),sQuery(id+"F0.wireOp",EDGE,"E6.8.1"),sQuery(id+"F0.wireOp",EDGE,"E6.8.2"),sQuery(id+"F0.wireOp",EDGE,"E6.8.3"),sQuery(id+"F0.wireOp",EDGE,"E6.8.4"),sQuery(id+"F0.wireOp",EDGE,"E6.9.1"),sQuery(id+"F0.wireOp",EDGE,"E6.9.2"),sQuery(id+"F0.wireOp",EDGE,"E6.9.3"),sQuery(id+"F0.wireOp",EDGE,"E6.9.4"),sQuery(id+"F0.wireOp",EDGE,"E6.10.1"),sQuery(id+"F0.wireOp",EDGE,"E6.10.2"),sQuery(id+"F0.wireOp",EDGE,"E6.10.3"),sQuery(id+"F0.wireOp",EDGE,"E6.10.4"),sQuery(id+"F0.wireOp",EDGE,"E6.11.1"),sQuery(id+"F0.wireOp",EDGE,"E6.11.2"),sQuery(id+"F0.wireOp",EDGE,"E6.11.3"),sQuery(id+"F0.wireOp",EDGE,"E6.11.4"),sQuery(id+"F0.wireOp",EDGE,"E6.12.1"),sQuery(id+"F0.wireOp",EDGE,"E6.12.2"),sQuery(id+"F0.wireOp",EDGE,"E6.12.3"),sQuery(id+"F0.wireOp",EDGE,"E6.12.4"),sQuery(id+"F0.wireOp",EDGE,"E6.13.1"),sQuery(id+"F0.wireOp",EDGE,"E6.13.2"),sQuery(id+"F0.wireOp",EDGE,"E6.13.3"),sQuery(id+"F0.wireOp",EDGE,"E6.13.4"),sQuery(id+"F0.wireOp",EDGE,"E6.14.1"),sQuery(id+"F0.wireOp",EDGE,"E6.14.2"),sQuery(id+"F0.wireOp",EDGE,"E6.14.3"),sQuery(id+"F0.wireOp",EDGE,"E6.14.4"),sQuery(id+"F0.wireOp",EDGE,"E6.15.1"),sQuery(id+"F0.wireOp",EDGE,"E6.15.2"),sQuery(id+"F0.wireOp",EDGE,"E6.15.3"),sQuery(id+"F0.wireOp",EDGE,"E6.15.4"),sQuery(id+"F0.wireOp",EDGE,"E6.16.1"),sQuery(id+"F0.wireOp",EDGE,"E6.16.2"),sQuery(id+"F0.wireOp",EDGE,"E6.16.3"),sQuery(id+"F0.wireOp",EDGE,"E6.16.4"),sQuery(id+"F0.wireOp",EDGE,"E6.17.1"),sQuery(id+"F0.wireOp",EDGE,"E6.17.2"),sQuery(id+"F0.wireOp",EDGE,"E6.17.3"),sQuery(id+"F0.wireOp",EDGE,"E6.17.4"),sQuery(id+"F0.wireOp",EDGE,"E6.18.1"),sQuery(id+"F0.wireOp",EDGE,"E6.18.2"),sQuery(id+"F0.wireOp",EDGE,"E6.18.3"),sQuery(id+"F0.wireOp",EDGE,"E6.18.4"),sQuery(id+"F0.wireOp",EDGE,"E6.19.1"),sQuery(id+"F0.wireOp",EDGE,"E6.19.2"),sQuery(id+"F0.wireOp",EDGE,"E6.19.3"),sQuery(id+"F0.wireOp",EDGE,"E6.19.4"),sQuery(id+"F0.wireOp",EDGE,"E6.20.1"),sQuery(id+"F0.wireOp",EDGE,"E6.20.2"),sQuery(id+"F0.wireOp",EDGE,"E6.20.3"),sQuery(id+"F0.wireOp",EDGE,"E6.20.4"),sQuery(id+"F0.wireOp",EDGE,"E6.21.1"),sQuery(id+"F0.wireOp",EDGE,"E6.21.2"),sQuery(id+"F0.wireOp",EDGE,"E6.21.3"),sQuery(id+"F0.wireOp",EDGE,"E6.21.4"),sQuery(id+"F0.wireOp",EDGE,"E6.22.1"),sQuery(id+"F0.wireOp",EDGE,"E6.22.2"),sQuery(id+"F0.wireOp",EDGE,"E6.22.3"),sQuery(id+"F0.wireOp",EDGE,"E6.22.4"),sQuery(id+"F0.wireOp",EDGE,"E6.23.1"),sQuery(id+"F0.wireOp",EDGE,"E6.23.2"),sQuery(id+"F0.wireOp",EDGE,"E6.23.3"),sQuery(id+"F0.wireOp",EDGE,"E6.23.4"),sQuery(id+"F0.wireOp",EDGE,"E6.24.1"),sQuery(id+"F0.wireOp",EDGE,"E6.24.2"),sQuery(id+"F0.wireOp",EDGE,"E6.24.3"),sQuery(id+"F0.wireOp",EDGE,"E6.24.4"),sQuery(id+"F0.wireOp",EDGE,"E6.25.1"),sQuery(id+"F0.wireOp",EDGE,"E6.25.2"),sQuery(id+"F0.wireOp",EDGE,"E6.25.3"),sQuery(id+"F0.wireOp",EDGE,"E6.25.4"),sQuery(id+"F0.wireOp",EDGE,"E6.26.1"),sQuery(id+"F0.wireOp",EDGE,"E6.26.2"),sQuery(id+"F0.wireOp",EDGE,"E6.26.3"),sQuery(id+"F0.wireOp",EDGE,"E6.26.4"),sQuery(id+"F0.wireOp",EDGE,"E6.27.1"),sQuery(id+"F0.wireOp",EDGE,"E6.27.2"),sQuery(id+"F0.wireOp",EDGE,"E6.27.3"),sQuery(id+"F0.wireOp",EDGE,"E6.27.4"),sQuery(id+"F0.wireOp",EDGE,"E6.28.1"),sQuery(id+"F0.wireOp",EDGE,"E6.28.2"),sQuery(id+"F0.wireOp",EDGE,"E6.28.3"),sQuery(id+"F0.wireOp",EDGE,"E6.28.4"),sQuery(id+"F0.wireOp",EDGE,"E6.29.1"),sQuery(id+"F0.wireOp",EDGE,"E6.29.2"),sQuery(id+"F0.wireOp",EDGE,"E6.29.3"),sQuery(id+"F0.wireOp",EDGE,"E6.29.4"),sQuery(id+"F0.wireOp",EDGE,"E6.30.1"),sQuery(id+"F0.wireOp",EDGE,"E6.30.2"),sQuery(id+"F0.wireOp",EDGE,"E6.30.3"),sQuery(id+"F0.wireOp",EDGE,"E6.30.4"),sQuery(id+"F0.wireOp",EDGE,"E6.31.1"),sQuery(id+"F0.wireOp",EDGE,"E6.31.2"),sQuery(id+"F0.wireOp",EDGE,"E6.31.3"),sQuery(id+"F0.wireOp",EDGE,"E6.31.4"),sQuery(id+"F0.wireOp",EDGE,"E6.32.1"),sQuery(id+"F0.wireOp",EDGE,"E6.32.2"),sQuery(id+"F0.wireOp",EDGE,"E6.32.3"),sQuery(id+"F0.wireOp",EDGE,"E6.32.4"),sQuery(id+"F0.wireOp",EDGE,"E6.33.1"),sQuery(id+"F0.wireOp",EDGE,"E6.33.2"),sQuery(id+"F0.wireOp",EDGE,"E6.33.3"),sQuery(id+"F0.wireOp",EDGE,"E6.33.4"),sQuery(id+"F0.wireOp",EDGE,"E6.34.1"),sQuery(id+"F0.wireOp",EDGE,"E6.34.2"),sQuery(id+"F0.wireOp",EDGE,"E6.34.3"),sQuery(id+"F0.wireOp",EDGE,"E6.34.4"),sQuery(id+"F0.wireOp",EDGE,"E6.35.1"),sQuery(id+"F0.wireOp",EDGE,"E6.35.2"),sQuery(id+"F0.wireOp",EDGE,"E6.35.3"),sQuery(id+"F0.wireOp",EDGE,"E6.35.4"),sQuery(id+"F0.wireOp",EDGE,"E6.36.1"),sQuery(id+"F0.wireOp",EDGE,"E6.36.2"),sQuery(id+"F0.wireOp",EDGE,"E6.36.3"),sQuery(id+"F0.wireOp",EDGE,"E6.36.4"),sQuery(id+"F0.wireOp",EDGE,"E6.37.1"),sQuery(id+"F0.wireOp",EDGE,"E6.37.2"),sQuery(id+"F0.wireOp",EDGE,"E6.37.3"),sQuery(id+"F0.wireOp",EDGE,"E6.37.4"),sQuery(id+"F0.wireOp",EDGE,"E6.38.1"),sQuery(id+"F0.wireOp",EDGE,"E6.38.2"),sQuery(id+"F0.wireOp",EDGE,"E6.38.3"),sQuery(id+"F0.wireOp",EDGE,"E6.38.4"),sQuery(id+"F0.wireOp",EDGE,"E6.39.1"),sQuery(id+"F0.wireOp",EDGE,"E6.39.2"),sQuery(id+"F0.wireOp",EDGE,"E6.39.3"),sQuery(id+"F0.wireOp",EDGE,"E6.39.4"),sQuery(id+"F0.wireOp",EDGE,"E6.40.1"),sQuery(id+"F0.wireOp",EDGE,"E6.40.2"),sQuery(id+"F0.wireOp",EDGE,"E6.40.3"),sQuery(id+"F0.wireOp",EDGE,"E6.40.4"),sQuery(id+"F0.wireOp",EDGE,"E6.41.1"),sQuery(id+"F0.wireOp",EDGE,"E6.41.2"),sQuery(id+"F0.wireOp",EDGE,"E6.41.3"),sQuery(id+"F0.wireOp",EDGE,"E6.41.4"),sQuery(id+"F0.wireOp",EDGE,"E6.42.1"),sQuery(id+"F0.wireOp",EDGE,"E6.42.2"),sQuery(id+"F0.wireOp",EDGE,"E6.42.3"),sQuery(id+"F0.wireOp",EDGE,"E6.42.4"),sQuery(id+"F0.wireOp",EDGE,"E6.43.1"),sQuery(id+"F0.wireOp",EDGE,"E6.43.2"),sQuery(id+"F0.wireOp",EDGE,"E6.43.3"),sQuery(id+"F0.wireOp",EDGE,"E6.43.4"),sQuery(id+"F0.wireOp",EDGE,"E7"),sQuery(id+"F0.wireOp",EDGE,"E8.1.0"),sQuery(id+"F0.wireOp",EDGE,"E8.2.0"),sQuery(id+"F0.wireOp",EDGE,"E8.3.0"),sQuery(id+"F0.wireOp",EDGE,"E8.4.0"),sQuery(id+"F0.wireOp",EDGE,"E8.5.0"),sQuery(id+"F0.wireOp",EDGE,"E8.6.0"),sQuery(id+"F0.wireOp",EDGE,"E8.7.0"),sQuery(id+"F0.wireOp",EDGE,"E8.8.0"),sQuery(id+"F0.wireOp",EDGE,"E8.9.0"),sQuery(id+"F0.wireOp",EDGE,"E8.10.0"),sQuery(id+"F0.wireOp",EDGE,"E8.11.0"),sQuery(id+"F0.wireOp",EDGE,"E8.12.0"),sQuery(id+"F0.wireOp",EDGE,"E8.13.0"),sQuery(id+"F0.wireOp",EDGE,"E8.14.0"),sQuery(id+"F0.wireOp",EDGE,"E8.15.0"),sQuery(id+"F0.wireOp",EDGE,"E8.16.0"),sQuery(id+"F0.wireOp",EDGE,"E8.17.0"),sQuery(id+"F0.wireOp",EDGE,"E8.18.0"),sQuery(id+"F0.wireOp",EDGE,"E8.19.0"),sQuery(id+"F0.wireOp",EDGE,"E8.20.0"),sQuery(id+"F0.wireOp",EDGE,"E8.21.0"),sQuery(id+"F0.wireOp",EDGE,"E8.22.0"),sQuery(id+"F0.wireOp",EDGE,"E8.23.0"),sQuery(id+"F0.wireOp",EDGE,"E8.24.0"),sQuery(id+"F0.wireOp",EDGE,"E8.25.0"),sQuery(id+"F0.wireOp",EDGE,"E8.26.0"),sQuery(id+"F0.wireOp",EDGE,"E8.27.0"),sQuery(id+"F0.wireOp",EDGE,"E8.28.0"),sQuery(id+"F0.wireOp",EDGE,"E8.29.0"),sQuery(id+"F0.wireOp",EDGE,"E8.30.0"),sQuery(id+"F0.wireOp",EDGE,"E8.31.0"),sQuery(id+"F0.wireOp",EDGE,"E8.32.0"),sQuery(id+"F0.wireOp",EDGE,"E8.33.0"),sQuery(id+"F0.wireOp",EDGE,"E8.34.0"),sQuery(id+"F0.wireOp",EDGE,"E8.35.0"),sQuery(id+"F0.wireOp",EDGE,"E8.36.0"),sQuery(id+"F0.wireOp",EDGE,"E8.37.0"),sQuery(id+"F0.wireOp",EDGE,"E8.38.0"),sQuery(id+"F0.wireOp",EDGE,"E8.39.0"),sQuery(id+"F0.wireOp",EDGE,"E8.40.0"),sQuery(id+"F0.wireOp",EDGE,"E8.41.0"),sQuery(id+"F0.wireOp",EDGE,"E8.42.0"),sQuery(id+"F0.wireOp",EDGE,"E8.43.0")])],"isStart":true})],"blendedInto":[makeQuery(id+"F1.opExtrude","CAP_FACE",FACE,{"disambiguationData":[OSD([sQuery(id+"F0.wireOp",EDGE,"E0"),sQuery(id+"F0.wireOp",EDGE,"E1"),sQuery(id+"F0.wireOp",EDGE,"E2"),subQ1,subQ0,sQuery(id+"F0.wireOp",EDGE,"E6.1.1"),sQuery(id+"F0.wireOp",EDGE,"E6.1.2"),sQuery(id+"F0.wireOp",EDGE,"E6.1.3"),sQuery(id+"F0.wireOp",EDGE,"E6.1.4"),sQuery(id+"F0.wireOp",EDGE,"E6.2.1"),sQuery(id+"F0.wireOp",EDGE,"E6.2.2"),sQuery(id+"F0.wireOp",EDGE,"E6.2.3"),sQuery(id+"F0.wireOp",EDGE,"E6.2.4"),sQuery(id+"F0.wireOp",EDGE,"E6.3.1"),sQuery(id+"F0.wireOp",EDGE,"E6.3.2"),sQuery(id+"F0.wireOp",EDGE,"E6.3.3"),sQuery(id+"F0.wireOp",EDGE,"E6.3.4"),sQuery(id+"F0.wireOp",EDGE,"E6.4.1"),sQuery(id+"F0.wireOp",EDGE,"E6.4.2"),sQuery(id+"F0.wireOp",EDGE,"E6.4.3"),sQuery(id+"F0.wireOp",EDGE,"E6.4.4"),sQuery(id+"F0.wireOp",EDGE,"E6.5.1"),sQuery(id+"F0.wireOp",EDGE,"E6.5.2"),sQuery(id+"F0.wireOp",EDGE,"E6.5.3"),sQuery(id+"F0.wireOp",EDGE,"E6.5.4"),sQuery(id+"F0.wireOp",EDGE,"E6.6.1"),sQuery(id+"F0.wireOp",EDGE,"E6.6.2"),sQuery(id+"F0.wireOp",EDGE,"E6.6.3"),sQuery(id+"F0.wireOp",EDGE,"E6.6.4"),sQuery(id+"F0.wireOp",EDGE,"E6.7.1"),sQuery(id+"F0.wireOp",EDGE,"E6.7.2"),sQuery(id+"F0.wireOp",EDGE,"E6.7.3"),sQuery(id+"F0.wireOp",EDGE,"E6.7.4"),sQuery(id+"F0.wireOp",EDGE,"E6.8.1"),sQuery(id+"F0.wireOp",EDGE,"E6.8.2"),sQuery(id+"F0.wireOp",EDGE,"E6.8.3"),sQuery(id+"F0.wireOp",EDGE,"E6.8.4"),sQuery(id+"F0.wireOp",EDGE,"E6.9.1"),sQuery(id+"F0.wireOp",EDGE,"E6.9.2"),sQuery(id+"F0.wireOp",EDGE,"E6.9.3"),sQuery(id+"F0.wireOp",EDGE,"E6.9.4"),sQuery(id+"F0.wireOp",EDGE,"E6.10.1"),sQuery(id+"F0.wireOp",EDGE,"E6.10.2"),sQuery(id+"F0.wireOp",EDGE,"E6.10.3"),sQuery(id+"F0.wireOp",EDGE,"E6.10.4"),sQuery(id+"F0.wireOp",EDGE,"E6.11.1"),sQuery(id+"F0.wireOp",EDGE,"E6.11.2"),sQuery(id+"F0.wireOp",EDGE,"E6.11.3"),sQuery(id+"F0.wireOp",EDGE,"E6.11.4"),sQuery(id+"F0.wireOp",EDGE,"E6.12.1"),sQuery(id+"F0.wireOp",EDGE,"E6.12.2"),sQuery(id+"F0.wireOp",EDGE,"E6.12.3"),sQuery(id+"F0.wireOp",EDGE,"E6.12.4"),sQuery(id+"F0.wireOp",EDGE,"E6.13.1"),sQuery(id+"F0.wireOp",EDGE,"E6.13.2"),sQuery(id+"F0.wireOp",EDGE,"E6.13.3"),sQuery(id+"F0.wireOp",EDGE,"E6.13.4"),sQuery(id+"F0.wireOp",EDGE,"E6.14.1"),sQuery(id+"F0.wireOp",EDGE,"E6.14.2"),sQuery(id+"F0.wireOp",EDGE,"E6.14.3"),sQuery(id+"F0.wireOp",EDGE,"E6.14.4"),sQuery(id+"F0.wireOp",EDGE,"E6.15.1"),sQuery(id+"F0.wireOp",EDGE,"E6.15.2"),sQuery(id+"F0.wireOp",EDGE,"E6.15.3"),sQuery(id+"F0.wireOp",EDGE,"E6.15.4"),sQuery(id+"F0.wireOp",EDGE,"E6.16.1"),sQuery(id+"F0.wireOp",EDGE,"E6.16.2"),sQuery(id+"F0.wireOp",EDGE,"E6.16.3"),sQuery(id+"F0.wireOp",EDGE,"E6.16.4"),sQuery(id+"F0.wireOp",EDGE,"E6.17.1"),sQuery(id+"F0.wireOp",EDGE,"E6.17.2"),sQuery(id+"F0.wireOp",EDGE,"E6.17.3"),sQuery(id+"F0.wireOp",EDGE,"E6.17.4"),sQuery(id+"F0.wireOp",EDGE,"E6.18.1"),sQuery(id+"F0.wireOp",EDGE,"E6.18.2"),sQuery(id+"F0.wireOp",EDGE,"E6.18.3"),sQuery(id+"F0.wireOp",EDGE,"E6.18.4"),sQuery(id+"F0.wireOp",EDGE,"E6.19.1"),sQuery(id+"F0.wireOp",EDGE,"E6.19.2"),sQuery(id+"F0.wireOp",EDGE,"E6.19.3"),sQuery(id+"F0.wireOp",EDGE,"E6.19.4"),sQuery(id+"F0.wireOp",EDGE,"E6.20.1"),sQuery(id+"F0.wireOp",EDGE,"E6.20.2"),sQuery(id+"F0.wireOp",EDGE,"E6.20.3"),sQuery(id+"F0.wireOp",EDGE,"E6.20.4"),sQuery(id+"F0.wireOp",EDGE,"E6.21.1"),sQuery(id+"F0.wireOp",EDGE,"E6.21.2"),sQuery(id+"F0.wireOp",EDGE,"E6.21.3"),sQuery(id+"F0.wireOp",EDGE,"E6.21.4"),sQuery(id+"F0.wireOp",EDGE,"E6.22.1"),sQuery(id+"F0.wireOp",EDGE,"E6.22.2"),sQuery(id+"F0.wireOp",EDGE,"E6.22.3"),sQuery(id+"F0.wireOp",EDGE,"E6.22.4"),sQuery(id+"F0.wireOp",EDGE,"E6.23.1"),sQuery(id+"F0.wireOp",EDGE,"E6.23.2"),sQuery(id+"F0.wireOp",EDGE,"E6.23.3"),sQuery(id+"F0.wireOp",EDGE,"E6.23.4"),sQuery(id+"F0.wireOp",EDGE,"E6.24.1"),sQuery(id+"F0.wireOp",EDGE,"E6.24.2"),sQuery(id+"F0.wireOp",EDGE,"E6.24.3"),sQuery(id+"F0.wireOp",EDGE,"E6.24.4"),sQuery(id+"F0.wireOp",EDGE,"E6.25.1"),sQuery(id+"F0.wireOp",EDGE,"E6.25.2"),sQuery(id+"F0.wireOp",EDGE,"E6.25.3"),sQuery(id+"F0.wireOp",EDGE,"E6.25.4"),sQuery(id+"F0.wireOp",EDGE,"E6.26.1"),sQuery(id+"F0.wireOp",EDGE,"E6.26.2"),sQuery(id+"F0.wireOp",EDGE,"E6.26.3"),sQuery(id+"F0.wireOp",EDGE,"E6.26.4"),sQuery(id+"F0.wireOp",EDGE,"E6.27.1"),sQuery(id+"F0.wireOp",EDGE,"E6.27.2"),sQuery(id+"F0.wireOp",EDGE,"E6.27.3"),sQuery(id+"F0.wireOp",EDGE,"E6.27.4"),sQuery(id+"F0.wireOp",EDGE,"E6.28.1"),sQuery(id+"F0.wireOp",EDGE,"E6.28.2"),sQuery(id+"F0.wireOp",EDGE,"E6.28.3"),sQuery(id+"F0.wireOp",EDGE,"E6.28.4"),sQuery(id+"F0.wireOp",EDGE,"E6.29.1"),sQuery(id+"F0.wireOp",EDGE,"E6.29.2"),sQuery(id+"F0.wireOp",EDGE,"E6.29.3"),sQuery(id+"F0.wireOp",EDGE,"E6.29.4"),sQuery(id+"F0.wireOp",EDGE,"E6.30.1"),sQuery(id+"F0.wireOp",EDGE,"E6.30.2"),sQuery(id+"F0.wireOp",EDGE,"E6.30.3"),sQuery(id+"F0.wireOp",EDGE,"E6.30.4"),sQuery(id+"F0.wireOp",EDGE,"E6.31.1"),sQuery(id+"F0.wireOp",EDGE,"E6.31.2"),sQuery(id+"F0.wireOp",EDGE,"E6.31.3"),sQuery(id+"F0.wireOp",EDGE,"E6.31.4"),sQuery(id+"F0.wireOp",EDGE,"E6.32.1"),sQuery(id+"F0.wireOp",EDGE,"E6.32.2"),sQuery(id+"F0.wireOp",EDGE,"E6.32.3"),sQuery(id+"F0.wireOp",EDGE,"E6.32.4"),sQuery(id+"F0.wireOp",EDGE,"E6.33.1"),sQuery(id+"F0.wireOp",EDGE,"E6.33.2"),sQuery(id+"F0.wireOp",EDGE,"E6.33.3"),sQuery(id+"F0.wireOp",EDGE,"E6.33.4"),sQuery(id+"F0.wireOp",EDGE,"E6.34.1"),sQuery(id+"F0.wireOp",EDGE,"E6.34.2"),sQuery(id+"F0.wireOp",EDGE,"E6.34.3"),sQuery(id+"F0.wireOp",EDGE,"E6.34.4"),sQuery(id+"F0.wireOp",EDGE,"E6.35.1"),sQuery(id+"F0.wireOp",EDGE,"E6.35.2"),sQuery(id+"F0.wireOp",EDGE,"E6.35.3"),sQuery(id+"F0.wireOp",EDGE,"E6.35.4"),sQuery(id+"F0.wireOp",EDGE,"E6.36.1"),sQuery(id+"F0.wireOp",EDGE,"E6.36.2"),sQuery(id+"F0.wireOp",EDGE,"E6.36.3"),sQuery(id+"F0.wireOp",EDGE,"E6.36.4"),sQuery(id+"F0.wireOp",EDGE,"E6.37.1"),sQuery(id+"F0.wireOp",EDGE,"E6.37.2"),sQuery(id+"F0.wireOp",EDGE,"E6.37.3"),sQuery(id+"F0.wireOp",EDGE,"E6.37.4"),sQuery(id+"F0.wireOp",EDGE,"E6.38.1"),sQuery(id+"F0.wireOp",EDGE,"E6.38.2"),sQuery(id+"F0.wireOp",EDGE,"E6.38.3"),sQuery(id+"F0.wireOp",EDGE,"E6.38.4"),sQuery(id+"F0.wireOp",EDGE,"E6.39.1"),sQuery(id+"F0.wireOp",EDGE,"E6.39.2"),sQuery(id+"F0.wireOp",EDGE,"E6.39.3"),sQuery(id+"F0.wireOp",EDGE,"E6.39.4"),sQuery(id+"F0.wireOp",EDGE,"E6.40.1"),sQuery(id+"F0.wireOp",EDGE,"E6.40.2"),sQuery(id+"F0.wireOp",EDGE,"E6.40.3"),sQuery(id+"F0.wireOp",EDGE,"E6.40.4"),sQuery(id+"F0.wireOp",EDGE,"E6.41.1"),sQuery(id+"F0.wireOp",EDGE,"E6.41.2"),sQuery(id+"F0.wireOp",EDGE,"E6.41.3"),sQuery(id+"F0.wireOp",EDGE,"E6.41.4"),sQuery(id+"F0.wireOp",EDGE,"E6.42.1"),sQuery(id+"F0.wireOp",EDGE,"E6.42.2"),sQuery(id+"F0.wireOp",EDGE,"E6.42.3"),sQuery(id+"F0.wireOp",EDGE,"E6.42.4"),sQuery(id+"F0.wireOp",EDGE,"E6.43.1"),sQuery(id+"F0.wireOp",EDGE,"E6.43.2"),sQuery(id+"F0.wireOp",EDGE,"E6.43.3"),sQuery(id+"F0.wireOp",EDGE,"E6.43.4"),sQuery(id+"F0.wireOp",EDGE,"E7"),sQuery(id+"F0.wireOp",EDGE,"E8.1.0"),sQuery(id+"F0.wireOp",EDGE,"E8.2.0"),sQuery(id+"F0.wireOp",EDGE,"E8.3.0"),sQuery(id+"F0.wireOp",EDGE,"E8.4.0"),sQuery(id+"F0.wireOp",EDGE,"E8.5.0"),sQuery(id+"F0.wireOp",EDGE,"E8.6.0"),sQuery(id+"F0.wireOp",EDGE,"E8.7.0"),sQuery(id+"F0.wireOp",EDGE,"E8.8.0"),sQuery(id+"F0.wireOp",EDGE,"E8.9.0"),sQuery(id+"F0.wireOp",EDGE,"E8.10.0"),sQuery(id+"F0.wireOp",EDGE,"E8.11.0"),sQuery(id+"F0.wireOp",EDGE,"E8.12.0"),sQuery(id+"F0.wireOp",EDGE,"E8.13.0"),sQuery(id+"F0.wireOp",EDGE,"E8.14.0"),sQuery(id+"F0.wireOp",EDGE,"E8.15.0"),sQuery(id+"F0.wireOp",EDGE,"E8.16.0"),sQuery(id+"F0.wireOp",EDGE,"E8.17.0"),sQuery(id+"F0.wireOp",EDGE,"E8.18.0"),sQuery(id+"F0.wireOp",EDGE,"E8.19.0"),sQuery(id+"F0.wireOp",EDGE,"E8.20.0"),sQuery(id+"F0.wireOp",EDGE,"E8.21.0"),sQuery(id+"F0.wireOp",EDGE,"E8.22.0"),sQuery(id+"F0.wireOp",EDGE,"E8.23.0"),sQuery(id+"F0.wireOp",EDGE,"E8.24.0"),sQuery(id+"F0.wireOp",EDGE,"E8.25.0"),sQuery(id+"F0.wireOp",EDGE,"E8.26.0"),sQuery(id+"F0.wireOp",EDGE,"E8.27.0"),sQuery(id+"F0.wireOp",EDGE,"E8.28.0"),sQuery(id+"F0.wireOp",EDGE,"E8.29.0"),sQuery(id+"F0.wireOp",EDGE,"E8.30.0"),sQuery(id+"F0.wireOp",EDGE,"E8.31.0"),sQuery(id+"F0.wireOp",EDGE,"E8.32.0"),sQuery(id+"F0.wireOp",EDGE,"E8.33.0"),sQuery(id+"F0.wireOp",EDGE,"E8.34.0"),sQuery(id+"F0.wireOp",EDGE,"E8.35.0"),sQuery(id+"F0.wireOp",EDGE,"E8.36.0"),sQuery(id+"F0.wireOp",EDGE,"E8.37.0"),sQuery(id+"F0.wireOp",EDGE,"E8.38.0"),sQuery(id+"F0.wireOp",EDGE,"E8.39.0"),sQuery(id+"F0.wireOp",EDGE,"E8.40.0"),sQuery(id+"F0.wireOp",EDGE,"E8.41.0"),sQuery(id+"F0.wireOp",EDGE,"E8.42.0"),sQuery(id+"F0.wireOp",EDGE,"E8.43.0")])],"isStart":true})]});}
            var Q23;
            {var subQ0=sQuery(id+"F0.wireOp",EDGE,"E6.2.3");var subQ1=sQuery(id+"F0.wireOp",EDGE,"E6.2.1");Q23=makeQuery(id+"F2.opFillet","BLEND_EDGE",EDGE,{"blendedFrom":[makeQuery(id+"F1.opExtrude","SWEPT_EDGE",EDGE,{"disambiguationData":[OSD([sQuery(id+"F0.wireOp",EDGE,"E6.2.0"),subQ1,subQ0])]}),makeQuery(id+"F1.opExtrude","CAP_FACE",FACE,{"disambiguationData":[OSD([sQuery(id+"F0.wireOp",EDGE,"E0"),sQuery(id+"F0.wireOp",EDGE,"E1"),sQuery(id+"F0.wireOp",EDGE,"E2"),sQuery(id+"F0.wireOp",EDGE,"E4"),sQuery(id+"F0.wireOp",EDGE,"E5"),sQuery(id+"F0.wireOp",EDGE,"E6.1.1"),sQuery(id+"F0.wireOp",EDGE,"E6.1.2"),sQuery(id+"F0.wireOp",EDGE,"E6.1.3"),sQuery(id+"F0.wireOp",EDGE,"E6.1.4"),subQ1,sQuery(id+"F0.wireOp",EDGE,"E6.2.2"),subQ0,sQuery(id+"F0.wireOp",EDGE,"E6.2.4"),sQuery(id+"F0.wireOp",EDGE,"E6.3.1"),sQuery(id+"F0.wireOp",EDGE,"E6.3.2"),sQuery(id+"F0.wireOp",EDGE,"E6.3.3"),sQuery(id+"F0.wireOp",EDGE,"E6.3.4"),sQuery(id+"F0.wireOp",EDGE,"E6.4.1"),sQuery(id+"F0.wireOp",EDGE,"E6.4.2"),sQuery(id+"F0.wireOp",EDGE,"E6.4.3"),sQuery(id+"F0.wireOp",EDGE,"E6.4.4"),sQuery(id+"F0.wireOp",EDGE,"E6.5.1"),sQuery(id+"F0.wireOp",EDGE,"E6.5.2"),sQuery(id+"F0.wireOp",EDGE,"E6.5.3"),sQuery(id+"F0.wireOp",EDGE,"E6.5.4"),sQuery(id+"F0.wireOp",EDGE,"E6.6.1"),sQuery(id+"F0.wireOp",EDGE,"E6.6.2"),sQuery(id+"F0.wireOp",EDGE,"E6.6.3"),sQuery(id+"F0.wireOp",EDGE,"E6.6.4"),sQuery(id+"F0.wireOp",EDGE,"E6.7.1"),sQuery(id+"F0.wireOp",EDGE,"E6.7.2"),sQuery(id+"F0.wireOp",EDGE,"E6.7.3"),sQuery(id+"F0.wireOp",EDGE,"E6.7.4"),sQuery(id+"F0.wireOp",EDGE,"E6.8.1"),sQuery(id+"F0.wireOp",EDGE,"E6.8.2"),sQuery(id+"F0.wireOp",EDGE,"E6.8.3"),sQuery(id+"F0.wireOp",EDGE,"E6.8.4"),sQuery(id+"F0.wireOp",EDGE,"E6.9.1"),sQuery(id+"F0.wireOp",EDGE,"E6.9.2"),sQuery(id+"F0.wireOp",EDGE,"E6.9.3"),sQuery(id+"F0.wireOp",EDGE,"E6.9.4"),sQuery(id+"F0.wireOp",EDGE,"E6.10.1"),sQuery(id+"F0.wireOp",EDGE,"E6.10.2"),sQuery(id+"F0.wireOp",EDGE,"E6.10.3"),sQuery(id+"F0.wireOp",EDGE,"E6.10.4"),sQuery(id+"F0.wireOp",EDGE,"E6.11.1"),sQuery(id+"F0.wireOp",EDGE,"E6.11.2"),sQuery(id+"F0.wireOp",EDGE,"E6.11.3"),sQuery(id+"F0.wireOp",EDGE,"E6.11.4"),sQuery(id+"F0.wireOp",EDGE,"E6.12.1"),sQuery(id+"F0.wireOp",EDGE,"E6.12.2"),sQuery(id+"F0.wireOp",EDGE,"E6.12.3"),sQuery(id+"F0.wireOp",EDGE,"E6.12.4"),sQuery(id+"F0.wireOp",EDGE,"E6.13.1"),sQuery(id+"F0.wireOp",EDGE,"E6.13.2"),sQuery(id+"F0.wireOp",EDGE,"E6.13.3"),sQuery(id+"F0.wireOp",EDGE,"E6.13.4"),sQuery(id+"F0.wireOp",EDGE,"E6.14.1"),sQuery(id+"F0.wireOp",EDGE,"E6.14.2"),sQuery(id+"F0.wireOp",EDGE,"E6.14.3"),sQuery(id+"F0.wireOp",EDGE,"E6.14.4"),sQuery(id+"F0.wireOp",EDGE,"E6.15.1"),sQuery(id+"F0.wireOp",EDGE,"E6.15.2"),sQuery(id+"F0.wireOp",EDGE,"E6.15.3"),sQuery(id+"F0.wireOp",EDGE,"E6.15.4"),sQuery(id+"F0.wireOp",EDGE,"E6.16.1"),sQuery(id+"F0.wireOp",EDGE,"E6.16.2"),sQuery(id+"F0.wireOp",EDGE,"E6.16.3"),sQuery(id+"F0.wireOp",EDGE,"E6.16.4"),sQuery(id+"F0.wireOp",EDGE,"E6.17.1"),sQuery(id+"F0.wireOp",EDGE,"E6.17.2"),sQuery(id+"F0.wireOp",EDGE,"E6.17.3"),sQuery(id+"F0.wireOp",EDGE,"E6.17.4"),sQuery(id+"F0.wireOp",EDGE,"E6.18.1"),sQuery(id+"F0.wireOp",EDGE,"E6.18.2"),sQuery(id+"F0.wireOp",EDGE,"E6.18.3"),sQuery(id+"F0.wireOp",EDGE,"E6.18.4"),sQuery(id+"F0.wireOp",EDGE,"E6.19.1"),sQuery(id+"F0.wireOp",EDGE,"E6.19.2"),sQuery(id+"F0.wireOp",EDGE,"E6.19.3"),sQuery(id+"F0.wireOp",EDGE,"E6.19.4"),sQuery(id+"F0.wireOp",EDGE,"E6.20.1"),sQuery(id+"F0.wireOp",EDGE,"E6.20.2"),sQuery(id+"F0.wireOp",EDGE,"E6.20.3"),sQuery(id+"F0.wireOp",EDGE,"E6.20.4"),sQuery(id+"F0.wireOp",EDGE,"E6.21.1"),sQuery(id+"F0.wireOp",EDGE,"E6.21.2"),sQuery(id+"F0.wireOp",EDGE,"E6.21.3"),sQuery(id+"F0.wireOp",EDGE,"E6.21.4"),sQuery(id+"F0.wireOp",EDGE,"E6.22.1"),sQuery(id+"F0.wireOp",EDGE,"E6.22.2"),sQuery(id+"F0.wireOp",EDGE,"E6.22.3"),sQuery(id+"F0.wireOp",EDGE,"E6.22.4"),sQuery(id+"F0.wireOp",EDGE,"E6.23.1"),sQuery(id+"F0.wireOp",EDGE,"E6.23.2"),sQuery(id+"F0.wireOp",EDGE,"E6.23.3"),sQuery(id+"F0.wireOp",EDGE,"E6.23.4"),sQuery(id+"F0.wireOp",EDGE,"E6.24.1"),sQuery(id+"F0.wireOp",EDGE,"E6.24.2"),sQuery(id+"F0.wireOp",EDGE,"E6.24.3"),sQuery(id+"F0.wireOp",EDGE,"E6.24.4"),sQuery(id+"F0.wireOp",EDGE,"E6.25.1"),sQuery(id+"F0.wireOp",EDGE,"E6.25.2"),sQuery(id+"F0.wireOp",EDGE,"E6.25.3"),sQuery(id+"F0.wireOp",EDGE,"E6.25.4"),sQuery(id+"F0.wireOp",EDGE,"E6.26.1"),sQuery(id+"F0.wireOp",EDGE,"E6.26.2"),sQuery(id+"F0.wireOp",EDGE,"E6.26.3"),sQuery(id+"F0.wireOp",EDGE,"E6.26.4"),sQuery(id+"F0.wireOp",EDGE,"E6.27.1"),sQuery(id+"F0.wireOp",EDGE,"E6.27.2"),sQuery(id+"F0.wireOp",EDGE,"E6.27.3"),sQuery(id+"F0.wireOp",EDGE,"E6.27.4"),sQuery(id+"F0.wireOp",EDGE,"E6.28.1"),sQuery(id+"F0.wireOp",EDGE,"E6.28.2"),sQuery(id+"F0.wireOp",EDGE,"E6.28.3"),sQuery(id+"F0.wireOp",EDGE,"E6.28.4"),sQuery(id+"F0.wireOp",EDGE,"E6.29.1"),sQuery(id+"F0.wireOp",EDGE,"E6.29.2"),sQuery(id+"F0.wireOp",EDGE,"E6.29.3"),sQuery(id+"F0.wireOp",EDGE,"E6.29.4"),sQuery(id+"F0.wireOp",EDGE,"E6.30.1"),sQuery(id+"F0.wireOp",EDGE,"E6.30.2"),sQuery(id+"F0.wireOp",EDGE,"E6.30.3"),sQuery(id+"F0.wireOp",EDGE,"E6.30.4"),sQuery(id+"F0.wireOp",EDGE,"E6.31.1"),sQuery(id+"F0.wireOp",EDGE,"E6.31.2"),sQuery(id+"F0.wireOp",EDGE,"E6.31.3"),sQuery(id+"F0.wireOp",EDGE,"E6.31.4"),sQuery(id+"F0.wireOp",EDGE,"E6.32.1"),sQuery(id+"F0.wireOp",EDGE,"E6.32.2"),sQuery(id+"F0.wireOp",EDGE,"E6.32.3"),sQuery(id+"F0.wireOp",EDGE,"E6.32.4"),sQuery(id+"F0.wireOp",EDGE,"E6.33.1"),sQuery(id+"F0.wireOp",EDGE,"E6.33.2"),sQuery(id+"F0.wireOp",EDGE,"E6.33.3"),sQuery(id+"F0.wireOp",EDGE,"E6.33.4"),sQuery(id+"F0.wireOp",EDGE,"E6.34.1"),sQuery(id+"F0.wireOp",EDGE,"E6.34.2"),sQuery(id+"F0.wireOp",EDGE,"E6.34.3"),sQuery(id+"F0.wireOp",EDGE,"E6.34.4"),sQuery(id+"F0.wireOp",EDGE,"E6.35.1"),sQuery(id+"F0.wireOp",EDGE,"E6.35.2"),sQuery(id+"F0.wireOp",EDGE,"E6.35.3"),sQuery(id+"F0.wireOp",EDGE,"E6.35.4"),sQuery(id+"F0.wireOp",EDGE,"E6.36.1"),sQuery(id+"F0.wireOp",EDGE,"E6.36.2"),sQuery(id+"F0.wireOp",EDGE,"E6.36.3"),sQuery(id+"F0.wireOp",EDGE,"E6.36.4"),sQuery(id+"F0.wireOp",EDGE,"E6.37.1"),sQuery(id+"F0.wireOp",EDGE,"E6.37.2"),sQuery(id+"F0.wireOp",EDGE,"E6.37.3"),sQuery(id+"F0.wireOp",EDGE,"E6.37.4"),sQuery(id+"F0.wireOp",EDGE,"E6.38.1"),sQuery(id+"F0.wireOp",EDGE,"E6.38.2"),sQuery(id+"F0.wireOp",EDGE,"E6.38.3"),sQuery(id+"F0.wireOp",EDGE,"E6.38.4"),sQuery(id+"F0.wireOp",EDGE,"E6.39.1"),sQuery(id+"F0.wireOp",EDGE,"E6.39.2"),sQuery(id+"F0.wireOp",EDGE,"E6.39.3"),sQuery(id+"F0.wireOp",EDGE,"E6.39.4"),sQuery(id+"F0.wireOp",EDGE,"E6.40.1"),sQuery(id+"F0.wireOp",EDGE,"E6.40.2"),sQuery(id+"F0.wireOp",EDGE,"E6.40.3"),sQuery(id+"F0.wireOp",EDGE,"E6.40.4"),sQuery(id+"F0.wireOp",EDGE,"E6.41.1"),sQuery(id+"F0.wireOp",EDGE,"E6.41.2"),sQuery(id+"F0.wireOp",EDGE,"E6.41.3"),sQuery(id+"F0.wireOp",EDGE,"E6.41.4"),sQuery(id+"F0.wireOp",EDGE,"E6.42.1"),sQuery(id+"F0.wireOp",EDGE,"E6.42.2"),sQuery(id+"F0.wireOp",EDGE,"E6.42.3"),sQuery(id+"F0.wireOp",EDGE,"E6.42.4"),sQuery(id+"F0.wireOp",EDGE,"E6.43.1"),sQuery(id+"F0.wireOp",EDGE,"E6.43.2"),sQuery(id+"F0.wireOp",EDGE,"E6.43.3"),sQuery(id+"F0.wireOp",EDGE,"E6.43.4"),sQuery(id+"F0.wireOp",EDGE,"E7"),sQuery(id+"F0.wireOp",EDGE,"E8.1.0"),sQuery(id+"F0.wireOp",EDGE,"E8.2.0"),sQuery(id+"F0.wireOp",EDGE,"E8.3.0"),sQuery(id+"F0.wireOp",EDGE,"E8.4.0"),sQuery(id+"F0.wireOp",EDGE,"E8.5.0"),sQuery(id+"F0.wireOp",EDGE,"E8.6.0"),sQuery(id+"F0.wireOp",EDGE,"E8.7.0"),sQuery(id+"F0.wireOp",EDGE,"E8.8.0"),sQuery(id+"F0.wireOp",EDGE,"E8.9.0"),sQuery(id+"F0.wireOp",EDGE,"E8.10.0"),sQuery(id+"F0.wireOp",EDGE,"E8.11.0"),sQuery(id+"F0.wireOp",EDGE,"E8.12.0"),sQuery(id+"F0.wireOp",EDGE,"E8.13.0"),sQuery(id+"F0.wireOp",EDGE,"E8.14.0"),sQuery(id+"F0.wireOp",EDGE,"E8.15.0"),sQuery(id+"F0.wireOp",EDGE,"E8.16.0"),sQuery(id+"F0.wireOp",EDGE,"E8.17.0"),sQuery(id+"F0.wireOp",EDGE,"E8.18.0"),sQuery(id+"F0.wireOp",EDGE,"E8.19.0"),sQuery(id+"F0.wireOp",EDGE,"E8.20.0"),sQuery(id+"F0.wireOp",EDGE,"E8.21.0"),sQuery(id+"F0.wireOp",EDGE,"E8.22.0"),sQuery(id+"F0.wireOp",EDGE,"E8.23.0"),sQuery(id+"F0.wireOp",EDGE,"E8.24.0"),sQuery(id+"F0.wireOp",EDGE,"E8.25.0"),sQuery(id+"F0.wireOp",EDGE,"E8.26.0"),sQuery(id+"F0.wireOp",EDGE,"E8.27.0"),sQuery(id+"F0.wireOp",EDGE,"E8.28.0"),sQuery(id+"F0.wireOp",EDGE,"E8.29.0"),sQuery(id+"F0.wireOp",EDGE,"E8.30.0"),sQuery(id+"F0.wireOp",EDGE,"E8.31.0"),sQuery(id+"F0.wireOp",EDGE,"E8.32.0"),sQuery(id+"F0.wireOp",EDGE,"E8.33.0"),sQuery(id+"F0.wireOp",EDGE,"E8.34.0"),sQuery(id+"F0.wireOp",EDGE,"E8.35.0"),sQuery(id+"F0.wireOp",EDGE,"E8.36.0"),sQuery(id+"F0.wireOp",EDGE,"E8.37.0"),sQuery(id+"F0.wireOp",EDGE,"E8.38.0"),sQuery(id+"F0.wireOp",EDGE,"E8.39.0"),sQuery(id+"F0.wireOp",EDGE,"E8.40.0"),sQuery(id+"F0.wireOp",EDGE,"E8.41.0"),sQuery(id+"F0.wireOp",EDGE,"E8.42.0"),sQuery(id+"F0.wireOp",EDGE,"E8.43.0")])],"isStart":true})],"blendedInto":[makeQuery(id+"F1.opExtrude","CAP_FACE",FACE,{"disambiguationData":[OSD([sQuery(id+"F0.wireOp",EDGE,"E0"),sQuery(id+"F0.wireOp",EDGE,"E1"),sQuery(id+"F0.wireOp",EDGE,"E2"),sQuery(id+"F0.wireOp",EDGE,"E4"),sQuery(id+"F0.wireOp",EDGE,"E5"),sQuery(id+"F0.wireOp",EDGE,"E6.1.1"),sQuery(id+"F0.wireOp",EDGE,"E6.1.2"),sQuery(id+"F0.wireOp",EDGE,"E6.1.3"),sQuery(id+"F0.wireOp",EDGE,"E6.1.4"),subQ1,sQuery(id+"F0.wireOp",EDGE,"E6.2.2"),subQ0,sQuery(id+"F0.wireOp",EDGE,"E6.2.4"),sQuery(id+"F0.wireOp",EDGE,"E6.3.1"),sQuery(id+"F0.wireOp",EDGE,"E6.3.2"),sQuery(id+"F0.wireOp",EDGE,"E6.3.3"),sQuery(id+"F0.wireOp",EDGE,"E6.3.4"),sQuery(id+"F0.wireOp",EDGE,"E6.4.1"),sQuery(id+"F0.wireOp",EDGE,"E6.4.2"),sQuery(id+"F0.wireOp",EDGE,"E6.4.3"),sQuery(id+"F0.wireOp",EDGE,"E6.4.4"),sQuery(id+"F0.wireOp",EDGE,"E6.5.1"),sQuery(id+"F0.wireOp",EDGE,"E6.5.2"),sQuery(id+"F0.wireOp",EDGE,"E6.5.3"),sQuery(id+"F0.wireOp",EDGE,"E6.5.4"),sQuery(id+"F0.wireOp",EDGE,"E6.6.1"),sQuery(id+"F0.wireOp",EDGE,"E6.6.2"),sQuery(id+"F0.wireOp",EDGE,"E6.6.3"),sQuery(id+"F0.wireOp",EDGE,"E6.6.4"),sQuery(id+"F0.wireOp",EDGE,"E6.7.1"),sQuery(id+"F0.wireOp",EDGE,"E6.7.2"),sQuery(id+"F0.wireOp",EDGE,"E6.7.3"),sQuery(id+"F0.wireOp",EDGE,"E6.7.4"),sQuery(id+"F0.wireOp",EDGE,"E6.8.1"),sQuery(id+"F0.wireOp",EDGE,"E6.8.2"),sQuery(id+"F0.wireOp",EDGE,"E6.8.3"),sQuery(id+"F0.wireOp",EDGE,"E6.8.4"),sQuery(id+"F0.wireOp",EDGE,"E6.9.1"),sQuery(id+"F0.wireOp",EDGE,"E6.9.2"),sQuery(id+"F0.wireOp",EDGE,"E6.9.3"),sQuery(id+"F0.wireOp",EDGE,"E6.9.4"),sQuery(id+"F0.wireOp",EDGE,"E6.10.1"),sQuery(id+"F0.wireOp",EDGE,"E6.10.2"),sQuery(id+"F0.wireOp",EDGE,"E6.10.3"),sQuery(id+"F0.wireOp",EDGE,"E6.10.4"),sQuery(id+"F0.wireOp",EDGE,"E6.11.1"),sQuery(id+"F0.wireOp",EDGE,"E6.11.2"),sQuery(id+"F0.wireOp",EDGE,"E6.11.3"),sQuery(id+"F0.wireOp",EDGE,"E6.11.4"),sQuery(id+"F0.wireOp",EDGE,"E6.12.1"),sQuery(id+"F0.wireOp",EDGE,"E6.12.2"),sQuery(id+"F0.wireOp",EDGE,"E6.12.3"),sQuery(id+"F0.wireOp",EDGE,"E6.12.4"),sQuery(id+"F0.wireOp",EDGE,"E6.13.1"),sQuery(id+"F0.wireOp",EDGE,"E6.13.2"),sQuery(id+"F0.wireOp",EDGE,"E6.13.3"),sQuery(id+"F0.wireOp",EDGE,"E6.13.4"),sQuery(id+"F0.wireOp",EDGE,"E6.14.1"),sQuery(id+"F0.wireOp",EDGE,"E6.14.2"),sQuery(id+"F0.wireOp",EDGE,"E6.14.3"),sQuery(id+"F0.wireOp",EDGE,"E6.14.4"),sQuery(id+"F0.wireOp",EDGE,"E6.15.1"),sQuery(id+"F0.wireOp",EDGE,"E6.15.2"),sQuery(id+"F0.wireOp",EDGE,"E6.15.3"),sQuery(id+"F0.wireOp",EDGE,"E6.15.4"),sQuery(id+"F0.wireOp",EDGE,"E6.16.1"),sQuery(id+"F0.wireOp",EDGE,"E6.16.2"),sQuery(id+"F0.wireOp",EDGE,"E6.16.3"),sQuery(id+"F0.wireOp",EDGE,"E6.16.4"),sQuery(id+"F0.wireOp",EDGE,"E6.17.1"),sQuery(id+"F0.wireOp",EDGE,"E6.17.2"),sQuery(id+"F0.wireOp",EDGE,"E6.17.3"),sQuery(id+"F0.wireOp",EDGE,"E6.17.4"),sQuery(id+"F0.wireOp",EDGE,"E6.18.1"),sQuery(id+"F0.wireOp",EDGE,"E6.18.2"),sQuery(id+"F0.wireOp",EDGE,"E6.18.3"),sQuery(id+"F0.wireOp",EDGE,"E6.18.4"),sQuery(id+"F0.wireOp",EDGE,"E6.19.1"),sQuery(id+"F0.wireOp",EDGE,"E6.19.2"),sQuery(id+"F0.wireOp",EDGE,"E6.19.3"),sQuery(id+"F0.wireOp",EDGE,"E6.19.4"),sQuery(id+"F0.wireOp",EDGE,"E6.20.1"),sQuery(id+"F0.wireOp",EDGE,"E6.20.2"),sQuery(id+"F0.wireOp",EDGE,"E6.20.3"),sQuery(id+"F0.wireOp",EDGE,"E6.20.4"),sQuery(id+"F0.wireOp",EDGE,"E6.21.1"),sQuery(id+"F0.wireOp",EDGE,"E6.21.2"),sQuery(id+"F0.wireOp",EDGE,"E6.21.3"),sQuery(id+"F0.wireOp",EDGE,"E6.21.4"),sQuery(id+"F0.wireOp",EDGE,"E6.22.1"),sQuery(id+"F0.wireOp",EDGE,"E6.22.2"),sQuery(id+"F0.wireOp",EDGE,"E6.22.3"),sQuery(id+"F0.wireOp",EDGE,"E6.22.4"),sQuery(id+"F0.wireOp",EDGE,"E6.23.1"),sQuery(id+"F0.wireOp",EDGE,"E6.23.2"),sQuery(id+"F0.wireOp",EDGE,"E6.23.3"),sQuery(id+"F0.wireOp",EDGE,"E6.23.4"),sQuery(id+"F0.wireOp",EDGE,"E6.24.1"),sQuery(id+"F0.wireOp",EDGE,"E6.24.2"),sQuery(id+"F0.wireOp",EDGE,"E6.24.3"),sQuery(id+"F0.wireOp",EDGE,"E6.24.4"),sQuery(id+"F0.wireOp",EDGE,"E6.25.1"),sQuery(id+"F0.wireOp",EDGE,"E6.25.2"),sQuery(id+"F0.wireOp",EDGE,"E6.25.3"),sQuery(id+"F0.wireOp",EDGE,"E6.25.4"),sQuery(id+"F0.wireOp",EDGE,"E6.26.1"),sQuery(id+"F0.wireOp",EDGE,"E6.26.2"),sQuery(id+"F0.wireOp",EDGE,"E6.26.3"),sQuery(id+"F0.wireOp",EDGE,"E6.26.4"),sQuery(id+"F0.wireOp",EDGE,"E6.27.1"),sQuery(id+"F0.wireOp",EDGE,"E6.27.2"),sQuery(id+"F0.wireOp",EDGE,"E6.27.3"),sQuery(id+"F0.wireOp",EDGE,"E6.27.4"),sQuery(id+"F0.wireOp",EDGE,"E6.28.1"),sQuery(id+"F0.wireOp",EDGE,"E6.28.2"),sQuery(id+"F0.wireOp",EDGE,"E6.28.3"),sQuery(id+"F0.wireOp",EDGE,"E6.28.4"),sQuery(id+"F0.wireOp",EDGE,"E6.29.1"),sQuery(id+"F0.wireOp",EDGE,"E6.29.2"),sQuery(id+"F0.wireOp",EDGE,"E6.29.3"),sQuery(id+"F0.wireOp",EDGE,"E6.29.4"),sQuery(id+"F0.wireOp",EDGE,"E6.30.1"),sQuery(id+"F0.wireOp",EDGE,"E6.30.2"),sQuery(id+"F0.wireOp",EDGE,"E6.30.3"),sQuery(id+"F0.wireOp",EDGE,"E6.30.4"),sQuery(id+"F0.wireOp",EDGE,"E6.31.1"),sQuery(id+"F0.wireOp",EDGE,"E6.31.2"),sQuery(id+"F0.wireOp",EDGE,"E6.31.3"),sQuery(id+"F0.wireOp",EDGE,"E6.31.4"),sQuery(id+"F0.wireOp",EDGE,"E6.32.1"),sQuery(id+"F0.wireOp",EDGE,"E6.32.2"),sQuery(id+"F0.wireOp",EDGE,"E6.32.3"),sQuery(id+"F0.wireOp",EDGE,"E6.32.4"),sQuery(id+"F0.wireOp",EDGE,"E6.33.1"),sQuery(id+"F0.wireOp",EDGE,"E6.33.2"),sQuery(id+"F0.wireOp",EDGE,"E6.33.3"),sQuery(id+"F0.wireOp",EDGE,"E6.33.4"),sQuery(id+"F0.wireOp",EDGE,"E6.34.1"),sQuery(id+"F0.wireOp",EDGE,"E6.34.2"),sQuery(id+"F0.wireOp",EDGE,"E6.34.3"),sQuery(id+"F0.wireOp",EDGE,"E6.34.4"),sQuery(id+"F0.wireOp",EDGE,"E6.35.1"),sQuery(id+"F0.wireOp",EDGE,"E6.35.2"),sQuery(id+"F0.wireOp",EDGE,"E6.35.3"),sQuery(id+"F0.wireOp",EDGE,"E6.35.4"),sQuery(id+"F0.wireOp",EDGE,"E6.36.1"),sQuery(id+"F0.wireOp",EDGE,"E6.36.2"),sQuery(id+"F0.wireOp",EDGE,"E6.36.3"),sQuery(id+"F0.wireOp",EDGE,"E6.36.4"),sQuery(id+"F0.wireOp",EDGE,"E6.37.1"),sQuery(id+"F0.wireOp",EDGE,"E6.37.2"),sQuery(id+"F0.wireOp",EDGE,"E6.37.3"),sQuery(id+"F0.wireOp",EDGE,"E6.37.4"),sQuery(id+"F0.wireOp",EDGE,"E6.38.1"),sQuery(id+"F0.wireOp",EDGE,"E6.38.2"),sQuery(id+"F0.wireOp",EDGE,"E6.38.3"),sQuery(id+"F0.wireOp",EDGE,"E6.38.4"),sQuery(id+"F0.wireOp",EDGE,"E6.39.1"),sQuery(id+"F0.wireOp",EDGE,"E6.39.2"),sQuery(id+"F0.wireOp",EDGE,"E6.39.3"),sQuery(id+"F0.wireOp",EDGE,"E6.39.4"),sQuery(id+"F0.wireOp",EDGE,"E6.40.1"),sQuery(id+"F0.wireOp",EDGE,"E6.40.2"),sQuery(id+"F0.wireOp",EDGE,"E6.40.3"),sQuery(id+"F0.wireOp",EDGE,"E6.40.4"),sQuery(id+"F0.wireOp",EDGE,"E6.41.1"),sQuery(id+"F0.wireOp",EDGE,"E6.41.2"),sQuery(id+"F0.wireOp",EDGE,"E6.41.3"),sQuery(id+"F0.wireOp",EDGE,"E6.41.4"),sQuery(id+"F0.wireOp",EDGE,"E6.42.1"),sQuery(id+"F0.wireOp",EDGE,"E6.42.2"),sQuery(id+"F0.wireOp",EDGE,"E6.42.3"),sQuery(id+"F0.wireOp",EDGE,"E6.42.4"),sQuery(id+"F0.wireOp",EDGE,"E6.43.1"),sQuery(id+"F0.wireOp",EDGE,"E6.43.2"),sQuery(id+"F0.wireOp",EDGE,"E6.43.3"),sQuery(id+"F0.wireOp",EDGE,"E6.43.4"),sQuery(id+"F0.wireOp",EDGE,"E7"),sQuery(id+"F0.wireOp",EDGE,"E8.1.0"),sQuery(id+"F0.wireOp",EDGE,"E8.2.0"),sQuery(id+"F0.wireOp",EDGE,"E8.3.0"),sQuery(id+"F0.wireOp",EDGE,"E8.4.0"),sQuery(id+"F0.wireOp",EDGE,"E8.5.0"),sQuery(id+"F0.wireOp",EDGE,"E8.6.0"),sQuery(id+"F0.wireOp",EDGE,"E8.7.0"),sQuery(id+"F0.wireOp",EDGE,"E8.8.0"),sQuery(id+"F0.wireOp",EDGE,"E8.9.0"),sQuery(id+"F0.wireOp",EDGE,"E8.10.0"),sQuery(id+"F0.wireOp",EDGE,"E8.11.0"),sQuery(id+"F0.wireOp",EDGE,"E8.12.0"),sQuery(id+"F0.wireOp",EDGE,"E8.13.0"),sQuery(id+"F0.wireOp",EDGE,"E8.14.0"),sQuery(id+"F0.wireOp",EDGE,"E8.15.0"),sQuery(id+"F0.wireOp",EDGE,"E8.16.0"),sQuery(id+"F0.wireOp",EDGE,"E8.17.0"),sQuery(id+"F0.wireOp",EDGE,"E8.18.0"),sQuery(id+"F0.wireOp",EDGE,"E8.19.0"),sQuery(id+"F0.wireOp",EDGE,"E8.20.0"),sQuery(id+"F0.wireOp",EDGE,"E8.21.0"),sQuery(id+"F0.wireOp",EDGE,"E8.22.0"),sQuery(id+"F0.wireOp",EDGE,"E8.23.0"),sQuery(id+"F0.wireOp",EDGE,"E8.24.0"),sQuery(id+"F0.wireOp",EDGE,"E8.25.0"),sQuery(id+"F0.wireOp",EDGE,"E8.26.0"),sQuery(id+"F0.wireOp",EDGE,"E8.27.0"),sQuery(id+"F0.wireOp",EDGE,"E8.28.0"),sQuery(id+"F0.wireOp",EDGE,"E8.29.0"),sQuery(id+"F0.wireOp",EDGE,"E8.30.0"),sQuery(id+"F0.wireOp",EDGE,"E8.31.0"),sQuery(id+"F0.wireOp",EDGE,"E8.32.0"),sQuery(id+"F0.wireOp",EDGE,"E8.33.0"),sQuery(id+"F0.wireOp",EDGE,"E8.34.0"),sQuery(id+"F0.wireOp",EDGE,"E8.35.0"),sQuery(id+"F0.wireOp",EDGE,"E8.36.0"),sQuery(id+"F0.wireOp",EDGE,"E8.37.0"),sQuery(id+"F0.wireOp",EDGE,"E8.38.0"),sQuery(id+"F0.wireOp",EDGE,"E8.39.0"),sQuery(id+"F0.wireOp",EDGE,"E8.40.0"),sQuery(id+"F0.wireOp",EDGE,"E8.41.0"),sQuery(id+"F0.wireOp",EDGE,"E8.42.0"),sQuery(id+"F0.wireOp",EDGE,"E8.43.0")])],"isStart":true})]});}
            var Q24;
            {var subQ0=sQuery(id+"F0.wireOp",EDGE,"E6.4.3");var subQ1=sQuery(id+"F0.wireOp",EDGE,"E6.4.1");Q24=makeQuery(id+"F2.opFillet","BLEND_EDGE",EDGE,{"blendedFrom":[makeQuery(id+"F1.opExtrude","SWEPT_EDGE",EDGE,{"disambiguationData":[OSD([sQuery(id+"F0.wireOp",EDGE,"E6.4.0"),subQ1,subQ0])]}),makeQuery(id+"F1.opExtrude","CAP_FACE",FACE,{"disambiguationData":[OSD([sQuery(id+"F0.wireOp",EDGE,"E0"),sQuery(id+"F0.wireOp",EDGE,"E1"),sQuery(id+"F0.wireOp",EDGE,"E2"),sQuery(id+"F0.wireOp",EDGE,"E4"),sQuery(id+"F0.wireOp",EDGE,"E5"),sQuery(id+"F0.wireOp",EDGE,"E6.1.1"),sQuery(id+"F0.wireOp",EDGE,"E6.1.2"),sQuery(id+"F0.wireOp",EDGE,"E6.1.3"),sQuery(id+"F0.wireOp",EDGE,"E6.1.4"),sQuery(id+"F0.wireOp",EDGE,"E6.2.1"),sQuery(id+"F0.wireOp",EDGE,"E6.2.2"),sQuery(id+"F0.wireOp",EDGE,"E6.2.3"),sQuery(id+"F0.wireOp",EDGE,"E6.2.4"),sQuery(id+"F0.wireOp",EDGE,"E6.3.1"),sQuery(id+"F0.wireOp",EDGE,"E6.3.2"),sQuery(id+"F0.wireOp",EDGE,"E6.3.3"),sQuery(id+"F0.wireOp",EDGE,"E6.3.4"),subQ1,sQuery(id+"F0.wireOp",EDGE,"E6.4.2"),subQ0,sQuery(id+"F0.wireOp",EDGE,"E6.4.4"),sQuery(id+"F0.wireOp",EDGE,"E6.5.1"),sQuery(id+"F0.wireOp",EDGE,"E6.5.2"),sQuery(id+"F0.wireOp",EDGE,"E6.5.3"),sQuery(id+"F0.wireOp",EDGE,"E6.5.4"),sQuery(id+"F0.wireOp",EDGE,"E6.6.1"),sQuery(id+"F0.wireOp",EDGE,"E6.6.2"),sQuery(id+"F0.wireOp",EDGE,"E6.6.3"),sQuery(id+"F0.wireOp",EDGE,"E6.6.4"),sQuery(id+"F0.wireOp",EDGE,"E6.7.1"),sQuery(id+"F0.wireOp",EDGE,"E6.7.2"),sQuery(id+"F0.wireOp",EDGE,"E6.7.3"),sQuery(id+"F0.wireOp",EDGE,"E6.7.4"),sQuery(id+"F0.wireOp",EDGE,"E6.8.1"),sQuery(id+"F0.wireOp",EDGE,"E6.8.2"),sQuery(id+"F0.wireOp",EDGE,"E6.8.3"),sQuery(id+"F0.wireOp",EDGE,"E6.8.4"),sQuery(id+"F0.wireOp",EDGE,"E6.9.1"),sQuery(id+"F0.wireOp",EDGE,"E6.9.2"),sQuery(id+"F0.wireOp",EDGE,"E6.9.3"),sQuery(id+"F0.wireOp",EDGE,"E6.9.4"),sQuery(id+"F0.wireOp",EDGE,"E6.10.1"),sQuery(id+"F0.wireOp",EDGE,"E6.10.2"),sQuery(id+"F0.wireOp",EDGE,"E6.10.3"),sQuery(id+"F0.wireOp",EDGE,"E6.10.4"),sQuery(id+"F0.wireOp",EDGE,"E6.11.1"),sQuery(id+"F0.wireOp",EDGE,"E6.11.2"),sQuery(id+"F0.wireOp",EDGE,"E6.11.3"),sQuery(id+"F0.wireOp",EDGE,"E6.11.4"),sQuery(id+"F0.wireOp",EDGE,"E6.12.1"),sQuery(id+"F0.wireOp",EDGE,"E6.12.2"),sQuery(id+"F0.wireOp",EDGE,"E6.12.3"),sQuery(id+"F0.wireOp",EDGE,"E6.12.4"),sQuery(id+"F0.wireOp",EDGE,"E6.13.1"),sQuery(id+"F0.wireOp",EDGE,"E6.13.2"),sQuery(id+"F0.wireOp",EDGE,"E6.13.3"),sQuery(id+"F0.wireOp",EDGE,"E6.13.4"),sQuery(id+"F0.wireOp",EDGE,"E6.14.1"),sQuery(id+"F0.wireOp",EDGE,"E6.14.2"),sQuery(id+"F0.wireOp",EDGE,"E6.14.3"),sQuery(id+"F0.wireOp",EDGE,"E6.14.4"),sQuery(id+"F0.wireOp",EDGE,"E6.15.1"),sQuery(id+"F0.wireOp",EDGE,"E6.15.2"),sQuery(id+"F0.wireOp",EDGE,"E6.15.3"),sQuery(id+"F0.wireOp",EDGE,"E6.15.4"),sQuery(id+"F0.wireOp",EDGE,"E6.16.1"),sQuery(id+"F0.wireOp",EDGE,"E6.16.2"),sQuery(id+"F0.wireOp",EDGE,"E6.16.3"),sQuery(id+"F0.wireOp",EDGE,"E6.16.4"),sQuery(id+"F0.wireOp",EDGE,"E6.17.1"),sQuery(id+"F0.wireOp",EDGE,"E6.17.2"),sQuery(id+"F0.wireOp",EDGE,"E6.17.3"),sQuery(id+"F0.wireOp",EDGE,"E6.17.4"),sQuery(id+"F0.wireOp",EDGE,"E6.18.1"),sQuery(id+"F0.wireOp",EDGE,"E6.18.2"),sQuery(id+"F0.wireOp",EDGE,"E6.18.3"),sQuery(id+"F0.wireOp",EDGE,"E6.18.4"),sQuery(id+"F0.wireOp",EDGE,"E6.19.1"),sQuery(id+"F0.wireOp",EDGE,"E6.19.2"),sQuery(id+"F0.wireOp",EDGE,"E6.19.3"),sQuery(id+"F0.wireOp",EDGE,"E6.19.4"),sQuery(id+"F0.wireOp",EDGE,"E6.20.1"),sQuery(id+"F0.wireOp",EDGE,"E6.20.2"),sQuery(id+"F0.wireOp",EDGE,"E6.20.3"),sQuery(id+"F0.wireOp",EDGE,"E6.20.4"),sQuery(id+"F0.wireOp",EDGE,"E6.21.1"),sQuery(id+"F0.wireOp",EDGE,"E6.21.2"),sQuery(id+"F0.wireOp",EDGE,"E6.21.3"),sQuery(id+"F0.wireOp",EDGE,"E6.21.4"),sQuery(id+"F0.wireOp",EDGE,"E6.22.1"),sQuery(id+"F0.wireOp",EDGE,"E6.22.2"),sQuery(id+"F0.wireOp",EDGE,"E6.22.3"),sQuery(id+"F0.wireOp",EDGE,"E6.22.4"),sQuery(id+"F0.wireOp",EDGE,"E6.23.1"),sQuery(id+"F0.wireOp",EDGE,"E6.23.2"),sQuery(id+"F0.wireOp",EDGE,"E6.23.3"),sQuery(id+"F0.wireOp",EDGE,"E6.23.4"),sQuery(id+"F0.wireOp",EDGE,"E6.24.1"),sQuery(id+"F0.wireOp",EDGE,"E6.24.2"),sQuery(id+"F0.wireOp",EDGE,"E6.24.3"),sQuery(id+"F0.wireOp",EDGE,"E6.24.4"),sQuery(id+"F0.wireOp",EDGE,"E6.25.1"),sQuery(id+"F0.wireOp",EDGE,"E6.25.2"),sQuery(id+"F0.wireOp",EDGE,"E6.25.3"),sQuery(id+"F0.wireOp",EDGE,"E6.25.4"),sQuery(id+"F0.wireOp",EDGE,"E6.26.1"),sQuery(id+"F0.wireOp",EDGE,"E6.26.2"),sQuery(id+"F0.wireOp",EDGE,"E6.26.3"),sQuery(id+"F0.wireOp",EDGE,"E6.26.4"),sQuery(id+"F0.wireOp",EDGE,"E6.27.1"),sQuery(id+"F0.wireOp",EDGE,"E6.27.2"),sQuery(id+"F0.wireOp",EDGE,"E6.27.3"),sQuery(id+"F0.wireOp",EDGE,"E6.27.4"),sQuery(id+"F0.wireOp",EDGE,"E6.28.1"),sQuery(id+"F0.wireOp",EDGE,"E6.28.2"),sQuery(id+"F0.wireOp",EDGE,"E6.28.3"),sQuery(id+"F0.wireOp",EDGE,"E6.28.4"),sQuery(id+"F0.wireOp",EDGE,"E6.29.1"),sQuery(id+"F0.wireOp",EDGE,"E6.29.2"),sQuery(id+"F0.wireOp",EDGE,"E6.29.3"),sQuery(id+"F0.wireOp",EDGE,"E6.29.4"),sQuery(id+"F0.wireOp",EDGE,"E6.30.1"),sQuery(id+"F0.wireOp",EDGE,"E6.30.2"),sQuery(id+"F0.wireOp",EDGE,"E6.30.3"),sQuery(id+"F0.wireOp",EDGE,"E6.30.4"),sQuery(id+"F0.wireOp",EDGE,"E6.31.1"),sQuery(id+"F0.wireOp",EDGE,"E6.31.2"),sQuery(id+"F0.wireOp",EDGE,"E6.31.3"),sQuery(id+"F0.wireOp",EDGE,"E6.31.4"),sQuery(id+"F0.wireOp",EDGE,"E6.32.1"),sQuery(id+"F0.wireOp",EDGE,"E6.32.2"),sQuery(id+"F0.wireOp",EDGE,"E6.32.3"),sQuery(id+"F0.wireOp",EDGE,"E6.32.4"),sQuery(id+"F0.wireOp",EDGE,"E6.33.1"),sQuery(id+"F0.wireOp",EDGE,"E6.33.2"),sQuery(id+"F0.wireOp",EDGE,"E6.33.3"),sQuery(id+"F0.wireOp",EDGE,"E6.33.4"),sQuery(id+"F0.wireOp",EDGE,"E6.34.1"),sQuery(id+"F0.wireOp",EDGE,"E6.34.2"),sQuery(id+"F0.wireOp",EDGE,"E6.34.3"),sQuery(id+"F0.wireOp",EDGE,"E6.34.4"),sQuery(id+"F0.wireOp",EDGE,"E6.35.1"),sQuery(id+"F0.wireOp",EDGE,"E6.35.2"),sQuery(id+"F0.wireOp",EDGE,"E6.35.3"),sQuery(id+"F0.wireOp",EDGE,"E6.35.4"),sQuery(id+"F0.wireOp",EDGE,"E6.36.1"),sQuery(id+"F0.wireOp",EDGE,"E6.36.2"),sQuery(id+"F0.wireOp",EDGE,"E6.36.3"),sQuery(id+"F0.wireOp",EDGE,"E6.36.4"),sQuery(id+"F0.wireOp",EDGE,"E6.37.1"),sQuery(id+"F0.wireOp",EDGE,"E6.37.2"),sQuery(id+"F0.wireOp",EDGE,"E6.37.3"),sQuery(id+"F0.wireOp",EDGE,"E6.37.4"),sQuery(id+"F0.wireOp",EDGE,"E6.38.1"),sQuery(id+"F0.wireOp",EDGE,"E6.38.2"),sQuery(id+"F0.wireOp",EDGE,"E6.38.3"),sQuery(id+"F0.wireOp",EDGE,"E6.38.4"),sQuery(id+"F0.wireOp",EDGE,"E6.39.1"),sQuery(id+"F0.wireOp",EDGE,"E6.39.2"),sQuery(id+"F0.wireOp",EDGE,"E6.39.3"),sQuery(id+"F0.wireOp",EDGE,"E6.39.4"),sQuery(id+"F0.wireOp",EDGE,"E6.40.1"),sQuery(id+"F0.wireOp",EDGE,"E6.40.2"),sQuery(id+"F0.wireOp",EDGE,"E6.40.3"),sQuery(id+"F0.wireOp",EDGE,"E6.40.4"),sQuery(id+"F0.wireOp",EDGE,"E6.41.1"),sQuery(id+"F0.wireOp",EDGE,"E6.41.2"),sQuery(id+"F0.wireOp",EDGE,"E6.41.3"),sQuery(id+"F0.wireOp",EDGE,"E6.41.4"),sQuery(id+"F0.wireOp",EDGE,"E6.42.1"),sQuery(id+"F0.wireOp",EDGE,"E6.42.2"),sQuery(id+"F0.wireOp",EDGE,"E6.42.3"),sQuery(id+"F0.wireOp",EDGE,"E6.42.4"),sQuery(id+"F0.wireOp",EDGE,"E6.43.1"),sQuery(id+"F0.wireOp",EDGE,"E6.43.2"),sQuery(id+"F0.wireOp",EDGE,"E6.43.3"),sQuery(id+"F0.wireOp",EDGE,"E6.43.4"),sQuery(id+"F0.wireOp",EDGE,"E7"),sQuery(id+"F0.wireOp",EDGE,"E8.1.0"),sQuery(id+"F0.wireOp",EDGE,"E8.2.0"),sQuery(id+"F0.wireOp",EDGE,"E8.3.0"),sQuery(id+"F0.wireOp",EDGE,"E8.4.0"),sQuery(id+"F0.wireOp",EDGE,"E8.5.0"),sQuery(id+"F0.wireOp",EDGE,"E8.6.0"),sQuery(id+"F0.wireOp",EDGE,"E8.7.0"),sQuery(id+"F0.wireOp",EDGE,"E8.8.0"),sQuery(id+"F0.wireOp",EDGE,"E8.9.0"),sQuery(id+"F0.wireOp",EDGE,"E8.10.0"),sQuery(id+"F0.wireOp",EDGE,"E8.11.0"),sQuery(id+"F0.wireOp",EDGE,"E8.12.0"),sQuery(id+"F0.wireOp",EDGE,"E8.13.0"),sQuery(id+"F0.wireOp",EDGE,"E8.14.0"),sQuery(id+"F0.wireOp",EDGE,"E8.15.0"),sQuery(id+"F0.wireOp",EDGE,"E8.16.0"),sQuery(id+"F0.wireOp",EDGE,"E8.17.0"),sQuery(id+"F0.wireOp",EDGE,"E8.18.0"),sQuery(id+"F0.wireOp",EDGE,"E8.19.0"),sQuery(id+"F0.wireOp",EDGE,"E8.20.0"),sQuery(id+"F0.wireOp",EDGE,"E8.21.0"),sQuery(id+"F0.wireOp",EDGE,"E8.22.0"),sQuery(id+"F0.wireOp",EDGE,"E8.23.0"),sQuery(id+"F0.wireOp",EDGE,"E8.24.0"),sQuery(id+"F0.wireOp",EDGE,"E8.25.0"),sQuery(id+"F0.wireOp",EDGE,"E8.26.0"),sQuery(id+"F0.wireOp",EDGE,"E8.27.0"),sQuery(id+"F0.wireOp",EDGE,"E8.28.0"),sQuery(id+"F0.wireOp",EDGE,"E8.29.0"),sQuery(id+"F0.wireOp",EDGE,"E8.30.0"),sQuery(id+"F0.wireOp",EDGE,"E8.31.0"),sQuery(id+"F0.wireOp",EDGE,"E8.32.0"),sQuery(id+"F0.wireOp",EDGE,"E8.33.0"),sQuery(id+"F0.wireOp",EDGE,"E8.34.0"),sQuery(id+"F0.wireOp",EDGE,"E8.35.0"),sQuery(id+"F0.wireOp",EDGE,"E8.36.0"),sQuery(id+"F0.wireOp",EDGE,"E8.37.0"),sQuery(id+"F0.wireOp",EDGE,"E8.38.0"),sQuery(id+"F0.wireOp",EDGE,"E8.39.0"),sQuery(id+"F0.wireOp",EDGE,"E8.40.0"),sQuery(id+"F0.wireOp",EDGE,"E8.41.0"),sQuery(id+"F0.wireOp",EDGE,"E8.42.0"),sQuery(id+"F0.wireOp",EDGE,"E8.43.0")])],"isStart":true})],"blendedInto":[makeQuery(id+"F1.opExtrude","CAP_FACE",FACE,{"disambiguationData":[OSD([sQuery(id+"F0.wireOp",EDGE,"E0"),sQuery(id+"F0.wireOp",EDGE,"E1"),sQuery(id+"F0.wireOp",EDGE,"E2"),sQuery(id+"F0.wireOp",EDGE,"E4"),sQuery(id+"F0.wireOp",EDGE,"E5"),sQuery(id+"F0.wireOp",EDGE,"E6.1.1"),sQuery(id+"F0.wireOp",EDGE,"E6.1.2"),sQuery(id+"F0.wireOp",EDGE,"E6.1.3"),sQuery(id+"F0.wireOp",EDGE,"E6.1.4"),sQuery(id+"F0.wireOp",EDGE,"E6.2.1"),sQuery(id+"F0.wireOp",EDGE,"E6.2.2"),sQuery(id+"F0.wireOp",EDGE,"E6.2.3"),sQuery(id+"F0.wireOp",EDGE,"E6.2.4"),sQuery(id+"F0.wireOp",EDGE,"E6.3.1"),sQuery(id+"F0.wireOp",EDGE,"E6.3.2"),sQuery(id+"F0.wireOp",EDGE,"E6.3.3"),sQuery(id+"F0.wireOp",EDGE,"E6.3.4"),subQ1,sQuery(id+"F0.wireOp",EDGE,"E6.4.2"),subQ0,sQuery(id+"F0.wireOp",EDGE,"E6.4.4"),sQuery(id+"F0.wireOp",EDGE,"E6.5.1"),sQuery(id+"F0.wireOp",EDGE,"E6.5.2"),sQuery(id+"F0.wireOp",EDGE,"E6.5.3"),sQuery(id+"F0.wireOp",EDGE,"E6.5.4"),sQuery(id+"F0.wireOp",EDGE,"E6.6.1"),sQuery(id+"F0.wireOp",EDGE,"E6.6.2"),sQuery(id+"F0.wireOp",EDGE,"E6.6.3"),sQuery(id+"F0.wireOp",EDGE,"E6.6.4"),sQuery(id+"F0.wireOp",EDGE,"E6.7.1"),sQuery(id+"F0.wireOp",EDGE,"E6.7.2"),sQuery(id+"F0.wireOp",EDGE,"E6.7.3"),sQuery(id+"F0.wireOp",EDGE,"E6.7.4"),sQuery(id+"F0.wireOp",EDGE,"E6.8.1"),sQuery(id+"F0.wireOp",EDGE,"E6.8.2"),sQuery(id+"F0.wireOp",EDGE,"E6.8.3"),sQuery(id+"F0.wireOp",EDGE,"E6.8.4"),sQuery(id+"F0.wireOp",EDGE,"E6.9.1"),sQuery(id+"F0.wireOp",EDGE,"E6.9.2"),sQuery(id+"F0.wireOp",EDGE,"E6.9.3"),sQuery(id+"F0.wireOp",EDGE,"E6.9.4"),sQuery(id+"F0.wireOp",EDGE,"E6.10.1"),sQuery(id+"F0.wireOp",EDGE,"E6.10.2"),sQuery(id+"F0.wireOp",EDGE,"E6.10.3"),sQuery(id+"F0.wireOp",EDGE,"E6.10.4"),sQuery(id+"F0.wireOp",EDGE,"E6.11.1"),sQuery(id+"F0.wireOp",EDGE,"E6.11.2"),sQuery(id+"F0.wireOp",EDGE,"E6.11.3"),sQuery(id+"F0.wireOp",EDGE,"E6.11.4"),sQuery(id+"F0.wireOp",EDGE,"E6.12.1"),sQuery(id+"F0.wireOp",EDGE,"E6.12.2"),sQuery(id+"F0.wireOp",EDGE,"E6.12.3"),sQuery(id+"F0.wireOp",EDGE,"E6.12.4"),sQuery(id+"F0.wireOp",EDGE,"E6.13.1"),sQuery(id+"F0.wireOp",EDGE,"E6.13.2"),sQuery(id+"F0.wireOp",EDGE,"E6.13.3"),sQuery(id+"F0.wireOp",EDGE,"E6.13.4"),sQuery(id+"F0.wireOp",EDGE,"E6.14.1"),sQuery(id+"F0.wireOp",EDGE,"E6.14.2"),sQuery(id+"F0.wireOp",EDGE,"E6.14.3"),sQuery(id+"F0.wireOp",EDGE,"E6.14.4"),sQuery(id+"F0.wireOp",EDGE,"E6.15.1"),sQuery(id+"F0.wireOp",EDGE,"E6.15.2"),sQuery(id+"F0.wireOp",EDGE,"E6.15.3"),sQuery(id+"F0.wireOp",EDGE,"E6.15.4"),sQuery(id+"F0.wireOp",EDGE,"E6.16.1"),sQuery(id+"F0.wireOp",EDGE,"E6.16.2"),sQuery(id+"F0.wireOp",EDGE,"E6.16.3"),sQuery(id+"F0.wireOp",EDGE,"E6.16.4"),sQuery(id+"F0.wireOp",EDGE,"E6.17.1"),sQuery(id+"F0.wireOp",EDGE,"E6.17.2"),sQuery(id+"F0.wireOp",EDGE,"E6.17.3"),sQuery(id+"F0.wireOp",EDGE,"E6.17.4"),sQuery(id+"F0.wireOp",EDGE,"E6.18.1"),sQuery(id+"F0.wireOp",EDGE,"E6.18.2"),sQuery(id+"F0.wireOp",EDGE,"E6.18.3"),sQuery(id+"F0.wireOp",EDGE,"E6.18.4"),sQuery(id+"F0.wireOp",EDGE,"E6.19.1"),sQuery(id+"F0.wireOp",EDGE,"E6.19.2"),sQuery(id+"F0.wireOp",EDGE,"E6.19.3"),sQuery(id+"F0.wireOp",EDGE,"E6.19.4"),sQuery(id+"F0.wireOp",EDGE,"E6.20.1"),sQuery(id+"F0.wireOp",EDGE,"E6.20.2"),sQuery(id+"F0.wireOp",EDGE,"E6.20.3"),sQuery(id+"F0.wireOp",EDGE,"E6.20.4"),sQuery(id+"F0.wireOp",EDGE,"E6.21.1"),sQuery(id+"F0.wireOp",EDGE,"E6.21.2"),sQuery(id+"F0.wireOp",EDGE,"E6.21.3"),sQuery(id+"F0.wireOp",EDGE,"E6.21.4"),sQuery(id+"F0.wireOp",EDGE,"E6.22.1"),sQuery(id+"F0.wireOp",EDGE,"E6.22.2"),sQuery(id+"F0.wireOp",EDGE,"E6.22.3"),sQuery(id+"F0.wireOp",EDGE,"E6.22.4"),sQuery(id+"F0.wireOp",EDGE,"E6.23.1"),sQuery(id+"F0.wireOp",EDGE,"E6.23.2"),sQuery(id+"F0.wireOp",EDGE,"E6.23.3"),sQuery(id+"F0.wireOp",EDGE,"E6.23.4"),sQuery(id+"F0.wireOp",EDGE,"E6.24.1"),sQuery(id+"F0.wireOp",EDGE,"E6.24.2"),sQuery(id+"F0.wireOp",EDGE,"E6.24.3"),sQuery(id+"F0.wireOp",EDGE,"E6.24.4"),sQuery(id+"F0.wireOp",EDGE,"E6.25.1"),sQuery(id+"F0.wireOp",EDGE,"E6.25.2"),sQuery(id+"F0.wireOp",EDGE,"E6.25.3"),sQuery(id+"F0.wireOp",EDGE,"E6.25.4"),sQuery(id+"F0.wireOp",EDGE,"E6.26.1"),sQuery(id+"F0.wireOp",EDGE,"E6.26.2"),sQuery(id+"F0.wireOp",EDGE,"E6.26.3"),sQuery(id+"F0.wireOp",EDGE,"E6.26.4"),sQuery(id+"F0.wireOp",EDGE,"E6.27.1"),sQuery(id+"F0.wireOp",EDGE,"E6.27.2"),sQuery(id+"F0.wireOp",EDGE,"E6.27.3"),sQuery(id+"F0.wireOp",EDGE,"E6.27.4"),sQuery(id+"F0.wireOp",EDGE,"E6.28.1"),sQuery(id+"F0.wireOp",EDGE,"E6.28.2"),sQuery(id+"F0.wireOp",EDGE,"E6.28.3"),sQuery(id+"F0.wireOp",EDGE,"E6.28.4"),sQuery(id+"F0.wireOp",EDGE,"E6.29.1"),sQuery(id+"F0.wireOp",EDGE,"E6.29.2"),sQuery(id+"F0.wireOp",EDGE,"E6.29.3"),sQuery(id+"F0.wireOp",EDGE,"E6.29.4"),sQuery(id+"F0.wireOp",EDGE,"E6.30.1"),sQuery(id+"F0.wireOp",EDGE,"E6.30.2"),sQuery(id+"F0.wireOp",EDGE,"E6.30.3"),sQuery(id+"F0.wireOp",EDGE,"E6.30.4"),sQuery(id+"F0.wireOp",EDGE,"E6.31.1"),sQuery(id+"F0.wireOp",EDGE,"E6.31.2"),sQuery(id+"F0.wireOp",EDGE,"E6.31.3"),sQuery(id+"F0.wireOp",EDGE,"E6.31.4"),sQuery(id+"F0.wireOp",EDGE,"E6.32.1"),sQuery(id+"F0.wireOp",EDGE,"E6.32.2"),sQuery(id+"F0.wireOp",EDGE,"E6.32.3"),sQuery(id+"F0.wireOp",EDGE,"E6.32.4"),sQuery(id+"F0.wireOp",EDGE,"E6.33.1"),sQuery(id+"F0.wireOp",EDGE,"E6.33.2"),sQuery(id+"F0.wireOp",EDGE,"E6.33.3"),sQuery(id+"F0.wireOp",EDGE,"E6.33.4"),sQuery(id+"F0.wireOp",EDGE,"E6.34.1"),sQuery(id+"F0.wireOp",EDGE,"E6.34.2"),sQuery(id+"F0.wireOp",EDGE,"E6.34.3"),sQuery(id+"F0.wireOp",EDGE,"E6.34.4"),sQuery(id+"F0.wireOp",EDGE,"E6.35.1"),sQuery(id+"F0.wireOp",EDGE,"E6.35.2"),sQuery(id+"F0.wireOp",EDGE,"E6.35.3"),sQuery(id+"F0.wireOp",EDGE,"E6.35.4"),sQuery(id+"F0.wireOp",EDGE,"E6.36.1"),sQuery(id+"F0.wireOp",EDGE,"E6.36.2"),sQuery(id+"F0.wireOp",EDGE,"E6.36.3"),sQuery(id+"F0.wireOp",EDGE,"E6.36.4"),sQuery(id+"F0.wireOp",EDGE,"E6.37.1"),sQuery(id+"F0.wireOp",EDGE,"E6.37.2"),sQuery(id+"F0.wireOp",EDGE,"E6.37.3"),sQuery(id+"F0.wireOp",EDGE,"E6.37.4"),sQuery(id+"F0.wireOp",EDGE,"E6.38.1"),sQuery(id+"F0.wireOp",EDGE,"E6.38.2"),sQuery(id+"F0.wireOp",EDGE,"E6.38.3"),sQuery(id+"F0.wireOp",EDGE,"E6.38.4"),sQuery(id+"F0.wireOp",EDGE,"E6.39.1"),sQuery(id+"F0.wireOp",EDGE,"E6.39.2"),sQuery(id+"F0.wireOp",EDGE,"E6.39.3"),sQuery(id+"F0.wireOp",EDGE,"E6.39.4"),sQuery(id+"F0.wireOp",EDGE,"E6.40.1"),sQuery(id+"F0.wireOp",EDGE,"E6.40.2"),sQuery(id+"F0.wireOp",EDGE,"E6.40.3"),sQuery(id+"F0.wireOp",EDGE,"E6.40.4"),sQuery(id+"F0.wireOp",EDGE,"E6.41.1"),sQuery(id+"F0.wireOp",EDGE,"E6.41.2"),sQuery(id+"F0.wireOp",EDGE,"E6.41.3"),sQuery(id+"F0.wireOp",EDGE,"E6.41.4"),sQuery(id+"F0.wireOp",EDGE,"E6.42.1"),sQuery(id+"F0.wireOp",EDGE,"E6.42.2"),sQuery(id+"F0.wireOp",EDGE,"E6.42.3"),sQuery(id+"F0.wireOp",EDGE,"E6.42.4"),sQuery(id+"F0.wireOp",EDGE,"E6.43.1"),sQuery(id+"F0.wireOp",EDGE,"E6.43.2"),sQuery(id+"F0.wireOp",EDGE,"E6.43.3"),sQuery(id+"F0.wireOp",EDGE,"E6.43.4"),sQuery(id+"F0.wireOp",EDGE,"E7"),sQuery(id+"F0.wireOp",EDGE,"E8.1.0"),sQuery(id+"F0.wireOp",EDGE,"E8.2.0"),sQuery(id+"F0.wireOp",EDGE,"E8.3.0"),sQuery(id+"F0.wireOp",EDGE,"E8.4.0"),sQuery(id+"F0.wireOp",EDGE,"E8.5.0"),sQuery(id+"F0.wireOp",EDGE,"E8.6.0"),sQuery(id+"F0.wireOp",EDGE,"E8.7.0"),sQuery(id+"F0.wireOp",EDGE,"E8.8.0"),sQuery(id+"F0.wireOp",EDGE,"E8.9.0"),sQuery(id+"F0.wireOp",EDGE,"E8.10.0"),sQuery(id+"F0.wireOp",EDGE,"E8.11.0"),sQuery(id+"F0.wireOp",EDGE,"E8.12.0"),sQuery(id+"F0.wireOp",EDGE,"E8.13.0"),sQuery(id+"F0.wireOp",EDGE,"E8.14.0"),sQuery(id+"F0.wireOp",EDGE,"E8.15.0"),sQuery(id+"F0.wireOp",EDGE,"E8.16.0"),sQuery(id+"F0.wireOp",EDGE,"E8.17.0"),sQuery(id+"F0.wireOp",EDGE,"E8.18.0"),sQuery(id+"F0.wireOp",EDGE,"E8.19.0"),sQuery(id+"F0.wireOp",EDGE,"E8.20.0"),sQuery(id+"F0.wireOp",EDGE,"E8.21.0"),sQuery(id+"F0.wireOp",EDGE,"E8.22.0"),sQuery(id+"F0.wireOp",EDGE,"E8.23.0"),sQuery(id+"F0.wireOp",EDGE,"E8.24.0"),sQuery(id+"F0.wireOp",EDGE,"E8.25.0"),sQuery(id+"F0.wireOp",EDGE,"E8.26.0"),sQuery(id+"F0.wireOp",EDGE,"E8.27.0"),sQuery(id+"F0.wireOp",EDGE,"E8.28.0"),sQuery(id+"F0.wireOp",EDGE,"E8.29.0"),sQuery(id+"F0.wireOp",EDGE,"E8.30.0"),sQuery(id+"F0.wireOp",EDGE,"E8.31.0"),sQuery(id+"F0.wireOp",EDGE,"E8.32.0"),sQuery(id+"F0.wireOp",EDGE,"E8.33.0"),sQuery(id+"F0.wireOp",EDGE,"E8.34.0"),sQuery(id+"F0.wireOp",EDGE,"E8.35.0"),sQuery(id+"F0.wireOp",EDGE,"E8.36.0"),sQuery(id+"F0.wireOp",EDGE,"E8.37.0"),sQuery(id+"F0.wireOp",EDGE,"E8.38.0"),sQuery(id+"F0.wireOp",EDGE,"E8.39.0"),sQuery(id+"F0.wireOp",EDGE,"E8.40.0"),sQuery(id+"F0.wireOp",EDGE,"E8.41.0"),sQuery(id+"F0.wireOp",EDGE,"E8.42.0"),sQuery(id+"F0.wireOp",EDGE,"E8.43.0")])],"isStart":true})]});}
            var Q25;
            {var subQ0=sQuery(id+"F0.wireOp",EDGE,"E6.6.3");var subQ1=sQuery(id+"F0.wireOp",EDGE,"E6.6.1");Q25=makeQuery(id+"F2.opFillet","BLEND_EDGE",EDGE,{"blendedFrom":[makeQuery(id+"F1.opExtrude","SWEPT_EDGE",EDGE,{"disambiguationData":[OSD([sQuery(id+"F0.wireOp",EDGE,"E6.6.0"),subQ1,subQ0])]}),makeQuery(id+"F1.opExtrude","CAP_FACE",FACE,{"disambiguationData":[OSD([sQuery(id+"F0.wireOp",EDGE,"E0"),sQuery(id+"F0.wireOp",EDGE,"E1"),sQuery(id+"F0.wireOp",EDGE,"E2"),sQuery(id+"F0.wireOp",EDGE,"E4"),sQuery(id+"F0.wireOp",EDGE,"E5"),sQuery(id+"F0.wireOp",EDGE,"E6.1.1"),sQuery(id+"F0.wireOp",EDGE,"E6.1.2"),sQuery(id+"F0.wireOp",EDGE,"E6.1.3"),sQuery(id+"F0.wireOp",EDGE,"E6.1.4"),sQuery(id+"F0.wireOp",EDGE,"E6.2.1"),sQuery(id+"F0.wireOp",EDGE,"E6.2.2"),sQuery(id+"F0.wireOp",EDGE,"E6.2.3"),sQuery(id+"F0.wireOp",EDGE,"E6.2.4"),sQuery(id+"F0.wireOp",EDGE,"E6.3.1"),sQuery(id+"F0.wireOp",EDGE,"E6.3.2"),sQuery(id+"F0.wireOp",EDGE,"E6.3.3"),sQuery(id+"F0.wireOp",EDGE,"E6.3.4"),sQuery(id+"F0.wireOp",EDGE,"E6.4.1"),sQuery(id+"F0.wireOp",EDGE,"E6.4.2"),sQuery(id+"F0.wireOp",EDGE,"E6.4.3"),sQuery(id+"F0.wireOp",EDGE,"E6.4.4"),sQuery(id+"F0.wireOp",EDGE,"E6.5.1"),sQuery(id+"F0.wireOp",EDGE,"E6.5.2"),sQuery(id+"F0.wireOp",EDGE,"E6.5.3"),sQuery(id+"F0.wireOp",EDGE,"E6.5.4"),subQ1,sQuery(id+"F0.wireOp",EDGE,"E6.6.2"),subQ0,sQuery(id+"F0.wireOp",EDGE,"E6.6.4"),sQuery(id+"F0.wireOp",EDGE,"E6.7.1"),sQuery(id+"F0.wireOp",EDGE,"E6.7.2"),sQuery(id+"F0.wireOp",EDGE,"E6.7.3"),sQuery(id+"F0.wireOp",EDGE,"E6.7.4"),sQuery(id+"F0.wireOp",EDGE,"E6.8.1"),sQuery(id+"F0.wireOp",EDGE,"E6.8.2"),sQuery(id+"F0.wireOp",EDGE,"E6.8.3"),sQuery(id+"F0.wireOp",EDGE,"E6.8.4"),sQuery(id+"F0.wireOp",EDGE,"E6.9.1"),sQuery(id+"F0.wireOp",EDGE,"E6.9.2"),sQuery(id+"F0.wireOp",EDGE,"E6.9.3"),sQuery(id+"F0.wireOp",EDGE,"E6.9.4"),sQuery(id+"F0.wireOp",EDGE,"E6.10.1"),sQuery(id+"F0.wireOp",EDGE,"E6.10.2"),sQuery(id+"F0.wireOp",EDGE,"E6.10.3"),sQuery(id+"F0.wireOp",EDGE,"E6.10.4"),sQuery(id+"F0.wireOp",EDGE,"E6.11.1"),sQuery(id+"F0.wireOp",EDGE,"E6.11.2"),sQuery(id+"F0.wireOp",EDGE,"E6.11.3"),sQuery(id+"F0.wireOp",EDGE,"E6.11.4"),sQuery(id+"F0.wireOp",EDGE,"E6.12.1"),sQuery(id+"F0.wireOp",EDGE,"E6.12.2"),sQuery(id+"F0.wireOp",EDGE,"E6.12.3"),sQuery(id+"F0.wireOp",EDGE,"E6.12.4"),sQuery(id+"F0.wireOp",EDGE,"E6.13.1"),sQuery(id+"F0.wireOp",EDGE,"E6.13.2"),sQuery(id+"F0.wireOp",EDGE,"E6.13.3"),sQuery(id+"F0.wireOp",EDGE,"E6.13.4"),sQuery(id+"F0.wireOp",EDGE,"E6.14.1"),sQuery(id+"F0.wireOp",EDGE,"E6.14.2"),sQuery(id+"F0.wireOp",EDGE,"E6.14.3"),sQuery(id+"F0.wireOp",EDGE,"E6.14.4"),sQuery(id+"F0.wireOp",EDGE,"E6.15.1"),sQuery(id+"F0.wireOp",EDGE,"E6.15.2"),sQuery(id+"F0.wireOp",EDGE,"E6.15.3"),sQuery(id+"F0.wireOp",EDGE,"E6.15.4"),sQuery(id+"F0.wireOp",EDGE,"E6.16.1"),sQuery(id+"F0.wireOp",EDGE,"E6.16.2"),sQuery(id+"F0.wireOp",EDGE,"E6.16.3"),sQuery(id+"F0.wireOp",EDGE,"E6.16.4"),sQuery(id+"F0.wireOp",EDGE,"E6.17.1"),sQuery(id+"F0.wireOp",EDGE,"E6.17.2"),sQuery(id+"F0.wireOp",EDGE,"E6.17.3"),sQuery(id+"F0.wireOp",EDGE,"E6.17.4"),sQuery(id+"F0.wireOp",EDGE,"E6.18.1"),sQuery(id+"F0.wireOp",EDGE,"E6.18.2"),sQuery(id+"F0.wireOp",EDGE,"E6.18.3"),sQuery(id+"F0.wireOp",EDGE,"E6.18.4"),sQuery(id+"F0.wireOp",EDGE,"E6.19.1"),sQuery(id+"F0.wireOp",EDGE,"E6.19.2"),sQuery(id+"F0.wireOp",EDGE,"E6.19.3"),sQuery(id+"F0.wireOp",EDGE,"E6.19.4"),sQuery(id+"F0.wireOp",EDGE,"E6.20.1"),sQuery(id+"F0.wireOp",EDGE,"E6.20.2"),sQuery(id+"F0.wireOp",EDGE,"E6.20.3"),sQuery(id+"F0.wireOp",EDGE,"E6.20.4"),sQuery(id+"F0.wireOp",EDGE,"E6.21.1"),sQuery(id+"F0.wireOp",EDGE,"E6.21.2"),sQuery(id+"F0.wireOp",EDGE,"E6.21.3"),sQuery(id+"F0.wireOp",EDGE,"E6.21.4"),sQuery(id+"F0.wireOp",EDGE,"E6.22.1"),sQuery(id+"F0.wireOp",EDGE,"E6.22.2"),sQuery(id+"F0.wireOp",EDGE,"E6.22.3"),sQuery(id+"F0.wireOp",EDGE,"E6.22.4"),sQuery(id+"F0.wireOp",EDGE,"E6.23.1"),sQuery(id+"F0.wireOp",EDGE,"E6.23.2"),sQuery(id+"F0.wireOp",EDGE,"E6.23.3"),sQuery(id+"F0.wireOp",EDGE,"E6.23.4"),sQuery(id+"F0.wireOp",EDGE,"E6.24.1"),sQuery(id+"F0.wireOp",EDGE,"E6.24.2"),sQuery(id+"F0.wireOp",EDGE,"E6.24.3"),sQuery(id+"F0.wireOp",EDGE,"E6.24.4"),sQuery(id+"F0.wireOp",EDGE,"E6.25.1"),sQuery(id+"F0.wireOp",EDGE,"E6.25.2"),sQuery(id+"F0.wireOp",EDGE,"E6.25.3"),sQuery(id+"F0.wireOp",EDGE,"E6.25.4"),sQuery(id+"F0.wireOp",EDGE,"E6.26.1"),sQuery(id+"F0.wireOp",EDGE,"E6.26.2"),sQuery(id+"F0.wireOp",EDGE,"E6.26.3"),sQuery(id+"F0.wireOp",EDGE,"E6.26.4"),sQuery(id+"F0.wireOp",EDGE,"E6.27.1"),sQuery(id+"F0.wireOp",EDGE,"E6.27.2"),sQuery(id+"F0.wireOp",EDGE,"E6.27.3"),sQuery(id+"F0.wireOp",EDGE,"E6.27.4"),sQuery(id+"F0.wireOp",EDGE,"E6.28.1"),sQuery(id+"F0.wireOp",EDGE,"E6.28.2"),sQuery(id+"F0.wireOp",EDGE,"E6.28.3"),sQuery(id+"F0.wireOp",EDGE,"E6.28.4"),sQuery(id+"F0.wireOp",EDGE,"E6.29.1"),sQuery(id+"F0.wireOp",EDGE,"E6.29.2"),sQuery(id+"F0.wireOp",EDGE,"E6.29.3"),sQuery(id+"F0.wireOp",EDGE,"E6.29.4"),sQuery(id+"F0.wireOp",EDGE,"E6.30.1"),sQuery(id+"F0.wireOp",EDGE,"E6.30.2"),sQuery(id+"F0.wireOp",EDGE,"E6.30.3"),sQuery(id+"F0.wireOp",EDGE,"E6.30.4"),sQuery(id+"F0.wireOp",EDGE,"E6.31.1"),sQuery(id+"F0.wireOp",EDGE,"E6.31.2"),sQuery(id+"F0.wireOp",EDGE,"E6.31.3"),sQuery(id+"F0.wireOp",EDGE,"E6.31.4"),sQuery(id+"F0.wireOp",EDGE,"E6.32.1"),sQuery(id+"F0.wireOp",EDGE,"E6.32.2"),sQuery(id+"F0.wireOp",EDGE,"E6.32.3"),sQuery(id+"F0.wireOp",EDGE,"E6.32.4"),sQuery(id+"F0.wireOp",EDGE,"E6.33.1"),sQuery(id+"F0.wireOp",EDGE,"E6.33.2"),sQuery(id+"F0.wireOp",EDGE,"E6.33.3"),sQuery(id+"F0.wireOp",EDGE,"E6.33.4"),sQuery(id+"F0.wireOp",EDGE,"E6.34.1"),sQuery(id+"F0.wireOp",EDGE,"E6.34.2"),sQuery(id+"F0.wireOp",EDGE,"E6.34.3"),sQuery(id+"F0.wireOp",EDGE,"E6.34.4"),sQuery(id+"F0.wireOp",EDGE,"E6.35.1"),sQuery(id+"F0.wireOp",EDGE,"E6.35.2"),sQuery(id+"F0.wireOp",EDGE,"E6.35.3"),sQuery(id+"F0.wireOp",EDGE,"E6.35.4"),sQuery(id+"F0.wireOp",EDGE,"E6.36.1"),sQuery(id+"F0.wireOp",EDGE,"E6.36.2"),sQuery(id+"F0.wireOp",EDGE,"E6.36.3"),sQuery(id+"F0.wireOp",EDGE,"E6.36.4"),sQuery(id+"F0.wireOp",EDGE,"E6.37.1"),sQuery(id+"F0.wireOp",EDGE,"E6.37.2"),sQuery(id+"F0.wireOp",EDGE,"E6.37.3"),sQuery(id+"F0.wireOp",EDGE,"E6.37.4"),sQuery(id+"F0.wireOp",EDGE,"E6.38.1"),sQuery(id+"F0.wireOp",EDGE,"E6.38.2"),sQuery(id+"F0.wireOp",EDGE,"E6.38.3"),sQuery(id+"F0.wireOp",EDGE,"E6.38.4"),sQuery(id+"F0.wireOp",EDGE,"E6.39.1"),sQuery(id+"F0.wireOp",EDGE,"E6.39.2"),sQuery(id+"F0.wireOp",EDGE,"E6.39.3"),sQuery(id+"F0.wireOp",EDGE,"E6.39.4"),sQuery(id+"F0.wireOp",EDGE,"E6.40.1"),sQuery(id+"F0.wireOp",EDGE,"E6.40.2"),sQuery(id+"F0.wireOp",EDGE,"E6.40.3"),sQuery(id+"F0.wireOp",EDGE,"E6.40.4"),sQuery(id+"F0.wireOp",EDGE,"E6.41.1"),sQuery(id+"F0.wireOp",EDGE,"E6.41.2"),sQuery(id+"F0.wireOp",EDGE,"E6.41.3"),sQuery(id+"F0.wireOp",EDGE,"E6.41.4"),sQuery(id+"F0.wireOp",EDGE,"E6.42.1"),sQuery(id+"F0.wireOp",EDGE,"E6.42.2"),sQuery(id+"F0.wireOp",EDGE,"E6.42.3"),sQuery(id+"F0.wireOp",EDGE,"E6.42.4"),sQuery(id+"F0.wireOp",EDGE,"E6.43.1"),sQuery(id+"F0.wireOp",EDGE,"E6.43.2"),sQuery(id+"F0.wireOp",EDGE,"E6.43.3"),sQuery(id+"F0.wireOp",EDGE,"E6.43.4"),sQuery(id+"F0.wireOp",EDGE,"E7"),sQuery(id+"F0.wireOp",EDGE,"E8.1.0"),sQuery(id+"F0.wireOp",EDGE,"E8.2.0"),sQuery(id+"F0.wireOp",EDGE,"E8.3.0"),sQuery(id+"F0.wireOp",EDGE,"E8.4.0"),sQuery(id+"F0.wireOp",EDGE,"E8.5.0"),sQuery(id+"F0.wireOp",EDGE,"E8.6.0"),sQuery(id+"F0.wireOp",EDGE,"E8.7.0"),sQuery(id+"F0.wireOp",EDGE,"E8.8.0"),sQuery(id+"F0.wireOp",EDGE,"E8.9.0"),sQuery(id+"F0.wireOp",EDGE,"E8.10.0"),sQuery(id+"F0.wireOp",EDGE,"E8.11.0"),sQuery(id+"F0.wireOp",EDGE,"E8.12.0"),sQuery(id+"F0.wireOp",EDGE,"E8.13.0"),sQuery(id+"F0.wireOp",EDGE,"E8.14.0"),sQuery(id+"F0.wireOp",EDGE,"E8.15.0"),sQuery(id+"F0.wireOp",EDGE,"E8.16.0"),sQuery(id+"F0.wireOp",EDGE,"E8.17.0"),sQuery(id+"F0.wireOp",EDGE,"E8.18.0"),sQuery(id+"F0.wireOp",EDGE,"E8.19.0"),sQuery(id+"F0.wireOp",EDGE,"E8.20.0"),sQuery(id+"F0.wireOp",EDGE,"E8.21.0"),sQuery(id+"F0.wireOp",EDGE,"E8.22.0"),sQuery(id+"F0.wireOp",EDGE,"E8.23.0"),sQuery(id+"F0.wireOp",EDGE,"E8.24.0"),sQuery(id+"F0.wireOp",EDGE,"E8.25.0"),sQuery(id+"F0.wireOp",EDGE,"E8.26.0"),sQuery(id+"F0.wireOp",EDGE,"E8.27.0"),sQuery(id+"F0.wireOp",EDGE,"E8.28.0"),sQuery(id+"F0.wireOp",EDGE,"E8.29.0"),sQuery(id+"F0.wireOp",EDGE,"E8.30.0"),sQuery(id+"F0.wireOp",EDGE,"E8.31.0"),sQuery(id+"F0.wireOp",EDGE,"E8.32.0"),sQuery(id+"F0.wireOp",EDGE,"E8.33.0"),sQuery(id+"F0.wireOp",EDGE,"E8.34.0"),sQuery(id+"F0.wireOp",EDGE,"E8.35.0"),sQuery(id+"F0.wireOp",EDGE,"E8.36.0"),sQuery(id+"F0.wireOp",EDGE,"E8.37.0"),sQuery(id+"F0.wireOp",EDGE,"E8.38.0"),sQuery(id+"F0.wireOp",EDGE,"E8.39.0"),sQuery(id+"F0.wireOp",EDGE,"E8.40.0"),sQuery(id+"F0.wireOp",EDGE,"E8.41.0"),sQuery(id+"F0.wireOp",EDGE,"E8.42.0"),sQuery(id+"F0.wireOp",EDGE,"E8.43.0")])],"isStart":true})],"blendedInto":[makeQuery(id+"F1.opExtrude","CAP_FACE",FACE,{"disambiguationData":[OSD([sQuery(id+"F0.wireOp",EDGE,"E0"),sQuery(id+"F0.wireOp",EDGE,"E1"),sQuery(id+"F0.wireOp",EDGE,"E2"),sQuery(id+"F0.wireOp",EDGE,"E4"),sQuery(id+"F0.wireOp",EDGE,"E5"),sQuery(id+"F0.wireOp",EDGE,"E6.1.1"),sQuery(id+"F0.wireOp",EDGE,"E6.1.2"),sQuery(id+"F0.wireOp",EDGE,"E6.1.3"),sQuery(id+"F0.wireOp",EDGE,"E6.1.4"),sQuery(id+"F0.wireOp",EDGE,"E6.2.1"),sQuery(id+"F0.wireOp",EDGE,"E6.2.2"),sQuery(id+"F0.wireOp",EDGE,"E6.2.3"),sQuery(id+"F0.wireOp",EDGE,"E6.2.4"),sQuery(id+"F0.wireOp",EDGE,"E6.3.1"),sQuery(id+"F0.wireOp",EDGE,"E6.3.2"),sQuery(id+"F0.wireOp",EDGE,"E6.3.3"),sQuery(id+"F0.wireOp",EDGE,"E6.3.4"),sQuery(id+"F0.wireOp",EDGE,"E6.4.1"),sQuery(id+"F0.wireOp",EDGE,"E6.4.2"),sQuery(id+"F0.wireOp",EDGE,"E6.4.3"),sQuery(id+"F0.wireOp",EDGE,"E6.4.4"),sQuery(id+"F0.wireOp",EDGE,"E6.5.1"),sQuery(id+"F0.wireOp",EDGE,"E6.5.2"),sQuery(id+"F0.wireOp",EDGE,"E6.5.3"),sQuery(id+"F0.wireOp",EDGE,"E6.5.4"),subQ1,sQuery(id+"F0.wireOp",EDGE,"E6.6.2"),subQ0,sQuery(id+"F0.wireOp",EDGE,"E6.6.4"),sQuery(id+"F0.wireOp",EDGE,"E6.7.1"),sQuery(id+"F0.wireOp",EDGE,"E6.7.2"),sQuery(id+"F0.wireOp",EDGE,"E6.7.3"),sQuery(id+"F0.wireOp",EDGE,"E6.7.4"),sQuery(id+"F0.wireOp",EDGE,"E6.8.1"),sQuery(id+"F0.wireOp",EDGE,"E6.8.2"),sQuery(id+"F0.wireOp",EDGE,"E6.8.3"),sQuery(id+"F0.wireOp",EDGE,"E6.8.4"),sQuery(id+"F0.wireOp",EDGE,"E6.9.1"),sQuery(id+"F0.wireOp",EDGE,"E6.9.2"),sQuery(id+"F0.wireOp",EDGE,"E6.9.3"),sQuery(id+"F0.wireOp",EDGE,"E6.9.4"),sQuery(id+"F0.wireOp",EDGE,"E6.10.1"),sQuery(id+"F0.wireOp",EDGE,"E6.10.2"),sQuery(id+"F0.wireOp",EDGE,"E6.10.3"),sQuery(id+"F0.wireOp",EDGE,"E6.10.4"),sQuery(id+"F0.wireOp",EDGE,"E6.11.1"),sQuery(id+"F0.wireOp",EDGE,"E6.11.2"),sQuery(id+"F0.wireOp",EDGE,"E6.11.3"),sQuery(id+"F0.wireOp",EDGE,"E6.11.4"),sQuery(id+"F0.wireOp",EDGE,"E6.12.1"),sQuery(id+"F0.wireOp",EDGE,"E6.12.2"),sQuery(id+"F0.wireOp",EDGE,"E6.12.3"),sQuery(id+"F0.wireOp",EDGE,"E6.12.4"),sQuery(id+"F0.wireOp",EDGE,"E6.13.1"),sQuery(id+"F0.wireOp",EDGE,"E6.13.2"),sQuery(id+"F0.wireOp",EDGE,"E6.13.3"),sQuery(id+"F0.wireOp",EDGE,"E6.13.4"),sQuery(id+"F0.wireOp",EDGE,"E6.14.1"),sQuery(id+"F0.wireOp",EDGE,"E6.14.2"),sQuery(id+"F0.wireOp",EDGE,"E6.14.3"),sQuery(id+"F0.wireOp",EDGE,"E6.14.4"),sQuery(id+"F0.wireOp",EDGE,"E6.15.1"),sQuery(id+"F0.wireOp",EDGE,"E6.15.2"),sQuery(id+"F0.wireOp",EDGE,"E6.15.3"),sQuery(id+"F0.wireOp",EDGE,"E6.15.4"),sQuery(id+"F0.wireOp",EDGE,"E6.16.1"),sQuery(id+"F0.wireOp",EDGE,"E6.16.2"),sQuery(id+"F0.wireOp",EDGE,"E6.16.3"),sQuery(id+"F0.wireOp",EDGE,"E6.16.4"),sQuery(id+"F0.wireOp",EDGE,"E6.17.1"),sQuery(id+"F0.wireOp",EDGE,"E6.17.2"),sQuery(id+"F0.wireOp",EDGE,"E6.17.3"),sQuery(id+"F0.wireOp",EDGE,"E6.17.4"),sQuery(id+"F0.wireOp",EDGE,"E6.18.1"),sQuery(id+"F0.wireOp",EDGE,"E6.18.2"),sQuery(id+"F0.wireOp",EDGE,"E6.18.3"),sQuery(id+"F0.wireOp",EDGE,"E6.18.4"),sQuery(id+"F0.wireOp",EDGE,"E6.19.1"),sQuery(id+"F0.wireOp",EDGE,"E6.19.2"),sQuery(id+"F0.wireOp",EDGE,"E6.19.3"),sQuery(id+"F0.wireOp",EDGE,"E6.19.4"),sQuery(id+"F0.wireOp",EDGE,"E6.20.1"),sQuery(id+"F0.wireOp",EDGE,"E6.20.2"),sQuery(id+"F0.wireOp",EDGE,"E6.20.3"),sQuery(id+"F0.wireOp",EDGE,"E6.20.4"),sQuery(id+"F0.wireOp",EDGE,"E6.21.1"),sQuery(id+"F0.wireOp",EDGE,"E6.21.2"),sQuery(id+"F0.wireOp",EDGE,"E6.21.3"),sQuery(id+"F0.wireOp",EDGE,"E6.21.4"),sQuery(id+"F0.wireOp",EDGE,"E6.22.1"),sQuery(id+"F0.wireOp",EDGE,"E6.22.2"),sQuery(id+"F0.wireOp",EDGE,"E6.22.3"),sQuery(id+"F0.wireOp",EDGE,"E6.22.4"),sQuery(id+"F0.wireOp",EDGE,"E6.23.1"),sQuery(id+"F0.wireOp",EDGE,"E6.23.2"),sQuery(id+"F0.wireOp",EDGE,"E6.23.3"),sQuery(id+"F0.wireOp",EDGE,"E6.23.4"),sQuery(id+"F0.wireOp",EDGE,"E6.24.1"),sQuery(id+"F0.wireOp",EDGE,"E6.24.2"),sQuery(id+"F0.wireOp",EDGE,"E6.24.3"),sQuery(id+"F0.wireOp",EDGE,"E6.24.4"),sQuery(id+"F0.wireOp",EDGE,"E6.25.1"),sQuery(id+"F0.wireOp",EDGE,"E6.25.2"),sQuery(id+"F0.wireOp",EDGE,"E6.25.3"),sQuery(id+"F0.wireOp",EDGE,"E6.25.4"),sQuery(id+"F0.wireOp",EDGE,"E6.26.1"),sQuery(id+"F0.wireOp",EDGE,"E6.26.2"),sQuery(id+"F0.wireOp",EDGE,"E6.26.3"),sQuery(id+"F0.wireOp",EDGE,"E6.26.4"),sQuery(id+"F0.wireOp",EDGE,"E6.27.1"),sQuery(id+"F0.wireOp",EDGE,"E6.27.2"),sQuery(id+"F0.wireOp",EDGE,"E6.27.3"),sQuery(id+"F0.wireOp",EDGE,"E6.27.4"),sQuery(id+"F0.wireOp",EDGE,"E6.28.1"),sQuery(id+"F0.wireOp",EDGE,"E6.28.2"),sQuery(id+"F0.wireOp",EDGE,"E6.28.3"),sQuery(id+"F0.wireOp",EDGE,"E6.28.4"),sQuery(id+"F0.wireOp",EDGE,"E6.29.1"),sQuery(id+"F0.wireOp",EDGE,"E6.29.2"),sQuery(id+"F0.wireOp",EDGE,"E6.29.3"),sQuery(id+"F0.wireOp",EDGE,"E6.29.4"),sQuery(id+"F0.wireOp",EDGE,"E6.30.1"),sQuery(id+"F0.wireOp",EDGE,"E6.30.2"),sQuery(id+"F0.wireOp",EDGE,"E6.30.3"),sQuery(id+"F0.wireOp",EDGE,"E6.30.4"),sQuery(id+"F0.wireOp",EDGE,"E6.31.1"),sQuery(id+"F0.wireOp",EDGE,"E6.31.2"),sQuery(id+"F0.wireOp",EDGE,"E6.31.3"),sQuery(id+"F0.wireOp",EDGE,"E6.31.4"),sQuery(id+"F0.wireOp",EDGE,"E6.32.1"),sQuery(id+"F0.wireOp",EDGE,"E6.32.2"),sQuery(id+"F0.wireOp",EDGE,"E6.32.3"),sQuery(id+"F0.wireOp",EDGE,"E6.32.4"),sQuery(id+"F0.wireOp",EDGE,"E6.33.1"),sQuery(id+"F0.wireOp",EDGE,"E6.33.2"),sQuery(id+"F0.wireOp",EDGE,"E6.33.3"),sQuery(id+"F0.wireOp",EDGE,"E6.33.4"),sQuery(id+"F0.wireOp",EDGE,"E6.34.1"),sQuery(id+"F0.wireOp",EDGE,"E6.34.2"),sQuery(id+"F0.wireOp",EDGE,"E6.34.3"),sQuery(id+"F0.wireOp",EDGE,"E6.34.4"),sQuery(id+"F0.wireOp",EDGE,"E6.35.1"),sQuery(id+"F0.wireOp",EDGE,"E6.35.2"),sQuery(id+"F0.wireOp",EDGE,"E6.35.3"),sQuery(id+"F0.wireOp",EDGE,"E6.35.4"),sQuery(id+"F0.wireOp",EDGE,"E6.36.1"),sQuery(id+"F0.wireOp",EDGE,"E6.36.2"),sQuery(id+"F0.wireOp",EDGE,"E6.36.3"),sQuery(id+"F0.wireOp",EDGE,"E6.36.4"),sQuery(id+"F0.wireOp",EDGE,"E6.37.1"),sQuery(id+"F0.wireOp",EDGE,"E6.37.2"),sQuery(id+"F0.wireOp",EDGE,"E6.37.3"),sQuery(id+"F0.wireOp",EDGE,"E6.37.4"),sQuery(id+"F0.wireOp",EDGE,"E6.38.1"),sQuery(id+"F0.wireOp",EDGE,"E6.38.2"),sQuery(id+"F0.wireOp",EDGE,"E6.38.3"),sQuery(id+"F0.wireOp",EDGE,"E6.38.4"),sQuery(id+"F0.wireOp",EDGE,"E6.39.1"),sQuery(id+"F0.wireOp",EDGE,"E6.39.2"),sQuery(id+"F0.wireOp",EDGE,"E6.39.3"),sQuery(id+"F0.wireOp",EDGE,"E6.39.4"),sQuery(id+"F0.wireOp",EDGE,"E6.40.1"),sQuery(id+"F0.wireOp",EDGE,"E6.40.2"),sQuery(id+"F0.wireOp",EDGE,"E6.40.3"),sQuery(id+"F0.wireOp",EDGE,"E6.40.4"),sQuery(id+"F0.wireOp",EDGE,"E6.41.1"),sQuery(id+"F0.wireOp",EDGE,"E6.41.2"),sQuery(id+"F0.wireOp",EDGE,"E6.41.3"),sQuery(id+"F0.wireOp",EDGE,"E6.41.4"),sQuery(id+"F0.wireOp",EDGE,"E6.42.1"),sQuery(id+"F0.wireOp",EDGE,"E6.42.2"),sQuery(id+"F0.wireOp",EDGE,"E6.42.3"),sQuery(id+"F0.wireOp",EDGE,"E6.42.4"),sQuery(id+"F0.wireOp",EDGE,"E6.43.1"),sQuery(id+"F0.wireOp",EDGE,"E6.43.2"),sQuery(id+"F0.wireOp",EDGE,"E6.43.3"),sQuery(id+"F0.wireOp",EDGE,"E6.43.4"),sQuery(id+"F0.wireOp",EDGE,"E7"),sQuery(id+"F0.wireOp",EDGE,"E8.1.0"),sQuery(id+"F0.wireOp",EDGE,"E8.2.0"),sQuery(id+"F0.wireOp",EDGE,"E8.3.0"),sQuery(id+"F0.wireOp",EDGE,"E8.4.0"),sQuery(id+"F0.wireOp",EDGE,"E8.5.0"),sQuery(id+"F0.wireOp",EDGE,"E8.6.0"),sQuery(id+"F0.wireOp",EDGE,"E8.7.0"),sQuery(id+"F0.wireOp",EDGE,"E8.8.0"),sQuery(id+"F0.wireOp",EDGE,"E8.9.0"),sQuery(id+"F0.wireOp",EDGE,"E8.10.0"),sQuery(id+"F0.wireOp",EDGE,"E8.11.0"),sQuery(id+"F0.wireOp",EDGE,"E8.12.0"),sQuery(id+"F0.wireOp",EDGE,"E8.13.0"),sQuery(id+"F0.wireOp",EDGE,"E8.14.0"),sQuery(id+"F0.wireOp",EDGE,"E8.15.0"),sQuery(id+"F0.wireOp",EDGE,"E8.16.0"),sQuery(id+"F0.wireOp",EDGE,"E8.17.0"),sQuery(id+"F0.wireOp",EDGE,"E8.18.0"),sQuery(id+"F0.wireOp",EDGE,"E8.19.0"),sQuery(id+"F0.wireOp",EDGE,"E8.20.0"),sQuery(id+"F0.wireOp",EDGE,"E8.21.0"),sQuery(id+"F0.wireOp",EDGE,"E8.22.0"),sQuery(id+"F0.wireOp",EDGE,"E8.23.0"),sQuery(id+"F0.wireOp",EDGE,"E8.24.0"),sQuery(id+"F0.wireOp",EDGE,"E8.25.0"),sQuery(id+"F0.wireOp",EDGE,"E8.26.0"),sQuery(id+"F0.wireOp",EDGE,"E8.27.0"),sQuery(id+"F0.wireOp",EDGE,"E8.28.0"),sQuery(id+"F0.wireOp",EDGE,"E8.29.0"),sQuery(id+"F0.wireOp",EDGE,"E8.30.0"),sQuery(id+"F0.wireOp",EDGE,"E8.31.0"),sQuery(id+"F0.wireOp",EDGE,"E8.32.0"),sQuery(id+"F0.wireOp",EDGE,"E8.33.0"),sQuery(id+"F0.wireOp",EDGE,"E8.34.0"),sQuery(id+"F0.wireOp",EDGE,"E8.35.0"),sQuery(id+"F0.wireOp",EDGE,"E8.36.0"),sQuery(id+"F0.wireOp",EDGE,"E8.37.0"),sQuery(id+"F0.wireOp",EDGE,"E8.38.0"),sQuery(id+"F0.wireOp",EDGE,"E8.39.0"),sQuery(id+"F0.wireOp",EDGE,"E8.40.0"),sQuery(id+"F0.wireOp",EDGE,"E8.41.0"),sQuery(id+"F0.wireOp",EDGE,"E8.42.0"),sQuery(id+"F0.wireOp",EDGE,"E8.43.0")])],"isStart":true})]});}
            var Q26;
            {var subQ0=sQuery(id+"F0.wireOp",EDGE,"E6.8.3");var subQ1=sQuery(id+"F0.wireOp",EDGE,"E6.8.1");Q26=makeQuery(id+"F2.opFillet","BLEND_EDGE",EDGE,{"blendedFrom":[makeQuery(id+"F1.opExtrude","SWEPT_EDGE",EDGE,{"disambiguationData":[OSD([sQuery(id+"F0.wireOp",EDGE,"E6.8.0"),subQ1,subQ0])]}),makeQuery(id+"F1.opExtrude","CAP_FACE",FACE,{"disambiguationData":[OSD([sQuery(id+"F0.wireOp",EDGE,"E0"),sQuery(id+"F0.wireOp",EDGE,"E1"),sQuery(id+"F0.wireOp",EDGE,"E2"),sQuery(id+"F0.wireOp",EDGE,"E4"),sQuery(id+"F0.wireOp",EDGE,"E5"),sQuery(id+"F0.wireOp",EDGE,"E6.1.1"),sQuery(id+"F0.wireOp",EDGE,"E6.1.2"),sQuery(id+"F0.wireOp",EDGE,"E6.1.3"),sQuery(id+"F0.wireOp",EDGE,"E6.1.4"),sQuery(id+"F0.wireOp",EDGE,"E6.2.1"),sQuery(id+"F0.wireOp",EDGE,"E6.2.2"),sQuery(id+"F0.wireOp",EDGE,"E6.2.3"),sQuery(id+"F0.wireOp",EDGE,"E6.2.4"),sQuery(id+"F0.wireOp",EDGE,"E6.3.1"),sQuery(id+"F0.wireOp",EDGE,"E6.3.2"),sQuery(id+"F0.wireOp",EDGE,"E6.3.3"),sQuery(id+"F0.wireOp",EDGE,"E6.3.4"),sQuery(id+"F0.wireOp",EDGE,"E6.4.1"),sQuery(id+"F0.wireOp",EDGE,"E6.4.2"),sQuery(id+"F0.wireOp",EDGE,"E6.4.3"),sQuery(id+"F0.wireOp",EDGE,"E6.4.4"),sQuery(id+"F0.wireOp",EDGE,"E6.5.1"),sQuery(id+"F0.wireOp",EDGE,"E6.5.2"),sQuery(id+"F0.wireOp",EDGE,"E6.5.3"),sQuery(id+"F0.wireOp",EDGE,"E6.5.4"),sQuery(id+"F0.wireOp",EDGE,"E6.6.1"),sQuery(id+"F0.wireOp",EDGE,"E6.6.2"),sQuery(id+"F0.wireOp",EDGE,"E6.6.3"),sQuery(id+"F0.wireOp",EDGE,"E6.6.4"),sQuery(id+"F0.wireOp",EDGE,"E6.7.1"),sQuery(id+"F0.wireOp",EDGE,"E6.7.2"),sQuery(id+"F0.wireOp",EDGE,"E6.7.3"),sQuery(id+"F0.wireOp",EDGE,"E6.7.4"),subQ1,sQuery(id+"F0.wireOp",EDGE,"E6.8.2"),subQ0,sQuery(id+"F0.wireOp",EDGE,"E6.8.4"),sQuery(id+"F0.wireOp",EDGE,"E6.9.1"),sQuery(id+"F0.wireOp",EDGE,"E6.9.2"),sQuery(id+"F0.wireOp",EDGE,"E6.9.3"),sQuery(id+"F0.wireOp",EDGE,"E6.9.4"),sQuery(id+"F0.wireOp",EDGE,"E6.10.1"),sQuery(id+"F0.wireOp",EDGE,"E6.10.2"),sQuery(id+"F0.wireOp",EDGE,"E6.10.3"),sQuery(id+"F0.wireOp",EDGE,"E6.10.4"),sQuery(id+"F0.wireOp",EDGE,"E6.11.1"),sQuery(id+"F0.wireOp",EDGE,"E6.11.2"),sQuery(id+"F0.wireOp",EDGE,"E6.11.3"),sQuery(id+"F0.wireOp",EDGE,"E6.11.4"),sQuery(id+"F0.wireOp",EDGE,"E6.12.1"),sQuery(id+"F0.wireOp",EDGE,"E6.12.2"),sQuery(id+"F0.wireOp",EDGE,"E6.12.3"),sQuery(id+"F0.wireOp",EDGE,"E6.12.4"),sQuery(id+"F0.wireOp",EDGE,"E6.13.1"),sQuery(id+"F0.wireOp",EDGE,"E6.13.2"),sQuery(id+"F0.wireOp",EDGE,"E6.13.3"),sQuery(id+"F0.wireOp",EDGE,"E6.13.4"),sQuery(id+"F0.wireOp",EDGE,"E6.14.1"),sQuery(id+"F0.wireOp",EDGE,"E6.14.2"),sQuery(id+"F0.wireOp",EDGE,"E6.14.3"),sQuery(id+"F0.wireOp",EDGE,"E6.14.4"),sQuery(id+"F0.wireOp",EDGE,"E6.15.1"),sQuery(id+"F0.wireOp",EDGE,"E6.15.2"),sQuery(id+"F0.wireOp",EDGE,"E6.15.3"),sQuery(id+"F0.wireOp",EDGE,"E6.15.4"),sQuery(id+"F0.wireOp",EDGE,"E6.16.1"),sQuery(id+"F0.wireOp",EDGE,"E6.16.2"),sQuery(id+"F0.wireOp",EDGE,"E6.16.3"),sQuery(id+"F0.wireOp",EDGE,"E6.16.4"),sQuery(id+"F0.wireOp",EDGE,"E6.17.1"),sQuery(id+"F0.wireOp",EDGE,"E6.17.2"),sQuery(id+"F0.wireOp",EDGE,"E6.17.3"),sQuery(id+"F0.wireOp",EDGE,"E6.17.4"),sQuery(id+"F0.wireOp",EDGE,"E6.18.1"),sQuery(id+"F0.wireOp",EDGE,"E6.18.2"),sQuery(id+"F0.wireOp",EDGE,"E6.18.3"),sQuery(id+"F0.wireOp",EDGE,"E6.18.4"),sQuery(id+"F0.wireOp",EDGE,"E6.19.1"),sQuery(id+"F0.wireOp",EDGE,"E6.19.2"),sQuery(id+"F0.wireOp",EDGE,"E6.19.3"),sQuery(id+"F0.wireOp",EDGE,"E6.19.4"),sQuery(id+"F0.wireOp",EDGE,"E6.20.1"),sQuery(id+"F0.wireOp",EDGE,"E6.20.2"),sQuery(id+"F0.wireOp",EDGE,"E6.20.3"),sQuery(id+"F0.wireOp",EDGE,"E6.20.4"),sQuery(id+"F0.wireOp",EDGE,"E6.21.1"),sQuery(id+"F0.wireOp",EDGE,"E6.21.2"),sQuery(id+"F0.wireOp",EDGE,"E6.21.3"),sQuery(id+"F0.wireOp",EDGE,"E6.21.4"),sQuery(id+"F0.wireOp",EDGE,"E6.22.1"),sQuery(id+"F0.wireOp",EDGE,"E6.22.2"),sQuery(id+"F0.wireOp",EDGE,"E6.22.3"),sQuery(id+"F0.wireOp",EDGE,"E6.22.4"),sQuery(id+"F0.wireOp",EDGE,"E6.23.1"),sQuery(id+"F0.wireOp",EDGE,"E6.23.2"),sQuery(id+"F0.wireOp",EDGE,"E6.23.3"),sQuery(id+"F0.wireOp",EDGE,"E6.23.4"),sQuery(id+"F0.wireOp",EDGE,"E6.24.1"),sQuery(id+"F0.wireOp",EDGE,"E6.24.2"),sQuery(id+"F0.wireOp",EDGE,"E6.24.3"),sQuery(id+"F0.wireOp",EDGE,"E6.24.4"),sQuery(id+"F0.wireOp",EDGE,"E6.25.1"),sQuery(id+"F0.wireOp",EDGE,"E6.25.2"),sQuery(id+"F0.wireOp",EDGE,"E6.25.3"),sQuery(id+"F0.wireOp",EDGE,"E6.25.4"),sQuery(id+"F0.wireOp",EDGE,"E6.26.1"),sQuery(id+"F0.wireOp",EDGE,"E6.26.2"),sQuery(id+"F0.wireOp",EDGE,"E6.26.3"),sQuery(id+"F0.wireOp",EDGE,"E6.26.4"),sQuery(id+"F0.wireOp",EDGE,"E6.27.1"),sQuery(id+"F0.wireOp",EDGE,"E6.27.2"),sQuery(id+"F0.wireOp",EDGE,"E6.27.3"),sQuery(id+"F0.wireOp",EDGE,"E6.27.4"),sQuery(id+"F0.wireOp",EDGE,"E6.28.1"),sQuery(id+"F0.wireOp",EDGE,"E6.28.2"),sQuery(id+"F0.wireOp",EDGE,"E6.28.3"),sQuery(id+"F0.wireOp",EDGE,"E6.28.4"),sQuery(id+"F0.wireOp",EDGE,"E6.29.1"),sQuery(id+"F0.wireOp",EDGE,"E6.29.2"),sQuery(id+"F0.wireOp",EDGE,"E6.29.3"),sQuery(id+"F0.wireOp",EDGE,"E6.29.4"),sQuery(id+"F0.wireOp",EDGE,"E6.30.1"),sQuery(id+"F0.wireOp",EDGE,"E6.30.2"),sQuery(id+"F0.wireOp",EDGE,"E6.30.3"),sQuery(id+"F0.wireOp",EDGE,"E6.30.4"),sQuery(id+"F0.wireOp",EDGE,"E6.31.1"),sQuery(id+"F0.wireOp",EDGE,"E6.31.2"),sQuery(id+"F0.wireOp",EDGE,"E6.31.3"),sQuery(id+"F0.wireOp",EDGE,"E6.31.4"),sQuery(id+"F0.wireOp",EDGE,"E6.32.1"),sQuery(id+"F0.wireOp",EDGE,"E6.32.2"),sQuery(id+"F0.wireOp",EDGE,"E6.32.3"),sQuery(id+"F0.wireOp",EDGE,"E6.32.4"),sQuery(id+"F0.wireOp",EDGE,"E6.33.1"),sQuery(id+"F0.wireOp",EDGE,"E6.33.2"),sQuery(id+"F0.wireOp",EDGE,"E6.33.3"),sQuery(id+"F0.wireOp",EDGE,"E6.33.4"),sQuery(id+"F0.wireOp",EDGE,"E6.34.1"),sQuery(id+"F0.wireOp",EDGE,"E6.34.2"),sQuery(id+"F0.wireOp",EDGE,"E6.34.3"),sQuery(id+"F0.wireOp",EDGE,"E6.34.4"),sQuery(id+"F0.wireOp",EDGE,"E6.35.1"),sQuery(id+"F0.wireOp",EDGE,"E6.35.2"),sQuery(id+"F0.wireOp",EDGE,"E6.35.3"),sQuery(id+"F0.wireOp",EDGE,"E6.35.4"),sQuery(id+"F0.wireOp",EDGE,"E6.36.1"),sQuery(id+"F0.wireOp",EDGE,"E6.36.2"),sQuery(id+"F0.wireOp",EDGE,"E6.36.3"),sQuery(id+"F0.wireOp",EDGE,"E6.36.4"),sQuery(id+"F0.wireOp",EDGE,"E6.37.1"),sQuery(id+"F0.wireOp",EDGE,"E6.37.2"),sQuery(id+"F0.wireOp",EDGE,"E6.37.3"),sQuery(id+"F0.wireOp",EDGE,"E6.37.4"),sQuery(id+"F0.wireOp",EDGE,"E6.38.1"),sQuery(id+"F0.wireOp",EDGE,"E6.38.2"),sQuery(id+"F0.wireOp",EDGE,"E6.38.3"),sQuery(id+"F0.wireOp",EDGE,"E6.38.4"),sQuery(id+"F0.wireOp",EDGE,"E6.39.1"),sQuery(id+"F0.wireOp",EDGE,"E6.39.2"),sQuery(id+"F0.wireOp",EDGE,"E6.39.3"),sQuery(id+"F0.wireOp",EDGE,"E6.39.4"),sQuery(id+"F0.wireOp",EDGE,"E6.40.1"),sQuery(id+"F0.wireOp",EDGE,"E6.40.2"),sQuery(id+"F0.wireOp",EDGE,"E6.40.3"),sQuery(id+"F0.wireOp",EDGE,"E6.40.4"),sQuery(id+"F0.wireOp",EDGE,"E6.41.1"),sQuery(id+"F0.wireOp",EDGE,"E6.41.2"),sQuery(id+"F0.wireOp",EDGE,"E6.41.3"),sQuery(id+"F0.wireOp",EDGE,"E6.41.4"),sQuery(id+"F0.wireOp",EDGE,"E6.42.1"),sQuery(id+"F0.wireOp",EDGE,"E6.42.2"),sQuery(id+"F0.wireOp",EDGE,"E6.42.3"),sQuery(id+"F0.wireOp",EDGE,"E6.42.4"),sQuery(id+"F0.wireOp",EDGE,"E6.43.1"),sQuery(id+"F0.wireOp",EDGE,"E6.43.2"),sQuery(id+"F0.wireOp",EDGE,"E6.43.3"),sQuery(id+"F0.wireOp",EDGE,"E6.43.4"),sQuery(id+"F0.wireOp",EDGE,"E7"),sQuery(id+"F0.wireOp",EDGE,"E8.1.0"),sQuery(id+"F0.wireOp",EDGE,"E8.2.0"),sQuery(id+"F0.wireOp",EDGE,"E8.3.0"),sQuery(id+"F0.wireOp",EDGE,"E8.4.0"),sQuery(id+"F0.wireOp",EDGE,"E8.5.0"),sQuery(id+"F0.wireOp",EDGE,"E8.6.0"),sQuery(id+"F0.wireOp",EDGE,"E8.7.0"),sQuery(id+"F0.wireOp",EDGE,"E8.8.0"),sQuery(id+"F0.wireOp",EDGE,"E8.9.0"),sQuery(id+"F0.wireOp",EDGE,"E8.10.0"),sQuery(id+"F0.wireOp",EDGE,"E8.11.0"),sQuery(id+"F0.wireOp",EDGE,"E8.12.0"),sQuery(id+"F0.wireOp",EDGE,"E8.13.0"),sQuery(id+"F0.wireOp",EDGE,"E8.14.0"),sQuery(id+"F0.wireOp",EDGE,"E8.15.0"),sQuery(id+"F0.wireOp",EDGE,"E8.16.0"),sQuery(id+"F0.wireOp",EDGE,"E8.17.0"),sQuery(id+"F0.wireOp",EDGE,"E8.18.0"),sQuery(id+"F0.wireOp",EDGE,"E8.19.0"),sQuery(id+"F0.wireOp",EDGE,"E8.20.0"),sQuery(id+"F0.wireOp",EDGE,"E8.21.0"),sQuery(id+"F0.wireOp",EDGE,"E8.22.0"),sQuery(id+"F0.wireOp",EDGE,"E8.23.0"),sQuery(id+"F0.wireOp",EDGE,"E8.24.0"),sQuery(id+"F0.wireOp",EDGE,"E8.25.0"),sQuery(id+"F0.wireOp",EDGE,"E8.26.0"),sQuery(id+"F0.wireOp",EDGE,"E8.27.0"),sQuery(id+"F0.wireOp",EDGE,"E8.28.0"),sQuery(id+"F0.wireOp",EDGE,"E8.29.0"),sQuery(id+"F0.wireOp",EDGE,"E8.30.0"),sQuery(id+"F0.wireOp",EDGE,"E8.31.0"),sQuery(id+"F0.wireOp",EDGE,"E8.32.0"),sQuery(id+"F0.wireOp",EDGE,"E8.33.0"),sQuery(id+"F0.wireOp",EDGE,"E8.34.0"),sQuery(id+"F0.wireOp",EDGE,"E8.35.0"),sQuery(id+"F0.wireOp",EDGE,"E8.36.0"),sQuery(id+"F0.wireOp",EDGE,"E8.37.0"),sQuery(id+"F0.wireOp",EDGE,"E8.38.0"),sQuery(id+"F0.wireOp",EDGE,"E8.39.0"),sQuery(id+"F0.wireOp",EDGE,"E8.40.0"),sQuery(id+"F0.wireOp",EDGE,"E8.41.0"),sQuery(id+"F0.wireOp",EDGE,"E8.42.0"),sQuery(id+"F0.wireOp",EDGE,"E8.43.0")])],"isStart":true})],"blendedInto":[makeQuery(id+"F1.opExtrude","CAP_FACE",FACE,{"disambiguationData":[OSD([sQuery(id+"F0.wireOp",EDGE,"E0"),sQuery(id+"F0.wireOp",EDGE,"E1"),sQuery(id+"F0.wireOp",EDGE,"E2"),sQuery(id+"F0.wireOp",EDGE,"E4"),sQuery(id+"F0.wireOp",EDGE,"E5"),sQuery(id+"F0.wireOp",EDGE,"E6.1.1"),sQuery(id+"F0.wireOp",EDGE,"E6.1.2"),sQuery(id+"F0.wireOp",EDGE,"E6.1.3"),sQuery(id+"F0.wireOp",EDGE,"E6.1.4"),sQuery(id+"F0.wireOp",EDGE,"E6.2.1"),sQuery(id+"F0.wireOp",EDGE,"E6.2.2"),sQuery(id+"F0.wireOp",EDGE,"E6.2.3"),sQuery(id+"F0.wireOp",EDGE,"E6.2.4"),sQuery(id+"F0.wireOp",EDGE,"E6.3.1"),sQuery(id+"F0.wireOp",EDGE,"E6.3.2"),sQuery(id+"F0.wireOp",EDGE,"E6.3.3"),sQuery(id+"F0.wireOp",EDGE,"E6.3.4"),sQuery(id+"F0.wireOp",EDGE,"E6.4.1"),sQuery(id+"F0.wireOp",EDGE,"E6.4.2"),sQuery(id+"F0.wireOp",EDGE,"E6.4.3"),sQuery(id+"F0.wireOp",EDGE,"E6.4.4"),sQuery(id+"F0.wireOp",EDGE,"E6.5.1"),sQuery(id+"F0.wireOp",EDGE,"E6.5.2"),sQuery(id+"F0.wireOp",EDGE,"E6.5.3"),sQuery(id+"F0.wireOp",EDGE,"E6.5.4"),sQuery(id+"F0.wireOp",EDGE,"E6.6.1"),sQuery(id+"F0.wireOp",EDGE,"E6.6.2"),sQuery(id+"F0.wireOp",EDGE,"E6.6.3"),sQuery(id+"F0.wireOp",EDGE,"E6.6.4"),sQuery(id+"F0.wireOp",EDGE,"E6.7.1"),sQuery(id+"F0.wireOp",EDGE,"E6.7.2"),sQuery(id+"F0.wireOp",EDGE,"E6.7.3"),sQuery(id+"F0.wireOp",EDGE,"E6.7.4"),subQ1,sQuery(id+"F0.wireOp",EDGE,"E6.8.2"),subQ0,sQuery(id+"F0.wireOp",EDGE,"E6.8.4"),sQuery(id+"F0.wireOp",EDGE,"E6.9.1"),sQuery(id+"F0.wireOp",EDGE,"E6.9.2"),sQuery(id+"F0.wireOp",EDGE,"E6.9.3"),sQuery(id+"F0.wireOp",EDGE,"E6.9.4"),sQuery(id+"F0.wireOp",EDGE,"E6.10.1"),sQuery(id+"F0.wireOp",EDGE,"E6.10.2"),sQuery(id+"F0.wireOp",EDGE,"E6.10.3"),sQuery(id+"F0.wireOp",EDGE,"E6.10.4"),sQuery(id+"F0.wireOp",EDGE,"E6.11.1"),sQuery(id+"F0.wireOp",EDGE,"E6.11.2"),sQuery(id+"F0.wireOp",EDGE,"E6.11.3"),sQuery(id+"F0.wireOp",EDGE,"E6.11.4"),sQuery(id+"F0.wireOp",EDGE,"E6.12.1"),sQuery(id+"F0.wireOp",EDGE,"E6.12.2"),sQuery(id+"F0.wireOp",EDGE,"E6.12.3"),sQuery(id+"F0.wireOp",EDGE,"E6.12.4"),sQuery(id+"F0.wireOp",EDGE,"E6.13.1"),sQuery(id+"F0.wireOp",EDGE,"E6.13.2"),sQuery(id+"F0.wireOp",EDGE,"E6.13.3"),sQuery(id+"F0.wireOp",EDGE,"E6.13.4"),sQuery(id+"F0.wireOp",EDGE,"E6.14.1"),sQuery(id+"F0.wireOp",EDGE,"E6.14.2"),sQuery(id+"F0.wireOp",EDGE,"E6.14.3"),sQuery(id+"F0.wireOp",EDGE,"E6.14.4"),sQuery(id+"F0.wireOp",EDGE,"E6.15.1"),sQuery(id+"F0.wireOp",EDGE,"E6.15.2"),sQuery(id+"F0.wireOp",EDGE,"E6.15.3"),sQuery(id+"F0.wireOp",EDGE,"E6.15.4"),sQuery(id+"F0.wireOp",EDGE,"E6.16.1"),sQuery(id+"F0.wireOp",EDGE,"E6.16.2"),sQuery(id+"F0.wireOp",EDGE,"E6.16.3"),sQuery(id+"F0.wireOp",EDGE,"E6.16.4"),sQuery(id+"F0.wireOp",EDGE,"E6.17.1"),sQuery(id+"F0.wireOp",EDGE,"E6.17.2"),sQuery(id+"F0.wireOp",EDGE,"E6.17.3"),sQuery(id+"F0.wireOp",EDGE,"E6.17.4"),sQuery(id+"F0.wireOp",EDGE,"E6.18.1"),sQuery(id+"F0.wireOp",EDGE,"E6.18.2"),sQuery(id+"F0.wireOp",EDGE,"E6.18.3"),sQuery(id+"F0.wireOp",EDGE,"E6.18.4"),sQuery(id+"F0.wireOp",EDGE,"E6.19.1"),sQuery(id+"F0.wireOp",EDGE,"E6.19.2"),sQuery(id+"F0.wireOp",EDGE,"E6.19.3"),sQuery(id+"F0.wireOp",EDGE,"E6.19.4"),sQuery(id+"F0.wireOp",EDGE,"E6.20.1"),sQuery(id+"F0.wireOp",EDGE,"E6.20.2"),sQuery(id+"F0.wireOp",EDGE,"E6.20.3"),sQuery(id+"F0.wireOp",EDGE,"E6.20.4"),sQuery(id+"F0.wireOp",EDGE,"E6.21.1"),sQuery(id+"F0.wireOp",EDGE,"E6.21.2"),sQuery(id+"F0.wireOp",EDGE,"E6.21.3"),sQuery(id+"F0.wireOp",EDGE,"E6.21.4"),sQuery(id+"F0.wireOp",EDGE,"E6.22.1"),sQuery(id+"F0.wireOp",EDGE,"E6.22.2"),sQuery(id+"F0.wireOp",EDGE,"E6.22.3"),sQuery(id+"F0.wireOp",EDGE,"E6.22.4"),sQuery(id+"F0.wireOp",EDGE,"E6.23.1"),sQuery(id+"F0.wireOp",EDGE,"E6.23.2"),sQuery(id+"F0.wireOp",EDGE,"E6.23.3"),sQuery(id+"F0.wireOp",EDGE,"E6.23.4"),sQuery(id+"F0.wireOp",EDGE,"E6.24.1"),sQuery(id+"F0.wireOp",EDGE,"E6.24.2"),sQuery(id+"F0.wireOp",EDGE,"E6.24.3"),sQuery(id+"F0.wireOp",EDGE,"E6.24.4"),sQuery(id+"F0.wireOp",EDGE,"E6.25.1"),sQuery(id+"F0.wireOp",EDGE,"E6.25.2"),sQuery(id+"F0.wireOp",EDGE,"E6.25.3"),sQuery(id+"F0.wireOp",EDGE,"E6.25.4"),sQuery(id+"F0.wireOp",EDGE,"E6.26.1"),sQuery(id+"F0.wireOp",EDGE,"E6.26.2"),sQuery(id+"F0.wireOp",EDGE,"E6.26.3"),sQuery(id+"F0.wireOp",EDGE,"E6.26.4"),sQuery(id+"F0.wireOp",EDGE,"E6.27.1"),sQuery(id+"F0.wireOp",EDGE,"E6.27.2"),sQuery(id+"F0.wireOp",EDGE,"E6.27.3"),sQuery(id+"F0.wireOp",EDGE,"E6.27.4"),sQuery(id+"F0.wireOp",EDGE,"E6.28.1"),sQuery(id+"F0.wireOp",EDGE,"E6.28.2"),sQuery(id+"F0.wireOp",EDGE,"E6.28.3"),sQuery(id+"F0.wireOp",EDGE,"E6.28.4"),sQuery(id+"F0.wireOp",EDGE,"E6.29.1"),sQuery(id+"F0.wireOp",EDGE,"E6.29.2"),sQuery(id+"F0.wireOp",EDGE,"E6.29.3"),sQuery(id+"F0.wireOp",EDGE,"E6.29.4"),sQuery(id+"F0.wireOp",EDGE,"E6.30.1"),sQuery(id+"F0.wireOp",EDGE,"E6.30.2"),sQuery(id+"F0.wireOp",EDGE,"E6.30.3"),sQuery(id+"F0.wireOp",EDGE,"E6.30.4"),sQuery(id+"F0.wireOp",EDGE,"E6.31.1"),sQuery(id+"F0.wireOp",EDGE,"E6.31.2"),sQuery(id+"F0.wireOp",EDGE,"E6.31.3"),sQuery(id+"F0.wireOp",EDGE,"E6.31.4"),sQuery(id+"F0.wireOp",EDGE,"E6.32.1"),sQuery(id+"F0.wireOp",EDGE,"E6.32.2"),sQuery(id+"F0.wireOp",EDGE,"E6.32.3"),sQuery(id+"F0.wireOp",EDGE,"E6.32.4"),sQuery(id+"F0.wireOp",EDGE,"E6.33.1"),sQuery(id+"F0.wireOp",EDGE,"E6.33.2"),sQuery(id+"F0.wireOp",EDGE,"E6.33.3"),sQuery(id+"F0.wireOp",EDGE,"E6.33.4"),sQuery(id+"F0.wireOp",EDGE,"E6.34.1"),sQuery(id+"F0.wireOp",EDGE,"E6.34.2"),sQuery(id+"F0.wireOp",EDGE,"E6.34.3"),sQuery(id+"F0.wireOp",EDGE,"E6.34.4"),sQuery(id+"F0.wireOp",EDGE,"E6.35.1"),sQuery(id+"F0.wireOp",EDGE,"E6.35.2"),sQuery(id+"F0.wireOp",EDGE,"E6.35.3"),sQuery(id+"F0.wireOp",EDGE,"E6.35.4"),sQuery(id+"F0.wireOp",EDGE,"E6.36.1"),sQuery(id+"F0.wireOp",EDGE,"E6.36.2"),sQuery(id+"F0.wireOp",EDGE,"E6.36.3"),sQuery(id+"F0.wireOp",EDGE,"E6.36.4"),sQuery(id+"F0.wireOp",EDGE,"E6.37.1"),sQuery(id+"F0.wireOp",EDGE,"E6.37.2"),sQuery(id+"F0.wireOp",EDGE,"E6.37.3"),sQuery(id+"F0.wireOp",EDGE,"E6.37.4"),sQuery(id+"F0.wireOp",EDGE,"E6.38.1"),sQuery(id+"F0.wireOp",EDGE,"E6.38.2"),sQuery(id+"F0.wireOp",EDGE,"E6.38.3"),sQuery(id+"F0.wireOp",EDGE,"E6.38.4"),sQuery(id+"F0.wireOp",EDGE,"E6.39.1"),sQuery(id+"F0.wireOp",EDGE,"E6.39.2"),sQuery(id+"F0.wireOp",EDGE,"E6.39.3"),sQuery(id+"F0.wireOp",EDGE,"E6.39.4"),sQuery(id+"F0.wireOp",EDGE,"E6.40.1"),sQuery(id+"F0.wireOp",EDGE,"E6.40.2"),sQuery(id+"F0.wireOp",EDGE,"E6.40.3"),sQuery(id+"F0.wireOp",EDGE,"E6.40.4"),sQuery(id+"F0.wireOp",EDGE,"E6.41.1"),sQuery(id+"F0.wireOp",EDGE,"E6.41.2"),sQuery(id+"F0.wireOp",EDGE,"E6.41.3"),sQuery(id+"F0.wireOp",EDGE,"E6.41.4"),sQuery(id+"F0.wireOp",EDGE,"E6.42.1"),sQuery(id+"F0.wireOp",EDGE,"E6.42.2"),sQuery(id+"F0.wireOp",EDGE,"E6.42.3"),sQuery(id+"F0.wireOp",EDGE,"E6.42.4"),sQuery(id+"F0.wireOp",EDGE,"E6.43.1"),sQuery(id+"F0.wireOp",EDGE,"E6.43.2"),sQuery(id+"F0.wireOp",EDGE,"E6.43.3"),sQuery(id+"F0.wireOp",EDGE,"E6.43.4"),sQuery(id+"F0.wireOp",EDGE,"E7"),sQuery(id+"F0.wireOp",EDGE,"E8.1.0"),sQuery(id+"F0.wireOp",EDGE,"E8.2.0"),sQuery(id+"F0.wireOp",EDGE,"E8.3.0"),sQuery(id+"F0.wireOp",EDGE,"E8.4.0"),sQuery(id+"F0.wireOp",EDGE,"E8.5.0"),sQuery(id+"F0.wireOp",EDGE,"E8.6.0"),sQuery(id+"F0.wireOp",EDGE,"E8.7.0"),sQuery(id+"F0.wireOp",EDGE,"E8.8.0"),sQuery(id+"F0.wireOp",EDGE,"E8.9.0"),sQuery(id+"F0.wireOp",EDGE,"E8.10.0"),sQuery(id+"F0.wireOp",EDGE,"E8.11.0"),sQuery(id+"F0.wireOp",EDGE,"E8.12.0"),sQuery(id+"F0.wireOp",EDGE,"E8.13.0"),sQuery(id+"F0.wireOp",EDGE,"E8.14.0"),sQuery(id+"F0.wireOp",EDGE,"E8.15.0"),sQuery(id+"F0.wireOp",EDGE,"E8.16.0"),sQuery(id+"F0.wireOp",EDGE,"E8.17.0"),sQuery(id+"F0.wireOp",EDGE,"E8.18.0"),sQuery(id+"F0.wireOp",EDGE,"E8.19.0"),sQuery(id+"F0.wireOp",EDGE,"E8.20.0"),sQuery(id+"F0.wireOp",EDGE,"E8.21.0"),sQuery(id+"F0.wireOp",EDGE,"E8.22.0"),sQuery(id+"F0.wireOp",EDGE,"E8.23.0"),sQuery(id+"F0.wireOp",EDGE,"E8.24.0"),sQuery(id+"F0.wireOp",EDGE,"E8.25.0"),sQuery(id+"F0.wireOp",EDGE,"E8.26.0"),sQuery(id+"F0.wireOp",EDGE,"E8.27.0"),sQuery(id+"F0.wireOp",EDGE,"E8.28.0"),sQuery(id+"F0.wireOp",EDGE,"E8.29.0"),sQuery(id+"F0.wireOp",EDGE,"E8.30.0"),sQuery(id+"F0.wireOp",EDGE,"E8.31.0"),sQuery(id+"F0.wireOp",EDGE,"E8.32.0"),sQuery(id+"F0.wireOp",EDGE,"E8.33.0"),sQuery(id+"F0.wireOp",EDGE,"E8.34.0"),sQuery(id+"F0.wireOp",EDGE,"E8.35.0"),sQuery(id+"F0.wireOp",EDGE,"E8.36.0"),sQuery(id+"F0.wireOp",EDGE,"E8.37.0"),sQuery(id+"F0.wireOp",EDGE,"E8.38.0"),sQuery(id+"F0.wireOp",EDGE,"E8.39.0"),sQuery(id+"F0.wireOp",EDGE,"E8.40.0"),sQuery(id+"F0.wireOp",EDGE,"E8.41.0"),sQuery(id+"F0.wireOp",EDGE,"E8.42.0"),sQuery(id+"F0.wireOp",EDGE,"E8.43.0")])],"isStart":true})]});}
            var Q27;
            {var subQ0=sQuery(id+"F0.wireOp",EDGE,"E6.10.3");var subQ1=sQuery(id+"F0.wireOp",EDGE,"E6.10.1");Q27=makeQuery(id+"F2.opFillet","BLEND_EDGE",EDGE,{"blendedFrom":[makeQuery(id+"F1.opExtrude","SWEPT_EDGE",EDGE,{"disambiguationData":[OSD([sQuery(id+"F0.wireOp",EDGE,"E6.10.0"),subQ1,subQ0])]}),makeQuery(id+"F1.opExtrude","CAP_FACE",FACE,{"disambiguationData":[OSD([sQuery(id+"F0.wireOp",EDGE,"E0"),sQuery(id+"F0.wireOp",EDGE,"E1"),sQuery(id+"F0.wireOp",EDGE,"E2"),sQuery(id+"F0.wireOp",EDGE,"E4"),sQuery(id+"F0.wireOp",EDGE,"E5"),sQuery(id+"F0.wireOp",EDGE,"E6.1.1"),sQuery(id+"F0.wireOp",EDGE,"E6.1.2"),sQuery(id+"F0.wireOp",EDGE,"E6.1.3"),sQuery(id+"F0.wireOp",EDGE,"E6.1.4"),sQuery(id+"F0.wireOp",EDGE,"E6.2.1"),sQuery(id+"F0.wireOp",EDGE,"E6.2.2"),sQuery(id+"F0.wireOp",EDGE,"E6.2.3"),sQuery(id+"F0.wireOp",EDGE,"E6.2.4"),sQuery(id+"F0.wireOp",EDGE,"E6.3.1"),sQuery(id+"F0.wireOp",EDGE,"E6.3.2"),sQuery(id+"F0.wireOp",EDGE,"E6.3.3"),sQuery(id+"F0.wireOp",EDGE,"E6.3.4"),sQuery(id+"F0.wireOp",EDGE,"E6.4.1"),sQuery(id+"F0.wireOp",EDGE,"E6.4.2"),sQuery(id+"F0.wireOp",EDGE,"E6.4.3"),sQuery(id+"F0.wireOp",EDGE,"E6.4.4"),sQuery(id+"F0.wireOp",EDGE,"E6.5.1"),sQuery(id+"F0.wireOp",EDGE,"E6.5.2"),sQuery(id+"F0.wireOp",EDGE,"E6.5.3"),sQuery(id+"F0.wireOp",EDGE,"E6.5.4"),sQuery(id+"F0.wireOp",EDGE,"E6.6.1"),sQuery(id+"F0.wireOp",EDGE,"E6.6.2"),sQuery(id+"F0.wireOp",EDGE,"E6.6.3"),sQuery(id+"F0.wireOp",EDGE,"E6.6.4"),sQuery(id+"F0.wireOp",EDGE,"E6.7.1"),sQuery(id+"F0.wireOp",EDGE,"E6.7.2"),sQuery(id+"F0.wireOp",EDGE,"E6.7.3"),sQuery(id+"F0.wireOp",EDGE,"E6.7.4"),sQuery(id+"F0.wireOp",EDGE,"E6.8.1"),sQuery(id+"F0.wireOp",EDGE,"E6.8.2"),sQuery(id+"F0.wireOp",EDGE,"E6.8.3"),sQuery(id+"F0.wireOp",EDGE,"E6.8.4"),sQuery(id+"F0.wireOp",EDGE,"E6.9.1"),sQuery(id+"F0.wireOp",EDGE,"E6.9.2"),sQuery(id+"F0.wireOp",EDGE,"E6.9.3"),sQuery(id+"F0.wireOp",EDGE,"E6.9.4"),subQ1,sQuery(id+"F0.wireOp",EDGE,"E6.10.2"),subQ0,sQuery(id+"F0.wireOp",EDGE,"E6.10.4"),sQuery(id+"F0.wireOp",EDGE,"E6.11.1"),sQuery(id+"F0.wireOp",EDGE,"E6.11.2"),sQuery(id+"F0.wireOp",EDGE,"E6.11.3"),sQuery(id+"F0.wireOp",EDGE,"E6.11.4"),sQuery(id+"F0.wireOp",EDGE,"E6.12.1"),sQuery(id+"F0.wireOp",EDGE,"E6.12.2"),sQuery(id+"F0.wireOp",EDGE,"E6.12.3"),sQuery(id+"F0.wireOp",EDGE,"E6.12.4"),sQuery(id+"F0.wireOp",EDGE,"E6.13.1"),sQuery(id+"F0.wireOp",EDGE,"E6.13.2"),sQuery(id+"F0.wireOp",EDGE,"E6.13.3"),sQuery(id+"F0.wireOp",EDGE,"E6.13.4"),sQuery(id+"F0.wireOp",EDGE,"E6.14.1"),sQuery(id+"F0.wireOp",EDGE,"E6.14.2"),sQuery(id+"F0.wireOp",EDGE,"E6.14.3"),sQuery(id+"F0.wireOp",EDGE,"E6.14.4"),sQuery(id+"F0.wireOp",EDGE,"E6.15.1"),sQuery(id+"F0.wireOp",EDGE,"E6.15.2"),sQuery(id+"F0.wireOp",EDGE,"E6.15.3"),sQuery(id+"F0.wireOp",EDGE,"E6.15.4"),sQuery(id+"F0.wireOp",EDGE,"E6.16.1"),sQuery(id+"F0.wireOp",EDGE,"E6.16.2"),sQuery(id+"F0.wireOp",EDGE,"E6.16.3"),sQuery(id+"F0.wireOp",EDGE,"E6.16.4"),sQuery(id+"F0.wireOp",EDGE,"E6.17.1"),sQuery(id+"F0.wireOp",EDGE,"E6.17.2"),sQuery(id+"F0.wireOp",EDGE,"E6.17.3"),sQuery(id+"F0.wireOp",EDGE,"E6.17.4"),sQuery(id+"F0.wireOp",EDGE,"E6.18.1"),sQuery(id+"F0.wireOp",EDGE,"E6.18.2"),sQuery(id+"F0.wireOp",EDGE,"E6.18.3"),sQuery(id+"F0.wireOp",EDGE,"E6.18.4"),sQuery(id+"F0.wireOp",EDGE,"E6.19.1"),sQuery(id+"F0.wireOp",EDGE,"E6.19.2"),sQuery(id+"F0.wireOp",EDGE,"E6.19.3"),sQuery(id+"F0.wireOp",EDGE,"E6.19.4"),sQuery(id+"F0.wireOp",EDGE,"E6.20.1"),sQuery(id+"F0.wireOp",EDGE,"E6.20.2"),sQuery(id+"F0.wireOp",EDGE,"E6.20.3"),sQuery(id+"F0.wireOp",EDGE,"E6.20.4"),sQuery(id+"F0.wireOp",EDGE,"E6.21.1"),sQuery(id+"F0.wireOp",EDGE,"E6.21.2"),sQuery(id+"F0.wireOp",EDGE,"E6.21.3"),sQuery(id+"F0.wireOp",EDGE,"E6.21.4"),sQuery(id+"F0.wireOp",EDGE,"E6.22.1"),sQuery(id+"F0.wireOp",EDGE,"E6.22.2"),sQuery(id+"F0.wireOp",EDGE,"E6.22.3"),sQuery(id+"F0.wireOp",EDGE,"E6.22.4"),sQuery(id+"F0.wireOp",EDGE,"E6.23.1"),sQuery(id+"F0.wireOp",EDGE,"E6.23.2"),sQuery(id+"F0.wireOp",EDGE,"E6.23.3"),sQuery(id+"F0.wireOp",EDGE,"E6.23.4"),sQuery(id+"F0.wireOp",EDGE,"E6.24.1"),sQuery(id+"F0.wireOp",EDGE,"E6.24.2"),sQuery(id+"F0.wireOp",EDGE,"E6.24.3"),sQuery(id+"F0.wireOp",EDGE,"E6.24.4"),sQuery(id+"F0.wireOp",EDGE,"E6.25.1"),sQuery(id+"F0.wireOp",EDGE,"E6.25.2"),sQuery(id+"F0.wireOp",EDGE,"E6.25.3"),sQuery(id+"F0.wireOp",EDGE,"E6.25.4"),sQuery(id+"F0.wireOp",EDGE,"E6.26.1"),sQuery(id+"F0.wireOp",EDGE,"E6.26.2"),sQuery(id+"F0.wireOp",EDGE,"E6.26.3"),sQuery(id+"F0.wireOp",EDGE,"E6.26.4"),sQuery(id+"F0.wireOp",EDGE,"E6.27.1"),sQuery(id+"F0.wireOp",EDGE,"E6.27.2"),sQuery(id+"F0.wireOp",EDGE,"E6.27.3"),sQuery(id+"F0.wireOp",EDGE,"E6.27.4"),sQuery(id+"F0.wireOp",EDGE,"E6.28.1"),sQuery(id+"F0.wireOp",EDGE,"E6.28.2"),sQuery(id+"F0.wireOp",EDGE,"E6.28.3"),sQuery(id+"F0.wireOp",EDGE,"E6.28.4"),sQuery(id+"F0.wireOp",EDGE,"E6.29.1"),sQuery(id+"F0.wireOp",EDGE,"E6.29.2"),sQuery(id+"F0.wireOp",EDGE,"E6.29.3"),sQuery(id+"F0.wireOp",EDGE,"E6.29.4"),sQuery(id+"F0.wireOp",EDGE,"E6.30.1"),sQuery(id+"F0.wireOp",EDGE,"E6.30.2"),sQuery(id+"F0.wireOp",EDGE,"E6.30.3"),sQuery(id+"F0.wireOp",EDGE,"E6.30.4"),sQuery(id+"F0.wireOp",EDGE,"E6.31.1"),sQuery(id+"F0.wireOp",EDGE,"E6.31.2"),sQuery(id+"F0.wireOp",EDGE,"E6.31.3"),sQuery(id+"F0.wireOp",EDGE,"E6.31.4"),sQuery(id+"F0.wireOp",EDGE,"E6.32.1"),sQuery(id+"F0.wireOp",EDGE,"E6.32.2"),sQuery(id+"F0.wireOp",EDGE,"E6.32.3"),sQuery(id+"F0.wireOp",EDGE,"E6.32.4"),sQuery(id+"F0.wireOp",EDGE,"E6.33.1"),sQuery(id+"F0.wireOp",EDGE,"E6.33.2"),sQuery(id+"F0.wireOp",EDGE,"E6.33.3"),sQuery(id+"F0.wireOp",EDGE,"E6.33.4"),sQuery(id+"F0.wireOp",EDGE,"E6.34.1"),sQuery(id+"F0.wireOp",EDGE,"E6.34.2"),sQuery(id+"F0.wireOp",EDGE,"E6.34.3"),sQuery(id+"F0.wireOp",EDGE,"E6.34.4"),sQuery(id+"F0.wireOp",EDGE,"E6.35.1"),sQuery(id+"F0.wireOp",EDGE,"E6.35.2"),sQuery(id+"F0.wireOp",EDGE,"E6.35.3"),sQuery(id+"F0.wireOp",EDGE,"E6.35.4"),sQuery(id+"F0.wireOp",EDGE,"E6.36.1"),sQuery(id+"F0.wireOp",EDGE,"E6.36.2"),sQuery(id+"F0.wireOp",EDGE,"E6.36.3"),sQuery(id+"F0.wireOp",EDGE,"E6.36.4"),sQuery(id+"F0.wireOp",EDGE,"E6.37.1"),sQuery(id+"F0.wireOp",EDGE,"E6.37.2"),sQuery(id+"F0.wireOp",EDGE,"E6.37.3"),sQuery(id+"F0.wireOp",EDGE,"E6.37.4"),sQuery(id+"F0.wireOp",EDGE,"E6.38.1"),sQuery(id+"F0.wireOp",EDGE,"E6.38.2"),sQuery(id+"F0.wireOp",EDGE,"E6.38.3"),sQuery(id+"F0.wireOp",EDGE,"E6.38.4"),sQuery(id+"F0.wireOp",EDGE,"E6.39.1"),sQuery(id+"F0.wireOp",EDGE,"E6.39.2"),sQuery(id+"F0.wireOp",EDGE,"E6.39.3"),sQuery(id+"F0.wireOp",EDGE,"E6.39.4"),sQuery(id+"F0.wireOp",EDGE,"E6.40.1"),sQuery(id+"F0.wireOp",EDGE,"E6.40.2"),sQuery(id+"F0.wireOp",EDGE,"E6.40.3"),sQuery(id+"F0.wireOp",EDGE,"E6.40.4"),sQuery(id+"F0.wireOp",EDGE,"E6.41.1"),sQuery(id+"F0.wireOp",EDGE,"E6.41.2"),sQuery(id+"F0.wireOp",EDGE,"E6.41.3"),sQuery(id+"F0.wireOp",EDGE,"E6.41.4"),sQuery(id+"F0.wireOp",EDGE,"E6.42.1"),sQuery(id+"F0.wireOp",EDGE,"E6.42.2"),sQuery(id+"F0.wireOp",EDGE,"E6.42.3"),sQuery(id+"F0.wireOp",EDGE,"E6.42.4"),sQuery(id+"F0.wireOp",EDGE,"E6.43.1"),sQuery(id+"F0.wireOp",EDGE,"E6.43.2"),sQuery(id+"F0.wireOp",EDGE,"E6.43.3"),sQuery(id+"F0.wireOp",EDGE,"E6.43.4"),sQuery(id+"F0.wireOp",EDGE,"E7"),sQuery(id+"F0.wireOp",EDGE,"E8.1.0"),sQuery(id+"F0.wireOp",EDGE,"E8.2.0"),sQuery(id+"F0.wireOp",EDGE,"E8.3.0"),sQuery(id+"F0.wireOp",EDGE,"E8.4.0"),sQuery(id+"F0.wireOp",EDGE,"E8.5.0"),sQuery(id+"F0.wireOp",EDGE,"E8.6.0"),sQuery(id+"F0.wireOp",EDGE,"E8.7.0"),sQuery(id+"F0.wireOp",EDGE,"E8.8.0"),sQuery(id+"F0.wireOp",EDGE,"E8.9.0"),sQuery(id+"F0.wireOp",EDGE,"E8.10.0"),sQuery(id+"F0.wireOp",EDGE,"E8.11.0"),sQuery(id+"F0.wireOp",EDGE,"E8.12.0"),sQuery(id+"F0.wireOp",EDGE,"E8.13.0"),sQuery(id+"F0.wireOp",EDGE,"E8.14.0"),sQuery(id+"F0.wireOp",EDGE,"E8.15.0"),sQuery(id+"F0.wireOp",EDGE,"E8.16.0"),sQuery(id+"F0.wireOp",EDGE,"E8.17.0"),sQuery(id+"F0.wireOp",EDGE,"E8.18.0"),sQuery(id+"F0.wireOp",EDGE,"E8.19.0"),sQuery(id+"F0.wireOp",EDGE,"E8.20.0"),sQuery(id+"F0.wireOp",EDGE,"E8.21.0"),sQuery(id+"F0.wireOp",EDGE,"E8.22.0"),sQuery(id+"F0.wireOp",EDGE,"E8.23.0"),sQuery(id+"F0.wireOp",EDGE,"E8.24.0"),sQuery(id+"F0.wireOp",EDGE,"E8.25.0"),sQuery(id+"F0.wireOp",EDGE,"E8.26.0"),sQuery(id+"F0.wireOp",EDGE,"E8.27.0"),sQuery(id+"F0.wireOp",EDGE,"E8.28.0"),sQuery(id+"F0.wireOp",EDGE,"E8.29.0"),sQuery(id+"F0.wireOp",EDGE,"E8.30.0"),sQuery(id+"F0.wireOp",EDGE,"E8.31.0"),sQuery(id+"F0.wireOp",EDGE,"E8.32.0"),sQuery(id+"F0.wireOp",EDGE,"E8.33.0"),sQuery(id+"F0.wireOp",EDGE,"E8.34.0"),sQuery(id+"F0.wireOp",EDGE,"E8.35.0"),sQuery(id+"F0.wireOp",EDGE,"E8.36.0"),sQuery(id+"F0.wireOp",EDGE,"E8.37.0"),sQuery(id+"F0.wireOp",EDGE,"E8.38.0"),sQuery(id+"F0.wireOp",EDGE,"E8.39.0"),sQuery(id+"F0.wireOp",EDGE,"E8.40.0"),sQuery(id+"F0.wireOp",EDGE,"E8.41.0"),sQuery(id+"F0.wireOp",EDGE,"E8.42.0"),sQuery(id+"F0.wireOp",EDGE,"E8.43.0")])],"isStart":true})],"blendedInto":[makeQuery(id+"F1.opExtrude","CAP_FACE",FACE,{"disambiguationData":[OSD([sQuery(id+"F0.wireOp",EDGE,"E0"),sQuery(id+"F0.wireOp",EDGE,"E1"),sQuery(id+"F0.wireOp",EDGE,"E2"),sQuery(id+"F0.wireOp",EDGE,"E4"),sQuery(id+"F0.wireOp",EDGE,"E5"),sQuery(id+"F0.wireOp",EDGE,"E6.1.1"),sQuery(id+"F0.wireOp",EDGE,"E6.1.2"),sQuery(id+"F0.wireOp",EDGE,"E6.1.3"),sQuery(id+"F0.wireOp",EDGE,"E6.1.4"),sQuery(id+"F0.wireOp",EDGE,"E6.2.1"),sQuery(id+"F0.wireOp",EDGE,"E6.2.2"),sQuery(id+"F0.wireOp",EDGE,"E6.2.3"),sQuery(id+"F0.wireOp",EDGE,"E6.2.4"),sQuery(id+"F0.wireOp",EDGE,"E6.3.1"),sQuery(id+"F0.wireOp",EDGE,"E6.3.2"),sQuery(id+"F0.wireOp",EDGE,"E6.3.3"),sQuery(id+"F0.wireOp",EDGE,"E6.3.4"),sQuery(id+"F0.wireOp",EDGE,"E6.4.1"),sQuery(id+"F0.wireOp",EDGE,"E6.4.2"),sQuery(id+"F0.wireOp",EDGE,"E6.4.3"),sQuery(id+"F0.wireOp",EDGE,"E6.4.4"),sQuery(id+"F0.wireOp",EDGE,"E6.5.1"),sQuery(id+"F0.wireOp",EDGE,"E6.5.2"),sQuery(id+"F0.wireOp",EDGE,"E6.5.3"),sQuery(id+"F0.wireOp",EDGE,"E6.5.4"),sQuery(id+"F0.wireOp",EDGE,"E6.6.1"),sQuery(id+"F0.wireOp",EDGE,"E6.6.2"),sQuery(id+"F0.wireOp",EDGE,"E6.6.3"),sQuery(id+"F0.wireOp",EDGE,"E6.6.4"),sQuery(id+"F0.wireOp",EDGE,"E6.7.1"),sQuery(id+"F0.wireOp",EDGE,"E6.7.2"),sQuery(id+"F0.wireOp",EDGE,"E6.7.3"),sQuery(id+"F0.wireOp",EDGE,"E6.7.4"),sQuery(id+"F0.wireOp",EDGE,"E6.8.1"),sQuery(id+"F0.wireOp",EDGE,"E6.8.2"),sQuery(id+"F0.wireOp",EDGE,"E6.8.3"),sQuery(id+"F0.wireOp",EDGE,"E6.8.4"),sQuery(id+"F0.wireOp",EDGE,"E6.9.1"),sQuery(id+"F0.wireOp",EDGE,"E6.9.2"),sQuery(id+"F0.wireOp",EDGE,"E6.9.3"),sQuery(id+"F0.wireOp",EDGE,"E6.9.4"),subQ1,sQuery(id+"F0.wireOp",EDGE,"E6.10.2"),subQ0,sQuery(id+"F0.wireOp",EDGE,"E6.10.4"),sQuery(id+"F0.wireOp",EDGE,"E6.11.1"),sQuery(id+"F0.wireOp",EDGE,"E6.11.2"),sQuery(id+"F0.wireOp",EDGE,"E6.11.3"),sQuery(id+"F0.wireOp",EDGE,"E6.11.4"),sQuery(id+"F0.wireOp",EDGE,"E6.12.1"),sQuery(id+"F0.wireOp",EDGE,"E6.12.2"),sQuery(id+"F0.wireOp",EDGE,"E6.12.3"),sQuery(id+"F0.wireOp",EDGE,"E6.12.4"),sQuery(id+"F0.wireOp",EDGE,"E6.13.1"),sQuery(id+"F0.wireOp",EDGE,"E6.13.2"),sQuery(id+"F0.wireOp",EDGE,"E6.13.3"),sQuery(id+"F0.wireOp",EDGE,"E6.13.4"),sQuery(id+"F0.wireOp",EDGE,"E6.14.1"),sQuery(id+"F0.wireOp",EDGE,"E6.14.2"),sQuery(id+"F0.wireOp",EDGE,"E6.14.3"),sQuery(id+"F0.wireOp",EDGE,"E6.14.4"),sQuery(id+"F0.wireOp",EDGE,"E6.15.1"),sQuery(id+"F0.wireOp",EDGE,"E6.15.2"),sQuery(id+"F0.wireOp",EDGE,"E6.15.3"),sQuery(id+"F0.wireOp",EDGE,"E6.15.4"),sQuery(id+"F0.wireOp",EDGE,"E6.16.1"),sQuery(id+"F0.wireOp",EDGE,"E6.16.2"),sQuery(id+"F0.wireOp",EDGE,"E6.16.3"),sQuery(id+"F0.wireOp",EDGE,"E6.16.4"),sQuery(id+"F0.wireOp",EDGE,"E6.17.1"),sQuery(id+"F0.wireOp",EDGE,"E6.17.2"),sQuery(id+"F0.wireOp",EDGE,"E6.17.3"),sQuery(id+"F0.wireOp",EDGE,"E6.17.4"),sQuery(id+"F0.wireOp",EDGE,"E6.18.1"),sQuery(id+"F0.wireOp",EDGE,"E6.18.2"),sQuery(id+"F0.wireOp",EDGE,"E6.18.3"),sQuery(id+"F0.wireOp",EDGE,"E6.18.4"),sQuery(id+"F0.wireOp",EDGE,"E6.19.1"),sQuery(id+"F0.wireOp",EDGE,"E6.19.2"),sQuery(id+"F0.wireOp",EDGE,"E6.19.3"),sQuery(id+"F0.wireOp",EDGE,"E6.19.4"),sQuery(id+"F0.wireOp",EDGE,"E6.20.1"),sQuery(id+"F0.wireOp",EDGE,"E6.20.2"),sQuery(id+"F0.wireOp",EDGE,"E6.20.3"),sQuery(id+"F0.wireOp",EDGE,"E6.20.4"),sQuery(id+"F0.wireOp",EDGE,"E6.21.1"),sQuery(id+"F0.wireOp",EDGE,"E6.21.2"),sQuery(id+"F0.wireOp",EDGE,"E6.21.3"),sQuery(id+"F0.wireOp",EDGE,"E6.21.4"),sQuery(id+"F0.wireOp",EDGE,"E6.22.1"),sQuery(id+"F0.wireOp",EDGE,"E6.22.2"),sQuery(id+"F0.wireOp",EDGE,"E6.22.3"),sQuery(id+"F0.wireOp",EDGE,"E6.22.4"),sQuery(id+"F0.wireOp",EDGE,"E6.23.1"),sQuery(id+"F0.wireOp",EDGE,"E6.23.2"),sQuery(id+"F0.wireOp",EDGE,"E6.23.3"),sQuery(id+"F0.wireOp",EDGE,"E6.23.4"),sQuery(id+"F0.wireOp",EDGE,"E6.24.1"),sQuery(id+"F0.wireOp",EDGE,"E6.24.2"),sQuery(id+"F0.wireOp",EDGE,"E6.24.3"),sQuery(id+"F0.wireOp",EDGE,"E6.24.4"),sQuery(id+"F0.wireOp",EDGE,"E6.25.1"),sQuery(id+"F0.wireOp",EDGE,"E6.25.2"),sQuery(id+"F0.wireOp",EDGE,"E6.25.3"),sQuery(id+"F0.wireOp",EDGE,"E6.25.4"),sQuery(id+"F0.wireOp",EDGE,"E6.26.1"),sQuery(id+"F0.wireOp",EDGE,"E6.26.2"),sQuery(id+"F0.wireOp",EDGE,"E6.26.3"),sQuery(id+"F0.wireOp",EDGE,"E6.26.4"),sQuery(id+"F0.wireOp",EDGE,"E6.27.1"),sQuery(id+"F0.wireOp",EDGE,"E6.27.2"),sQuery(id+"F0.wireOp",EDGE,"E6.27.3"),sQuery(id+"F0.wireOp",EDGE,"E6.27.4"),sQuery(id+"F0.wireOp",EDGE,"E6.28.1"),sQuery(id+"F0.wireOp",EDGE,"E6.28.2"),sQuery(id+"F0.wireOp",EDGE,"E6.28.3"),sQuery(id+"F0.wireOp",EDGE,"E6.28.4"),sQuery(id+"F0.wireOp",EDGE,"E6.29.1"),sQuery(id+"F0.wireOp",EDGE,"E6.29.2"),sQuery(id+"F0.wireOp",EDGE,"E6.29.3"),sQuery(id+"F0.wireOp",EDGE,"E6.29.4"),sQuery(id+"F0.wireOp",EDGE,"E6.30.1"),sQuery(id+"F0.wireOp",EDGE,"E6.30.2"),sQuery(id+"F0.wireOp",EDGE,"E6.30.3"),sQuery(id+"F0.wireOp",EDGE,"E6.30.4"),sQuery(id+"F0.wireOp",EDGE,"E6.31.1"),sQuery(id+"F0.wireOp",EDGE,"E6.31.2"),sQuery(id+"F0.wireOp",EDGE,"E6.31.3"),sQuery(id+"F0.wireOp",EDGE,"E6.31.4"),sQuery(id+"F0.wireOp",EDGE,"E6.32.1"),sQuery(id+"F0.wireOp",EDGE,"E6.32.2"),sQuery(id+"F0.wireOp",EDGE,"E6.32.3"),sQuery(id+"F0.wireOp",EDGE,"E6.32.4"),sQuery(id+"F0.wireOp",EDGE,"E6.33.1"),sQuery(id+"F0.wireOp",EDGE,"E6.33.2"),sQuery(id+"F0.wireOp",EDGE,"E6.33.3"),sQuery(id+"F0.wireOp",EDGE,"E6.33.4"),sQuery(id+"F0.wireOp",EDGE,"E6.34.1"),sQuery(id+"F0.wireOp",EDGE,"E6.34.2"),sQuery(id+"F0.wireOp",EDGE,"E6.34.3"),sQuery(id+"F0.wireOp",EDGE,"E6.34.4"),sQuery(id+"F0.wireOp",EDGE,"E6.35.1"),sQuery(id+"F0.wireOp",EDGE,"E6.35.2"),sQuery(id+"F0.wireOp",EDGE,"E6.35.3"),sQuery(id+"F0.wireOp",EDGE,"E6.35.4"),sQuery(id+"F0.wireOp",EDGE,"E6.36.1"),sQuery(id+"F0.wireOp",EDGE,"E6.36.2"),sQuery(id+"F0.wireOp",EDGE,"E6.36.3"),sQuery(id+"F0.wireOp",EDGE,"E6.36.4"),sQuery(id+"F0.wireOp",EDGE,"E6.37.1"),sQuery(id+"F0.wireOp",EDGE,"E6.37.2"),sQuery(id+"F0.wireOp",EDGE,"E6.37.3"),sQuery(id+"F0.wireOp",EDGE,"E6.37.4"),sQuery(id+"F0.wireOp",EDGE,"E6.38.1"),sQuery(id+"F0.wireOp",EDGE,"E6.38.2"),sQuery(id+"F0.wireOp",EDGE,"E6.38.3"),sQuery(id+"F0.wireOp",EDGE,"E6.38.4"),sQuery(id+"F0.wireOp",EDGE,"E6.39.1"),sQuery(id+"F0.wireOp",EDGE,"E6.39.2"),sQuery(id+"F0.wireOp",EDGE,"E6.39.3"),sQuery(id+"F0.wireOp",EDGE,"E6.39.4"),sQuery(id+"F0.wireOp",EDGE,"E6.40.1"),sQuery(id+"F0.wireOp",EDGE,"E6.40.2"),sQuery(id+"F0.wireOp",EDGE,"E6.40.3"),sQuery(id+"F0.wireOp",EDGE,"E6.40.4"),sQuery(id+"F0.wireOp",EDGE,"E6.41.1"),sQuery(id+"F0.wireOp",EDGE,"E6.41.2"),sQuery(id+"F0.wireOp",EDGE,"E6.41.3"),sQuery(id+"F0.wireOp",EDGE,"E6.41.4"),sQuery(id+"F0.wireOp",EDGE,"E6.42.1"),sQuery(id+"F0.wireOp",EDGE,"E6.42.2"),sQuery(id+"F0.wireOp",EDGE,"E6.42.3"),sQuery(id+"F0.wireOp",EDGE,"E6.42.4"),sQuery(id+"F0.wireOp",EDGE,"E6.43.1"),sQuery(id+"F0.wireOp",EDGE,"E6.43.2"),sQuery(id+"F0.wireOp",EDGE,"E6.43.3"),sQuery(id+"F0.wireOp",EDGE,"E6.43.4"),sQuery(id+"F0.wireOp",EDGE,"E7"),sQuery(id+"F0.wireOp",EDGE,"E8.1.0"),sQuery(id+"F0.wireOp",EDGE,"E8.2.0"),sQuery(id+"F0.wireOp",EDGE,"E8.3.0"),sQuery(id+"F0.wireOp",EDGE,"E8.4.0"),sQuery(id+"F0.wireOp",EDGE,"E8.5.0"),sQuery(id+"F0.wireOp",EDGE,"E8.6.0"),sQuery(id+"F0.wireOp",EDGE,"E8.7.0"),sQuery(id+"F0.wireOp",EDGE,"E8.8.0"),sQuery(id+"F0.wireOp",EDGE,"E8.9.0"),sQuery(id+"F0.wireOp",EDGE,"E8.10.0"),sQuery(id+"F0.wireOp",EDGE,"E8.11.0"),sQuery(id+"F0.wireOp",EDGE,"E8.12.0"),sQuery(id+"F0.wireOp",EDGE,"E8.13.0"),sQuery(id+"F0.wireOp",EDGE,"E8.14.0"),sQuery(id+"F0.wireOp",EDGE,"E8.15.0"),sQuery(id+"F0.wireOp",EDGE,"E8.16.0"),sQuery(id+"F0.wireOp",EDGE,"E8.17.0"),sQuery(id+"F0.wireOp",EDGE,"E8.18.0"),sQuery(id+"F0.wireOp",EDGE,"E8.19.0"),sQuery(id+"F0.wireOp",EDGE,"E8.20.0"),sQuery(id+"F0.wireOp",EDGE,"E8.21.0"),sQuery(id+"F0.wireOp",EDGE,"E8.22.0"),sQuery(id+"F0.wireOp",EDGE,"E8.23.0"),sQuery(id+"F0.wireOp",EDGE,"E8.24.0"),sQuery(id+"F0.wireOp",EDGE,"E8.25.0"),sQuery(id+"F0.wireOp",EDGE,"E8.26.0"),sQuery(id+"F0.wireOp",EDGE,"E8.27.0"),sQuery(id+"F0.wireOp",EDGE,"E8.28.0"),sQuery(id+"F0.wireOp",EDGE,"E8.29.0"),sQuery(id+"F0.wireOp",EDGE,"E8.30.0"),sQuery(id+"F0.wireOp",EDGE,"E8.31.0"),sQuery(id+"F0.wireOp",EDGE,"E8.32.0"),sQuery(id+"F0.wireOp",EDGE,"E8.33.0"),sQuery(id+"F0.wireOp",EDGE,"E8.34.0"),sQuery(id+"F0.wireOp",EDGE,"E8.35.0"),sQuery(id+"F0.wireOp",EDGE,"E8.36.0"),sQuery(id+"F0.wireOp",EDGE,"E8.37.0"),sQuery(id+"F0.wireOp",EDGE,"E8.38.0"),sQuery(id+"F0.wireOp",EDGE,"E8.39.0"),sQuery(id+"F0.wireOp",EDGE,"E8.40.0"),sQuery(id+"F0.wireOp",EDGE,"E8.41.0"),sQuery(id+"F0.wireOp",EDGE,"E8.42.0"),sQuery(id+"F0.wireOp",EDGE,"E8.43.0")])],"isStart":true})]});}
            var Q28;
            {var subQ0=sQuery(id+"F0.wireOp",EDGE,"E6.12.3");var subQ1=sQuery(id+"F0.wireOp",EDGE,"E6.12.1");Q28=makeQuery(id+"F2.opFillet","BLEND_EDGE",EDGE,{"blendedFrom":[makeQuery(id+"F1.opExtrude","SWEPT_EDGE",EDGE,{"disambiguationData":[OSD([sQuery(id+"F0.wireOp",EDGE,"E6.12.0"),subQ1,subQ0])]}),makeQuery(id+"F1.opExtrude","CAP_FACE",FACE,{"disambiguationData":[OSD([sQuery(id+"F0.wireOp",EDGE,"E0"),sQuery(id+"F0.wireOp",EDGE,"E1"),sQuery(id+"F0.wireOp",EDGE,"E2"),sQuery(id+"F0.wireOp",EDGE,"E4"),sQuery(id+"F0.wireOp",EDGE,"E5"),sQuery(id+"F0.wireOp",EDGE,"E6.1.1"),sQuery(id+"F0.wireOp",EDGE,"E6.1.2"),sQuery(id+"F0.wireOp",EDGE,"E6.1.3"),sQuery(id+"F0.wireOp",EDGE,"E6.1.4"),sQuery(id+"F0.wireOp",EDGE,"E6.2.1"),sQuery(id+"F0.wireOp",EDGE,"E6.2.2"),sQuery(id+"F0.wireOp",EDGE,"E6.2.3"),sQuery(id+"F0.wireOp",EDGE,"E6.2.4"),sQuery(id+"F0.wireOp",EDGE,"E6.3.1"),sQuery(id+"F0.wireOp",EDGE,"E6.3.2"),sQuery(id+"F0.wireOp",EDGE,"E6.3.3"),sQuery(id+"F0.wireOp",EDGE,"E6.3.4"),sQuery(id+"F0.wireOp",EDGE,"E6.4.1"),sQuery(id+"F0.wireOp",EDGE,"E6.4.2"),sQuery(id+"F0.wireOp",EDGE,"E6.4.3"),sQuery(id+"F0.wireOp",EDGE,"E6.4.4"),sQuery(id+"F0.wireOp",EDGE,"E6.5.1"),sQuery(id+"F0.wireOp",EDGE,"E6.5.2"),sQuery(id+"F0.wireOp",EDGE,"E6.5.3"),sQuery(id+"F0.wireOp",EDGE,"E6.5.4"),sQuery(id+"F0.wireOp",EDGE,"E6.6.1"),sQuery(id+"F0.wireOp",EDGE,"E6.6.2"),sQuery(id+"F0.wireOp",EDGE,"E6.6.3"),sQuery(id+"F0.wireOp",EDGE,"E6.6.4"),sQuery(id+"F0.wireOp",EDGE,"E6.7.1"),sQuery(id+"F0.wireOp",EDGE,"E6.7.2"),sQuery(id+"F0.wireOp",EDGE,"E6.7.3"),sQuery(id+"F0.wireOp",EDGE,"E6.7.4"),sQuery(id+"F0.wireOp",EDGE,"E6.8.1"),sQuery(id+"F0.wireOp",EDGE,"E6.8.2"),sQuery(id+"F0.wireOp",EDGE,"E6.8.3"),sQuery(id+"F0.wireOp",EDGE,"E6.8.4"),sQuery(id+"F0.wireOp",EDGE,"E6.9.1"),sQuery(id+"F0.wireOp",EDGE,"E6.9.2"),sQuery(id+"F0.wireOp",EDGE,"E6.9.3"),sQuery(id+"F0.wireOp",EDGE,"E6.9.4"),sQuery(id+"F0.wireOp",EDGE,"E6.10.1"),sQuery(id+"F0.wireOp",EDGE,"E6.10.2"),sQuery(id+"F0.wireOp",EDGE,"E6.10.3"),sQuery(id+"F0.wireOp",EDGE,"E6.10.4"),sQuery(id+"F0.wireOp",EDGE,"E6.11.1"),sQuery(id+"F0.wireOp",EDGE,"E6.11.2"),sQuery(id+"F0.wireOp",EDGE,"E6.11.3"),sQuery(id+"F0.wireOp",EDGE,"E6.11.4"),subQ1,sQuery(id+"F0.wireOp",EDGE,"E6.12.2"),subQ0,sQuery(id+"F0.wireOp",EDGE,"E6.12.4"),sQuery(id+"F0.wireOp",EDGE,"E6.13.1"),sQuery(id+"F0.wireOp",EDGE,"E6.13.2"),sQuery(id+"F0.wireOp",EDGE,"E6.13.3"),sQuery(id+"F0.wireOp",EDGE,"E6.13.4"),sQuery(id+"F0.wireOp",EDGE,"E6.14.1"),sQuery(id+"F0.wireOp",EDGE,"E6.14.2"),sQuery(id+"F0.wireOp",EDGE,"E6.14.3"),sQuery(id+"F0.wireOp",EDGE,"E6.14.4"),sQuery(id+"F0.wireOp",EDGE,"E6.15.1"),sQuery(id+"F0.wireOp",EDGE,"E6.15.2"),sQuery(id+"F0.wireOp",EDGE,"E6.15.3"),sQuery(id+"F0.wireOp",EDGE,"E6.15.4"),sQuery(id+"F0.wireOp",EDGE,"E6.16.1"),sQuery(id+"F0.wireOp",EDGE,"E6.16.2"),sQuery(id+"F0.wireOp",EDGE,"E6.16.3"),sQuery(id+"F0.wireOp",EDGE,"E6.16.4"),sQuery(id+"F0.wireOp",EDGE,"E6.17.1"),sQuery(id+"F0.wireOp",EDGE,"E6.17.2"),sQuery(id+"F0.wireOp",EDGE,"E6.17.3"),sQuery(id+"F0.wireOp",EDGE,"E6.17.4"),sQuery(id+"F0.wireOp",EDGE,"E6.18.1"),sQuery(id+"F0.wireOp",EDGE,"E6.18.2"),sQuery(id+"F0.wireOp",EDGE,"E6.18.3"),sQuery(id+"F0.wireOp",EDGE,"E6.18.4"),sQuery(id+"F0.wireOp",EDGE,"E6.19.1"),sQuery(id+"F0.wireOp",EDGE,"E6.19.2"),sQuery(id+"F0.wireOp",EDGE,"E6.19.3"),sQuery(id+"F0.wireOp",EDGE,"E6.19.4"),sQuery(id+"F0.wireOp",EDGE,"E6.20.1"),sQuery(id+"F0.wireOp",EDGE,"E6.20.2"),sQuery(id+"F0.wireOp",EDGE,"E6.20.3"),sQuery(id+"F0.wireOp",EDGE,"E6.20.4"),sQuery(id+"F0.wireOp",EDGE,"E6.21.1"),sQuery(id+"F0.wireOp",EDGE,"E6.21.2"),sQuery(id+"F0.wireOp",EDGE,"E6.21.3"),sQuery(id+"F0.wireOp",EDGE,"E6.21.4"),sQuery(id+"F0.wireOp",EDGE,"E6.22.1"),sQuery(id+"F0.wireOp",EDGE,"E6.22.2"),sQuery(id+"F0.wireOp",EDGE,"E6.22.3"),sQuery(id+"F0.wireOp",EDGE,"E6.22.4"),sQuery(id+"F0.wireOp",EDGE,"E6.23.1"),sQuery(id+"F0.wireOp",EDGE,"E6.23.2"),sQuery(id+"F0.wireOp",EDGE,"E6.23.3"),sQuery(id+"F0.wireOp",EDGE,"E6.23.4"),sQuery(id+"F0.wireOp",EDGE,"E6.24.1"),sQuery(id+"F0.wireOp",EDGE,"E6.24.2"),sQuery(id+"F0.wireOp",EDGE,"E6.24.3"),sQuery(id+"F0.wireOp",EDGE,"E6.24.4"),sQuery(id+"F0.wireOp",EDGE,"E6.25.1"),sQuery(id+"F0.wireOp",EDGE,"E6.25.2"),sQuery(id+"F0.wireOp",EDGE,"E6.25.3"),sQuery(id+"F0.wireOp",EDGE,"E6.25.4"),sQuery(id+"F0.wireOp",EDGE,"E6.26.1"),sQuery(id+"F0.wireOp",EDGE,"E6.26.2"),sQuery(id+"F0.wireOp",EDGE,"E6.26.3"),sQuery(id+"F0.wireOp",EDGE,"E6.26.4"),sQuery(id+"F0.wireOp",EDGE,"E6.27.1"),sQuery(id+"F0.wireOp",EDGE,"E6.27.2"),sQuery(id+"F0.wireOp",EDGE,"E6.27.3"),sQuery(id+"F0.wireOp",EDGE,"E6.27.4"),sQuery(id+"F0.wireOp",EDGE,"E6.28.1"),sQuery(id+"F0.wireOp",EDGE,"E6.28.2"),sQuery(id+"F0.wireOp",EDGE,"E6.28.3"),sQuery(id+"F0.wireOp",EDGE,"E6.28.4"),sQuery(id+"F0.wireOp",EDGE,"E6.29.1"),sQuery(id+"F0.wireOp",EDGE,"E6.29.2"),sQuery(id+"F0.wireOp",EDGE,"E6.29.3"),sQuery(id+"F0.wireOp",EDGE,"E6.29.4"),sQuery(id+"F0.wireOp",EDGE,"E6.30.1"),sQuery(id+"F0.wireOp",EDGE,"E6.30.2"),sQuery(id+"F0.wireOp",EDGE,"E6.30.3"),sQuery(id+"F0.wireOp",EDGE,"E6.30.4"),sQuery(id+"F0.wireOp",EDGE,"E6.31.1"),sQuery(id+"F0.wireOp",EDGE,"E6.31.2"),sQuery(id+"F0.wireOp",EDGE,"E6.31.3"),sQuery(id+"F0.wireOp",EDGE,"E6.31.4"),sQuery(id+"F0.wireOp",EDGE,"E6.32.1"),sQuery(id+"F0.wireOp",EDGE,"E6.32.2"),sQuery(id+"F0.wireOp",EDGE,"E6.32.3"),sQuery(id+"F0.wireOp",EDGE,"E6.32.4"),sQuery(id+"F0.wireOp",EDGE,"E6.33.1"),sQuery(id+"F0.wireOp",EDGE,"E6.33.2"),sQuery(id+"F0.wireOp",EDGE,"E6.33.3"),sQuery(id+"F0.wireOp",EDGE,"E6.33.4"),sQuery(id+"F0.wireOp",EDGE,"E6.34.1"),sQuery(id+"F0.wireOp",EDGE,"E6.34.2"),sQuery(id+"F0.wireOp",EDGE,"E6.34.3"),sQuery(id+"F0.wireOp",EDGE,"E6.34.4"),sQuery(id+"F0.wireOp",EDGE,"E6.35.1"),sQuery(id+"F0.wireOp",EDGE,"E6.35.2"),sQuery(id+"F0.wireOp",EDGE,"E6.35.3"),sQuery(id+"F0.wireOp",EDGE,"E6.35.4"),sQuery(id+"F0.wireOp",EDGE,"E6.36.1"),sQuery(id+"F0.wireOp",EDGE,"E6.36.2"),sQuery(id+"F0.wireOp",EDGE,"E6.36.3"),sQuery(id+"F0.wireOp",EDGE,"E6.36.4"),sQuery(id+"F0.wireOp",EDGE,"E6.37.1"),sQuery(id+"F0.wireOp",EDGE,"E6.37.2"),sQuery(id+"F0.wireOp",EDGE,"E6.37.3"),sQuery(id+"F0.wireOp",EDGE,"E6.37.4"),sQuery(id+"F0.wireOp",EDGE,"E6.38.1"),sQuery(id+"F0.wireOp",EDGE,"E6.38.2"),sQuery(id+"F0.wireOp",EDGE,"E6.38.3"),sQuery(id+"F0.wireOp",EDGE,"E6.38.4"),sQuery(id+"F0.wireOp",EDGE,"E6.39.1"),sQuery(id+"F0.wireOp",EDGE,"E6.39.2"),sQuery(id+"F0.wireOp",EDGE,"E6.39.3"),sQuery(id+"F0.wireOp",EDGE,"E6.39.4"),sQuery(id+"F0.wireOp",EDGE,"E6.40.1"),sQuery(id+"F0.wireOp",EDGE,"E6.40.2"),sQuery(id+"F0.wireOp",EDGE,"E6.40.3"),sQuery(id+"F0.wireOp",EDGE,"E6.40.4"),sQuery(id+"F0.wireOp",EDGE,"E6.41.1"),sQuery(id+"F0.wireOp",EDGE,"E6.41.2"),sQuery(id+"F0.wireOp",EDGE,"E6.41.3"),sQuery(id+"F0.wireOp",EDGE,"E6.41.4"),sQuery(id+"F0.wireOp",EDGE,"E6.42.1"),sQuery(id+"F0.wireOp",EDGE,"E6.42.2"),sQuery(id+"F0.wireOp",EDGE,"E6.42.3"),sQuery(id+"F0.wireOp",EDGE,"E6.42.4"),sQuery(id+"F0.wireOp",EDGE,"E6.43.1"),sQuery(id+"F0.wireOp",EDGE,"E6.43.2"),sQuery(id+"F0.wireOp",EDGE,"E6.43.3"),sQuery(id+"F0.wireOp",EDGE,"E6.43.4"),sQuery(id+"F0.wireOp",EDGE,"E7"),sQuery(id+"F0.wireOp",EDGE,"E8.1.0"),sQuery(id+"F0.wireOp",EDGE,"E8.2.0"),sQuery(id+"F0.wireOp",EDGE,"E8.3.0"),sQuery(id+"F0.wireOp",EDGE,"E8.4.0"),sQuery(id+"F0.wireOp",EDGE,"E8.5.0"),sQuery(id+"F0.wireOp",EDGE,"E8.6.0"),sQuery(id+"F0.wireOp",EDGE,"E8.7.0"),sQuery(id+"F0.wireOp",EDGE,"E8.8.0"),sQuery(id+"F0.wireOp",EDGE,"E8.9.0"),sQuery(id+"F0.wireOp",EDGE,"E8.10.0"),sQuery(id+"F0.wireOp",EDGE,"E8.11.0"),sQuery(id+"F0.wireOp",EDGE,"E8.12.0"),sQuery(id+"F0.wireOp",EDGE,"E8.13.0"),sQuery(id+"F0.wireOp",EDGE,"E8.14.0"),sQuery(id+"F0.wireOp",EDGE,"E8.15.0"),sQuery(id+"F0.wireOp",EDGE,"E8.16.0"),sQuery(id+"F0.wireOp",EDGE,"E8.17.0"),sQuery(id+"F0.wireOp",EDGE,"E8.18.0"),sQuery(id+"F0.wireOp",EDGE,"E8.19.0"),sQuery(id+"F0.wireOp",EDGE,"E8.20.0"),sQuery(id+"F0.wireOp",EDGE,"E8.21.0"),sQuery(id+"F0.wireOp",EDGE,"E8.22.0"),sQuery(id+"F0.wireOp",EDGE,"E8.23.0"),sQuery(id+"F0.wireOp",EDGE,"E8.24.0"),sQuery(id+"F0.wireOp",EDGE,"E8.25.0"),sQuery(id+"F0.wireOp",EDGE,"E8.26.0"),sQuery(id+"F0.wireOp",EDGE,"E8.27.0"),sQuery(id+"F0.wireOp",EDGE,"E8.28.0"),sQuery(id+"F0.wireOp",EDGE,"E8.29.0"),sQuery(id+"F0.wireOp",EDGE,"E8.30.0"),sQuery(id+"F0.wireOp",EDGE,"E8.31.0"),sQuery(id+"F0.wireOp",EDGE,"E8.32.0"),sQuery(id+"F0.wireOp",EDGE,"E8.33.0"),sQuery(id+"F0.wireOp",EDGE,"E8.34.0"),sQuery(id+"F0.wireOp",EDGE,"E8.35.0"),sQuery(id+"F0.wireOp",EDGE,"E8.36.0"),sQuery(id+"F0.wireOp",EDGE,"E8.37.0"),sQuery(id+"F0.wireOp",EDGE,"E8.38.0"),sQuery(id+"F0.wireOp",EDGE,"E8.39.0"),sQuery(id+"F0.wireOp",EDGE,"E8.40.0"),sQuery(id+"F0.wireOp",EDGE,"E8.41.0"),sQuery(id+"F0.wireOp",EDGE,"E8.42.0"),sQuery(id+"F0.wireOp",EDGE,"E8.43.0")])],"isStart":true})],"blendedInto":[makeQuery(id+"F1.opExtrude","CAP_FACE",FACE,{"disambiguationData":[OSD([sQuery(id+"F0.wireOp",EDGE,"E0"),sQuery(id+"F0.wireOp",EDGE,"E1"),sQuery(id+"F0.wireOp",EDGE,"E2"),sQuery(id+"F0.wireOp",EDGE,"E4"),sQuery(id+"F0.wireOp",EDGE,"E5"),sQuery(id+"F0.wireOp",EDGE,"E6.1.1"),sQuery(id+"F0.wireOp",EDGE,"E6.1.2"),sQuery(id+"F0.wireOp",EDGE,"E6.1.3"),sQuery(id+"F0.wireOp",EDGE,"E6.1.4"),sQuery(id+"F0.wireOp",EDGE,"E6.2.1"),sQuery(id+"F0.wireOp",EDGE,"E6.2.2"),sQuery(id+"F0.wireOp",EDGE,"E6.2.3"),sQuery(id+"F0.wireOp",EDGE,"E6.2.4"),sQuery(id+"F0.wireOp",EDGE,"E6.3.1"),sQuery(id+"F0.wireOp",EDGE,"E6.3.2"),sQuery(id+"F0.wireOp",EDGE,"E6.3.3"),sQuery(id+"F0.wireOp",EDGE,"E6.3.4"),sQuery(id+"F0.wireOp",EDGE,"E6.4.1"),sQuery(id+"F0.wireOp",EDGE,"E6.4.2"),sQuery(id+"F0.wireOp",EDGE,"E6.4.3"),sQuery(id+"F0.wireOp",EDGE,"E6.4.4"),sQuery(id+"F0.wireOp",EDGE,"E6.5.1"),sQuery(id+"F0.wireOp",EDGE,"E6.5.2"),sQuery(id+"F0.wireOp",EDGE,"E6.5.3"),sQuery(id+"F0.wireOp",EDGE,"E6.5.4"),sQuery(id+"F0.wireOp",EDGE,"E6.6.1"),sQuery(id+"F0.wireOp",EDGE,"E6.6.2"),sQuery(id+"F0.wireOp",EDGE,"E6.6.3"),sQuery(id+"F0.wireOp",EDGE,"E6.6.4"),sQuery(id+"F0.wireOp",EDGE,"E6.7.1"),sQuery(id+"F0.wireOp",EDGE,"E6.7.2"),sQuery(id+"F0.wireOp",EDGE,"E6.7.3"),sQuery(id+"F0.wireOp",EDGE,"E6.7.4"),sQuery(id+"F0.wireOp",EDGE,"E6.8.1"),sQuery(id+"F0.wireOp",EDGE,"E6.8.2"),sQuery(id+"F0.wireOp",EDGE,"E6.8.3"),sQuery(id+"F0.wireOp",EDGE,"E6.8.4"),sQuery(id+"F0.wireOp",EDGE,"E6.9.1"),sQuery(id+"F0.wireOp",EDGE,"E6.9.2"),sQuery(id+"F0.wireOp",EDGE,"E6.9.3"),sQuery(id+"F0.wireOp",EDGE,"E6.9.4"),sQuery(id+"F0.wireOp",EDGE,"E6.10.1"),sQuery(id+"F0.wireOp",EDGE,"E6.10.2"),sQuery(id+"F0.wireOp",EDGE,"E6.10.3"),sQuery(id+"F0.wireOp",EDGE,"E6.10.4"),sQuery(id+"F0.wireOp",EDGE,"E6.11.1"),sQuery(id+"F0.wireOp",EDGE,"E6.11.2"),sQuery(id+"F0.wireOp",EDGE,"E6.11.3"),sQuery(id+"F0.wireOp",EDGE,"E6.11.4"),subQ1,sQuery(id+"F0.wireOp",EDGE,"E6.12.2"),subQ0,sQuery(id+"F0.wireOp",EDGE,"E6.12.4"),sQuery(id+"F0.wireOp",EDGE,"E6.13.1"),sQuery(id+"F0.wireOp",EDGE,"E6.13.2"),sQuery(id+"F0.wireOp",EDGE,"E6.13.3"),sQuery(id+"F0.wireOp",EDGE,"E6.13.4"),sQuery(id+"F0.wireOp",EDGE,"E6.14.1"),sQuery(id+"F0.wireOp",EDGE,"E6.14.2"),sQuery(id+"F0.wireOp",EDGE,"E6.14.3"),sQuery(id+"F0.wireOp",EDGE,"E6.14.4"),sQuery(id+"F0.wireOp",EDGE,"E6.15.1"),sQuery(id+"F0.wireOp",EDGE,"E6.15.2"),sQuery(id+"F0.wireOp",EDGE,"E6.15.3"),sQuery(id+"F0.wireOp",EDGE,"E6.15.4"),sQuery(id+"F0.wireOp",EDGE,"E6.16.1"),sQuery(id+"F0.wireOp",EDGE,"E6.16.2"),sQuery(id+"F0.wireOp",EDGE,"E6.16.3"),sQuery(id+"F0.wireOp",EDGE,"E6.16.4"),sQuery(id+"F0.wireOp",EDGE,"E6.17.1"),sQuery(id+"F0.wireOp",EDGE,"E6.17.2"),sQuery(id+"F0.wireOp",EDGE,"E6.17.3"),sQuery(id+"F0.wireOp",EDGE,"E6.17.4"),sQuery(id+"F0.wireOp",EDGE,"E6.18.1"),sQuery(id+"F0.wireOp",EDGE,"E6.18.2"),sQuery(id+"F0.wireOp",EDGE,"E6.18.3"),sQuery(id+"F0.wireOp",EDGE,"E6.18.4"),sQuery(id+"F0.wireOp",EDGE,"E6.19.1"),sQuery(id+"F0.wireOp",EDGE,"E6.19.2"),sQuery(id+"F0.wireOp",EDGE,"E6.19.3"),sQuery(id+"F0.wireOp",EDGE,"E6.19.4"),sQuery(id+"F0.wireOp",EDGE,"E6.20.1"),sQuery(id+"F0.wireOp",EDGE,"E6.20.2"),sQuery(id+"F0.wireOp",EDGE,"E6.20.3"),sQuery(id+"F0.wireOp",EDGE,"E6.20.4"),sQuery(id+"F0.wireOp",EDGE,"E6.21.1"),sQuery(id+"F0.wireOp",EDGE,"E6.21.2"),sQuery(id+"F0.wireOp",EDGE,"E6.21.3"),sQuery(id+"F0.wireOp",EDGE,"E6.21.4"),sQuery(id+"F0.wireOp",EDGE,"E6.22.1"),sQuery(id+"F0.wireOp",EDGE,"E6.22.2"),sQuery(id+"F0.wireOp",EDGE,"E6.22.3"),sQuery(id+"F0.wireOp",EDGE,"E6.22.4"),sQuery(id+"F0.wireOp",EDGE,"E6.23.1"),sQuery(id+"F0.wireOp",EDGE,"E6.23.2"),sQuery(id+"F0.wireOp",EDGE,"E6.23.3"),sQuery(id+"F0.wireOp",EDGE,"E6.23.4"),sQuery(id+"F0.wireOp",EDGE,"E6.24.1"),sQuery(id+"F0.wireOp",EDGE,"E6.24.2"),sQuery(id+"F0.wireOp",EDGE,"E6.24.3"),sQuery(id+"F0.wireOp",EDGE,"E6.24.4"),sQuery(id+"F0.wireOp",EDGE,"E6.25.1"),sQuery(id+"F0.wireOp",EDGE,"E6.25.2"),sQuery(id+"F0.wireOp",EDGE,"E6.25.3"),sQuery(id+"F0.wireOp",EDGE,"E6.25.4"),sQuery(id+"F0.wireOp",EDGE,"E6.26.1"),sQuery(id+"F0.wireOp",EDGE,"E6.26.2"),sQuery(id+"F0.wireOp",EDGE,"E6.26.3"),sQuery(id+"F0.wireOp",EDGE,"E6.26.4"),sQuery(id+"F0.wireOp",EDGE,"E6.27.1"),sQuery(id+"F0.wireOp",EDGE,"E6.27.2"),sQuery(id+"F0.wireOp",EDGE,"E6.27.3"),sQuery(id+"F0.wireOp",EDGE,"E6.27.4"),sQuery(id+"F0.wireOp",EDGE,"E6.28.1"),sQuery(id+"F0.wireOp",EDGE,"E6.28.2"),sQuery(id+"F0.wireOp",EDGE,"E6.28.3"),sQuery(id+"F0.wireOp",EDGE,"E6.28.4"),sQuery(id+"F0.wireOp",EDGE,"E6.29.1"),sQuery(id+"F0.wireOp",EDGE,"E6.29.2"),sQuery(id+"F0.wireOp",EDGE,"E6.29.3"),sQuery(id+"F0.wireOp",EDGE,"E6.29.4"),sQuery(id+"F0.wireOp",EDGE,"E6.30.1"),sQuery(id+"F0.wireOp",EDGE,"E6.30.2"),sQuery(id+"F0.wireOp",EDGE,"E6.30.3"),sQuery(id+"F0.wireOp",EDGE,"E6.30.4"),sQuery(id+"F0.wireOp",EDGE,"E6.31.1"),sQuery(id+"F0.wireOp",EDGE,"E6.31.2"),sQuery(id+"F0.wireOp",EDGE,"E6.31.3"),sQuery(id+"F0.wireOp",EDGE,"E6.31.4"),sQuery(id+"F0.wireOp",EDGE,"E6.32.1"),sQuery(id+"F0.wireOp",EDGE,"E6.32.2"),sQuery(id+"F0.wireOp",EDGE,"E6.32.3"),sQuery(id+"F0.wireOp",EDGE,"E6.32.4"),sQuery(id+"F0.wireOp",EDGE,"E6.33.1"),sQuery(id+"F0.wireOp",EDGE,"E6.33.2"),sQuery(id+"F0.wireOp",EDGE,"E6.33.3"),sQuery(id+"F0.wireOp",EDGE,"E6.33.4"),sQuery(id+"F0.wireOp",EDGE,"E6.34.1"),sQuery(id+"F0.wireOp",EDGE,"E6.34.2"),sQuery(id+"F0.wireOp",EDGE,"E6.34.3"),sQuery(id+"F0.wireOp",EDGE,"E6.34.4"),sQuery(id+"F0.wireOp",EDGE,"E6.35.1"),sQuery(id+"F0.wireOp",EDGE,"E6.35.2"),sQuery(id+"F0.wireOp",EDGE,"E6.35.3"),sQuery(id+"F0.wireOp",EDGE,"E6.35.4"),sQuery(id+"F0.wireOp",EDGE,"E6.36.1"),sQuery(id+"F0.wireOp",EDGE,"E6.36.2"),sQuery(id+"F0.wireOp",EDGE,"E6.36.3"),sQuery(id+"F0.wireOp",EDGE,"E6.36.4"),sQuery(id+"F0.wireOp",EDGE,"E6.37.1"),sQuery(id+"F0.wireOp",EDGE,"E6.37.2"),sQuery(id+"F0.wireOp",EDGE,"E6.37.3"),sQuery(id+"F0.wireOp",EDGE,"E6.37.4"),sQuery(id+"F0.wireOp",EDGE,"E6.38.1"),sQuery(id+"F0.wireOp",EDGE,"E6.38.2"),sQuery(id+"F0.wireOp",EDGE,"E6.38.3"),sQuery(id+"F0.wireOp",EDGE,"E6.38.4"),sQuery(id+"F0.wireOp",EDGE,"E6.39.1"),sQuery(id+"F0.wireOp",EDGE,"E6.39.2"),sQuery(id+"F0.wireOp",EDGE,"E6.39.3"),sQuery(id+"F0.wireOp",EDGE,"E6.39.4"),sQuery(id+"F0.wireOp",EDGE,"E6.40.1"),sQuery(id+"F0.wireOp",EDGE,"E6.40.2"),sQuery(id+"F0.wireOp",EDGE,"E6.40.3"),sQuery(id+"F0.wireOp",EDGE,"E6.40.4"),sQuery(id+"F0.wireOp",EDGE,"E6.41.1"),sQuery(id+"F0.wireOp",EDGE,"E6.41.2"),sQuery(id+"F0.wireOp",EDGE,"E6.41.3"),sQuery(id+"F0.wireOp",EDGE,"E6.41.4"),sQuery(id+"F0.wireOp",EDGE,"E6.42.1"),sQuery(id+"F0.wireOp",EDGE,"E6.42.2"),sQuery(id+"F0.wireOp",EDGE,"E6.42.3"),sQuery(id+"F0.wireOp",EDGE,"E6.42.4"),sQuery(id+"F0.wireOp",EDGE,"E6.43.1"),sQuery(id+"F0.wireOp",EDGE,"E6.43.2"),sQuery(id+"F0.wireOp",EDGE,"E6.43.3"),sQuery(id+"F0.wireOp",EDGE,"E6.43.4"),sQuery(id+"F0.wireOp",EDGE,"E7"),sQuery(id+"F0.wireOp",EDGE,"E8.1.0"),sQuery(id+"F0.wireOp",EDGE,"E8.2.0"),sQuery(id+"F0.wireOp",EDGE,"E8.3.0"),sQuery(id+"F0.wireOp",EDGE,"E8.4.0"),sQuery(id+"F0.wireOp",EDGE,"E8.5.0"),sQuery(id+"F0.wireOp",EDGE,"E8.6.0"),sQuery(id+"F0.wireOp",EDGE,"E8.7.0"),sQuery(id+"F0.wireOp",EDGE,"E8.8.0"),sQuery(id+"F0.wireOp",EDGE,"E8.9.0"),sQuery(id+"F0.wireOp",EDGE,"E8.10.0"),sQuery(id+"F0.wireOp",EDGE,"E8.11.0"),sQuery(id+"F0.wireOp",EDGE,"E8.12.0"),sQuery(id+"F0.wireOp",EDGE,"E8.13.0"),sQuery(id+"F0.wireOp",EDGE,"E8.14.0"),sQuery(id+"F0.wireOp",EDGE,"E8.15.0"),sQuery(id+"F0.wireOp",EDGE,"E8.16.0"),sQuery(id+"F0.wireOp",EDGE,"E8.17.0"),sQuery(id+"F0.wireOp",EDGE,"E8.18.0"),sQuery(id+"F0.wireOp",EDGE,"E8.19.0"),sQuery(id+"F0.wireOp",EDGE,"E8.20.0"),sQuery(id+"F0.wireOp",EDGE,"E8.21.0"),sQuery(id+"F0.wireOp",EDGE,"E8.22.0"),sQuery(id+"F0.wireOp",EDGE,"E8.23.0"),sQuery(id+"F0.wireOp",EDGE,"E8.24.0"),sQuery(id+"F0.wireOp",EDGE,"E8.25.0"),sQuery(id+"F0.wireOp",EDGE,"E8.26.0"),sQuery(id+"F0.wireOp",EDGE,"E8.27.0"),sQuery(id+"F0.wireOp",EDGE,"E8.28.0"),sQuery(id+"F0.wireOp",EDGE,"E8.29.0"),sQuery(id+"F0.wireOp",EDGE,"E8.30.0"),sQuery(id+"F0.wireOp",EDGE,"E8.31.0"),sQuery(id+"F0.wireOp",EDGE,"E8.32.0"),sQuery(id+"F0.wireOp",EDGE,"E8.33.0"),sQuery(id+"F0.wireOp",EDGE,"E8.34.0"),sQuery(id+"F0.wireOp",EDGE,"E8.35.0"),sQuery(id+"F0.wireOp",EDGE,"E8.36.0"),sQuery(id+"F0.wireOp",EDGE,"E8.37.0"),sQuery(id+"F0.wireOp",EDGE,"E8.38.0"),sQuery(id+"F0.wireOp",EDGE,"E8.39.0"),sQuery(id+"F0.wireOp",EDGE,"E8.40.0"),sQuery(id+"F0.wireOp",EDGE,"E8.41.0"),sQuery(id+"F0.wireOp",EDGE,"E8.42.0"),sQuery(id+"F0.wireOp",EDGE,"E8.43.0")])],"isStart":true})]});}
            var Q29;
            {var subQ0=sQuery(id+"F0.wireOp",EDGE,"E6.16.3");var subQ1=sQuery(id+"F0.wireOp",EDGE,"E6.16.1");Q29=makeQuery(id+"F2.opFillet","BLEND_EDGE",EDGE,{"blendedFrom":[makeQuery(id+"F1.opExtrude","SWEPT_EDGE",EDGE,{"disambiguationData":[OSD([sQuery(id+"F0.wireOp",EDGE,"E6.16.0"),subQ1,subQ0])]}),makeQuery(id+"F1.opExtrude","CAP_FACE",FACE,{"disambiguationData":[OSD([sQuery(id+"F0.wireOp",EDGE,"E0"),sQuery(id+"F0.wireOp",EDGE,"E1"),sQuery(id+"F0.wireOp",EDGE,"E2"),sQuery(id+"F0.wireOp",EDGE,"E4"),sQuery(id+"F0.wireOp",EDGE,"E5"),sQuery(id+"F0.wireOp",EDGE,"E6.1.1"),sQuery(id+"F0.wireOp",EDGE,"E6.1.2"),sQuery(id+"F0.wireOp",EDGE,"E6.1.3"),sQuery(id+"F0.wireOp",EDGE,"E6.1.4"),sQuery(id+"F0.wireOp",EDGE,"E6.2.1"),sQuery(id+"F0.wireOp",EDGE,"E6.2.2"),sQuery(id+"F0.wireOp",EDGE,"E6.2.3"),sQuery(id+"F0.wireOp",EDGE,"E6.2.4"),sQuery(id+"F0.wireOp",EDGE,"E6.3.1"),sQuery(id+"F0.wireOp",EDGE,"E6.3.2"),sQuery(id+"F0.wireOp",EDGE,"E6.3.3"),sQuery(id+"F0.wireOp",EDGE,"E6.3.4"),sQuery(id+"F0.wireOp",EDGE,"E6.4.1"),sQuery(id+"F0.wireOp",EDGE,"E6.4.2"),sQuery(id+"F0.wireOp",EDGE,"E6.4.3"),sQuery(id+"F0.wireOp",EDGE,"E6.4.4"),sQuery(id+"F0.wireOp",EDGE,"E6.5.1"),sQuery(id+"F0.wireOp",EDGE,"E6.5.2"),sQuery(id+"F0.wireOp",EDGE,"E6.5.3"),sQuery(id+"F0.wireOp",EDGE,"E6.5.4"),sQuery(id+"F0.wireOp",EDGE,"E6.6.1"),sQuery(id+"F0.wireOp",EDGE,"E6.6.2"),sQuery(id+"F0.wireOp",EDGE,"E6.6.3"),sQuery(id+"F0.wireOp",EDGE,"E6.6.4"),sQuery(id+"F0.wireOp",EDGE,"E6.7.1"),sQuery(id+"F0.wireOp",EDGE,"E6.7.2"),sQuery(id+"F0.wireOp",EDGE,"E6.7.3"),sQuery(id+"F0.wireOp",EDGE,"E6.7.4"),sQuery(id+"F0.wireOp",EDGE,"E6.8.1"),sQuery(id+"F0.wireOp",EDGE,"E6.8.2"),sQuery(id+"F0.wireOp",EDGE,"E6.8.3"),sQuery(id+"F0.wireOp",EDGE,"E6.8.4"),sQuery(id+"F0.wireOp",EDGE,"E6.9.1"),sQuery(id+"F0.wireOp",EDGE,"E6.9.2"),sQuery(id+"F0.wireOp",EDGE,"E6.9.3"),sQuery(id+"F0.wireOp",EDGE,"E6.9.4"),sQuery(id+"F0.wireOp",EDGE,"E6.10.1"),sQuery(id+"F0.wireOp",EDGE,"E6.10.2"),sQuery(id+"F0.wireOp",EDGE,"E6.10.3"),sQuery(id+"F0.wireOp",EDGE,"E6.10.4"),sQuery(id+"F0.wireOp",EDGE,"E6.11.1"),sQuery(id+"F0.wireOp",EDGE,"E6.11.2"),sQuery(id+"F0.wireOp",EDGE,"E6.11.3"),sQuery(id+"F0.wireOp",EDGE,"E6.11.4"),sQuery(id+"F0.wireOp",EDGE,"E6.12.1"),sQuery(id+"F0.wireOp",EDGE,"E6.12.2"),sQuery(id+"F0.wireOp",EDGE,"E6.12.3"),sQuery(id+"F0.wireOp",EDGE,"E6.12.4"),sQuery(id+"F0.wireOp",EDGE,"E6.13.1"),sQuery(id+"F0.wireOp",EDGE,"E6.13.2"),sQuery(id+"F0.wireOp",EDGE,"E6.13.3"),sQuery(id+"F0.wireOp",EDGE,"E6.13.4"),sQuery(id+"F0.wireOp",EDGE,"E6.14.1"),sQuery(id+"F0.wireOp",EDGE,"E6.14.2"),sQuery(id+"F0.wireOp",EDGE,"E6.14.3"),sQuery(id+"F0.wireOp",EDGE,"E6.14.4"),sQuery(id+"F0.wireOp",EDGE,"E6.15.1"),sQuery(id+"F0.wireOp",EDGE,"E6.15.2"),sQuery(id+"F0.wireOp",EDGE,"E6.15.3"),sQuery(id+"F0.wireOp",EDGE,"E6.15.4"),subQ1,sQuery(id+"F0.wireOp",EDGE,"E6.16.2"),subQ0,sQuery(id+"F0.wireOp",EDGE,"E6.16.4"),sQuery(id+"F0.wireOp",EDGE,"E6.17.1"),sQuery(id+"F0.wireOp",EDGE,"E6.17.2"),sQuery(id+"F0.wireOp",EDGE,"E6.17.3"),sQuery(id+"F0.wireOp",EDGE,"E6.17.4"),sQuery(id+"F0.wireOp",EDGE,"E6.18.1"),sQuery(id+"F0.wireOp",EDGE,"E6.18.2"),sQuery(id+"F0.wireOp",EDGE,"E6.18.3"),sQuery(id+"F0.wireOp",EDGE,"E6.18.4"),sQuery(id+"F0.wireOp",EDGE,"E6.19.1"),sQuery(id+"F0.wireOp",EDGE,"E6.19.2"),sQuery(id+"F0.wireOp",EDGE,"E6.19.3"),sQuery(id+"F0.wireOp",EDGE,"E6.19.4"),sQuery(id+"F0.wireOp",EDGE,"E6.20.1"),sQuery(id+"F0.wireOp",EDGE,"E6.20.2"),sQuery(id+"F0.wireOp",EDGE,"E6.20.3"),sQuery(id+"F0.wireOp",EDGE,"E6.20.4"),sQuery(id+"F0.wireOp",EDGE,"E6.21.1"),sQuery(id+"F0.wireOp",EDGE,"E6.21.2"),sQuery(id+"F0.wireOp",EDGE,"E6.21.3"),sQuery(id+"F0.wireOp",EDGE,"E6.21.4"),sQuery(id+"F0.wireOp",EDGE,"E6.22.1"),sQuery(id+"F0.wireOp",EDGE,"E6.22.2"),sQuery(id+"F0.wireOp",EDGE,"E6.22.3"),sQuery(id+"F0.wireOp",EDGE,"E6.22.4"),sQuery(id+"F0.wireOp",EDGE,"E6.23.1"),sQuery(id+"F0.wireOp",EDGE,"E6.23.2"),sQuery(id+"F0.wireOp",EDGE,"E6.23.3"),sQuery(id+"F0.wireOp",EDGE,"E6.23.4"),sQuery(id+"F0.wireOp",EDGE,"E6.24.1"),sQuery(id+"F0.wireOp",EDGE,"E6.24.2"),sQuery(id+"F0.wireOp",EDGE,"E6.24.3"),sQuery(id+"F0.wireOp",EDGE,"E6.24.4"),sQuery(id+"F0.wireOp",EDGE,"E6.25.1"),sQuery(id+"F0.wireOp",EDGE,"E6.25.2"),sQuery(id+"F0.wireOp",EDGE,"E6.25.3"),sQuery(id+"F0.wireOp",EDGE,"E6.25.4"),sQuery(id+"F0.wireOp",EDGE,"E6.26.1"),sQuery(id+"F0.wireOp",EDGE,"E6.26.2"),sQuery(id+"F0.wireOp",EDGE,"E6.26.3"),sQuery(id+"F0.wireOp",EDGE,"E6.26.4"),sQuery(id+"F0.wireOp",EDGE,"E6.27.1"),sQuery(id+"F0.wireOp",EDGE,"E6.27.2"),sQuery(id+"F0.wireOp",EDGE,"E6.27.3"),sQuery(id+"F0.wireOp",EDGE,"E6.27.4"),sQuery(id+"F0.wireOp",EDGE,"E6.28.1"),sQuery(id+"F0.wireOp",EDGE,"E6.28.2"),sQuery(id+"F0.wireOp",EDGE,"E6.28.3"),sQuery(id+"F0.wireOp",EDGE,"E6.28.4"),sQuery(id+"F0.wireOp",EDGE,"E6.29.1"),sQuery(id+"F0.wireOp",EDGE,"E6.29.2"),sQuery(id+"F0.wireOp",EDGE,"E6.29.3"),sQuery(id+"F0.wireOp",EDGE,"E6.29.4"),sQuery(id+"F0.wireOp",EDGE,"E6.30.1"),sQuery(id+"F0.wireOp",EDGE,"E6.30.2"),sQuery(id+"F0.wireOp",EDGE,"E6.30.3"),sQuery(id+"F0.wireOp",EDGE,"E6.30.4"),sQuery(id+"F0.wireOp",EDGE,"E6.31.1"),sQuery(id+"F0.wireOp",EDGE,"E6.31.2"),sQuery(id+"F0.wireOp",EDGE,"E6.31.3"),sQuery(id+"F0.wireOp",EDGE,"E6.31.4"),sQuery(id+"F0.wireOp",EDGE,"E6.32.1"),sQuery(id+"F0.wireOp",EDGE,"E6.32.2"),sQuery(id+"F0.wireOp",EDGE,"E6.32.3"),sQuery(id+"F0.wireOp",EDGE,"E6.32.4"),sQuery(id+"F0.wireOp",EDGE,"E6.33.1"),sQuery(id+"F0.wireOp",EDGE,"E6.33.2"),sQuery(id+"F0.wireOp",EDGE,"E6.33.3"),sQuery(id+"F0.wireOp",EDGE,"E6.33.4"),sQuery(id+"F0.wireOp",EDGE,"E6.34.1"),sQuery(id+"F0.wireOp",EDGE,"E6.34.2"),sQuery(id+"F0.wireOp",EDGE,"E6.34.3"),sQuery(id+"F0.wireOp",EDGE,"E6.34.4"),sQuery(id+"F0.wireOp",EDGE,"E6.35.1"),sQuery(id+"F0.wireOp",EDGE,"E6.35.2"),sQuery(id+"F0.wireOp",EDGE,"E6.35.3"),sQuery(id+"F0.wireOp",EDGE,"E6.35.4"),sQuery(id+"F0.wireOp",EDGE,"E6.36.1"),sQuery(id+"F0.wireOp",EDGE,"E6.36.2"),sQuery(id+"F0.wireOp",EDGE,"E6.36.3"),sQuery(id+"F0.wireOp",EDGE,"E6.36.4"),sQuery(id+"F0.wireOp",EDGE,"E6.37.1"),sQuery(id+"F0.wireOp",EDGE,"E6.37.2"),sQuery(id+"F0.wireOp",EDGE,"E6.37.3"),sQuery(id+"F0.wireOp",EDGE,"E6.37.4"),sQuery(id+"F0.wireOp",EDGE,"E6.38.1"),sQuery(id+"F0.wireOp",EDGE,"E6.38.2"),sQuery(id+"F0.wireOp",EDGE,"E6.38.3"),sQuery(id+"F0.wireOp",EDGE,"E6.38.4"),sQuery(id+"F0.wireOp",EDGE,"E6.39.1"),sQuery(id+"F0.wireOp",EDGE,"E6.39.2"),sQuery(id+"F0.wireOp",EDGE,"E6.39.3"),sQuery(id+"F0.wireOp",EDGE,"E6.39.4"),sQuery(id+"F0.wireOp",EDGE,"E6.40.1"),sQuery(id+"F0.wireOp",EDGE,"E6.40.2"),sQuery(id+"F0.wireOp",EDGE,"E6.40.3"),sQuery(id+"F0.wireOp",EDGE,"E6.40.4"),sQuery(id+"F0.wireOp",EDGE,"E6.41.1"),sQuery(id+"F0.wireOp",EDGE,"E6.41.2"),sQuery(id+"F0.wireOp",EDGE,"E6.41.3"),sQuery(id+"F0.wireOp",EDGE,"E6.41.4"),sQuery(id+"F0.wireOp",EDGE,"E6.42.1"),sQuery(id+"F0.wireOp",EDGE,"E6.42.2"),sQuery(id+"F0.wireOp",EDGE,"E6.42.3"),sQuery(id+"F0.wireOp",EDGE,"E6.42.4"),sQuery(id+"F0.wireOp",EDGE,"E6.43.1"),sQuery(id+"F0.wireOp",EDGE,"E6.43.2"),sQuery(id+"F0.wireOp",EDGE,"E6.43.3"),sQuery(id+"F0.wireOp",EDGE,"E6.43.4"),sQuery(id+"F0.wireOp",EDGE,"E7"),sQuery(id+"F0.wireOp",EDGE,"E8.1.0"),sQuery(id+"F0.wireOp",EDGE,"E8.2.0"),sQuery(id+"F0.wireOp",EDGE,"E8.3.0"),sQuery(id+"F0.wireOp",EDGE,"E8.4.0"),sQuery(id+"F0.wireOp",EDGE,"E8.5.0"),sQuery(id+"F0.wireOp",EDGE,"E8.6.0"),sQuery(id+"F0.wireOp",EDGE,"E8.7.0"),sQuery(id+"F0.wireOp",EDGE,"E8.8.0"),sQuery(id+"F0.wireOp",EDGE,"E8.9.0"),sQuery(id+"F0.wireOp",EDGE,"E8.10.0"),sQuery(id+"F0.wireOp",EDGE,"E8.11.0"),sQuery(id+"F0.wireOp",EDGE,"E8.12.0"),sQuery(id+"F0.wireOp",EDGE,"E8.13.0"),sQuery(id+"F0.wireOp",EDGE,"E8.14.0"),sQuery(id+"F0.wireOp",EDGE,"E8.15.0"),sQuery(id+"F0.wireOp",EDGE,"E8.16.0"),sQuery(id+"F0.wireOp",EDGE,"E8.17.0"),sQuery(id+"F0.wireOp",EDGE,"E8.18.0"),sQuery(id+"F0.wireOp",EDGE,"E8.19.0"),sQuery(id+"F0.wireOp",EDGE,"E8.20.0"),sQuery(id+"F0.wireOp",EDGE,"E8.21.0"),sQuery(id+"F0.wireOp",EDGE,"E8.22.0"),sQuery(id+"F0.wireOp",EDGE,"E8.23.0"),sQuery(id+"F0.wireOp",EDGE,"E8.24.0"),sQuery(id+"F0.wireOp",EDGE,"E8.25.0"),sQuery(id+"F0.wireOp",EDGE,"E8.26.0"),sQuery(id+"F0.wireOp",EDGE,"E8.27.0"),sQuery(id+"F0.wireOp",EDGE,"E8.28.0"),sQuery(id+"F0.wireOp",EDGE,"E8.29.0"),sQuery(id+"F0.wireOp",EDGE,"E8.30.0"),sQuery(id+"F0.wireOp",EDGE,"E8.31.0"),sQuery(id+"F0.wireOp",EDGE,"E8.32.0"),sQuery(id+"F0.wireOp",EDGE,"E8.33.0"),sQuery(id+"F0.wireOp",EDGE,"E8.34.0"),sQuery(id+"F0.wireOp",EDGE,"E8.35.0"),sQuery(id+"F0.wireOp",EDGE,"E8.36.0"),sQuery(id+"F0.wireOp",EDGE,"E8.37.0"),sQuery(id+"F0.wireOp",EDGE,"E8.38.0"),sQuery(id+"F0.wireOp",EDGE,"E8.39.0"),sQuery(id+"F0.wireOp",EDGE,"E8.40.0"),sQuery(id+"F0.wireOp",EDGE,"E8.41.0"),sQuery(id+"F0.wireOp",EDGE,"E8.42.0"),sQuery(id+"F0.wireOp",EDGE,"E8.43.0")])],"isStart":true})],"blendedInto":[makeQuery(id+"F1.opExtrude","CAP_FACE",FACE,{"disambiguationData":[OSD([sQuery(id+"F0.wireOp",EDGE,"E0"),sQuery(id+"F0.wireOp",EDGE,"E1"),sQuery(id+"F0.wireOp",EDGE,"E2"),sQuery(id+"F0.wireOp",EDGE,"E4"),sQuery(id+"F0.wireOp",EDGE,"E5"),sQuery(id+"F0.wireOp",EDGE,"E6.1.1"),sQuery(id+"F0.wireOp",EDGE,"E6.1.2"),sQuery(id+"F0.wireOp",EDGE,"E6.1.3"),sQuery(id+"F0.wireOp",EDGE,"E6.1.4"),sQuery(id+"F0.wireOp",EDGE,"E6.2.1"),sQuery(id+"F0.wireOp",EDGE,"E6.2.2"),sQuery(id+"F0.wireOp",EDGE,"E6.2.3"),sQuery(id+"F0.wireOp",EDGE,"E6.2.4"),sQuery(id+"F0.wireOp",EDGE,"E6.3.1"),sQuery(id+"F0.wireOp",EDGE,"E6.3.2"),sQuery(id+"F0.wireOp",EDGE,"E6.3.3"),sQuery(id+"F0.wireOp",EDGE,"E6.3.4"),sQuery(id+"F0.wireOp",EDGE,"E6.4.1"),sQuery(id+"F0.wireOp",EDGE,"E6.4.2"),sQuery(id+"F0.wireOp",EDGE,"E6.4.3"),sQuery(id+"F0.wireOp",EDGE,"E6.4.4"),sQuery(id+"F0.wireOp",EDGE,"E6.5.1"),sQuery(id+"F0.wireOp",EDGE,"E6.5.2"),sQuery(id+"F0.wireOp",EDGE,"E6.5.3"),sQuery(id+"F0.wireOp",EDGE,"E6.5.4"),sQuery(id+"F0.wireOp",EDGE,"E6.6.1"),sQuery(id+"F0.wireOp",EDGE,"E6.6.2"),sQuery(id+"F0.wireOp",EDGE,"E6.6.3"),sQuery(id+"F0.wireOp",EDGE,"E6.6.4"),sQuery(id+"F0.wireOp",EDGE,"E6.7.1"),sQuery(id+"F0.wireOp",EDGE,"E6.7.2"),sQuery(id+"F0.wireOp",EDGE,"E6.7.3"),sQuery(id+"F0.wireOp",EDGE,"E6.7.4"),sQuery(id+"F0.wireOp",EDGE,"E6.8.1"),sQuery(id+"F0.wireOp",EDGE,"E6.8.2"),sQuery(id+"F0.wireOp",EDGE,"E6.8.3"),sQuery(id+"F0.wireOp",EDGE,"E6.8.4"),sQuery(id+"F0.wireOp",EDGE,"E6.9.1"),sQuery(id+"F0.wireOp",EDGE,"E6.9.2"),sQuery(id+"F0.wireOp",EDGE,"E6.9.3"),sQuery(id+"F0.wireOp",EDGE,"E6.9.4"),sQuery(id+"F0.wireOp",EDGE,"E6.10.1"),sQuery(id+"F0.wireOp",EDGE,"E6.10.2"),sQuery(id+"F0.wireOp",EDGE,"E6.10.3"),sQuery(id+"F0.wireOp",EDGE,"E6.10.4"),sQuery(id+"F0.wireOp",EDGE,"E6.11.1"),sQuery(id+"F0.wireOp",EDGE,"E6.11.2"),sQuery(id+"F0.wireOp",EDGE,"E6.11.3"),sQuery(id+"F0.wireOp",EDGE,"E6.11.4"),sQuery(id+"F0.wireOp",EDGE,"E6.12.1"),sQuery(id+"F0.wireOp",EDGE,"E6.12.2"),sQuery(id+"F0.wireOp",EDGE,"E6.12.3"),sQuery(id+"F0.wireOp",EDGE,"E6.12.4"),sQuery(id+"F0.wireOp",EDGE,"E6.13.1"),sQuery(id+"F0.wireOp",EDGE,"E6.13.2"),sQuery(id+"F0.wireOp",EDGE,"E6.13.3"),sQuery(id+"F0.wireOp",EDGE,"E6.13.4"),sQuery(id+"F0.wireOp",EDGE,"E6.14.1"),sQuery(id+"F0.wireOp",EDGE,"E6.14.2"),sQuery(id+"F0.wireOp",EDGE,"E6.14.3"),sQuery(id+"F0.wireOp",EDGE,"E6.14.4"),sQuery(id+"F0.wireOp",EDGE,"E6.15.1"),sQuery(id+"F0.wireOp",EDGE,"E6.15.2"),sQuery(id+"F0.wireOp",EDGE,"E6.15.3"),sQuery(id+"F0.wireOp",EDGE,"E6.15.4"),subQ1,sQuery(id+"F0.wireOp",EDGE,"E6.16.2"),subQ0,sQuery(id+"F0.wireOp",EDGE,"E6.16.4"),sQuery(id+"F0.wireOp",EDGE,"E6.17.1"),sQuery(id+"F0.wireOp",EDGE,"E6.17.2"),sQuery(id+"F0.wireOp",EDGE,"E6.17.3"),sQuery(id+"F0.wireOp",EDGE,"E6.17.4"),sQuery(id+"F0.wireOp",EDGE,"E6.18.1"),sQuery(id+"F0.wireOp",EDGE,"E6.18.2"),sQuery(id+"F0.wireOp",EDGE,"E6.18.3"),sQuery(id+"F0.wireOp",EDGE,"E6.18.4"),sQuery(id+"F0.wireOp",EDGE,"E6.19.1"),sQuery(id+"F0.wireOp",EDGE,"E6.19.2"),sQuery(id+"F0.wireOp",EDGE,"E6.19.3"),sQuery(id+"F0.wireOp",EDGE,"E6.19.4"),sQuery(id+"F0.wireOp",EDGE,"E6.20.1"),sQuery(id+"F0.wireOp",EDGE,"E6.20.2"),sQuery(id+"F0.wireOp",EDGE,"E6.20.3"),sQuery(id+"F0.wireOp",EDGE,"E6.20.4"),sQuery(id+"F0.wireOp",EDGE,"E6.21.1"),sQuery(id+"F0.wireOp",EDGE,"E6.21.2"),sQuery(id+"F0.wireOp",EDGE,"E6.21.3"),sQuery(id+"F0.wireOp",EDGE,"E6.21.4"),sQuery(id+"F0.wireOp",EDGE,"E6.22.1"),sQuery(id+"F0.wireOp",EDGE,"E6.22.2"),sQuery(id+"F0.wireOp",EDGE,"E6.22.3"),sQuery(id+"F0.wireOp",EDGE,"E6.22.4"),sQuery(id+"F0.wireOp",EDGE,"E6.23.1"),sQuery(id+"F0.wireOp",EDGE,"E6.23.2"),sQuery(id+"F0.wireOp",EDGE,"E6.23.3"),sQuery(id+"F0.wireOp",EDGE,"E6.23.4"),sQuery(id+"F0.wireOp",EDGE,"E6.24.1"),sQuery(id+"F0.wireOp",EDGE,"E6.24.2"),sQuery(id+"F0.wireOp",EDGE,"E6.24.3"),sQuery(id+"F0.wireOp",EDGE,"E6.24.4"),sQuery(id+"F0.wireOp",EDGE,"E6.25.1"),sQuery(id+"F0.wireOp",EDGE,"E6.25.2"),sQuery(id+"F0.wireOp",EDGE,"E6.25.3"),sQuery(id+"F0.wireOp",EDGE,"E6.25.4"),sQuery(id+"F0.wireOp",EDGE,"E6.26.1"),sQuery(id+"F0.wireOp",EDGE,"E6.26.2"),sQuery(id+"F0.wireOp",EDGE,"E6.26.3"),sQuery(id+"F0.wireOp",EDGE,"E6.26.4"),sQuery(id+"F0.wireOp",EDGE,"E6.27.1"),sQuery(id+"F0.wireOp",EDGE,"E6.27.2"),sQuery(id+"F0.wireOp",EDGE,"E6.27.3"),sQuery(id+"F0.wireOp",EDGE,"E6.27.4"),sQuery(id+"F0.wireOp",EDGE,"E6.28.1"),sQuery(id+"F0.wireOp",EDGE,"E6.28.2"),sQuery(id+"F0.wireOp",EDGE,"E6.28.3"),sQuery(id+"F0.wireOp",EDGE,"E6.28.4"),sQuery(id+"F0.wireOp",EDGE,"E6.29.1"),sQuery(id+"F0.wireOp",EDGE,"E6.29.2"),sQuery(id+"F0.wireOp",EDGE,"E6.29.3"),sQuery(id+"F0.wireOp",EDGE,"E6.29.4"),sQuery(id+"F0.wireOp",EDGE,"E6.30.1"),sQuery(id+"F0.wireOp",EDGE,"E6.30.2"),sQuery(id+"F0.wireOp",EDGE,"E6.30.3"),sQuery(id+"F0.wireOp",EDGE,"E6.30.4"),sQuery(id+"F0.wireOp",EDGE,"E6.31.1"),sQuery(id+"F0.wireOp",EDGE,"E6.31.2"),sQuery(id+"F0.wireOp",EDGE,"E6.31.3"),sQuery(id+"F0.wireOp",EDGE,"E6.31.4"),sQuery(id+"F0.wireOp",EDGE,"E6.32.1"),sQuery(id+"F0.wireOp",EDGE,"E6.32.2"),sQuery(id+"F0.wireOp",EDGE,"E6.32.3"),sQuery(id+"F0.wireOp",EDGE,"E6.32.4"),sQuery(id+"F0.wireOp",EDGE,"E6.33.1"),sQuery(id+"F0.wireOp",EDGE,"E6.33.2"),sQuery(id+"F0.wireOp",EDGE,"E6.33.3"),sQuery(id+"F0.wireOp",EDGE,"E6.33.4"),sQuery(id+"F0.wireOp",EDGE,"E6.34.1"),sQuery(id+"F0.wireOp",EDGE,"E6.34.2"),sQuery(id+"F0.wireOp",EDGE,"E6.34.3"),sQuery(id+"F0.wireOp",EDGE,"E6.34.4"),sQuery(id+"F0.wireOp",EDGE,"E6.35.1"),sQuery(id+"F0.wireOp",EDGE,"E6.35.2"),sQuery(id+"F0.wireOp",EDGE,"E6.35.3"),sQuery(id+"F0.wireOp",EDGE,"E6.35.4"),sQuery(id+"F0.wireOp",EDGE,"E6.36.1"),sQuery(id+"F0.wireOp",EDGE,"E6.36.2"),sQuery(id+"F0.wireOp",EDGE,"E6.36.3"),sQuery(id+"F0.wireOp",EDGE,"E6.36.4"),sQuery(id+"F0.wireOp",EDGE,"E6.37.1"),sQuery(id+"F0.wireOp",EDGE,"E6.37.2"),sQuery(id+"F0.wireOp",EDGE,"E6.37.3"),sQuery(id+"F0.wireOp",EDGE,"E6.37.4"),sQuery(id+"F0.wireOp",EDGE,"E6.38.1"),sQuery(id+"F0.wireOp",EDGE,"E6.38.2"),sQuery(id+"F0.wireOp",EDGE,"E6.38.3"),sQuery(id+"F0.wireOp",EDGE,"E6.38.4"),sQuery(id+"F0.wireOp",EDGE,"E6.39.1"),sQuery(id+"F0.wireOp",EDGE,"E6.39.2"),sQuery(id+"F0.wireOp",EDGE,"E6.39.3"),sQuery(id+"F0.wireOp",EDGE,"E6.39.4"),sQuery(id+"F0.wireOp",EDGE,"E6.40.1"),sQuery(id+"F0.wireOp",EDGE,"E6.40.2"),sQuery(id+"F0.wireOp",EDGE,"E6.40.3"),sQuery(id+"F0.wireOp",EDGE,"E6.40.4"),sQuery(id+"F0.wireOp",EDGE,"E6.41.1"),sQuery(id+"F0.wireOp",EDGE,"E6.41.2"),sQuery(id+"F0.wireOp",EDGE,"E6.41.3"),sQuery(id+"F0.wireOp",EDGE,"E6.41.4"),sQuery(id+"F0.wireOp",EDGE,"E6.42.1"),sQuery(id+"F0.wireOp",EDGE,"E6.42.2"),sQuery(id+"F0.wireOp",EDGE,"E6.42.3"),sQuery(id+"F0.wireOp",EDGE,"E6.42.4"),sQuery(id+"F0.wireOp",EDGE,"E6.43.1"),sQuery(id+"F0.wireOp",EDGE,"E6.43.2"),sQuery(id+"F0.wireOp",EDGE,"E6.43.3"),sQuery(id+"F0.wireOp",EDGE,"E6.43.4"),sQuery(id+"F0.wireOp",EDGE,"E7"),sQuery(id+"F0.wireOp",EDGE,"E8.1.0"),sQuery(id+"F0.wireOp",EDGE,"E8.2.0"),sQuery(id+"F0.wireOp",EDGE,"E8.3.0"),sQuery(id+"F0.wireOp",EDGE,"E8.4.0"),sQuery(id+"F0.wireOp",EDGE,"E8.5.0"),sQuery(id+"F0.wireOp",EDGE,"E8.6.0"),sQuery(id+"F0.wireOp",EDGE,"E8.7.0"),sQuery(id+"F0.wireOp",EDGE,"E8.8.0"),sQuery(id+"F0.wireOp",EDGE,"E8.9.0"),sQuery(id+"F0.wireOp",EDGE,"E8.10.0"),sQuery(id+"F0.wireOp",EDGE,"E8.11.0"),sQuery(id+"F0.wireOp",EDGE,"E8.12.0"),sQuery(id+"F0.wireOp",EDGE,"E8.13.0"),sQuery(id+"F0.wireOp",EDGE,"E8.14.0"),sQuery(id+"F0.wireOp",EDGE,"E8.15.0"),sQuery(id+"F0.wireOp",EDGE,"E8.16.0"),sQuery(id+"F0.wireOp",EDGE,"E8.17.0"),sQuery(id+"F0.wireOp",EDGE,"E8.18.0"),sQuery(id+"F0.wireOp",EDGE,"E8.19.0"),sQuery(id+"F0.wireOp",EDGE,"E8.20.0"),sQuery(id+"F0.wireOp",EDGE,"E8.21.0"),sQuery(id+"F0.wireOp",EDGE,"E8.22.0"),sQuery(id+"F0.wireOp",EDGE,"E8.23.0"),sQuery(id+"F0.wireOp",EDGE,"E8.24.0"),sQuery(id+"F0.wireOp",EDGE,"E8.25.0"),sQuery(id+"F0.wireOp",EDGE,"E8.26.0"),sQuery(id+"F0.wireOp",EDGE,"E8.27.0"),sQuery(id+"F0.wireOp",EDGE,"E8.28.0"),sQuery(id+"F0.wireOp",EDGE,"E8.29.0"),sQuery(id+"F0.wireOp",EDGE,"E8.30.0"),sQuery(id+"F0.wireOp",EDGE,"E8.31.0"),sQuery(id+"F0.wireOp",EDGE,"E8.32.0"),sQuery(id+"F0.wireOp",EDGE,"E8.33.0"),sQuery(id+"F0.wireOp",EDGE,"E8.34.0"),sQuery(id+"F0.wireOp",EDGE,"E8.35.0"),sQuery(id+"F0.wireOp",EDGE,"E8.36.0"),sQuery(id+"F0.wireOp",EDGE,"E8.37.0"),sQuery(id+"F0.wireOp",EDGE,"E8.38.0"),sQuery(id+"F0.wireOp",EDGE,"E8.39.0"),sQuery(id+"F0.wireOp",EDGE,"E8.40.0"),sQuery(id+"F0.wireOp",EDGE,"E8.41.0"),sQuery(id+"F0.wireOp",EDGE,"E8.42.0"),sQuery(id+"F0.wireOp",EDGE,"E8.43.0")])],"isStart":true})]});}
            var Q30;
            {var subQ0=sQuery(id+"F0.wireOp",EDGE,"E6.18.3");var subQ1=sQuery(id+"F0.wireOp",EDGE,"E6.18.1");Q30=makeQuery(id+"F2.opFillet","BLEND_EDGE",EDGE,{"blendedFrom":[makeQuery(id+"F1.opExtrude","SWEPT_EDGE",EDGE,{"disambiguationData":[OSD([sQuery(id+"F0.wireOp",EDGE,"E6.18.0"),subQ1,subQ0])]}),makeQuery(id+"F1.opExtrude","CAP_FACE",FACE,{"disambiguationData":[OSD([sQuery(id+"F0.wireOp",EDGE,"E0"),sQuery(id+"F0.wireOp",EDGE,"E1"),sQuery(id+"F0.wireOp",EDGE,"E2"),sQuery(id+"F0.wireOp",EDGE,"E4"),sQuery(id+"F0.wireOp",EDGE,"E5"),sQuery(id+"F0.wireOp",EDGE,"E6.1.1"),sQuery(id+"F0.wireOp",EDGE,"E6.1.2"),sQuery(id+"F0.wireOp",EDGE,"E6.1.3"),sQuery(id+"F0.wireOp",EDGE,"E6.1.4"),sQuery(id+"F0.wireOp",EDGE,"E6.2.1"),sQuery(id+"F0.wireOp",EDGE,"E6.2.2"),sQuery(id+"F0.wireOp",EDGE,"E6.2.3"),sQuery(id+"F0.wireOp",EDGE,"E6.2.4"),sQuery(id+"F0.wireOp",EDGE,"E6.3.1"),sQuery(id+"F0.wireOp",EDGE,"E6.3.2"),sQuery(id+"F0.wireOp",EDGE,"E6.3.3"),sQuery(id+"F0.wireOp",EDGE,"E6.3.4"),sQuery(id+"F0.wireOp",EDGE,"E6.4.1"),sQuery(id+"F0.wireOp",EDGE,"E6.4.2"),sQuery(id+"F0.wireOp",EDGE,"E6.4.3"),sQuery(id+"F0.wireOp",EDGE,"E6.4.4"),sQuery(id+"F0.wireOp",EDGE,"E6.5.1"),sQuery(id+"F0.wireOp",EDGE,"E6.5.2"),sQuery(id+"F0.wireOp",EDGE,"E6.5.3"),sQuery(id+"F0.wireOp",EDGE,"E6.5.4"),sQuery(id+"F0.wireOp",EDGE,"E6.6.1"),sQuery(id+"F0.wireOp",EDGE,"E6.6.2"),sQuery(id+"F0.wireOp",EDGE,"E6.6.3"),sQuery(id+"F0.wireOp",EDGE,"E6.6.4"),sQuery(id+"F0.wireOp",EDGE,"E6.7.1"),sQuery(id+"F0.wireOp",EDGE,"E6.7.2"),sQuery(id+"F0.wireOp",EDGE,"E6.7.3"),sQuery(id+"F0.wireOp",EDGE,"E6.7.4"),sQuery(id+"F0.wireOp",EDGE,"E6.8.1"),sQuery(id+"F0.wireOp",EDGE,"E6.8.2"),sQuery(id+"F0.wireOp",EDGE,"E6.8.3"),sQuery(id+"F0.wireOp",EDGE,"E6.8.4"),sQuery(id+"F0.wireOp",EDGE,"E6.9.1"),sQuery(id+"F0.wireOp",EDGE,"E6.9.2"),sQuery(id+"F0.wireOp",EDGE,"E6.9.3"),sQuery(id+"F0.wireOp",EDGE,"E6.9.4"),sQuery(id+"F0.wireOp",EDGE,"E6.10.1"),sQuery(id+"F0.wireOp",EDGE,"E6.10.2"),sQuery(id+"F0.wireOp",EDGE,"E6.10.3"),sQuery(id+"F0.wireOp",EDGE,"E6.10.4"),sQuery(id+"F0.wireOp",EDGE,"E6.11.1"),sQuery(id+"F0.wireOp",EDGE,"E6.11.2"),sQuery(id+"F0.wireOp",EDGE,"E6.11.3"),sQuery(id+"F0.wireOp",EDGE,"E6.11.4"),sQuery(id+"F0.wireOp",EDGE,"E6.12.1"),sQuery(id+"F0.wireOp",EDGE,"E6.12.2"),sQuery(id+"F0.wireOp",EDGE,"E6.12.3"),sQuery(id+"F0.wireOp",EDGE,"E6.12.4"),sQuery(id+"F0.wireOp",EDGE,"E6.13.1"),sQuery(id+"F0.wireOp",EDGE,"E6.13.2"),sQuery(id+"F0.wireOp",EDGE,"E6.13.3"),sQuery(id+"F0.wireOp",EDGE,"E6.13.4"),sQuery(id+"F0.wireOp",EDGE,"E6.14.1"),sQuery(id+"F0.wireOp",EDGE,"E6.14.2"),sQuery(id+"F0.wireOp",EDGE,"E6.14.3"),sQuery(id+"F0.wireOp",EDGE,"E6.14.4"),sQuery(id+"F0.wireOp",EDGE,"E6.15.1"),sQuery(id+"F0.wireOp",EDGE,"E6.15.2"),sQuery(id+"F0.wireOp",EDGE,"E6.15.3"),sQuery(id+"F0.wireOp",EDGE,"E6.15.4"),sQuery(id+"F0.wireOp",EDGE,"E6.16.1"),sQuery(id+"F0.wireOp",EDGE,"E6.16.2"),sQuery(id+"F0.wireOp",EDGE,"E6.16.3"),sQuery(id+"F0.wireOp",EDGE,"E6.16.4"),sQuery(id+"F0.wireOp",EDGE,"E6.17.1"),sQuery(id+"F0.wireOp",EDGE,"E6.17.2"),sQuery(id+"F0.wireOp",EDGE,"E6.17.3"),sQuery(id+"F0.wireOp",EDGE,"E6.17.4"),subQ1,sQuery(id+"F0.wireOp",EDGE,"E6.18.2"),subQ0,sQuery(id+"F0.wireOp",EDGE,"E6.18.4"),sQuery(id+"F0.wireOp",EDGE,"E6.19.1"),sQuery(id+"F0.wireOp",EDGE,"E6.19.2"),sQuery(id+"F0.wireOp",EDGE,"E6.19.3"),sQuery(id+"F0.wireOp",EDGE,"E6.19.4"),sQuery(id+"F0.wireOp",EDGE,"E6.20.1"),sQuery(id+"F0.wireOp",EDGE,"E6.20.2"),sQuery(id+"F0.wireOp",EDGE,"E6.20.3"),sQuery(id+"F0.wireOp",EDGE,"E6.20.4"),sQuery(id+"F0.wireOp",EDGE,"E6.21.1"),sQuery(id+"F0.wireOp",EDGE,"E6.21.2"),sQuery(id+"F0.wireOp",EDGE,"E6.21.3"),sQuery(id+"F0.wireOp",EDGE,"E6.21.4"),sQuery(id+"F0.wireOp",EDGE,"E6.22.1"),sQuery(id+"F0.wireOp",EDGE,"E6.22.2"),sQuery(id+"F0.wireOp",EDGE,"E6.22.3"),sQuery(id+"F0.wireOp",EDGE,"E6.22.4"),sQuery(id+"F0.wireOp",EDGE,"E6.23.1"),sQuery(id+"F0.wireOp",EDGE,"E6.23.2"),sQuery(id+"F0.wireOp",EDGE,"E6.23.3"),sQuery(id+"F0.wireOp",EDGE,"E6.23.4"),sQuery(id+"F0.wireOp",EDGE,"E6.24.1"),sQuery(id+"F0.wireOp",EDGE,"E6.24.2"),sQuery(id+"F0.wireOp",EDGE,"E6.24.3"),sQuery(id+"F0.wireOp",EDGE,"E6.24.4"),sQuery(id+"F0.wireOp",EDGE,"E6.25.1"),sQuery(id+"F0.wireOp",EDGE,"E6.25.2"),sQuery(id+"F0.wireOp",EDGE,"E6.25.3"),sQuery(id+"F0.wireOp",EDGE,"E6.25.4"),sQuery(id+"F0.wireOp",EDGE,"E6.26.1"),sQuery(id+"F0.wireOp",EDGE,"E6.26.2"),sQuery(id+"F0.wireOp",EDGE,"E6.26.3"),sQuery(id+"F0.wireOp",EDGE,"E6.26.4"),sQuery(id+"F0.wireOp",EDGE,"E6.27.1"),sQuery(id+"F0.wireOp",EDGE,"E6.27.2"),sQuery(id+"F0.wireOp",EDGE,"E6.27.3"),sQuery(id+"F0.wireOp",EDGE,"E6.27.4"),sQuery(id+"F0.wireOp",EDGE,"E6.28.1"),sQuery(id+"F0.wireOp",EDGE,"E6.28.2"),sQuery(id+"F0.wireOp",EDGE,"E6.28.3"),sQuery(id+"F0.wireOp",EDGE,"E6.28.4"),sQuery(id+"F0.wireOp",EDGE,"E6.29.1"),sQuery(id+"F0.wireOp",EDGE,"E6.29.2"),sQuery(id+"F0.wireOp",EDGE,"E6.29.3"),sQuery(id+"F0.wireOp",EDGE,"E6.29.4"),sQuery(id+"F0.wireOp",EDGE,"E6.30.1"),sQuery(id+"F0.wireOp",EDGE,"E6.30.2"),sQuery(id+"F0.wireOp",EDGE,"E6.30.3"),sQuery(id+"F0.wireOp",EDGE,"E6.30.4"),sQuery(id+"F0.wireOp",EDGE,"E6.31.1"),sQuery(id+"F0.wireOp",EDGE,"E6.31.2"),sQuery(id+"F0.wireOp",EDGE,"E6.31.3"),sQuery(id+"F0.wireOp",EDGE,"E6.31.4"),sQuery(id+"F0.wireOp",EDGE,"E6.32.1"),sQuery(id+"F0.wireOp",EDGE,"E6.32.2"),sQuery(id+"F0.wireOp",EDGE,"E6.32.3"),sQuery(id+"F0.wireOp",EDGE,"E6.32.4"),sQuery(id+"F0.wireOp",EDGE,"E6.33.1"),sQuery(id+"F0.wireOp",EDGE,"E6.33.2"),sQuery(id+"F0.wireOp",EDGE,"E6.33.3"),sQuery(id+"F0.wireOp",EDGE,"E6.33.4"),sQuery(id+"F0.wireOp",EDGE,"E6.34.1"),sQuery(id+"F0.wireOp",EDGE,"E6.34.2"),sQuery(id+"F0.wireOp",EDGE,"E6.34.3"),sQuery(id+"F0.wireOp",EDGE,"E6.34.4"),sQuery(id+"F0.wireOp",EDGE,"E6.35.1"),sQuery(id+"F0.wireOp",EDGE,"E6.35.2"),sQuery(id+"F0.wireOp",EDGE,"E6.35.3"),sQuery(id+"F0.wireOp",EDGE,"E6.35.4"),sQuery(id+"F0.wireOp",EDGE,"E6.36.1"),sQuery(id+"F0.wireOp",EDGE,"E6.36.2"),sQuery(id+"F0.wireOp",EDGE,"E6.36.3"),sQuery(id+"F0.wireOp",EDGE,"E6.36.4"),sQuery(id+"F0.wireOp",EDGE,"E6.37.1"),sQuery(id+"F0.wireOp",EDGE,"E6.37.2"),sQuery(id+"F0.wireOp",EDGE,"E6.37.3"),sQuery(id+"F0.wireOp",EDGE,"E6.37.4"),sQuery(id+"F0.wireOp",EDGE,"E6.38.1"),sQuery(id+"F0.wireOp",EDGE,"E6.38.2"),sQuery(id+"F0.wireOp",EDGE,"E6.38.3"),sQuery(id+"F0.wireOp",EDGE,"E6.38.4"),sQuery(id+"F0.wireOp",EDGE,"E6.39.1"),sQuery(id+"F0.wireOp",EDGE,"E6.39.2"),sQuery(id+"F0.wireOp",EDGE,"E6.39.3"),sQuery(id+"F0.wireOp",EDGE,"E6.39.4"),sQuery(id+"F0.wireOp",EDGE,"E6.40.1"),sQuery(id+"F0.wireOp",EDGE,"E6.40.2"),sQuery(id+"F0.wireOp",EDGE,"E6.40.3"),sQuery(id+"F0.wireOp",EDGE,"E6.40.4"),sQuery(id+"F0.wireOp",EDGE,"E6.41.1"),sQuery(id+"F0.wireOp",EDGE,"E6.41.2"),sQuery(id+"F0.wireOp",EDGE,"E6.41.3"),sQuery(id+"F0.wireOp",EDGE,"E6.41.4"),sQuery(id+"F0.wireOp",EDGE,"E6.42.1"),sQuery(id+"F0.wireOp",EDGE,"E6.42.2"),sQuery(id+"F0.wireOp",EDGE,"E6.42.3"),sQuery(id+"F0.wireOp",EDGE,"E6.42.4"),sQuery(id+"F0.wireOp",EDGE,"E6.43.1"),sQuery(id+"F0.wireOp",EDGE,"E6.43.2"),sQuery(id+"F0.wireOp",EDGE,"E6.43.3"),sQuery(id+"F0.wireOp",EDGE,"E6.43.4"),sQuery(id+"F0.wireOp",EDGE,"E7"),sQuery(id+"F0.wireOp",EDGE,"E8.1.0"),sQuery(id+"F0.wireOp",EDGE,"E8.2.0"),sQuery(id+"F0.wireOp",EDGE,"E8.3.0"),sQuery(id+"F0.wireOp",EDGE,"E8.4.0"),sQuery(id+"F0.wireOp",EDGE,"E8.5.0"),sQuery(id+"F0.wireOp",EDGE,"E8.6.0"),sQuery(id+"F0.wireOp",EDGE,"E8.7.0"),sQuery(id+"F0.wireOp",EDGE,"E8.8.0"),sQuery(id+"F0.wireOp",EDGE,"E8.9.0"),sQuery(id+"F0.wireOp",EDGE,"E8.10.0"),sQuery(id+"F0.wireOp",EDGE,"E8.11.0"),sQuery(id+"F0.wireOp",EDGE,"E8.12.0"),sQuery(id+"F0.wireOp",EDGE,"E8.13.0"),sQuery(id+"F0.wireOp",EDGE,"E8.14.0"),sQuery(id+"F0.wireOp",EDGE,"E8.15.0"),sQuery(id+"F0.wireOp",EDGE,"E8.16.0"),sQuery(id+"F0.wireOp",EDGE,"E8.17.0"),sQuery(id+"F0.wireOp",EDGE,"E8.18.0"),sQuery(id+"F0.wireOp",EDGE,"E8.19.0"),sQuery(id+"F0.wireOp",EDGE,"E8.20.0"),sQuery(id+"F0.wireOp",EDGE,"E8.21.0"),sQuery(id+"F0.wireOp",EDGE,"E8.22.0"),sQuery(id+"F0.wireOp",EDGE,"E8.23.0"),sQuery(id+"F0.wireOp",EDGE,"E8.24.0"),sQuery(id+"F0.wireOp",EDGE,"E8.25.0"),sQuery(id+"F0.wireOp",EDGE,"E8.26.0"),sQuery(id+"F0.wireOp",EDGE,"E8.27.0"),sQuery(id+"F0.wireOp",EDGE,"E8.28.0"),sQuery(id+"F0.wireOp",EDGE,"E8.29.0"),sQuery(id+"F0.wireOp",EDGE,"E8.30.0"),sQuery(id+"F0.wireOp",EDGE,"E8.31.0"),sQuery(id+"F0.wireOp",EDGE,"E8.32.0"),sQuery(id+"F0.wireOp",EDGE,"E8.33.0"),sQuery(id+"F0.wireOp",EDGE,"E8.34.0"),sQuery(id+"F0.wireOp",EDGE,"E8.35.0"),sQuery(id+"F0.wireOp",EDGE,"E8.36.0"),sQuery(id+"F0.wireOp",EDGE,"E8.37.0"),sQuery(id+"F0.wireOp",EDGE,"E8.38.0"),sQuery(id+"F0.wireOp",EDGE,"E8.39.0"),sQuery(id+"F0.wireOp",EDGE,"E8.40.0"),sQuery(id+"F0.wireOp",EDGE,"E8.41.0"),sQuery(id+"F0.wireOp",EDGE,"E8.42.0"),sQuery(id+"F0.wireOp",EDGE,"E8.43.0")])],"isStart":true})],"blendedInto":[makeQuery(id+"F1.opExtrude","CAP_FACE",FACE,{"disambiguationData":[OSD([sQuery(id+"F0.wireOp",EDGE,"E0"),sQuery(id+"F0.wireOp",EDGE,"E1"),sQuery(id+"F0.wireOp",EDGE,"E2"),sQuery(id+"F0.wireOp",EDGE,"E4"),sQuery(id+"F0.wireOp",EDGE,"E5"),sQuery(id+"F0.wireOp",EDGE,"E6.1.1"),sQuery(id+"F0.wireOp",EDGE,"E6.1.2"),sQuery(id+"F0.wireOp",EDGE,"E6.1.3"),sQuery(id+"F0.wireOp",EDGE,"E6.1.4"),sQuery(id+"F0.wireOp",EDGE,"E6.2.1"),sQuery(id+"F0.wireOp",EDGE,"E6.2.2"),sQuery(id+"F0.wireOp",EDGE,"E6.2.3"),sQuery(id+"F0.wireOp",EDGE,"E6.2.4"),sQuery(id+"F0.wireOp",EDGE,"E6.3.1"),sQuery(id+"F0.wireOp",EDGE,"E6.3.2"),sQuery(id+"F0.wireOp",EDGE,"E6.3.3"),sQuery(id+"F0.wireOp",EDGE,"E6.3.4"),sQuery(id+"F0.wireOp",EDGE,"E6.4.1"),sQuery(id+"F0.wireOp",EDGE,"E6.4.2"),sQuery(id+"F0.wireOp",EDGE,"E6.4.3"),sQuery(id+"F0.wireOp",EDGE,"E6.4.4"),sQuery(id+"F0.wireOp",EDGE,"E6.5.1"),sQuery(id+"F0.wireOp",EDGE,"E6.5.2"),sQuery(id+"F0.wireOp",EDGE,"E6.5.3"),sQuery(id+"F0.wireOp",EDGE,"E6.5.4"),sQuery(id+"F0.wireOp",EDGE,"E6.6.1"),sQuery(id+"F0.wireOp",EDGE,"E6.6.2"),sQuery(id+"F0.wireOp",EDGE,"E6.6.3"),sQuery(id+"F0.wireOp",EDGE,"E6.6.4"),sQuery(id+"F0.wireOp",EDGE,"E6.7.1"),sQuery(id+"F0.wireOp",EDGE,"E6.7.2"),sQuery(id+"F0.wireOp",EDGE,"E6.7.3"),sQuery(id+"F0.wireOp",EDGE,"E6.7.4"),sQuery(id+"F0.wireOp",EDGE,"E6.8.1"),sQuery(id+"F0.wireOp",EDGE,"E6.8.2"),sQuery(id+"F0.wireOp",EDGE,"E6.8.3"),sQuery(id+"F0.wireOp",EDGE,"E6.8.4"),sQuery(id+"F0.wireOp",EDGE,"E6.9.1"),sQuery(id+"F0.wireOp",EDGE,"E6.9.2"),sQuery(id+"F0.wireOp",EDGE,"E6.9.3"),sQuery(id+"F0.wireOp",EDGE,"E6.9.4"),sQuery(id+"F0.wireOp",EDGE,"E6.10.1"),sQuery(id+"F0.wireOp",EDGE,"E6.10.2"),sQuery(id+"F0.wireOp",EDGE,"E6.10.3"),sQuery(id+"F0.wireOp",EDGE,"E6.10.4"),sQuery(id+"F0.wireOp",EDGE,"E6.11.1"),sQuery(id+"F0.wireOp",EDGE,"E6.11.2"),sQuery(id+"F0.wireOp",EDGE,"E6.11.3"),sQuery(id+"F0.wireOp",EDGE,"E6.11.4"),sQuery(id+"F0.wireOp",EDGE,"E6.12.1"),sQuery(id+"F0.wireOp",EDGE,"E6.12.2"),sQuery(id+"F0.wireOp",EDGE,"E6.12.3"),sQuery(id+"F0.wireOp",EDGE,"E6.12.4"),sQuery(id+"F0.wireOp",EDGE,"E6.13.1"),sQuery(id+"F0.wireOp",EDGE,"E6.13.2"),sQuery(id+"F0.wireOp",EDGE,"E6.13.3"),sQuery(id+"F0.wireOp",EDGE,"E6.13.4"),sQuery(id+"F0.wireOp",EDGE,"E6.14.1"),sQuery(id+"F0.wireOp",EDGE,"E6.14.2"),sQuery(id+"F0.wireOp",EDGE,"E6.14.3"),sQuery(id+"F0.wireOp",EDGE,"E6.14.4"),sQuery(id+"F0.wireOp",EDGE,"E6.15.1"),sQuery(id+"F0.wireOp",EDGE,"E6.15.2"),sQuery(id+"F0.wireOp",EDGE,"E6.15.3"),sQuery(id+"F0.wireOp",EDGE,"E6.15.4"),sQuery(id+"F0.wireOp",EDGE,"E6.16.1"),sQuery(id+"F0.wireOp",EDGE,"E6.16.2"),sQuery(id+"F0.wireOp",EDGE,"E6.16.3"),sQuery(id+"F0.wireOp",EDGE,"E6.16.4"),sQuery(id+"F0.wireOp",EDGE,"E6.17.1"),sQuery(id+"F0.wireOp",EDGE,"E6.17.2"),sQuery(id+"F0.wireOp",EDGE,"E6.17.3"),sQuery(id+"F0.wireOp",EDGE,"E6.17.4"),subQ1,sQuery(id+"F0.wireOp",EDGE,"E6.18.2"),subQ0,sQuery(id+"F0.wireOp",EDGE,"E6.18.4"),sQuery(id+"F0.wireOp",EDGE,"E6.19.1"),sQuery(id+"F0.wireOp",EDGE,"E6.19.2"),sQuery(id+"F0.wireOp",EDGE,"E6.19.3"),sQuery(id+"F0.wireOp",EDGE,"E6.19.4"),sQuery(id+"F0.wireOp",EDGE,"E6.20.1"),sQuery(id+"F0.wireOp",EDGE,"E6.20.2"),sQuery(id+"F0.wireOp",EDGE,"E6.20.3"),sQuery(id+"F0.wireOp",EDGE,"E6.20.4"),sQuery(id+"F0.wireOp",EDGE,"E6.21.1"),sQuery(id+"F0.wireOp",EDGE,"E6.21.2"),sQuery(id+"F0.wireOp",EDGE,"E6.21.3"),sQuery(id+"F0.wireOp",EDGE,"E6.21.4"),sQuery(id+"F0.wireOp",EDGE,"E6.22.1"),sQuery(id+"F0.wireOp",EDGE,"E6.22.2"),sQuery(id+"F0.wireOp",EDGE,"E6.22.3"),sQuery(id+"F0.wireOp",EDGE,"E6.22.4"),sQuery(id+"F0.wireOp",EDGE,"E6.23.1"),sQuery(id+"F0.wireOp",EDGE,"E6.23.2"),sQuery(id+"F0.wireOp",EDGE,"E6.23.3"),sQuery(id+"F0.wireOp",EDGE,"E6.23.4"),sQuery(id+"F0.wireOp",EDGE,"E6.24.1"),sQuery(id+"F0.wireOp",EDGE,"E6.24.2"),sQuery(id+"F0.wireOp",EDGE,"E6.24.3"),sQuery(id+"F0.wireOp",EDGE,"E6.24.4"),sQuery(id+"F0.wireOp",EDGE,"E6.25.1"),sQuery(id+"F0.wireOp",EDGE,"E6.25.2"),sQuery(id+"F0.wireOp",EDGE,"E6.25.3"),sQuery(id+"F0.wireOp",EDGE,"E6.25.4"),sQuery(id+"F0.wireOp",EDGE,"E6.26.1"),sQuery(id+"F0.wireOp",EDGE,"E6.26.2"),sQuery(id+"F0.wireOp",EDGE,"E6.26.3"),sQuery(id+"F0.wireOp",EDGE,"E6.26.4"),sQuery(id+"F0.wireOp",EDGE,"E6.27.1"),sQuery(id+"F0.wireOp",EDGE,"E6.27.2"),sQuery(id+"F0.wireOp",EDGE,"E6.27.3"),sQuery(id+"F0.wireOp",EDGE,"E6.27.4"),sQuery(id+"F0.wireOp",EDGE,"E6.28.1"),sQuery(id+"F0.wireOp",EDGE,"E6.28.2"),sQuery(id+"F0.wireOp",EDGE,"E6.28.3"),sQuery(id+"F0.wireOp",EDGE,"E6.28.4"),sQuery(id+"F0.wireOp",EDGE,"E6.29.1"),sQuery(id+"F0.wireOp",EDGE,"E6.29.2"),sQuery(id+"F0.wireOp",EDGE,"E6.29.3"),sQuery(id+"F0.wireOp",EDGE,"E6.29.4"),sQuery(id+"F0.wireOp",EDGE,"E6.30.1"),sQuery(id+"F0.wireOp",EDGE,"E6.30.2"),sQuery(id+"F0.wireOp",EDGE,"E6.30.3"),sQuery(id+"F0.wireOp",EDGE,"E6.30.4"),sQuery(id+"F0.wireOp",EDGE,"E6.31.1"),sQuery(id+"F0.wireOp",EDGE,"E6.31.2"),sQuery(id+"F0.wireOp",EDGE,"E6.31.3"),sQuery(id+"F0.wireOp",EDGE,"E6.31.4"),sQuery(id+"F0.wireOp",EDGE,"E6.32.1"),sQuery(id+"F0.wireOp",EDGE,"E6.32.2"),sQuery(id+"F0.wireOp",EDGE,"E6.32.3"),sQuery(id+"F0.wireOp",EDGE,"E6.32.4"),sQuery(id+"F0.wireOp",EDGE,"E6.33.1"),sQuery(id+"F0.wireOp",EDGE,"E6.33.2"),sQuery(id+"F0.wireOp",EDGE,"E6.33.3"),sQuery(id+"F0.wireOp",EDGE,"E6.33.4"),sQuery(id+"F0.wireOp",EDGE,"E6.34.1"),sQuery(id+"F0.wireOp",EDGE,"E6.34.2"),sQuery(id+"F0.wireOp",EDGE,"E6.34.3"),sQuery(id+"F0.wireOp",EDGE,"E6.34.4"),sQuery(id+"F0.wireOp",EDGE,"E6.35.1"),sQuery(id+"F0.wireOp",EDGE,"E6.35.2"),sQuery(id+"F0.wireOp",EDGE,"E6.35.3"),sQuery(id+"F0.wireOp",EDGE,"E6.35.4"),sQuery(id+"F0.wireOp",EDGE,"E6.36.1"),sQuery(id+"F0.wireOp",EDGE,"E6.36.2"),sQuery(id+"F0.wireOp",EDGE,"E6.36.3"),sQuery(id+"F0.wireOp",EDGE,"E6.36.4"),sQuery(id+"F0.wireOp",EDGE,"E6.37.1"),sQuery(id+"F0.wireOp",EDGE,"E6.37.2"),sQuery(id+"F0.wireOp",EDGE,"E6.37.3"),sQuery(id+"F0.wireOp",EDGE,"E6.37.4"),sQuery(id+"F0.wireOp",EDGE,"E6.38.1"),sQuery(id+"F0.wireOp",EDGE,"E6.38.2"),sQuery(id+"F0.wireOp",EDGE,"E6.38.3"),sQuery(id+"F0.wireOp",EDGE,"E6.38.4"),sQuery(id+"F0.wireOp",EDGE,"E6.39.1"),sQuery(id+"F0.wireOp",EDGE,"E6.39.2"),sQuery(id+"F0.wireOp",EDGE,"E6.39.3"),sQuery(id+"F0.wireOp",EDGE,"E6.39.4"),sQuery(id+"F0.wireOp",EDGE,"E6.40.1"),sQuery(id+"F0.wireOp",EDGE,"E6.40.2"),sQuery(id+"F0.wireOp",EDGE,"E6.40.3"),sQuery(id+"F0.wireOp",EDGE,"E6.40.4"),sQuery(id+"F0.wireOp",EDGE,"E6.41.1"),sQuery(id+"F0.wireOp",EDGE,"E6.41.2"),sQuery(id+"F0.wireOp",EDGE,"E6.41.3"),sQuery(id+"F0.wireOp",EDGE,"E6.41.4"),sQuery(id+"F0.wireOp",EDGE,"E6.42.1"),sQuery(id+"F0.wireOp",EDGE,"E6.42.2"),sQuery(id+"F0.wireOp",EDGE,"E6.42.3"),sQuery(id+"F0.wireOp",EDGE,"E6.42.4"),sQuery(id+"F0.wireOp",EDGE,"E6.43.1"),sQuery(id+"F0.wireOp",EDGE,"E6.43.2"),sQuery(id+"F0.wireOp",EDGE,"E6.43.3"),sQuery(id+"F0.wireOp",EDGE,"E6.43.4"),sQuery(id+"F0.wireOp",EDGE,"E7"),sQuery(id+"F0.wireOp",EDGE,"E8.1.0"),sQuery(id+"F0.wireOp",EDGE,"E8.2.0"),sQuery(id+"F0.wireOp",EDGE,"E8.3.0"),sQuery(id+"F0.wireOp",EDGE,"E8.4.0"),sQuery(id+"F0.wireOp",EDGE,"E8.5.0"),sQuery(id+"F0.wireOp",EDGE,"E8.6.0"),sQuery(id+"F0.wireOp",EDGE,"E8.7.0"),sQuery(id+"F0.wireOp",EDGE,"E8.8.0"),sQuery(id+"F0.wireOp",EDGE,"E8.9.0"),sQuery(id+"F0.wireOp",EDGE,"E8.10.0"),sQuery(id+"F0.wireOp",EDGE,"E8.11.0"),sQuery(id+"F0.wireOp",EDGE,"E8.12.0"),sQuery(id+"F0.wireOp",EDGE,"E8.13.0"),sQuery(id+"F0.wireOp",EDGE,"E8.14.0"),sQuery(id+"F0.wireOp",EDGE,"E8.15.0"),sQuery(id+"F0.wireOp",EDGE,"E8.16.0"),sQuery(id+"F0.wireOp",EDGE,"E8.17.0"),sQuery(id+"F0.wireOp",EDGE,"E8.18.0"),sQuery(id+"F0.wireOp",EDGE,"E8.19.0"),sQuery(id+"F0.wireOp",EDGE,"E8.20.0"),sQuery(id+"F0.wireOp",EDGE,"E8.21.0"),sQuery(id+"F0.wireOp",EDGE,"E8.22.0"),sQuery(id+"F0.wireOp",EDGE,"E8.23.0"),sQuery(id+"F0.wireOp",EDGE,"E8.24.0"),sQuery(id+"F0.wireOp",EDGE,"E8.25.0"),sQuery(id+"F0.wireOp",EDGE,"E8.26.0"),sQuery(id+"F0.wireOp",EDGE,"E8.27.0"),sQuery(id+"F0.wireOp",EDGE,"E8.28.0"),sQuery(id+"F0.wireOp",EDGE,"E8.29.0"),sQuery(id+"F0.wireOp",EDGE,"E8.30.0"),sQuery(id+"F0.wireOp",EDGE,"E8.31.0"),sQuery(id+"F0.wireOp",EDGE,"E8.32.0"),sQuery(id+"F0.wireOp",EDGE,"E8.33.0"),sQuery(id+"F0.wireOp",EDGE,"E8.34.0"),sQuery(id+"F0.wireOp",EDGE,"E8.35.0"),sQuery(id+"F0.wireOp",EDGE,"E8.36.0"),sQuery(id+"F0.wireOp",EDGE,"E8.37.0"),sQuery(id+"F0.wireOp",EDGE,"E8.38.0"),sQuery(id+"F0.wireOp",EDGE,"E8.39.0"),sQuery(id+"F0.wireOp",EDGE,"E8.40.0"),sQuery(id+"F0.wireOp",EDGE,"E8.41.0"),sQuery(id+"F0.wireOp",EDGE,"E8.42.0"),sQuery(id+"F0.wireOp",EDGE,"E8.43.0")])],"isStart":true})]});}
            var Q31;
            {var subQ0=sQuery(id+"F0.wireOp",EDGE,"E6.20.3");var subQ1=sQuery(id+"F0.wireOp",EDGE,"E6.20.1");Q31=makeQuery(id+"F2.opFillet","BLEND_EDGE",EDGE,{"blendedFrom":[makeQuery(id+"F1.opExtrude","SWEPT_EDGE",EDGE,{"disambiguationData":[OSD([sQuery(id+"F0.wireOp",EDGE,"E6.20.0"),subQ1,subQ0])]}),makeQuery(id+"F1.opExtrude","CAP_FACE",FACE,{"disambiguationData":[OSD([sQuery(id+"F0.wireOp",EDGE,"E0"),sQuery(id+"F0.wireOp",EDGE,"E1"),sQuery(id+"F0.wireOp",EDGE,"E2"),sQuery(id+"F0.wireOp",EDGE,"E4"),sQuery(id+"F0.wireOp",EDGE,"E5"),sQuery(id+"F0.wireOp",EDGE,"E6.1.1"),sQuery(id+"F0.wireOp",EDGE,"E6.1.2"),sQuery(id+"F0.wireOp",EDGE,"E6.1.3"),sQuery(id+"F0.wireOp",EDGE,"E6.1.4"),sQuery(id+"F0.wireOp",EDGE,"E6.2.1"),sQuery(id+"F0.wireOp",EDGE,"E6.2.2"),sQuery(id+"F0.wireOp",EDGE,"E6.2.3"),sQuery(id+"F0.wireOp",EDGE,"E6.2.4"),sQuery(id+"F0.wireOp",EDGE,"E6.3.1"),sQuery(id+"F0.wireOp",EDGE,"E6.3.2"),sQuery(id+"F0.wireOp",EDGE,"E6.3.3"),sQuery(id+"F0.wireOp",EDGE,"E6.3.4"),sQuery(id+"F0.wireOp",EDGE,"E6.4.1"),sQuery(id+"F0.wireOp",EDGE,"E6.4.2"),sQuery(id+"F0.wireOp",EDGE,"E6.4.3"),sQuery(id+"F0.wireOp",EDGE,"E6.4.4"),sQuery(id+"F0.wireOp",EDGE,"E6.5.1"),sQuery(id+"F0.wireOp",EDGE,"E6.5.2"),sQuery(id+"F0.wireOp",EDGE,"E6.5.3"),sQuery(id+"F0.wireOp",EDGE,"E6.5.4"),sQuery(id+"F0.wireOp",EDGE,"E6.6.1"),sQuery(id+"F0.wireOp",EDGE,"E6.6.2"),sQuery(id+"F0.wireOp",EDGE,"E6.6.3"),sQuery(id+"F0.wireOp",EDGE,"E6.6.4"),sQuery(id+"F0.wireOp",EDGE,"E6.7.1"),sQuery(id+"F0.wireOp",EDGE,"E6.7.2"),sQuery(id+"F0.wireOp",EDGE,"E6.7.3"),sQuery(id+"F0.wireOp",EDGE,"E6.7.4"),sQuery(id+"F0.wireOp",EDGE,"E6.8.1"),sQuery(id+"F0.wireOp",EDGE,"E6.8.2"),sQuery(id+"F0.wireOp",EDGE,"E6.8.3"),sQuery(id+"F0.wireOp",EDGE,"E6.8.4"),sQuery(id+"F0.wireOp",EDGE,"E6.9.1"),sQuery(id+"F0.wireOp",EDGE,"E6.9.2"),sQuery(id+"F0.wireOp",EDGE,"E6.9.3"),sQuery(id+"F0.wireOp",EDGE,"E6.9.4"),sQuery(id+"F0.wireOp",EDGE,"E6.10.1"),sQuery(id+"F0.wireOp",EDGE,"E6.10.2"),sQuery(id+"F0.wireOp",EDGE,"E6.10.3"),sQuery(id+"F0.wireOp",EDGE,"E6.10.4"),sQuery(id+"F0.wireOp",EDGE,"E6.11.1"),sQuery(id+"F0.wireOp",EDGE,"E6.11.2"),sQuery(id+"F0.wireOp",EDGE,"E6.11.3"),sQuery(id+"F0.wireOp",EDGE,"E6.11.4"),sQuery(id+"F0.wireOp",EDGE,"E6.12.1"),sQuery(id+"F0.wireOp",EDGE,"E6.12.2"),sQuery(id+"F0.wireOp",EDGE,"E6.12.3"),sQuery(id+"F0.wireOp",EDGE,"E6.12.4"),sQuery(id+"F0.wireOp",EDGE,"E6.13.1"),sQuery(id+"F0.wireOp",EDGE,"E6.13.2"),sQuery(id+"F0.wireOp",EDGE,"E6.13.3"),sQuery(id+"F0.wireOp",EDGE,"E6.13.4"),sQuery(id+"F0.wireOp",EDGE,"E6.14.1"),sQuery(id+"F0.wireOp",EDGE,"E6.14.2"),sQuery(id+"F0.wireOp",EDGE,"E6.14.3"),sQuery(id+"F0.wireOp",EDGE,"E6.14.4"),sQuery(id+"F0.wireOp",EDGE,"E6.15.1"),sQuery(id+"F0.wireOp",EDGE,"E6.15.2"),sQuery(id+"F0.wireOp",EDGE,"E6.15.3"),sQuery(id+"F0.wireOp",EDGE,"E6.15.4"),sQuery(id+"F0.wireOp",EDGE,"E6.16.1"),sQuery(id+"F0.wireOp",EDGE,"E6.16.2"),sQuery(id+"F0.wireOp",EDGE,"E6.16.3"),sQuery(id+"F0.wireOp",EDGE,"E6.16.4"),sQuery(id+"F0.wireOp",EDGE,"E6.17.1"),sQuery(id+"F0.wireOp",EDGE,"E6.17.2"),sQuery(id+"F0.wireOp",EDGE,"E6.17.3"),sQuery(id+"F0.wireOp",EDGE,"E6.17.4"),sQuery(id+"F0.wireOp",EDGE,"E6.18.1"),sQuery(id+"F0.wireOp",EDGE,"E6.18.2"),sQuery(id+"F0.wireOp",EDGE,"E6.18.3"),sQuery(id+"F0.wireOp",EDGE,"E6.18.4"),sQuery(id+"F0.wireOp",EDGE,"E6.19.1"),sQuery(id+"F0.wireOp",EDGE,"E6.19.2"),sQuery(id+"F0.wireOp",EDGE,"E6.19.3"),sQuery(id+"F0.wireOp",EDGE,"E6.19.4"),subQ1,sQuery(id+"F0.wireOp",EDGE,"E6.20.2"),subQ0,sQuery(id+"F0.wireOp",EDGE,"E6.20.4"),sQuery(id+"F0.wireOp",EDGE,"E6.21.1"),sQuery(id+"F0.wireOp",EDGE,"E6.21.2"),sQuery(id+"F0.wireOp",EDGE,"E6.21.3"),sQuery(id+"F0.wireOp",EDGE,"E6.21.4"),sQuery(id+"F0.wireOp",EDGE,"E6.22.1"),sQuery(id+"F0.wireOp",EDGE,"E6.22.2"),sQuery(id+"F0.wireOp",EDGE,"E6.22.3"),sQuery(id+"F0.wireOp",EDGE,"E6.22.4"),sQuery(id+"F0.wireOp",EDGE,"E6.23.1"),sQuery(id+"F0.wireOp",EDGE,"E6.23.2"),sQuery(id+"F0.wireOp",EDGE,"E6.23.3"),sQuery(id+"F0.wireOp",EDGE,"E6.23.4"),sQuery(id+"F0.wireOp",EDGE,"E6.24.1"),sQuery(id+"F0.wireOp",EDGE,"E6.24.2"),sQuery(id+"F0.wireOp",EDGE,"E6.24.3"),sQuery(id+"F0.wireOp",EDGE,"E6.24.4"),sQuery(id+"F0.wireOp",EDGE,"E6.25.1"),sQuery(id+"F0.wireOp",EDGE,"E6.25.2"),sQuery(id+"F0.wireOp",EDGE,"E6.25.3"),sQuery(id+"F0.wireOp",EDGE,"E6.25.4"),sQuery(id+"F0.wireOp",EDGE,"E6.26.1"),sQuery(id+"F0.wireOp",EDGE,"E6.26.2"),sQuery(id+"F0.wireOp",EDGE,"E6.26.3"),sQuery(id+"F0.wireOp",EDGE,"E6.26.4"),sQuery(id+"F0.wireOp",EDGE,"E6.27.1"),sQuery(id+"F0.wireOp",EDGE,"E6.27.2"),sQuery(id+"F0.wireOp",EDGE,"E6.27.3"),sQuery(id+"F0.wireOp",EDGE,"E6.27.4"),sQuery(id+"F0.wireOp",EDGE,"E6.28.1"),sQuery(id+"F0.wireOp",EDGE,"E6.28.2"),sQuery(id+"F0.wireOp",EDGE,"E6.28.3"),sQuery(id+"F0.wireOp",EDGE,"E6.28.4"),sQuery(id+"F0.wireOp",EDGE,"E6.29.1"),sQuery(id+"F0.wireOp",EDGE,"E6.29.2"),sQuery(id+"F0.wireOp",EDGE,"E6.29.3"),sQuery(id+"F0.wireOp",EDGE,"E6.29.4"),sQuery(id+"F0.wireOp",EDGE,"E6.30.1"),sQuery(id+"F0.wireOp",EDGE,"E6.30.2"),sQuery(id+"F0.wireOp",EDGE,"E6.30.3"),sQuery(id+"F0.wireOp",EDGE,"E6.30.4"),sQuery(id+"F0.wireOp",EDGE,"E6.31.1"),sQuery(id+"F0.wireOp",EDGE,"E6.31.2"),sQuery(id+"F0.wireOp",EDGE,"E6.31.3"),sQuery(id+"F0.wireOp",EDGE,"E6.31.4"),sQuery(id+"F0.wireOp",EDGE,"E6.32.1"),sQuery(id+"F0.wireOp",EDGE,"E6.32.2"),sQuery(id+"F0.wireOp",EDGE,"E6.32.3"),sQuery(id+"F0.wireOp",EDGE,"E6.32.4"),sQuery(id+"F0.wireOp",EDGE,"E6.33.1"),sQuery(id+"F0.wireOp",EDGE,"E6.33.2"),sQuery(id+"F0.wireOp",EDGE,"E6.33.3"),sQuery(id+"F0.wireOp",EDGE,"E6.33.4"),sQuery(id+"F0.wireOp",EDGE,"E6.34.1"),sQuery(id+"F0.wireOp",EDGE,"E6.34.2"),sQuery(id+"F0.wireOp",EDGE,"E6.34.3"),sQuery(id+"F0.wireOp",EDGE,"E6.34.4"),sQuery(id+"F0.wireOp",EDGE,"E6.35.1"),sQuery(id+"F0.wireOp",EDGE,"E6.35.2"),sQuery(id+"F0.wireOp",EDGE,"E6.35.3"),sQuery(id+"F0.wireOp",EDGE,"E6.35.4"),sQuery(id+"F0.wireOp",EDGE,"E6.36.1"),sQuery(id+"F0.wireOp",EDGE,"E6.36.2"),sQuery(id+"F0.wireOp",EDGE,"E6.36.3"),sQuery(id+"F0.wireOp",EDGE,"E6.36.4"),sQuery(id+"F0.wireOp",EDGE,"E6.37.1"),sQuery(id+"F0.wireOp",EDGE,"E6.37.2"),sQuery(id+"F0.wireOp",EDGE,"E6.37.3"),sQuery(id+"F0.wireOp",EDGE,"E6.37.4"),sQuery(id+"F0.wireOp",EDGE,"E6.38.1"),sQuery(id+"F0.wireOp",EDGE,"E6.38.2"),sQuery(id+"F0.wireOp",EDGE,"E6.38.3"),sQuery(id+"F0.wireOp",EDGE,"E6.38.4"),sQuery(id+"F0.wireOp",EDGE,"E6.39.1"),sQuery(id+"F0.wireOp",EDGE,"E6.39.2"),sQuery(id+"F0.wireOp",EDGE,"E6.39.3"),sQuery(id+"F0.wireOp",EDGE,"E6.39.4"),sQuery(id+"F0.wireOp",EDGE,"E6.40.1"),sQuery(id+"F0.wireOp",EDGE,"E6.40.2"),sQuery(id+"F0.wireOp",EDGE,"E6.40.3"),sQuery(id+"F0.wireOp",EDGE,"E6.40.4"),sQuery(id+"F0.wireOp",EDGE,"E6.41.1"),sQuery(id+"F0.wireOp",EDGE,"E6.41.2"),sQuery(id+"F0.wireOp",EDGE,"E6.41.3"),sQuery(id+"F0.wireOp",EDGE,"E6.41.4"),sQuery(id+"F0.wireOp",EDGE,"E6.42.1"),sQuery(id+"F0.wireOp",EDGE,"E6.42.2"),sQuery(id+"F0.wireOp",EDGE,"E6.42.3"),sQuery(id+"F0.wireOp",EDGE,"E6.42.4"),sQuery(id+"F0.wireOp",EDGE,"E6.43.1"),sQuery(id+"F0.wireOp",EDGE,"E6.43.2"),sQuery(id+"F0.wireOp",EDGE,"E6.43.3"),sQuery(id+"F0.wireOp",EDGE,"E6.43.4"),sQuery(id+"F0.wireOp",EDGE,"E7"),sQuery(id+"F0.wireOp",EDGE,"E8.1.0"),sQuery(id+"F0.wireOp",EDGE,"E8.2.0"),sQuery(id+"F0.wireOp",EDGE,"E8.3.0"),sQuery(id+"F0.wireOp",EDGE,"E8.4.0"),sQuery(id+"F0.wireOp",EDGE,"E8.5.0"),sQuery(id+"F0.wireOp",EDGE,"E8.6.0"),sQuery(id+"F0.wireOp",EDGE,"E8.7.0"),sQuery(id+"F0.wireOp",EDGE,"E8.8.0"),sQuery(id+"F0.wireOp",EDGE,"E8.9.0"),sQuery(id+"F0.wireOp",EDGE,"E8.10.0"),sQuery(id+"F0.wireOp",EDGE,"E8.11.0"),sQuery(id+"F0.wireOp",EDGE,"E8.12.0"),sQuery(id+"F0.wireOp",EDGE,"E8.13.0"),sQuery(id+"F0.wireOp",EDGE,"E8.14.0"),sQuery(id+"F0.wireOp",EDGE,"E8.15.0"),sQuery(id+"F0.wireOp",EDGE,"E8.16.0"),sQuery(id+"F0.wireOp",EDGE,"E8.17.0"),sQuery(id+"F0.wireOp",EDGE,"E8.18.0"),sQuery(id+"F0.wireOp",EDGE,"E8.19.0"),sQuery(id+"F0.wireOp",EDGE,"E8.20.0"),sQuery(id+"F0.wireOp",EDGE,"E8.21.0"),sQuery(id+"F0.wireOp",EDGE,"E8.22.0"),sQuery(id+"F0.wireOp",EDGE,"E8.23.0"),sQuery(id+"F0.wireOp",EDGE,"E8.24.0"),sQuery(id+"F0.wireOp",EDGE,"E8.25.0"),sQuery(id+"F0.wireOp",EDGE,"E8.26.0"),sQuery(id+"F0.wireOp",EDGE,"E8.27.0"),sQuery(id+"F0.wireOp",EDGE,"E8.28.0"),sQuery(id+"F0.wireOp",EDGE,"E8.29.0"),sQuery(id+"F0.wireOp",EDGE,"E8.30.0"),sQuery(id+"F0.wireOp",EDGE,"E8.31.0"),sQuery(id+"F0.wireOp",EDGE,"E8.32.0"),sQuery(id+"F0.wireOp",EDGE,"E8.33.0"),sQuery(id+"F0.wireOp",EDGE,"E8.34.0"),sQuery(id+"F0.wireOp",EDGE,"E8.35.0"),sQuery(id+"F0.wireOp",EDGE,"E8.36.0"),sQuery(id+"F0.wireOp",EDGE,"E8.37.0"),sQuery(id+"F0.wireOp",EDGE,"E8.38.0"),sQuery(id+"F0.wireOp",EDGE,"E8.39.0"),sQuery(id+"F0.wireOp",EDGE,"E8.40.0"),sQuery(id+"F0.wireOp",EDGE,"E8.41.0"),sQuery(id+"F0.wireOp",EDGE,"E8.42.0"),sQuery(id+"F0.wireOp",EDGE,"E8.43.0")])],"isStart":true})],"blendedInto":[makeQuery(id+"F1.opExtrude","CAP_FACE",FACE,{"disambiguationData":[OSD([sQuery(id+"F0.wireOp",EDGE,"E0"),sQuery(id+"F0.wireOp",EDGE,"E1"),sQuery(id+"F0.wireOp",EDGE,"E2"),sQuery(id+"F0.wireOp",EDGE,"E4"),sQuery(id+"F0.wireOp",EDGE,"E5"),sQuery(id+"F0.wireOp",EDGE,"E6.1.1"),sQuery(id+"F0.wireOp",EDGE,"E6.1.2"),sQuery(id+"F0.wireOp",EDGE,"E6.1.3"),sQuery(id+"F0.wireOp",EDGE,"E6.1.4"),sQuery(id+"F0.wireOp",EDGE,"E6.2.1"),sQuery(id+"F0.wireOp",EDGE,"E6.2.2"),sQuery(id+"F0.wireOp",EDGE,"E6.2.3"),sQuery(id+"F0.wireOp",EDGE,"E6.2.4"),sQuery(id+"F0.wireOp",EDGE,"E6.3.1"),sQuery(id+"F0.wireOp",EDGE,"E6.3.2"),sQuery(id+"F0.wireOp",EDGE,"E6.3.3"),sQuery(id+"F0.wireOp",EDGE,"E6.3.4"),sQuery(id+"F0.wireOp",EDGE,"E6.4.1"),sQuery(id+"F0.wireOp",EDGE,"E6.4.2"),sQuery(id+"F0.wireOp",EDGE,"E6.4.3"),sQuery(id+"F0.wireOp",EDGE,"E6.4.4"),sQuery(id+"F0.wireOp",EDGE,"E6.5.1"),sQuery(id+"F0.wireOp",EDGE,"E6.5.2"),sQuery(id+"F0.wireOp",EDGE,"E6.5.3"),sQuery(id+"F0.wireOp",EDGE,"E6.5.4"),sQuery(id+"F0.wireOp",EDGE,"E6.6.1"),sQuery(id+"F0.wireOp",EDGE,"E6.6.2"),sQuery(id+"F0.wireOp",EDGE,"E6.6.3"),sQuery(id+"F0.wireOp",EDGE,"E6.6.4"),sQuery(id+"F0.wireOp",EDGE,"E6.7.1"),sQuery(id+"F0.wireOp",EDGE,"E6.7.2"),sQuery(id+"F0.wireOp",EDGE,"E6.7.3"),sQuery(id+"F0.wireOp",EDGE,"E6.7.4"),sQuery(id+"F0.wireOp",EDGE,"E6.8.1"),sQuery(id+"F0.wireOp",EDGE,"E6.8.2"),sQuery(id+"F0.wireOp",EDGE,"E6.8.3"),sQuery(id+"F0.wireOp",EDGE,"E6.8.4"),sQuery(id+"F0.wireOp",EDGE,"E6.9.1"),sQuery(id+"F0.wireOp",EDGE,"E6.9.2"),sQuery(id+"F0.wireOp",EDGE,"E6.9.3"),sQuery(id+"F0.wireOp",EDGE,"E6.9.4"),sQuery(id+"F0.wireOp",EDGE,"E6.10.1"),sQuery(id+"F0.wireOp",EDGE,"E6.10.2"),sQuery(id+"F0.wireOp",EDGE,"E6.10.3"),sQuery(id+"F0.wireOp",EDGE,"E6.10.4"),sQuery(id+"F0.wireOp",EDGE,"E6.11.1"),sQuery(id+"F0.wireOp",EDGE,"E6.11.2"),sQuery(id+"F0.wireOp",EDGE,"E6.11.3"),sQuery(id+"F0.wireOp",EDGE,"E6.11.4"),sQuery(id+"F0.wireOp",EDGE,"E6.12.1"),sQuery(id+"F0.wireOp",EDGE,"E6.12.2"),sQuery(id+"F0.wireOp",EDGE,"E6.12.3"),sQuery(id+"F0.wireOp",EDGE,"E6.12.4"),sQuery(id+"F0.wireOp",EDGE,"E6.13.1"),sQuery(id+"F0.wireOp",EDGE,"E6.13.2"),sQuery(id+"F0.wireOp",EDGE,"E6.13.3"),sQuery(id+"F0.wireOp",EDGE,"E6.13.4"),sQuery(id+"F0.wireOp",EDGE,"E6.14.1"),sQuery(id+"F0.wireOp",EDGE,"E6.14.2"),sQuery(id+"F0.wireOp",EDGE,"E6.14.3"),sQuery(id+"F0.wireOp",EDGE,"E6.14.4"),sQuery(id+"F0.wireOp",EDGE,"E6.15.1"),sQuery(id+"F0.wireOp",EDGE,"E6.15.2"),sQuery(id+"F0.wireOp",EDGE,"E6.15.3"),sQuery(id+"F0.wireOp",EDGE,"E6.15.4"),sQuery(id+"F0.wireOp",EDGE,"E6.16.1"),sQuery(id+"F0.wireOp",EDGE,"E6.16.2"),sQuery(id+"F0.wireOp",EDGE,"E6.16.3"),sQuery(id+"F0.wireOp",EDGE,"E6.16.4"),sQuery(id+"F0.wireOp",EDGE,"E6.17.1"),sQuery(id+"F0.wireOp",EDGE,"E6.17.2"),sQuery(id+"F0.wireOp",EDGE,"E6.17.3"),sQuery(id+"F0.wireOp",EDGE,"E6.17.4"),sQuery(id+"F0.wireOp",EDGE,"E6.18.1"),sQuery(id+"F0.wireOp",EDGE,"E6.18.2"),sQuery(id+"F0.wireOp",EDGE,"E6.18.3"),sQuery(id+"F0.wireOp",EDGE,"E6.18.4"),sQuery(id+"F0.wireOp",EDGE,"E6.19.1"),sQuery(id+"F0.wireOp",EDGE,"E6.19.2"),sQuery(id+"F0.wireOp",EDGE,"E6.19.3"),sQuery(id+"F0.wireOp",EDGE,"E6.19.4"),subQ1,sQuery(id+"F0.wireOp",EDGE,"E6.20.2"),subQ0,sQuery(id+"F0.wireOp",EDGE,"E6.20.4"),sQuery(id+"F0.wireOp",EDGE,"E6.21.1"),sQuery(id+"F0.wireOp",EDGE,"E6.21.2"),sQuery(id+"F0.wireOp",EDGE,"E6.21.3"),sQuery(id+"F0.wireOp",EDGE,"E6.21.4"),sQuery(id+"F0.wireOp",EDGE,"E6.22.1"),sQuery(id+"F0.wireOp",EDGE,"E6.22.2"),sQuery(id+"F0.wireOp",EDGE,"E6.22.3"),sQuery(id+"F0.wireOp",EDGE,"E6.22.4"),sQuery(id+"F0.wireOp",EDGE,"E6.23.1"),sQuery(id+"F0.wireOp",EDGE,"E6.23.2"),sQuery(id+"F0.wireOp",EDGE,"E6.23.3"),sQuery(id+"F0.wireOp",EDGE,"E6.23.4"),sQuery(id+"F0.wireOp",EDGE,"E6.24.1"),sQuery(id+"F0.wireOp",EDGE,"E6.24.2"),sQuery(id+"F0.wireOp",EDGE,"E6.24.3"),sQuery(id+"F0.wireOp",EDGE,"E6.24.4"),sQuery(id+"F0.wireOp",EDGE,"E6.25.1"),sQuery(id+"F0.wireOp",EDGE,"E6.25.2"),sQuery(id+"F0.wireOp",EDGE,"E6.25.3"),sQuery(id+"F0.wireOp",EDGE,"E6.25.4"),sQuery(id+"F0.wireOp",EDGE,"E6.26.1"),sQuery(id+"F0.wireOp",EDGE,"E6.26.2"),sQuery(id+"F0.wireOp",EDGE,"E6.26.3"),sQuery(id+"F0.wireOp",EDGE,"E6.26.4"),sQuery(id+"F0.wireOp",EDGE,"E6.27.1"),sQuery(id+"F0.wireOp",EDGE,"E6.27.2"),sQuery(id+"F0.wireOp",EDGE,"E6.27.3"),sQuery(id+"F0.wireOp",EDGE,"E6.27.4"),sQuery(id+"F0.wireOp",EDGE,"E6.28.1"),sQuery(id+"F0.wireOp",EDGE,"E6.28.2"),sQuery(id+"F0.wireOp",EDGE,"E6.28.3"),sQuery(id+"F0.wireOp",EDGE,"E6.28.4"),sQuery(id+"F0.wireOp",EDGE,"E6.29.1"),sQuery(id+"F0.wireOp",EDGE,"E6.29.2"),sQuery(id+"F0.wireOp",EDGE,"E6.29.3"),sQuery(id+"F0.wireOp",EDGE,"E6.29.4"),sQuery(id+"F0.wireOp",EDGE,"E6.30.1"),sQuery(id+"F0.wireOp",EDGE,"E6.30.2"),sQuery(id+"F0.wireOp",EDGE,"E6.30.3"),sQuery(id+"F0.wireOp",EDGE,"E6.30.4"),sQuery(id+"F0.wireOp",EDGE,"E6.31.1"),sQuery(id+"F0.wireOp",EDGE,"E6.31.2"),sQuery(id+"F0.wireOp",EDGE,"E6.31.3"),sQuery(id+"F0.wireOp",EDGE,"E6.31.4"),sQuery(id+"F0.wireOp",EDGE,"E6.32.1"),sQuery(id+"F0.wireOp",EDGE,"E6.32.2"),sQuery(id+"F0.wireOp",EDGE,"E6.32.3"),sQuery(id+"F0.wireOp",EDGE,"E6.32.4"),sQuery(id+"F0.wireOp",EDGE,"E6.33.1"),sQuery(id+"F0.wireOp",EDGE,"E6.33.2"),sQuery(id+"F0.wireOp",EDGE,"E6.33.3"),sQuery(id+"F0.wireOp",EDGE,"E6.33.4"),sQuery(id+"F0.wireOp",EDGE,"E6.34.1"),sQuery(id+"F0.wireOp",EDGE,"E6.34.2"),sQuery(id+"F0.wireOp",EDGE,"E6.34.3"),sQuery(id+"F0.wireOp",EDGE,"E6.34.4"),sQuery(id+"F0.wireOp",EDGE,"E6.35.1"),sQuery(id+"F0.wireOp",EDGE,"E6.35.2"),sQuery(id+"F0.wireOp",EDGE,"E6.35.3"),sQuery(id+"F0.wireOp",EDGE,"E6.35.4"),sQuery(id+"F0.wireOp",EDGE,"E6.36.1"),sQuery(id+"F0.wireOp",EDGE,"E6.36.2"),sQuery(id+"F0.wireOp",EDGE,"E6.36.3"),sQuery(id+"F0.wireOp",EDGE,"E6.36.4"),sQuery(id+"F0.wireOp",EDGE,"E6.37.1"),sQuery(id+"F0.wireOp",EDGE,"E6.37.2"),sQuery(id+"F0.wireOp",EDGE,"E6.37.3"),sQuery(id+"F0.wireOp",EDGE,"E6.37.4"),sQuery(id+"F0.wireOp",EDGE,"E6.38.1"),sQuery(id+"F0.wireOp",EDGE,"E6.38.2"),sQuery(id+"F0.wireOp",EDGE,"E6.38.3"),sQuery(id+"F0.wireOp",EDGE,"E6.38.4"),sQuery(id+"F0.wireOp",EDGE,"E6.39.1"),sQuery(id+"F0.wireOp",EDGE,"E6.39.2"),sQuery(id+"F0.wireOp",EDGE,"E6.39.3"),sQuery(id+"F0.wireOp",EDGE,"E6.39.4"),sQuery(id+"F0.wireOp",EDGE,"E6.40.1"),sQuery(id+"F0.wireOp",EDGE,"E6.40.2"),sQuery(id+"F0.wireOp",EDGE,"E6.40.3"),sQuery(id+"F0.wireOp",EDGE,"E6.40.4"),sQuery(id+"F0.wireOp",EDGE,"E6.41.1"),sQuery(id+"F0.wireOp",EDGE,"E6.41.2"),sQuery(id+"F0.wireOp",EDGE,"E6.41.3"),sQuery(id+"F0.wireOp",EDGE,"E6.41.4"),sQuery(id+"F0.wireOp",EDGE,"E6.42.1"),sQuery(id+"F0.wireOp",EDGE,"E6.42.2"),sQuery(id+"F0.wireOp",EDGE,"E6.42.3"),sQuery(id+"F0.wireOp",EDGE,"E6.42.4"),sQuery(id+"F0.wireOp",EDGE,"E6.43.1"),sQuery(id+"F0.wireOp",EDGE,"E6.43.2"),sQuery(id+"F0.wireOp",EDGE,"E6.43.3"),sQuery(id+"F0.wireOp",EDGE,"E6.43.4"),sQuery(id+"F0.wireOp",EDGE,"E7"),sQuery(id+"F0.wireOp",EDGE,"E8.1.0"),sQuery(id+"F0.wireOp",EDGE,"E8.2.0"),sQuery(id+"F0.wireOp",EDGE,"E8.3.0"),sQuery(id+"F0.wireOp",EDGE,"E8.4.0"),sQuery(id+"F0.wireOp",EDGE,"E8.5.0"),sQuery(id+"F0.wireOp",EDGE,"E8.6.0"),sQuery(id+"F0.wireOp",EDGE,"E8.7.0"),sQuery(id+"F0.wireOp",EDGE,"E8.8.0"),sQuery(id+"F0.wireOp",EDGE,"E8.9.0"),sQuery(id+"F0.wireOp",EDGE,"E8.10.0"),sQuery(id+"F0.wireOp",EDGE,"E8.11.0"),sQuery(id+"F0.wireOp",EDGE,"E8.12.0"),sQuery(id+"F0.wireOp",EDGE,"E8.13.0"),sQuery(id+"F0.wireOp",EDGE,"E8.14.0"),sQuery(id+"F0.wireOp",EDGE,"E8.15.0"),sQuery(id+"F0.wireOp",EDGE,"E8.16.0"),sQuery(id+"F0.wireOp",EDGE,"E8.17.0"),sQuery(id+"F0.wireOp",EDGE,"E8.18.0"),sQuery(id+"F0.wireOp",EDGE,"E8.19.0"),sQuery(id+"F0.wireOp",EDGE,"E8.20.0"),sQuery(id+"F0.wireOp",EDGE,"E8.21.0"),sQuery(id+"F0.wireOp",EDGE,"E8.22.0"),sQuery(id+"F0.wireOp",EDGE,"E8.23.0"),sQuery(id+"F0.wireOp",EDGE,"E8.24.0"),sQuery(id+"F0.wireOp",EDGE,"E8.25.0"),sQuery(id+"F0.wireOp",EDGE,"E8.26.0"),sQuery(id+"F0.wireOp",EDGE,"E8.27.0"),sQuery(id+"F0.wireOp",EDGE,"E8.28.0"),sQuery(id+"F0.wireOp",EDGE,"E8.29.0"),sQuery(id+"F0.wireOp",EDGE,"E8.30.0"),sQuery(id+"F0.wireOp",EDGE,"E8.31.0"),sQuery(id+"F0.wireOp",EDGE,"E8.32.0"),sQuery(id+"F0.wireOp",EDGE,"E8.33.0"),sQuery(id+"F0.wireOp",EDGE,"E8.34.0"),sQuery(id+"F0.wireOp",EDGE,"E8.35.0"),sQuery(id+"F0.wireOp",EDGE,"E8.36.0"),sQuery(id+"F0.wireOp",EDGE,"E8.37.0"),sQuery(id+"F0.wireOp",EDGE,"E8.38.0"),sQuery(id+"F0.wireOp",EDGE,"E8.39.0"),sQuery(id+"F0.wireOp",EDGE,"E8.40.0"),sQuery(id+"F0.wireOp",EDGE,"E8.41.0"),sQuery(id+"F0.wireOp",EDGE,"E8.42.0"),sQuery(id+"F0.wireOp",EDGE,"E8.43.0")])],"isStart":true})]});}
            var Q32;
            {var subQ0=sQuery(id+"F0.wireOp",EDGE,"E6.22.3");var subQ1=sQuery(id+"F0.wireOp",EDGE,"E6.22.1");Q32=makeQuery(id+"F2.opFillet","BLEND_EDGE",EDGE,{"blendedFrom":[makeQuery(id+"F1.opExtrude","SWEPT_EDGE",EDGE,{"disambiguationData":[OSD([sQuery(id+"F0.wireOp",EDGE,"E6.22.0"),subQ1,subQ0])]}),makeQuery(id+"F1.opExtrude","CAP_FACE",FACE,{"disambiguationData":[OSD([sQuery(id+"F0.wireOp",EDGE,"E0"),sQuery(id+"F0.wireOp",EDGE,"E1"),sQuery(id+"F0.wireOp",EDGE,"E2"),sQuery(id+"F0.wireOp",EDGE,"E4"),sQuery(id+"F0.wireOp",EDGE,"E5"),sQuery(id+"F0.wireOp",EDGE,"E6.1.1"),sQuery(id+"F0.wireOp",EDGE,"E6.1.2"),sQuery(id+"F0.wireOp",EDGE,"E6.1.3"),sQuery(id+"F0.wireOp",EDGE,"E6.1.4"),sQuery(id+"F0.wireOp",EDGE,"E6.2.1"),sQuery(id+"F0.wireOp",EDGE,"E6.2.2"),sQuery(id+"F0.wireOp",EDGE,"E6.2.3"),sQuery(id+"F0.wireOp",EDGE,"E6.2.4"),sQuery(id+"F0.wireOp",EDGE,"E6.3.1"),sQuery(id+"F0.wireOp",EDGE,"E6.3.2"),sQuery(id+"F0.wireOp",EDGE,"E6.3.3"),sQuery(id+"F0.wireOp",EDGE,"E6.3.4"),sQuery(id+"F0.wireOp",EDGE,"E6.4.1"),sQuery(id+"F0.wireOp",EDGE,"E6.4.2"),sQuery(id+"F0.wireOp",EDGE,"E6.4.3"),sQuery(id+"F0.wireOp",EDGE,"E6.4.4"),sQuery(id+"F0.wireOp",EDGE,"E6.5.1"),sQuery(id+"F0.wireOp",EDGE,"E6.5.2"),sQuery(id+"F0.wireOp",EDGE,"E6.5.3"),sQuery(id+"F0.wireOp",EDGE,"E6.5.4"),sQuery(id+"F0.wireOp",EDGE,"E6.6.1"),sQuery(id+"F0.wireOp",EDGE,"E6.6.2"),sQuery(id+"F0.wireOp",EDGE,"E6.6.3"),sQuery(id+"F0.wireOp",EDGE,"E6.6.4"),sQuery(id+"F0.wireOp",EDGE,"E6.7.1"),sQuery(id+"F0.wireOp",EDGE,"E6.7.2"),sQuery(id+"F0.wireOp",EDGE,"E6.7.3"),sQuery(id+"F0.wireOp",EDGE,"E6.7.4"),sQuery(id+"F0.wireOp",EDGE,"E6.8.1"),sQuery(id+"F0.wireOp",EDGE,"E6.8.2"),sQuery(id+"F0.wireOp",EDGE,"E6.8.3"),sQuery(id+"F0.wireOp",EDGE,"E6.8.4"),sQuery(id+"F0.wireOp",EDGE,"E6.9.1"),sQuery(id+"F0.wireOp",EDGE,"E6.9.2"),sQuery(id+"F0.wireOp",EDGE,"E6.9.3"),sQuery(id+"F0.wireOp",EDGE,"E6.9.4"),sQuery(id+"F0.wireOp",EDGE,"E6.10.1"),sQuery(id+"F0.wireOp",EDGE,"E6.10.2"),sQuery(id+"F0.wireOp",EDGE,"E6.10.3"),sQuery(id+"F0.wireOp",EDGE,"E6.10.4"),sQuery(id+"F0.wireOp",EDGE,"E6.11.1"),sQuery(id+"F0.wireOp",EDGE,"E6.11.2"),sQuery(id+"F0.wireOp",EDGE,"E6.11.3"),sQuery(id+"F0.wireOp",EDGE,"E6.11.4"),sQuery(id+"F0.wireOp",EDGE,"E6.12.1"),sQuery(id+"F0.wireOp",EDGE,"E6.12.2"),sQuery(id+"F0.wireOp",EDGE,"E6.12.3"),sQuery(id+"F0.wireOp",EDGE,"E6.12.4"),sQuery(id+"F0.wireOp",EDGE,"E6.13.1"),sQuery(id+"F0.wireOp",EDGE,"E6.13.2"),sQuery(id+"F0.wireOp",EDGE,"E6.13.3"),sQuery(id+"F0.wireOp",EDGE,"E6.13.4"),sQuery(id+"F0.wireOp",EDGE,"E6.14.1"),sQuery(id+"F0.wireOp",EDGE,"E6.14.2"),sQuery(id+"F0.wireOp",EDGE,"E6.14.3"),sQuery(id+"F0.wireOp",EDGE,"E6.14.4"),sQuery(id+"F0.wireOp",EDGE,"E6.15.1"),sQuery(id+"F0.wireOp",EDGE,"E6.15.2"),sQuery(id+"F0.wireOp",EDGE,"E6.15.3"),sQuery(id+"F0.wireOp",EDGE,"E6.15.4"),sQuery(id+"F0.wireOp",EDGE,"E6.16.1"),sQuery(id+"F0.wireOp",EDGE,"E6.16.2"),sQuery(id+"F0.wireOp",EDGE,"E6.16.3"),sQuery(id+"F0.wireOp",EDGE,"E6.16.4"),sQuery(id+"F0.wireOp",EDGE,"E6.17.1"),sQuery(id+"F0.wireOp",EDGE,"E6.17.2"),sQuery(id+"F0.wireOp",EDGE,"E6.17.3"),sQuery(id+"F0.wireOp",EDGE,"E6.17.4"),sQuery(id+"F0.wireOp",EDGE,"E6.18.1"),sQuery(id+"F0.wireOp",EDGE,"E6.18.2"),sQuery(id+"F0.wireOp",EDGE,"E6.18.3"),sQuery(id+"F0.wireOp",EDGE,"E6.18.4"),sQuery(id+"F0.wireOp",EDGE,"E6.19.1"),sQuery(id+"F0.wireOp",EDGE,"E6.19.2"),sQuery(id+"F0.wireOp",EDGE,"E6.19.3"),sQuery(id+"F0.wireOp",EDGE,"E6.19.4"),sQuery(id+"F0.wireOp",EDGE,"E6.20.1"),sQuery(id+"F0.wireOp",EDGE,"E6.20.2"),sQuery(id+"F0.wireOp",EDGE,"E6.20.3"),sQuery(id+"F0.wireOp",EDGE,"E6.20.4"),sQuery(id+"F0.wireOp",EDGE,"E6.21.1"),sQuery(id+"F0.wireOp",EDGE,"E6.21.2"),sQuery(id+"F0.wireOp",EDGE,"E6.21.3"),sQuery(id+"F0.wireOp",EDGE,"E6.21.4"),subQ1,sQuery(id+"F0.wireOp",EDGE,"E6.22.2"),subQ0,sQuery(id+"F0.wireOp",EDGE,"E6.22.4"),sQuery(id+"F0.wireOp",EDGE,"E6.23.1"),sQuery(id+"F0.wireOp",EDGE,"E6.23.2"),sQuery(id+"F0.wireOp",EDGE,"E6.23.3"),sQuery(id+"F0.wireOp",EDGE,"E6.23.4"),sQuery(id+"F0.wireOp",EDGE,"E6.24.1"),sQuery(id+"F0.wireOp",EDGE,"E6.24.2"),sQuery(id+"F0.wireOp",EDGE,"E6.24.3"),sQuery(id+"F0.wireOp",EDGE,"E6.24.4"),sQuery(id+"F0.wireOp",EDGE,"E6.25.1"),sQuery(id+"F0.wireOp",EDGE,"E6.25.2"),sQuery(id+"F0.wireOp",EDGE,"E6.25.3"),sQuery(id+"F0.wireOp",EDGE,"E6.25.4"),sQuery(id+"F0.wireOp",EDGE,"E6.26.1"),sQuery(id+"F0.wireOp",EDGE,"E6.26.2"),sQuery(id+"F0.wireOp",EDGE,"E6.26.3"),sQuery(id+"F0.wireOp",EDGE,"E6.26.4"),sQuery(id+"F0.wireOp",EDGE,"E6.27.1"),sQuery(id+"F0.wireOp",EDGE,"E6.27.2"),sQuery(id+"F0.wireOp",EDGE,"E6.27.3"),sQuery(id+"F0.wireOp",EDGE,"E6.27.4"),sQuery(id+"F0.wireOp",EDGE,"E6.28.1"),sQuery(id+"F0.wireOp",EDGE,"E6.28.2"),sQuery(id+"F0.wireOp",EDGE,"E6.28.3"),sQuery(id+"F0.wireOp",EDGE,"E6.28.4"),sQuery(id+"F0.wireOp",EDGE,"E6.29.1"),sQuery(id+"F0.wireOp",EDGE,"E6.29.2"),sQuery(id+"F0.wireOp",EDGE,"E6.29.3"),sQuery(id+"F0.wireOp",EDGE,"E6.29.4"),sQuery(id+"F0.wireOp",EDGE,"E6.30.1"),sQuery(id+"F0.wireOp",EDGE,"E6.30.2"),sQuery(id+"F0.wireOp",EDGE,"E6.30.3"),sQuery(id+"F0.wireOp",EDGE,"E6.30.4"),sQuery(id+"F0.wireOp",EDGE,"E6.31.1"),sQuery(id+"F0.wireOp",EDGE,"E6.31.2"),sQuery(id+"F0.wireOp",EDGE,"E6.31.3"),sQuery(id+"F0.wireOp",EDGE,"E6.31.4"),sQuery(id+"F0.wireOp",EDGE,"E6.32.1"),sQuery(id+"F0.wireOp",EDGE,"E6.32.2"),sQuery(id+"F0.wireOp",EDGE,"E6.32.3"),sQuery(id+"F0.wireOp",EDGE,"E6.32.4"),sQuery(id+"F0.wireOp",EDGE,"E6.33.1"),sQuery(id+"F0.wireOp",EDGE,"E6.33.2"),sQuery(id+"F0.wireOp",EDGE,"E6.33.3"),sQuery(id+"F0.wireOp",EDGE,"E6.33.4"),sQuery(id+"F0.wireOp",EDGE,"E6.34.1"),sQuery(id+"F0.wireOp",EDGE,"E6.34.2"),sQuery(id+"F0.wireOp",EDGE,"E6.34.3"),sQuery(id+"F0.wireOp",EDGE,"E6.34.4"),sQuery(id+"F0.wireOp",EDGE,"E6.35.1"),sQuery(id+"F0.wireOp",EDGE,"E6.35.2"),sQuery(id+"F0.wireOp",EDGE,"E6.35.3"),sQuery(id+"F0.wireOp",EDGE,"E6.35.4"),sQuery(id+"F0.wireOp",EDGE,"E6.36.1"),sQuery(id+"F0.wireOp",EDGE,"E6.36.2"),sQuery(id+"F0.wireOp",EDGE,"E6.36.3"),sQuery(id+"F0.wireOp",EDGE,"E6.36.4"),sQuery(id+"F0.wireOp",EDGE,"E6.37.1"),sQuery(id+"F0.wireOp",EDGE,"E6.37.2"),sQuery(id+"F0.wireOp",EDGE,"E6.37.3"),sQuery(id+"F0.wireOp",EDGE,"E6.37.4"),sQuery(id+"F0.wireOp",EDGE,"E6.38.1"),sQuery(id+"F0.wireOp",EDGE,"E6.38.2"),sQuery(id+"F0.wireOp",EDGE,"E6.38.3"),sQuery(id+"F0.wireOp",EDGE,"E6.38.4"),sQuery(id+"F0.wireOp",EDGE,"E6.39.1"),sQuery(id+"F0.wireOp",EDGE,"E6.39.2"),sQuery(id+"F0.wireOp",EDGE,"E6.39.3"),sQuery(id+"F0.wireOp",EDGE,"E6.39.4"),sQuery(id+"F0.wireOp",EDGE,"E6.40.1"),sQuery(id+"F0.wireOp",EDGE,"E6.40.2"),sQuery(id+"F0.wireOp",EDGE,"E6.40.3"),sQuery(id+"F0.wireOp",EDGE,"E6.40.4"),sQuery(id+"F0.wireOp",EDGE,"E6.41.1"),sQuery(id+"F0.wireOp",EDGE,"E6.41.2"),sQuery(id+"F0.wireOp",EDGE,"E6.41.3"),sQuery(id+"F0.wireOp",EDGE,"E6.41.4"),sQuery(id+"F0.wireOp",EDGE,"E6.42.1"),sQuery(id+"F0.wireOp",EDGE,"E6.42.2"),sQuery(id+"F0.wireOp",EDGE,"E6.42.3"),sQuery(id+"F0.wireOp",EDGE,"E6.42.4"),sQuery(id+"F0.wireOp",EDGE,"E6.43.1"),sQuery(id+"F0.wireOp",EDGE,"E6.43.2"),sQuery(id+"F0.wireOp",EDGE,"E6.43.3"),sQuery(id+"F0.wireOp",EDGE,"E6.43.4"),sQuery(id+"F0.wireOp",EDGE,"E7"),sQuery(id+"F0.wireOp",EDGE,"E8.1.0"),sQuery(id+"F0.wireOp",EDGE,"E8.2.0"),sQuery(id+"F0.wireOp",EDGE,"E8.3.0"),sQuery(id+"F0.wireOp",EDGE,"E8.4.0"),sQuery(id+"F0.wireOp",EDGE,"E8.5.0"),sQuery(id+"F0.wireOp",EDGE,"E8.6.0"),sQuery(id+"F0.wireOp",EDGE,"E8.7.0"),sQuery(id+"F0.wireOp",EDGE,"E8.8.0"),sQuery(id+"F0.wireOp",EDGE,"E8.9.0"),sQuery(id+"F0.wireOp",EDGE,"E8.10.0"),sQuery(id+"F0.wireOp",EDGE,"E8.11.0"),sQuery(id+"F0.wireOp",EDGE,"E8.12.0"),sQuery(id+"F0.wireOp",EDGE,"E8.13.0"),sQuery(id+"F0.wireOp",EDGE,"E8.14.0"),sQuery(id+"F0.wireOp",EDGE,"E8.15.0"),sQuery(id+"F0.wireOp",EDGE,"E8.16.0"),sQuery(id+"F0.wireOp",EDGE,"E8.17.0"),sQuery(id+"F0.wireOp",EDGE,"E8.18.0"),sQuery(id+"F0.wireOp",EDGE,"E8.19.0"),sQuery(id+"F0.wireOp",EDGE,"E8.20.0"),sQuery(id+"F0.wireOp",EDGE,"E8.21.0"),sQuery(id+"F0.wireOp",EDGE,"E8.22.0"),sQuery(id+"F0.wireOp",EDGE,"E8.23.0"),sQuery(id+"F0.wireOp",EDGE,"E8.24.0"),sQuery(id+"F0.wireOp",EDGE,"E8.25.0"),sQuery(id+"F0.wireOp",EDGE,"E8.26.0"),sQuery(id+"F0.wireOp",EDGE,"E8.27.0"),sQuery(id+"F0.wireOp",EDGE,"E8.28.0"),sQuery(id+"F0.wireOp",EDGE,"E8.29.0"),sQuery(id+"F0.wireOp",EDGE,"E8.30.0"),sQuery(id+"F0.wireOp",EDGE,"E8.31.0"),sQuery(id+"F0.wireOp",EDGE,"E8.32.0"),sQuery(id+"F0.wireOp",EDGE,"E8.33.0"),sQuery(id+"F0.wireOp",EDGE,"E8.34.0"),sQuery(id+"F0.wireOp",EDGE,"E8.35.0"),sQuery(id+"F0.wireOp",EDGE,"E8.36.0"),sQuery(id+"F0.wireOp",EDGE,"E8.37.0"),sQuery(id+"F0.wireOp",EDGE,"E8.38.0"),sQuery(id+"F0.wireOp",EDGE,"E8.39.0"),sQuery(id+"F0.wireOp",EDGE,"E8.40.0"),sQuery(id+"F0.wireOp",EDGE,"E8.41.0"),sQuery(id+"F0.wireOp",EDGE,"E8.42.0"),sQuery(id+"F0.wireOp",EDGE,"E8.43.0")])],"isStart":true})],"blendedInto":[makeQuery(id+"F1.opExtrude","CAP_FACE",FACE,{"disambiguationData":[OSD([sQuery(id+"F0.wireOp",EDGE,"E0"),sQuery(id+"F0.wireOp",EDGE,"E1"),sQuery(id+"F0.wireOp",EDGE,"E2"),sQuery(id+"F0.wireOp",EDGE,"E4"),sQuery(id+"F0.wireOp",EDGE,"E5"),sQuery(id+"F0.wireOp",EDGE,"E6.1.1"),sQuery(id+"F0.wireOp",EDGE,"E6.1.2"),sQuery(id+"F0.wireOp",EDGE,"E6.1.3"),sQuery(id+"F0.wireOp",EDGE,"E6.1.4"),sQuery(id+"F0.wireOp",EDGE,"E6.2.1"),sQuery(id+"F0.wireOp",EDGE,"E6.2.2"),sQuery(id+"F0.wireOp",EDGE,"E6.2.3"),sQuery(id+"F0.wireOp",EDGE,"E6.2.4"),sQuery(id+"F0.wireOp",EDGE,"E6.3.1"),sQuery(id+"F0.wireOp",EDGE,"E6.3.2"),sQuery(id+"F0.wireOp",EDGE,"E6.3.3"),sQuery(id+"F0.wireOp",EDGE,"E6.3.4"),sQuery(id+"F0.wireOp",EDGE,"E6.4.1"),sQuery(id+"F0.wireOp",EDGE,"E6.4.2"),sQuery(id+"F0.wireOp",EDGE,"E6.4.3"),sQuery(id+"F0.wireOp",EDGE,"E6.4.4"),sQuery(id+"F0.wireOp",EDGE,"E6.5.1"),sQuery(id+"F0.wireOp",EDGE,"E6.5.2"),sQuery(id+"F0.wireOp",EDGE,"E6.5.3"),sQuery(id+"F0.wireOp",EDGE,"E6.5.4"),sQuery(id+"F0.wireOp",EDGE,"E6.6.1"),sQuery(id+"F0.wireOp",EDGE,"E6.6.2"),sQuery(id+"F0.wireOp",EDGE,"E6.6.3"),sQuery(id+"F0.wireOp",EDGE,"E6.6.4"),sQuery(id+"F0.wireOp",EDGE,"E6.7.1"),sQuery(id+"F0.wireOp",EDGE,"E6.7.2"),sQuery(id+"F0.wireOp",EDGE,"E6.7.3"),sQuery(id+"F0.wireOp",EDGE,"E6.7.4"),sQuery(id+"F0.wireOp",EDGE,"E6.8.1"),sQuery(id+"F0.wireOp",EDGE,"E6.8.2"),sQuery(id+"F0.wireOp",EDGE,"E6.8.3"),sQuery(id+"F0.wireOp",EDGE,"E6.8.4"),sQuery(id+"F0.wireOp",EDGE,"E6.9.1"),sQuery(id+"F0.wireOp",EDGE,"E6.9.2"),sQuery(id+"F0.wireOp",EDGE,"E6.9.3"),sQuery(id+"F0.wireOp",EDGE,"E6.9.4"),sQuery(id+"F0.wireOp",EDGE,"E6.10.1"),sQuery(id+"F0.wireOp",EDGE,"E6.10.2"),sQuery(id+"F0.wireOp",EDGE,"E6.10.3"),sQuery(id+"F0.wireOp",EDGE,"E6.10.4"),sQuery(id+"F0.wireOp",EDGE,"E6.11.1"),sQuery(id+"F0.wireOp",EDGE,"E6.11.2"),sQuery(id+"F0.wireOp",EDGE,"E6.11.3"),sQuery(id+"F0.wireOp",EDGE,"E6.11.4"),sQuery(id+"F0.wireOp",EDGE,"E6.12.1"),sQuery(id+"F0.wireOp",EDGE,"E6.12.2"),sQuery(id+"F0.wireOp",EDGE,"E6.12.3"),sQuery(id+"F0.wireOp",EDGE,"E6.12.4"),sQuery(id+"F0.wireOp",EDGE,"E6.13.1"),sQuery(id+"F0.wireOp",EDGE,"E6.13.2"),sQuery(id+"F0.wireOp",EDGE,"E6.13.3"),sQuery(id+"F0.wireOp",EDGE,"E6.13.4"),sQuery(id+"F0.wireOp",EDGE,"E6.14.1"),sQuery(id+"F0.wireOp",EDGE,"E6.14.2"),sQuery(id+"F0.wireOp",EDGE,"E6.14.3"),sQuery(id+"F0.wireOp",EDGE,"E6.14.4"),sQuery(id+"F0.wireOp",EDGE,"E6.15.1"),sQuery(id+"F0.wireOp",EDGE,"E6.15.2"),sQuery(id+"F0.wireOp",EDGE,"E6.15.3"),sQuery(id+"F0.wireOp",EDGE,"E6.15.4"),sQuery(id+"F0.wireOp",EDGE,"E6.16.1"),sQuery(id+"F0.wireOp",EDGE,"E6.16.2"),sQuery(id+"F0.wireOp",EDGE,"E6.16.3"),sQuery(id+"F0.wireOp",EDGE,"E6.16.4"),sQuery(id+"F0.wireOp",EDGE,"E6.17.1"),sQuery(id+"F0.wireOp",EDGE,"E6.17.2"),sQuery(id+"F0.wireOp",EDGE,"E6.17.3"),sQuery(id+"F0.wireOp",EDGE,"E6.17.4"),sQuery(id+"F0.wireOp",EDGE,"E6.18.1"),sQuery(id+"F0.wireOp",EDGE,"E6.18.2"),sQuery(id+"F0.wireOp",EDGE,"E6.18.3"),sQuery(id+"F0.wireOp",EDGE,"E6.18.4"),sQuery(id+"F0.wireOp",EDGE,"E6.19.1"),sQuery(id+"F0.wireOp",EDGE,"E6.19.2"),sQuery(id+"F0.wireOp",EDGE,"E6.19.3"),sQuery(id+"F0.wireOp",EDGE,"E6.19.4"),sQuery(id+"F0.wireOp",EDGE,"E6.20.1"),sQuery(id+"F0.wireOp",EDGE,"E6.20.2"),sQuery(id+"F0.wireOp",EDGE,"E6.20.3"),sQuery(id+"F0.wireOp",EDGE,"E6.20.4"),sQuery(id+"F0.wireOp",EDGE,"E6.21.1"),sQuery(id+"F0.wireOp",EDGE,"E6.21.2"),sQuery(id+"F0.wireOp",EDGE,"E6.21.3"),sQuery(id+"F0.wireOp",EDGE,"E6.21.4"),subQ1,sQuery(id+"F0.wireOp",EDGE,"E6.22.2"),subQ0,sQuery(id+"F0.wireOp",EDGE,"E6.22.4"),sQuery(id+"F0.wireOp",EDGE,"E6.23.1"),sQuery(id+"F0.wireOp",EDGE,"E6.23.2"),sQuery(id+"F0.wireOp",EDGE,"E6.23.3"),sQuery(id+"F0.wireOp",EDGE,"E6.23.4"),sQuery(id+"F0.wireOp",EDGE,"E6.24.1"),sQuery(id+"F0.wireOp",EDGE,"E6.24.2"),sQuery(id+"F0.wireOp",EDGE,"E6.24.3"),sQuery(id+"F0.wireOp",EDGE,"E6.24.4"),sQuery(id+"F0.wireOp",EDGE,"E6.25.1"),sQuery(id+"F0.wireOp",EDGE,"E6.25.2"),sQuery(id+"F0.wireOp",EDGE,"E6.25.3"),sQuery(id+"F0.wireOp",EDGE,"E6.25.4"),sQuery(id+"F0.wireOp",EDGE,"E6.26.1"),sQuery(id+"F0.wireOp",EDGE,"E6.26.2"),sQuery(id+"F0.wireOp",EDGE,"E6.26.3"),sQuery(id+"F0.wireOp",EDGE,"E6.26.4"),sQuery(id+"F0.wireOp",EDGE,"E6.27.1"),sQuery(id+"F0.wireOp",EDGE,"E6.27.2"),sQuery(id+"F0.wireOp",EDGE,"E6.27.3"),sQuery(id+"F0.wireOp",EDGE,"E6.27.4"),sQuery(id+"F0.wireOp",EDGE,"E6.28.1"),sQuery(id+"F0.wireOp",EDGE,"E6.28.2"),sQuery(id+"F0.wireOp",EDGE,"E6.28.3"),sQuery(id+"F0.wireOp",EDGE,"E6.28.4"),sQuery(id+"F0.wireOp",EDGE,"E6.29.1"),sQuery(id+"F0.wireOp",EDGE,"E6.29.2"),sQuery(id+"F0.wireOp",EDGE,"E6.29.3"),sQuery(id+"F0.wireOp",EDGE,"E6.29.4"),sQuery(id+"F0.wireOp",EDGE,"E6.30.1"),sQuery(id+"F0.wireOp",EDGE,"E6.30.2"),sQuery(id+"F0.wireOp",EDGE,"E6.30.3"),sQuery(id+"F0.wireOp",EDGE,"E6.30.4"),sQuery(id+"F0.wireOp",EDGE,"E6.31.1"),sQuery(id+"F0.wireOp",EDGE,"E6.31.2"),sQuery(id+"F0.wireOp",EDGE,"E6.31.3"),sQuery(id+"F0.wireOp",EDGE,"E6.31.4"),sQuery(id+"F0.wireOp",EDGE,"E6.32.1"),sQuery(id+"F0.wireOp",EDGE,"E6.32.2"),sQuery(id+"F0.wireOp",EDGE,"E6.32.3"),sQuery(id+"F0.wireOp",EDGE,"E6.32.4"),sQuery(id+"F0.wireOp",EDGE,"E6.33.1"),sQuery(id+"F0.wireOp",EDGE,"E6.33.2"),sQuery(id+"F0.wireOp",EDGE,"E6.33.3"),sQuery(id+"F0.wireOp",EDGE,"E6.33.4"),sQuery(id+"F0.wireOp",EDGE,"E6.34.1"),sQuery(id+"F0.wireOp",EDGE,"E6.34.2"),sQuery(id+"F0.wireOp",EDGE,"E6.34.3"),sQuery(id+"F0.wireOp",EDGE,"E6.34.4"),sQuery(id+"F0.wireOp",EDGE,"E6.35.1"),sQuery(id+"F0.wireOp",EDGE,"E6.35.2"),sQuery(id+"F0.wireOp",EDGE,"E6.35.3"),sQuery(id+"F0.wireOp",EDGE,"E6.35.4"),sQuery(id+"F0.wireOp",EDGE,"E6.36.1"),sQuery(id+"F0.wireOp",EDGE,"E6.36.2"),sQuery(id+"F0.wireOp",EDGE,"E6.36.3"),sQuery(id+"F0.wireOp",EDGE,"E6.36.4"),sQuery(id+"F0.wireOp",EDGE,"E6.37.1"),sQuery(id+"F0.wireOp",EDGE,"E6.37.2"),sQuery(id+"F0.wireOp",EDGE,"E6.37.3"),sQuery(id+"F0.wireOp",EDGE,"E6.37.4"),sQuery(id+"F0.wireOp",EDGE,"E6.38.1"),sQuery(id+"F0.wireOp",EDGE,"E6.38.2"),sQuery(id+"F0.wireOp",EDGE,"E6.38.3"),sQuery(id+"F0.wireOp",EDGE,"E6.38.4"),sQuery(id+"F0.wireOp",EDGE,"E6.39.1"),sQuery(id+"F0.wireOp",EDGE,"E6.39.2"),sQuery(id+"F0.wireOp",EDGE,"E6.39.3"),sQuery(id+"F0.wireOp",EDGE,"E6.39.4"),sQuery(id+"F0.wireOp",EDGE,"E6.40.1"),sQuery(id+"F0.wireOp",EDGE,"E6.40.2"),sQuery(id+"F0.wireOp",EDGE,"E6.40.3"),sQuery(id+"F0.wireOp",EDGE,"E6.40.4"),sQuery(id+"F0.wireOp",EDGE,"E6.41.1"),sQuery(id+"F0.wireOp",EDGE,"E6.41.2"),sQuery(id+"F0.wireOp",EDGE,"E6.41.3"),sQuery(id+"F0.wireOp",EDGE,"E6.41.4"),sQuery(id+"F0.wireOp",EDGE,"E6.42.1"),sQuery(id+"F0.wireOp",EDGE,"E6.42.2"),sQuery(id+"F0.wireOp",EDGE,"E6.42.3"),sQuery(id+"F0.wireOp",EDGE,"E6.42.4"),sQuery(id+"F0.wireOp",EDGE,"E6.43.1"),sQuery(id+"F0.wireOp",EDGE,"E6.43.2"),sQuery(id+"F0.wireOp",EDGE,"E6.43.3"),sQuery(id+"F0.wireOp",EDGE,"E6.43.4"),sQuery(id+"F0.wireOp",EDGE,"E7"),sQuery(id+"F0.wireOp",EDGE,"E8.1.0"),sQuery(id+"F0.wireOp",EDGE,"E8.2.0"),sQuery(id+"F0.wireOp",EDGE,"E8.3.0"),sQuery(id+"F0.wireOp",EDGE,"E8.4.0"),sQuery(id+"F0.wireOp",EDGE,"E8.5.0"),sQuery(id+"F0.wireOp",EDGE,"E8.6.0"),sQuery(id+"F0.wireOp",EDGE,"E8.7.0"),sQuery(id+"F0.wireOp",EDGE,"E8.8.0"),sQuery(id+"F0.wireOp",EDGE,"E8.9.0"),sQuery(id+"F0.wireOp",EDGE,"E8.10.0"),sQuery(id+"F0.wireOp",EDGE,"E8.11.0"),sQuery(id+"F0.wireOp",EDGE,"E8.12.0"),sQuery(id+"F0.wireOp",EDGE,"E8.13.0"),sQuery(id+"F0.wireOp",EDGE,"E8.14.0"),sQuery(id+"F0.wireOp",EDGE,"E8.15.0"),sQuery(id+"F0.wireOp",EDGE,"E8.16.0"),sQuery(id+"F0.wireOp",EDGE,"E8.17.0"),sQuery(id+"F0.wireOp",EDGE,"E8.18.0"),sQuery(id+"F0.wireOp",EDGE,"E8.19.0"),sQuery(id+"F0.wireOp",EDGE,"E8.20.0"),sQuery(id+"F0.wireOp",EDGE,"E8.21.0"),sQuery(id+"F0.wireOp",EDGE,"E8.22.0"),sQuery(id+"F0.wireOp",EDGE,"E8.23.0"),sQuery(id+"F0.wireOp",EDGE,"E8.24.0"),sQuery(id+"F0.wireOp",EDGE,"E8.25.0"),sQuery(id+"F0.wireOp",EDGE,"E8.26.0"),sQuery(id+"F0.wireOp",EDGE,"E8.27.0"),sQuery(id+"F0.wireOp",EDGE,"E8.28.0"),sQuery(id+"F0.wireOp",EDGE,"E8.29.0"),sQuery(id+"F0.wireOp",EDGE,"E8.30.0"),sQuery(id+"F0.wireOp",EDGE,"E8.31.0"),sQuery(id+"F0.wireOp",EDGE,"E8.32.0"),sQuery(id+"F0.wireOp",EDGE,"E8.33.0"),sQuery(id+"F0.wireOp",EDGE,"E8.34.0"),sQuery(id+"F0.wireOp",EDGE,"E8.35.0"),sQuery(id+"F0.wireOp",EDGE,"E8.36.0"),sQuery(id+"F0.wireOp",EDGE,"E8.37.0"),sQuery(id+"F0.wireOp",EDGE,"E8.38.0"),sQuery(id+"F0.wireOp",EDGE,"E8.39.0"),sQuery(id+"F0.wireOp",EDGE,"E8.40.0"),sQuery(id+"F0.wireOp",EDGE,"E8.41.0"),sQuery(id+"F0.wireOp",EDGE,"E8.42.0"),sQuery(id+"F0.wireOp",EDGE,"E8.43.0")])],"isStart":true})]});}
            var Q33;
            {var subQ0=sQuery(id+"F0.wireOp",EDGE,"E6.24.3");var subQ1=sQuery(id+"F0.wireOp",EDGE,"E6.24.1");Q33=makeQuery(id+"F2.opFillet","BLEND_EDGE",EDGE,{"blendedFrom":[makeQuery(id+"F1.opExtrude","SWEPT_EDGE",EDGE,{"disambiguationData":[OSD([sQuery(id+"F0.wireOp",EDGE,"E6.24.0"),subQ1,subQ0])]}),makeQuery(id+"F1.opExtrude","CAP_FACE",FACE,{"disambiguationData":[OSD([sQuery(id+"F0.wireOp",EDGE,"E0"),sQuery(id+"F0.wireOp",EDGE,"E1"),sQuery(id+"F0.wireOp",EDGE,"E2"),sQuery(id+"F0.wireOp",EDGE,"E4"),sQuery(id+"F0.wireOp",EDGE,"E5"),sQuery(id+"F0.wireOp",EDGE,"E6.1.1"),sQuery(id+"F0.wireOp",EDGE,"E6.1.2"),sQuery(id+"F0.wireOp",EDGE,"E6.1.3"),sQuery(id+"F0.wireOp",EDGE,"E6.1.4"),sQuery(id+"F0.wireOp",EDGE,"E6.2.1"),sQuery(id+"F0.wireOp",EDGE,"E6.2.2"),sQuery(id+"F0.wireOp",EDGE,"E6.2.3"),sQuery(id+"F0.wireOp",EDGE,"E6.2.4"),sQuery(id+"F0.wireOp",EDGE,"E6.3.1"),sQuery(id+"F0.wireOp",EDGE,"E6.3.2"),sQuery(id+"F0.wireOp",EDGE,"E6.3.3"),sQuery(id+"F0.wireOp",EDGE,"E6.3.4"),sQuery(id+"F0.wireOp",EDGE,"E6.4.1"),sQuery(id+"F0.wireOp",EDGE,"E6.4.2"),sQuery(id+"F0.wireOp",EDGE,"E6.4.3"),sQuery(id+"F0.wireOp",EDGE,"E6.4.4"),sQuery(id+"F0.wireOp",EDGE,"E6.5.1"),sQuery(id+"F0.wireOp",EDGE,"E6.5.2"),sQuery(id+"F0.wireOp",EDGE,"E6.5.3"),sQuery(id+"F0.wireOp",EDGE,"E6.5.4"),sQuery(id+"F0.wireOp",EDGE,"E6.6.1"),sQuery(id+"F0.wireOp",EDGE,"E6.6.2"),sQuery(id+"F0.wireOp",EDGE,"E6.6.3"),sQuery(id+"F0.wireOp",EDGE,"E6.6.4"),sQuery(id+"F0.wireOp",EDGE,"E6.7.1"),sQuery(id+"F0.wireOp",EDGE,"E6.7.2"),sQuery(id+"F0.wireOp",EDGE,"E6.7.3"),sQuery(id+"F0.wireOp",EDGE,"E6.7.4"),sQuery(id+"F0.wireOp",EDGE,"E6.8.1"),sQuery(id+"F0.wireOp",EDGE,"E6.8.2"),sQuery(id+"F0.wireOp",EDGE,"E6.8.3"),sQuery(id+"F0.wireOp",EDGE,"E6.8.4"),sQuery(id+"F0.wireOp",EDGE,"E6.9.1"),sQuery(id+"F0.wireOp",EDGE,"E6.9.2"),sQuery(id+"F0.wireOp",EDGE,"E6.9.3"),sQuery(id+"F0.wireOp",EDGE,"E6.9.4"),sQuery(id+"F0.wireOp",EDGE,"E6.10.1"),sQuery(id+"F0.wireOp",EDGE,"E6.10.2"),sQuery(id+"F0.wireOp",EDGE,"E6.10.3"),sQuery(id+"F0.wireOp",EDGE,"E6.10.4"),sQuery(id+"F0.wireOp",EDGE,"E6.11.1"),sQuery(id+"F0.wireOp",EDGE,"E6.11.2"),sQuery(id+"F0.wireOp",EDGE,"E6.11.3"),sQuery(id+"F0.wireOp",EDGE,"E6.11.4"),sQuery(id+"F0.wireOp",EDGE,"E6.12.1"),sQuery(id+"F0.wireOp",EDGE,"E6.12.2"),sQuery(id+"F0.wireOp",EDGE,"E6.12.3"),sQuery(id+"F0.wireOp",EDGE,"E6.12.4"),sQuery(id+"F0.wireOp",EDGE,"E6.13.1"),sQuery(id+"F0.wireOp",EDGE,"E6.13.2"),sQuery(id+"F0.wireOp",EDGE,"E6.13.3"),sQuery(id+"F0.wireOp",EDGE,"E6.13.4"),sQuery(id+"F0.wireOp",EDGE,"E6.14.1"),sQuery(id+"F0.wireOp",EDGE,"E6.14.2"),sQuery(id+"F0.wireOp",EDGE,"E6.14.3"),sQuery(id+"F0.wireOp",EDGE,"E6.14.4"),sQuery(id+"F0.wireOp",EDGE,"E6.15.1"),sQuery(id+"F0.wireOp",EDGE,"E6.15.2"),sQuery(id+"F0.wireOp",EDGE,"E6.15.3"),sQuery(id+"F0.wireOp",EDGE,"E6.15.4"),sQuery(id+"F0.wireOp",EDGE,"E6.16.1"),sQuery(id+"F0.wireOp",EDGE,"E6.16.2"),sQuery(id+"F0.wireOp",EDGE,"E6.16.3"),sQuery(id+"F0.wireOp",EDGE,"E6.16.4"),sQuery(id+"F0.wireOp",EDGE,"E6.17.1"),sQuery(id+"F0.wireOp",EDGE,"E6.17.2"),sQuery(id+"F0.wireOp",EDGE,"E6.17.3"),sQuery(id+"F0.wireOp",EDGE,"E6.17.4"),sQuery(id+"F0.wireOp",EDGE,"E6.18.1"),sQuery(id+"F0.wireOp",EDGE,"E6.18.2"),sQuery(id+"F0.wireOp",EDGE,"E6.18.3"),sQuery(id+"F0.wireOp",EDGE,"E6.18.4"),sQuery(id+"F0.wireOp",EDGE,"E6.19.1"),sQuery(id+"F0.wireOp",EDGE,"E6.19.2"),sQuery(id+"F0.wireOp",EDGE,"E6.19.3"),sQuery(id+"F0.wireOp",EDGE,"E6.19.4"),sQuery(id+"F0.wireOp",EDGE,"E6.20.1"),sQuery(id+"F0.wireOp",EDGE,"E6.20.2"),sQuery(id+"F0.wireOp",EDGE,"E6.20.3"),sQuery(id+"F0.wireOp",EDGE,"E6.20.4"),sQuery(id+"F0.wireOp",EDGE,"E6.21.1"),sQuery(id+"F0.wireOp",EDGE,"E6.21.2"),sQuery(id+"F0.wireOp",EDGE,"E6.21.3"),sQuery(id+"F0.wireOp",EDGE,"E6.21.4"),sQuery(id+"F0.wireOp",EDGE,"E6.22.1"),sQuery(id+"F0.wireOp",EDGE,"E6.22.2"),sQuery(id+"F0.wireOp",EDGE,"E6.22.3"),sQuery(id+"F0.wireOp",EDGE,"E6.22.4"),sQuery(id+"F0.wireOp",EDGE,"E6.23.1"),sQuery(id+"F0.wireOp",EDGE,"E6.23.2"),sQuery(id+"F0.wireOp",EDGE,"E6.23.3"),sQuery(id+"F0.wireOp",EDGE,"E6.23.4"),subQ1,sQuery(id+"F0.wireOp",EDGE,"E6.24.2"),subQ0,sQuery(id+"F0.wireOp",EDGE,"E6.24.4"),sQuery(id+"F0.wireOp",EDGE,"E6.25.1"),sQuery(id+"F0.wireOp",EDGE,"E6.25.2"),sQuery(id+"F0.wireOp",EDGE,"E6.25.3"),sQuery(id+"F0.wireOp",EDGE,"E6.25.4"),sQuery(id+"F0.wireOp",EDGE,"E6.26.1"),sQuery(id+"F0.wireOp",EDGE,"E6.26.2"),sQuery(id+"F0.wireOp",EDGE,"E6.26.3"),sQuery(id+"F0.wireOp",EDGE,"E6.26.4"),sQuery(id+"F0.wireOp",EDGE,"E6.27.1"),sQuery(id+"F0.wireOp",EDGE,"E6.27.2"),sQuery(id+"F0.wireOp",EDGE,"E6.27.3"),sQuery(id+"F0.wireOp",EDGE,"E6.27.4"),sQuery(id+"F0.wireOp",EDGE,"E6.28.1"),sQuery(id+"F0.wireOp",EDGE,"E6.28.2"),sQuery(id+"F0.wireOp",EDGE,"E6.28.3"),sQuery(id+"F0.wireOp",EDGE,"E6.28.4"),sQuery(id+"F0.wireOp",EDGE,"E6.29.1"),sQuery(id+"F0.wireOp",EDGE,"E6.29.2"),sQuery(id+"F0.wireOp",EDGE,"E6.29.3"),sQuery(id+"F0.wireOp",EDGE,"E6.29.4"),sQuery(id+"F0.wireOp",EDGE,"E6.30.1"),sQuery(id+"F0.wireOp",EDGE,"E6.30.2"),sQuery(id+"F0.wireOp",EDGE,"E6.30.3"),sQuery(id+"F0.wireOp",EDGE,"E6.30.4"),sQuery(id+"F0.wireOp",EDGE,"E6.31.1"),sQuery(id+"F0.wireOp",EDGE,"E6.31.2"),sQuery(id+"F0.wireOp",EDGE,"E6.31.3"),sQuery(id+"F0.wireOp",EDGE,"E6.31.4"),sQuery(id+"F0.wireOp",EDGE,"E6.32.1"),sQuery(id+"F0.wireOp",EDGE,"E6.32.2"),sQuery(id+"F0.wireOp",EDGE,"E6.32.3"),sQuery(id+"F0.wireOp",EDGE,"E6.32.4"),sQuery(id+"F0.wireOp",EDGE,"E6.33.1"),sQuery(id+"F0.wireOp",EDGE,"E6.33.2"),sQuery(id+"F0.wireOp",EDGE,"E6.33.3"),sQuery(id+"F0.wireOp",EDGE,"E6.33.4"),sQuery(id+"F0.wireOp",EDGE,"E6.34.1"),sQuery(id+"F0.wireOp",EDGE,"E6.34.2"),sQuery(id+"F0.wireOp",EDGE,"E6.34.3"),sQuery(id+"F0.wireOp",EDGE,"E6.34.4"),sQuery(id+"F0.wireOp",EDGE,"E6.35.1"),sQuery(id+"F0.wireOp",EDGE,"E6.35.2"),sQuery(id+"F0.wireOp",EDGE,"E6.35.3"),sQuery(id+"F0.wireOp",EDGE,"E6.35.4"),sQuery(id+"F0.wireOp",EDGE,"E6.36.1"),sQuery(id+"F0.wireOp",EDGE,"E6.36.2"),sQuery(id+"F0.wireOp",EDGE,"E6.36.3"),sQuery(id+"F0.wireOp",EDGE,"E6.36.4"),sQuery(id+"F0.wireOp",EDGE,"E6.37.1"),sQuery(id+"F0.wireOp",EDGE,"E6.37.2"),sQuery(id+"F0.wireOp",EDGE,"E6.37.3"),sQuery(id+"F0.wireOp",EDGE,"E6.37.4"),sQuery(id+"F0.wireOp",EDGE,"E6.38.1"),sQuery(id+"F0.wireOp",EDGE,"E6.38.2"),sQuery(id+"F0.wireOp",EDGE,"E6.38.3"),sQuery(id+"F0.wireOp",EDGE,"E6.38.4"),sQuery(id+"F0.wireOp",EDGE,"E6.39.1"),sQuery(id+"F0.wireOp",EDGE,"E6.39.2"),sQuery(id+"F0.wireOp",EDGE,"E6.39.3"),sQuery(id+"F0.wireOp",EDGE,"E6.39.4"),sQuery(id+"F0.wireOp",EDGE,"E6.40.1"),sQuery(id+"F0.wireOp",EDGE,"E6.40.2"),sQuery(id+"F0.wireOp",EDGE,"E6.40.3"),sQuery(id+"F0.wireOp",EDGE,"E6.40.4"),sQuery(id+"F0.wireOp",EDGE,"E6.41.1"),sQuery(id+"F0.wireOp",EDGE,"E6.41.2"),sQuery(id+"F0.wireOp",EDGE,"E6.41.3"),sQuery(id+"F0.wireOp",EDGE,"E6.41.4"),sQuery(id+"F0.wireOp",EDGE,"E6.42.1"),sQuery(id+"F0.wireOp",EDGE,"E6.42.2"),sQuery(id+"F0.wireOp",EDGE,"E6.42.3"),sQuery(id+"F0.wireOp",EDGE,"E6.42.4"),sQuery(id+"F0.wireOp",EDGE,"E6.43.1"),sQuery(id+"F0.wireOp",EDGE,"E6.43.2"),sQuery(id+"F0.wireOp",EDGE,"E6.43.3"),sQuery(id+"F0.wireOp",EDGE,"E6.43.4"),sQuery(id+"F0.wireOp",EDGE,"E7"),sQuery(id+"F0.wireOp",EDGE,"E8.1.0"),sQuery(id+"F0.wireOp",EDGE,"E8.2.0"),sQuery(id+"F0.wireOp",EDGE,"E8.3.0"),sQuery(id+"F0.wireOp",EDGE,"E8.4.0"),sQuery(id+"F0.wireOp",EDGE,"E8.5.0"),sQuery(id+"F0.wireOp",EDGE,"E8.6.0"),sQuery(id+"F0.wireOp",EDGE,"E8.7.0"),sQuery(id+"F0.wireOp",EDGE,"E8.8.0"),sQuery(id+"F0.wireOp",EDGE,"E8.9.0"),sQuery(id+"F0.wireOp",EDGE,"E8.10.0"),sQuery(id+"F0.wireOp",EDGE,"E8.11.0"),sQuery(id+"F0.wireOp",EDGE,"E8.12.0"),sQuery(id+"F0.wireOp",EDGE,"E8.13.0"),sQuery(id+"F0.wireOp",EDGE,"E8.14.0"),sQuery(id+"F0.wireOp",EDGE,"E8.15.0"),sQuery(id+"F0.wireOp",EDGE,"E8.16.0"),sQuery(id+"F0.wireOp",EDGE,"E8.17.0"),sQuery(id+"F0.wireOp",EDGE,"E8.18.0"),sQuery(id+"F0.wireOp",EDGE,"E8.19.0"),sQuery(id+"F0.wireOp",EDGE,"E8.20.0"),sQuery(id+"F0.wireOp",EDGE,"E8.21.0"),sQuery(id+"F0.wireOp",EDGE,"E8.22.0"),sQuery(id+"F0.wireOp",EDGE,"E8.23.0"),sQuery(id+"F0.wireOp",EDGE,"E8.24.0"),sQuery(id+"F0.wireOp",EDGE,"E8.25.0"),sQuery(id+"F0.wireOp",EDGE,"E8.26.0"),sQuery(id+"F0.wireOp",EDGE,"E8.27.0"),sQuery(id+"F0.wireOp",EDGE,"E8.28.0"),sQuery(id+"F0.wireOp",EDGE,"E8.29.0"),sQuery(id+"F0.wireOp",EDGE,"E8.30.0"),sQuery(id+"F0.wireOp",EDGE,"E8.31.0"),sQuery(id+"F0.wireOp",EDGE,"E8.32.0"),sQuery(id+"F0.wireOp",EDGE,"E8.33.0"),sQuery(id+"F0.wireOp",EDGE,"E8.34.0"),sQuery(id+"F0.wireOp",EDGE,"E8.35.0"),sQuery(id+"F0.wireOp",EDGE,"E8.36.0"),sQuery(id+"F0.wireOp",EDGE,"E8.37.0"),sQuery(id+"F0.wireOp",EDGE,"E8.38.0"),sQuery(id+"F0.wireOp",EDGE,"E8.39.0"),sQuery(id+"F0.wireOp",EDGE,"E8.40.0"),sQuery(id+"F0.wireOp",EDGE,"E8.41.0"),sQuery(id+"F0.wireOp",EDGE,"E8.42.0"),sQuery(id+"F0.wireOp",EDGE,"E8.43.0")])],"isStart":true})],"blendedInto":[makeQuery(id+"F1.opExtrude","CAP_FACE",FACE,{"disambiguationData":[OSD([sQuery(id+"F0.wireOp",EDGE,"E0"),sQuery(id+"F0.wireOp",EDGE,"E1"),sQuery(id+"F0.wireOp",EDGE,"E2"),sQuery(id+"F0.wireOp",EDGE,"E4"),sQuery(id+"F0.wireOp",EDGE,"E5"),sQuery(id+"F0.wireOp",EDGE,"E6.1.1"),sQuery(id+"F0.wireOp",EDGE,"E6.1.2"),sQuery(id+"F0.wireOp",EDGE,"E6.1.3"),sQuery(id+"F0.wireOp",EDGE,"E6.1.4"),sQuery(id+"F0.wireOp",EDGE,"E6.2.1"),sQuery(id+"F0.wireOp",EDGE,"E6.2.2"),sQuery(id+"F0.wireOp",EDGE,"E6.2.3"),sQuery(id+"F0.wireOp",EDGE,"E6.2.4"),sQuery(id+"F0.wireOp",EDGE,"E6.3.1"),sQuery(id+"F0.wireOp",EDGE,"E6.3.2"),sQuery(id+"F0.wireOp",EDGE,"E6.3.3"),sQuery(id+"F0.wireOp",EDGE,"E6.3.4"),sQuery(id+"F0.wireOp",EDGE,"E6.4.1"),sQuery(id+"F0.wireOp",EDGE,"E6.4.2"),sQuery(id+"F0.wireOp",EDGE,"E6.4.3"),sQuery(id+"F0.wireOp",EDGE,"E6.4.4"),sQuery(id+"F0.wireOp",EDGE,"E6.5.1"),sQuery(id+"F0.wireOp",EDGE,"E6.5.2"),sQuery(id+"F0.wireOp",EDGE,"E6.5.3"),sQuery(id+"F0.wireOp",EDGE,"E6.5.4"),sQuery(id+"F0.wireOp",EDGE,"E6.6.1"),sQuery(id+"F0.wireOp",EDGE,"E6.6.2"),sQuery(id+"F0.wireOp",EDGE,"E6.6.3"),sQuery(id+"F0.wireOp",EDGE,"E6.6.4"),sQuery(id+"F0.wireOp",EDGE,"E6.7.1"),sQuery(id+"F0.wireOp",EDGE,"E6.7.2"),sQuery(id+"F0.wireOp",EDGE,"E6.7.3"),sQuery(id+"F0.wireOp",EDGE,"E6.7.4"),sQuery(id+"F0.wireOp",EDGE,"E6.8.1"),sQuery(id+"F0.wireOp",EDGE,"E6.8.2"),sQuery(id+"F0.wireOp",EDGE,"E6.8.3"),sQuery(id+"F0.wireOp",EDGE,"E6.8.4"),sQuery(id+"F0.wireOp",EDGE,"E6.9.1"),sQuery(id+"F0.wireOp",EDGE,"E6.9.2"),sQuery(id+"F0.wireOp",EDGE,"E6.9.3"),sQuery(id+"F0.wireOp",EDGE,"E6.9.4"),sQuery(id+"F0.wireOp",EDGE,"E6.10.1"),sQuery(id+"F0.wireOp",EDGE,"E6.10.2"),sQuery(id+"F0.wireOp",EDGE,"E6.10.3"),sQuery(id+"F0.wireOp",EDGE,"E6.10.4"),sQuery(id+"F0.wireOp",EDGE,"E6.11.1"),sQuery(id+"F0.wireOp",EDGE,"E6.11.2"),sQuery(id+"F0.wireOp",EDGE,"E6.11.3"),sQuery(id+"F0.wireOp",EDGE,"E6.11.4"),sQuery(id+"F0.wireOp",EDGE,"E6.12.1"),sQuery(id+"F0.wireOp",EDGE,"E6.12.2"),sQuery(id+"F0.wireOp",EDGE,"E6.12.3"),sQuery(id+"F0.wireOp",EDGE,"E6.12.4"),sQuery(id+"F0.wireOp",EDGE,"E6.13.1"),sQuery(id+"F0.wireOp",EDGE,"E6.13.2"),sQuery(id+"F0.wireOp",EDGE,"E6.13.3"),sQuery(id+"F0.wireOp",EDGE,"E6.13.4"),sQuery(id+"F0.wireOp",EDGE,"E6.14.1"),sQuery(id+"F0.wireOp",EDGE,"E6.14.2"),sQuery(id+"F0.wireOp",EDGE,"E6.14.3"),sQuery(id+"F0.wireOp",EDGE,"E6.14.4"),sQuery(id+"F0.wireOp",EDGE,"E6.15.1"),sQuery(id+"F0.wireOp",EDGE,"E6.15.2"),sQuery(id+"F0.wireOp",EDGE,"E6.15.3"),sQuery(id+"F0.wireOp",EDGE,"E6.15.4"),sQuery(id+"F0.wireOp",EDGE,"E6.16.1"),sQuery(id+"F0.wireOp",EDGE,"E6.16.2"),sQuery(id+"F0.wireOp",EDGE,"E6.16.3"),sQuery(id+"F0.wireOp",EDGE,"E6.16.4"),sQuery(id+"F0.wireOp",EDGE,"E6.17.1"),sQuery(id+"F0.wireOp",EDGE,"E6.17.2"),sQuery(id+"F0.wireOp",EDGE,"E6.17.3"),sQuery(id+"F0.wireOp",EDGE,"E6.17.4"),sQuery(id+"F0.wireOp",EDGE,"E6.18.1"),sQuery(id+"F0.wireOp",EDGE,"E6.18.2"),sQuery(id+"F0.wireOp",EDGE,"E6.18.3"),sQuery(id+"F0.wireOp",EDGE,"E6.18.4"),sQuery(id+"F0.wireOp",EDGE,"E6.19.1"),sQuery(id+"F0.wireOp",EDGE,"E6.19.2"),sQuery(id+"F0.wireOp",EDGE,"E6.19.3"),sQuery(id+"F0.wireOp",EDGE,"E6.19.4"),sQuery(id+"F0.wireOp",EDGE,"E6.20.1"),sQuery(id+"F0.wireOp",EDGE,"E6.20.2"),sQuery(id+"F0.wireOp",EDGE,"E6.20.3"),sQuery(id+"F0.wireOp",EDGE,"E6.20.4"),sQuery(id+"F0.wireOp",EDGE,"E6.21.1"),sQuery(id+"F0.wireOp",EDGE,"E6.21.2"),sQuery(id+"F0.wireOp",EDGE,"E6.21.3"),sQuery(id+"F0.wireOp",EDGE,"E6.21.4"),sQuery(id+"F0.wireOp",EDGE,"E6.22.1"),sQuery(id+"F0.wireOp",EDGE,"E6.22.2"),sQuery(id+"F0.wireOp",EDGE,"E6.22.3"),sQuery(id+"F0.wireOp",EDGE,"E6.22.4"),sQuery(id+"F0.wireOp",EDGE,"E6.23.1"),sQuery(id+"F0.wireOp",EDGE,"E6.23.2"),sQuery(id+"F0.wireOp",EDGE,"E6.23.3"),sQuery(id+"F0.wireOp",EDGE,"E6.23.4"),subQ1,sQuery(id+"F0.wireOp",EDGE,"E6.24.2"),subQ0,sQuery(id+"F0.wireOp",EDGE,"E6.24.4"),sQuery(id+"F0.wireOp",EDGE,"E6.25.1"),sQuery(id+"F0.wireOp",EDGE,"E6.25.2"),sQuery(id+"F0.wireOp",EDGE,"E6.25.3"),sQuery(id+"F0.wireOp",EDGE,"E6.25.4"),sQuery(id+"F0.wireOp",EDGE,"E6.26.1"),sQuery(id+"F0.wireOp",EDGE,"E6.26.2"),sQuery(id+"F0.wireOp",EDGE,"E6.26.3"),sQuery(id+"F0.wireOp",EDGE,"E6.26.4"),sQuery(id+"F0.wireOp",EDGE,"E6.27.1"),sQuery(id+"F0.wireOp",EDGE,"E6.27.2"),sQuery(id+"F0.wireOp",EDGE,"E6.27.3"),sQuery(id+"F0.wireOp",EDGE,"E6.27.4"),sQuery(id+"F0.wireOp",EDGE,"E6.28.1"),sQuery(id+"F0.wireOp",EDGE,"E6.28.2"),sQuery(id+"F0.wireOp",EDGE,"E6.28.3"),sQuery(id+"F0.wireOp",EDGE,"E6.28.4"),sQuery(id+"F0.wireOp",EDGE,"E6.29.1"),sQuery(id+"F0.wireOp",EDGE,"E6.29.2"),sQuery(id+"F0.wireOp",EDGE,"E6.29.3"),sQuery(id+"F0.wireOp",EDGE,"E6.29.4"),sQuery(id+"F0.wireOp",EDGE,"E6.30.1"),sQuery(id+"F0.wireOp",EDGE,"E6.30.2"),sQuery(id+"F0.wireOp",EDGE,"E6.30.3"),sQuery(id+"F0.wireOp",EDGE,"E6.30.4"),sQuery(id+"F0.wireOp",EDGE,"E6.31.1"),sQuery(id+"F0.wireOp",EDGE,"E6.31.2"),sQuery(id+"F0.wireOp",EDGE,"E6.31.3"),sQuery(id+"F0.wireOp",EDGE,"E6.31.4"),sQuery(id+"F0.wireOp",EDGE,"E6.32.1"),sQuery(id+"F0.wireOp",EDGE,"E6.32.2"),sQuery(id+"F0.wireOp",EDGE,"E6.32.3"),sQuery(id+"F0.wireOp",EDGE,"E6.32.4"),sQuery(id+"F0.wireOp",EDGE,"E6.33.1"),sQuery(id+"F0.wireOp",EDGE,"E6.33.2"),sQuery(id+"F0.wireOp",EDGE,"E6.33.3"),sQuery(id+"F0.wireOp",EDGE,"E6.33.4"),sQuery(id+"F0.wireOp",EDGE,"E6.34.1"),sQuery(id+"F0.wireOp",EDGE,"E6.34.2"),sQuery(id+"F0.wireOp",EDGE,"E6.34.3"),sQuery(id+"F0.wireOp",EDGE,"E6.34.4"),sQuery(id+"F0.wireOp",EDGE,"E6.35.1"),sQuery(id+"F0.wireOp",EDGE,"E6.35.2"),sQuery(id+"F0.wireOp",EDGE,"E6.35.3"),sQuery(id+"F0.wireOp",EDGE,"E6.35.4"),sQuery(id+"F0.wireOp",EDGE,"E6.36.1"),sQuery(id+"F0.wireOp",EDGE,"E6.36.2"),sQuery(id+"F0.wireOp",EDGE,"E6.36.3"),sQuery(id+"F0.wireOp",EDGE,"E6.36.4"),sQuery(id+"F0.wireOp",EDGE,"E6.37.1"),sQuery(id+"F0.wireOp",EDGE,"E6.37.2"),sQuery(id+"F0.wireOp",EDGE,"E6.37.3"),sQuery(id+"F0.wireOp",EDGE,"E6.37.4"),sQuery(id+"F0.wireOp",EDGE,"E6.38.1"),sQuery(id+"F0.wireOp",EDGE,"E6.38.2"),sQuery(id+"F0.wireOp",EDGE,"E6.38.3"),sQuery(id+"F0.wireOp",EDGE,"E6.38.4"),sQuery(id+"F0.wireOp",EDGE,"E6.39.1"),sQuery(id+"F0.wireOp",EDGE,"E6.39.2"),sQuery(id+"F0.wireOp",EDGE,"E6.39.3"),sQuery(id+"F0.wireOp",EDGE,"E6.39.4"),sQuery(id+"F0.wireOp",EDGE,"E6.40.1"),sQuery(id+"F0.wireOp",EDGE,"E6.40.2"),sQuery(id+"F0.wireOp",EDGE,"E6.40.3"),sQuery(id+"F0.wireOp",EDGE,"E6.40.4"),sQuery(id+"F0.wireOp",EDGE,"E6.41.1"),sQuery(id+"F0.wireOp",EDGE,"E6.41.2"),sQuery(id+"F0.wireOp",EDGE,"E6.41.3"),sQuery(id+"F0.wireOp",EDGE,"E6.41.4"),sQuery(id+"F0.wireOp",EDGE,"E6.42.1"),sQuery(id+"F0.wireOp",EDGE,"E6.42.2"),sQuery(id+"F0.wireOp",EDGE,"E6.42.3"),sQuery(id+"F0.wireOp",EDGE,"E6.42.4"),sQuery(id+"F0.wireOp",EDGE,"E6.43.1"),sQuery(id+"F0.wireOp",EDGE,"E6.43.2"),sQuery(id+"F0.wireOp",EDGE,"E6.43.3"),sQuery(id+"F0.wireOp",EDGE,"E6.43.4"),sQuery(id+"F0.wireOp",EDGE,"E7"),sQuery(id+"F0.wireOp",EDGE,"E8.1.0"),sQuery(id+"F0.wireOp",EDGE,"E8.2.0"),sQuery(id+"F0.wireOp",EDGE,"E8.3.0"),sQuery(id+"F0.wireOp",EDGE,"E8.4.0"),sQuery(id+"F0.wireOp",EDGE,"E8.5.0"),sQuery(id+"F0.wireOp",EDGE,"E8.6.0"),sQuery(id+"F0.wireOp",EDGE,"E8.7.0"),sQuery(id+"F0.wireOp",EDGE,"E8.8.0"),sQuery(id+"F0.wireOp",EDGE,"E8.9.0"),sQuery(id+"F0.wireOp",EDGE,"E8.10.0"),sQuery(id+"F0.wireOp",EDGE,"E8.11.0"),sQuery(id+"F0.wireOp",EDGE,"E8.12.0"),sQuery(id+"F0.wireOp",EDGE,"E8.13.0"),sQuery(id+"F0.wireOp",EDGE,"E8.14.0"),sQuery(id+"F0.wireOp",EDGE,"E8.15.0"),sQuery(id+"F0.wireOp",EDGE,"E8.16.0"),sQuery(id+"F0.wireOp",EDGE,"E8.17.0"),sQuery(id+"F0.wireOp",EDGE,"E8.18.0"),sQuery(id+"F0.wireOp",EDGE,"E8.19.0"),sQuery(id+"F0.wireOp",EDGE,"E8.20.0"),sQuery(id+"F0.wireOp",EDGE,"E8.21.0"),sQuery(id+"F0.wireOp",EDGE,"E8.22.0"),sQuery(id+"F0.wireOp",EDGE,"E8.23.0"),sQuery(id+"F0.wireOp",EDGE,"E8.24.0"),sQuery(id+"F0.wireOp",EDGE,"E8.25.0"),sQuery(id+"F0.wireOp",EDGE,"E8.26.0"),sQuery(id+"F0.wireOp",EDGE,"E8.27.0"),sQuery(id+"F0.wireOp",EDGE,"E8.28.0"),sQuery(id+"F0.wireOp",EDGE,"E8.29.0"),sQuery(id+"F0.wireOp",EDGE,"E8.30.0"),sQuery(id+"F0.wireOp",EDGE,"E8.31.0"),sQuery(id+"F0.wireOp",EDGE,"E8.32.0"),sQuery(id+"F0.wireOp",EDGE,"E8.33.0"),sQuery(id+"F0.wireOp",EDGE,"E8.34.0"),sQuery(id+"F0.wireOp",EDGE,"E8.35.0"),sQuery(id+"F0.wireOp",EDGE,"E8.36.0"),sQuery(id+"F0.wireOp",EDGE,"E8.37.0"),sQuery(id+"F0.wireOp",EDGE,"E8.38.0"),sQuery(id+"F0.wireOp",EDGE,"E8.39.0"),sQuery(id+"F0.wireOp",EDGE,"E8.40.0"),sQuery(id+"F0.wireOp",EDGE,"E8.41.0"),sQuery(id+"F0.wireOp",EDGE,"E8.42.0"),sQuery(id+"F0.wireOp",EDGE,"E8.43.0")])],"isStart":true})]});}
            var Q34;
            {var subQ0=sQuery(id+"F0.wireOp",EDGE,"E6.26.3");var subQ1=sQuery(id+"F0.wireOp",EDGE,"E6.26.1");Q34=makeQuery(id+"F2.opFillet","BLEND_EDGE",EDGE,{"blendedFrom":[makeQuery(id+"F1.opExtrude","SWEPT_EDGE",EDGE,{"disambiguationData":[OSD([sQuery(id+"F0.wireOp",EDGE,"E6.26.0"),subQ1,subQ0])]}),makeQuery(id+"F1.opExtrude","CAP_FACE",FACE,{"disambiguationData":[OSD([sQuery(id+"F0.wireOp",EDGE,"E0"),sQuery(id+"F0.wireOp",EDGE,"E1"),sQuery(id+"F0.wireOp",EDGE,"E2"),sQuery(id+"F0.wireOp",EDGE,"E4"),sQuery(id+"F0.wireOp",EDGE,"E5"),sQuery(id+"F0.wireOp",EDGE,"E6.1.1"),sQuery(id+"F0.wireOp",EDGE,"E6.1.2"),sQuery(id+"F0.wireOp",EDGE,"E6.1.3"),sQuery(id+"F0.wireOp",EDGE,"E6.1.4"),sQuery(id+"F0.wireOp",EDGE,"E6.2.1"),sQuery(id+"F0.wireOp",EDGE,"E6.2.2"),sQuery(id+"F0.wireOp",EDGE,"E6.2.3"),sQuery(id+"F0.wireOp",EDGE,"E6.2.4"),sQuery(id+"F0.wireOp",EDGE,"E6.3.1"),sQuery(id+"F0.wireOp",EDGE,"E6.3.2"),sQuery(id+"F0.wireOp",EDGE,"E6.3.3"),sQuery(id+"F0.wireOp",EDGE,"E6.3.4"),sQuery(id+"F0.wireOp",EDGE,"E6.4.1"),sQuery(id+"F0.wireOp",EDGE,"E6.4.2"),sQuery(id+"F0.wireOp",EDGE,"E6.4.3"),sQuery(id+"F0.wireOp",EDGE,"E6.4.4"),sQuery(id+"F0.wireOp",EDGE,"E6.5.1"),sQuery(id+"F0.wireOp",EDGE,"E6.5.2"),sQuery(id+"F0.wireOp",EDGE,"E6.5.3"),sQuery(id+"F0.wireOp",EDGE,"E6.5.4"),sQuery(id+"F0.wireOp",EDGE,"E6.6.1"),sQuery(id+"F0.wireOp",EDGE,"E6.6.2"),sQuery(id+"F0.wireOp",EDGE,"E6.6.3"),sQuery(id+"F0.wireOp",EDGE,"E6.6.4"),sQuery(id+"F0.wireOp",EDGE,"E6.7.1"),sQuery(id+"F0.wireOp",EDGE,"E6.7.2"),sQuery(id+"F0.wireOp",EDGE,"E6.7.3"),sQuery(id+"F0.wireOp",EDGE,"E6.7.4"),sQuery(id+"F0.wireOp",EDGE,"E6.8.1"),sQuery(id+"F0.wireOp",EDGE,"E6.8.2"),sQuery(id+"F0.wireOp",EDGE,"E6.8.3"),sQuery(id+"F0.wireOp",EDGE,"E6.8.4"),sQuery(id+"F0.wireOp",EDGE,"E6.9.1"),sQuery(id+"F0.wireOp",EDGE,"E6.9.2"),sQuery(id+"F0.wireOp",EDGE,"E6.9.3"),sQuery(id+"F0.wireOp",EDGE,"E6.9.4"),sQuery(id+"F0.wireOp",EDGE,"E6.10.1"),sQuery(id+"F0.wireOp",EDGE,"E6.10.2"),sQuery(id+"F0.wireOp",EDGE,"E6.10.3"),sQuery(id+"F0.wireOp",EDGE,"E6.10.4"),sQuery(id+"F0.wireOp",EDGE,"E6.11.1"),sQuery(id+"F0.wireOp",EDGE,"E6.11.2"),sQuery(id+"F0.wireOp",EDGE,"E6.11.3"),sQuery(id+"F0.wireOp",EDGE,"E6.11.4"),sQuery(id+"F0.wireOp",EDGE,"E6.12.1"),sQuery(id+"F0.wireOp",EDGE,"E6.12.2"),sQuery(id+"F0.wireOp",EDGE,"E6.12.3"),sQuery(id+"F0.wireOp",EDGE,"E6.12.4"),sQuery(id+"F0.wireOp",EDGE,"E6.13.1"),sQuery(id+"F0.wireOp",EDGE,"E6.13.2"),sQuery(id+"F0.wireOp",EDGE,"E6.13.3"),sQuery(id+"F0.wireOp",EDGE,"E6.13.4"),sQuery(id+"F0.wireOp",EDGE,"E6.14.1"),sQuery(id+"F0.wireOp",EDGE,"E6.14.2"),sQuery(id+"F0.wireOp",EDGE,"E6.14.3"),sQuery(id+"F0.wireOp",EDGE,"E6.14.4"),sQuery(id+"F0.wireOp",EDGE,"E6.15.1"),sQuery(id+"F0.wireOp",EDGE,"E6.15.2"),sQuery(id+"F0.wireOp",EDGE,"E6.15.3"),sQuery(id+"F0.wireOp",EDGE,"E6.15.4"),sQuery(id+"F0.wireOp",EDGE,"E6.16.1"),sQuery(id+"F0.wireOp",EDGE,"E6.16.2"),sQuery(id+"F0.wireOp",EDGE,"E6.16.3"),sQuery(id+"F0.wireOp",EDGE,"E6.16.4"),sQuery(id+"F0.wireOp",EDGE,"E6.17.1"),sQuery(id+"F0.wireOp",EDGE,"E6.17.2"),sQuery(id+"F0.wireOp",EDGE,"E6.17.3"),sQuery(id+"F0.wireOp",EDGE,"E6.17.4"),sQuery(id+"F0.wireOp",EDGE,"E6.18.1"),sQuery(id+"F0.wireOp",EDGE,"E6.18.2"),sQuery(id+"F0.wireOp",EDGE,"E6.18.3"),sQuery(id+"F0.wireOp",EDGE,"E6.18.4"),sQuery(id+"F0.wireOp",EDGE,"E6.19.1"),sQuery(id+"F0.wireOp",EDGE,"E6.19.2"),sQuery(id+"F0.wireOp",EDGE,"E6.19.3"),sQuery(id+"F0.wireOp",EDGE,"E6.19.4"),sQuery(id+"F0.wireOp",EDGE,"E6.20.1"),sQuery(id+"F0.wireOp",EDGE,"E6.20.2"),sQuery(id+"F0.wireOp",EDGE,"E6.20.3"),sQuery(id+"F0.wireOp",EDGE,"E6.20.4"),sQuery(id+"F0.wireOp",EDGE,"E6.21.1"),sQuery(id+"F0.wireOp",EDGE,"E6.21.2"),sQuery(id+"F0.wireOp",EDGE,"E6.21.3"),sQuery(id+"F0.wireOp",EDGE,"E6.21.4"),sQuery(id+"F0.wireOp",EDGE,"E6.22.1"),sQuery(id+"F0.wireOp",EDGE,"E6.22.2"),sQuery(id+"F0.wireOp",EDGE,"E6.22.3"),sQuery(id+"F0.wireOp",EDGE,"E6.22.4"),sQuery(id+"F0.wireOp",EDGE,"E6.23.1"),sQuery(id+"F0.wireOp",EDGE,"E6.23.2"),sQuery(id+"F0.wireOp",EDGE,"E6.23.3"),sQuery(id+"F0.wireOp",EDGE,"E6.23.4"),sQuery(id+"F0.wireOp",EDGE,"E6.24.1"),sQuery(id+"F0.wireOp",EDGE,"E6.24.2"),sQuery(id+"F0.wireOp",EDGE,"E6.24.3"),sQuery(id+"F0.wireOp",EDGE,"E6.24.4"),sQuery(id+"F0.wireOp",EDGE,"E6.25.1"),sQuery(id+"F0.wireOp",EDGE,"E6.25.2"),sQuery(id+"F0.wireOp",EDGE,"E6.25.3"),sQuery(id+"F0.wireOp",EDGE,"E6.25.4"),subQ1,sQuery(id+"F0.wireOp",EDGE,"E6.26.2"),subQ0,sQuery(id+"F0.wireOp",EDGE,"E6.26.4"),sQuery(id+"F0.wireOp",EDGE,"E6.27.1"),sQuery(id+"F0.wireOp",EDGE,"E6.27.2"),sQuery(id+"F0.wireOp",EDGE,"E6.27.3"),sQuery(id+"F0.wireOp",EDGE,"E6.27.4"),sQuery(id+"F0.wireOp",EDGE,"E6.28.1"),sQuery(id+"F0.wireOp",EDGE,"E6.28.2"),sQuery(id+"F0.wireOp",EDGE,"E6.28.3"),sQuery(id+"F0.wireOp",EDGE,"E6.28.4"),sQuery(id+"F0.wireOp",EDGE,"E6.29.1"),sQuery(id+"F0.wireOp",EDGE,"E6.29.2"),sQuery(id+"F0.wireOp",EDGE,"E6.29.3"),sQuery(id+"F0.wireOp",EDGE,"E6.29.4"),sQuery(id+"F0.wireOp",EDGE,"E6.30.1"),sQuery(id+"F0.wireOp",EDGE,"E6.30.2"),sQuery(id+"F0.wireOp",EDGE,"E6.30.3"),sQuery(id+"F0.wireOp",EDGE,"E6.30.4"),sQuery(id+"F0.wireOp",EDGE,"E6.31.1"),sQuery(id+"F0.wireOp",EDGE,"E6.31.2"),sQuery(id+"F0.wireOp",EDGE,"E6.31.3"),sQuery(id+"F0.wireOp",EDGE,"E6.31.4"),sQuery(id+"F0.wireOp",EDGE,"E6.32.1"),sQuery(id+"F0.wireOp",EDGE,"E6.32.2"),sQuery(id+"F0.wireOp",EDGE,"E6.32.3"),sQuery(id+"F0.wireOp",EDGE,"E6.32.4"),sQuery(id+"F0.wireOp",EDGE,"E6.33.1"),sQuery(id+"F0.wireOp",EDGE,"E6.33.2"),sQuery(id+"F0.wireOp",EDGE,"E6.33.3"),sQuery(id+"F0.wireOp",EDGE,"E6.33.4"),sQuery(id+"F0.wireOp",EDGE,"E6.34.1"),sQuery(id+"F0.wireOp",EDGE,"E6.34.2"),sQuery(id+"F0.wireOp",EDGE,"E6.34.3"),sQuery(id+"F0.wireOp",EDGE,"E6.34.4"),sQuery(id+"F0.wireOp",EDGE,"E6.35.1"),sQuery(id+"F0.wireOp",EDGE,"E6.35.2"),sQuery(id+"F0.wireOp",EDGE,"E6.35.3"),sQuery(id+"F0.wireOp",EDGE,"E6.35.4"),sQuery(id+"F0.wireOp",EDGE,"E6.36.1"),sQuery(id+"F0.wireOp",EDGE,"E6.36.2"),sQuery(id+"F0.wireOp",EDGE,"E6.36.3"),sQuery(id+"F0.wireOp",EDGE,"E6.36.4"),sQuery(id+"F0.wireOp",EDGE,"E6.37.1"),sQuery(id+"F0.wireOp",EDGE,"E6.37.2"),sQuery(id+"F0.wireOp",EDGE,"E6.37.3"),sQuery(id+"F0.wireOp",EDGE,"E6.37.4"),sQuery(id+"F0.wireOp",EDGE,"E6.38.1"),sQuery(id+"F0.wireOp",EDGE,"E6.38.2"),sQuery(id+"F0.wireOp",EDGE,"E6.38.3"),sQuery(id+"F0.wireOp",EDGE,"E6.38.4"),sQuery(id+"F0.wireOp",EDGE,"E6.39.1"),sQuery(id+"F0.wireOp",EDGE,"E6.39.2"),sQuery(id+"F0.wireOp",EDGE,"E6.39.3"),sQuery(id+"F0.wireOp",EDGE,"E6.39.4"),sQuery(id+"F0.wireOp",EDGE,"E6.40.1"),sQuery(id+"F0.wireOp",EDGE,"E6.40.2"),sQuery(id+"F0.wireOp",EDGE,"E6.40.3"),sQuery(id+"F0.wireOp",EDGE,"E6.40.4"),sQuery(id+"F0.wireOp",EDGE,"E6.41.1"),sQuery(id+"F0.wireOp",EDGE,"E6.41.2"),sQuery(id+"F0.wireOp",EDGE,"E6.41.3"),sQuery(id+"F0.wireOp",EDGE,"E6.41.4"),sQuery(id+"F0.wireOp",EDGE,"E6.42.1"),sQuery(id+"F0.wireOp",EDGE,"E6.42.2"),sQuery(id+"F0.wireOp",EDGE,"E6.42.3"),sQuery(id+"F0.wireOp",EDGE,"E6.42.4"),sQuery(id+"F0.wireOp",EDGE,"E6.43.1"),sQuery(id+"F0.wireOp",EDGE,"E6.43.2"),sQuery(id+"F0.wireOp",EDGE,"E6.43.3"),sQuery(id+"F0.wireOp",EDGE,"E6.43.4"),sQuery(id+"F0.wireOp",EDGE,"E7"),sQuery(id+"F0.wireOp",EDGE,"E8.1.0"),sQuery(id+"F0.wireOp",EDGE,"E8.2.0"),sQuery(id+"F0.wireOp",EDGE,"E8.3.0"),sQuery(id+"F0.wireOp",EDGE,"E8.4.0"),sQuery(id+"F0.wireOp",EDGE,"E8.5.0"),sQuery(id+"F0.wireOp",EDGE,"E8.6.0"),sQuery(id+"F0.wireOp",EDGE,"E8.7.0"),sQuery(id+"F0.wireOp",EDGE,"E8.8.0"),sQuery(id+"F0.wireOp",EDGE,"E8.9.0"),sQuery(id+"F0.wireOp",EDGE,"E8.10.0"),sQuery(id+"F0.wireOp",EDGE,"E8.11.0"),sQuery(id+"F0.wireOp",EDGE,"E8.12.0"),sQuery(id+"F0.wireOp",EDGE,"E8.13.0"),sQuery(id+"F0.wireOp",EDGE,"E8.14.0"),sQuery(id+"F0.wireOp",EDGE,"E8.15.0"),sQuery(id+"F0.wireOp",EDGE,"E8.16.0"),sQuery(id+"F0.wireOp",EDGE,"E8.17.0"),sQuery(id+"F0.wireOp",EDGE,"E8.18.0"),sQuery(id+"F0.wireOp",EDGE,"E8.19.0"),sQuery(id+"F0.wireOp",EDGE,"E8.20.0"),sQuery(id+"F0.wireOp",EDGE,"E8.21.0"),sQuery(id+"F0.wireOp",EDGE,"E8.22.0"),sQuery(id+"F0.wireOp",EDGE,"E8.23.0"),sQuery(id+"F0.wireOp",EDGE,"E8.24.0"),sQuery(id+"F0.wireOp",EDGE,"E8.25.0"),sQuery(id+"F0.wireOp",EDGE,"E8.26.0"),sQuery(id+"F0.wireOp",EDGE,"E8.27.0"),sQuery(id+"F0.wireOp",EDGE,"E8.28.0"),sQuery(id+"F0.wireOp",EDGE,"E8.29.0"),sQuery(id+"F0.wireOp",EDGE,"E8.30.0"),sQuery(id+"F0.wireOp",EDGE,"E8.31.0"),sQuery(id+"F0.wireOp",EDGE,"E8.32.0"),sQuery(id+"F0.wireOp",EDGE,"E8.33.0"),sQuery(id+"F0.wireOp",EDGE,"E8.34.0"),sQuery(id+"F0.wireOp",EDGE,"E8.35.0"),sQuery(id+"F0.wireOp",EDGE,"E8.36.0"),sQuery(id+"F0.wireOp",EDGE,"E8.37.0"),sQuery(id+"F0.wireOp",EDGE,"E8.38.0"),sQuery(id+"F0.wireOp",EDGE,"E8.39.0"),sQuery(id+"F0.wireOp",EDGE,"E8.40.0"),sQuery(id+"F0.wireOp",EDGE,"E8.41.0"),sQuery(id+"F0.wireOp",EDGE,"E8.42.0"),sQuery(id+"F0.wireOp",EDGE,"E8.43.0")])],"isStart":true})],"blendedInto":[makeQuery(id+"F1.opExtrude","CAP_FACE",FACE,{"disambiguationData":[OSD([sQuery(id+"F0.wireOp",EDGE,"E0"),sQuery(id+"F0.wireOp",EDGE,"E1"),sQuery(id+"F0.wireOp",EDGE,"E2"),sQuery(id+"F0.wireOp",EDGE,"E4"),sQuery(id+"F0.wireOp",EDGE,"E5"),sQuery(id+"F0.wireOp",EDGE,"E6.1.1"),sQuery(id+"F0.wireOp",EDGE,"E6.1.2"),sQuery(id+"F0.wireOp",EDGE,"E6.1.3"),sQuery(id+"F0.wireOp",EDGE,"E6.1.4"),sQuery(id+"F0.wireOp",EDGE,"E6.2.1"),sQuery(id+"F0.wireOp",EDGE,"E6.2.2"),sQuery(id+"F0.wireOp",EDGE,"E6.2.3"),sQuery(id+"F0.wireOp",EDGE,"E6.2.4"),sQuery(id+"F0.wireOp",EDGE,"E6.3.1"),sQuery(id+"F0.wireOp",EDGE,"E6.3.2"),sQuery(id+"F0.wireOp",EDGE,"E6.3.3"),sQuery(id+"F0.wireOp",EDGE,"E6.3.4"),sQuery(id+"F0.wireOp",EDGE,"E6.4.1"),sQuery(id+"F0.wireOp",EDGE,"E6.4.2"),sQuery(id+"F0.wireOp",EDGE,"E6.4.3"),sQuery(id+"F0.wireOp",EDGE,"E6.4.4"),sQuery(id+"F0.wireOp",EDGE,"E6.5.1"),sQuery(id+"F0.wireOp",EDGE,"E6.5.2"),sQuery(id+"F0.wireOp",EDGE,"E6.5.3"),sQuery(id+"F0.wireOp",EDGE,"E6.5.4"),sQuery(id+"F0.wireOp",EDGE,"E6.6.1"),sQuery(id+"F0.wireOp",EDGE,"E6.6.2"),sQuery(id+"F0.wireOp",EDGE,"E6.6.3"),sQuery(id+"F0.wireOp",EDGE,"E6.6.4"),sQuery(id+"F0.wireOp",EDGE,"E6.7.1"),sQuery(id+"F0.wireOp",EDGE,"E6.7.2"),sQuery(id+"F0.wireOp",EDGE,"E6.7.3"),sQuery(id+"F0.wireOp",EDGE,"E6.7.4"),sQuery(id+"F0.wireOp",EDGE,"E6.8.1"),sQuery(id+"F0.wireOp",EDGE,"E6.8.2"),sQuery(id+"F0.wireOp",EDGE,"E6.8.3"),sQuery(id+"F0.wireOp",EDGE,"E6.8.4"),sQuery(id+"F0.wireOp",EDGE,"E6.9.1"),sQuery(id+"F0.wireOp",EDGE,"E6.9.2"),sQuery(id+"F0.wireOp",EDGE,"E6.9.3"),sQuery(id+"F0.wireOp",EDGE,"E6.9.4"),sQuery(id+"F0.wireOp",EDGE,"E6.10.1"),sQuery(id+"F0.wireOp",EDGE,"E6.10.2"),sQuery(id+"F0.wireOp",EDGE,"E6.10.3"),sQuery(id+"F0.wireOp",EDGE,"E6.10.4"),sQuery(id+"F0.wireOp",EDGE,"E6.11.1"),sQuery(id+"F0.wireOp",EDGE,"E6.11.2"),sQuery(id+"F0.wireOp",EDGE,"E6.11.3"),sQuery(id+"F0.wireOp",EDGE,"E6.11.4"),sQuery(id+"F0.wireOp",EDGE,"E6.12.1"),sQuery(id+"F0.wireOp",EDGE,"E6.12.2"),sQuery(id+"F0.wireOp",EDGE,"E6.12.3"),sQuery(id+"F0.wireOp",EDGE,"E6.12.4"),sQuery(id+"F0.wireOp",EDGE,"E6.13.1"),sQuery(id+"F0.wireOp",EDGE,"E6.13.2"),sQuery(id+"F0.wireOp",EDGE,"E6.13.3"),sQuery(id+"F0.wireOp",EDGE,"E6.13.4"),sQuery(id+"F0.wireOp",EDGE,"E6.14.1"),sQuery(id+"F0.wireOp",EDGE,"E6.14.2"),sQuery(id+"F0.wireOp",EDGE,"E6.14.3"),sQuery(id+"F0.wireOp",EDGE,"E6.14.4"),sQuery(id+"F0.wireOp",EDGE,"E6.15.1"),sQuery(id+"F0.wireOp",EDGE,"E6.15.2"),sQuery(id+"F0.wireOp",EDGE,"E6.15.3"),sQuery(id+"F0.wireOp",EDGE,"E6.15.4"),sQuery(id+"F0.wireOp",EDGE,"E6.16.1"),sQuery(id+"F0.wireOp",EDGE,"E6.16.2"),sQuery(id+"F0.wireOp",EDGE,"E6.16.3"),sQuery(id+"F0.wireOp",EDGE,"E6.16.4"),sQuery(id+"F0.wireOp",EDGE,"E6.17.1"),sQuery(id+"F0.wireOp",EDGE,"E6.17.2"),sQuery(id+"F0.wireOp",EDGE,"E6.17.3"),sQuery(id+"F0.wireOp",EDGE,"E6.17.4"),sQuery(id+"F0.wireOp",EDGE,"E6.18.1"),sQuery(id+"F0.wireOp",EDGE,"E6.18.2"),sQuery(id+"F0.wireOp",EDGE,"E6.18.3"),sQuery(id+"F0.wireOp",EDGE,"E6.18.4"),sQuery(id+"F0.wireOp",EDGE,"E6.19.1"),sQuery(id+"F0.wireOp",EDGE,"E6.19.2"),sQuery(id+"F0.wireOp",EDGE,"E6.19.3"),sQuery(id+"F0.wireOp",EDGE,"E6.19.4"),sQuery(id+"F0.wireOp",EDGE,"E6.20.1"),sQuery(id+"F0.wireOp",EDGE,"E6.20.2"),sQuery(id+"F0.wireOp",EDGE,"E6.20.3"),sQuery(id+"F0.wireOp",EDGE,"E6.20.4"),sQuery(id+"F0.wireOp",EDGE,"E6.21.1"),sQuery(id+"F0.wireOp",EDGE,"E6.21.2"),sQuery(id+"F0.wireOp",EDGE,"E6.21.3"),sQuery(id+"F0.wireOp",EDGE,"E6.21.4"),sQuery(id+"F0.wireOp",EDGE,"E6.22.1"),sQuery(id+"F0.wireOp",EDGE,"E6.22.2"),sQuery(id+"F0.wireOp",EDGE,"E6.22.3"),sQuery(id+"F0.wireOp",EDGE,"E6.22.4"),sQuery(id+"F0.wireOp",EDGE,"E6.23.1"),sQuery(id+"F0.wireOp",EDGE,"E6.23.2"),sQuery(id+"F0.wireOp",EDGE,"E6.23.3"),sQuery(id+"F0.wireOp",EDGE,"E6.23.4"),sQuery(id+"F0.wireOp",EDGE,"E6.24.1"),sQuery(id+"F0.wireOp",EDGE,"E6.24.2"),sQuery(id+"F0.wireOp",EDGE,"E6.24.3"),sQuery(id+"F0.wireOp",EDGE,"E6.24.4"),sQuery(id+"F0.wireOp",EDGE,"E6.25.1"),sQuery(id+"F0.wireOp",EDGE,"E6.25.2"),sQuery(id+"F0.wireOp",EDGE,"E6.25.3"),sQuery(id+"F0.wireOp",EDGE,"E6.25.4"),subQ1,sQuery(id+"F0.wireOp",EDGE,"E6.26.2"),subQ0,sQuery(id+"F0.wireOp",EDGE,"E6.26.4"),sQuery(id+"F0.wireOp",EDGE,"E6.27.1"),sQuery(id+"F0.wireOp",EDGE,"E6.27.2"),sQuery(id+"F0.wireOp",EDGE,"E6.27.3"),sQuery(id+"F0.wireOp",EDGE,"E6.27.4"),sQuery(id+"F0.wireOp",EDGE,"E6.28.1"),sQuery(id+"F0.wireOp",EDGE,"E6.28.2"),sQuery(id+"F0.wireOp",EDGE,"E6.28.3"),sQuery(id+"F0.wireOp",EDGE,"E6.28.4"),sQuery(id+"F0.wireOp",EDGE,"E6.29.1"),sQuery(id+"F0.wireOp",EDGE,"E6.29.2"),sQuery(id+"F0.wireOp",EDGE,"E6.29.3"),sQuery(id+"F0.wireOp",EDGE,"E6.29.4"),sQuery(id+"F0.wireOp",EDGE,"E6.30.1"),sQuery(id+"F0.wireOp",EDGE,"E6.30.2"),sQuery(id+"F0.wireOp",EDGE,"E6.30.3"),sQuery(id+"F0.wireOp",EDGE,"E6.30.4"),sQuery(id+"F0.wireOp",EDGE,"E6.31.1"),sQuery(id+"F0.wireOp",EDGE,"E6.31.2"),sQuery(id+"F0.wireOp",EDGE,"E6.31.3"),sQuery(id+"F0.wireOp",EDGE,"E6.31.4"),sQuery(id+"F0.wireOp",EDGE,"E6.32.1"),sQuery(id+"F0.wireOp",EDGE,"E6.32.2"),sQuery(id+"F0.wireOp",EDGE,"E6.32.3"),sQuery(id+"F0.wireOp",EDGE,"E6.32.4"),sQuery(id+"F0.wireOp",EDGE,"E6.33.1"),sQuery(id+"F0.wireOp",EDGE,"E6.33.2"),sQuery(id+"F0.wireOp",EDGE,"E6.33.3"),sQuery(id+"F0.wireOp",EDGE,"E6.33.4"),sQuery(id+"F0.wireOp",EDGE,"E6.34.1"),sQuery(id+"F0.wireOp",EDGE,"E6.34.2"),sQuery(id+"F0.wireOp",EDGE,"E6.34.3"),sQuery(id+"F0.wireOp",EDGE,"E6.34.4"),sQuery(id+"F0.wireOp",EDGE,"E6.35.1"),sQuery(id+"F0.wireOp",EDGE,"E6.35.2"),sQuery(id+"F0.wireOp",EDGE,"E6.35.3"),sQuery(id+"F0.wireOp",EDGE,"E6.35.4"),sQuery(id+"F0.wireOp",EDGE,"E6.36.1"),sQuery(id+"F0.wireOp",EDGE,"E6.36.2"),sQuery(id+"F0.wireOp",EDGE,"E6.36.3"),sQuery(id+"F0.wireOp",EDGE,"E6.36.4"),sQuery(id+"F0.wireOp",EDGE,"E6.37.1"),sQuery(id+"F0.wireOp",EDGE,"E6.37.2"),sQuery(id+"F0.wireOp",EDGE,"E6.37.3"),sQuery(id+"F0.wireOp",EDGE,"E6.37.4"),sQuery(id+"F0.wireOp",EDGE,"E6.38.1"),sQuery(id+"F0.wireOp",EDGE,"E6.38.2"),sQuery(id+"F0.wireOp",EDGE,"E6.38.3"),sQuery(id+"F0.wireOp",EDGE,"E6.38.4"),sQuery(id+"F0.wireOp",EDGE,"E6.39.1"),sQuery(id+"F0.wireOp",EDGE,"E6.39.2"),sQuery(id+"F0.wireOp",EDGE,"E6.39.3"),sQuery(id+"F0.wireOp",EDGE,"E6.39.4"),sQuery(id+"F0.wireOp",EDGE,"E6.40.1"),sQuery(id+"F0.wireOp",EDGE,"E6.40.2"),sQuery(id+"F0.wireOp",EDGE,"E6.40.3"),sQuery(id+"F0.wireOp",EDGE,"E6.40.4"),sQuery(id+"F0.wireOp",EDGE,"E6.41.1"),sQuery(id+"F0.wireOp",EDGE,"E6.41.2"),sQuery(id+"F0.wireOp",EDGE,"E6.41.3"),sQuery(id+"F0.wireOp",EDGE,"E6.41.4"),sQuery(id+"F0.wireOp",EDGE,"E6.42.1"),sQuery(id+"F0.wireOp",EDGE,"E6.42.2"),sQuery(id+"F0.wireOp",EDGE,"E6.42.3"),sQuery(id+"F0.wireOp",EDGE,"E6.42.4"),sQuery(id+"F0.wireOp",EDGE,"E6.43.1"),sQuery(id+"F0.wireOp",EDGE,"E6.43.2"),sQuery(id+"F0.wireOp",EDGE,"E6.43.3"),sQuery(id+"F0.wireOp",EDGE,"E6.43.4"),sQuery(id+"F0.wireOp",EDGE,"E7"),sQuery(id+"F0.wireOp",EDGE,"E8.1.0"),sQuery(id+"F0.wireOp",EDGE,"E8.2.0"),sQuery(id+"F0.wireOp",EDGE,"E8.3.0"),sQuery(id+"F0.wireOp",EDGE,"E8.4.0"),sQuery(id+"F0.wireOp",EDGE,"E8.5.0"),sQuery(id+"F0.wireOp",EDGE,"E8.6.0"),sQuery(id+"F0.wireOp",EDGE,"E8.7.0"),sQuery(id+"F0.wireOp",EDGE,"E8.8.0"),sQuery(id+"F0.wireOp",EDGE,"E8.9.0"),sQuery(id+"F0.wireOp",EDGE,"E8.10.0"),sQuery(id+"F0.wireOp",EDGE,"E8.11.0"),sQuery(id+"F0.wireOp",EDGE,"E8.12.0"),sQuery(id+"F0.wireOp",EDGE,"E8.13.0"),sQuery(id+"F0.wireOp",EDGE,"E8.14.0"),sQuery(id+"F0.wireOp",EDGE,"E8.15.0"),sQuery(id+"F0.wireOp",EDGE,"E8.16.0"),sQuery(id+"F0.wireOp",EDGE,"E8.17.0"),sQuery(id+"F0.wireOp",EDGE,"E8.18.0"),sQuery(id+"F0.wireOp",EDGE,"E8.19.0"),sQuery(id+"F0.wireOp",EDGE,"E8.20.0"),sQuery(id+"F0.wireOp",EDGE,"E8.21.0"),sQuery(id+"F0.wireOp",EDGE,"E8.22.0"),sQuery(id+"F0.wireOp",EDGE,"E8.23.0"),sQuery(id+"F0.wireOp",EDGE,"E8.24.0"),sQuery(id+"F0.wireOp",EDGE,"E8.25.0"),sQuery(id+"F0.wireOp",EDGE,"E8.26.0"),sQuery(id+"F0.wireOp",EDGE,"E8.27.0"),sQuery(id+"F0.wireOp",EDGE,"E8.28.0"),sQuery(id+"F0.wireOp",EDGE,"E8.29.0"),sQuery(id+"F0.wireOp",EDGE,"E8.30.0"),sQuery(id+"F0.wireOp",EDGE,"E8.31.0"),sQuery(id+"F0.wireOp",EDGE,"E8.32.0"),sQuery(id+"F0.wireOp",EDGE,"E8.33.0"),sQuery(id+"F0.wireOp",EDGE,"E8.34.0"),sQuery(id+"F0.wireOp",EDGE,"E8.35.0"),sQuery(id+"F0.wireOp",EDGE,"E8.36.0"),sQuery(id+"F0.wireOp",EDGE,"E8.37.0"),sQuery(id+"F0.wireOp",EDGE,"E8.38.0"),sQuery(id+"F0.wireOp",EDGE,"E8.39.0"),sQuery(id+"F0.wireOp",EDGE,"E8.40.0"),sQuery(id+"F0.wireOp",EDGE,"E8.41.0"),sQuery(id+"F0.wireOp",EDGE,"E8.42.0"),sQuery(id+"F0.wireOp",EDGE,"E8.43.0")])],"isStart":true})]});}
            var Q35;
            {var subQ0=sQuery(id+"F0.wireOp",EDGE,"E6.28.3");var subQ1=sQuery(id+"F0.wireOp",EDGE,"E6.28.1");Q35=makeQuery(id+"F2.opFillet","BLEND_EDGE",EDGE,{"blendedFrom":[makeQuery(id+"F1.opExtrude","SWEPT_EDGE",EDGE,{"disambiguationData":[OSD([sQuery(id+"F0.wireOp",EDGE,"E6.28.0"),subQ1,subQ0])]}),makeQuery(id+"F1.opExtrude","CAP_FACE",FACE,{"disambiguationData":[OSD([sQuery(id+"F0.wireOp",EDGE,"E0"),sQuery(id+"F0.wireOp",EDGE,"E1"),sQuery(id+"F0.wireOp",EDGE,"E2"),sQuery(id+"F0.wireOp",EDGE,"E4"),sQuery(id+"F0.wireOp",EDGE,"E5"),sQuery(id+"F0.wireOp",EDGE,"E6.1.1"),sQuery(id+"F0.wireOp",EDGE,"E6.1.2"),sQuery(id+"F0.wireOp",EDGE,"E6.1.3"),sQuery(id+"F0.wireOp",EDGE,"E6.1.4"),sQuery(id+"F0.wireOp",EDGE,"E6.2.1"),sQuery(id+"F0.wireOp",EDGE,"E6.2.2"),sQuery(id+"F0.wireOp",EDGE,"E6.2.3"),sQuery(id+"F0.wireOp",EDGE,"E6.2.4"),sQuery(id+"F0.wireOp",EDGE,"E6.3.1"),sQuery(id+"F0.wireOp",EDGE,"E6.3.2"),sQuery(id+"F0.wireOp",EDGE,"E6.3.3"),sQuery(id+"F0.wireOp",EDGE,"E6.3.4"),sQuery(id+"F0.wireOp",EDGE,"E6.4.1"),sQuery(id+"F0.wireOp",EDGE,"E6.4.2"),sQuery(id+"F0.wireOp",EDGE,"E6.4.3"),sQuery(id+"F0.wireOp",EDGE,"E6.4.4"),sQuery(id+"F0.wireOp",EDGE,"E6.5.1"),sQuery(id+"F0.wireOp",EDGE,"E6.5.2"),sQuery(id+"F0.wireOp",EDGE,"E6.5.3"),sQuery(id+"F0.wireOp",EDGE,"E6.5.4"),sQuery(id+"F0.wireOp",EDGE,"E6.6.1"),sQuery(id+"F0.wireOp",EDGE,"E6.6.2"),sQuery(id+"F0.wireOp",EDGE,"E6.6.3"),sQuery(id+"F0.wireOp",EDGE,"E6.6.4"),sQuery(id+"F0.wireOp",EDGE,"E6.7.1"),sQuery(id+"F0.wireOp",EDGE,"E6.7.2"),sQuery(id+"F0.wireOp",EDGE,"E6.7.3"),sQuery(id+"F0.wireOp",EDGE,"E6.7.4"),sQuery(id+"F0.wireOp",EDGE,"E6.8.1"),sQuery(id+"F0.wireOp",EDGE,"E6.8.2"),sQuery(id+"F0.wireOp",EDGE,"E6.8.3"),sQuery(id+"F0.wireOp",EDGE,"E6.8.4"),sQuery(id+"F0.wireOp",EDGE,"E6.9.1"),sQuery(id+"F0.wireOp",EDGE,"E6.9.2"),sQuery(id+"F0.wireOp",EDGE,"E6.9.3"),sQuery(id+"F0.wireOp",EDGE,"E6.9.4"),sQuery(id+"F0.wireOp",EDGE,"E6.10.1"),sQuery(id+"F0.wireOp",EDGE,"E6.10.2"),sQuery(id+"F0.wireOp",EDGE,"E6.10.3"),sQuery(id+"F0.wireOp",EDGE,"E6.10.4"),sQuery(id+"F0.wireOp",EDGE,"E6.11.1"),sQuery(id+"F0.wireOp",EDGE,"E6.11.2"),sQuery(id+"F0.wireOp",EDGE,"E6.11.3"),sQuery(id+"F0.wireOp",EDGE,"E6.11.4"),sQuery(id+"F0.wireOp",EDGE,"E6.12.1"),sQuery(id+"F0.wireOp",EDGE,"E6.12.2"),sQuery(id+"F0.wireOp",EDGE,"E6.12.3"),sQuery(id+"F0.wireOp",EDGE,"E6.12.4"),sQuery(id+"F0.wireOp",EDGE,"E6.13.1"),sQuery(id+"F0.wireOp",EDGE,"E6.13.2"),sQuery(id+"F0.wireOp",EDGE,"E6.13.3"),sQuery(id+"F0.wireOp",EDGE,"E6.13.4"),sQuery(id+"F0.wireOp",EDGE,"E6.14.1"),sQuery(id+"F0.wireOp",EDGE,"E6.14.2"),sQuery(id+"F0.wireOp",EDGE,"E6.14.3"),sQuery(id+"F0.wireOp",EDGE,"E6.14.4"),sQuery(id+"F0.wireOp",EDGE,"E6.15.1"),sQuery(id+"F0.wireOp",EDGE,"E6.15.2"),sQuery(id+"F0.wireOp",EDGE,"E6.15.3"),sQuery(id+"F0.wireOp",EDGE,"E6.15.4"),sQuery(id+"F0.wireOp",EDGE,"E6.16.1"),sQuery(id+"F0.wireOp",EDGE,"E6.16.2"),sQuery(id+"F0.wireOp",EDGE,"E6.16.3"),sQuery(id+"F0.wireOp",EDGE,"E6.16.4"),sQuery(id+"F0.wireOp",EDGE,"E6.17.1"),sQuery(id+"F0.wireOp",EDGE,"E6.17.2"),sQuery(id+"F0.wireOp",EDGE,"E6.17.3"),sQuery(id+"F0.wireOp",EDGE,"E6.17.4"),sQuery(id+"F0.wireOp",EDGE,"E6.18.1"),sQuery(id+"F0.wireOp",EDGE,"E6.18.2"),sQuery(id+"F0.wireOp",EDGE,"E6.18.3"),sQuery(id+"F0.wireOp",EDGE,"E6.18.4"),sQuery(id+"F0.wireOp",EDGE,"E6.19.1"),sQuery(id+"F0.wireOp",EDGE,"E6.19.2"),sQuery(id+"F0.wireOp",EDGE,"E6.19.3"),sQuery(id+"F0.wireOp",EDGE,"E6.19.4"),sQuery(id+"F0.wireOp",EDGE,"E6.20.1"),sQuery(id+"F0.wireOp",EDGE,"E6.20.2"),sQuery(id+"F0.wireOp",EDGE,"E6.20.3"),sQuery(id+"F0.wireOp",EDGE,"E6.20.4"),sQuery(id+"F0.wireOp",EDGE,"E6.21.1"),sQuery(id+"F0.wireOp",EDGE,"E6.21.2"),sQuery(id+"F0.wireOp",EDGE,"E6.21.3"),sQuery(id+"F0.wireOp",EDGE,"E6.21.4"),sQuery(id+"F0.wireOp",EDGE,"E6.22.1"),sQuery(id+"F0.wireOp",EDGE,"E6.22.2"),sQuery(id+"F0.wireOp",EDGE,"E6.22.3"),sQuery(id+"F0.wireOp",EDGE,"E6.22.4"),sQuery(id+"F0.wireOp",EDGE,"E6.23.1"),sQuery(id+"F0.wireOp",EDGE,"E6.23.2"),sQuery(id+"F0.wireOp",EDGE,"E6.23.3"),sQuery(id+"F0.wireOp",EDGE,"E6.23.4"),sQuery(id+"F0.wireOp",EDGE,"E6.24.1"),sQuery(id+"F0.wireOp",EDGE,"E6.24.2"),sQuery(id+"F0.wireOp",EDGE,"E6.24.3"),sQuery(id+"F0.wireOp",EDGE,"E6.24.4"),sQuery(id+"F0.wireOp",EDGE,"E6.25.1"),sQuery(id+"F0.wireOp",EDGE,"E6.25.2"),sQuery(id+"F0.wireOp",EDGE,"E6.25.3"),sQuery(id+"F0.wireOp",EDGE,"E6.25.4"),sQuery(id+"F0.wireOp",EDGE,"E6.26.1"),sQuery(id+"F0.wireOp",EDGE,"E6.26.2"),sQuery(id+"F0.wireOp",EDGE,"E6.26.3"),sQuery(id+"F0.wireOp",EDGE,"E6.26.4"),sQuery(id+"F0.wireOp",EDGE,"E6.27.1"),sQuery(id+"F0.wireOp",EDGE,"E6.27.2"),sQuery(id+"F0.wireOp",EDGE,"E6.27.3"),sQuery(id+"F0.wireOp",EDGE,"E6.27.4"),subQ1,sQuery(id+"F0.wireOp",EDGE,"E6.28.2"),subQ0,sQuery(id+"F0.wireOp",EDGE,"E6.28.4"),sQuery(id+"F0.wireOp",EDGE,"E6.29.1"),sQuery(id+"F0.wireOp",EDGE,"E6.29.2"),sQuery(id+"F0.wireOp",EDGE,"E6.29.3"),sQuery(id+"F0.wireOp",EDGE,"E6.29.4"),sQuery(id+"F0.wireOp",EDGE,"E6.30.1"),sQuery(id+"F0.wireOp",EDGE,"E6.30.2"),sQuery(id+"F0.wireOp",EDGE,"E6.30.3"),sQuery(id+"F0.wireOp",EDGE,"E6.30.4"),sQuery(id+"F0.wireOp",EDGE,"E6.31.1"),sQuery(id+"F0.wireOp",EDGE,"E6.31.2"),sQuery(id+"F0.wireOp",EDGE,"E6.31.3"),sQuery(id+"F0.wireOp",EDGE,"E6.31.4"),sQuery(id+"F0.wireOp",EDGE,"E6.32.1"),sQuery(id+"F0.wireOp",EDGE,"E6.32.2"),sQuery(id+"F0.wireOp",EDGE,"E6.32.3"),sQuery(id+"F0.wireOp",EDGE,"E6.32.4"),sQuery(id+"F0.wireOp",EDGE,"E6.33.1"),sQuery(id+"F0.wireOp",EDGE,"E6.33.2"),sQuery(id+"F0.wireOp",EDGE,"E6.33.3"),sQuery(id+"F0.wireOp",EDGE,"E6.33.4"),sQuery(id+"F0.wireOp",EDGE,"E6.34.1"),sQuery(id+"F0.wireOp",EDGE,"E6.34.2"),sQuery(id+"F0.wireOp",EDGE,"E6.34.3"),sQuery(id+"F0.wireOp",EDGE,"E6.34.4"),sQuery(id+"F0.wireOp",EDGE,"E6.35.1"),sQuery(id+"F0.wireOp",EDGE,"E6.35.2"),sQuery(id+"F0.wireOp",EDGE,"E6.35.3"),sQuery(id+"F0.wireOp",EDGE,"E6.35.4"),sQuery(id+"F0.wireOp",EDGE,"E6.36.1"),sQuery(id+"F0.wireOp",EDGE,"E6.36.2"),sQuery(id+"F0.wireOp",EDGE,"E6.36.3"),sQuery(id+"F0.wireOp",EDGE,"E6.36.4"),sQuery(id+"F0.wireOp",EDGE,"E6.37.1"),sQuery(id+"F0.wireOp",EDGE,"E6.37.2"),sQuery(id+"F0.wireOp",EDGE,"E6.37.3"),sQuery(id+"F0.wireOp",EDGE,"E6.37.4"),sQuery(id+"F0.wireOp",EDGE,"E6.38.1"),sQuery(id+"F0.wireOp",EDGE,"E6.38.2"),sQuery(id+"F0.wireOp",EDGE,"E6.38.3"),sQuery(id+"F0.wireOp",EDGE,"E6.38.4"),sQuery(id+"F0.wireOp",EDGE,"E6.39.1"),sQuery(id+"F0.wireOp",EDGE,"E6.39.2"),sQuery(id+"F0.wireOp",EDGE,"E6.39.3"),sQuery(id+"F0.wireOp",EDGE,"E6.39.4"),sQuery(id+"F0.wireOp",EDGE,"E6.40.1"),sQuery(id+"F0.wireOp",EDGE,"E6.40.2"),sQuery(id+"F0.wireOp",EDGE,"E6.40.3"),sQuery(id+"F0.wireOp",EDGE,"E6.40.4"),sQuery(id+"F0.wireOp",EDGE,"E6.41.1"),sQuery(id+"F0.wireOp",EDGE,"E6.41.2"),sQuery(id+"F0.wireOp",EDGE,"E6.41.3"),sQuery(id+"F0.wireOp",EDGE,"E6.41.4"),sQuery(id+"F0.wireOp",EDGE,"E6.42.1"),sQuery(id+"F0.wireOp",EDGE,"E6.42.2"),sQuery(id+"F0.wireOp",EDGE,"E6.42.3"),sQuery(id+"F0.wireOp",EDGE,"E6.42.4"),sQuery(id+"F0.wireOp",EDGE,"E6.43.1"),sQuery(id+"F0.wireOp",EDGE,"E6.43.2"),sQuery(id+"F0.wireOp",EDGE,"E6.43.3"),sQuery(id+"F0.wireOp",EDGE,"E6.43.4"),sQuery(id+"F0.wireOp",EDGE,"E7"),sQuery(id+"F0.wireOp",EDGE,"E8.1.0"),sQuery(id+"F0.wireOp",EDGE,"E8.2.0"),sQuery(id+"F0.wireOp",EDGE,"E8.3.0"),sQuery(id+"F0.wireOp",EDGE,"E8.4.0"),sQuery(id+"F0.wireOp",EDGE,"E8.5.0"),sQuery(id+"F0.wireOp",EDGE,"E8.6.0"),sQuery(id+"F0.wireOp",EDGE,"E8.7.0"),sQuery(id+"F0.wireOp",EDGE,"E8.8.0"),sQuery(id+"F0.wireOp",EDGE,"E8.9.0"),sQuery(id+"F0.wireOp",EDGE,"E8.10.0"),sQuery(id+"F0.wireOp",EDGE,"E8.11.0"),sQuery(id+"F0.wireOp",EDGE,"E8.12.0"),sQuery(id+"F0.wireOp",EDGE,"E8.13.0"),sQuery(id+"F0.wireOp",EDGE,"E8.14.0"),sQuery(id+"F0.wireOp",EDGE,"E8.15.0"),sQuery(id+"F0.wireOp",EDGE,"E8.16.0"),sQuery(id+"F0.wireOp",EDGE,"E8.17.0"),sQuery(id+"F0.wireOp",EDGE,"E8.18.0"),sQuery(id+"F0.wireOp",EDGE,"E8.19.0"),sQuery(id+"F0.wireOp",EDGE,"E8.20.0"),sQuery(id+"F0.wireOp",EDGE,"E8.21.0"),sQuery(id+"F0.wireOp",EDGE,"E8.22.0"),sQuery(id+"F0.wireOp",EDGE,"E8.23.0"),sQuery(id+"F0.wireOp",EDGE,"E8.24.0"),sQuery(id+"F0.wireOp",EDGE,"E8.25.0"),sQuery(id+"F0.wireOp",EDGE,"E8.26.0"),sQuery(id+"F0.wireOp",EDGE,"E8.27.0"),sQuery(id+"F0.wireOp",EDGE,"E8.28.0"),sQuery(id+"F0.wireOp",EDGE,"E8.29.0"),sQuery(id+"F0.wireOp",EDGE,"E8.30.0"),sQuery(id+"F0.wireOp",EDGE,"E8.31.0"),sQuery(id+"F0.wireOp",EDGE,"E8.32.0"),sQuery(id+"F0.wireOp",EDGE,"E8.33.0"),sQuery(id+"F0.wireOp",EDGE,"E8.34.0"),sQuery(id+"F0.wireOp",EDGE,"E8.35.0"),sQuery(id+"F0.wireOp",EDGE,"E8.36.0"),sQuery(id+"F0.wireOp",EDGE,"E8.37.0"),sQuery(id+"F0.wireOp",EDGE,"E8.38.0"),sQuery(id+"F0.wireOp",EDGE,"E8.39.0"),sQuery(id+"F0.wireOp",EDGE,"E8.40.0"),sQuery(id+"F0.wireOp",EDGE,"E8.41.0"),sQuery(id+"F0.wireOp",EDGE,"E8.42.0"),sQuery(id+"F0.wireOp",EDGE,"E8.43.0")])],"isStart":true})],"blendedInto":[makeQuery(id+"F1.opExtrude","CAP_FACE",FACE,{"disambiguationData":[OSD([sQuery(id+"F0.wireOp",EDGE,"E0"),sQuery(id+"F0.wireOp",EDGE,"E1"),sQuery(id+"F0.wireOp",EDGE,"E2"),sQuery(id+"F0.wireOp",EDGE,"E4"),sQuery(id+"F0.wireOp",EDGE,"E5"),sQuery(id+"F0.wireOp",EDGE,"E6.1.1"),sQuery(id+"F0.wireOp",EDGE,"E6.1.2"),sQuery(id+"F0.wireOp",EDGE,"E6.1.3"),sQuery(id+"F0.wireOp",EDGE,"E6.1.4"),sQuery(id+"F0.wireOp",EDGE,"E6.2.1"),sQuery(id+"F0.wireOp",EDGE,"E6.2.2"),sQuery(id+"F0.wireOp",EDGE,"E6.2.3"),sQuery(id+"F0.wireOp",EDGE,"E6.2.4"),sQuery(id+"F0.wireOp",EDGE,"E6.3.1"),sQuery(id+"F0.wireOp",EDGE,"E6.3.2"),sQuery(id+"F0.wireOp",EDGE,"E6.3.3"),sQuery(id+"F0.wireOp",EDGE,"E6.3.4"),sQuery(id+"F0.wireOp",EDGE,"E6.4.1"),sQuery(id+"F0.wireOp",EDGE,"E6.4.2"),sQuery(id+"F0.wireOp",EDGE,"E6.4.3"),sQuery(id+"F0.wireOp",EDGE,"E6.4.4"),sQuery(id+"F0.wireOp",EDGE,"E6.5.1"),sQuery(id+"F0.wireOp",EDGE,"E6.5.2"),sQuery(id+"F0.wireOp",EDGE,"E6.5.3"),sQuery(id+"F0.wireOp",EDGE,"E6.5.4"),sQuery(id+"F0.wireOp",EDGE,"E6.6.1"),sQuery(id+"F0.wireOp",EDGE,"E6.6.2"),sQuery(id+"F0.wireOp",EDGE,"E6.6.3"),sQuery(id+"F0.wireOp",EDGE,"E6.6.4"),sQuery(id+"F0.wireOp",EDGE,"E6.7.1"),sQuery(id+"F0.wireOp",EDGE,"E6.7.2"),sQuery(id+"F0.wireOp",EDGE,"E6.7.3"),sQuery(id+"F0.wireOp",EDGE,"E6.7.4"),sQuery(id+"F0.wireOp",EDGE,"E6.8.1"),sQuery(id+"F0.wireOp",EDGE,"E6.8.2"),sQuery(id+"F0.wireOp",EDGE,"E6.8.3"),sQuery(id+"F0.wireOp",EDGE,"E6.8.4"),sQuery(id+"F0.wireOp",EDGE,"E6.9.1"),sQuery(id+"F0.wireOp",EDGE,"E6.9.2"),sQuery(id+"F0.wireOp",EDGE,"E6.9.3"),sQuery(id+"F0.wireOp",EDGE,"E6.9.4"),sQuery(id+"F0.wireOp",EDGE,"E6.10.1"),sQuery(id+"F0.wireOp",EDGE,"E6.10.2"),sQuery(id+"F0.wireOp",EDGE,"E6.10.3"),sQuery(id+"F0.wireOp",EDGE,"E6.10.4"),sQuery(id+"F0.wireOp",EDGE,"E6.11.1"),sQuery(id+"F0.wireOp",EDGE,"E6.11.2"),sQuery(id+"F0.wireOp",EDGE,"E6.11.3"),sQuery(id+"F0.wireOp",EDGE,"E6.11.4"),sQuery(id+"F0.wireOp",EDGE,"E6.12.1"),sQuery(id+"F0.wireOp",EDGE,"E6.12.2"),sQuery(id+"F0.wireOp",EDGE,"E6.12.3"),sQuery(id+"F0.wireOp",EDGE,"E6.12.4"),sQuery(id+"F0.wireOp",EDGE,"E6.13.1"),sQuery(id+"F0.wireOp",EDGE,"E6.13.2"),sQuery(id+"F0.wireOp",EDGE,"E6.13.3"),sQuery(id+"F0.wireOp",EDGE,"E6.13.4"),sQuery(id+"F0.wireOp",EDGE,"E6.14.1"),sQuery(id+"F0.wireOp",EDGE,"E6.14.2"),sQuery(id+"F0.wireOp",EDGE,"E6.14.3"),sQuery(id+"F0.wireOp",EDGE,"E6.14.4"),sQuery(id+"F0.wireOp",EDGE,"E6.15.1"),sQuery(id+"F0.wireOp",EDGE,"E6.15.2"),sQuery(id+"F0.wireOp",EDGE,"E6.15.3"),sQuery(id+"F0.wireOp",EDGE,"E6.15.4"),sQuery(id+"F0.wireOp",EDGE,"E6.16.1"),sQuery(id+"F0.wireOp",EDGE,"E6.16.2"),sQuery(id+"F0.wireOp",EDGE,"E6.16.3"),sQuery(id+"F0.wireOp",EDGE,"E6.16.4"),sQuery(id+"F0.wireOp",EDGE,"E6.17.1"),sQuery(id+"F0.wireOp",EDGE,"E6.17.2"),sQuery(id+"F0.wireOp",EDGE,"E6.17.3"),sQuery(id+"F0.wireOp",EDGE,"E6.17.4"),sQuery(id+"F0.wireOp",EDGE,"E6.18.1"),sQuery(id+"F0.wireOp",EDGE,"E6.18.2"),sQuery(id+"F0.wireOp",EDGE,"E6.18.3"),sQuery(id+"F0.wireOp",EDGE,"E6.18.4"),sQuery(id+"F0.wireOp",EDGE,"E6.19.1"),sQuery(id+"F0.wireOp",EDGE,"E6.19.2"),sQuery(id+"F0.wireOp",EDGE,"E6.19.3"),sQuery(id+"F0.wireOp",EDGE,"E6.19.4"),sQuery(id+"F0.wireOp",EDGE,"E6.20.1"),sQuery(id+"F0.wireOp",EDGE,"E6.20.2"),sQuery(id+"F0.wireOp",EDGE,"E6.20.3"),sQuery(id+"F0.wireOp",EDGE,"E6.20.4"),sQuery(id+"F0.wireOp",EDGE,"E6.21.1"),sQuery(id+"F0.wireOp",EDGE,"E6.21.2"),sQuery(id+"F0.wireOp",EDGE,"E6.21.3"),sQuery(id+"F0.wireOp",EDGE,"E6.21.4"),sQuery(id+"F0.wireOp",EDGE,"E6.22.1"),sQuery(id+"F0.wireOp",EDGE,"E6.22.2"),sQuery(id+"F0.wireOp",EDGE,"E6.22.3"),sQuery(id+"F0.wireOp",EDGE,"E6.22.4"),sQuery(id+"F0.wireOp",EDGE,"E6.23.1"),sQuery(id+"F0.wireOp",EDGE,"E6.23.2"),sQuery(id+"F0.wireOp",EDGE,"E6.23.3"),sQuery(id+"F0.wireOp",EDGE,"E6.23.4"),sQuery(id+"F0.wireOp",EDGE,"E6.24.1"),sQuery(id+"F0.wireOp",EDGE,"E6.24.2"),sQuery(id+"F0.wireOp",EDGE,"E6.24.3"),sQuery(id+"F0.wireOp",EDGE,"E6.24.4"),sQuery(id+"F0.wireOp",EDGE,"E6.25.1"),sQuery(id+"F0.wireOp",EDGE,"E6.25.2"),sQuery(id+"F0.wireOp",EDGE,"E6.25.3"),sQuery(id+"F0.wireOp",EDGE,"E6.25.4"),sQuery(id+"F0.wireOp",EDGE,"E6.26.1"),sQuery(id+"F0.wireOp",EDGE,"E6.26.2"),sQuery(id+"F0.wireOp",EDGE,"E6.26.3"),sQuery(id+"F0.wireOp",EDGE,"E6.26.4"),sQuery(id+"F0.wireOp",EDGE,"E6.27.1"),sQuery(id+"F0.wireOp",EDGE,"E6.27.2"),sQuery(id+"F0.wireOp",EDGE,"E6.27.3"),sQuery(id+"F0.wireOp",EDGE,"E6.27.4"),subQ1,sQuery(id+"F0.wireOp",EDGE,"E6.28.2"),subQ0,sQuery(id+"F0.wireOp",EDGE,"E6.28.4"),sQuery(id+"F0.wireOp",EDGE,"E6.29.1"),sQuery(id+"F0.wireOp",EDGE,"E6.29.2"),sQuery(id+"F0.wireOp",EDGE,"E6.29.3"),sQuery(id+"F0.wireOp",EDGE,"E6.29.4"),sQuery(id+"F0.wireOp",EDGE,"E6.30.1"),sQuery(id+"F0.wireOp",EDGE,"E6.30.2"),sQuery(id+"F0.wireOp",EDGE,"E6.30.3"),sQuery(id+"F0.wireOp",EDGE,"E6.30.4"),sQuery(id+"F0.wireOp",EDGE,"E6.31.1"),sQuery(id+"F0.wireOp",EDGE,"E6.31.2"),sQuery(id+"F0.wireOp",EDGE,"E6.31.3"),sQuery(id+"F0.wireOp",EDGE,"E6.31.4"),sQuery(id+"F0.wireOp",EDGE,"E6.32.1"),sQuery(id+"F0.wireOp",EDGE,"E6.32.2"),sQuery(id+"F0.wireOp",EDGE,"E6.32.3"),sQuery(id+"F0.wireOp",EDGE,"E6.32.4"),sQuery(id+"F0.wireOp",EDGE,"E6.33.1"),sQuery(id+"F0.wireOp",EDGE,"E6.33.2"),sQuery(id+"F0.wireOp",EDGE,"E6.33.3"),sQuery(id+"F0.wireOp",EDGE,"E6.33.4"),sQuery(id+"F0.wireOp",EDGE,"E6.34.1"),sQuery(id+"F0.wireOp",EDGE,"E6.34.2"),sQuery(id+"F0.wireOp",EDGE,"E6.34.3"),sQuery(id+"F0.wireOp",EDGE,"E6.34.4"),sQuery(id+"F0.wireOp",EDGE,"E6.35.1"),sQuery(id+"F0.wireOp",EDGE,"E6.35.2"),sQuery(id+"F0.wireOp",EDGE,"E6.35.3"),sQuery(id+"F0.wireOp",EDGE,"E6.35.4"),sQuery(id+"F0.wireOp",EDGE,"E6.36.1"),sQuery(id+"F0.wireOp",EDGE,"E6.36.2"),sQuery(id+"F0.wireOp",EDGE,"E6.36.3"),sQuery(id+"F0.wireOp",EDGE,"E6.36.4"),sQuery(id+"F0.wireOp",EDGE,"E6.37.1"),sQuery(id+"F0.wireOp",EDGE,"E6.37.2"),sQuery(id+"F0.wireOp",EDGE,"E6.37.3"),sQuery(id+"F0.wireOp",EDGE,"E6.37.4"),sQuery(id+"F0.wireOp",EDGE,"E6.38.1"),sQuery(id+"F0.wireOp",EDGE,"E6.38.2"),sQuery(id+"F0.wireOp",EDGE,"E6.38.3"),sQuery(id+"F0.wireOp",EDGE,"E6.38.4"),sQuery(id+"F0.wireOp",EDGE,"E6.39.1"),sQuery(id+"F0.wireOp",EDGE,"E6.39.2"),sQuery(id+"F0.wireOp",EDGE,"E6.39.3"),sQuery(id+"F0.wireOp",EDGE,"E6.39.4"),sQuery(id+"F0.wireOp",EDGE,"E6.40.1"),sQuery(id+"F0.wireOp",EDGE,"E6.40.2"),sQuery(id+"F0.wireOp",EDGE,"E6.40.3"),sQuery(id+"F0.wireOp",EDGE,"E6.40.4"),sQuery(id+"F0.wireOp",EDGE,"E6.41.1"),sQuery(id+"F0.wireOp",EDGE,"E6.41.2"),sQuery(id+"F0.wireOp",EDGE,"E6.41.3"),sQuery(id+"F0.wireOp",EDGE,"E6.41.4"),sQuery(id+"F0.wireOp",EDGE,"E6.42.1"),sQuery(id+"F0.wireOp",EDGE,"E6.42.2"),sQuery(id+"F0.wireOp",EDGE,"E6.42.3"),sQuery(id+"F0.wireOp",EDGE,"E6.42.4"),sQuery(id+"F0.wireOp",EDGE,"E6.43.1"),sQuery(id+"F0.wireOp",EDGE,"E6.43.2"),sQuery(id+"F0.wireOp",EDGE,"E6.43.3"),sQuery(id+"F0.wireOp",EDGE,"E6.43.4"),sQuery(id+"F0.wireOp",EDGE,"E7"),sQuery(id+"F0.wireOp",EDGE,"E8.1.0"),sQuery(id+"F0.wireOp",EDGE,"E8.2.0"),sQuery(id+"F0.wireOp",EDGE,"E8.3.0"),sQuery(id+"F0.wireOp",EDGE,"E8.4.0"),sQuery(id+"F0.wireOp",EDGE,"E8.5.0"),sQuery(id+"F0.wireOp",EDGE,"E8.6.0"),sQuery(id+"F0.wireOp",EDGE,"E8.7.0"),sQuery(id+"F0.wireOp",EDGE,"E8.8.0"),sQuery(id+"F0.wireOp",EDGE,"E8.9.0"),sQuery(id+"F0.wireOp",EDGE,"E8.10.0"),sQuery(id+"F0.wireOp",EDGE,"E8.11.0"),sQuery(id+"F0.wireOp",EDGE,"E8.12.0"),sQuery(id+"F0.wireOp",EDGE,"E8.13.0"),sQuery(id+"F0.wireOp",EDGE,"E8.14.0"),sQuery(id+"F0.wireOp",EDGE,"E8.15.0"),sQuery(id+"F0.wireOp",EDGE,"E8.16.0"),sQuery(id+"F0.wireOp",EDGE,"E8.17.0"),sQuery(id+"F0.wireOp",EDGE,"E8.18.0"),sQuery(id+"F0.wireOp",EDGE,"E8.19.0"),sQuery(id+"F0.wireOp",EDGE,"E8.20.0"),sQuery(id+"F0.wireOp",EDGE,"E8.21.0"),sQuery(id+"F0.wireOp",EDGE,"E8.22.0"),sQuery(id+"F0.wireOp",EDGE,"E8.23.0"),sQuery(id+"F0.wireOp",EDGE,"E8.24.0"),sQuery(id+"F0.wireOp",EDGE,"E8.25.0"),sQuery(id+"F0.wireOp",EDGE,"E8.26.0"),sQuery(id+"F0.wireOp",EDGE,"E8.27.0"),sQuery(id+"F0.wireOp",EDGE,"E8.28.0"),sQuery(id+"F0.wireOp",EDGE,"E8.29.0"),sQuery(id+"F0.wireOp",EDGE,"E8.30.0"),sQuery(id+"F0.wireOp",EDGE,"E8.31.0"),sQuery(id+"F0.wireOp",EDGE,"E8.32.0"),sQuery(id+"F0.wireOp",EDGE,"E8.33.0"),sQuery(id+"F0.wireOp",EDGE,"E8.34.0"),sQuery(id+"F0.wireOp",EDGE,"E8.35.0"),sQuery(id+"F0.wireOp",EDGE,"E8.36.0"),sQuery(id+"F0.wireOp",EDGE,"E8.37.0"),sQuery(id+"F0.wireOp",EDGE,"E8.38.0"),sQuery(id+"F0.wireOp",EDGE,"E8.39.0"),sQuery(id+"F0.wireOp",EDGE,"E8.40.0"),sQuery(id+"F0.wireOp",EDGE,"E8.41.0"),sQuery(id+"F0.wireOp",EDGE,"E8.42.0"),sQuery(id+"F0.wireOp",EDGE,"E8.43.0")])],"isStart":true})]});}
            var Q36;
            {var subQ0=sQuery(id+"F0.wireOp",EDGE,"E6.30.3");var subQ1=sQuery(id+"F0.wireOp",EDGE,"E6.30.1");Q36=makeQuery(id+"F2.opFillet","BLEND_EDGE",EDGE,{"blendedFrom":[makeQuery(id+"F1.opExtrude","SWEPT_EDGE",EDGE,{"disambiguationData":[OSD([sQuery(id+"F0.wireOp",EDGE,"E6.30.0"),subQ1,subQ0])]}),makeQuery(id+"F1.opExtrude","CAP_FACE",FACE,{"disambiguationData":[OSD([sQuery(id+"F0.wireOp",EDGE,"E0"),sQuery(id+"F0.wireOp",EDGE,"E1"),sQuery(id+"F0.wireOp",EDGE,"E2"),sQuery(id+"F0.wireOp",EDGE,"E4"),sQuery(id+"F0.wireOp",EDGE,"E5"),sQuery(id+"F0.wireOp",EDGE,"E6.1.1"),sQuery(id+"F0.wireOp",EDGE,"E6.1.2"),sQuery(id+"F0.wireOp",EDGE,"E6.1.3"),sQuery(id+"F0.wireOp",EDGE,"E6.1.4"),sQuery(id+"F0.wireOp",EDGE,"E6.2.1"),sQuery(id+"F0.wireOp",EDGE,"E6.2.2"),sQuery(id+"F0.wireOp",EDGE,"E6.2.3"),sQuery(id+"F0.wireOp",EDGE,"E6.2.4"),sQuery(id+"F0.wireOp",EDGE,"E6.3.1"),sQuery(id+"F0.wireOp",EDGE,"E6.3.2"),sQuery(id+"F0.wireOp",EDGE,"E6.3.3"),sQuery(id+"F0.wireOp",EDGE,"E6.3.4"),sQuery(id+"F0.wireOp",EDGE,"E6.4.1"),sQuery(id+"F0.wireOp",EDGE,"E6.4.2"),sQuery(id+"F0.wireOp",EDGE,"E6.4.3"),sQuery(id+"F0.wireOp",EDGE,"E6.4.4"),sQuery(id+"F0.wireOp",EDGE,"E6.5.1"),sQuery(id+"F0.wireOp",EDGE,"E6.5.2"),sQuery(id+"F0.wireOp",EDGE,"E6.5.3"),sQuery(id+"F0.wireOp",EDGE,"E6.5.4"),sQuery(id+"F0.wireOp",EDGE,"E6.6.1"),sQuery(id+"F0.wireOp",EDGE,"E6.6.2"),sQuery(id+"F0.wireOp",EDGE,"E6.6.3"),sQuery(id+"F0.wireOp",EDGE,"E6.6.4"),sQuery(id+"F0.wireOp",EDGE,"E6.7.1"),sQuery(id+"F0.wireOp",EDGE,"E6.7.2"),sQuery(id+"F0.wireOp",EDGE,"E6.7.3"),sQuery(id+"F0.wireOp",EDGE,"E6.7.4"),sQuery(id+"F0.wireOp",EDGE,"E6.8.1"),sQuery(id+"F0.wireOp",EDGE,"E6.8.2"),sQuery(id+"F0.wireOp",EDGE,"E6.8.3"),sQuery(id+"F0.wireOp",EDGE,"E6.8.4"),sQuery(id+"F0.wireOp",EDGE,"E6.9.1"),sQuery(id+"F0.wireOp",EDGE,"E6.9.2"),sQuery(id+"F0.wireOp",EDGE,"E6.9.3"),sQuery(id+"F0.wireOp",EDGE,"E6.9.4"),sQuery(id+"F0.wireOp",EDGE,"E6.10.1"),sQuery(id+"F0.wireOp",EDGE,"E6.10.2"),sQuery(id+"F0.wireOp",EDGE,"E6.10.3"),sQuery(id+"F0.wireOp",EDGE,"E6.10.4"),sQuery(id+"F0.wireOp",EDGE,"E6.11.1"),sQuery(id+"F0.wireOp",EDGE,"E6.11.2"),sQuery(id+"F0.wireOp",EDGE,"E6.11.3"),sQuery(id+"F0.wireOp",EDGE,"E6.11.4"),sQuery(id+"F0.wireOp",EDGE,"E6.12.1"),sQuery(id+"F0.wireOp",EDGE,"E6.12.2"),sQuery(id+"F0.wireOp",EDGE,"E6.12.3"),sQuery(id+"F0.wireOp",EDGE,"E6.12.4"),sQuery(id+"F0.wireOp",EDGE,"E6.13.1"),sQuery(id+"F0.wireOp",EDGE,"E6.13.2"),sQuery(id+"F0.wireOp",EDGE,"E6.13.3"),sQuery(id+"F0.wireOp",EDGE,"E6.13.4"),sQuery(id+"F0.wireOp",EDGE,"E6.14.1"),sQuery(id+"F0.wireOp",EDGE,"E6.14.2"),sQuery(id+"F0.wireOp",EDGE,"E6.14.3"),sQuery(id+"F0.wireOp",EDGE,"E6.14.4"),sQuery(id+"F0.wireOp",EDGE,"E6.15.1"),sQuery(id+"F0.wireOp",EDGE,"E6.15.2"),sQuery(id+"F0.wireOp",EDGE,"E6.15.3"),sQuery(id+"F0.wireOp",EDGE,"E6.15.4"),sQuery(id+"F0.wireOp",EDGE,"E6.16.1"),sQuery(id+"F0.wireOp",EDGE,"E6.16.2"),sQuery(id+"F0.wireOp",EDGE,"E6.16.3"),sQuery(id+"F0.wireOp",EDGE,"E6.16.4"),sQuery(id+"F0.wireOp",EDGE,"E6.17.1"),sQuery(id+"F0.wireOp",EDGE,"E6.17.2"),sQuery(id+"F0.wireOp",EDGE,"E6.17.3"),sQuery(id+"F0.wireOp",EDGE,"E6.17.4"),sQuery(id+"F0.wireOp",EDGE,"E6.18.1"),sQuery(id+"F0.wireOp",EDGE,"E6.18.2"),sQuery(id+"F0.wireOp",EDGE,"E6.18.3"),sQuery(id+"F0.wireOp",EDGE,"E6.18.4"),sQuery(id+"F0.wireOp",EDGE,"E6.19.1"),sQuery(id+"F0.wireOp",EDGE,"E6.19.2"),sQuery(id+"F0.wireOp",EDGE,"E6.19.3"),sQuery(id+"F0.wireOp",EDGE,"E6.19.4"),sQuery(id+"F0.wireOp",EDGE,"E6.20.1"),sQuery(id+"F0.wireOp",EDGE,"E6.20.2"),sQuery(id+"F0.wireOp",EDGE,"E6.20.3"),sQuery(id+"F0.wireOp",EDGE,"E6.20.4"),sQuery(id+"F0.wireOp",EDGE,"E6.21.1"),sQuery(id+"F0.wireOp",EDGE,"E6.21.2"),sQuery(id+"F0.wireOp",EDGE,"E6.21.3"),sQuery(id+"F0.wireOp",EDGE,"E6.21.4"),sQuery(id+"F0.wireOp",EDGE,"E6.22.1"),sQuery(id+"F0.wireOp",EDGE,"E6.22.2"),sQuery(id+"F0.wireOp",EDGE,"E6.22.3"),sQuery(id+"F0.wireOp",EDGE,"E6.22.4"),sQuery(id+"F0.wireOp",EDGE,"E6.23.1"),sQuery(id+"F0.wireOp",EDGE,"E6.23.2"),sQuery(id+"F0.wireOp",EDGE,"E6.23.3"),sQuery(id+"F0.wireOp",EDGE,"E6.23.4"),sQuery(id+"F0.wireOp",EDGE,"E6.24.1"),sQuery(id+"F0.wireOp",EDGE,"E6.24.2"),sQuery(id+"F0.wireOp",EDGE,"E6.24.3"),sQuery(id+"F0.wireOp",EDGE,"E6.24.4"),sQuery(id+"F0.wireOp",EDGE,"E6.25.1"),sQuery(id+"F0.wireOp",EDGE,"E6.25.2"),sQuery(id+"F0.wireOp",EDGE,"E6.25.3"),sQuery(id+"F0.wireOp",EDGE,"E6.25.4"),sQuery(id+"F0.wireOp",EDGE,"E6.26.1"),sQuery(id+"F0.wireOp",EDGE,"E6.26.2"),sQuery(id+"F0.wireOp",EDGE,"E6.26.3"),sQuery(id+"F0.wireOp",EDGE,"E6.26.4"),sQuery(id+"F0.wireOp",EDGE,"E6.27.1"),sQuery(id+"F0.wireOp",EDGE,"E6.27.2"),sQuery(id+"F0.wireOp",EDGE,"E6.27.3"),sQuery(id+"F0.wireOp",EDGE,"E6.27.4"),sQuery(id+"F0.wireOp",EDGE,"E6.28.1"),sQuery(id+"F0.wireOp",EDGE,"E6.28.2"),sQuery(id+"F0.wireOp",EDGE,"E6.28.3"),sQuery(id+"F0.wireOp",EDGE,"E6.28.4"),sQuery(id+"F0.wireOp",EDGE,"E6.29.1"),sQuery(id+"F0.wireOp",EDGE,"E6.29.2"),sQuery(id+"F0.wireOp",EDGE,"E6.29.3"),sQuery(id+"F0.wireOp",EDGE,"E6.29.4"),subQ1,sQuery(id+"F0.wireOp",EDGE,"E6.30.2"),subQ0,sQuery(id+"F0.wireOp",EDGE,"E6.30.4"),sQuery(id+"F0.wireOp",EDGE,"E6.31.1"),sQuery(id+"F0.wireOp",EDGE,"E6.31.2"),sQuery(id+"F0.wireOp",EDGE,"E6.31.3"),sQuery(id+"F0.wireOp",EDGE,"E6.31.4"),sQuery(id+"F0.wireOp",EDGE,"E6.32.1"),sQuery(id+"F0.wireOp",EDGE,"E6.32.2"),sQuery(id+"F0.wireOp",EDGE,"E6.32.3"),sQuery(id+"F0.wireOp",EDGE,"E6.32.4"),sQuery(id+"F0.wireOp",EDGE,"E6.33.1"),sQuery(id+"F0.wireOp",EDGE,"E6.33.2"),sQuery(id+"F0.wireOp",EDGE,"E6.33.3"),sQuery(id+"F0.wireOp",EDGE,"E6.33.4"),sQuery(id+"F0.wireOp",EDGE,"E6.34.1"),sQuery(id+"F0.wireOp",EDGE,"E6.34.2"),sQuery(id+"F0.wireOp",EDGE,"E6.34.3"),sQuery(id+"F0.wireOp",EDGE,"E6.34.4"),sQuery(id+"F0.wireOp",EDGE,"E6.35.1"),sQuery(id+"F0.wireOp",EDGE,"E6.35.2"),sQuery(id+"F0.wireOp",EDGE,"E6.35.3"),sQuery(id+"F0.wireOp",EDGE,"E6.35.4"),sQuery(id+"F0.wireOp",EDGE,"E6.36.1"),sQuery(id+"F0.wireOp",EDGE,"E6.36.2"),sQuery(id+"F0.wireOp",EDGE,"E6.36.3"),sQuery(id+"F0.wireOp",EDGE,"E6.36.4"),sQuery(id+"F0.wireOp",EDGE,"E6.37.1"),sQuery(id+"F0.wireOp",EDGE,"E6.37.2"),sQuery(id+"F0.wireOp",EDGE,"E6.37.3"),sQuery(id+"F0.wireOp",EDGE,"E6.37.4"),sQuery(id+"F0.wireOp",EDGE,"E6.38.1"),sQuery(id+"F0.wireOp",EDGE,"E6.38.2"),sQuery(id+"F0.wireOp",EDGE,"E6.38.3"),sQuery(id+"F0.wireOp",EDGE,"E6.38.4"),sQuery(id+"F0.wireOp",EDGE,"E6.39.1"),sQuery(id+"F0.wireOp",EDGE,"E6.39.2"),sQuery(id+"F0.wireOp",EDGE,"E6.39.3"),sQuery(id+"F0.wireOp",EDGE,"E6.39.4"),sQuery(id+"F0.wireOp",EDGE,"E6.40.1"),sQuery(id+"F0.wireOp",EDGE,"E6.40.2"),sQuery(id+"F0.wireOp",EDGE,"E6.40.3"),sQuery(id+"F0.wireOp",EDGE,"E6.40.4"),sQuery(id+"F0.wireOp",EDGE,"E6.41.1"),sQuery(id+"F0.wireOp",EDGE,"E6.41.2"),sQuery(id+"F0.wireOp",EDGE,"E6.41.3"),sQuery(id+"F0.wireOp",EDGE,"E6.41.4"),sQuery(id+"F0.wireOp",EDGE,"E6.42.1"),sQuery(id+"F0.wireOp",EDGE,"E6.42.2"),sQuery(id+"F0.wireOp",EDGE,"E6.42.3"),sQuery(id+"F0.wireOp",EDGE,"E6.42.4"),sQuery(id+"F0.wireOp",EDGE,"E6.43.1"),sQuery(id+"F0.wireOp",EDGE,"E6.43.2"),sQuery(id+"F0.wireOp",EDGE,"E6.43.3"),sQuery(id+"F0.wireOp",EDGE,"E6.43.4"),sQuery(id+"F0.wireOp",EDGE,"E7"),sQuery(id+"F0.wireOp",EDGE,"E8.1.0"),sQuery(id+"F0.wireOp",EDGE,"E8.2.0"),sQuery(id+"F0.wireOp",EDGE,"E8.3.0"),sQuery(id+"F0.wireOp",EDGE,"E8.4.0"),sQuery(id+"F0.wireOp",EDGE,"E8.5.0"),sQuery(id+"F0.wireOp",EDGE,"E8.6.0"),sQuery(id+"F0.wireOp",EDGE,"E8.7.0"),sQuery(id+"F0.wireOp",EDGE,"E8.8.0"),sQuery(id+"F0.wireOp",EDGE,"E8.9.0"),sQuery(id+"F0.wireOp",EDGE,"E8.10.0"),sQuery(id+"F0.wireOp",EDGE,"E8.11.0"),sQuery(id+"F0.wireOp",EDGE,"E8.12.0"),sQuery(id+"F0.wireOp",EDGE,"E8.13.0"),sQuery(id+"F0.wireOp",EDGE,"E8.14.0"),sQuery(id+"F0.wireOp",EDGE,"E8.15.0"),sQuery(id+"F0.wireOp",EDGE,"E8.16.0"),sQuery(id+"F0.wireOp",EDGE,"E8.17.0"),sQuery(id+"F0.wireOp",EDGE,"E8.18.0"),sQuery(id+"F0.wireOp",EDGE,"E8.19.0"),sQuery(id+"F0.wireOp",EDGE,"E8.20.0"),sQuery(id+"F0.wireOp",EDGE,"E8.21.0"),sQuery(id+"F0.wireOp",EDGE,"E8.22.0"),sQuery(id+"F0.wireOp",EDGE,"E8.23.0"),sQuery(id+"F0.wireOp",EDGE,"E8.24.0"),sQuery(id+"F0.wireOp",EDGE,"E8.25.0"),sQuery(id+"F0.wireOp",EDGE,"E8.26.0"),sQuery(id+"F0.wireOp",EDGE,"E8.27.0"),sQuery(id+"F0.wireOp",EDGE,"E8.28.0"),sQuery(id+"F0.wireOp",EDGE,"E8.29.0"),sQuery(id+"F0.wireOp",EDGE,"E8.30.0"),sQuery(id+"F0.wireOp",EDGE,"E8.31.0"),sQuery(id+"F0.wireOp",EDGE,"E8.32.0"),sQuery(id+"F0.wireOp",EDGE,"E8.33.0"),sQuery(id+"F0.wireOp",EDGE,"E8.34.0"),sQuery(id+"F0.wireOp",EDGE,"E8.35.0"),sQuery(id+"F0.wireOp",EDGE,"E8.36.0"),sQuery(id+"F0.wireOp",EDGE,"E8.37.0"),sQuery(id+"F0.wireOp",EDGE,"E8.38.0"),sQuery(id+"F0.wireOp",EDGE,"E8.39.0"),sQuery(id+"F0.wireOp",EDGE,"E8.40.0"),sQuery(id+"F0.wireOp",EDGE,"E8.41.0"),sQuery(id+"F0.wireOp",EDGE,"E8.42.0"),sQuery(id+"F0.wireOp",EDGE,"E8.43.0")])],"isStart":true})],"blendedInto":[makeQuery(id+"F1.opExtrude","CAP_FACE",FACE,{"disambiguationData":[OSD([sQuery(id+"F0.wireOp",EDGE,"E0"),sQuery(id+"F0.wireOp",EDGE,"E1"),sQuery(id+"F0.wireOp",EDGE,"E2"),sQuery(id+"F0.wireOp",EDGE,"E4"),sQuery(id+"F0.wireOp",EDGE,"E5"),sQuery(id+"F0.wireOp",EDGE,"E6.1.1"),sQuery(id+"F0.wireOp",EDGE,"E6.1.2"),sQuery(id+"F0.wireOp",EDGE,"E6.1.3"),sQuery(id+"F0.wireOp",EDGE,"E6.1.4"),sQuery(id+"F0.wireOp",EDGE,"E6.2.1"),sQuery(id+"F0.wireOp",EDGE,"E6.2.2"),sQuery(id+"F0.wireOp",EDGE,"E6.2.3"),sQuery(id+"F0.wireOp",EDGE,"E6.2.4"),sQuery(id+"F0.wireOp",EDGE,"E6.3.1"),sQuery(id+"F0.wireOp",EDGE,"E6.3.2"),sQuery(id+"F0.wireOp",EDGE,"E6.3.3"),sQuery(id+"F0.wireOp",EDGE,"E6.3.4"),sQuery(id+"F0.wireOp",EDGE,"E6.4.1"),sQuery(id+"F0.wireOp",EDGE,"E6.4.2"),sQuery(id+"F0.wireOp",EDGE,"E6.4.3"),sQuery(id+"F0.wireOp",EDGE,"E6.4.4"),sQuery(id+"F0.wireOp",EDGE,"E6.5.1"),sQuery(id+"F0.wireOp",EDGE,"E6.5.2"),sQuery(id+"F0.wireOp",EDGE,"E6.5.3"),sQuery(id+"F0.wireOp",EDGE,"E6.5.4"),sQuery(id+"F0.wireOp",EDGE,"E6.6.1"),sQuery(id+"F0.wireOp",EDGE,"E6.6.2"),sQuery(id+"F0.wireOp",EDGE,"E6.6.3"),sQuery(id+"F0.wireOp",EDGE,"E6.6.4"),sQuery(id+"F0.wireOp",EDGE,"E6.7.1"),sQuery(id+"F0.wireOp",EDGE,"E6.7.2"),sQuery(id+"F0.wireOp",EDGE,"E6.7.3"),sQuery(id+"F0.wireOp",EDGE,"E6.7.4"),sQuery(id+"F0.wireOp",EDGE,"E6.8.1"),sQuery(id+"F0.wireOp",EDGE,"E6.8.2"),sQuery(id+"F0.wireOp",EDGE,"E6.8.3"),sQuery(id+"F0.wireOp",EDGE,"E6.8.4"),sQuery(id+"F0.wireOp",EDGE,"E6.9.1"),sQuery(id+"F0.wireOp",EDGE,"E6.9.2"),sQuery(id+"F0.wireOp",EDGE,"E6.9.3"),sQuery(id+"F0.wireOp",EDGE,"E6.9.4"),sQuery(id+"F0.wireOp",EDGE,"E6.10.1"),sQuery(id+"F0.wireOp",EDGE,"E6.10.2"),sQuery(id+"F0.wireOp",EDGE,"E6.10.3"),sQuery(id+"F0.wireOp",EDGE,"E6.10.4"),sQuery(id+"F0.wireOp",EDGE,"E6.11.1"),sQuery(id+"F0.wireOp",EDGE,"E6.11.2"),sQuery(id+"F0.wireOp",EDGE,"E6.11.3"),sQuery(id+"F0.wireOp",EDGE,"E6.11.4"),sQuery(id+"F0.wireOp",EDGE,"E6.12.1"),sQuery(id+"F0.wireOp",EDGE,"E6.12.2"),sQuery(id+"F0.wireOp",EDGE,"E6.12.3"),sQuery(id+"F0.wireOp",EDGE,"E6.12.4"),sQuery(id+"F0.wireOp",EDGE,"E6.13.1"),sQuery(id+"F0.wireOp",EDGE,"E6.13.2"),sQuery(id+"F0.wireOp",EDGE,"E6.13.3"),sQuery(id+"F0.wireOp",EDGE,"E6.13.4"),sQuery(id+"F0.wireOp",EDGE,"E6.14.1"),sQuery(id+"F0.wireOp",EDGE,"E6.14.2"),sQuery(id+"F0.wireOp",EDGE,"E6.14.3"),sQuery(id+"F0.wireOp",EDGE,"E6.14.4"),sQuery(id+"F0.wireOp",EDGE,"E6.15.1"),sQuery(id+"F0.wireOp",EDGE,"E6.15.2"),sQuery(id+"F0.wireOp",EDGE,"E6.15.3"),sQuery(id+"F0.wireOp",EDGE,"E6.15.4"),sQuery(id+"F0.wireOp",EDGE,"E6.16.1"),sQuery(id+"F0.wireOp",EDGE,"E6.16.2"),sQuery(id+"F0.wireOp",EDGE,"E6.16.3"),sQuery(id+"F0.wireOp",EDGE,"E6.16.4"),sQuery(id+"F0.wireOp",EDGE,"E6.17.1"),sQuery(id+"F0.wireOp",EDGE,"E6.17.2"),sQuery(id+"F0.wireOp",EDGE,"E6.17.3"),sQuery(id+"F0.wireOp",EDGE,"E6.17.4"),sQuery(id+"F0.wireOp",EDGE,"E6.18.1"),sQuery(id+"F0.wireOp",EDGE,"E6.18.2"),sQuery(id+"F0.wireOp",EDGE,"E6.18.3"),sQuery(id+"F0.wireOp",EDGE,"E6.18.4"),sQuery(id+"F0.wireOp",EDGE,"E6.19.1"),sQuery(id+"F0.wireOp",EDGE,"E6.19.2"),sQuery(id+"F0.wireOp",EDGE,"E6.19.3"),sQuery(id+"F0.wireOp",EDGE,"E6.19.4"),sQuery(id+"F0.wireOp",EDGE,"E6.20.1"),sQuery(id+"F0.wireOp",EDGE,"E6.20.2"),sQuery(id+"F0.wireOp",EDGE,"E6.20.3"),sQuery(id+"F0.wireOp",EDGE,"E6.20.4"),sQuery(id+"F0.wireOp",EDGE,"E6.21.1"),sQuery(id+"F0.wireOp",EDGE,"E6.21.2"),sQuery(id+"F0.wireOp",EDGE,"E6.21.3"),sQuery(id+"F0.wireOp",EDGE,"E6.21.4"),sQuery(id+"F0.wireOp",EDGE,"E6.22.1"),sQuery(id+"F0.wireOp",EDGE,"E6.22.2"),sQuery(id+"F0.wireOp",EDGE,"E6.22.3"),sQuery(id+"F0.wireOp",EDGE,"E6.22.4"),sQuery(id+"F0.wireOp",EDGE,"E6.23.1"),sQuery(id+"F0.wireOp",EDGE,"E6.23.2"),sQuery(id+"F0.wireOp",EDGE,"E6.23.3"),sQuery(id+"F0.wireOp",EDGE,"E6.23.4"),sQuery(id+"F0.wireOp",EDGE,"E6.24.1"),sQuery(id+"F0.wireOp",EDGE,"E6.24.2"),sQuery(id+"F0.wireOp",EDGE,"E6.24.3"),sQuery(id+"F0.wireOp",EDGE,"E6.24.4"),sQuery(id+"F0.wireOp",EDGE,"E6.25.1"),sQuery(id+"F0.wireOp",EDGE,"E6.25.2"),sQuery(id+"F0.wireOp",EDGE,"E6.25.3"),sQuery(id+"F0.wireOp",EDGE,"E6.25.4"),sQuery(id+"F0.wireOp",EDGE,"E6.26.1"),sQuery(id+"F0.wireOp",EDGE,"E6.26.2"),sQuery(id+"F0.wireOp",EDGE,"E6.26.3"),sQuery(id+"F0.wireOp",EDGE,"E6.26.4"),sQuery(id+"F0.wireOp",EDGE,"E6.27.1"),sQuery(id+"F0.wireOp",EDGE,"E6.27.2"),sQuery(id+"F0.wireOp",EDGE,"E6.27.3"),sQuery(id+"F0.wireOp",EDGE,"E6.27.4"),sQuery(id+"F0.wireOp",EDGE,"E6.28.1"),sQuery(id+"F0.wireOp",EDGE,"E6.28.2"),sQuery(id+"F0.wireOp",EDGE,"E6.28.3"),sQuery(id+"F0.wireOp",EDGE,"E6.28.4"),sQuery(id+"F0.wireOp",EDGE,"E6.29.1"),sQuery(id+"F0.wireOp",EDGE,"E6.29.2"),sQuery(id+"F0.wireOp",EDGE,"E6.29.3"),sQuery(id+"F0.wireOp",EDGE,"E6.29.4"),subQ1,sQuery(id+"F0.wireOp",EDGE,"E6.30.2"),subQ0,sQuery(id+"F0.wireOp",EDGE,"E6.30.4"),sQuery(id+"F0.wireOp",EDGE,"E6.31.1"),sQuery(id+"F0.wireOp",EDGE,"E6.31.2"),sQuery(id+"F0.wireOp",EDGE,"E6.31.3"),sQuery(id+"F0.wireOp",EDGE,"E6.31.4"),sQuery(id+"F0.wireOp",EDGE,"E6.32.1"),sQuery(id+"F0.wireOp",EDGE,"E6.32.2"),sQuery(id+"F0.wireOp",EDGE,"E6.32.3"),sQuery(id+"F0.wireOp",EDGE,"E6.32.4"),sQuery(id+"F0.wireOp",EDGE,"E6.33.1"),sQuery(id+"F0.wireOp",EDGE,"E6.33.2"),sQuery(id+"F0.wireOp",EDGE,"E6.33.3"),sQuery(id+"F0.wireOp",EDGE,"E6.33.4"),sQuery(id+"F0.wireOp",EDGE,"E6.34.1"),sQuery(id+"F0.wireOp",EDGE,"E6.34.2"),sQuery(id+"F0.wireOp",EDGE,"E6.34.3"),sQuery(id+"F0.wireOp",EDGE,"E6.34.4"),sQuery(id+"F0.wireOp",EDGE,"E6.35.1"),sQuery(id+"F0.wireOp",EDGE,"E6.35.2"),sQuery(id+"F0.wireOp",EDGE,"E6.35.3"),sQuery(id+"F0.wireOp",EDGE,"E6.35.4"),sQuery(id+"F0.wireOp",EDGE,"E6.36.1"),sQuery(id+"F0.wireOp",EDGE,"E6.36.2"),sQuery(id+"F0.wireOp",EDGE,"E6.36.3"),sQuery(id+"F0.wireOp",EDGE,"E6.36.4"),sQuery(id+"F0.wireOp",EDGE,"E6.37.1"),sQuery(id+"F0.wireOp",EDGE,"E6.37.2"),sQuery(id+"F0.wireOp",EDGE,"E6.37.3"),sQuery(id+"F0.wireOp",EDGE,"E6.37.4"),sQuery(id+"F0.wireOp",EDGE,"E6.38.1"),sQuery(id+"F0.wireOp",EDGE,"E6.38.2"),sQuery(id+"F0.wireOp",EDGE,"E6.38.3"),sQuery(id+"F0.wireOp",EDGE,"E6.38.4"),sQuery(id+"F0.wireOp",EDGE,"E6.39.1"),sQuery(id+"F0.wireOp",EDGE,"E6.39.2"),sQuery(id+"F0.wireOp",EDGE,"E6.39.3"),sQuery(id+"F0.wireOp",EDGE,"E6.39.4"),sQuery(id+"F0.wireOp",EDGE,"E6.40.1"),sQuery(id+"F0.wireOp",EDGE,"E6.40.2"),sQuery(id+"F0.wireOp",EDGE,"E6.40.3"),sQuery(id+"F0.wireOp",EDGE,"E6.40.4"),sQuery(id+"F0.wireOp",EDGE,"E6.41.1"),sQuery(id+"F0.wireOp",EDGE,"E6.41.2"),sQuery(id+"F0.wireOp",EDGE,"E6.41.3"),sQuery(id+"F0.wireOp",EDGE,"E6.41.4"),sQuery(id+"F0.wireOp",EDGE,"E6.42.1"),sQuery(id+"F0.wireOp",EDGE,"E6.42.2"),sQuery(id+"F0.wireOp",EDGE,"E6.42.3"),sQuery(id+"F0.wireOp",EDGE,"E6.42.4"),sQuery(id+"F0.wireOp",EDGE,"E6.43.1"),sQuery(id+"F0.wireOp",EDGE,"E6.43.2"),sQuery(id+"F0.wireOp",EDGE,"E6.43.3"),sQuery(id+"F0.wireOp",EDGE,"E6.43.4"),sQuery(id+"F0.wireOp",EDGE,"E7"),sQuery(id+"F0.wireOp",EDGE,"E8.1.0"),sQuery(id+"F0.wireOp",EDGE,"E8.2.0"),sQuery(id+"F0.wireOp",EDGE,"E8.3.0"),sQuery(id+"F0.wireOp",EDGE,"E8.4.0"),sQuery(id+"F0.wireOp",EDGE,"E8.5.0"),sQuery(id+"F0.wireOp",EDGE,"E8.6.0"),sQuery(id+"F0.wireOp",EDGE,"E8.7.0"),sQuery(id+"F0.wireOp",EDGE,"E8.8.0"),sQuery(id+"F0.wireOp",EDGE,"E8.9.0"),sQuery(id+"F0.wireOp",EDGE,"E8.10.0"),sQuery(id+"F0.wireOp",EDGE,"E8.11.0"),sQuery(id+"F0.wireOp",EDGE,"E8.12.0"),sQuery(id+"F0.wireOp",EDGE,"E8.13.0"),sQuery(id+"F0.wireOp",EDGE,"E8.14.0"),sQuery(id+"F0.wireOp",EDGE,"E8.15.0"),sQuery(id+"F0.wireOp",EDGE,"E8.16.0"),sQuery(id+"F0.wireOp",EDGE,"E8.17.0"),sQuery(id+"F0.wireOp",EDGE,"E8.18.0"),sQuery(id+"F0.wireOp",EDGE,"E8.19.0"),sQuery(id+"F0.wireOp",EDGE,"E8.20.0"),sQuery(id+"F0.wireOp",EDGE,"E8.21.0"),sQuery(id+"F0.wireOp",EDGE,"E8.22.0"),sQuery(id+"F0.wireOp",EDGE,"E8.23.0"),sQuery(id+"F0.wireOp",EDGE,"E8.24.0"),sQuery(id+"F0.wireOp",EDGE,"E8.25.0"),sQuery(id+"F0.wireOp",EDGE,"E8.26.0"),sQuery(id+"F0.wireOp",EDGE,"E8.27.0"),sQuery(id+"F0.wireOp",EDGE,"E8.28.0"),sQuery(id+"F0.wireOp",EDGE,"E8.29.0"),sQuery(id+"F0.wireOp",EDGE,"E8.30.0"),sQuery(id+"F0.wireOp",EDGE,"E8.31.0"),sQuery(id+"F0.wireOp",EDGE,"E8.32.0"),sQuery(id+"F0.wireOp",EDGE,"E8.33.0"),sQuery(id+"F0.wireOp",EDGE,"E8.34.0"),sQuery(id+"F0.wireOp",EDGE,"E8.35.0"),sQuery(id+"F0.wireOp",EDGE,"E8.36.0"),sQuery(id+"F0.wireOp",EDGE,"E8.37.0"),sQuery(id+"F0.wireOp",EDGE,"E8.38.0"),sQuery(id+"F0.wireOp",EDGE,"E8.39.0"),sQuery(id+"F0.wireOp",EDGE,"E8.40.0"),sQuery(id+"F0.wireOp",EDGE,"E8.41.0"),sQuery(id+"F0.wireOp",EDGE,"E8.42.0"),sQuery(id+"F0.wireOp",EDGE,"E8.43.0")])],"isStart":true})]});}
            var Q37;
            {var subQ0=sQuery(id+"F0.wireOp",EDGE,"E6.32.3");var subQ1=sQuery(id+"F0.wireOp",EDGE,"E6.32.1");Q37=makeQuery(id+"F2.opFillet","BLEND_EDGE",EDGE,{"blendedFrom":[makeQuery(id+"F1.opExtrude","SWEPT_EDGE",EDGE,{"disambiguationData":[OSD([sQuery(id+"F0.wireOp",EDGE,"E6.32.0"),subQ1,subQ0])]}),makeQuery(id+"F1.opExtrude","CAP_FACE",FACE,{"disambiguationData":[OSD([sQuery(id+"F0.wireOp",EDGE,"E0"),sQuery(id+"F0.wireOp",EDGE,"E1"),sQuery(id+"F0.wireOp",EDGE,"E2"),sQuery(id+"F0.wireOp",EDGE,"E4"),sQuery(id+"F0.wireOp",EDGE,"E5"),sQuery(id+"F0.wireOp",EDGE,"E6.1.1"),sQuery(id+"F0.wireOp",EDGE,"E6.1.2"),sQuery(id+"F0.wireOp",EDGE,"E6.1.3"),sQuery(id+"F0.wireOp",EDGE,"E6.1.4"),sQuery(id+"F0.wireOp",EDGE,"E6.2.1"),sQuery(id+"F0.wireOp",EDGE,"E6.2.2"),sQuery(id+"F0.wireOp",EDGE,"E6.2.3"),sQuery(id+"F0.wireOp",EDGE,"E6.2.4"),sQuery(id+"F0.wireOp",EDGE,"E6.3.1"),sQuery(id+"F0.wireOp",EDGE,"E6.3.2"),sQuery(id+"F0.wireOp",EDGE,"E6.3.3"),sQuery(id+"F0.wireOp",EDGE,"E6.3.4"),sQuery(id+"F0.wireOp",EDGE,"E6.4.1"),sQuery(id+"F0.wireOp",EDGE,"E6.4.2"),sQuery(id+"F0.wireOp",EDGE,"E6.4.3"),sQuery(id+"F0.wireOp",EDGE,"E6.4.4"),sQuery(id+"F0.wireOp",EDGE,"E6.5.1"),sQuery(id+"F0.wireOp",EDGE,"E6.5.2"),sQuery(id+"F0.wireOp",EDGE,"E6.5.3"),sQuery(id+"F0.wireOp",EDGE,"E6.5.4"),sQuery(id+"F0.wireOp",EDGE,"E6.6.1"),sQuery(id+"F0.wireOp",EDGE,"E6.6.2"),sQuery(id+"F0.wireOp",EDGE,"E6.6.3"),sQuery(id+"F0.wireOp",EDGE,"E6.6.4"),sQuery(id+"F0.wireOp",EDGE,"E6.7.1"),sQuery(id+"F0.wireOp",EDGE,"E6.7.2"),sQuery(id+"F0.wireOp",EDGE,"E6.7.3"),sQuery(id+"F0.wireOp",EDGE,"E6.7.4"),sQuery(id+"F0.wireOp",EDGE,"E6.8.1"),sQuery(id+"F0.wireOp",EDGE,"E6.8.2"),sQuery(id+"F0.wireOp",EDGE,"E6.8.3"),sQuery(id+"F0.wireOp",EDGE,"E6.8.4"),sQuery(id+"F0.wireOp",EDGE,"E6.9.1"),sQuery(id+"F0.wireOp",EDGE,"E6.9.2"),sQuery(id+"F0.wireOp",EDGE,"E6.9.3"),sQuery(id+"F0.wireOp",EDGE,"E6.9.4"),sQuery(id+"F0.wireOp",EDGE,"E6.10.1"),sQuery(id+"F0.wireOp",EDGE,"E6.10.2"),sQuery(id+"F0.wireOp",EDGE,"E6.10.3"),sQuery(id+"F0.wireOp",EDGE,"E6.10.4"),sQuery(id+"F0.wireOp",EDGE,"E6.11.1"),sQuery(id+"F0.wireOp",EDGE,"E6.11.2"),sQuery(id+"F0.wireOp",EDGE,"E6.11.3"),sQuery(id+"F0.wireOp",EDGE,"E6.11.4"),sQuery(id+"F0.wireOp",EDGE,"E6.12.1"),sQuery(id+"F0.wireOp",EDGE,"E6.12.2"),sQuery(id+"F0.wireOp",EDGE,"E6.12.3"),sQuery(id+"F0.wireOp",EDGE,"E6.12.4"),sQuery(id+"F0.wireOp",EDGE,"E6.13.1"),sQuery(id+"F0.wireOp",EDGE,"E6.13.2"),sQuery(id+"F0.wireOp",EDGE,"E6.13.3"),sQuery(id+"F0.wireOp",EDGE,"E6.13.4"),sQuery(id+"F0.wireOp",EDGE,"E6.14.1"),sQuery(id+"F0.wireOp",EDGE,"E6.14.2"),sQuery(id+"F0.wireOp",EDGE,"E6.14.3"),sQuery(id+"F0.wireOp",EDGE,"E6.14.4"),sQuery(id+"F0.wireOp",EDGE,"E6.15.1"),sQuery(id+"F0.wireOp",EDGE,"E6.15.2"),sQuery(id+"F0.wireOp",EDGE,"E6.15.3"),sQuery(id+"F0.wireOp",EDGE,"E6.15.4"),sQuery(id+"F0.wireOp",EDGE,"E6.16.1"),sQuery(id+"F0.wireOp",EDGE,"E6.16.2"),sQuery(id+"F0.wireOp",EDGE,"E6.16.3"),sQuery(id+"F0.wireOp",EDGE,"E6.16.4"),sQuery(id+"F0.wireOp",EDGE,"E6.17.1"),sQuery(id+"F0.wireOp",EDGE,"E6.17.2"),sQuery(id+"F0.wireOp",EDGE,"E6.17.3"),sQuery(id+"F0.wireOp",EDGE,"E6.17.4"),sQuery(id+"F0.wireOp",EDGE,"E6.18.1"),sQuery(id+"F0.wireOp",EDGE,"E6.18.2"),sQuery(id+"F0.wireOp",EDGE,"E6.18.3"),sQuery(id+"F0.wireOp",EDGE,"E6.18.4"),sQuery(id+"F0.wireOp",EDGE,"E6.19.1"),sQuery(id+"F0.wireOp",EDGE,"E6.19.2"),sQuery(id+"F0.wireOp",EDGE,"E6.19.3"),sQuery(id+"F0.wireOp",EDGE,"E6.19.4"),sQuery(id+"F0.wireOp",EDGE,"E6.20.1"),sQuery(id+"F0.wireOp",EDGE,"E6.20.2"),sQuery(id+"F0.wireOp",EDGE,"E6.20.3"),sQuery(id+"F0.wireOp",EDGE,"E6.20.4"),sQuery(id+"F0.wireOp",EDGE,"E6.21.1"),sQuery(id+"F0.wireOp",EDGE,"E6.21.2"),sQuery(id+"F0.wireOp",EDGE,"E6.21.3"),sQuery(id+"F0.wireOp",EDGE,"E6.21.4"),sQuery(id+"F0.wireOp",EDGE,"E6.22.1"),sQuery(id+"F0.wireOp",EDGE,"E6.22.2"),sQuery(id+"F0.wireOp",EDGE,"E6.22.3"),sQuery(id+"F0.wireOp",EDGE,"E6.22.4"),sQuery(id+"F0.wireOp",EDGE,"E6.23.1"),sQuery(id+"F0.wireOp",EDGE,"E6.23.2"),sQuery(id+"F0.wireOp",EDGE,"E6.23.3"),sQuery(id+"F0.wireOp",EDGE,"E6.23.4"),sQuery(id+"F0.wireOp",EDGE,"E6.24.1"),sQuery(id+"F0.wireOp",EDGE,"E6.24.2"),sQuery(id+"F0.wireOp",EDGE,"E6.24.3"),sQuery(id+"F0.wireOp",EDGE,"E6.24.4"),sQuery(id+"F0.wireOp",EDGE,"E6.25.1"),sQuery(id+"F0.wireOp",EDGE,"E6.25.2"),sQuery(id+"F0.wireOp",EDGE,"E6.25.3"),sQuery(id+"F0.wireOp",EDGE,"E6.25.4"),sQuery(id+"F0.wireOp",EDGE,"E6.26.1"),sQuery(id+"F0.wireOp",EDGE,"E6.26.2"),sQuery(id+"F0.wireOp",EDGE,"E6.26.3"),sQuery(id+"F0.wireOp",EDGE,"E6.26.4"),sQuery(id+"F0.wireOp",EDGE,"E6.27.1"),sQuery(id+"F0.wireOp",EDGE,"E6.27.2"),sQuery(id+"F0.wireOp",EDGE,"E6.27.3"),sQuery(id+"F0.wireOp",EDGE,"E6.27.4"),sQuery(id+"F0.wireOp",EDGE,"E6.28.1"),sQuery(id+"F0.wireOp",EDGE,"E6.28.2"),sQuery(id+"F0.wireOp",EDGE,"E6.28.3"),sQuery(id+"F0.wireOp",EDGE,"E6.28.4"),sQuery(id+"F0.wireOp",EDGE,"E6.29.1"),sQuery(id+"F0.wireOp",EDGE,"E6.29.2"),sQuery(id+"F0.wireOp",EDGE,"E6.29.3"),sQuery(id+"F0.wireOp",EDGE,"E6.29.4"),sQuery(id+"F0.wireOp",EDGE,"E6.30.1"),sQuery(id+"F0.wireOp",EDGE,"E6.30.2"),sQuery(id+"F0.wireOp",EDGE,"E6.30.3"),sQuery(id+"F0.wireOp",EDGE,"E6.30.4"),sQuery(id+"F0.wireOp",EDGE,"E6.31.1"),sQuery(id+"F0.wireOp",EDGE,"E6.31.2"),sQuery(id+"F0.wireOp",EDGE,"E6.31.3"),sQuery(id+"F0.wireOp",EDGE,"E6.31.4"),subQ1,sQuery(id+"F0.wireOp",EDGE,"E6.32.2"),subQ0,sQuery(id+"F0.wireOp",EDGE,"E6.32.4"),sQuery(id+"F0.wireOp",EDGE,"E6.33.1"),sQuery(id+"F0.wireOp",EDGE,"E6.33.2"),sQuery(id+"F0.wireOp",EDGE,"E6.33.3"),sQuery(id+"F0.wireOp",EDGE,"E6.33.4"),sQuery(id+"F0.wireOp",EDGE,"E6.34.1"),sQuery(id+"F0.wireOp",EDGE,"E6.34.2"),sQuery(id+"F0.wireOp",EDGE,"E6.34.3"),sQuery(id+"F0.wireOp",EDGE,"E6.34.4"),sQuery(id+"F0.wireOp",EDGE,"E6.35.1"),sQuery(id+"F0.wireOp",EDGE,"E6.35.2"),sQuery(id+"F0.wireOp",EDGE,"E6.35.3"),sQuery(id+"F0.wireOp",EDGE,"E6.35.4"),sQuery(id+"F0.wireOp",EDGE,"E6.36.1"),sQuery(id+"F0.wireOp",EDGE,"E6.36.2"),sQuery(id+"F0.wireOp",EDGE,"E6.36.3"),sQuery(id+"F0.wireOp",EDGE,"E6.36.4"),sQuery(id+"F0.wireOp",EDGE,"E6.37.1"),sQuery(id+"F0.wireOp",EDGE,"E6.37.2"),sQuery(id+"F0.wireOp",EDGE,"E6.37.3"),sQuery(id+"F0.wireOp",EDGE,"E6.37.4"),sQuery(id+"F0.wireOp",EDGE,"E6.38.1"),sQuery(id+"F0.wireOp",EDGE,"E6.38.2"),sQuery(id+"F0.wireOp",EDGE,"E6.38.3"),sQuery(id+"F0.wireOp",EDGE,"E6.38.4"),sQuery(id+"F0.wireOp",EDGE,"E6.39.1"),sQuery(id+"F0.wireOp",EDGE,"E6.39.2"),sQuery(id+"F0.wireOp",EDGE,"E6.39.3"),sQuery(id+"F0.wireOp",EDGE,"E6.39.4"),sQuery(id+"F0.wireOp",EDGE,"E6.40.1"),sQuery(id+"F0.wireOp",EDGE,"E6.40.2"),sQuery(id+"F0.wireOp",EDGE,"E6.40.3"),sQuery(id+"F0.wireOp",EDGE,"E6.40.4"),sQuery(id+"F0.wireOp",EDGE,"E6.41.1"),sQuery(id+"F0.wireOp",EDGE,"E6.41.2"),sQuery(id+"F0.wireOp",EDGE,"E6.41.3"),sQuery(id+"F0.wireOp",EDGE,"E6.41.4"),sQuery(id+"F0.wireOp",EDGE,"E6.42.1"),sQuery(id+"F0.wireOp",EDGE,"E6.42.2"),sQuery(id+"F0.wireOp",EDGE,"E6.42.3"),sQuery(id+"F0.wireOp",EDGE,"E6.42.4"),sQuery(id+"F0.wireOp",EDGE,"E6.43.1"),sQuery(id+"F0.wireOp",EDGE,"E6.43.2"),sQuery(id+"F0.wireOp",EDGE,"E6.43.3"),sQuery(id+"F0.wireOp",EDGE,"E6.43.4"),sQuery(id+"F0.wireOp",EDGE,"E7"),sQuery(id+"F0.wireOp",EDGE,"E8.1.0"),sQuery(id+"F0.wireOp",EDGE,"E8.2.0"),sQuery(id+"F0.wireOp",EDGE,"E8.3.0"),sQuery(id+"F0.wireOp",EDGE,"E8.4.0"),sQuery(id+"F0.wireOp",EDGE,"E8.5.0"),sQuery(id+"F0.wireOp",EDGE,"E8.6.0"),sQuery(id+"F0.wireOp",EDGE,"E8.7.0"),sQuery(id+"F0.wireOp",EDGE,"E8.8.0"),sQuery(id+"F0.wireOp",EDGE,"E8.9.0"),sQuery(id+"F0.wireOp",EDGE,"E8.10.0"),sQuery(id+"F0.wireOp",EDGE,"E8.11.0"),sQuery(id+"F0.wireOp",EDGE,"E8.12.0"),sQuery(id+"F0.wireOp",EDGE,"E8.13.0"),sQuery(id+"F0.wireOp",EDGE,"E8.14.0"),sQuery(id+"F0.wireOp",EDGE,"E8.15.0"),sQuery(id+"F0.wireOp",EDGE,"E8.16.0"),sQuery(id+"F0.wireOp",EDGE,"E8.17.0"),sQuery(id+"F0.wireOp",EDGE,"E8.18.0"),sQuery(id+"F0.wireOp",EDGE,"E8.19.0"),sQuery(id+"F0.wireOp",EDGE,"E8.20.0"),sQuery(id+"F0.wireOp",EDGE,"E8.21.0"),sQuery(id+"F0.wireOp",EDGE,"E8.22.0"),sQuery(id+"F0.wireOp",EDGE,"E8.23.0"),sQuery(id+"F0.wireOp",EDGE,"E8.24.0"),sQuery(id+"F0.wireOp",EDGE,"E8.25.0"),sQuery(id+"F0.wireOp",EDGE,"E8.26.0"),sQuery(id+"F0.wireOp",EDGE,"E8.27.0"),sQuery(id+"F0.wireOp",EDGE,"E8.28.0"),sQuery(id+"F0.wireOp",EDGE,"E8.29.0"),sQuery(id+"F0.wireOp",EDGE,"E8.30.0"),sQuery(id+"F0.wireOp",EDGE,"E8.31.0"),sQuery(id+"F0.wireOp",EDGE,"E8.32.0"),sQuery(id+"F0.wireOp",EDGE,"E8.33.0"),sQuery(id+"F0.wireOp",EDGE,"E8.34.0"),sQuery(id+"F0.wireOp",EDGE,"E8.35.0"),sQuery(id+"F0.wireOp",EDGE,"E8.36.0"),sQuery(id+"F0.wireOp",EDGE,"E8.37.0"),sQuery(id+"F0.wireOp",EDGE,"E8.38.0"),sQuery(id+"F0.wireOp",EDGE,"E8.39.0"),sQuery(id+"F0.wireOp",EDGE,"E8.40.0"),sQuery(id+"F0.wireOp",EDGE,"E8.41.0"),sQuery(id+"F0.wireOp",EDGE,"E8.42.0"),sQuery(id+"F0.wireOp",EDGE,"E8.43.0")])],"isStart":true})],"blendedInto":[makeQuery(id+"F1.opExtrude","CAP_FACE",FACE,{"disambiguationData":[OSD([sQuery(id+"F0.wireOp",EDGE,"E0"),sQuery(id+"F0.wireOp",EDGE,"E1"),sQuery(id+"F0.wireOp",EDGE,"E2"),sQuery(id+"F0.wireOp",EDGE,"E4"),sQuery(id+"F0.wireOp",EDGE,"E5"),sQuery(id+"F0.wireOp",EDGE,"E6.1.1"),sQuery(id+"F0.wireOp",EDGE,"E6.1.2"),sQuery(id+"F0.wireOp",EDGE,"E6.1.3"),sQuery(id+"F0.wireOp",EDGE,"E6.1.4"),sQuery(id+"F0.wireOp",EDGE,"E6.2.1"),sQuery(id+"F0.wireOp",EDGE,"E6.2.2"),sQuery(id+"F0.wireOp",EDGE,"E6.2.3"),sQuery(id+"F0.wireOp",EDGE,"E6.2.4"),sQuery(id+"F0.wireOp",EDGE,"E6.3.1"),sQuery(id+"F0.wireOp",EDGE,"E6.3.2"),sQuery(id+"F0.wireOp",EDGE,"E6.3.3"),sQuery(id+"F0.wireOp",EDGE,"E6.3.4"),sQuery(id+"F0.wireOp",EDGE,"E6.4.1"),sQuery(id+"F0.wireOp",EDGE,"E6.4.2"),sQuery(id+"F0.wireOp",EDGE,"E6.4.3"),sQuery(id+"F0.wireOp",EDGE,"E6.4.4"),sQuery(id+"F0.wireOp",EDGE,"E6.5.1"),sQuery(id+"F0.wireOp",EDGE,"E6.5.2"),sQuery(id+"F0.wireOp",EDGE,"E6.5.3"),sQuery(id+"F0.wireOp",EDGE,"E6.5.4"),sQuery(id+"F0.wireOp",EDGE,"E6.6.1"),sQuery(id+"F0.wireOp",EDGE,"E6.6.2"),sQuery(id+"F0.wireOp",EDGE,"E6.6.3"),sQuery(id+"F0.wireOp",EDGE,"E6.6.4"),sQuery(id+"F0.wireOp",EDGE,"E6.7.1"),sQuery(id+"F0.wireOp",EDGE,"E6.7.2"),sQuery(id+"F0.wireOp",EDGE,"E6.7.3"),sQuery(id+"F0.wireOp",EDGE,"E6.7.4"),sQuery(id+"F0.wireOp",EDGE,"E6.8.1"),sQuery(id+"F0.wireOp",EDGE,"E6.8.2"),sQuery(id+"F0.wireOp",EDGE,"E6.8.3"),sQuery(id+"F0.wireOp",EDGE,"E6.8.4"),sQuery(id+"F0.wireOp",EDGE,"E6.9.1"),sQuery(id+"F0.wireOp",EDGE,"E6.9.2"),sQuery(id+"F0.wireOp",EDGE,"E6.9.3"),sQuery(id+"F0.wireOp",EDGE,"E6.9.4"),sQuery(id+"F0.wireOp",EDGE,"E6.10.1"),sQuery(id+"F0.wireOp",EDGE,"E6.10.2"),sQuery(id+"F0.wireOp",EDGE,"E6.10.3"),sQuery(id+"F0.wireOp",EDGE,"E6.10.4"),sQuery(id+"F0.wireOp",EDGE,"E6.11.1"),sQuery(id+"F0.wireOp",EDGE,"E6.11.2"),sQuery(id+"F0.wireOp",EDGE,"E6.11.3"),sQuery(id+"F0.wireOp",EDGE,"E6.11.4"),sQuery(id+"F0.wireOp",EDGE,"E6.12.1"),sQuery(id+"F0.wireOp",EDGE,"E6.12.2"),sQuery(id+"F0.wireOp",EDGE,"E6.12.3"),sQuery(id+"F0.wireOp",EDGE,"E6.12.4"),sQuery(id+"F0.wireOp",EDGE,"E6.13.1"),sQuery(id+"F0.wireOp",EDGE,"E6.13.2"),sQuery(id+"F0.wireOp",EDGE,"E6.13.3"),sQuery(id+"F0.wireOp",EDGE,"E6.13.4"),sQuery(id+"F0.wireOp",EDGE,"E6.14.1"),sQuery(id+"F0.wireOp",EDGE,"E6.14.2"),sQuery(id+"F0.wireOp",EDGE,"E6.14.3"),sQuery(id+"F0.wireOp",EDGE,"E6.14.4"),sQuery(id+"F0.wireOp",EDGE,"E6.15.1"),sQuery(id+"F0.wireOp",EDGE,"E6.15.2"),sQuery(id+"F0.wireOp",EDGE,"E6.15.3"),sQuery(id+"F0.wireOp",EDGE,"E6.15.4"),sQuery(id+"F0.wireOp",EDGE,"E6.16.1"),sQuery(id+"F0.wireOp",EDGE,"E6.16.2"),sQuery(id+"F0.wireOp",EDGE,"E6.16.3"),sQuery(id+"F0.wireOp",EDGE,"E6.16.4"),sQuery(id+"F0.wireOp",EDGE,"E6.17.1"),sQuery(id+"F0.wireOp",EDGE,"E6.17.2"),sQuery(id+"F0.wireOp",EDGE,"E6.17.3"),sQuery(id+"F0.wireOp",EDGE,"E6.17.4"),sQuery(id+"F0.wireOp",EDGE,"E6.18.1"),sQuery(id+"F0.wireOp",EDGE,"E6.18.2"),sQuery(id+"F0.wireOp",EDGE,"E6.18.3"),sQuery(id+"F0.wireOp",EDGE,"E6.18.4"),sQuery(id+"F0.wireOp",EDGE,"E6.19.1"),sQuery(id+"F0.wireOp",EDGE,"E6.19.2"),sQuery(id+"F0.wireOp",EDGE,"E6.19.3"),sQuery(id+"F0.wireOp",EDGE,"E6.19.4"),sQuery(id+"F0.wireOp",EDGE,"E6.20.1"),sQuery(id+"F0.wireOp",EDGE,"E6.20.2"),sQuery(id+"F0.wireOp",EDGE,"E6.20.3"),sQuery(id+"F0.wireOp",EDGE,"E6.20.4"),sQuery(id+"F0.wireOp",EDGE,"E6.21.1"),sQuery(id+"F0.wireOp",EDGE,"E6.21.2"),sQuery(id+"F0.wireOp",EDGE,"E6.21.3"),sQuery(id+"F0.wireOp",EDGE,"E6.21.4"),sQuery(id+"F0.wireOp",EDGE,"E6.22.1"),sQuery(id+"F0.wireOp",EDGE,"E6.22.2"),sQuery(id+"F0.wireOp",EDGE,"E6.22.3"),sQuery(id+"F0.wireOp",EDGE,"E6.22.4"),sQuery(id+"F0.wireOp",EDGE,"E6.23.1"),sQuery(id+"F0.wireOp",EDGE,"E6.23.2"),sQuery(id+"F0.wireOp",EDGE,"E6.23.3"),sQuery(id+"F0.wireOp",EDGE,"E6.23.4"),sQuery(id+"F0.wireOp",EDGE,"E6.24.1"),sQuery(id+"F0.wireOp",EDGE,"E6.24.2"),sQuery(id+"F0.wireOp",EDGE,"E6.24.3"),sQuery(id+"F0.wireOp",EDGE,"E6.24.4"),sQuery(id+"F0.wireOp",EDGE,"E6.25.1"),sQuery(id+"F0.wireOp",EDGE,"E6.25.2"),sQuery(id+"F0.wireOp",EDGE,"E6.25.3"),sQuery(id+"F0.wireOp",EDGE,"E6.25.4"),sQuery(id+"F0.wireOp",EDGE,"E6.26.1"),sQuery(id+"F0.wireOp",EDGE,"E6.26.2"),sQuery(id+"F0.wireOp",EDGE,"E6.26.3"),sQuery(id+"F0.wireOp",EDGE,"E6.26.4"),sQuery(id+"F0.wireOp",EDGE,"E6.27.1"),sQuery(id+"F0.wireOp",EDGE,"E6.27.2"),sQuery(id+"F0.wireOp",EDGE,"E6.27.3"),sQuery(id+"F0.wireOp",EDGE,"E6.27.4"),sQuery(id+"F0.wireOp",EDGE,"E6.28.1"),sQuery(id+"F0.wireOp",EDGE,"E6.28.2"),sQuery(id+"F0.wireOp",EDGE,"E6.28.3"),sQuery(id+"F0.wireOp",EDGE,"E6.28.4"),sQuery(id+"F0.wireOp",EDGE,"E6.29.1"),sQuery(id+"F0.wireOp",EDGE,"E6.29.2"),sQuery(id+"F0.wireOp",EDGE,"E6.29.3"),sQuery(id+"F0.wireOp",EDGE,"E6.29.4"),sQuery(id+"F0.wireOp",EDGE,"E6.30.1"),sQuery(id+"F0.wireOp",EDGE,"E6.30.2"),sQuery(id+"F0.wireOp",EDGE,"E6.30.3"),sQuery(id+"F0.wireOp",EDGE,"E6.30.4"),sQuery(id+"F0.wireOp",EDGE,"E6.31.1"),sQuery(id+"F0.wireOp",EDGE,"E6.31.2"),sQuery(id+"F0.wireOp",EDGE,"E6.31.3"),sQuery(id+"F0.wireOp",EDGE,"E6.31.4"),subQ1,sQuery(id+"F0.wireOp",EDGE,"E6.32.2"),subQ0,sQuery(id+"F0.wireOp",EDGE,"E6.32.4"),sQuery(id+"F0.wireOp",EDGE,"E6.33.1"),sQuery(id+"F0.wireOp",EDGE,"E6.33.2"),sQuery(id+"F0.wireOp",EDGE,"E6.33.3"),sQuery(id+"F0.wireOp",EDGE,"E6.33.4"),sQuery(id+"F0.wireOp",EDGE,"E6.34.1"),sQuery(id+"F0.wireOp",EDGE,"E6.34.2"),sQuery(id+"F0.wireOp",EDGE,"E6.34.3"),sQuery(id+"F0.wireOp",EDGE,"E6.34.4"),sQuery(id+"F0.wireOp",EDGE,"E6.35.1"),sQuery(id+"F0.wireOp",EDGE,"E6.35.2"),sQuery(id+"F0.wireOp",EDGE,"E6.35.3"),sQuery(id+"F0.wireOp",EDGE,"E6.35.4"),sQuery(id+"F0.wireOp",EDGE,"E6.36.1"),sQuery(id+"F0.wireOp",EDGE,"E6.36.2"),sQuery(id+"F0.wireOp",EDGE,"E6.36.3"),sQuery(id+"F0.wireOp",EDGE,"E6.36.4"),sQuery(id+"F0.wireOp",EDGE,"E6.37.1"),sQuery(id+"F0.wireOp",EDGE,"E6.37.2"),sQuery(id+"F0.wireOp",EDGE,"E6.37.3"),sQuery(id+"F0.wireOp",EDGE,"E6.37.4"),sQuery(id+"F0.wireOp",EDGE,"E6.38.1"),sQuery(id+"F0.wireOp",EDGE,"E6.38.2"),sQuery(id+"F0.wireOp",EDGE,"E6.38.3"),sQuery(id+"F0.wireOp",EDGE,"E6.38.4"),sQuery(id+"F0.wireOp",EDGE,"E6.39.1"),sQuery(id+"F0.wireOp",EDGE,"E6.39.2"),sQuery(id+"F0.wireOp",EDGE,"E6.39.3"),sQuery(id+"F0.wireOp",EDGE,"E6.39.4"),sQuery(id+"F0.wireOp",EDGE,"E6.40.1"),sQuery(id+"F0.wireOp",EDGE,"E6.40.2"),sQuery(id+"F0.wireOp",EDGE,"E6.40.3"),sQuery(id+"F0.wireOp",EDGE,"E6.40.4"),sQuery(id+"F0.wireOp",EDGE,"E6.41.1"),sQuery(id+"F0.wireOp",EDGE,"E6.41.2"),sQuery(id+"F0.wireOp",EDGE,"E6.41.3"),sQuery(id+"F0.wireOp",EDGE,"E6.41.4"),sQuery(id+"F0.wireOp",EDGE,"E6.42.1"),sQuery(id+"F0.wireOp",EDGE,"E6.42.2"),sQuery(id+"F0.wireOp",EDGE,"E6.42.3"),sQuery(id+"F0.wireOp",EDGE,"E6.42.4"),sQuery(id+"F0.wireOp",EDGE,"E6.43.1"),sQuery(id+"F0.wireOp",EDGE,"E6.43.2"),sQuery(id+"F0.wireOp",EDGE,"E6.43.3"),sQuery(id+"F0.wireOp",EDGE,"E6.43.4"),sQuery(id+"F0.wireOp",EDGE,"E7"),sQuery(id+"F0.wireOp",EDGE,"E8.1.0"),sQuery(id+"F0.wireOp",EDGE,"E8.2.0"),sQuery(id+"F0.wireOp",EDGE,"E8.3.0"),sQuery(id+"F0.wireOp",EDGE,"E8.4.0"),sQuery(id+"F0.wireOp",EDGE,"E8.5.0"),sQuery(id+"F0.wireOp",EDGE,"E8.6.0"),sQuery(id+"F0.wireOp",EDGE,"E8.7.0"),sQuery(id+"F0.wireOp",EDGE,"E8.8.0"),sQuery(id+"F0.wireOp",EDGE,"E8.9.0"),sQuery(id+"F0.wireOp",EDGE,"E8.10.0"),sQuery(id+"F0.wireOp",EDGE,"E8.11.0"),sQuery(id+"F0.wireOp",EDGE,"E8.12.0"),sQuery(id+"F0.wireOp",EDGE,"E8.13.0"),sQuery(id+"F0.wireOp",EDGE,"E8.14.0"),sQuery(id+"F0.wireOp",EDGE,"E8.15.0"),sQuery(id+"F0.wireOp",EDGE,"E8.16.0"),sQuery(id+"F0.wireOp",EDGE,"E8.17.0"),sQuery(id+"F0.wireOp",EDGE,"E8.18.0"),sQuery(id+"F0.wireOp",EDGE,"E8.19.0"),sQuery(id+"F0.wireOp",EDGE,"E8.20.0"),sQuery(id+"F0.wireOp",EDGE,"E8.21.0"),sQuery(id+"F0.wireOp",EDGE,"E8.22.0"),sQuery(id+"F0.wireOp",EDGE,"E8.23.0"),sQuery(id+"F0.wireOp",EDGE,"E8.24.0"),sQuery(id+"F0.wireOp",EDGE,"E8.25.0"),sQuery(id+"F0.wireOp",EDGE,"E8.26.0"),sQuery(id+"F0.wireOp",EDGE,"E8.27.0"),sQuery(id+"F0.wireOp",EDGE,"E8.28.0"),sQuery(id+"F0.wireOp",EDGE,"E8.29.0"),sQuery(id+"F0.wireOp",EDGE,"E8.30.0"),sQuery(id+"F0.wireOp",EDGE,"E8.31.0"),sQuery(id+"F0.wireOp",EDGE,"E8.32.0"),sQuery(id+"F0.wireOp",EDGE,"E8.33.0"),sQuery(id+"F0.wireOp",EDGE,"E8.34.0"),sQuery(id+"F0.wireOp",EDGE,"E8.35.0"),sQuery(id+"F0.wireOp",EDGE,"E8.36.0"),sQuery(id+"F0.wireOp",EDGE,"E8.37.0"),sQuery(id+"F0.wireOp",EDGE,"E8.38.0"),sQuery(id+"F0.wireOp",EDGE,"E8.39.0"),sQuery(id+"F0.wireOp",EDGE,"E8.40.0"),sQuery(id+"F0.wireOp",EDGE,"E8.41.0"),sQuery(id+"F0.wireOp",EDGE,"E8.42.0"),sQuery(id+"F0.wireOp",EDGE,"E8.43.0")])],"isStart":true})]});}
            var Q38;
            {var subQ0=sQuery(id+"F0.wireOp",EDGE,"E6.34.3");var subQ1=sQuery(id+"F0.wireOp",EDGE,"E6.34.1");Q38=makeQuery(id+"F2.opFillet","BLEND_EDGE",EDGE,{"blendedFrom":[makeQuery(id+"F1.opExtrude","SWEPT_EDGE",EDGE,{"disambiguationData":[OSD([sQuery(id+"F0.wireOp",EDGE,"E6.34.0"),subQ1,subQ0])]}),makeQuery(id+"F1.opExtrude","CAP_FACE",FACE,{"disambiguationData":[OSD([sQuery(id+"F0.wireOp",EDGE,"E0"),sQuery(id+"F0.wireOp",EDGE,"E1"),sQuery(id+"F0.wireOp",EDGE,"E2"),sQuery(id+"F0.wireOp",EDGE,"E4"),sQuery(id+"F0.wireOp",EDGE,"E5"),sQuery(id+"F0.wireOp",EDGE,"E6.1.1"),sQuery(id+"F0.wireOp",EDGE,"E6.1.2"),sQuery(id+"F0.wireOp",EDGE,"E6.1.3"),sQuery(id+"F0.wireOp",EDGE,"E6.1.4"),sQuery(id+"F0.wireOp",EDGE,"E6.2.1"),sQuery(id+"F0.wireOp",EDGE,"E6.2.2"),sQuery(id+"F0.wireOp",EDGE,"E6.2.3"),sQuery(id+"F0.wireOp",EDGE,"E6.2.4"),sQuery(id+"F0.wireOp",EDGE,"E6.3.1"),sQuery(id+"F0.wireOp",EDGE,"E6.3.2"),sQuery(id+"F0.wireOp",EDGE,"E6.3.3"),sQuery(id+"F0.wireOp",EDGE,"E6.3.4"),sQuery(id+"F0.wireOp",EDGE,"E6.4.1"),sQuery(id+"F0.wireOp",EDGE,"E6.4.2"),sQuery(id+"F0.wireOp",EDGE,"E6.4.3"),sQuery(id+"F0.wireOp",EDGE,"E6.4.4"),sQuery(id+"F0.wireOp",EDGE,"E6.5.1"),sQuery(id+"F0.wireOp",EDGE,"E6.5.2"),sQuery(id+"F0.wireOp",EDGE,"E6.5.3"),sQuery(id+"F0.wireOp",EDGE,"E6.5.4"),sQuery(id+"F0.wireOp",EDGE,"E6.6.1"),sQuery(id+"F0.wireOp",EDGE,"E6.6.2"),sQuery(id+"F0.wireOp",EDGE,"E6.6.3"),sQuery(id+"F0.wireOp",EDGE,"E6.6.4"),sQuery(id+"F0.wireOp",EDGE,"E6.7.1"),sQuery(id+"F0.wireOp",EDGE,"E6.7.2"),sQuery(id+"F0.wireOp",EDGE,"E6.7.3"),sQuery(id+"F0.wireOp",EDGE,"E6.7.4"),sQuery(id+"F0.wireOp",EDGE,"E6.8.1"),sQuery(id+"F0.wireOp",EDGE,"E6.8.2"),sQuery(id+"F0.wireOp",EDGE,"E6.8.3"),sQuery(id+"F0.wireOp",EDGE,"E6.8.4"),sQuery(id+"F0.wireOp",EDGE,"E6.9.1"),sQuery(id+"F0.wireOp",EDGE,"E6.9.2"),sQuery(id+"F0.wireOp",EDGE,"E6.9.3"),sQuery(id+"F0.wireOp",EDGE,"E6.9.4"),sQuery(id+"F0.wireOp",EDGE,"E6.10.1"),sQuery(id+"F0.wireOp",EDGE,"E6.10.2"),sQuery(id+"F0.wireOp",EDGE,"E6.10.3"),sQuery(id+"F0.wireOp",EDGE,"E6.10.4"),sQuery(id+"F0.wireOp",EDGE,"E6.11.1"),sQuery(id+"F0.wireOp",EDGE,"E6.11.2"),sQuery(id+"F0.wireOp",EDGE,"E6.11.3"),sQuery(id+"F0.wireOp",EDGE,"E6.11.4"),sQuery(id+"F0.wireOp",EDGE,"E6.12.1"),sQuery(id+"F0.wireOp",EDGE,"E6.12.2"),sQuery(id+"F0.wireOp",EDGE,"E6.12.3"),sQuery(id+"F0.wireOp",EDGE,"E6.12.4"),sQuery(id+"F0.wireOp",EDGE,"E6.13.1"),sQuery(id+"F0.wireOp",EDGE,"E6.13.2"),sQuery(id+"F0.wireOp",EDGE,"E6.13.3"),sQuery(id+"F0.wireOp",EDGE,"E6.13.4"),sQuery(id+"F0.wireOp",EDGE,"E6.14.1"),sQuery(id+"F0.wireOp",EDGE,"E6.14.2"),sQuery(id+"F0.wireOp",EDGE,"E6.14.3"),sQuery(id+"F0.wireOp",EDGE,"E6.14.4"),sQuery(id+"F0.wireOp",EDGE,"E6.15.1"),sQuery(id+"F0.wireOp",EDGE,"E6.15.2"),sQuery(id+"F0.wireOp",EDGE,"E6.15.3"),sQuery(id+"F0.wireOp",EDGE,"E6.15.4"),sQuery(id+"F0.wireOp",EDGE,"E6.16.1"),sQuery(id+"F0.wireOp",EDGE,"E6.16.2"),sQuery(id+"F0.wireOp",EDGE,"E6.16.3"),sQuery(id+"F0.wireOp",EDGE,"E6.16.4"),sQuery(id+"F0.wireOp",EDGE,"E6.17.1"),sQuery(id+"F0.wireOp",EDGE,"E6.17.2"),sQuery(id+"F0.wireOp",EDGE,"E6.17.3"),sQuery(id+"F0.wireOp",EDGE,"E6.17.4"),sQuery(id+"F0.wireOp",EDGE,"E6.18.1"),sQuery(id+"F0.wireOp",EDGE,"E6.18.2"),sQuery(id+"F0.wireOp",EDGE,"E6.18.3"),sQuery(id+"F0.wireOp",EDGE,"E6.18.4"),sQuery(id+"F0.wireOp",EDGE,"E6.19.1"),sQuery(id+"F0.wireOp",EDGE,"E6.19.2"),sQuery(id+"F0.wireOp",EDGE,"E6.19.3"),sQuery(id+"F0.wireOp",EDGE,"E6.19.4"),sQuery(id+"F0.wireOp",EDGE,"E6.20.1"),sQuery(id+"F0.wireOp",EDGE,"E6.20.2"),sQuery(id+"F0.wireOp",EDGE,"E6.20.3"),sQuery(id+"F0.wireOp",EDGE,"E6.20.4"),sQuery(id+"F0.wireOp",EDGE,"E6.21.1"),sQuery(id+"F0.wireOp",EDGE,"E6.21.2"),sQuery(id+"F0.wireOp",EDGE,"E6.21.3"),sQuery(id+"F0.wireOp",EDGE,"E6.21.4"),sQuery(id+"F0.wireOp",EDGE,"E6.22.1"),sQuery(id+"F0.wireOp",EDGE,"E6.22.2"),sQuery(id+"F0.wireOp",EDGE,"E6.22.3"),sQuery(id+"F0.wireOp",EDGE,"E6.22.4"),sQuery(id+"F0.wireOp",EDGE,"E6.23.1"),sQuery(id+"F0.wireOp",EDGE,"E6.23.2"),sQuery(id+"F0.wireOp",EDGE,"E6.23.3"),sQuery(id+"F0.wireOp",EDGE,"E6.23.4"),sQuery(id+"F0.wireOp",EDGE,"E6.24.1"),sQuery(id+"F0.wireOp",EDGE,"E6.24.2"),sQuery(id+"F0.wireOp",EDGE,"E6.24.3"),sQuery(id+"F0.wireOp",EDGE,"E6.24.4"),sQuery(id+"F0.wireOp",EDGE,"E6.25.1"),sQuery(id+"F0.wireOp",EDGE,"E6.25.2"),sQuery(id+"F0.wireOp",EDGE,"E6.25.3"),sQuery(id+"F0.wireOp",EDGE,"E6.25.4"),sQuery(id+"F0.wireOp",EDGE,"E6.26.1"),sQuery(id+"F0.wireOp",EDGE,"E6.26.2"),sQuery(id+"F0.wireOp",EDGE,"E6.26.3"),sQuery(id+"F0.wireOp",EDGE,"E6.26.4"),sQuery(id+"F0.wireOp",EDGE,"E6.27.1"),sQuery(id+"F0.wireOp",EDGE,"E6.27.2"),sQuery(id+"F0.wireOp",EDGE,"E6.27.3"),sQuery(id+"F0.wireOp",EDGE,"E6.27.4"),sQuery(id+"F0.wireOp",EDGE,"E6.28.1"),sQuery(id+"F0.wireOp",EDGE,"E6.28.2"),sQuery(id+"F0.wireOp",EDGE,"E6.28.3"),sQuery(id+"F0.wireOp",EDGE,"E6.28.4"),sQuery(id+"F0.wireOp",EDGE,"E6.29.1"),sQuery(id+"F0.wireOp",EDGE,"E6.29.2"),sQuery(id+"F0.wireOp",EDGE,"E6.29.3"),sQuery(id+"F0.wireOp",EDGE,"E6.29.4"),sQuery(id+"F0.wireOp",EDGE,"E6.30.1"),sQuery(id+"F0.wireOp",EDGE,"E6.30.2"),sQuery(id+"F0.wireOp",EDGE,"E6.30.3"),sQuery(id+"F0.wireOp",EDGE,"E6.30.4"),sQuery(id+"F0.wireOp",EDGE,"E6.31.1"),sQuery(id+"F0.wireOp",EDGE,"E6.31.2"),sQuery(id+"F0.wireOp",EDGE,"E6.31.3"),sQuery(id+"F0.wireOp",EDGE,"E6.31.4"),sQuery(id+"F0.wireOp",EDGE,"E6.32.1"),sQuery(id+"F0.wireOp",EDGE,"E6.32.2"),sQuery(id+"F0.wireOp",EDGE,"E6.32.3"),sQuery(id+"F0.wireOp",EDGE,"E6.32.4"),sQuery(id+"F0.wireOp",EDGE,"E6.33.1"),sQuery(id+"F0.wireOp",EDGE,"E6.33.2"),sQuery(id+"F0.wireOp",EDGE,"E6.33.3"),sQuery(id+"F0.wireOp",EDGE,"E6.33.4"),subQ1,sQuery(id+"F0.wireOp",EDGE,"E6.34.2"),subQ0,sQuery(id+"F0.wireOp",EDGE,"E6.34.4"),sQuery(id+"F0.wireOp",EDGE,"E6.35.1"),sQuery(id+"F0.wireOp",EDGE,"E6.35.2"),sQuery(id+"F0.wireOp",EDGE,"E6.35.3"),sQuery(id+"F0.wireOp",EDGE,"E6.35.4"),sQuery(id+"F0.wireOp",EDGE,"E6.36.1"),sQuery(id+"F0.wireOp",EDGE,"E6.36.2"),sQuery(id+"F0.wireOp",EDGE,"E6.36.3"),sQuery(id+"F0.wireOp",EDGE,"E6.36.4"),sQuery(id+"F0.wireOp",EDGE,"E6.37.1"),sQuery(id+"F0.wireOp",EDGE,"E6.37.2"),sQuery(id+"F0.wireOp",EDGE,"E6.37.3"),sQuery(id+"F0.wireOp",EDGE,"E6.37.4"),sQuery(id+"F0.wireOp",EDGE,"E6.38.1"),sQuery(id+"F0.wireOp",EDGE,"E6.38.2"),sQuery(id+"F0.wireOp",EDGE,"E6.38.3"),sQuery(id+"F0.wireOp",EDGE,"E6.38.4"),sQuery(id+"F0.wireOp",EDGE,"E6.39.1"),sQuery(id+"F0.wireOp",EDGE,"E6.39.2"),sQuery(id+"F0.wireOp",EDGE,"E6.39.3"),sQuery(id+"F0.wireOp",EDGE,"E6.39.4"),sQuery(id+"F0.wireOp",EDGE,"E6.40.1"),sQuery(id+"F0.wireOp",EDGE,"E6.40.2"),sQuery(id+"F0.wireOp",EDGE,"E6.40.3"),sQuery(id+"F0.wireOp",EDGE,"E6.40.4"),sQuery(id+"F0.wireOp",EDGE,"E6.41.1"),sQuery(id+"F0.wireOp",EDGE,"E6.41.2"),sQuery(id+"F0.wireOp",EDGE,"E6.41.3"),sQuery(id+"F0.wireOp",EDGE,"E6.41.4"),sQuery(id+"F0.wireOp",EDGE,"E6.42.1"),sQuery(id+"F0.wireOp",EDGE,"E6.42.2"),sQuery(id+"F0.wireOp",EDGE,"E6.42.3"),sQuery(id+"F0.wireOp",EDGE,"E6.42.4"),sQuery(id+"F0.wireOp",EDGE,"E6.43.1"),sQuery(id+"F0.wireOp",EDGE,"E6.43.2"),sQuery(id+"F0.wireOp",EDGE,"E6.43.3"),sQuery(id+"F0.wireOp",EDGE,"E6.43.4"),sQuery(id+"F0.wireOp",EDGE,"E7"),sQuery(id+"F0.wireOp",EDGE,"E8.1.0"),sQuery(id+"F0.wireOp",EDGE,"E8.2.0"),sQuery(id+"F0.wireOp",EDGE,"E8.3.0"),sQuery(id+"F0.wireOp",EDGE,"E8.4.0"),sQuery(id+"F0.wireOp",EDGE,"E8.5.0"),sQuery(id+"F0.wireOp",EDGE,"E8.6.0"),sQuery(id+"F0.wireOp",EDGE,"E8.7.0"),sQuery(id+"F0.wireOp",EDGE,"E8.8.0"),sQuery(id+"F0.wireOp",EDGE,"E8.9.0"),sQuery(id+"F0.wireOp",EDGE,"E8.10.0"),sQuery(id+"F0.wireOp",EDGE,"E8.11.0"),sQuery(id+"F0.wireOp",EDGE,"E8.12.0"),sQuery(id+"F0.wireOp",EDGE,"E8.13.0"),sQuery(id+"F0.wireOp",EDGE,"E8.14.0"),sQuery(id+"F0.wireOp",EDGE,"E8.15.0"),sQuery(id+"F0.wireOp",EDGE,"E8.16.0"),sQuery(id+"F0.wireOp",EDGE,"E8.17.0"),sQuery(id+"F0.wireOp",EDGE,"E8.18.0"),sQuery(id+"F0.wireOp",EDGE,"E8.19.0"),sQuery(id+"F0.wireOp",EDGE,"E8.20.0"),sQuery(id+"F0.wireOp",EDGE,"E8.21.0"),sQuery(id+"F0.wireOp",EDGE,"E8.22.0"),sQuery(id+"F0.wireOp",EDGE,"E8.23.0"),sQuery(id+"F0.wireOp",EDGE,"E8.24.0"),sQuery(id+"F0.wireOp",EDGE,"E8.25.0"),sQuery(id+"F0.wireOp",EDGE,"E8.26.0"),sQuery(id+"F0.wireOp",EDGE,"E8.27.0"),sQuery(id+"F0.wireOp",EDGE,"E8.28.0"),sQuery(id+"F0.wireOp",EDGE,"E8.29.0"),sQuery(id+"F0.wireOp",EDGE,"E8.30.0"),sQuery(id+"F0.wireOp",EDGE,"E8.31.0"),sQuery(id+"F0.wireOp",EDGE,"E8.32.0"),sQuery(id+"F0.wireOp",EDGE,"E8.33.0"),sQuery(id+"F0.wireOp",EDGE,"E8.34.0"),sQuery(id+"F0.wireOp",EDGE,"E8.35.0"),sQuery(id+"F0.wireOp",EDGE,"E8.36.0"),sQuery(id+"F0.wireOp",EDGE,"E8.37.0"),sQuery(id+"F0.wireOp",EDGE,"E8.38.0"),sQuery(id+"F0.wireOp",EDGE,"E8.39.0"),sQuery(id+"F0.wireOp",EDGE,"E8.40.0"),sQuery(id+"F0.wireOp",EDGE,"E8.41.0"),sQuery(id+"F0.wireOp",EDGE,"E8.42.0"),sQuery(id+"F0.wireOp",EDGE,"E8.43.0")])],"isStart":true})],"blendedInto":[makeQuery(id+"F1.opExtrude","CAP_FACE",FACE,{"disambiguationData":[OSD([sQuery(id+"F0.wireOp",EDGE,"E0"),sQuery(id+"F0.wireOp",EDGE,"E1"),sQuery(id+"F0.wireOp",EDGE,"E2"),sQuery(id+"F0.wireOp",EDGE,"E4"),sQuery(id+"F0.wireOp",EDGE,"E5"),sQuery(id+"F0.wireOp",EDGE,"E6.1.1"),sQuery(id+"F0.wireOp",EDGE,"E6.1.2"),sQuery(id+"F0.wireOp",EDGE,"E6.1.3"),sQuery(id+"F0.wireOp",EDGE,"E6.1.4"),sQuery(id+"F0.wireOp",EDGE,"E6.2.1"),sQuery(id+"F0.wireOp",EDGE,"E6.2.2"),sQuery(id+"F0.wireOp",EDGE,"E6.2.3"),sQuery(id+"F0.wireOp",EDGE,"E6.2.4"),sQuery(id+"F0.wireOp",EDGE,"E6.3.1"),sQuery(id+"F0.wireOp",EDGE,"E6.3.2"),sQuery(id+"F0.wireOp",EDGE,"E6.3.3"),sQuery(id+"F0.wireOp",EDGE,"E6.3.4"),sQuery(id+"F0.wireOp",EDGE,"E6.4.1"),sQuery(id+"F0.wireOp",EDGE,"E6.4.2"),sQuery(id+"F0.wireOp",EDGE,"E6.4.3"),sQuery(id+"F0.wireOp",EDGE,"E6.4.4"),sQuery(id+"F0.wireOp",EDGE,"E6.5.1"),sQuery(id+"F0.wireOp",EDGE,"E6.5.2"),sQuery(id+"F0.wireOp",EDGE,"E6.5.3"),sQuery(id+"F0.wireOp",EDGE,"E6.5.4"),sQuery(id+"F0.wireOp",EDGE,"E6.6.1"),sQuery(id+"F0.wireOp",EDGE,"E6.6.2"),sQuery(id+"F0.wireOp",EDGE,"E6.6.3"),sQuery(id+"F0.wireOp",EDGE,"E6.6.4"),sQuery(id+"F0.wireOp",EDGE,"E6.7.1"),sQuery(id+"F0.wireOp",EDGE,"E6.7.2"),sQuery(id+"F0.wireOp",EDGE,"E6.7.3"),sQuery(id+"F0.wireOp",EDGE,"E6.7.4"),sQuery(id+"F0.wireOp",EDGE,"E6.8.1"),sQuery(id+"F0.wireOp",EDGE,"E6.8.2"),sQuery(id+"F0.wireOp",EDGE,"E6.8.3"),sQuery(id+"F0.wireOp",EDGE,"E6.8.4"),sQuery(id+"F0.wireOp",EDGE,"E6.9.1"),sQuery(id+"F0.wireOp",EDGE,"E6.9.2"),sQuery(id+"F0.wireOp",EDGE,"E6.9.3"),sQuery(id+"F0.wireOp",EDGE,"E6.9.4"),sQuery(id+"F0.wireOp",EDGE,"E6.10.1"),sQuery(id+"F0.wireOp",EDGE,"E6.10.2"),sQuery(id+"F0.wireOp",EDGE,"E6.10.3"),sQuery(id+"F0.wireOp",EDGE,"E6.10.4"),sQuery(id+"F0.wireOp",EDGE,"E6.11.1"),sQuery(id+"F0.wireOp",EDGE,"E6.11.2"),sQuery(id+"F0.wireOp",EDGE,"E6.11.3"),sQuery(id+"F0.wireOp",EDGE,"E6.11.4"),sQuery(id+"F0.wireOp",EDGE,"E6.12.1"),sQuery(id+"F0.wireOp",EDGE,"E6.12.2"),sQuery(id+"F0.wireOp",EDGE,"E6.12.3"),sQuery(id+"F0.wireOp",EDGE,"E6.12.4"),sQuery(id+"F0.wireOp",EDGE,"E6.13.1"),sQuery(id+"F0.wireOp",EDGE,"E6.13.2"),sQuery(id+"F0.wireOp",EDGE,"E6.13.3"),sQuery(id+"F0.wireOp",EDGE,"E6.13.4"),sQuery(id+"F0.wireOp",EDGE,"E6.14.1"),sQuery(id+"F0.wireOp",EDGE,"E6.14.2"),sQuery(id+"F0.wireOp",EDGE,"E6.14.3"),sQuery(id+"F0.wireOp",EDGE,"E6.14.4"),sQuery(id+"F0.wireOp",EDGE,"E6.15.1"),sQuery(id+"F0.wireOp",EDGE,"E6.15.2"),sQuery(id+"F0.wireOp",EDGE,"E6.15.3"),sQuery(id+"F0.wireOp",EDGE,"E6.15.4"),sQuery(id+"F0.wireOp",EDGE,"E6.16.1"),sQuery(id+"F0.wireOp",EDGE,"E6.16.2"),sQuery(id+"F0.wireOp",EDGE,"E6.16.3"),sQuery(id+"F0.wireOp",EDGE,"E6.16.4"),sQuery(id+"F0.wireOp",EDGE,"E6.17.1"),sQuery(id+"F0.wireOp",EDGE,"E6.17.2"),sQuery(id+"F0.wireOp",EDGE,"E6.17.3"),sQuery(id+"F0.wireOp",EDGE,"E6.17.4"),sQuery(id+"F0.wireOp",EDGE,"E6.18.1"),sQuery(id+"F0.wireOp",EDGE,"E6.18.2"),sQuery(id+"F0.wireOp",EDGE,"E6.18.3"),sQuery(id+"F0.wireOp",EDGE,"E6.18.4"),sQuery(id+"F0.wireOp",EDGE,"E6.19.1"),sQuery(id+"F0.wireOp",EDGE,"E6.19.2"),sQuery(id+"F0.wireOp",EDGE,"E6.19.3"),sQuery(id+"F0.wireOp",EDGE,"E6.19.4"),sQuery(id+"F0.wireOp",EDGE,"E6.20.1"),sQuery(id+"F0.wireOp",EDGE,"E6.20.2"),sQuery(id+"F0.wireOp",EDGE,"E6.20.3"),sQuery(id+"F0.wireOp",EDGE,"E6.20.4"),sQuery(id+"F0.wireOp",EDGE,"E6.21.1"),sQuery(id+"F0.wireOp",EDGE,"E6.21.2"),sQuery(id+"F0.wireOp",EDGE,"E6.21.3"),sQuery(id+"F0.wireOp",EDGE,"E6.21.4"),sQuery(id+"F0.wireOp",EDGE,"E6.22.1"),sQuery(id+"F0.wireOp",EDGE,"E6.22.2"),sQuery(id+"F0.wireOp",EDGE,"E6.22.3"),sQuery(id+"F0.wireOp",EDGE,"E6.22.4"),sQuery(id+"F0.wireOp",EDGE,"E6.23.1"),sQuery(id+"F0.wireOp",EDGE,"E6.23.2"),sQuery(id+"F0.wireOp",EDGE,"E6.23.3"),sQuery(id+"F0.wireOp",EDGE,"E6.23.4"),sQuery(id+"F0.wireOp",EDGE,"E6.24.1"),sQuery(id+"F0.wireOp",EDGE,"E6.24.2"),sQuery(id+"F0.wireOp",EDGE,"E6.24.3"),sQuery(id+"F0.wireOp",EDGE,"E6.24.4"),sQuery(id+"F0.wireOp",EDGE,"E6.25.1"),sQuery(id+"F0.wireOp",EDGE,"E6.25.2"),sQuery(id+"F0.wireOp",EDGE,"E6.25.3"),sQuery(id+"F0.wireOp",EDGE,"E6.25.4"),sQuery(id+"F0.wireOp",EDGE,"E6.26.1"),sQuery(id+"F0.wireOp",EDGE,"E6.26.2"),sQuery(id+"F0.wireOp",EDGE,"E6.26.3"),sQuery(id+"F0.wireOp",EDGE,"E6.26.4"),sQuery(id+"F0.wireOp",EDGE,"E6.27.1"),sQuery(id+"F0.wireOp",EDGE,"E6.27.2"),sQuery(id+"F0.wireOp",EDGE,"E6.27.3"),sQuery(id+"F0.wireOp",EDGE,"E6.27.4"),sQuery(id+"F0.wireOp",EDGE,"E6.28.1"),sQuery(id+"F0.wireOp",EDGE,"E6.28.2"),sQuery(id+"F0.wireOp",EDGE,"E6.28.3"),sQuery(id+"F0.wireOp",EDGE,"E6.28.4"),sQuery(id+"F0.wireOp",EDGE,"E6.29.1"),sQuery(id+"F0.wireOp",EDGE,"E6.29.2"),sQuery(id+"F0.wireOp",EDGE,"E6.29.3"),sQuery(id+"F0.wireOp",EDGE,"E6.29.4"),sQuery(id+"F0.wireOp",EDGE,"E6.30.1"),sQuery(id+"F0.wireOp",EDGE,"E6.30.2"),sQuery(id+"F0.wireOp",EDGE,"E6.30.3"),sQuery(id+"F0.wireOp",EDGE,"E6.30.4"),sQuery(id+"F0.wireOp",EDGE,"E6.31.1"),sQuery(id+"F0.wireOp",EDGE,"E6.31.2"),sQuery(id+"F0.wireOp",EDGE,"E6.31.3"),sQuery(id+"F0.wireOp",EDGE,"E6.31.4"),sQuery(id+"F0.wireOp",EDGE,"E6.32.1"),sQuery(id+"F0.wireOp",EDGE,"E6.32.2"),sQuery(id+"F0.wireOp",EDGE,"E6.32.3"),sQuery(id+"F0.wireOp",EDGE,"E6.32.4"),sQuery(id+"F0.wireOp",EDGE,"E6.33.1"),sQuery(id+"F0.wireOp",EDGE,"E6.33.2"),sQuery(id+"F0.wireOp",EDGE,"E6.33.3"),sQuery(id+"F0.wireOp",EDGE,"E6.33.4"),subQ1,sQuery(id+"F0.wireOp",EDGE,"E6.34.2"),subQ0,sQuery(id+"F0.wireOp",EDGE,"E6.34.4"),sQuery(id+"F0.wireOp",EDGE,"E6.35.1"),sQuery(id+"F0.wireOp",EDGE,"E6.35.2"),sQuery(id+"F0.wireOp",EDGE,"E6.35.3"),sQuery(id+"F0.wireOp",EDGE,"E6.35.4"),sQuery(id+"F0.wireOp",EDGE,"E6.36.1"),sQuery(id+"F0.wireOp",EDGE,"E6.36.2"),sQuery(id+"F0.wireOp",EDGE,"E6.36.3"),sQuery(id+"F0.wireOp",EDGE,"E6.36.4"),sQuery(id+"F0.wireOp",EDGE,"E6.37.1"),sQuery(id+"F0.wireOp",EDGE,"E6.37.2"),sQuery(id+"F0.wireOp",EDGE,"E6.37.3"),sQuery(id+"F0.wireOp",EDGE,"E6.37.4"),sQuery(id+"F0.wireOp",EDGE,"E6.38.1"),sQuery(id+"F0.wireOp",EDGE,"E6.38.2"),sQuery(id+"F0.wireOp",EDGE,"E6.38.3"),sQuery(id+"F0.wireOp",EDGE,"E6.38.4"),sQuery(id+"F0.wireOp",EDGE,"E6.39.1"),sQuery(id+"F0.wireOp",EDGE,"E6.39.2"),sQuery(id+"F0.wireOp",EDGE,"E6.39.3"),sQuery(id+"F0.wireOp",EDGE,"E6.39.4"),sQuery(id+"F0.wireOp",EDGE,"E6.40.1"),sQuery(id+"F0.wireOp",EDGE,"E6.40.2"),sQuery(id+"F0.wireOp",EDGE,"E6.40.3"),sQuery(id+"F0.wireOp",EDGE,"E6.40.4"),sQuery(id+"F0.wireOp",EDGE,"E6.41.1"),sQuery(id+"F0.wireOp",EDGE,"E6.41.2"),sQuery(id+"F0.wireOp",EDGE,"E6.41.3"),sQuery(id+"F0.wireOp",EDGE,"E6.41.4"),sQuery(id+"F0.wireOp",EDGE,"E6.42.1"),sQuery(id+"F0.wireOp",EDGE,"E6.42.2"),sQuery(id+"F0.wireOp",EDGE,"E6.42.3"),sQuery(id+"F0.wireOp",EDGE,"E6.42.4"),sQuery(id+"F0.wireOp",EDGE,"E6.43.1"),sQuery(id+"F0.wireOp",EDGE,"E6.43.2"),sQuery(id+"F0.wireOp",EDGE,"E6.43.3"),sQuery(id+"F0.wireOp",EDGE,"E6.43.4"),sQuery(id+"F0.wireOp",EDGE,"E7"),sQuery(id+"F0.wireOp",EDGE,"E8.1.0"),sQuery(id+"F0.wireOp",EDGE,"E8.2.0"),sQuery(id+"F0.wireOp",EDGE,"E8.3.0"),sQuery(id+"F0.wireOp",EDGE,"E8.4.0"),sQuery(id+"F0.wireOp",EDGE,"E8.5.0"),sQuery(id+"F0.wireOp",EDGE,"E8.6.0"),sQuery(id+"F0.wireOp",EDGE,"E8.7.0"),sQuery(id+"F0.wireOp",EDGE,"E8.8.0"),sQuery(id+"F0.wireOp",EDGE,"E8.9.0"),sQuery(id+"F0.wireOp",EDGE,"E8.10.0"),sQuery(id+"F0.wireOp",EDGE,"E8.11.0"),sQuery(id+"F0.wireOp",EDGE,"E8.12.0"),sQuery(id+"F0.wireOp",EDGE,"E8.13.0"),sQuery(id+"F0.wireOp",EDGE,"E8.14.0"),sQuery(id+"F0.wireOp",EDGE,"E8.15.0"),sQuery(id+"F0.wireOp",EDGE,"E8.16.0"),sQuery(id+"F0.wireOp",EDGE,"E8.17.0"),sQuery(id+"F0.wireOp",EDGE,"E8.18.0"),sQuery(id+"F0.wireOp",EDGE,"E8.19.0"),sQuery(id+"F0.wireOp",EDGE,"E8.20.0"),sQuery(id+"F0.wireOp",EDGE,"E8.21.0"),sQuery(id+"F0.wireOp",EDGE,"E8.22.0"),sQuery(id+"F0.wireOp",EDGE,"E8.23.0"),sQuery(id+"F0.wireOp",EDGE,"E8.24.0"),sQuery(id+"F0.wireOp",EDGE,"E8.25.0"),sQuery(id+"F0.wireOp",EDGE,"E8.26.0"),sQuery(id+"F0.wireOp",EDGE,"E8.27.0"),sQuery(id+"F0.wireOp",EDGE,"E8.28.0"),sQuery(id+"F0.wireOp",EDGE,"E8.29.0"),sQuery(id+"F0.wireOp",EDGE,"E8.30.0"),sQuery(id+"F0.wireOp",EDGE,"E8.31.0"),sQuery(id+"F0.wireOp",EDGE,"E8.32.0"),sQuery(id+"F0.wireOp",EDGE,"E8.33.0"),sQuery(id+"F0.wireOp",EDGE,"E8.34.0"),sQuery(id+"F0.wireOp",EDGE,"E8.35.0"),sQuery(id+"F0.wireOp",EDGE,"E8.36.0"),sQuery(id+"F0.wireOp",EDGE,"E8.37.0"),sQuery(id+"F0.wireOp",EDGE,"E8.38.0"),sQuery(id+"F0.wireOp",EDGE,"E8.39.0"),sQuery(id+"F0.wireOp",EDGE,"E8.40.0"),sQuery(id+"F0.wireOp",EDGE,"E8.41.0"),sQuery(id+"F0.wireOp",EDGE,"E8.42.0"),sQuery(id+"F0.wireOp",EDGE,"E8.43.0")])],"isStart":true})]});}
            var Q39;
            {var subQ0=sQuery(id+"F0.wireOp",EDGE,"E6.36.3");var subQ1=sQuery(id+"F0.wireOp",EDGE,"E6.36.1");Q39=makeQuery(id+"F2.opFillet","BLEND_EDGE",EDGE,{"blendedFrom":[makeQuery(id+"F1.opExtrude","SWEPT_EDGE",EDGE,{"disambiguationData":[OSD([sQuery(id+"F0.wireOp",EDGE,"E6.36.0"),subQ1,subQ0])]}),makeQuery(id+"F1.opExtrude","CAP_FACE",FACE,{"disambiguationData":[OSD([sQuery(id+"F0.wireOp",EDGE,"E0"),sQuery(id+"F0.wireOp",EDGE,"E1"),sQuery(id+"F0.wireOp",EDGE,"E2"),sQuery(id+"F0.wireOp",EDGE,"E4"),sQuery(id+"F0.wireOp",EDGE,"E5"),sQuery(id+"F0.wireOp",EDGE,"E6.1.1"),sQuery(id+"F0.wireOp",EDGE,"E6.1.2"),sQuery(id+"F0.wireOp",EDGE,"E6.1.3"),sQuery(id+"F0.wireOp",EDGE,"E6.1.4"),sQuery(id+"F0.wireOp",EDGE,"E6.2.1"),sQuery(id+"F0.wireOp",EDGE,"E6.2.2"),sQuery(id+"F0.wireOp",EDGE,"E6.2.3"),sQuery(id+"F0.wireOp",EDGE,"E6.2.4"),sQuery(id+"F0.wireOp",EDGE,"E6.3.1"),sQuery(id+"F0.wireOp",EDGE,"E6.3.2"),sQuery(id+"F0.wireOp",EDGE,"E6.3.3"),sQuery(id+"F0.wireOp",EDGE,"E6.3.4"),sQuery(id+"F0.wireOp",EDGE,"E6.4.1"),sQuery(id+"F0.wireOp",EDGE,"E6.4.2"),sQuery(id+"F0.wireOp",EDGE,"E6.4.3"),sQuery(id+"F0.wireOp",EDGE,"E6.4.4"),sQuery(id+"F0.wireOp",EDGE,"E6.5.1"),sQuery(id+"F0.wireOp",EDGE,"E6.5.2"),sQuery(id+"F0.wireOp",EDGE,"E6.5.3"),sQuery(id+"F0.wireOp",EDGE,"E6.5.4"),sQuery(id+"F0.wireOp",EDGE,"E6.6.1"),sQuery(id+"F0.wireOp",EDGE,"E6.6.2"),sQuery(id+"F0.wireOp",EDGE,"E6.6.3"),sQuery(id+"F0.wireOp",EDGE,"E6.6.4"),sQuery(id+"F0.wireOp",EDGE,"E6.7.1"),sQuery(id+"F0.wireOp",EDGE,"E6.7.2"),sQuery(id+"F0.wireOp",EDGE,"E6.7.3"),sQuery(id+"F0.wireOp",EDGE,"E6.7.4"),sQuery(id+"F0.wireOp",EDGE,"E6.8.1"),sQuery(id+"F0.wireOp",EDGE,"E6.8.2"),sQuery(id+"F0.wireOp",EDGE,"E6.8.3"),sQuery(id+"F0.wireOp",EDGE,"E6.8.4"),sQuery(id+"F0.wireOp",EDGE,"E6.9.1"),sQuery(id+"F0.wireOp",EDGE,"E6.9.2"),sQuery(id+"F0.wireOp",EDGE,"E6.9.3"),sQuery(id+"F0.wireOp",EDGE,"E6.9.4"),sQuery(id+"F0.wireOp",EDGE,"E6.10.1"),sQuery(id+"F0.wireOp",EDGE,"E6.10.2"),sQuery(id+"F0.wireOp",EDGE,"E6.10.3"),sQuery(id+"F0.wireOp",EDGE,"E6.10.4"),sQuery(id+"F0.wireOp",EDGE,"E6.11.1"),sQuery(id+"F0.wireOp",EDGE,"E6.11.2"),sQuery(id+"F0.wireOp",EDGE,"E6.11.3"),sQuery(id+"F0.wireOp",EDGE,"E6.11.4"),sQuery(id+"F0.wireOp",EDGE,"E6.12.1"),sQuery(id+"F0.wireOp",EDGE,"E6.12.2"),sQuery(id+"F0.wireOp",EDGE,"E6.12.3"),sQuery(id+"F0.wireOp",EDGE,"E6.12.4"),sQuery(id+"F0.wireOp",EDGE,"E6.13.1"),sQuery(id+"F0.wireOp",EDGE,"E6.13.2"),sQuery(id+"F0.wireOp",EDGE,"E6.13.3"),sQuery(id+"F0.wireOp",EDGE,"E6.13.4"),sQuery(id+"F0.wireOp",EDGE,"E6.14.1"),sQuery(id+"F0.wireOp",EDGE,"E6.14.2"),sQuery(id+"F0.wireOp",EDGE,"E6.14.3"),sQuery(id+"F0.wireOp",EDGE,"E6.14.4"),sQuery(id+"F0.wireOp",EDGE,"E6.15.1"),sQuery(id+"F0.wireOp",EDGE,"E6.15.2"),sQuery(id+"F0.wireOp",EDGE,"E6.15.3"),sQuery(id+"F0.wireOp",EDGE,"E6.15.4"),sQuery(id+"F0.wireOp",EDGE,"E6.16.1"),sQuery(id+"F0.wireOp",EDGE,"E6.16.2"),sQuery(id+"F0.wireOp",EDGE,"E6.16.3"),sQuery(id+"F0.wireOp",EDGE,"E6.16.4"),sQuery(id+"F0.wireOp",EDGE,"E6.17.1"),sQuery(id+"F0.wireOp",EDGE,"E6.17.2"),sQuery(id+"F0.wireOp",EDGE,"E6.17.3"),sQuery(id+"F0.wireOp",EDGE,"E6.17.4"),sQuery(id+"F0.wireOp",EDGE,"E6.18.1"),sQuery(id+"F0.wireOp",EDGE,"E6.18.2"),sQuery(id+"F0.wireOp",EDGE,"E6.18.3"),sQuery(id+"F0.wireOp",EDGE,"E6.18.4"),sQuery(id+"F0.wireOp",EDGE,"E6.19.1"),sQuery(id+"F0.wireOp",EDGE,"E6.19.2"),sQuery(id+"F0.wireOp",EDGE,"E6.19.3"),sQuery(id+"F0.wireOp",EDGE,"E6.19.4"),sQuery(id+"F0.wireOp",EDGE,"E6.20.1"),sQuery(id+"F0.wireOp",EDGE,"E6.20.2"),sQuery(id+"F0.wireOp",EDGE,"E6.20.3"),sQuery(id+"F0.wireOp",EDGE,"E6.20.4"),sQuery(id+"F0.wireOp",EDGE,"E6.21.1"),sQuery(id+"F0.wireOp",EDGE,"E6.21.2"),sQuery(id+"F0.wireOp",EDGE,"E6.21.3"),sQuery(id+"F0.wireOp",EDGE,"E6.21.4"),sQuery(id+"F0.wireOp",EDGE,"E6.22.1"),sQuery(id+"F0.wireOp",EDGE,"E6.22.2"),sQuery(id+"F0.wireOp",EDGE,"E6.22.3"),sQuery(id+"F0.wireOp",EDGE,"E6.22.4"),sQuery(id+"F0.wireOp",EDGE,"E6.23.1"),sQuery(id+"F0.wireOp",EDGE,"E6.23.2"),sQuery(id+"F0.wireOp",EDGE,"E6.23.3"),sQuery(id+"F0.wireOp",EDGE,"E6.23.4"),sQuery(id+"F0.wireOp",EDGE,"E6.24.1"),sQuery(id+"F0.wireOp",EDGE,"E6.24.2"),sQuery(id+"F0.wireOp",EDGE,"E6.24.3"),sQuery(id+"F0.wireOp",EDGE,"E6.24.4"),sQuery(id+"F0.wireOp",EDGE,"E6.25.1"),sQuery(id+"F0.wireOp",EDGE,"E6.25.2"),sQuery(id+"F0.wireOp",EDGE,"E6.25.3"),sQuery(id+"F0.wireOp",EDGE,"E6.25.4"),sQuery(id+"F0.wireOp",EDGE,"E6.26.1"),sQuery(id+"F0.wireOp",EDGE,"E6.26.2"),sQuery(id+"F0.wireOp",EDGE,"E6.26.3"),sQuery(id+"F0.wireOp",EDGE,"E6.26.4"),sQuery(id+"F0.wireOp",EDGE,"E6.27.1"),sQuery(id+"F0.wireOp",EDGE,"E6.27.2"),sQuery(id+"F0.wireOp",EDGE,"E6.27.3"),sQuery(id+"F0.wireOp",EDGE,"E6.27.4"),sQuery(id+"F0.wireOp",EDGE,"E6.28.1"),sQuery(id+"F0.wireOp",EDGE,"E6.28.2"),sQuery(id+"F0.wireOp",EDGE,"E6.28.3"),sQuery(id+"F0.wireOp",EDGE,"E6.28.4"),sQuery(id+"F0.wireOp",EDGE,"E6.29.1"),sQuery(id+"F0.wireOp",EDGE,"E6.29.2"),sQuery(id+"F0.wireOp",EDGE,"E6.29.3"),sQuery(id+"F0.wireOp",EDGE,"E6.29.4"),sQuery(id+"F0.wireOp",EDGE,"E6.30.1"),sQuery(id+"F0.wireOp",EDGE,"E6.30.2"),sQuery(id+"F0.wireOp",EDGE,"E6.30.3"),sQuery(id+"F0.wireOp",EDGE,"E6.30.4"),sQuery(id+"F0.wireOp",EDGE,"E6.31.1"),sQuery(id+"F0.wireOp",EDGE,"E6.31.2"),sQuery(id+"F0.wireOp",EDGE,"E6.31.3"),sQuery(id+"F0.wireOp",EDGE,"E6.31.4"),sQuery(id+"F0.wireOp",EDGE,"E6.32.1"),sQuery(id+"F0.wireOp",EDGE,"E6.32.2"),sQuery(id+"F0.wireOp",EDGE,"E6.32.3"),sQuery(id+"F0.wireOp",EDGE,"E6.32.4"),sQuery(id+"F0.wireOp",EDGE,"E6.33.1"),sQuery(id+"F0.wireOp",EDGE,"E6.33.2"),sQuery(id+"F0.wireOp",EDGE,"E6.33.3"),sQuery(id+"F0.wireOp",EDGE,"E6.33.4"),sQuery(id+"F0.wireOp",EDGE,"E6.34.1"),sQuery(id+"F0.wireOp",EDGE,"E6.34.2"),sQuery(id+"F0.wireOp",EDGE,"E6.34.3"),sQuery(id+"F0.wireOp",EDGE,"E6.34.4"),sQuery(id+"F0.wireOp",EDGE,"E6.35.1"),sQuery(id+"F0.wireOp",EDGE,"E6.35.2"),sQuery(id+"F0.wireOp",EDGE,"E6.35.3"),sQuery(id+"F0.wireOp",EDGE,"E6.35.4"),subQ1,sQuery(id+"F0.wireOp",EDGE,"E6.36.2"),subQ0,sQuery(id+"F0.wireOp",EDGE,"E6.36.4"),sQuery(id+"F0.wireOp",EDGE,"E6.37.1"),sQuery(id+"F0.wireOp",EDGE,"E6.37.2"),sQuery(id+"F0.wireOp",EDGE,"E6.37.3"),sQuery(id+"F0.wireOp",EDGE,"E6.37.4"),sQuery(id+"F0.wireOp",EDGE,"E6.38.1"),sQuery(id+"F0.wireOp",EDGE,"E6.38.2"),sQuery(id+"F0.wireOp",EDGE,"E6.38.3"),sQuery(id+"F0.wireOp",EDGE,"E6.38.4"),sQuery(id+"F0.wireOp",EDGE,"E6.39.1"),sQuery(id+"F0.wireOp",EDGE,"E6.39.2"),sQuery(id+"F0.wireOp",EDGE,"E6.39.3"),sQuery(id+"F0.wireOp",EDGE,"E6.39.4"),sQuery(id+"F0.wireOp",EDGE,"E6.40.1"),sQuery(id+"F0.wireOp",EDGE,"E6.40.2"),sQuery(id+"F0.wireOp",EDGE,"E6.40.3"),sQuery(id+"F0.wireOp",EDGE,"E6.40.4"),sQuery(id+"F0.wireOp",EDGE,"E6.41.1"),sQuery(id+"F0.wireOp",EDGE,"E6.41.2"),sQuery(id+"F0.wireOp",EDGE,"E6.41.3"),sQuery(id+"F0.wireOp",EDGE,"E6.41.4"),sQuery(id+"F0.wireOp",EDGE,"E6.42.1"),sQuery(id+"F0.wireOp",EDGE,"E6.42.2"),sQuery(id+"F0.wireOp",EDGE,"E6.42.3"),sQuery(id+"F0.wireOp",EDGE,"E6.42.4"),sQuery(id+"F0.wireOp",EDGE,"E6.43.1"),sQuery(id+"F0.wireOp",EDGE,"E6.43.2"),sQuery(id+"F0.wireOp",EDGE,"E6.43.3"),sQuery(id+"F0.wireOp",EDGE,"E6.43.4"),sQuery(id+"F0.wireOp",EDGE,"E7"),sQuery(id+"F0.wireOp",EDGE,"E8.1.0"),sQuery(id+"F0.wireOp",EDGE,"E8.2.0"),sQuery(id+"F0.wireOp",EDGE,"E8.3.0"),sQuery(id+"F0.wireOp",EDGE,"E8.4.0"),sQuery(id+"F0.wireOp",EDGE,"E8.5.0"),sQuery(id+"F0.wireOp",EDGE,"E8.6.0"),sQuery(id+"F0.wireOp",EDGE,"E8.7.0"),sQuery(id+"F0.wireOp",EDGE,"E8.8.0"),sQuery(id+"F0.wireOp",EDGE,"E8.9.0"),sQuery(id+"F0.wireOp",EDGE,"E8.10.0"),sQuery(id+"F0.wireOp",EDGE,"E8.11.0"),sQuery(id+"F0.wireOp",EDGE,"E8.12.0"),sQuery(id+"F0.wireOp",EDGE,"E8.13.0"),sQuery(id+"F0.wireOp",EDGE,"E8.14.0"),sQuery(id+"F0.wireOp",EDGE,"E8.15.0"),sQuery(id+"F0.wireOp",EDGE,"E8.16.0"),sQuery(id+"F0.wireOp",EDGE,"E8.17.0"),sQuery(id+"F0.wireOp",EDGE,"E8.18.0"),sQuery(id+"F0.wireOp",EDGE,"E8.19.0"),sQuery(id+"F0.wireOp",EDGE,"E8.20.0"),sQuery(id+"F0.wireOp",EDGE,"E8.21.0"),sQuery(id+"F0.wireOp",EDGE,"E8.22.0"),sQuery(id+"F0.wireOp",EDGE,"E8.23.0"),sQuery(id+"F0.wireOp",EDGE,"E8.24.0"),sQuery(id+"F0.wireOp",EDGE,"E8.25.0"),sQuery(id+"F0.wireOp",EDGE,"E8.26.0"),sQuery(id+"F0.wireOp",EDGE,"E8.27.0"),sQuery(id+"F0.wireOp",EDGE,"E8.28.0"),sQuery(id+"F0.wireOp",EDGE,"E8.29.0"),sQuery(id+"F0.wireOp",EDGE,"E8.30.0"),sQuery(id+"F0.wireOp",EDGE,"E8.31.0"),sQuery(id+"F0.wireOp",EDGE,"E8.32.0"),sQuery(id+"F0.wireOp",EDGE,"E8.33.0"),sQuery(id+"F0.wireOp",EDGE,"E8.34.0"),sQuery(id+"F0.wireOp",EDGE,"E8.35.0"),sQuery(id+"F0.wireOp",EDGE,"E8.36.0"),sQuery(id+"F0.wireOp",EDGE,"E8.37.0"),sQuery(id+"F0.wireOp",EDGE,"E8.38.0"),sQuery(id+"F0.wireOp",EDGE,"E8.39.0"),sQuery(id+"F0.wireOp",EDGE,"E8.40.0"),sQuery(id+"F0.wireOp",EDGE,"E8.41.0"),sQuery(id+"F0.wireOp",EDGE,"E8.42.0"),sQuery(id+"F0.wireOp",EDGE,"E8.43.0")])],"isStart":true})],"blendedInto":[makeQuery(id+"F1.opExtrude","CAP_FACE",FACE,{"disambiguationData":[OSD([sQuery(id+"F0.wireOp",EDGE,"E0"),sQuery(id+"F0.wireOp",EDGE,"E1"),sQuery(id+"F0.wireOp",EDGE,"E2"),sQuery(id+"F0.wireOp",EDGE,"E4"),sQuery(id+"F0.wireOp",EDGE,"E5"),sQuery(id+"F0.wireOp",EDGE,"E6.1.1"),sQuery(id+"F0.wireOp",EDGE,"E6.1.2"),sQuery(id+"F0.wireOp",EDGE,"E6.1.3"),sQuery(id+"F0.wireOp",EDGE,"E6.1.4"),sQuery(id+"F0.wireOp",EDGE,"E6.2.1"),sQuery(id+"F0.wireOp",EDGE,"E6.2.2"),sQuery(id+"F0.wireOp",EDGE,"E6.2.3"),sQuery(id+"F0.wireOp",EDGE,"E6.2.4"),sQuery(id+"F0.wireOp",EDGE,"E6.3.1"),sQuery(id+"F0.wireOp",EDGE,"E6.3.2"),sQuery(id+"F0.wireOp",EDGE,"E6.3.3"),sQuery(id+"F0.wireOp",EDGE,"E6.3.4"),sQuery(id+"F0.wireOp",EDGE,"E6.4.1"),sQuery(id+"F0.wireOp",EDGE,"E6.4.2"),sQuery(id+"F0.wireOp",EDGE,"E6.4.3"),sQuery(id+"F0.wireOp",EDGE,"E6.4.4"),sQuery(id+"F0.wireOp",EDGE,"E6.5.1"),sQuery(id+"F0.wireOp",EDGE,"E6.5.2"),sQuery(id+"F0.wireOp",EDGE,"E6.5.3"),sQuery(id+"F0.wireOp",EDGE,"E6.5.4"),sQuery(id+"F0.wireOp",EDGE,"E6.6.1"),sQuery(id+"F0.wireOp",EDGE,"E6.6.2"),sQuery(id+"F0.wireOp",EDGE,"E6.6.3"),sQuery(id+"F0.wireOp",EDGE,"E6.6.4"),sQuery(id+"F0.wireOp",EDGE,"E6.7.1"),sQuery(id+"F0.wireOp",EDGE,"E6.7.2"),sQuery(id+"F0.wireOp",EDGE,"E6.7.3"),sQuery(id+"F0.wireOp",EDGE,"E6.7.4"),sQuery(id+"F0.wireOp",EDGE,"E6.8.1"),sQuery(id+"F0.wireOp",EDGE,"E6.8.2"),sQuery(id+"F0.wireOp",EDGE,"E6.8.3"),sQuery(id+"F0.wireOp",EDGE,"E6.8.4"),sQuery(id+"F0.wireOp",EDGE,"E6.9.1"),sQuery(id+"F0.wireOp",EDGE,"E6.9.2"),sQuery(id+"F0.wireOp",EDGE,"E6.9.3"),sQuery(id+"F0.wireOp",EDGE,"E6.9.4"),sQuery(id+"F0.wireOp",EDGE,"E6.10.1"),sQuery(id+"F0.wireOp",EDGE,"E6.10.2"),sQuery(id+"F0.wireOp",EDGE,"E6.10.3"),sQuery(id+"F0.wireOp",EDGE,"E6.10.4"),sQuery(id+"F0.wireOp",EDGE,"E6.11.1"),sQuery(id+"F0.wireOp",EDGE,"E6.11.2"),sQuery(id+"F0.wireOp",EDGE,"E6.11.3"),sQuery(id+"F0.wireOp",EDGE,"E6.11.4"),sQuery(id+"F0.wireOp",EDGE,"E6.12.1"),sQuery(id+"F0.wireOp",EDGE,"E6.12.2"),sQuery(id+"F0.wireOp",EDGE,"E6.12.3"),sQuery(id+"F0.wireOp",EDGE,"E6.12.4"),sQuery(id+"F0.wireOp",EDGE,"E6.13.1"),sQuery(id+"F0.wireOp",EDGE,"E6.13.2"),sQuery(id+"F0.wireOp",EDGE,"E6.13.3"),sQuery(id+"F0.wireOp",EDGE,"E6.13.4"),sQuery(id+"F0.wireOp",EDGE,"E6.14.1"),sQuery(id+"F0.wireOp",EDGE,"E6.14.2"),sQuery(id+"F0.wireOp",EDGE,"E6.14.3"),sQuery(id+"F0.wireOp",EDGE,"E6.14.4"),sQuery(id+"F0.wireOp",EDGE,"E6.15.1"),sQuery(id+"F0.wireOp",EDGE,"E6.15.2"),sQuery(id+"F0.wireOp",EDGE,"E6.15.3"),sQuery(id+"F0.wireOp",EDGE,"E6.15.4"),sQuery(id+"F0.wireOp",EDGE,"E6.16.1"),sQuery(id+"F0.wireOp",EDGE,"E6.16.2"),sQuery(id+"F0.wireOp",EDGE,"E6.16.3"),sQuery(id+"F0.wireOp",EDGE,"E6.16.4"),sQuery(id+"F0.wireOp",EDGE,"E6.17.1"),sQuery(id+"F0.wireOp",EDGE,"E6.17.2"),sQuery(id+"F0.wireOp",EDGE,"E6.17.3"),sQuery(id+"F0.wireOp",EDGE,"E6.17.4"),sQuery(id+"F0.wireOp",EDGE,"E6.18.1"),sQuery(id+"F0.wireOp",EDGE,"E6.18.2"),sQuery(id+"F0.wireOp",EDGE,"E6.18.3"),sQuery(id+"F0.wireOp",EDGE,"E6.18.4"),sQuery(id+"F0.wireOp",EDGE,"E6.19.1"),sQuery(id+"F0.wireOp",EDGE,"E6.19.2"),sQuery(id+"F0.wireOp",EDGE,"E6.19.3"),sQuery(id+"F0.wireOp",EDGE,"E6.19.4"),sQuery(id+"F0.wireOp",EDGE,"E6.20.1"),sQuery(id+"F0.wireOp",EDGE,"E6.20.2"),sQuery(id+"F0.wireOp",EDGE,"E6.20.3"),sQuery(id+"F0.wireOp",EDGE,"E6.20.4"),sQuery(id+"F0.wireOp",EDGE,"E6.21.1"),sQuery(id+"F0.wireOp",EDGE,"E6.21.2"),sQuery(id+"F0.wireOp",EDGE,"E6.21.3"),sQuery(id+"F0.wireOp",EDGE,"E6.21.4"),sQuery(id+"F0.wireOp",EDGE,"E6.22.1"),sQuery(id+"F0.wireOp",EDGE,"E6.22.2"),sQuery(id+"F0.wireOp",EDGE,"E6.22.3"),sQuery(id+"F0.wireOp",EDGE,"E6.22.4"),sQuery(id+"F0.wireOp",EDGE,"E6.23.1"),sQuery(id+"F0.wireOp",EDGE,"E6.23.2"),sQuery(id+"F0.wireOp",EDGE,"E6.23.3"),sQuery(id+"F0.wireOp",EDGE,"E6.23.4"),sQuery(id+"F0.wireOp",EDGE,"E6.24.1"),sQuery(id+"F0.wireOp",EDGE,"E6.24.2"),sQuery(id+"F0.wireOp",EDGE,"E6.24.3"),sQuery(id+"F0.wireOp",EDGE,"E6.24.4"),sQuery(id+"F0.wireOp",EDGE,"E6.25.1"),sQuery(id+"F0.wireOp",EDGE,"E6.25.2"),sQuery(id+"F0.wireOp",EDGE,"E6.25.3"),sQuery(id+"F0.wireOp",EDGE,"E6.25.4"),sQuery(id+"F0.wireOp",EDGE,"E6.26.1"),sQuery(id+"F0.wireOp",EDGE,"E6.26.2"),sQuery(id+"F0.wireOp",EDGE,"E6.26.3"),sQuery(id+"F0.wireOp",EDGE,"E6.26.4"),sQuery(id+"F0.wireOp",EDGE,"E6.27.1"),sQuery(id+"F0.wireOp",EDGE,"E6.27.2"),sQuery(id+"F0.wireOp",EDGE,"E6.27.3"),sQuery(id+"F0.wireOp",EDGE,"E6.27.4"),sQuery(id+"F0.wireOp",EDGE,"E6.28.1"),sQuery(id+"F0.wireOp",EDGE,"E6.28.2"),sQuery(id+"F0.wireOp",EDGE,"E6.28.3"),sQuery(id+"F0.wireOp",EDGE,"E6.28.4"),sQuery(id+"F0.wireOp",EDGE,"E6.29.1"),sQuery(id+"F0.wireOp",EDGE,"E6.29.2"),sQuery(id+"F0.wireOp",EDGE,"E6.29.3"),sQuery(id+"F0.wireOp",EDGE,"E6.29.4"),sQuery(id+"F0.wireOp",EDGE,"E6.30.1"),sQuery(id+"F0.wireOp",EDGE,"E6.30.2"),sQuery(id+"F0.wireOp",EDGE,"E6.30.3"),sQuery(id+"F0.wireOp",EDGE,"E6.30.4"),sQuery(id+"F0.wireOp",EDGE,"E6.31.1"),sQuery(id+"F0.wireOp",EDGE,"E6.31.2"),sQuery(id+"F0.wireOp",EDGE,"E6.31.3"),sQuery(id+"F0.wireOp",EDGE,"E6.31.4"),sQuery(id+"F0.wireOp",EDGE,"E6.32.1"),sQuery(id+"F0.wireOp",EDGE,"E6.32.2"),sQuery(id+"F0.wireOp",EDGE,"E6.32.3"),sQuery(id+"F0.wireOp",EDGE,"E6.32.4"),sQuery(id+"F0.wireOp",EDGE,"E6.33.1"),sQuery(id+"F0.wireOp",EDGE,"E6.33.2"),sQuery(id+"F0.wireOp",EDGE,"E6.33.3"),sQuery(id+"F0.wireOp",EDGE,"E6.33.4"),sQuery(id+"F0.wireOp",EDGE,"E6.34.1"),sQuery(id+"F0.wireOp",EDGE,"E6.34.2"),sQuery(id+"F0.wireOp",EDGE,"E6.34.3"),sQuery(id+"F0.wireOp",EDGE,"E6.34.4"),sQuery(id+"F0.wireOp",EDGE,"E6.35.1"),sQuery(id+"F0.wireOp",EDGE,"E6.35.2"),sQuery(id+"F0.wireOp",EDGE,"E6.35.3"),sQuery(id+"F0.wireOp",EDGE,"E6.35.4"),subQ1,sQuery(id+"F0.wireOp",EDGE,"E6.36.2"),subQ0,sQuery(id+"F0.wireOp",EDGE,"E6.36.4"),sQuery(id+"F0.wireOp",EDGE,"E6.37.1"),sQuery(id+"F0.wireOp",EDGE,"E6.37.2"),sQuery(id+"F0.wireOp",EDGE,"E6.37.3"),sQuery(id+"F0.wireOp",EDGE,"E6.37.4"),sQuery(id+"F0.wireOp",EDGE,"E6.38.1"),sQuery(id+"F0.wireOp",EDGE,"E6.38.2"),sQuery(id+"F0.wireOp",EDGE,"E6.38.3"),sQuery(id+"F0.wireOp",EDGE,"E6.38.4"),sQuery(id+"F0.wireOp",EDGE,"E6.39.1"),sQuery(id+"F0.wireOp",EDGE,"E6.39.2"),sQuery(id+"F0.wireOp",EDGE,"E6.39.3"),sQuery(id+"F0.wireOp",EDGE,"E6.39.4"),sQuery(id+"F0.wireOp",EDGE,"E6.40.1"),sQuery(id+"F0.wireOp",EDGE,"E6.40.2"),sQuery(id+"F0.wireOp",EDGE,"E6.40.3"),sQuery(id+"F0.wireOp",EDGE,"E6.40.4"),sQuery(id+"F0.wireOp",EDGE,"E6.41.1"),sQuery(id+"F0.wireOp",EDGE,"E6.41.2"),sQuery(id+"F0.wireOp",EDGE,"E6.41.3"),sQuery(id+"F0.wireOp",EDGE,"E6.41.4"),sQuery(id+"F0.wireOp",EDGE,"E6.42.1"),sQuery(id+"F0.wireOp",EDGE,"E6.42.2"),sQuery(id+"F0.wireOp",EDGE,"E6.42.3"),sQuery(id+"F0.wireOp",EDGE,"E6.42.4"),sQuery(id+"F0.wireOp",EDGE,"E6.43.1"),sQuery(id+"F0.wireOp",EDGE,"E6.43.2"),sQuery(id+"F0.wireOp",EDGE,"E6.43.3"),sQuery(id+"F0.wireOp",EDGE,"E6.43.4"),sQuery(id+"F0.wireOp",EDGE,"E7"),sQuery(id+"F0.wireOp",EDGE,"E8.1.0"),sQuery(id+"F0.wireOp",EDGE,"E8.2.0"),sQuery(id+"F0.wireOp",EDGE,"E8.3.0"),sQuery(id+"F0.wireOp",EDGE,"E8.4.0"),sQuery(id+"F0.wireOp",EDGE,"E8.5.0"),sQuery(id+"F0.wireOp",EDGE,"E8.6.0"),sQuery(id+"F0.wireOp",EDGE,"E8.7.0"),sQuery(id+"F0.wireOp",EDGE,"E8.8.0"),sQuery(id+"F0.wireOp",EDGE,"E8.9.0"),sQuery(id+"F0.wireOp",EDGE,"E8.10.0"),sQuery(id+"F0.wireOp",EDGE,"E8.11.0"),sQuery(id+"F0.wireOp",EDGE,"E8.12.0"),sQuery(id+"F0.wireOp",EDGE,"E8.13.0"),sQuery(id+"F0.wireOp",EDGE,"E8.14.0"),sQuery(id+"F0.wireOp",EDGE,"E8.15.0"),sQuery(id+"F0.wireOp",EDGE,"E8.16.0"),sQuery(id+"F0.wireOp",EDGE,"E8.17.0"),sQuery(id+"F0.wireOp",EDGE,"E8.18.0"),sQuery(id+"F0.wireOp",EDGE,"E8.19.0"),sQuery(id+"F0.wireOp",EDGE,"E8.20.0"),sQuery(id+"F0.wireOp",EDGE,"E8.21.0"),sQuery(id+"F0.wireOp",EDGE,"E8.22.0"),sQuery(id+"F0.wireOp",EDGE,"E8.23.0"),sQuery(id+"F0.wireOp",EDGE,"E8.24.0"),sQuery(id+"F0.wireOp",EDGE,"E8.25.0"),sQuery(id+"F0.wireOp",EDGE,"E8.26.0"),sQuery(id+"F0.wireOp",EDGE,"E8.27.0"),sQuery(id+"F0.wireOp",EDGE,"E8.28.0"),sQuery(id+"F0.wireOp",EDGE,"E8.29.0"),sQuery(id+"F0.wireOp",EDGE,"E8.30.0"),sQuery(id+"F0.wireOp",EDGE,"E8.31.0"),sQuery(id+"F0.wireOp",EDGE,"E8.32.0"),sQuery(id+"F0.wireOp",EDGE,"E8.33.0"),sQuery(id+"F0.wireOp",EDGE,"E8.34.0"),sQuery(id+"F0.wireOp",EDGE,"E8.35.0"),sQuery(id+"F0.wireOp",EDGE,"E8.36.0"),sQuery(id+"F0.wireOp",EDGE,"E8.37.0"),sQuery(id+"F0.wireOp",EDGE,"E8.38.0"),sQuery(id+"F0.wireOp",EDGE,"E8.39.0"),sQuery(id+"F0.wireOp",EDGE,"E8.40.0"),sQuery(id+"F0.wireOp",EDGE,"E8.41.0"),sQuery(id+"F0.wireOp",EDGE,"E8.42.0"),sQuery(id+"F0.wireOp",EDGE,"E8.43.0")])],"isStart":true})]});}
            var Q40;
            {var subQ0=sQuery(id+"F0.wireOp",EDGE,"E6.38.3");var subQ1=sQuery(id+"F0.wireOp",EDGE,"E6.38.1");Q40=makeQuery(id+"F2.opFillet","BLEND_EDGE",EDGE,{"blendedFrom":[makeQuery(id+"F1.opExtrude","SWEPT_EDGE",EDGE,{"disambiguationData":[OSD([sQuery(id+"F0.wireOp",EDGE,"E6.38.0"),subQ1,subQ0])]}),makeQuery(id+"F1.opExtrude","CAP_FACE",FACE,{"disambiguationData":[OSD([sQuery(id+"F0.wireOp",EDGE,"E0"),sQuery(id+"F0.wireOp",EDGE,"E1"),sQuery(id+"F0.wireOp",EDGE,"E2"),sQuery(id+"F0.wireOp",EDGE,"E4"),sQuery(id+"F0.wireOp",EDGE,"E5"),sQuery(id+"F0.wireOp",EDGE,"E6.1.1"),sQuery(id+"F0.wireOp",EDGE,"E6.1.2"),sQuery(id+"F0.wireOp",EDGE,"E6.1.3"),sQuery(id+"F0.wireOp",EDGE,"E6.1.4"),sQuery(id+"F0.wireOp",EDGE,"E6.2.1"),sQuery(id+"F0.wireOp",EDGE,"E6.2.2"),sQuery(id+"F0.wireOp",EDGE,"E6.2.3"),sQuery(id+"F0.wireOp",EDGE,"E6.2.4"),sQuery(id+"F0.wireOp",EDGE,"E6.3.1"),sQuery(id+"F0.wireOp",EDGE,"E6.3.2"),sQuery(id+"F0.wireOp",EDGE,"E6.3.3"),sQuery(id+"F0.wireOp",EDGE,"E6.3.4"),sQuery(id+"F0.wireOp",EDGE,"E6.4.1"),sQuery(id+"F0.wireOp",EDGE,"E6.4.2"),sQuery(id+"F0.wireOp",EDGE,"E6.4.3"),sQuery(id+"F0.wireOp",EDGE,"E6.4.4"),sQuery(id+"F0.wireOp",EDGE,"E6.5.1"),sQuery(id+"F0.wireOp",EDGE,"E6.5.2"),sQuery(id+"F0.wireOp",EDGE,"E6.5.3"),sQuery(id+"F0.wireOp",EDGE,"E6.5.4"),sQuery(id+"F0.wireOp",EDGE,"E6.6.1"),sQuery(id+"F0.wireOp",EDGE,"E6.6.2"),sQuery(id+"F0.wireOp",EDGE,"E6.6.3"),sQuery(id+"F0.wireOp",EDGE,"E6.6.4"),sQuery(id+"F0.wireOp",EDGE,"E6.7.1"),sQuery(id+"F0.wireOp",EDGE,"E6.7.2"),sQuery(id+"F0.wireOp",EDGE,"E6.7.3"),sQuery(id+"F0.wireOp",EDGE,"E6.7.4"),sQuery(id+"F0.wireOp",EDGE,"E6.8.1"),sQuery(id+"F0.wireOp",EDGE,"E6.8.2"),sQuery(id+"F0.wireOp",EDGE,"E6.8.3"),sQuery(id+"F0.wireOp",EDGE,"E6.8.4"),sQuery(id+"F0.wireOp",EDGE,"E6.9.1"),sQuery(id+"F0.wireOp",EDGE,"E6.9.2"),sQuery(id+"F0.wireOp",EDGE,"E6.9.3"),sQuery(id+"F0.wireOp",EDGE,"E6.9.4"),sQuery(id+"F0.wireOp",EDGE,"E6.10.1"),sQuery(id+"F0.wireOp",EDGE,"E6.10.2"),sQuery(id+"F0.wireOp",EDGE,"E6.10.3"),sQuery(id+"F0.wireOp",EDGE,"E6.10.4"),sQuery(id+"F0.wireOp",EDGE,"E6.11.1"),sQuery(id+"F0.wireOp",EDGE,"E6.11.2"),sQuery(id+"F0.wireOp",EDGE,"E6.11.3"),sQuery(id+"F0.wireOp",EDGE,"E6.11.4"),sQuery(id+"F0.wireOp",EDGE,"E6.12.1"),sQuery(id+"F0.wireOp",EDGE,"E6.12.2"),sQuery(id+"F0.wireOp",EDGE,"E6.12.3"),sQuery(id+"F0.wireOp",EDGE,"E6.12.4"),sQuery(id+"F0.wireOp",EDGE,"E6.13.1"),sQuery(id+"F0.wireOp",EDGE,"E6.13.2"),sQuery(id+"F0.wireOp",EDGE,"E6.13.3"),sQuery(id+"F0.wireOp",EDGE,"E6.13.4"),sQuery(id+"F0.wireOp",EDGE,"E6.14.1"),sQuery(id+"F0.wireOp",EDGE,"E6.14.2"),sQuery(id+"F0.wireOp",EDGE,"E6.14.3"),sQuery(id+"F0.wireOp",EDGE,"E6.14.4"),sQuery(id+"F0.wireOp",EDGE,"E6.15.1"),sQuery(id+"F0.wireOp",EDGE,"E6.15.2"),sQuery(id+"F0.wireOp",EDGE,"E6.15.3"),sQuery(id+"F0.wireOp",EDGE,"E6.15.4"),sQuery(id+"F0.wireOp",EDGE,"E6.16.1"),sQuery(id+"F0.wireOp",EDGE,"E6.16.2"),sQuery(id+"F0.wireOp",EDGE,"E6.16.3"),sQuery(id+"F0.wireOp",EDGE,"E6.16.4"),sQuery(id+"F0.wireOp",EDGE,"E6.17.1"),sQuery(id+"F0.wireOp",EDGE,"E6.17.2"),sQuery(id+"F0.wireOp",EDGE,"E6.17.3"),sQuery(id+"F0.wireOp",EDGE,"E6.17.4"),sQuery(id+"F0.wireOp",EDGE,"E6.18.1"),sQuery(id+"F0.wireOp",EDGE,"E6.18.2"),sQuery(id+"F0.wireOp",EDGE,"E6.18.3"),sQuery(id+"F0.wireOp",EDGE,"E6.18.4"),sQuery(id+"F0.wireOp",EDGE,"E6.19.1"),sQuery(id+"F0.wireOp",EDGE,"E6.19.2"),sQuery(id+"F0.wireOp",EDGE,"E6.19.3"),sQuery(id+"F0.wireOp",EDGE,"E6.19.4"),sQuery(id+"F0.wireOp",EDGE,"E6.20.1"),sQuery(id+"F0.wireOp",EDGE,"E6.20.2"),sQuery(id+"F0.wireOp",EDGE,"E6.20.3"),sQuery(id+"F0.wireOp",EDGE,"E6.20.4"),sQuery(id+"F0.wireOp",EDGE,"E6.21.1"),sQuery(id+"F0.wireOp",EDGE,"E6.21.2"),sQuery(id+"F0.wireOp",EDGE,"E6.21.3"),sQuery(id+"F0.wireOp",EDGE,"E6.21.4"),sQuery(id+"F0.wireOp",EDGE,"E6.22.1"),sQuery(id+"F0.wireOp",EDGE,"E6.22.2"),sQuery(id+"F0.wireOp",EDGE,"E6.22.3"),sQuery(id+"F0.wireOp",EDGE,"E6.22.4"),sQuery(id+"F0.wireOp",EDGE,"E6.23.1"),sQuery(id+"F0.wireOp",EDGE,"E6.23.2"),sQuery(id+"F0.wireOp",EDGE,"E6.23.3"),sQuery(id+"F0.wireOp",EDGE,"E6.23.4"),sQuery(id+"F0.wireOp",EDGE,"E6.24.1"),sQuery(id+"F0.wireOp",EDGE,"E6.24.2"),sQuery(id+"F0.wireOp",EDGE,"E6.24.3"),sQuery(id+"F0.wireOp",EDGE,"E6.24.4"),sQuery(id+"F0.wireOp",EDGE,"E6.25.1"),sQuery(id+"F0.wireOp",EDGE,"E6.25.2"),sQuery(id+"F0.wireOp",EDGE,"E6.25.3"),sQuery(id+"F0.wireOp",EDGE,"E6.25.4"),sQuery(id+"F0.wireOp",EDGE,"E6.26.1"),sQuery(id+"F0.wireOp",EDGE,"E6.26.2"),sQuery(id+"F0.wireOp",EDGE,"E6.26.3"),sQuery(id+"F0.wireOp",EDGE,"E6.26.4"),sQuery(id+"F0.wireOp",EDGE,"E6.27.1"),sQuery(id+"F0.wireOp",EDGE,"E6.27.2"),sQuery(id+"F0.wireOp",EDGE,"E6.27.3"),sQuery(id+"F0.wireOp",EDGE,"E6.27.4"),sQuery(id+"F0.wireOp",EDGE,"E6.28.1"),sQuery(id+"F0.wireOp",EDGE,"E6.28.2"),sQuery(id+"F0.wireOp",EDGE,"E6.28.3"),sQuery(id+"F0.wireOp",EDGE,"E6.28.4"),sQuery(id+"F0.wireOp",EDGE,"E6.29.1"),sQuery(id+"F0.wireOp",EDGE,"E6.29.2"),sQuery(id+"F0.wireOp",EDGE,"E6.29.3"),sQuery(id+"F0.wireOp",EDGE,"E6.29.4"),sQuery(id+"F0.wireOp",EDGE,"E6.30.1"),sQuery(id+"F0.wireOp",EDGE,"E6.30.2"),sQuery(id+"F0.wireOp",EDGE,"E6.30.3"),sQuery(id+"F0.wireOp",EDGE,"E6.30.4"),sQuery(id+"F0.wireOp",EDGE,"E6.31.1"),sQuery(id+"F0.wireOp",EDGE,"E6.31.2"),sQuery(id+"F0.wireOp",EDGE,"E6.31.3"),sQuery(id+"F0.wireOp",EDGE,"E6.31.4"),sQuery(id+"F0.wireOp",EDGE,"E6.32.1"),sQuery(id+"F0.wireOp",EDGE,"E6.32.2"),sQuery(id+"F0.wireOp",EDGE,"E6.32.3"),sQuery(id+"F0.wireOp",EDGE,"E6.32.4"),sQuery(id+"F0.wireOp",EDGE,"E6.33.1"),sQuery(id+"F0.wireOp",EDGE,"E6.33.2"),sQuery(id+"F0.wireOp",EDGE,"E6.33.3"),sQuery(id+"F0.wireOp",EDGE,"E6.33.4"),sQuery(id+"F0.wireOp",EDGE,"E6.34.1"),sQuery(id+"F0.wireOp",EDGE,"E6.34.2"),sQuery(id+"F0.wireOp",EDGE,"E6.34.3"),sQuery(id+"F0.wireOp",EDGE,"E6.34.4"),sQuery(id+"F0.wireOp",EDGE,"E6.35.1"),sQuery(id+"F0.wireOp",EDGE,"E6.35.2"),sQuery(id+"F0.wireOp",EDGE,"E6.35.3"),sQuery(id+"F0.wireOp",EDGE,"E6.35.4"),sQuery(id+"F0.wireOp",EDGE,"E6.36.1"),sQuery(id+"F0.wireOp",EDGE,"E6.36.2"),sQuery(id+"F0.wireOp",EDGE,"E6.36.3"),sQuery(id+"F0.wireOp",EDGE,"E6.36.4"),sQuery(id+"F0.wireOp",EDGE,"E6.37.1"),sQuery(id+"F0.wireOp",EDGE,"E6.37.2"),sQuery(id+"F0.wireOp",EDGE,"E6.37.3"),sQuery(id+"F0.wireOp",EDGE,"E6.37.4"),subQ1,sQuery(id+"F0.wireOp",EDGE,"E6.38.2"),subQ0,sQuery(id+"F0.wireOp",EDGE,"E6.38.4"),sQuery(id+"F0.wireOp",EDGE,"E6.39.1"),sQuery(id+"F0.wireOp",EDGE,"E6.39.2"),sQuery(id+"F0.wireOp",EDGE,"E6.39.3"),sQuery(id+"F0.wireOp",EDGE,"E6.39.4"),sQuery(id+"F0.wireOp",EDGE,"E6.40.1"),sQuery(id+"F0.wireOp",EDGE,"E6.40.2"),sQuery(id+"F0.wireOp",EDGE,"E6.40.3"),sQuery(id+"F0.wireOp",EDGE,"E6.40.4"),sQuery(id+"F0.wireOp",EDGE,"E6.41.1"),sQuery(id+"F0.wireOp",EDGE,"E6.41.2"),sQuery(id+"F0.wireOp",EDGE,"E6.41.3"),sQuery(id+"F0.wireOp",EDGE,"E6.41.4"),sQuery(id+"F0.wireOp",EDGE,"E6.42.1"),sQuery(id+"F0.wireOp",EDGE,"E6.42.2"),sQuery(id+"F0.wireOp",EDGE,"E6.42.3"),sQuery(id+"F0.wireOp",EDGE,"E6.42.4"),sQuery(id+"F0.wireOp",EDGE,"E6.43.1"),sQuery(id+"F0.wireOp",EDGE,"E6.43.2"),sQuery(id+"F0.wireOp",EDGE,"E6.43.3"),sQuery(id+"F0.wireOp",EDGE,"E6.43.4"),sQuery(id+"F0.wireOp",EDGE,"E7"),sQuery(id+"F0.wireOp",EDGE,"E8.1.0"),sQuery(id+"F0.wireOp",EDGE,"E8.2.0"),sQuery(id+"F0.wireOp",EDGE,"E8.3.0"),sQuery(id+"F0.wireOp",EDGE,"E8.4.0"),sQuery(id+"F0.wireOp",EDGE,"E8.5.0"),sQuery(id+"F0.wireOp",EDGE,"E8.6.0"),sQuery(id+"F0.wireOp",EDGE,"E8.7.0"),sQuery(id+"F0.wireOp",EDGE,"E8.8.0"),sQuery(id+"F0.wireOp",EDGE,"E8.9.0"),sQuery(id+"F0.wireOp",EDGE,"E8.10.0"),sQuery(id+"F0.wireOp",EDGE,"E8.11.0"),sQuery(id+"F0.wireOp",EDGE,"E8.12.0"),sQuery(id+"F0.wireOp",EDGE,"E8.13.0"),sQuery(id+"F0.wireOp",EDGE,"E8.14.0"),sQuery(id+"F0.wireOp",EDGE,"E8.15.0"),sQuery(id+"F0.wireOp",EDGE,"E8.16.0"),sQuery(id+"F0.wireOp",EDGE,"E8.17.0"),sQuery(id+"F0.wireOp",EDGE,"E8.18.0"),sQuery(id+"F0.wireOp",EDGE,"E8.19.0"),sQuery(id+"F0.wireOp",EDGE,"E8.20.0"),sQuery(id+"F0.wireOp",EDGE,"E8.21.0"),sQuery(id+"F0.wireOp",EDGE,"E8.22.0"),sQuery(id+"F0.wireOp",EDGE,"E8.23.0"),sQuery(id+"F0.wireOp",EDGE,"E8.24.0"),sQuery(id+"F0.wireOp",EDGE,"E8.25.0"),sQuery(id+"F0.wireOp",EDGE,"E8.26.0"),sQuery(id+"F0.wireOp",EDGE,"E8.27.0"),sQuery(id+"F0.wireOp",EDGE,"E8.28.0"),sQuery(id+"F0.wireOp",EDGE,"E8.29.0"),sQuery(id+"F0.wireOp",EDGE,"E8.30.0"),sQuery(id+"F0.wireOp",EDGE,"E8.31.0"),sQuery(id+"F0.wireOp",EDGE,"E8.32.0"),sQuery(id+"F0.wireOp",EDGE,"E8.33.0"),sQuery(id+"F0.wireOp",EDGE,"E8.34.0"),sQuery(id+"F0.wireOp",EDGE,"E8.35.0"),sQuery(id+"F0.wireOp",EDGE,"E8.36.0"),sQuery(id+"F0.wireOp",EDGE,"E8.37.0"),sQuery(id+"F0.wireOp",EDGE,"E8.38.0"),sQuery(id+"F0.wireOp",EDGE,"E8.39.0"),sQuery(id+"F0.wireOp",EDGE,"E8.40.0"),sQuery(id+"F0.wireOp",EDGE,"E8.41.0"),sQuery(id+"F0.wireOp",EDGE,"E8.42.0"),sQuery(id+"F0.wireOp",EDGE,"E8.43.0")])],"isStart":true})],"blendedInto":[makeQuery(id+"F1.opExtrude","CAP_FACE",FACE,{"disambiguationData":[OSD([sQuery(id+"F0.wireOp",EDGE,"E0"),sQuery(id+"F0.wireOp",EDGE,"E1"),sQuery(id+"F0.wireOp",EDGE,"E2"),sQuery(id+"F0.wireOp",EDGE,"E4"),sQuery(id+"F0.wireOp",EDGE,"E5"),sQuery(id+"F0.wireOp",EDGE,"E6.1.1"),sQuery(id+"F0.wireOp",EDGE,"E6.1.2"),sQuery(id+"F0.wireOp",EDGE,"E6.1.3"),sQuery(id+"F0.wireOp",EDGE,"E6.1.4"),sQuery(id+"F0.wireOp",EDGE,"E6.2.1"),sQuery(id+"F0.wireOp",EDGE,"E6.2.2"),sQuery(id+"F0.wireOp",EDGE,"E6.2.3"),sQuery(id+"F0.wireOp",EDGE,"E6.2.4"),sQuery(id+"F0.wireOp",EDGE,"E6.3.1"),sQuery(id+"F0.wireOp",EDGE,"E6.3.2"),sQuery(id+"F0.wireOp",EDGE,"E6.3.3"),sQuery(id+"F0.wireOp",EDGE,"E6.3.4"),sQuery(id+"F0.wireOp",EDGE,"E6.4.1"),sQuery(id+"F0.wireOp",EDGE,"E6.4.2"),sQuery(id+"F0.wireOp",EDGE,"E6.4.3"),sQuery(id+"F0.wireOp",EDGE,"E6.4.4"),sQuery(id+"F0.wireOp",EDGE,"E6.5.1"),sQuery(id+"F0.wireOp",EDGE,"E6.5.2"),sQuery(id+"F0.wireOp",EDGE,"E6.5.3"),sQuery(id+"F0.wireOp",EDGE,"E6.5.4"),sQuery(id+"F0.wireOp",EDGE,"E6.6.1"),sQuery(id+"F0.wireOp",EDGE,"E6.6.2"),sQuery(id+"F0.wireOp",EDGE,"E6.6.3"),sQuery(id+"F0.wireOp",EDGE,"E6.6.4"),sQuery(id+"F0.wireOp",EDGE,"E6.7.1"),sQuery(id+"F0.wireOp",EDGE,"E6.7.2"),sQuery(id+"F0.wireOp",EDGE,"E6.7.3"),sQuery(id+"F0.wireOp",EDGE,"E6.7.4"),sQuery(id+"F0.wireOp",EDGE,"E6.8.1"),sQuery(id+"F0.wireOp",EDGE,"E6.8.2"),sQuery(id+"F0.wireOp",EDGE,"E6.8.3"),sQuery(id+"F0.wireOp",EDGE,"E6.8.4"),sQuery(id+"F0.wireOp",EDGE,"E6.9.1"),sQuery(id+"F0.wireOp",EDGE,"E6.9.2"),sQuery(id+"F0.wireOp",EDGE,"E6.9.3"),sQuery(id+"F0.wireOp",EDGE,"E6.9.4"),sQuery(id+"F0.wireOp",EDGE,"E6.10.1"),sQuery(id+"F0.wireOp",EDGE,"E6.10.2"),sQuery(id+"F0.wireOp",EDGE,"E6.10.3"),sQuery(id+"F0.wireOp",EDGE,"E6.10.4"),sQuery(id+"F0.wireOp",EDGE,"E6.11.1"),sQuery(id+"F0.wireOp",EDGE,"E6.11.2"),sQuery(id+"F0.wireOp",EDGE,"E6.11.3"),sQuery(id+"F0.wireOp",EDGE,"E6.11.4"),sQuery(id+"F0.wireOp",EDGE,"E6.12.1"),sQuery(id+"F0.wireOp",EDGE,"E6.12.2"),sQuery(id+"F0.wireOp",EDGE,"E6.12.3"),sQuery(id+"F0.wireOp",EDGE,"E6.12.4"),sQuery(id+"F0.wireOp",EDGE,"E6.13.1"),sQuery(id+"F0.wireOp",EDGE,"E6.13.2"),sQuery(id+"F0.wireOp",EDGE,"E6.13.3"),sQuery(id+"F0.wireOp",EDGE,"E6.13.4"),sQuery(id+"F0.wireOp",EDGE,"E6.14.1"),sQuery(id+"F0.wireOp",EDGE,"E6.14.2"),sQuery(id+"F0.wireOp",EDGE,"E6.14.3"),sQuery(id+"F0.wireOp",EDGE,"E6.14.4"),sQuery(id+"F0.wireOp",EDGE,"E6.15.1"),sQuery(id+"F0.wireOp",EDGE,"E6.15.2"),sQuery(id+"F0.wireOp",EDGE,"E6.15.3"),sQuery(id+"F0.wireOp",EDGE,"E6.15.4"),sQuery(id+"F0.wireOp",EDGE,"E6.16.1"),sQuery(id+"F0.wireOp",EDGE,"E6.16.2"),sQuery(id+"F0.wireOp",EDGE,"E6.16.3"),sQuery(id+"F0.wireOp",EDGE,"E6.16.4"),sQuery(id+"F0.wireOp",EDGE,"E6.17.1"),sQuery(id+"F0.wireOp",EDGE,"E6.17.2"),sQuery(id+"F0.wireOp",EDGE,"E6.17.3"),sQuery(id+"F0.wireOp",EDGE,"E6.17.4"),sQuery(id+"F0.wireOp",EDGE,"E6.18.1"),sQuery(id+"F0.wireOp",EDGE,"E6.18.2"),sQuery(id+"F0.wireOp",EDGE,"E6.18.3"),sQuery(id+"F0.wireOp",EDGE,"E6.18.4"),sQuery(id+"F0.wireOp",EDGE,"E6.19.1"),sQuery(id+"F0.wireOp",EDGE,"E6.19.2"),sQuery(id+"F0.wireOp",EDGE,"E6.19.3"),sQuery(id+"F0.wireOp",EDGE,"E6.19.4"),sQuery(id+"F0.wireOp",EDGE,"E6.20.1"),sQuery(id+"F0.wireOp",EDGE,"E6.20.2"),sQuery(id+"F0.wireOp",EDGE,"E6.20.3"),sQuery(id+"F0.wireOp",EDGE,"E6.20.4"),sQuery(id+"F0.wireOp",EDGE,"E6.21.1"),sQuery(id+"F0.wireOp",EDGE,"E6.21.2"),sQuery(id+"F0.wireOp",EDGE,"E6.21.3"),sQuery(id+"F0.wireOp",EDGE,"E6.21.4"),sQuery(id+"F0.wireOp",EDGE,"E6.22.1"),sQuery(id+"F0.wireOp",EDGE,"E6.22.2"),sQuery(id+"F0.wireOp",EDGE,"E6.22.3"),sQuery(id+"F0.wireOp",EDGE,"E6.22.4"),sQuery(id+"F0.wireOp",EDGE,"E6.23.1"),sQuery(id+"F0.wireOp",EDGE,"E6.23.2"),sQuery(id+"F0.wireOp",EDGE,"E6.23.3"),sQuery(id+"F0.wireOp",EDGE,"E6.23.4"),sQuery(id+"F0.wireOp",EDGE,"E6.24.1"),sQuery(id+"F0.wireOp",EDGE,"E6.24.2"),sQuery(id+"F0.wireOp",EDGE,"E6.24.3"),sQuery(id+"F0.wireOp",EDGE,"E6.24.4"),sQuery(id+"F0.wireOp",EDGE,"E6.25.1"),sQuery(id+"F0.wireOp",EDGE,"E6.25.2"),sQuery(id+"F0.wireOp",EDGE,"E6.25.3"),sQuery(id+"F0.wireOp",EDGE,"E6.25.4"),sQuery(id+"F0.wireOp",EDGE,"E6.26.1"),sQuery(id+"F0.wireOp",EDGE,"E6.26.2"),sQuery(id+"F0.wireOp",EDGE,"E6.26.3"),sQuery(id+"F0.wireOp",EDGE,"E6.26.4"),sQuery(id+"F0.wireOp",EDGE,"E6.27.1"),sQuery(id+"F0.wireOp",EDGE,"E6.27.2"),sQuery(id+"F0.wireOp",EDGE,"E6.27.3"),sQuery(id+"F0.wireOp",EDGE,"E6.27.4"),sQuery(id+"F0.wireOp",EDGE,"E6.28.1"),sQuery(id+"F0.wireOp",EDGE,"E6.28.2"),sQuery(id+"F0.wireOp",EDGE,"E6.28.3"),sQuery(id+"F0.wireOp",EDGE,"E6.28.4"),sQuery(id+"F0.wireOp",EDGE,"E6.29.1"),sQuery(id+"F0.wireOp",EDGE,"E6.29.2"),sQuery(id+"F0.wireOp",EDGE,"E6.29.3"),sQuery(id+"F0.wireOp",EDGE,"E6.29.4"),sQuery(id+"F0.wireOp",EDGE,"E6.30.1"),sQuery(id+"F0.wireOp",EDGE,"E6.30.2"),sQuery(id+"F0.wireOp",EDGE,"E6.30.3"),sQuery(id+"F0.wireOp",EDGE,"E6.30.4"),sQuery(id+"F0.wireOp",EDGE,"E6.31.1"),sQuery(id+"F0.wireOp",EDGE,"E6.31.2"),sQuery(id+"F0.wireOp",EDGE,"E6.31.3"),sQuery(id+"F0.wireOp",EDGE,"E6.31.4"),sQuery(id+"F0.wireOp",EDGE,"E6.32.1"),sQuery(id+"F0.wireOp",EDGE,"E6.32.2"),sQuery(id+"F0.wireOp",EDGE,"E6.32.3"),sQuery(id+"F0.wireOp",EDGE,"E6.32.4"),sQuery(id+"F0.wireOp",EDGE,"E6.33.1"),sQuery(id+"F0.wireOp",EDGE,"E6.33.2"),sQuery(id+"F0.wireOp",EDGE,"E6.33.3"),sQuery(id+"F0.wireOp",EDGE,"E6.33.4"),sQuery(id+"F0.wireOp",EDGE,"E6.34.1"),sQuery(id+"F0.wireOp",EDGE,"E6.34.2"),sQuery(id+"F0.wireOp",EDGE,"E6.34.3"),sQuery(id+"F0.wireOp",EDGE,"E6.34.4"),sQuery(id+"F0.wireOp",EDGE,"E6.35.1"),sQuery(id+"F0.wireOp",EDGE,"E6.35.2"),sQuery(id+"F0.wireOp",EDGE,"E6.35.3"),sQuery(id+"F0.wireOp",EDGE,"E6.35.4"),sQuery(id+"F0.wireOp",EDGE,"E6.36.1"),sQuery(id+"F0.wireOp",EDGE,"E6.36.2"),sQuery(id+"F0.wireOp",EDGE,"E6.36.3"),sQuery(id+"F0.wireOp",EDGE,"E6.36.4"),sQuery(id+"F0.wireOp",EDGE,"E6.37.1"),sQuery(id+"F0.wireOp",EDGE,"E6.37.2"),sQuery(id+"F0.wireOp",EDGE,"E6.37.3"),sQuery(id+"F0.wireOp",EDGE,"E6.37.4"),subQ1,sQuery(id+"F0.wireOp",EDGE,"E6.38.2"),subQ0,sQuery(id+"F0.wireOp",EDGE,"E6.38.4"),sQuery(id+"F0.wireOp",EDGE,"E6.39.1"),sQuery(id+"F0.wireOp",EDGE,"E6.39.2"),sQuery(id+"F0.wireOp",EDGE,"E6.39.3"),sQuery(id+"F0.wireOp",EDGE,"E6.39.4"),sQuery(id+"F0.wireOp",EDGE,"E6.40.1"),sQuery(id+"F0.wireOp",EDGE,"E6.40.2"),sQuery(id+"F0.wireOp",EDGE,"E6.40.3"),sQuery(id+"F0.wireOp",EDGE,"E6.40.4"),sQuery(id+"F0.wireOp",EDGE,"E6.41.1"),sQuery(id+"F0.wireOp",EDGE,"E6.41.2"),sQuery(id+"F0.wireOp",EDGE,"E6.41.3"),sQuery(id+"F0.wireOp",EDGE,"E6.41.4"),sQuery(id+"F0.wireOp",EDGE,"E6.42.1"),sQuery(id+"F0.wireOp",EDGE,"E6.42.2"),sQuery(id+"F0.wireOp",EDGE,"E6.42.3"),sQuery(id+"F0.wireOp",EDGE,"E6.42.4"),sQuery(id+"F0.wireOp",EDGE,"E6.43.1"),sQuery(id+"F0.wireOp",EDGE,"E6.43.2"),sQuery(id+"F0.wireOp",EDGE,"E6.43.3"),sQuery(id+"F0.wireOp",EDGE,"E6.43.4"),sQuery(id+"F0.wireOp",EDGE,"E7"),sQuery(id+"F0.wireOp",EDGE,"E8.1.0"),sQuery(id+"F0.wireOp",EDGE,"E8.2.0"),sQuery(id+"F0.wireOp",EDGE,"E8.3.0"),sQuery(id+"F0.wireOp",EDGE,"E8.4.0"),sQuery(id+"F0.wireOp",EDGE,"E8.5.0"),sQuery(id+"F0.wireOp",EDGE,"E8.6.0"),sQuery(id+"F0.wireOp",EDGE,"E8.7.0"),sQuery(id+"F0.wireOp",EDGE,"E8.8.0"),sQuery(id+"F0.wireOp",EDGE,"E8.9.0"),sQuery(id+"F0.wireOp",EDGE,"E8.10.0"),sQuery(id+"F0.wireOp",EDGE,"E8.11.0"),sQuery(id+"F0.wireOp",EDGE,"E8.12.0"),sQuery(id+"F0.wireOp",EDGE,"E8.13.0"),sQuery(id+"F0.wireOp",EDGE,"E8.14.0"),sQuery(id+"F0.wireOp",EDGE,"E8.15.0"),sQuery(id+"F0.wireOp",EDGE,"E8.16.0"),sQuery(id+"F0.wireOp",EDGE,"E8.17.0"),sQuery(id+"F0.wireOp",EDGE,"E8.18.0"),sQuery(id+"F0.wireOp",EDGE,"E8.19.0"),sQuery(id+"F0.wireOp",EDGE,"E8.20.0"),sQuery(id+"F0.wireOp",EDGE,"E8.21.0"),sQuery(id+"F0.wireOp",EDGE,"E8.22.0"),sQuery(id+"F0.wireOp",EDGE,"E8.23.0"),sQuery(id+"F0.wireOp",EDGE,"E8.24.0"),sQuery(id+"F0.wireOp",EDGE,"E8.25.0"),sQuery(id+"F0.wireOp",EDGE,"E8.26.0"),sQuery(id+"F0.wireOp",EDGE,"E8.27.0"),sQuery(id+"F0.wireOp",EDGE,"E8.28.0"),sQuery(id+"F0.wireOp",EDGE,"E8.29.0"),sQuery(id+"F0.wireOp",EDGE,"E8.30.0"),sQuery(id+"F0.wireOp",EDGE,"E8.31.0"),sQuery(id+"F0.wireOp",EDGE,"E8.32.0"),sQuery(id+"F0.wireOp",EDGE,"E8.33.0"),sQuery(id+"F0.wireOp",EDGE,"E8.34.0"),sQuery(id+"F0.wireOp",EDGE,"E8.35.0"),sQuery(id+"F0.wireOp",EDGE,"E8.36.0"),sQuery(id+"F0.wireOp",EDGE,"E8.37.0"),sQuery(id+"F0.wireOp",EDGE,"E8.38.0"),sQuery(id+"F0.wireOp",EDGE,"E8.39.0"),sQuery(id+"F0.wireOp",EDGE,"E8.40.0"),sQuery(id+"F0.wireOp",EDGE,"E8.41.0"),sQuery(id+"F0.wireOp",EDGE,"E8.42.0"),sQuery(id+"F0.wireOp",EDGE,"E8.43.0")])],"isStart":true})]});}
            var Q41;
            {var subQ0=sQuery(id+"F0.wireOp",EDGE,"E6.40.3");var subQ1=sQuery(id+"F0.wireOp",EDGE,"E6.40.1");Q41=makeQuery(id+"F2.opFillet","BLEND_EDGE",EDGE,{"blendedFrom":[makeQuery(id+"F1.opExtrude","SWEPT_EDGE",EDGE,{"disambiguationData":[OSD([sQuery(id+"F0.wireOp",EDGE,"E6.40.0"),subQ1,subQ0])]}),makeQuery(id+"F1.opExtrude","CAP_FACE",FACE,{"disambiguationData":[OSD([sQuery(id+"F0.wireOp",EDGE,"E0"),sQuery(id+"F0.wireOp",EDGE,"E1"),sQuery(id+"F0.wireOp",EDGE,"E2"),sQuery(id+"F0.wireOp",EDGE,"E4"),sQuery(id+"F0.wireOp",EDGE,"E5"),sQuery(id+"F0.wireOp",EDGE,"E6.1.1"),sQuery(id+"F0.wireOp",EDGE,"E6.1.2"),sQuery(id+"F0.wireOp",EDGE,"E6.1.3"),sQuery(id+"F0.wireOp",EDGE,"E6.1.4"),sQuery(id+"F0.wireOp",EDGE,"E6.2.1"),sQuery(id+"F0.wireOp",EDGE,"E6.2.2"),sQuery(id+"F0.wireOp",EDGE,"E6.2.3"),sQuery(id+"F0.wireOp",EDGE,"E6.2.4"),sQuery(id+"F0.wireOp",EDGE,"E6.3.1"),sQuery(id+"F0.wireOp",EDGE,"E6.3.2"),sQuery(id+"F0.wireOp",EDGE,"E6.3.3"),sQuery(id+"F0.wireOp",EDGE,"E6.3.4"),sQuery(id+"F0.wireOp",EDGE,"E6.4.1"),sQuery(id+"F0.wireOp",EDGE,"E6.4.2"),sQuery(id+"F0.wireOp",EDGE,"E6.4.3"),sQuery(id+"F0.wireOp",EDGE,"E6.4.4"),sQuery(id+"F0.wireOp",EDGE,"E6.5.1"),sQuery(id+"F0.wireOp",EDGE,"E6.5.2"),sQuery(id+"F0.wireOp",EDGE,"E6.5.3"),sQuery(id+"F0.wireOp",EDGE,"E6.5.4"),sQuery(id+"F0.wireOp",EDGE,"E6.6.1"),sQuery(id+"F0.wireOp",EDGE,"E6.6.2"),sQuery(id+"F0.wireOp",EDGE,"E6.6.3"),sQuery(id+"F0.wireOp",EDGE,"E6.6.4"),sQuery(id+"F0.wireOp",EDGE,"E6.7.1"),sQuery(id+"F0.wireOp",EDGE,"E6.7.2"),sQuery(id+"F0.wireOp",EDGE,"E6.7.3"),sQuery(id+"F0.wireOp",EDGE,"E6.7.4"),sQuery(id+"F0.wireOp",EDGE,"E6.8.1"),sQuery(id+"F0.wireOp",EDGE,"E6.8.2"),sQuery(id+"F0.wireOp",EDGE,"E6.8.3"),sQuery(id+"F0.wireOp",EDGE,"E6.8.4"),sQuery(id+"F0.wireOp",EDGE,"E6.9.1"),sQuery(id+"F0.wireOp",EDGE,"E6.9.2"),sQuery(id+"F0.wireOp",EDGE,"E6.9.3"),sQuery(id+"F0.wireOp",EDGE,"E6.9.4"),sQuery(id+"F0.wireOp",EDGE,"E6.10.1"),sQuery(id+"F0.wireOp",EDGE,"E6.10.2"),sQuery(id+"F0.wireOp",EDGE,"E6.10.3"),sQuery(id+"F0.wireOp",EDGE,"E6.10.4"),sQuery(id+"F0.wireOp",EDGE,"E6.11.1"),sQuery(id+"F0.wireOp",EDGE,"E6.11.2"),sQuery(id+"F0.wireOp",EDGE,"E6.11.3"),sQuery(id+"F0.wireOp",EDGE,"E6.11.4"),sQuery(id+"F0.wireOp",EDGE,"E6.12.1"),sQuery(id+"F0.wireOp",EDGE,"E6.12.2"),sQuery(id+"F0.wireOp",EDGE,"E6.12.3"),sQuery(id+"F0.wireOp",EDGE,"E6.12.4"),sQuery(id+"F0.wireOp",EDGE,"E6.13.1"),sQuery(id+"F0.wireOp",EDGE,"E6.13.2"),sQuery(id+"F0.wireOp",EDGE,"E6.13.3"),sQuery(id+"F0.wireOp",EDGE,"E6.13.4"),sQuery(id+"F0.wireOp",EDGE,"E6.14.1"),sQuery(id+"F0.wireOp",EDGE,"E6.14.2"),sQuery(id+"F0.wireOp",EDGE,"E6.14.3"),sQuery(id+"F0.wireOp",EDGE,"E6.14.4"),sQuery(id+"F0.wireOp",EDGE,"E6.15.1"),sQuery(id+"F0.wireOp",EDGE,"E6.15.2"),sQuery(id+"F0.wireOp",EDGE,"E6.15.3"),sQuery(id+"F0.wireOp",EDGE,"E6.15.4"),sQuery(id+"F0.wireOp",EDGE,"E6.16.1"),sQuery(id+"F0.wireOp",EDGE,"E6.16.2"),sQuery(id+"F0.wireOp",EDGE,"E6.16.3"),sQuery(id+"F0.wireOp",EDGE,"E6.16.4"),sQuery(id+"F0.wireOp",EDGE,"E6.17.1"),sQuery(id+"F0.wireOp",EDGE,"E6.17.2"),sQuery(id+"F0.wireOp",EDGE,"E6.17.3"),sQuery(id+"F0.wireOp",EDGE,"E6.17.4"),sQuery(id+"F0.wireOp",EDGE,"E6.18.1"),sQuery(id+"F0.wireOp",EDGE,"E6.18.2"),sQuery(id+"F0.wireOp",EDGE,"E6.18.3"),sQuery(id+"F0.wireOp",EDGE,"E6.18.4"),sQuery(id+"F0.wireOp",EDGE,"E6.19.1"),sQuery(id+"F0.wireOp",EDGE,"E6.19.2"),sQuery(id+"F0.wireOp",EDGE,"E6.19.3"),sQuery(id+"F0.wireOp",EDGE,"E6.19.4"),sQuery(id+"F0.wireOp",EDGE,"E6.20.1"),sQuery(id+"F0.wireOp",EDGE,"E6.20.2"),sQuery(id+"F0.wireOp",EDGE,"E6.20.3"),sQuery(id+"F0.wireOp",EDGE,"E6.20.4"),sQuery(id+"F0.wireOp",EDGE,"E6.21.1"),sQuery(id+"F0.wireOp",EDGE,"E6.21.2"),sQuery(id+"F0.wireOp",EDGE,"E6.21.3"),sQuery(id+"F0.wireOp",EDGE,"E6.21.4"),sQuery(id+"F0.wireOp",EDGE,"E6.22.1"),sQuery(id+"F0.wireOp",EDGE,"E6.22.2"),sQuery(id+"F0.wireOp",EDGE,"E6.22.3"),sQuery(id+"F0.wireOp",EDGE,"E6.22.4"),sQuery(id+"F0.wireOp",EDGE,"E6.23.1"),sQuery(id+"F0.wireOp",EDGE,"E6.23.2"),sQuery(id+"F0.wireOp",EDGE,"E6.23.3"),sQuery(id+"F0.wireOp",EDGE,"E6.23.4"),sQuery(id+"F0.wireOp",EDGE,"E6.24.1"),sQuery(id+"F0.wireOp",EDGE,"E6.24.2"),sQuery(id+"F0.wireOp",EDGE,"E6.24.3"),sQuery(id+"F0.wireOp",EDGE,"E6.24.4"),sQuery(id+"F0.wireOp",EDGE,"E6.25.1"),sQuery(id+"F0.wireOp",EDGE,"E6.25.2"),sQuery(id+"F0.wireOp",EDGE,"E6.25.3"),sQuery(id+"F0.wireOp",EDGE,"E6.25.4"),sQuery(id+"F0.wireOp",EDGE,"E6.26.1"),sQuery(id+"F0.wireOp",EDGE,"E6.26.2"),sQuery(id+"F0.wireOp",EDGE,"E6.26.3"),sQuery(id+"F0.wireOp",EDGE,"E6.26.4"),sQuery(id+"F0.wireOp",EDGE,"E6.27.1"),sQuery(id+"F0.wireOp",EDGE,"E6.27.2"),sQuery(id+"F0.wireOp",EDGE,"E6.27.3"),sQuery(id+"F0.wireOp",EDGE,"E6.27.4"),sQuery(id+"F0.wireOp",EDGE,"E6.28.1"),sQuery(id+"F0.wireOp",EDGE,"E6.28.2"),sQuery(id+"F0.wireOp",EDGE,"E6.28.3"),sQuery(id+"F0.wireOp",EDGE,"E6.28.4"),sQuery(id+"F0.wireOp",EDGE,"E6.29.1"),sQuery(id+"F0.wireOp",EDGE,"E6.29.2"),sQuery(id+"F0.wireOp",EDGE,"E6.29.3"),sQuery(id+"F0.wireOp",EDGE,"E6.29.4"),sQuery(id+"F0.wireOp",EDGE,"E6.30.1"),sQuery(id+"F0.wireOp",EDGE,"E6.30.2"),sQuery(id+"F0.wireOp",EDGE,"E6.30.3"),sQuery(id+"F0.wireOp",EDGE,"E6.30.4"),sQuery(id+"F0.wireOp",EDGE,"E6.31.1"),sQuery(id+"F0.wireOp",EDGE,"E6.31.2"),sQuery(id+"F0.wireOp",EDGE,"E6.31.3"),sQuery(id+"F0.wireOp",EDGE,"E6.31.4"),sQuery(id+"F0.wireOp",EDGE,"E6.32.1"),sQuery(id+"F0.wireOp",EDGE,"E6.32.2"),sQuery(id+"F0.wireOp",EDGE,"E6.32.3"),sQuery(id+"F0.wireOp",EDGE,"E6.32.4"),sQuery(id+"F0.wireOp",EDGE,"E6.33.1"),sQuery(id+"F0.wireOp",EDGE,"E6.33.2"),sQuery(id+"F0.wireOp",EDGE,"E6.33.3"),sQuery(id+"F0.wireOp",EDGE,"E6.33.4"),sQuery(id+"F0.wireOp",EDGE,"E6.34.1"),sQuery(id+"F0.wireOp",EDGE,"E6.34.2"),sQuery(id+"F0.wireOp",EDGE,"E6.34.3"),sQuery(id+"F0.wireOp",EDGE,"E6.34.4"),sQuery(id+"F0.wireOp",EDGE,"E6.35.1"),sQuery(id+"F0.wireOp",EDGE,"E6.35.2"),sQuery(id+"F0.wireOp",EDGE,"E6.35.3"),sQuery(id+"F0.wireOp",EDGE,"E6.35.4"),sQuery(id+"F0.wireOp",EDGE,"E6.36.1"),sQuery(id+"F0.wireOp",EDGE,"E6.36.2"),sQuery(id+"F0.wireOp",EDGE,"E6.36.3"),sQuery(id+"F0.wireOp",EDGE,"E6.36.4"),sQuery(id+"F0.wireOp",EDGE,"E6.37.1"),sQuery(id+"F0.wireOp",EDGE,"E6.37.2"),sQuery(id+"F0.wireOp",EDGE,"E6.37.3"),sQuery(id+"F0.wireOp",EDGE,"E6.37.4"),sQuery(id+"F0.wireOp",EDGE,"E6.38.1"),sQuery(id+"F0.wireOp",EDGE,"E6.38.2"),sQuery(id+"F0.wireOp",EDGE,"E6.38.3"),sQuery(id+"F0.wireOp",EDGE,"E6.38.4"),sQuery(id+"F0.wireOp",EDGE,"E6.39.1"),sQuery(id+"F0.wireOp",EDGE,"E6.39.2"),sQuery(id+"F0.wireOp",EDGE,"E6.39.3"),sQuery(id+"F0.wireOp",EDGE,"E6.39.4"),subQ1,sQuery(id+"F0.wireOp",EDGE,"E6.40.2"),subQ0,sQuery(id+"F0.wireOp",EDGE,"E6.40.4"),sQuery(id+"F0.wireOp",EDGE,"E6.41.1"),sQuery(id+"F0.wireOp",EDGE,"E6.41.2"),sQuery(id+"F0.wireOp",EDGE,"E6.41.3"),sQuery(id+"F0.wireOp",EDGE,"E6.41.4"),sQuery(id+"F0.wireOp",EDGE,"E6.42.1"),sQuery(id+"F0.wireOp",EDGE,"E6.42.2"),sQuery(id+"F0.wireOp",EDGE,"E6.42.3"),sQuery(id+"F0.wireOp",EDGE,"E6.42.4"),sQuery(id+"F0.wireOp",EDGE,"E6.43.1"),sQuery(id+"F0.wireOp",EDGE,"E6.43.2"),sQuery(id+"F0.wireOp",EDGE,"E6.43.3"),sQuery(id+"F0.wireOp",EDGE,"E6.43.4"),sQuery(id+"F0.wireOp",EDGE,"E7"),sQuery(id+"F0.wireOp",EDGE,"E8.1.0"),sQuery(id+"F0.wireOp",EDGE,"E8.2.0"),sQuery(id+"F0.wireOp",EDGE,"E8.3.0"),sQuery(id+"F0.wireOp",EDGE,"E8.4.0"),sQuery(id+"F0.wireOp",EDGE,"E8.5.0"),sQuery(id+"F0.wireOp",EDGE,"E8.6.0"),sQuery(id+"F0.wireOp",EDGE,"E8.7.0"),sQuery(id+"F0.wireOp",EDGE,"E8.8.0"),sQuery(id+"F0.wireOp",EDGE,"E8.9.0"),sQuery(id+"F0.wireOp",EDGE,"E8.10.0"),sQuery(id+"F0.wireOp",EDGE,"E8.11.0"),sQuery(id+"F0.wireOp",EDGE,"E8.12.0"),sQuery(id+"F0.wireOp",EDGE,"E8.13.0"),sQuery(id+"F0.wireOp",EDGE,"E8.14.0"),sQuery(id+"F0.wireOp",EDGE,"E8.15.0"),sQuery(id+"F0.wireOp",EDGE,"E8.16.0"),sQuery(id+"F0.wireOp",EDGE,"E8.17.0"),sQuery(id+"F0.wireOp",EDGE,"E8.18.0"),sQuery(id+"F0.wireOp",EDGE,"E8.19.0"),sQuery(id+"F0.wireOp",EDGE,"E8.20.0"),sQuery(id+"F0.wireOp",EDGE,"E8.21.0"),sQuery(id+"F0.wireOp",EDGE,"E8.22.0"),sQuery(id+"F0.wireOp",EDGE,"E8.23.0"),sQuery(id+"F0.wireOp",EDGE,"E8.24.0"),sQuery(id+"F0.wireOp",EDGE,"E8.25.0"),sQuery(id+"F0.wireOp",EDGE,"E8.26.0"),sQuery(id+"F0.wireOp",EDGE,"E8.27.0"),sQuery(id+"F0.wireOp",EDGE,"E8.28.0"),sQuery(id+"F0.wireOp",EDGE,"E8.29.0"),sQuery(id+"F0.wireOp",EDGE,"E8.30.0"),sQuery(id+"F0.wireOp",EDGE,"E8.31.0"),sQuery(id+"F0.wireOp",EDGE,"E8.32.0"),sQuery(id+"F0.wireOp",EDGE,"E8.33.0"),sQuery(id+"F0.wireOp",EDGE,"E8.34.0"),sQuery(id+"F0.wireOp",EDGE,"E8.35.0"),sQuery(id+"F0.wireOp",EDGE,"E8.36.0"),sQuery(id+"F0.wireOp",EDGE,"E8.37.0"),sQuery(id+"F0.wireOp",EDGE,"E8.38.0"),sQuery(id+"F0.wireOp",EDGE,"E8.39.0"),sQuery(id+"F0.wireOp",EDGE,"E8.40.0"),sQuery(id+"F0.wireOp",EDGE,"E8.41.0"),sQuery(id+"F0.wireOp",EDGE,"E8.42.0"),sQuery(id+"F0.wireOp",EDGE,"E8.43.0")])],"isStart":true})],"blendedInto":[makeQuery(id+"F1.opExtrude","CAP_FACE",FACE,{"disambiguationData":[OSD([sQuery(id+"F0.wireOp",EDGE,"E0"),sQuery(id+"F0.wireOp",EDGE,"E1"),sQuery(id+"F0.wireOp",EDGE,"E2"),sQuery(id+"F0.wireOp",EDGE,"E4"),sQuery(id+"F0.wireOp",EDGE,"E5"),sQuery(id+"F0.wireOp",EDGE,"E6.1.1"),sQuery(id+"F0.wireOp",EDGE,"E6.1.2"),sQuery(id+"F0.wireOp",EDGE,"E6.1.3"),sQuery(id+"F0.wireOp",EDGE,"E6.1.4"),sQuery(id+"F0.wireOp",EDGE,"E6.2.1"),sQuery(id+"F0.wireOp",EDGE,"E6.2.2"),sQuery(id+"F0.wireOp",EDGE,"E6.2.3"),sQuery(id+"F0.wireOp",EDGE,"E6.2.4"),sQuery(id+"F0.wireOp",EDGE,"E6.3.1"),sQuery(id+"F0.wireOp",EDGE,"E6.3.2"),sQuery(id+"F0.wireOp",EDGE,"E6.3.3"),sQuery(id+"F0.wireOp",EDGE,"E6.3.4"),sQuery(id+"F0.wireOp",EDGE,"E6.4.1"),sQuery(id+"F0.wireOp",EDGE,"E6.4.2"),sQuery(id+"F0.wireOp",EDGE,"E6.4.3"),sQuery(id+"F0.wireOp",EDGE,"E6.4.4"),sQuery(id+"F0.wireOp",EDGE,"E6.5.1"),sQuery(id+"F0.wireOp",EDGE,"E6.5.2"),sQuery(id+"F0.wireOp",EDGE,"E6.5.3"),sQuery(id+"F0.wireOp",EDGE,"E6.5.4"),sQuery(id+"F0.wireOp",EDGE,"E6.6.1"),sQuery(id+"F0.wireOp",EDGE,"E6.6.2"),sQuery(id+"F0.wireOp",EDGE,"E6.6.3"),sQuery(id+"F0.wireOp",EDGE,"E6.6.4"),sQuery(id+"F0.wireOp",EDGE,"E6.7.1"),sQuery(id+"F0.wireOp",EDGE,"E6.7.2"),sQuery(id+"F0.wireOp",EDGE,"E6.7.3"),sQuery(id+"F0.wireOp",EDGE,"E6.7.4"),sQuery(id+"F0.wireOp",EDGE,"E6.8.1"),sQuery(id+"F0.wireOp",EDGE,"E6.8.2"),sQuery(id+"F0.wireOp",EDGE,"E6.8.3"),sQuery(id+"F0.wireOp",EDGE,"E6.8.4"),sQuery(id+"F0.wireOp",EDGE,"E6.9.1"),sQuery(id+"F0.wireOp",EDGE,"E6.9.2"),sQuery(id+"F0.wireOp",EDGE,"E6.9.3"),sQuery(id+"F0.wireOp",EDGE,"E6.9.4"),sQuery(id+"F0.wireOp",EDGE,"E6.10.1"),sQuery(id+"F0.wireOp",EDGE,"E6.10.2"),sQuery(id+"F0.wireOp",EDGE,"E6.10.3"),sQuery(id+"F0.wireOp",EDGE,"E6.10.4"),sQuery(id+"F0.wireOp",EDGE,"E6.11.1"),sQuery(id+"F0.wireOp",EDGE,"E6.11.2"),sQuery(id+"F0.wireOp",EDGE,"E6.11.3"),sQuery(id+"F0.wireOp",EDGE,"E6.11.4"),sQuery(id+"F0.wireOp",EDGE,"E6.12.1"),sQuery(id+"F0.wireOp",EDGE,"E6.12.2"),sQuery(id+"F0.wireOp",EDGE,"E6.12.3"),sQuery(id+"F0.wireOp",EDGE,"E6.12.4"),sQuery(id+"F0.wireOp",EDGE,"E6.13.1"),sQuery(id+"F0.wireOp",EDGE,"E6.13.2"),sQuery(id+"F0.wireOp",EDGE,"E6.13.3"),sQuery(id+"F0.wireOp",EDGE,"E6.13.4"),sQuery(id+"F0.wireOp",EDGE,"E6.14.1"),sQuery(id+"F0.wireOp",EDGE,"E6.14.2"),sQuery(id+"F0.wireOp",EDGE,"E6.14.3"),sQuery(id+"F0.wireOp",EDGE,"E6.14.4"),sQuery(id+"F0.wireOp",EDGE,"E6.15.1"),sQuery(id+"F0.wireOp",EDGE,"E6.15.2"),sQuery(id+"F0.wireOp",EDGE,"E6.15.3"),sQuery(id+"F0.wireOp",EDGE,"E6.15.4"),sQuery(id+"F0.wireOp",EDGE,"E6.16.1"),sQuery(id+"F0.wireOp",EDGE,"E6.16.2"),sQuery(id+"F0.wireOp",EDGE,"E6.16.3"),sQuery(id+"F0.wireOp",EDGE,"E6.16.4"),sQuery(id+"F0.wireOp",EDGE,"E6.17.1"),sQuery(id+"F0.wireOp",EDGE,"E6.17.2"),sQuery(id+"F0.wireOp",EDGE,"E6.17.3"),sQuery(id+"F0.wireOp",EDGE,"E6.17.4"),sQuery(id+"F0.wireOp",EDGE,"E6.18.1"),sQuery(id+"F0.wireOp",EDGE,"E6.18.2"),sQuery(id+"F0.wireOp",EDGE,"E6.18.3"),sQuery(id+"F0.wireOp",EDGE,"E6.18.4"),sQuery(id+"F0.wireOp",EDGE,"E6.19.1"),sQuery(id+"F0.wireOp",EDGE,"E6.19.2"),sQuery(id+"F0.wireOp",EDGE,"E6.19.3"),sQuery(id+"F0.wireOp",EDGE,"E6.19.4"),sQuery(id+"F0.wireOp",EDGE,"E6.20.1"),sQuery(id+"F0.wireOp",EDGE,"E6.20.2"),sQuery(id+"F0.wireOp",EDGE,"E6.20.3"),sQuery(id+"F0.wireOp",EDGE,"E6.20.4"),sQuery(id+"F0.wireOp",EDGE,"E6.21.1"),sQuery(id+"F0.wireOp",EDGE,"E6.21.2"),sQuery(id+"F0.wireOp",EDGE,"E6.21.3"),sQuery(id+"F0.wireOp",EDGE,"E6.21.4"),sQuery(id+"F0.wireOp",EDGE,"E6.22.1"),sQuery(id+"F0.wireOp",EDGE,"E6.22.2"),sQuery(id+"F0.wireOp",EDGE,"E6.22.3"),sQuery(id+"F0.wireOp",EDGE,"E6.22.4"),sQuery(id+"F0.wireOp",EDGE,"E6.23.1"),sQuery(id+"F0.wireOp",EDGE,"E6.23.2"),sQuery(id+"F0.wireOp",EDGE,"E6.23.3"),sQuery(id+"F0.wireOp",EDGE,"E6.23.4"),sQuery(id+"F0.wireOp",EDGE,"E6.24.1"),sQuery(id+"F0.wireOp",EDGE,"E6.24.2"),sQuery(id+"F0.wireOp",EDGE,"E6.24.3"),sQuery(id+"F0.wireOp",EDGE,"E6.24.4"),sQuery(id+"F0.wireOp",EDGE,"E6.25.1"),sQuery(id+"F0.wireOp",EDGE,"E6.25.2"),sQuery(id+"F0.wireOp",EDGE,"E6.25.3"),sQuery(id+"F0.wireOp",EDGE,"E6.25.4"),sQuery(id+"F0.wireOp",EDGE,"E6.26.1"),sQuery(id+"F0.wireOp",EDGE,"E6.26.2"),sQuery(id+"F0.wireOp",EDGE,"E6.26.3"),sQuery(id+"F0.wireOp",EDGE,"E6.26.4"),sQuery(id+"F0.wireOp",EDGE,"E6.27.1"),sQuery(id+"F0.wireOp",EDGE,"E6.27.2"),sQuery(id+"F0.wireOp",EDGE,"E6.27.3"),sQuery(id+"F0.wireOp",EDGE,"E6.27.4"),sQuery(id+"F0.wireOp",EDGE,"E6.28.1"),sQuery(id+"F0.wireOp",EDGE,"E6.28.2"),sQuery(id+"F0.wireOp",EDGE,"E6.28.3"),sQuery(id+"F0.wireOp",EDGE,"E6.28.4"),sQuery(id+"F0.wireOp",EDGE,"E6.29.1"),sQuery(id+"F0.wireOp",EDGE,"E6.29.2"),sQuery(id+"F0.wireOp",EDGE,"E6.29.3"),sQuery(id+"F0.wireOp",EDGE,"E6.29.4"),sQuery(id+"F0.wireOp",EDGE,"E6.30.1"),sQuery(id+"F0.wireOp",EDGE,"E6.30.2"),sQuery(id+"F0.wireOp",EDGE,"E6.30.3"),sQuery(id+"F0.wireOp",EDGE,"E6.30.4"),sQuery(id+"F0.wireOp",EDGE,"E6.31.1"),sQuery(id+"F0.wireOp",EDGE,"E6.31.2"),sQuery(id+"F0.wireOp",EDGE,"E6.31.3"),sQuery(id+"F0.wireOp",EDGE,"E6.31.4"),sQuery(id+"F0.wireOp",EDGE,"E6.32.1"),sQuery(id+"F0.wireOp",EDGE,"E6.32.2"),sQuery(id+"F0.wireOp",EDGE,"E6.32.3"),sQuery(id+"F0.wireOp",EDGE,"E6.32.4"),sQuery(id+"F0.wireOp",EDGE,"E6.33.1"),sQuery(id+"F0.wireOp",EDGE,"E6.33.2"),sQuery(id+"F0.wireOp",EDGE,"E6.33.3"),sQuery(id+"F0.wireOp",EDGE,"E6.33.4"),sQuery(id+"F0.wireOp",EDGE,"E6.34.1"),sQuery(id+"F0.wireOp",EDGE,"E6.34.2"),sQuery(id+"F0.wireOp",EDGE,"E6.34.3"),sQuery(id+"F0.wireOp",EDGE,"E6.34.4"),sQuery(id+"F0.wireOp",EDGE,"E6.35.1"),sQuery(id+"F0.wireOp",EDGE,"E6.35.2"),sQuery(id+"F0.wireOp",EDGE,"E6.35.3"),sQuery(id+"F0.wireOp",EDGE,"E6.35.4"),sQuery(id+"F0.wireOp",EDGE,"E6.36.1"),sQuery(id+"F0.wireOp",EDGE,"E6.36.2"),sQuery(id+"F0.wireOp",EDGE,"E6.36.3"),sQuery(id+"F0.wireOp",EDGE,"E6.36.4"),sQuery(id+"F0.wireOp",EDGE,"E6.37.1"),sQuery(id+"F0.wireOp",EDGE,"E6.37.2"),sQuery(id+"F0.wireOp",EDGE,"E6.37.3"),sQuery(id+"F0.wireOp",EDGE,"E6.37.4"),sQuery(id+"F0.wireOp",EDGE,"E6.38.1"),sQuery(id+"F0.wireOp",EDGE,"E6.38.2"),sQuery(id+"F0.wireOp",EDGE,"E6.38.3"),sQuery(id+"F0.wireOp",EDGE,"E6.38.4"),sQuery(id+"F0.wireOp",EDGE,"E6.39.1"),sQuery(id+"F0.wireOp",EDGE,"E6.39.2"),sQuery(id+"F0.wireOp",EDGE,"E6.39.3"),sQuery(id+"F0.wireOp",EDGE,"E6.39.4"),subQ1,sQuery(id+"F0.wireOp",EDGE,"E6.40.2"),subQ0,sQuery(id+"F0.wireOp",EDGE,"E6.40.4"),sQuery(id+"F0.wireOp",EDGE,"E6.41.1"),sQuery(id+"F0.wireOp",EDGE,"E6.41.2"),sQuery(id+"F0.wireOp",EDGE,"E6.41.3"),sQuery(id+"F0.wireOp",EDGE,"E6.41.4"),sQuery(id+"F0.wireOp",EDGE,"E6.42.1"),sQuery(id+"F0.wireOp",EDGE,"E6.42.2"),sQuery(id+"F0.wireOp",EDGE,"E6.42.3"),sQuery(id+"F0.wireOp",EDGE,"E6.42.4"),sQuery(id+"F0.wireOp",EDGE,"E6.43.1"),sQuery(id+"F0.wireOp",EDGE,"E6.43.2"),sQuery(id+"F0.wireOp",EDGE,"E6.43.3"),sQuery(id+"F0.wireOp",EDGE,"E6.43.4"),sQuery(id+"F0.wireOp",EDGE,"E7"),sQuery(id+"F0.wireOp",EDGE,"E8.1.0"),sQuery(id+"F0.wireOp",EDGE,"E8.2.0"),sQuery(id+"F0.wireOp",EDGE,"E8.3.0"),sQuery(id+"F0.wireOp",EDGE,"E8.4.0"),sQuery(id+"F0.wireOp",EDGE,"E8.5.0"),sQuery(id+"F0.wireOp",EDGE,"E8.6.0"),sQuery(id+"F0.wireOp",EDGE,"E8.7.0"),sQuery(id+"F0.wireOp",EDGE,"E8.8.0"),sQuery(id+"F0.wireOp",EDGE,"E8.9.0"),sQuery(id+"F0.wireOp",EDGE,"E8.10.0"),sQuery(id+"F0.wireOp",EDGE,"E8.11.0"),sQuery(id+"F0.wireOp",EDGE,"E8.12.0"),sQuery(id+"F0.wireOp",EDGE,"E8.13.0"),sQuery(id+"F0.wireOp",EDGE,"E8.14.0"),sQuery(id+"F0.wireOp",EDGE,"E8.15.0"),sQuery(id+"F0.wireOp",EDGE,"E8.16.0"),sQuery(id+"F0.wireOp",EDGE,"E8.17.0"),sQuery(id+"F0.wireOp",EDGE,"E8.18.0"),sQuery(id+"F0.wireOp",EDGE,"E8.19.0"),sQuery(id+"F0.wireOp",EDGE,"E8.20.0"),sQuery(id+"F0.wireOp",EDGE,"E8.21.0"),sQuery(id+"F0.wireOp",EDGE,"E8.22.0"),sQuery(id+"F0.wireOp",EDGE,"E8.23.0"),sQuery(id+"F0.wireOp",EDGE,"E8.24.0"),sQuery(id+"F0.wireOp",EDGE,"E8.25.0"),sQuery(id+"F0.wireOp",EDGE,"E8.26.0"),sQuery(id+"F0.wireOp",EDGE,"E8.27.0"),sQuery(id+"F0.wireOp",EDGE,"E8.28.0"),sQuery(id+"F0.wireOp",EDGE,"E8.29.0"),sQuery(id+"F0.wireOp",EDGE,"E8.30.0"),sQuery(id+"F0.wireOp",EDGE,"E8.31.0"),sQuery(id+"F0.wireOp",EDGE,"E8.32.0"),sQuery(id+"F0.wireOp",EDGE,"E8.33.0"),sQuery(id+"F0.wireOp",EDGE,"E8.34.0"),sQuery(id+"F0.wireOp",EDGE,"E8.35.0"),sQuery(id+"F0.wireOp",EDGE,"E8.36.0"),sQuery(id+"F0.wireOp",EDGE,"E8.37.0"),sQuery(id+"F0.wireOp",EDGE,"E8.38.0"),sQuery(id+"F0.wireOp",EDGE,"E8.39.0"),sQuery(id+"F0.wireOp",EDGE,"E8.40.0"),sQuery(id+"F0.wireOp",EDGE,"E8.41.0"),sQuery(id+"F0.wireOp",EDGE,"E8.42.0"),sQuery(id+"F0.wireOp",EDGE,"E8.43.0")])],"isStart":true})]});}
            var Q42;
            {var subQ0=sQuery(id+"F0.wireOp",EDGE,"E6.42.3");var subQ1=sQuery(id+"F0.wireOp",EDGE,"E6.42.1");Q42=makeQuery(id+"F2.opFillet","BLEND_EDGE",EDGE,{"blendedFrom":[makeQuery(id+"F1.opExtrude","SWEPT_EDGE",EDGE,{"disambiguationData":[OSD([sQuery(id+"F0.wireOp",EDGE,"E6.42.0"),subQ1,subQ0])]}),makeQuery(id+"F1.opExtrude","CAP_FACE",FACE,{"disambiguationData":[OSD([sQuery(id+"F0.wireOp",EDGE,"E0"),sQuery(id+"F0.wireOp",EDGE,"E1"),sQuery(id+"F0.wireOp",EDGE,"E2"),sQuery(id+"F0.wireOp",EDGE,"E4"),sQuery(id+"F0.wireOp",EDGE,"E5"),sQuery(id+"F0.wireOp",EDGE,"E6.1.1"),sQuery(id+"F0.wireOp",EDGE,"E6.1.2"),sQuery(id+"F0.wireOp",EDGE,"E6.1.3"),sQuery(id+"F0.wireOp",EDGE,"E6.1.4"),sQuery(id+"F0.wireOp",EDGE,"E6.2.1"),sQuery(id+"F0.wireOp",EDGE,"E6.2.2"),sQuery(id+"F0.wireOp",EDGE,"E6.2.3"),sQuery(id+"F0.wireOp",EDGE,"E6.2.4"),sQuery(id+"F0.wireOp",EDGE,"E6.3.1"),sQuery(id+"F0.wireOp",EDGE,"E6.3.2"),sQuery(id+"F0.wireOp",EDGE,"E6.3.3"),sQuery(id+"F0.wireOp",EDGE,"E6.3.4"),sQuery(id+"F0.wireOp",EDGE,"E6.4.1"),sQuery(id+"F0.wireOp",EDGE,"E6.4.2"),sQuery(id+"F0.wireOp",EDGE,"E6.4.3"),sQuery(id+"F0.wireOp",EDGE,"E6.4.4"),sQuery(id+"F0.wireOp",EDGE,"E6.5.1"),sQuery(id+"F0.wireOp",EDGE,"E6.5.2"),sQuery(id+"F0.wireOp",EDGE,"E6.5.3"),sQuery(id+"F0.wireOp",EDGE,"E6.5.4"),sQuery(id+"F0.wireOp",EDGE,"E6.6.1"),sQuery(id+"F0.wireOp",EDGE,"E6.6.2"),sQuery(id+"F0.wireOp",EDGE,"E6.6.3"),sQuery(id+"F0.wireOp",EDGE,"E6.6.4"),sQuery(id+"F0.wireOp",EDGE,"E6.7.1"),sQuery(id+"F0.wireOp",EDGE,"E6.7.2"),sQuery(id+"F0.wireOp",EDGE,"E6.7.3"),sQuery(id+"F0.wireOp",EDGE,"E6.7.4"),sQuery(id+"F0.wireOp",EDGE,"E6.8.1"),sQuery(id+"F0.wireOp",EDGE,"E6.8.2"),sQuery(id+"F0.wireOp",EDGE,"E6.8.3"),sQuery(id+"F0.wireOp",EDGE,"E6.8.4"),sQuery(id+"F0.wireOp",EDGE,"E6.9.1"),sQuery(id+"F0.wireOp",EDGE,"E6.9.2"),sQuery(id+"F0.wireOp",EDGE,"E6.9.3"),sQuery(id+"F0.wireOp",EDGE,"E6.9.4"),sQuery(id+"F0.wireOp",EDGE,"E6.10.1"),sQuery(id+"F0.wireOp",EDGE,"E6.10.2"),sQuery(id+"F0.wireOp",EDGE,"E6.10.3"),sQuery(id+"F0.wireOp",EDGE,"E6.10.4"),sQuery(id+"F0.wireOp",EDGE,"E6.11.1"),sQuery(id+"F0.wireOp",EDGE,"E6.11.2"),sQuery(id+"F0.wireOp",EDGE,"E6.11.3"),sQuery(id+"F0.wireOp",EDGE,"E6.11.4"),sQuery(id+"F0.wireOp",EDGE,"E6.12.1"),sQuery(id+"F0.wireOp",EDGE,"E6.12.2"),sQuery(id+"F0.wireOp",EDGE,"E6.12.3"),sQuery(id+"F0.wireOp",EDGE,"E6.12.4"),sQuery(id+"F0.wireOp",EDGE,"E6.13.1"),sQuery(id+"F0.wireOp",EDGE,"E6.13.2"),sQuery(id+"F0.wireOp",EDGE,"E6.13.3"),sQuery(id+"F0.wireOp",EDGE,"E6.13.4"),sQuery(id+"F0.wireOp",EDGE,"E6.14.1"),sQuery(id+"F0.wireOp",EDGE,"E6.14.2"),sQuery(id+"F0.wireOp",EDGE,"E6.14.3"),sQuery(id+"F0.wireOp",EDGE,"E6.14.4"),sQuery(id+"F0.wireOp",EDGE,"E6.15.1"),sQuery(id+"F0.wireOp",EDGE,"E6.15.2"),sQuery(id+"F0.wireOp",EDGE,"E6.15.3"),sQuery(id+"F0.wireOp",EDGE,"E6.15.4"),sQuery(id+"F0.wireOp",EDGE,"E6.16.1"),sQuery(id+"F0.wireOp",EDGE,"E6.16.2"),sQuery(id+"F0.wireOp",EDGE,"E6.16.3"),sQuery(id+"F0.wireOp",EDGE,"E6.16.4"),sQuery(id+"F0.wireOp",EDGE,"E6.17.1"),sQuery(id+"F0.wireOp",EDGE,"E6.17.2"),sQuery(id+"F0.wireOp",EDGE,"E6.17.3"),sQuery(id+"F0.wireOp",EDGE,"E6.17.4"),sQuery(id+"F0.wireOp",EDGE,"E6.18.1"),sQuery(id+"F0.wireOp",EDGE,"E6.18.2"),sQuery(id+"F0.wireOp",EDGE,"E6.18.3"),sQuery(id+"F0.wireOp",EDGE,"E6.18.4"),sQuery(id+"F0.wireOp",EDGE,"E6.19.1"),sQuery(id+"F0.wireOp",EDGE,"E6.19.2"),sQuery(id+"F0.wireOp",EDGE,"E6.19.3"),sQuery(id+"F0.wireOp",EDGE,"E6.19.4"),sQuery(id+"F0.wireOp",EDGE,"E6.20.1"),sQuery(id+"F0.wireOp",EDGE,"E6.20.2"),sQuery(id+"F0.wireOp",EDGE,"E6.20.3"),sQuery(id+"F0.wireOp",EDGE,"E6.20.4"),sQuery(id+"F0.wireOp",EDGE,"E6.21.1"),sQuery(id+"F0.wireOp",EDGE,"E6.21.2"),sQuery(id+"F0.wireOp",EDGE,"E6.21.3"),sQuery(id+"F0.wireOp",EDGE,"E6.21.4"),sQuery(id+"F0.wireOp",EDGE,"E6.22.1"),sQuery(id+"F0.wireOp",EDGE,"E6.22.2"),sQuery(id+"F0.wireOp",EDGE,"E6.22.3"),sQuery(id+"F0.wireOp",EDGE,"E6.22.4"),sQuery(id+"F0.wireOp",EDGE,"E6.23.1"),sQuery(id+"F0.wireOp",EDGE,"E6.23.2"),sQuery(id+"F0.wireOp",EDGE,"E6.23.3"),sQuery(id+"F0.wireOp",EDGE,"E6.23.4"),sQuery(id+"F0.wireOp",EDGE,"E6.24.1"),sQuery(id+"F0.wireOp",EDGE,"E6.24.2"),sQuery(id+"F0.wireOp",EDGE,"E6.24.3"),sQuery(id+"F0.wireOp",EDGE,"E6.24.4"),sQuery(id+"F0.wireOp",EDGE,"E6.25.1"),sQuery(id+"F0.wireOp",EDGE,"E6.25.2"),sQuery(id+"F0.wireOp",EDGE,"E6.25.3"),sQuery(id+"F0.wireOp",EDGE,"E6.25.4"),sQuery(id+"F0.wireOp",EDGE,"E6.26.1"),sQuery(id+"F0.wireOp",EDGE,"E6.26.2"),sQuery(id+"F0.wireOp",EDGE,"E6.26.3"),sQuery(id+"F0.wireOp",EDGE,"E6.26.4"),sQuery(id+"F0.wireOp",EDGE,"E6.27.1"),sQuery(id+"F0.wireOp",EDGE,"E6.27.2"),sQuery(id+"F0.wireOp",EDGE,"E6.27.3"),sQuery(id+"F0.wireOp",EDGE,"E6.27.4"),sQuery(id+"F0.wireOp",EDGE,"E6.28.1"),sQuery(id+"F0.wireOp",EDGE,"E6.28.2"),sQuery(id+"F0.wireOp",EDGE,"E6.28.3"),sQuery(id+"F0.wireOp",EDGE,"E6.28.4"),sQuery(id+"F0.wireOp",EDGE,"E6.29.1"),sQuery(id+"F0.wireOp",EDGE,"E6.29.2"),sQuery(id+"F0.wireOp",EDGE,"E6.29.3"),sQuery(id+"F0.wireOp",EDGE,"E6.29.4"),sQuery(id+"F0.wireOp",EDGE,"E6.30.1"),sQuery(id+"F0.wireOp",EDGE,"E6.30.2"),sQuery(id+"F0.wireOp",EDGE,"E6.30.3"),sQuery(id+"F0.wireOp",EDGE,"E6.30.4"),sQuery(id+"F0.wireOp",EDGE,"E6.31.1"),sQuery(id+"F0.wireOp",EDGE,"E6.31.2"),sQuery(id+"F0.wireOp",EDGE,"E6.31.3"),sQuery(id+"F0.wireOp",EDGE,"E6.31.4"),sQuery(id+"F0.wireOp",EDGE,"E6.32.1"),sQuery(id+"F0.wireOp",EDGE,"E6.32.2"),sQuery(id+"F0.wireOp",EDGE,"E6.32.3"),sQuery(id+"F0.wireOp",EDGE,"E6.32.4"),sQuery(id+"F0.wireOp",EDGE,"E6.33.1"),sQuery(id+"F0.wireOp",EDGE,"E6.33.2"),sQuery(id+"F0.wireOp",EDGE,"E6.33.3"),sQuery(id+"F0.wireOp",EDGE,"E6.33.4"),sQuery(id+"F0.wireOp",EDGE,"E6.34.1"),sQuery(id+"F0.wireOp",EDGE,"E6.34.2"),sQuery(id+"F0.wireOp",EDGE,"E6.34.3"),sQuery(id+"F0.wireOp",EDGE,"E6.34.4"),sQuery(id+"F0.wireOp",EDGE,"E6.35.1"),sQuery(id+"F0.wireOp",EDGE,"E6.35.2"),sQuery(id+"F0.wireOp",EDGE,"E6.35.3"),sQuery(id+"F0.wireOp",EDGE,"E6.35.4"),sQuery(id+"F0.wireOp",EDGE,"E6.36.1"),sQuery(id+"F0.wireOp",EDGE,"E6.36.2"),sQuery(id+"F0.wireOp",EDGE,"E6.36.3"),sQuery(id+"F0.wireOp",EDGE,"E6.36.4"),sQuery(id+"F0.wireOp",EDGE,"E6.37.1"),sQuery(id+"F0.wireOp",EDGE,"E6.37.2"),sQuery(id+"F0.wireOp",EDGE,"E6.37.3"),sQuery(id+"F0.wireOp",EDGE,"E6.37.4"),sQuery(id+"F0.wireOp",EDGE,"E6.38.1"),sQuery(id+"F0.wireOp",EDGE,"E6.38.2"),sQuery(id+"F0.wireOp",EDGE,"E6.38.3"),sQuery(id+"F0.wireOp",EDGE,"E6.38.4"),sQuery(id+"F0.wireOp",EDGE,"E6.39.1"),sQuery(id+"F0.wireOp",EDGE,"E6.39.2"),sQuery(id+"F0.wireOp",EDGE,"E6.39.3"),sQuery(id+"F0.wireOp",EDGE,"E6.39.4"),sQuery(id+"F0.wireOp",EDGE,"E6.40.1"),sQuery(id+"F0.wireOp",EDGE,"E6.40.2"),sQuery(id+"F0.wireOp",EDGE,"E6.40.3"),sQuery(id+"F0.wireOp",EDGE,"E6.40.4"),sQuery(id+"F0.wireOp",EDGE,"E6.41.1"),sQuery(id+"F0.wireOp",EDGE,"E6.41.2"),sQuery(id+"F0.wireOp",EDGE,"E6.41.3"),sQuery(id+"F0.wireOp",EDGE,"E6.41.4"),subQ1,sQuery(id+"F0.wireOp",EDGE,"E6.42.2"),subQ0,sQuery(id+"F0.wireOp",EDGE,"E6.42.4"),sQuery(id+"F0.wireOp",EDGE,"E6.43.1"),sQuery(id+"F0.wireOp",EDGE,"E6.43.2"),sQuery(id+"F0.wireOp",EDGE,"E6.43.3"),sQuery(id+"F0.wireOp",EDGE,"E6.43.4"),sQuery(id+"F0.wireOp",EDGE,"E7"),sQuery(id+"F0.wireOp",EDGE,"E8.1.0"),sQuery(id+"F0.wireOp",EDGE,"E8.2.0"),sQuery(id+"F0.wireOp",EDGE,"E8.3.0"),sQuery(id+"F0.wireOp",EDGE,"E8.4.0"),sQuery(id+"F0.wireOp",EDGE,"E8.5.0"),sQuery(id+"F0.wireOp",EDGE,"E8.6.0"),sQuery(id+"F0.wireOp",EDGE,"E8.7.0"),sQuery(id+"F0.wireOp",EDGE,"E8.8.0"),sQuery(id+"F0.wireOp",EDGE,"E8.9.0"),sQuery(id+"F0.wireOp",EDGE,"E8.10.0"),sQuery(id+"F0.wireOp",EDGE,"E8.11.0"),sQuery(id+"F0.wireOp",EDGE,"E8.12.0"),sQuery(id+"F0.wireOp",EDGE,"E8.13.0"),sQuery(id+"F0.wireOp",EDGE,"E8.14.0"),sQuery(id+"F0.wireOp",EDGE,"E8.15.0"),sQuery(id+"F0.wireOp",EDGE,"E8.16.0"),sQuery(id+"F0.wireOp",EDGE,"E8.17.0"),sQuery(id+"F0.wireOp",EDGE,"E8.18.0"),sQuery(id+"F0.wireOp",EDGE,"E8.19.0"),sQuery(id+"F0.wireOp",EDGE,"E8.20.0"),sQuery(id+"F0.wireOp",EDGE,"E8.21.0"),sQuery(id+"F0.wireOp",EDGE,"E8.22.0"),sQuery(id+"F0.wireOp",EDGE,"E8.23.0"),sQuery(id+"F0.wireOp",EDGE,"E8.24.0"),sQuery(id+"F0.wireOp",EDGE,"E8.25.0"),sQuery(id+"F0.wireOp",EDGE,"E8.26.0"),sQuery(id+"F0.wireOp",EDGE,"E8.27.0"),sQuery(id+"F0.wireOp",EDGE,"E8.28.0"),sQuery(id+"F0.wireOp",EDGE,"E8.29.0"),sQuery(id+"F0.wireOp",EDGE,"E8.30.0"),sQuery(id+"F0.wireOp",EDGE,"E8.31.0"),sQuery(id+"F0.wireOp",EDGE,"E8.32.0"),sQuery(id+"F0.wireOp",EDGE,"E8.33.0"),sQuery(id+"F0.wireOp",EDGE,"E8.34.0"),sQuery(id+"F0.wireOp",EDGE,"E8.35.0"),sQuery(id+"F0.wireOp",EDGE,"E8.36.0"),sQuery(id+"F0.wireOp",EDGE,"E8.37.0"),sQuery(id+"F0.wireOp",EDGE,"E8.38.0"),sQuery(id+"F0.wireOp",EDGE,"E8.39.0"),sQuery(id+"F0.wireOp",EDGE,"E8.40.0"),sQuery(id+"F0.wireOp",EDGE,"E8.41.0"),sQuery(id+"F0.wireOp",EDGE,"E8.42.0"),sQuery(id+"F0.wireOp",EDGE,"E8.43.0")])],"isStart":true})],"blendedInto":[makeQuery(id+"F1.opExtrude","CAP_FACE",FACE,{"disambiguationData":[OSD([sQuery(id+"F0.wireOp",EDGE,"E0"),sQuery(id+"F0.wireOp",EDGE,"E1"),sQuery(id+"F0.wireOp",EDGE,"E2"),sQuery(id+"F0.wireOp",EDGE,"E4"),sQuery(id+"F0.wireOp",EDGE,"E5"),sQuery(id+"F0.wireOp",EDGE,"E6.1.1"),sQuery(id+"F0.wireOp",EDGE,"E6.1.2"),sQuery(id+"F0.wireOp",EDGE,"E6.1.3"),sQuery(id+"F0.wireOp",EDGE,"E6.1.4"),sQuery(id+"F0.wireOp",EDGE,"E6.2.1"),sQuery(id+"F0.wireOp",EDGE,"E6.2.2"),sQuery(id+"F0.wireOp",EDGE,"E6.2.3"),sQuery(id+"F0.wireOp",EDGE,"E6.2.4"),sQuery(id+"F0.wireOp",EDGE,"E6.3.1"),sQuery(id+"F0.wireOp",EDGE,"E6.3.2"),sQuery(id+"F0.wireOp",EDGE,"E6.3.3"),sQuery(id+"F0.wireOp",EDGE,"E6.3.4"),sQuery(id+"F0.wireOp",EDGE,"E6.4.1"),sQuery(id+"F0.wireOp",EDGE,"E6.4.2"),sQuery(id+"F0.wireOp",EDGE,"E6.4.3"),sQuery(id+"F0.wireOp",EDGE,"E6.4.4"),sQuery(id+"F0.wireOp",EDGE,"E6.5.1"),sQuery(id+"F0.wireOp",EDGE,"E6.5.2"),sQuery(id+"F0.wireOp",EDGE,"E6.5.3"),sQuery(id+"F0.wireOp",EDGE,"E6.5.4"),sQuery(id+"F0.wireOp",EDGE,"E6.6.1"),sQuery(id+"F0.wireOp",EDGE,"E6.6.2"),sQuery(id+"F0.wireOp",EDGE,"E6.6.3"),sQuery(id+"F0.wireOp",EDGE,"E6.6.4"),sQuery(id+"F0.wireOp",EDGE,"E6.7.1"),sQuery(id+"F0.wireOp",EDGE,"E6.7.2"),sQuery(id+"F0.wireOp",EDGE,"E6.7.3"),sQuery(id+"F0.wireOp",EDGE,"E6.7.4"),sQuery(id+"F0.wireOp",EDGE,"E6.8.1"),sQuery(id+"F0.wireOp",EDGE,"E6.8.2"),sQuery(id+"F0.wireOp",EDGE,"E6.8.3"),sQuery(id+"F0.wireOp",EDGE,"E6.8.4"),sQuery(id+"F0.wireOp",EDGE,"E6.9.1"),sQuery(id+"F0.wireOp",EDGE,"E6.9.2"),sQuery(id+"F0.wireOp",EDGE,"E6.9.3"),sQuery(id+"F0.wireOp",EDGE,"E6.9.4"),sQuery(id+"F0.wireOp",EDGE,"E6.10.1"),sQuery(id+"F0.wireOp",EDGE,"E6.10.2"),sQuery(id+"F0.wireOp",EDGE,"E6.10.3"),sQuery(id+"F0.wireOp",EDGE,"E6.10.4"),sQuery(id+"F0.wireOp",EDGE,"E6.11.1"),sQuery(id+"F0.wireOp",EDGE,"E6.11.2"),sQuery(id+"F0.wireOp",EDGE,"E6.11.3"),sQuery(id+"F0.wireOp",EDGE,"E6.11.4"),sQuery(id+"F0.wireOp",EDGE,"E6.12.1"),sQuery(id+"F0.wireOp",EDGE,"E6.12.2"),sQuery(id+"F0.wireOp",EDGE,"E6.12.3"),sQuery(id+"F0.wireOp",EDGE,"E6.12.4"),sQuery(id+"F0.wireOp",EDGE,"E6.13.1"),sQuery(id+"F0.wireOp",EDGE,"E6.13.2"),sQuery(id+"F0.wireOp",EDGE,"E6.13.3"),sQuery(id+"F0.wireOp",EDGE,"E6.13.4"),sQuery(id+"F0.wireOp",EDGE,"E6.14.1"),sQuery(id+"F0.wireOp",EDGE,"E6.14.2"),sQuery(id+"F0.wireOp",EDGE,"E6.14.3"),sQuery(id+"F0.wireOp",EDGE,"E6.14.4"),sQuery(id+"F0.wireOp",EDGE,"E6.15.1"),sQuery(id+"F0.wireOp",EDGE,"E6.15.2"),sQuery(id+"F0.wireOp",EDGE,"E6.15.3"),sQuery(id+"F0.wireOp",EDGE,"E6.15.4"),sQuery(id+"F0.wireOp",EDGE,"E6.16.1"),sQuery(id+"F0.wireOp",EDGE,"E6.16.2"),sQuery(id+"F0.wireOp",EDGE,"E6.16.3"),sQuery(id+"F0.wireOp",EDGE,"E6.16.4"),sQuery(id+"F0.wireOp",EDGE,"E6.17.1"),sQuery(id+"F0.wireOp",EDGE,"E6.17.2"),sQuery(id+"F0.wireOp",EDGE,"E6.17.3"),sQuery(id+"F0.wireOp",EDGE,"E6.17.4"),sQuery(id+"F0.wireOp",EDGE,"E6.18.1"),sQuery(id+"F0.wireOp",EDGE,"E6.18.2"),sQuery(id+"F0.wireOp",EDGE,"E6.18.3"),sQuery(id+"F0.wireOp",EDGE,"E6.18.4"),sQuery(id+"F0.wireOp",EDGE,"E6.19.1"),sQuery(id+"F0.wireOp",EDGE,"E6.19.2"),sQuery(id+"F0.wireOp",EDGE,"E6.19.3"),sQuery(id+"F0.wireOp",EDGE,"E6.19.4"),sQuery(id+"F0.wireOp",EDGE,"E6.20.1"),sQuery(id+"F0.wireOp",EDGE,"E6.20.2"),sQuery(id+"F0.wireOp",EDGE,"E6.20.3"),sQuery(id+"F0.wireOp",EDGE,"E6.20.4"),sQuery(id+"F0.wireOp",EDGE,"E6.21.1"),sQuery(id+"F0.wireOp",EDGE,"E6.21.2"),sQuery(id+"F0.wireOp",EDGE,"E6.21.3"),sQuery(id+"F0.wireOp",EDGE,"E6.21.4"),sQuery(id+"F0.wireOp",EDGE,"E6.22.1"),sQuery(id+"F0.wireOp",EDGE,"E6.22.2"),sQuery(id+"F0.wireOp",EDGE,"E6.22.3"),sQuery(id+"F0.wireOp",EDGE,"E6.22.4"),sQuery(id+"F0.wireOp",EDGE,"E6.23.1"),sQuery(id+"F0.wireOp",EDGE,"E6.23.2"),sQuery(id+"F0.wireOp",EDGE,"E6.23.3"),sQuery(id+"F0.wireOp",EDGE,"E6.23.4"),sQuery(id+"F0.wireOp",EDGE,"E6.24.1"),sQuery(id+"F0.wireOp",EDGE,"E6.24.2"),sQuery(id+"F0.wireOp",EDGE,"E6.24.3"),sQuery(id+"F0.wireOp",EDGE,"E6.24.4"),sQuery(id+"F0.wireOp",EDGE,"E6.25.1"),sQuery(id+"F0.wireOp",EDGE,"E6.25.2"),sQuery(id+"F0.wireOp",EDGE,"E6.25.3"),sQuery(id+"F0.wireOp",EDGE,"E6.25.4"),sQuery(id+"F0.wireOp",EDGE,"E6.26.1"),sQuery(id+"F0.wireOp",EDGE,"E6.26.2"),sQuery(id+"F0.wireOp",EDGE,"E6.26.3"),sQuery(id+"F0.wireOp",EDGE,"E6.26.4"),sQuery(id+"F0.wireOp",EDGE,"E6.27.1"),sQuery(id+"F0.wireOp",EDGE,"E6.27.2"),sQuery(id+"F0.wireOp",EDGE,"E6.27.3"),sQuery(id+"F0.wireOp",EDGE,"E6.27.4"),sQuery(id+"F0.wireOp",EDGE,"E6.28.1"),sQuery(id+"F0.wireOp",EDGE,"E6.28.2"),sQuery(id+"F0.wireOp",EDGE,"E6.28.3"),sQuery(id+"F0.wireOp",EDGE,"E6.28.4"),sQuery(id+"F0.wireOp",EDGE,"E6.29.1"),sQuery(id+"F0.wireOp",EDGE,"E6.29.2"),sQuery(id+"F0.wireOp",EDGE,"E6.29.3"),sQuery(id+"F0.wireOp",EDGE,"E6.29.4"),sQuery(id+"F0.wireOp",EDGE,"E6.30.1"),sQuery(id+"F0.wireOp",EDGE,"E6.30.2"),sQuery(id+"F0.wireOp",EDGE,"E6.30.3"),sQuery(id+"F0.wireOp",EDGE,"E6.30.4"),sQuery(id+"F0.wireOp",EDGE,"E6.31.1"),sQuery(id+"F0.wireOp",EDGE,"E6.31.2"),sQuery(id+"F0.wireOp",EDGE,"E6.31.3"),sQuery(id+"F0.wireOp",EDGE,"E6.31.4"),sQuery(id+"F0.wireOp",EDGE,"E6.32.1"),sQuery(id+"F0.wireOp",EDGE,"E6.32.2"),sQuery(id+"F0.wireOp",EDGE,"E6.32.3"),sQuery(id+"F0.wireOp",EDGE,"E6.32.4"),sQuery(id+"F0.wireOp",EDGE,"E6.33.1"),sQuery(id+"F0.wireOp",EDGE,"E6.33.2"),sQuery(id+"F0.wireOp",EDGE,"E6.33.3"),sQuery(id+"F0.wireOp",EDGE,"E6.33.4"),sQuery(id+"F0.wireOp",EDGE,"E6.34.1"),sQuery(id+"F0.wireOp",EDGE,"E6.34.2"),sQuery(id+"F0.wireOp",EDGE,"E6.34.3"),sQuery(id+"F0.wireOp",EDGE,"E6.34.4"),sQuery(id+"F0.wireOp",EDGE,"E6.35.1"),sQuery(id+"F0.wireOp",EDGE,"E6.35.2"),sQuery(id+"F0.wireOp",EDGE,"E6.35.3"),sQuery(id+"F0.wireOp",EDGE,"E6.35.4"),sQuery(id+"F0.wireOp",EDGE,"E6.36.1"),sQuery(id+"F0.wireOp",EDGE,"E6.36.2"),sQuery(id+"F0.wireOp",EDGE,"E6.36.3"),sQuery(id+"F0.wireOp",EDGE,"E6.36.4"),sQuery(id+"F0.wireOp",EDGE,"E6.37.1"),sQuery(id+"F0.wireOp",EDGE,"E6.37.2"),sQuery(id+"F0.wireOp",EDGE,"E6.37.3"),sQuery(id+"F0.wireOp",EDGE,"E6.37.4"),sQuery(id+"F0.wireOp",EDGE,"E6.38.1"),sQuery(id+"F0.wireOp",EDGE,"E6.38.2"),sQuery(id+"F0.wireOp",EDGE,"E6.38.3"),sQuery(id+"F0.wireOp",EDGE,"E6.38.4"),sQuery(id+"F0.wireOp",EDGE,"E6.39.1"),sQuery(id+"F0.wireOp",EDGE,"E6.39.2"),sQuery(id+"F0.wireOp",EDGE,"E6.39.3"),sQuery(id+"F0.wireOp",EDGE,"E6.39.4"),sQuery(id+"F0.wireOp",EDGE,"E6.40.1"),sQuery(id+"F0.wireOp",EDGE,"E6.40.2"),sQuery(id+"F0.wireOp",EDGE,"E6.40.3"),sQuery(id+"F0.wireOp",EDGE,"E6.40.4"),sQuery(id+"F0.wireOp",EDGE,"E6.41.1"),sQuery(id+"F0.wireOp",EDGE,"E6.41.2"),sQuery(id+"F0.wireOp",EDGE,"E6.41.3"),sQuery(id+"F0.wireOp",EDGE,"E6.41.4"),subQ1,sQuery(id+"F0.wireOp",EDGE,"E6.42.2"),subQ0,sQuery(id+"F0.wireOp",EDGE,"E6.42.4"),sQuery(id+"F0.wireOp",EDGE,"E6.43.1"),sQuery(id+"F0.wireOp",EDGE,"E6.43.2"),sQuery(id+"F0.wireOp",EDGE,"E6.43.3"),sQuery(id+"F0.wireOp",EDGE,"E6.43.4"),sQuery(id+"F0.wireOp",EDGE,"E7"),sQuery(id+"F0.wireOp",EDGE,"E8.1.0"),sQuery(id+"F0.wireOp",EDGE,"E8.2.0"),sQuery(id+"F0.wireOp",EDGE,"E8.3.0"),sQuery(id+"F0.wireOp",EDGE,"E8.4.0"),sQuery(id+"F0.wireOp",EDGE,"E8.5.0"),sQuery(id+"F0.wireOp",EDGE,"E8.6.0"),sQuery(id+"F0.wireOp",EDGE,"E8.7.0"),sQuery(id+"F0.wireOp",EDGE,"E8.8.0"),sQuery(id+"F0.wireOp",EDGE,"E8.9.0"),sQuery(id+"F0.wireOp",EDGE,"E8.10.0"),sQuery(id+"F0.wireOp",EDGE,"E8.11.0"),sQuery(id+"F0.wireOp",EDGE,"E8.12.0"),sQuery(id+"F0.wireOp",EDGE,"E8.13.0"),sQuery(id+"F0.wireOp",EDGE,"E8.14.0"),sQuery(id+"F0.wireOp",EDGE,"E8.15.0"),sQuery(id+"F0.wireOp",EDGE,"E8.16.0"),sQuery(id+"F0.wireOp",EDGE,"E8.17.0"),sQuery(id+"F0.wireOp",EDGE,"E8.18.0"),sQuery(id+"F0.wireOp",EDGE,"E8.19.0"),sQuery(id+"F0.wireOp",EDGE,"E8.20.0"),sQuery(id+"F0.wireOp",EDGE,"E8.21.0"),sQuery(id+"F0.wireOp",EDGE,"E8.22.0"),sQuery(id+"F0.wireOp",EDGE,"E8.23.0"),sQuery(id+"F0.wireOp",EDGE,"E8.24.0"),sQuery(id+"F0.wireOp",EDGE,"E8.25.0"),sQuery(id+"F0.wireOp",EDGE,"E8.26.0"),sQuery(id+"F0.wireOp",EDGE,"E8.27.0"),sQuery(id+"F0.wireOp",EDGE,"E8.28.0"),sQuery(id+"F0.wireOp",EDGE,"E8.29.0"),sQuery(id+"F0.wireOp",EDGE,"E8.30.0"),sQuery(id+"F0.wireOp",EDGE,"E8.31.0"),sQuery(id+"F0.wireOp",EDGE,"E8.32.0"),sQuery(id+"F0.wireOp",EDGE,"E8.33.0"),sQuery(id+"F0.wireOp",EDGE,"E8.34.0"),sQuery(id+"F0.wireOp",EDGE,"E8.35.0"),sQuery(id+"F0.wireOp",EDGE,"E8.36.0"),sQuery(id+"F0.wireOp",EDGE,"E8.37.0"),sQuery(id+"F0.wireOp",EDGE,"E8.38.0"),sQuery(id+"F0.wireOp",EDGE,"E8.39.0"),sQuery(id+"F0.wireOp",EDGE,"E8.40.0"),sQuery(id+"F0.wireOp",EDGE,"E8.41.0"),sQuery(id+"F0.wireOp",EDGE,"E8.42.0"),sQuery(id+"F0.wireOp",EDGE,"E8.43.0")])],"isStart":true})]});}
            chamfer(context, id + "F3", {"entities" : qUnion([Q0, Q1, Q2, Q3, Q4, Q5, Q6, Q7, Q8, Q9, Q10, Q11, Q12, Q13, Q14, Q15, Q16, Q17, Q18, Q19, Q20, Q21, Q22, Q23, Q24, Q25, Q26, Q27, Q28, Q29, Q30, Q31, Q32, Q33, Q34, Q35, Q36, Q37, Q38, Q39, Q40, Q41, Q42]), "width" : 3.5 * mm, "tangentPropagation" : true});
        }
        {
            var Q0;
            Q0=makeQuery(id+"F1.opExtrude","CAP_FACE",FACE,{"disambiguationData":[OSD([sQuery(id+"F0.wireOp",EDGE,"E0"),sQuery(id+"F0.wireOp",EDGE,"E1"),sQuery(id+"F0.wireOp",EDGE,"E2"),sQuery(id+"F0.wireOp",EDGE,"E4"),sQuery(id+"F0.wireOp",EDGE,"E5"),sQuery(id+"F0.wireOp",EDGE,"E6.1.1"),sQuery(id+"F0.wireOp",EDGE,"E6.1.2"),sQuery(id+"F0.wireOp",EDGE,"E6.1.3"),sQuery(id+"F0.wireOp",EDGE,"E6.1.4"),sQuery(id+"F0.wireOp",EDGE,"E6.2.1"),sQuery(id+"F0.wireOp",EDGE,"E6.2.2"),sQuery(id+"F0.wireOp",EDGE,"E6.2.3"),sQuery(id+"F0.wireOp",EDGE,"E6.2.4"),sQuery(id+"F0.wireOp",EDGE,"E6.3.1"),sQuery(id+"F0.wireOp",EDGE,"E6.3.2"),sQuery(id+"F0.wireOp",EDGE,"E6.3.3"),sQuery(id+"F0.wireOp",EDGE,"E6.3.4"),sQuery(id+"F0.wireOp",EDGE,"E6.4.1"),sQuery(id+"F0.wireOp",EDGE,"E6.4.2"),sQuery(id+"F0.wireOp",EDGE,"E6.4.3"),sQuery(id+"F0.wireOp",EDGE,"E6.4.4"),sQuery(id+"F0.wireOp",EDGE,"E6.5.1"),sQuery(id+"F0.wireOp",EDGE,"E6.5.2"),sQuery(id+"F0.wireOp",EDGE,"E6.5.3"),sQuery(id+"F0.wireOp",EDGE,"E6.5.4"),sQuery(id+"F0.wireOp",EDGE,"E6.6.1"),sQuery(id+"F0.wireOp",EDGE,"E6.6.2"),sQuery(id+"F0.wireOp",EDGE,"E6.6.3"),sQuery(id+"F0.wireOp",EDGE,"E6.6.4"),sQuery(id+"F0.wireOp",EDGE,"E6.7.1"),sQuery(id+"F0.wireOp",EDGE,"E6.7.2"),sQuery(id+"F0.wireOp",EDGE,"E6.7.3"),sQuery(id+"F0.wireOp",EDGE,"E6.7.4"),sQuery(id+"F0.wireOp",EDGE,"E6.8.1"),sQuery(id+"F0.wireOp",EDGE,"E6.8.2"),sQuery(id+"F0.wireOp",EDGE,"E6.8.3"),sQuery(id+"F0.wireOp",EDGE,"E6.8.4"),sQuery(id+"F0.wireOp",EDGE,"E6.9.1"),sQuery(id+"F0.wireOp",EDGE,"E6.9.2"),sQuery(id+"F0.wireOp",EDGE,"E6.9.3"),sQuery(id+"F0.wireOp",EDGE,"E6.9.4"),sQuery(id+"F0.wireOp",EDGE,"E6.10.1"),sQuery(id+"F0.wireOp",EDGE,"E6.10.2"),sQuery(id+"F0.wireOp",EDGE,"E6.10.3"),sQuery(id+"F0.wireOp",EDGE,"E6.10.4"),sQuery(id+"F0.wireOp",EDGE,"E6.11.1"),sQuery(id+"F0.wireOp",EDGE,"E6.11.2"),sQuery(id+"F0.wireOp",EDGE,"E6.11.3"),sQuery(id+"F0.wireOp",EDGE,"E6.11.4"),sQuery(id+"F0.wireOp",EDGE,"E6.12.1"),sQuery(id+"F0.wireOp",EDGE,"E6.12.2"),sQuery(id+"F0.wireOp",EDGE,"E6.12.3"),sQuery(id+"F0.wireOp",EDGE,"E6.12.4"),sQuery(id+"F0.wireOp",EDGE,"E6.13.1"),sQuery(id+"F0.wireOp",EDGE,"E6.13.2"),sQuery(id+"F0.wireOp",EDGE,"E6.13.3"),sQuery(id+"F0.wireOp",EDGE,"E6.13.4"),sQuery(id+"F0.wireOp",EDGE,"E6.14.1"),sQuery(id+"F0.wireOp",EDGE,"E6.14.2"),sQuery(id+"F0.wireOp",EDGE,"E6.14.3"),sQuery(id+"F0.wireOp",EDGE,"E6.14.4"),sQuery(id+"F0.wireOp",EDGE,"E6.15.1"),sQuery(id+"F0.wireOp",EDGE,"E6.15.2"),sQuery(id+"F0.wireOp",EDGE,"E6.15.3"),sQuery(id+"F0.wireOp",EDGE,"E6.15.4"),sQuery(id+"F0.wireOp",EDGE,"E6.16.1"),sQuery(id+"F0.wireOp",EDGE,"E6.16.2"),sQuery(id+"F0.wireOp",EDGE,"E6.16.3"),sQuery(id+"F0.wireOp",EDGE,"E6.16.4"),sQuery(id+"F0.wireOp",EDGE,"E6.17.1"),sQuery(id+"F0.wireOp",EDGE,"E6.17.2"),sQuery(id+"F0.wireOp",EDGE,"E6.17.3"),sQuery(id+"F0.wireOp",EDGE,"E6.17.4"),sQuery(id+"F0.wireOp",EDGE,"E6.18.1"),sQuery(id+"F0.wireOp",EDGE,"E6.18.2"),sQuery(id+"F0.wireOp",EDGE,"E6.18.3"),sQuery(id+"F0.wireOp",EDGE,"E6.18.4"),sQuery(id+"F0.wireOp",EDGE,"E6.19.1"),sQuery(id+"F0.wireOp",EDGE,"E6.19.2"),sQuery(id+"F0.wireOp",EDGE,"E6.19.3"),sQuery(id+"F0.wireOp",EDGE,"E6.19.4"),sQuery(id+"F0.wireOp",EDGE,"E6.20.1"),sQuery(id+"F0.wireOp",EDGE,"E6.20.2"),sQuery(id+"F0.wireOp",EDGE,"E6.20.3"),sQuery(id+"F0.wireOp",EDGE,"E6.20.4"),sQuery(id+"F0.wireOp",EDGE,"E6.21.1"),sQuery(id+"F0.wireOp",EDGE,"E6.21.2"),sQuery(id+"F0.wireOp",EDGE,"E6.21.3"),sQuery(id+"F0.wireOp",EDGE,"E6.21.4"),sQuery(id+"F0.wireOp",EDGE,"E6.22.1"),sQuery(id+"F0.wireOp",EDGE,"E6.22.2"),sQuery(id+"F0.wireOp",EDGE,"E6.22.3"),sQuery(id+"F0.wireOp",EDGE,"E6.22.4"),sQuery(id+"F0.wireOp",EDGE,"E6.23.1"),sQuery(id+"F0.wireOp",EDGE,"E6.23.2"),sQuery(id+"F0.wireOp",EDGE,"E6.23.3"),sQuery(id+"F0.wireOp",EDGE,"E6.23.4"),sQuery(id+"F0.wireOp",EDGE,"E6.24.1"),sQuery(id+"F0.wireOp",EDGE,"E6.24.2"),sQuery(id+"F0.wireOp",EDGE,"E6.24.3"),sQuery(id+"F0.wireOp",EDGE,"E6.24.4"),sQuery(id+"F0.wireOp",EDGE,"E6.25.1"),sQuery(id+"F0.wireOp",EDGE,"E6.25.2"),sQuery(id+"F0.wireOp",EDGE,"E6.25.3"),sQuery(id+"F0.wireOp",EDGE,"E6.25.4"),sQuery(id+"F0.wireOp",EDGE,"E6.26.1"),sQuery(id+"F0.wireOp",EDGE,"E6.26.2"),sQuery(id+"F0.wireOp",EDGE,"E6.26.3"),sQuery(id+"F0.wireOp",EDGE,"E6.26.4"),sQuery(id+"F0.wireOp",EDGE,"E6.27.1"),sQuery(id+"F0.wireOp",EDGE,"E6.27.2"),sQuery(id+"F0.wireOp",EDGE,"E6.27.3"),sQuery(id+"F0.wireOp",EDGE,"E6.27.4"),sQuery(id+"F0.wireOp",EDGE,"E6.28.1"),sQuery(id+"F0.wireOp",EDGE,"E6.28.2"),sQuery(id+"F0.wireOp",EDGE,"E6.28.3"),sQuery(id+"F0.wireOp",EDGE,"E6.28.4"),sQuery(id+"F0.wireOp",EDGE,"E6.29.1"),sQuery(id+"F0.wireOp",EDGE,"E6.29.2"),sQuery(id+"F0.wireOp",EDGE,"E6.29.3"),sQuery(id+"F0.wireOp",EDGE,"E6.29.4"),sQuery(id+"F0.wireOp",EDGE,"E6.30.1"),sQuery(id+"F0.wireOp",EDGE,"E6.30.2"),sQuery(id+"F0.wireOp",EDGE,"E6.30.3"),sQuery(id+"F0.wireOp",EDGE,"E6.30.4"),sQuery(id+"F0.wireOp",EDGE,"E6.31.1"),sQuery(id+"F0.wireOp",EDGE,"E6.31.2"),sQuery(id+"F0.wireOp",EDGE,"E6.31.3"),sQuery(id+"F0.wireOp",EDGE,"E6.31.4"),sQuery(id+"F0.wireOp",EDGE,"E6.32.1"),sQuery(id+"F0.wireOp",EDGE,"E6.32.2"),sQuery(id+"F0.wireOp",EDGE,"E6.32.3"),sQuery(id+"F0.wireOp",EDGE,"E6.32.4"),sQuery(id+"F0.wireOp",EDGE,"E6.33.1"),sQuery(id+"F0.wireOp",EDGE,"E6.33.2"),sQuery(id+"F0.wireOp",EDGE,"E6.33.3"),sQuery(id+"F0.wireOp",EDGE,"E6.33.4"),sQuery(id+"F0.wireOp",EDGE,"E6.34.1"),sQuery(id+"F0.wireOp",EDGE,"E6.34.2"),sQuery(id+"F0.wireOp",EDGE,"E6.34.3"),sQuery(id+"F0.wireOp",EDGE,"E6.34.4"),sQuery(id+"F0.wireOp",EDGE,"E6.35.1"),sQuery(id+"F0.wireOp",EDGE,"E6.35.2"),sQuery(id+"F0.wireOp",EDGE,"E6.35.3"),sQuery(id+"F0.wireOp",EDGE,"E6.35.4"),sQuery(id+"F0.wireOp",EDGE,"E6.36.1"),sQuery(id+"F0.wireOp",EDGE,"E6.36.2"),sQuery(id+"F0.wireOp",EDGE,"E6.36.3"),sQuery(id+"F0.wireOp",EDGE,"E6.36.4"),sQuery(id+"F0.wireOp",EDGE,"E6.37.1"),sQuery(id+"F0.wireOp",EDGE,"E6.37.2"),sQuery(id+"F0.wireOp",EDGE,"E6.37.3"),sQuery(id+"F0.wireOp",EDGE,"E6.37.4"),sQuery(id+"F0.wireOp",EDGE,"E6.38.1"),sQuery(id+"F0.wireOp",EDGE,"E6.38.2"),sQuery(id+"F0.wireOp",EDGE,"E6.38.3"),sQuery(id+"F0.wireOp",EDGE,"E6.38.4"),sQuery(id+"F0.wireOp",EDGE,"E6.39.1"),sQuery(id+"F0.wireOp",EDGE,"E6.39.2"),sQuery(id+"F0.wireOp",EDGE,"E6.39.3"),sQuery(id+"F0.wireOp",EDGE,"E6.39.4"),sQuery(id+"F0.wireOp",EDGE,"E6.40.1"),sQuery(id+"F0.wireOp",EDGE,"E6.40.2"),sQuery(id+"F0.wireOp",EDGE,"E6.40.3"),sQuery(id+"F0.wireOp",EDGE,"E6.40.4"),sQuery(id+"F0.wireOp",EDGE,"E6.41.1"),sQuery(id+"F0.wireOp",EDGE,"E6.41.2"),sQuery(id+"F0.wireOp",EDGE,"E6.41.3"),sQuery(id+"F0.wireOp",EDGE,"E6.41.4"),sQuery(id+"F0.wireOp",EDGE,"E6.42.1"),sQuery(id+"F0.wireOp",EDGE,"E6.42.2"),sQuery(id+"F0.wireOp",EDGE,"E6.42.3"),sQuery(id+"F0.wireOp",EDGE,"E6.42.4"),sQuery(id+"F0.wireOp",EDGE,"E6.43.1"),sQuery(id+"F0.wireOp",EDGE,"E6.43.2"),sQuery(id+"F0.wireOp",EDGE,"E6.43.3"),sQuery(id+"F0.wireOp",EDGE,"E6.43.4"),sQuery(id+"F0.wireOp",EDGE,"E7"),sQuery(id+"F0.wireOp",EDGE,"E8.1.0"),sQuery(id+"F0.wireOp",EDGE,"E8.2.0"),sQuery(id+"F0.wireOp",EDGE,"E8.3.0"),sQuery(id+"F0.wireOp",EDGE,"E8.4.0"),sQuery(id+"F0.wireOp",EDGE,"E8.5.0"),sQuery(id+"F0.wireOp",EDGE,"E8.6.0"),sQuery(id+"F0.wireOp",EDGE,"E8.7.0"),sQuery(id+"F0.wireOp",EDGE,"E8.8.0"),sQuery(id+"F0.wireOp",EDGE,"E8.9.0"),sQuery(id+"F0.wireOp",EDGE,"E8.10.0"),sQuery(id+"F0.wireOp",EDGE,"E8.11.0"),sQuery(id+"F0.wireOp",EDGE,"E8.12.0"),sQuery(id+"F0.wireOp",EDGE,"E8.13.0"),sQuery(id+"F0.wireOp",EDGE,"E8.14.0"),sQuery(id+"F0.wireOp",EDGE,"E8.15.0"),sQuery(id+"F0.wireOp",EDGE,"E8.16.0"),sQuery(id+"F0.wireOp",EDGE,"E8.17.0"),sQuery(id+"F0.wireOp",EDGE,"E8.18.0"),sQuery(id+"F0.wireOp",EDGE,"E8.19.0"),sQuery(id+"F0.wireOp",EDGE,"E8.20.0"),sQuery(id+"F0.wireOp",EDGE,"E8.21.0"),sQuery(id+"F0.wireOp",EDGE,"E8.22.0"),sQuery(id+"F0.wireOp",EDGE,"E8.23.0"),sQuery(id+"F0.wireOp",EDGE,"E8.24.0"),sQuery(id+"F0.wireOp",EDGE,"E8.25.0"),sQuery(id+"F0.wireOp",EDGE,"E8.26.0"),sQuery(id+"F0.wireOp",EDGE,"E8.27.0"),sQuery(id+"F0.wireOp",EDGE,"E8.28.0"),sQuery(id+"F0.wireOp",EDGE,"E8.29.0"),sQuery(id+"F0.wireOp",EDGE,"E8.30.0"),sQuery(id+"F0.wireOp",EDGE,"E8.31.0"),sQuery(id+"F0.wireOp",EDGE,"E8.32.0"),sQuery(id+"F0.wireOp",EDGE,"E8.33.0"),sQuery(id+"F0.wireOp",EDGE,"E8.34.0"),sQuery(id+"F0.wireOp",EDGE,"E8.35.0"),sQuery(id+"F0.wireOp",EDGE,"E8.36.0"),sQuery(id+"F0.wireOp",EDGE,"E8.37.0"),sQuery(id+"F0.wireOp",EDGE,"E8.38.0"),sQuery(id+"F0.wireOp",EDGE,"E8.39.0"),sQuery(id+"F0.wireOp",EDGE,"E8.40.0"),sQuery(id+"F0.wireOp",EDGE,"E8.41.0"),sQuery(id+"F0.wireOp",EDGE,"E8.42.0"),sQuery(id+"F0.wireOp",EDGE,"E8.43.0")])],"isStart":false});
            var sketch = newSketch(context, id + "F4", { "sketchPlane" : qUnion([Q0])});
            skLineSegment(sketch, "E9.bottom", {"start": v(55.5, -0.75) * mm, "end": v(80.5, -0.75) * mm});
            skLineSegment(sketch, "E9.top", {"start": v(55.5, 0.75) * mm, "end": v(80.5, 0.75) * mm});
            skLineSegment(sketch, "E9.left", {"start": v(55.5, -0.75) * mm, "end": v(55.5, 0.75) * mm});
            skLineSegment(sketch, "E9.right", {"start": v(80.5, -0.75) * mm, "end": v(80.5, 0.75) * mm});
            skPoint(sketch, "E9.middle", {"position": v(68, 0) * mm});
            skLineSegment(sketch, "E10.bottom", {"start": v(-55.5, -0.75) * mm, "end": v(-80.5, -0.75) * mm});
            skLineSegment(sketch, "E10.top", {"start": v(-55.5, 0.75) * mm, "end": v(-80.5, 0.75) * mm});
            skLineSegment(sketch, "E10.left", {"start": v(-55.5, -0.75) * mm, "end": v(-55.5, 0.75) * mm});
            skLineSegment(sketch, "E10.right", {"start": v(-80.5, -0.75) * mm, "end": v(-80.5, 0.75) * mm});
            skPoint(sketch, "E10.middle", {"position": v(-68, 0) * mm});
            skLineSegment(sketch, "E11.bottom", {"start": v(0.75, -80.5) * mm, "end": v(-0.75, -80.5) * mm});
            skLineSegment(sketch, "E11.top", {"start": v(0.75, -55.5) * mm, "end": v(-0.75, -55.5) * mm});
            skLineSegment(sketch, "E11.left", {"start": v(0.75, -80.5) * mm, "end": v(0.75, -55.5) * mm});
            skLineSegment(sketch, "E11.right", {"start": v(-0.75, -80.5) * mm, "end": v(-0.75, -55.5) * mm});
            skPoint(sketch, "E11.middle", {"position": v(0, -68) * mm});
            skArc(sketch, "E12", {"start": v(-55.5, -0.75) * mm, "mid": v(-54.75, 0) * mm, "end": v(-55.5, 0.75) * mm});
            skArc(sketch, "E13", {"start": v(55.5, 0.75) * mm, "mid": v(54.75, 0) * mm, "end": v(55.5, -0.75) * mm});
            skArc(sketch, "E14", {"start": v(0.75, -55.5) * mm, "mid": v(0, -54.75) * mm, "end": v(-0.75, -55.5) * mm});
            skLineSegment(sketch, "E15.bottom", {"start": v(0.75, 55.5) * mm, "end": v(-0.75, 55.5) * mm});
            skLineSegment(sketch, "E15.top", {"start": v(0.75, 80.5) * mm, "end": v(-0.75, 80.5) * mm});
            skLineSegment(sketch, "E15.left", {"start": v(0.75, 55.5) * mm, "end": v(0.75, 80.5) * mm});
            skLineSegment(sketch, "E15.right", {"start": v(-0.75, 55.5) * mm, "end": v(-0.75, 80.5) * mm});
            skPoint(sketch, "E15.middle", {"position": v(0, 68) * mm});
            skArc(sketch, "E16", {"start": v(-0.75, 55.5) * mm, "mid": v(0, 54.75) * mm, "end": v(0.75, 55.5) * mm});
            skText(sketch, "E17", { "text": "3DW\n", "fontName": "OpenSans-Bold.ttf"});
            const initialGuessF4  = {"E17": [-0.037, 0.02626, 1, 0, 0.02274]};
            skSetInitialGuess(sketch, initialGuessF4);
            skSolve(sketch);
        }
        {
            var Q0;
            Q0 = qSketchRegion(id + "F4", true);
            extrude(context, id + "F5", {"entities" : qUnion([Q0]), "operationType" : NewBodyOperationType.REMOVE, "oppositeDirection" : true, "depth" : 25 * mm});
        }
        {
            var Q0;
            Q0 = qSketchRegion(id + "F4", true);
            extrude(context, id + "F6", {"entities" : qUnion([Q0]), "operationType" : NewBodyOperationType.REMOVE, "oppositeDirection" : true, "depth" : 25 * mm});
        }
        {
            var Q0;
            Q0 = qSketchRegion(id + "F4", true);
            extrude(context, id + "F7", {"entities" : qUnion([Q0]), "operationType" : NewBodyOperationType.REMOVE, "oppositeDirection" : true, "depth" : 25 * mm});
        }
    });
